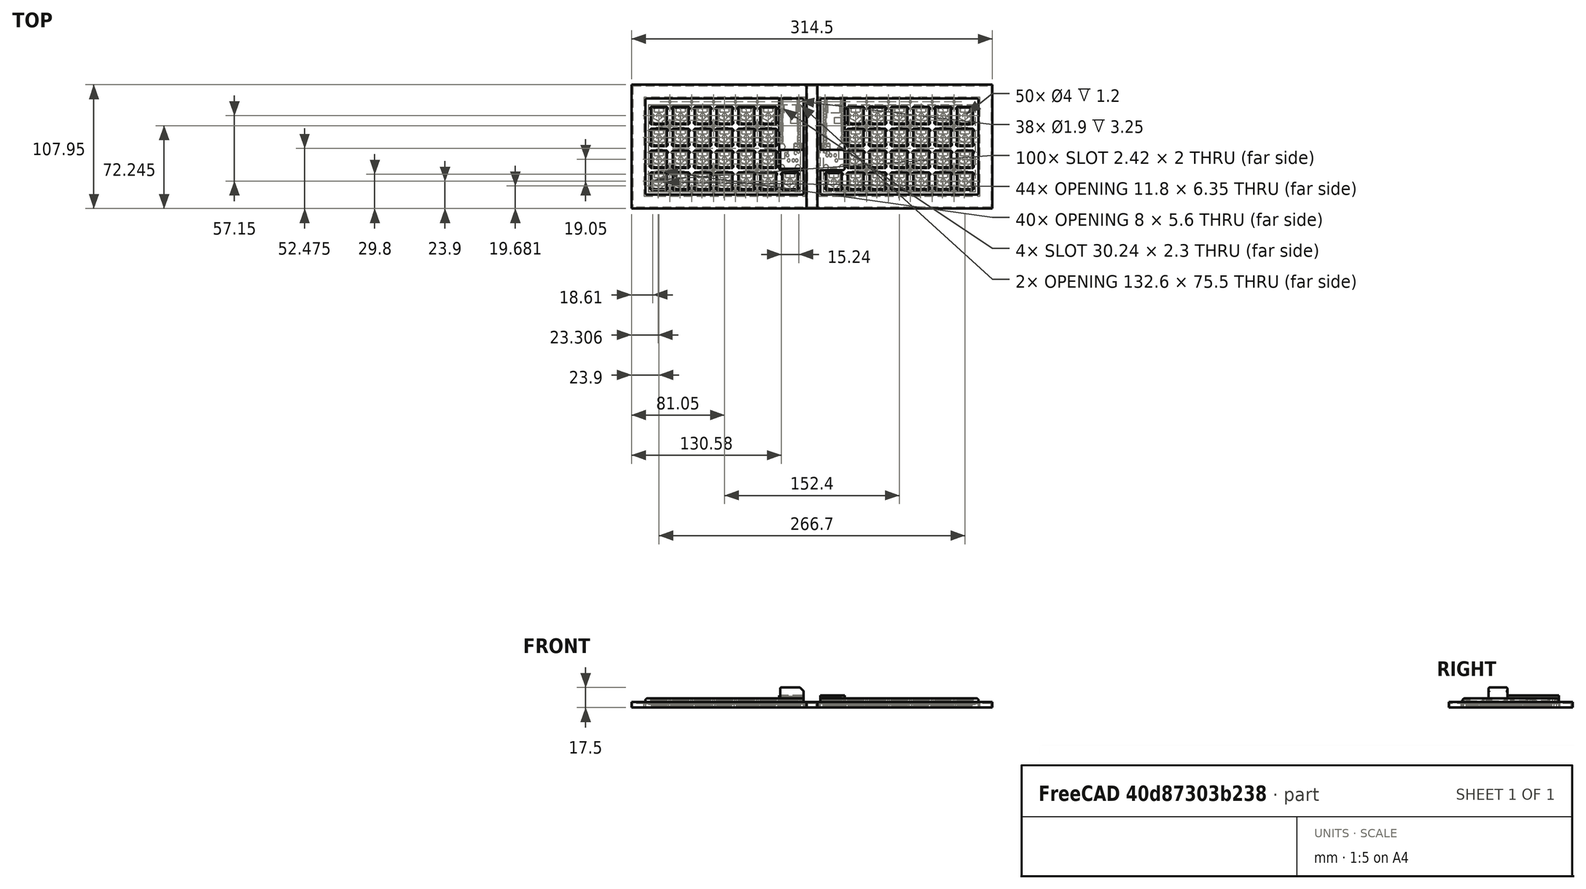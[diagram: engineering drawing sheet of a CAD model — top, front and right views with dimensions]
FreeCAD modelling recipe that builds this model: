
FCSTD DOCUMENT  (FreeCAD 1.0R39285 (Git))
Label: HelixCase
License: All rights reserved
LicenseURL: https://en.wikipedia.org/wiki/All_rights_reserved
objects: Sketcher::SketchObject×76, PartDesign::Pocket×59, PartDesign::Pad×17, PartDesign::Body×10, PartDesign::Fillet×7, Image::ImagePlane×5, PartDesign::ShapeBinder×2, PartDesign::Boolean×2, App::VarSet×1
note: 417 computed .brp shape members not serialized (recipe doc carries the construction recipe); baked Part::Feature solids carry a one-line shape summary decoded from their .brp

FEATURE [Sketcher::SketchObject] Sketch  label="TL-Lo"
  ArcFitTolerance = 1e-06
  AttachmentSupport = -> [XY_Plane]
  FullyConstrained = true
  MakeInternals = false
  MapMode = 5
  expr: Constraints[232] = VarSet.Top_LoXY
  expr: Constraints[233] = VarSet.Top_LoXY
  sketch-geometry (125):
    g0: LineSegment StartX=-45.4 StartY=11.75 StartZ=0 EndX=-30.8 EndY=11.75 EndZ=0
    g1: LineSegment StartX=-30.8 StartY=11.75 StartZ=0 EndX=-30.8 EndY=26.35 EndZ=0
    g2: LineSegment StartX=-30.8 StartY=26.35 StartZ=0 EndX=-45.4 EndY=26.35 EndZ=0
    g3: LineSegment StartX=-45.4 StartY=26.35 StartZ=0 EndX=-45.4 EndY=11.75 EndZ=0
    g4: GeomPoint [constr] X=-38.1 Y=19.05 Z=0
    g5: LineSegment StartX=-64.45 StartY=11.75 StartZ=0 EndX=-49.85 EndY=11.75 EndZ=0
    g6: LineSegment StartX=-49.85 StartY=11.75 StartZ=0 EndX=-49.85 EndY=26.35 EndZ=0
    g7: LineSegment StartX=-49.85 StartY=26.35 StartZ=0 EndX=-64.45 EndY=26.35 EndZ=0
    g8: LineSegment StartX=-64.45 StartY=26.35 StartZ=0 EndX=-64.45 EndY=11.75 EndZ=0
    g9: GeomPoint [constr] X=-57.15 Y=19.05 Z=0
    g10: LineSegment StartX=-83.5 StartY=11.75 StartZ=0 EndX=-68.9 EndY=11.75 EndZ=0
    g11: LineSegment StartX=-68.9 StartY=11.75 StartZ=0 EndX=-68.9 EndY=26.35 EndZ=0
    g12: LineSegment StartX=-68.9 StartY=26.35 StartZ=0 EndX=-83.5 EndY=26.35 EndZ=0
    g13: LineSegment StartX=-83.5 StartY=26.35 StartZ=0 EndX=-83.5 EndY=11.75 EndZ=0
    g14: GeomPoint [constr] X=-76.2 Y=19.05 Z=0
    g15: LineSegment StartX=-102.55 StartY=11.75 StartZ=0 EndX=-87.95 EndY=11.75 EndZ=0
    g16: LineSegment StartX=-87.95 StartY=11.75 StartZ=0 EndX=-87.95 EndY=26.35 EndZ=0
    g17: LineSegment StartX=-87.95 StartY=26.35 StartZ=0 EndX=-102.55 EndY=26.35 EndZ=0
    g18: LineSegment StartX=-102.55 StartY=26.35 StartZ=0 EndX=-102.55 EndY=11.75 EndZ=0
    g19: GeomPoint [constr] X=-95.25 Y=19.05 Z=0
    g20: LineSegment StartX=-121.6 StartY=11.75 StartZ=0 EndX=-107 EndY=11.75 EndZ=0
    g21: LineSegment StartX=-107 StartY=11.75 StartZ=0 EndX=-107 EndY=26.35 EndZ=0
    g22: LineSegment StartX=-107 StartY=26.35 StartZ=0 EndX=-121.6 EndY=26.35 EndZ=0
    g23: LineSegment StartX=-121.6 StartY=26.35 StartZ=0 EndX=-121.6 EndY=11.75 EndZ=0
    g24: GeomPoint [constr] X=-114.3 Y=19.05 Z=0
    g25: LineSegment StartX=-45.4 StartY=49.85 StartZ=0 EndX=-30.8 EndY=49.85 EndZ=0
    g26: LineSegment StartX=-30.8 StartY=49.85 StartZ=0 EndX=-30.8 EndY=64.45 EndZ=0
    g27: LineSegment StartX=-30.8 StartY=64.45 StartZ=0 EndX=-45.4 EndY=64.45 EndZ=0
    g28: LineSegment StartX=-45.4 StartY=64.45 StartZ=0 EndX=-45.4 EndY=49.85 EndZ=0
    g29: GeomPoint [constr] X=-38.1 Y=57.15 Z=0
    g30: LineSegment StartX=-64.45 StartY=49.85 StartZ=0 EndX=-49.85 EndY=49.85 EndZ=0
    g31: LineSegment StartX=-49.85 StartY=49.85 StartZ=0 EndX=-49.85 EndY=64.45 EndZ=0
    g32: LineSegment StartX=-49.85 StartY=64.45 StartZ=0 EndX=-64.45 EndY=64.45 EndZ=0
    g33: LineSegment StartX=-64.45 StartY=64.45 StartZ=0 EndX=-64.45 EndY=49.85 EndZ=0
    g34: GeomPoint [constr] X=-57.15 Y=57.15 Z=0
    g35: LineSegment StartX=-83.5 StartY=49.85 StartZ=0 EndX=-68.9 EndY=49.85 EndZ=0
    g36: LineSegment StartX=-68.9 StartY=49.85 StartZ=0 EndX=-68.9 EndY=64.45 EndZ=0
    g37: LineSegment StartX=-68.9 StartY=64.45 StartZ=0 EndX=-83.5 EndY=64.45 EndZ=0
    g38: LineSegment StartX=-83.5 StartY=64.45 StartZ=0 EndX=-83.5 EndY=49.85 EndZ=0
    g39: GeomPoint [constr] X=-76.2 Y=57.15 Z=0
    g40: LineSegment StartX=-102.55 StartY=49.85 StartZ=0 EndX=-87.95 EndY=49.85 EndZ=0
    g41: LineSegment StartX=-87.95 StartY=49.85 StartZ=0 EndX=-87.95 EndY=64.45 EndZ=0
    g42: LineSegment StartX=-87.95 StartY=64.45 StartZ=0 EndX=-102.55 EndY=64.45 EndZ=0
    g43: LineSegment StartX=-102.55 StartY=64.45 StartZ=0 EndX=-102.55 EndY=49.85 EndZ=0
    g44: GeomPoint [constr] X=-95.25 Y=57.15 Z=0
    g45: LineSegment StartX=-121.6 StartY=49.85 StartZ=0 EndX=-107 EndY=49.85 EndZ=0
    g46: LineSegment StartX=-107 StartY=49.85 StartZ=0 EndX=-107 EndY=64.45 EndZ=0
    g47: LineSegment StartX=-107 StartY=64.45 StartZ=0 EndX=-121.6 EndY=64.45 EndZ=0
    g48: LineSegment StartX=-121.6 StartY=64.45 StartZ=0 EndX=-121.6 EndY=49.85 EndZ=0
    g49: GeomPoint [constr] X=-114.3 Y=57.15 Z=0
    g50: LineSegment StartX=-45.4 StartY=30.8 StartZ=0 EndX=-30.8 EndY=30.8 EndZ=0
    g51: LineSegment StartX=-30.8 StartY=30.8 StartZ=0 EndX=-30.8 EndY=45.4 EndZ=0
    g52: LineSegment StartX=-30.8 StartY=45.4 StartZ=0 EndX=-45.4 EndY=45.4 EndZ=0
    g53: LineSegment StartX=-45.4 StartY=45.4 StartZ=0 EndX=-45.4 EndY=30.8 EndZ=0
    g54: GeomPoint [constr] X=-38.1 Y=38.1 Z=0
    g55: LineSegment StartX=-64.45 StartY=30.8 StartZ=0 EndX=-49.85 EndY=30.8 EndZ=0
    g56: LineSegment StartX=-49.85 StartY=30.8 StartZ=0 EndX=-49.85 EndY=45.4 EndZ=0
    g57: LineSegment StartX=-49.85 StartY=45.4 StartZ=0 EndX=-64.45 EndY=45.4 EndZ=0
    g58: LineSegment StartX=-64.45 StartY=45.4 StartZ=0 EndX=-64.45 EndY=30.8 EndZ=0
    g59: GeomPoint [constr] X=-57.15 Y=38.1 Z=0
    g60: LineSegment StartX=-83.5 StartY=30.8 StartZ=0 EndX=-68.9 EndY=30.8 EndZ=0
    g61: LineSegment StartX=-68.9 StartY=30.8 StartZ=0 EndX=-68.9 EndY=45.4 EndZ=0
    g62: LineSegment StartX=-68.9 StartY=45.4 StartZ=0 EndX=-83.5 EndY=45.4 EndZ=0
    g63: LineSegment StartX=-83.5 StartY=45.4 StartZ=0 EndX=-83.5 EndY=30.8 EndZ=0
    g64: GeomPoint [constr] X=-76.2 Y=38.1 Z=0
    g65: LineSegment StartX=-102.55 StartY=30.8 StartZ=0 EndX=-87.95 EndY=30.8 EndZ=0
    g66: LineSegment StartX=-87.95 StartY=30.8 StartZ=0 EndX=-87.95 EndY=45.4 EndZ=0
    g67: LineSegment StartX=-87.95 StartY=45.4 StartZ=0 EndX=-102.55 EndY=45.4 EndZ=0
    g68: LineSegment StartX=-102.55 StartY=45.4 StartZ=0 EndX=-102.55 EndY=30.8 EndZ=0
    g69: GeomPoint [constr] X=-95.25 Y=38.1 Z=0
    g70: LineSegment StartX=-121.6 StartY=30.8 StartZ=0 EndX=-107 EndY=30.8 EndZ=0
    g71: LineSegment StartX=-107 StartY=30.8 StartZ=0 EndX=-107 EndY=45.4 EndZ=0
    g72: LineSegment StartX=-107 StartY=45.4 StartZ=0 EndX=-121.6 EndY=45.4 EndZ=0
    g73: LineSegment StartX=-121.6 StartY=45.4 StartZ=0 EndX=-121.6 EndY=30.8 EndZ=0
    g74: GeomPoint [constr] X=-114.3 Y=38.1 Z=0
    g75: LineSegment StartX=-102.55 StartY=68.9 StartZ=0 EndX=-87.95 EndY=68.9 EndZ=0
    g76: LineSegment StartX=-87.95 StartY=68.9 StartZ=0 EndX=-87.95 EndY=83.5 EndZ=0
    g77: LineSegment StartX=-87.95 StartY=83.5 StartZ=0 EndX=-102.55 EndY=83.5 EndZ=0
    g78: LineSegment StartX=-102.55 StartY=83.5 StartZ=0 EndX=-102.55 EndY=68.9 EndZ=0
    g79: GeomPoint [constr] X=-95.25 Y=76.2 Z=0
    g80: LineSegment StartX=-64.45 StartY=68.9 StartZ=0 EndX=-49.85 EndY=68.9 EndZ=0
    g81: LineSegment StartX=-49.85 StartY=68.9 StartZ=0 EndX=-49.85 EndY=83.5 EndZ=0
    g82: LineSegment StartX=-49.85 StartY=83.5 StartZ=0 EndX=-64.45 EndY=83.5 EndZ=0
    g83: LineSegment StartX=-64.45 StartY=83.5 StartZ=0 EndX=-64.45 EndY=68.9 EndZ=0
    g84: GeomPoint [constr] X=-57.15 Y=76.2 Z=0
    g85: LineSegment StartX=-140.65 StartY=68.9 StartZ=0 EndX=-126.05 EndY=68.9 EndZ=0
    g86: LineSegment StartX=-126.05 StartY=68.9 StartZ=0 EndX=-126.05 EndY=83.5 EndZ=0
    g87: LineSegment StartX=-126.05 StartY=83.5 StartZ=0 EndX=-140.65 EndY=83.5 EndZ=0
    g88: LineSegment StartX=-140.65 StartY=83.5 StartZ=0 EndX=-140.65 EndY=68.9 EndZ=0
    g89: GeomPoint [constr] X=-133.35 Y=76.2 Z=0
    g90: LineSegment StartX=-121.6 StartY=68.9 StartZ=0 EndX=-107 EndY=68.9 EndZ=0
    g91: LineSegment StartX=-107 StartY=68.9 StartZ=0 EndX=-107 EndY=83.5 EndZ=0
    g92: LineSegment StartX=-107 StartY=83.5 StartZ=0 EndX=-121.6 EndY=83.5 EndZ=0
    g93: LineSegment StartX=-121.6 StartY=83.5 StartZ=0 EndX=-121.6 EndY=68.9 EndZ=0
    g94: GeomPoint [constr] X=-114.3 Y=76.2 Z=0
    g95: LineSegment StartX=-83.5 StartY=68.9 StartZ=0 EndX=-68.9 EndY=68.9 EndZ=0
    g96: LineSegment StartX=-68.9 StartY=68.9 StartZ=0 EndX=-68.9 EndY=83.5 EndZ=0
    g97: LineSegment StartX=-68.9 StartY=83.5 StartZ=0 EndX=-83.5 EndY=83.5 EndZ=0
    g98: LineSegment StartX=-83.5 StartY=83.5 StartZ=0 EndX=-83.5 EndY=68.9 EndZ=0
    g99: GeomPoint [constr] X=-76.2 Y=76.2 Z=0
    g100: LineSegment StartX=-30.8 StartY=83.5 StartZ=0 EndX=-45.4 EndY=83.5 EndZ=0
    g101: LineSegment StartX=-45.4 StartY=83.5 StartZ=0 EndX=-45.4 EndY=68.9 EndZ=0
    g102: LineSegment StartX=-45.4 StartY=68.9 StartZ=0 EndX=-30.8 EndY=68.9 EndZ=0
    g103: LineSegment StartX=-30.8 StartY=68.9 StartZ=0 EndX=-30.8 EndY=83.5 EndZ=0
    g104: GeomPoint [constr] X=-38.1 Y=76.2 Z=0
    g105: LineSegment StartX=-126.05 StartY=64.45 StartZ=0 EndX=-140.65 EndY=64.45 EndZ=0
    g106: LineSegment StartX=-140.65 StartY=64.45 StartZ=0 EndX=-140.65 EndY=49.85 EndZ=0
    g107: LineSegment StartX=-140.65 StartY=49.85 StartZ=0 EndX=-126.05 EndY=49.85 EndZ=0
    g108: LineSegment StartX=-126.05 StartY=49.85 StartZ=0 EndX=-126.05 EndY=64.45 EndZ=0
    g109: GeomPoint [constr] X=-133.35 Y=57.15 Z=0
    g110: LineSegment StartX=-126.05 StartY=45.4 StartZ=0 EndX=-140.65 EndY=45.4 EndZ=0
    g111: LineSegment StartX=-140.65 StartY=45.4 StartZ=0 EndX=-140.65 EndY=30.8 EndZ=0
    g112: LineSegment StartX=-140.65 StartY=30.8 StartZ=0 EndX=-126.05 EndY=30.8 EndZ=0
    g113: LineSegment StartX=-126.05 StartY=30.8 StartZ=0 EndX=-126.05 EndY=45.4 EndZ=0
    g114: GeomPoint [constr] X=-133.35 Y=38.1 Z=0
    g115: LineSegment StartX=-126.05 StartY=26.35 StartZ=0 EndX=-140.65 EndY=26.35 EndZ=0
    g116: LineSegment StartX=-140.65 StartY=26.35 StartZ=0 EndX=-140.65 EndY=11.75 EndZ=0
    g117: LineSegment StartX=-140.65 StartY=11.75 StartZ=0 EndX=-126.05 EndY=11.75 EndZ=0
    g118: LineSegment StartX=-126.05 StartY=11.75 StartZ=0 EndX=-126.05 EndY=26.35 EndZ=0
    g119: GeomPoint [constr] X=-133.35 Y=19.05 Z=0
    g120: LineSegment StartX=-11.75 StartY=26.35 StartZ=0 EndX=-26.35 EndY=26.35 EndZ=0
    g121: LineSegment StartX=-26.35 StartY=26.35 StartZ=0 EndX=-26.35 EndY=11.75 EndZ=0
    g122: LineSegment StartX=-26.35 StartY=11.75 StartZ=0 EndX=-11.75 EndY=11.75 EndZ=0
    g123: LineSegment StartX=-11.75 StartY=11.75 StartZ=0 EndX=-11.75 EndY=26.35 EndZ=0
    g124: GeomPoint [constr] X=-19.05 Y=19.05 Z=0
  constraints (325):
    c: Coincident(g0,g1)
    c: Coincident(g1,g2)
    c: Coincident(g2,g3)
    c: Coincident(g3,g0)
    c: Horizontal(g0)
    c: Horizontal(g2)
    c: Vertical(g1)
    c: Vertical(g3)
    c: Symmetric(g2,g0,g4)
    c: Coincident(g5,g6)
    c: Coincident(g6,g7)
    c: Coincident(g7,g8)
    c: Coincident(g8,g5)
    c: Horizontal(g5)
    c: Horizontal(g7)
    c: Vertical(g6)
    c: Vertical(g8)
    c: Symmetric(g7,g5,g9)
    c: DistanceX(g9,g4) = 19.05
    c: Coincident(g10,g11)
    c: Coincident(g11,g12)
    c: Coincident(g12,g13)
    c: Coincident(g13,g10)
    c: Horizontal(g10)
    c: Horizontal(g12)
    c: Vertical(g11)
    c: Vertical(g13)
    c: Symmetric(g12,g10,g14)
    c: DistanceX(g14,g9) = 19.05
    c: Coincident(g15,g16)
    c: Coincident(g16,g17)
    c: Coincident(g17,g18)
    c: Coincident(g18,g15)
    c: Horizontal(g15)
    c: Horizontal(g17)
    c: Vertical(g16)
    c: Vertical(g18)
    c: Symmetric(g17,g15,g19)
    c: Coincident(g20,g21)
    c: Coincident(g21,g22)
    c: Coincident(g22,g23)
    c: Coincident(g23,g20)
    c: Horizontal(g20)
    c: Horizontal(g22)
    c: Vertical(g21)
    c: Vertical(g23)
    c: Symmetric(g22,g20,g24)
    c: DistanceX(g19,g14) = 19.05
    c: DistanceX(g24,g19) = 19.05
    c: Coincident(g25,g26)
    c: Coincident(g26,g27)
    c: Coincident(g27,g28)
    c: Coincident(g28,g25)
    c: Horizontal(g25)
    c: Horizontal(g27)
    c: Vertical(g26)
    c: Vertical(g28)
    c: Symmetric(g27,g25,g29)
    c: Coincident(g30,g31)
    c: Coincident(g31,g32)
    c: Coincident(g32,g33)
    c: Coincident(g33,g30)
    c: Horizontal(g30)
    c: Horizontal(g32)
    c: Vertical(g31)
    c: Vertical(g33)
    c: Symmetric(g32,g30,g34)
    c: Coincident(g35,g36)
    c: Coincident(g36,g37)
    c: Coincident(g37,g38)
    c: Coincident(g38,g35)
    c: Horizontal(g35)
    c: Horizontal(g37)
    c: Vertical(g36)
    c: Vertical(g38)
    c: Symmetric(g37,g35,g39)
    c: Coincident(g40,g41)
    c: Coincident(g41,g42)
    c: Coincident(g42,g43)
    c: Coincident(g43,g40)
    c: Horizontal(g40)
    c: Horizontal(g42)
    c: Vertical(g41)
    c: Vertical(g43)
    c: Symmetric(g42,g40,g44)
    c: Coincident(g45,g46)
    c: Coincident(g46,g47)
    c: Coincident(g47,g48)
    c: Coincident(g48,g45)
    c: Horizontal(g45)
    c: Horizontal(g47)
    c: Vertical(g46)
    c: Vertical(g48)
    c: Symmetric(g47,g45,g49)
    c: Coincident(g50,g51)
    c: Coincident(g51,g52)
    c: Coincident(g52,g53)
    c: Coincident(g53,g50)
    c: Horizontal(g50)
    c: Horizontal(g52)
    c: Vertical(g51)
    c: Vertical(g53)
    c: Symmetric(g52,g50,g54)
    c: Coincident(g55,g56)
    c: Coincident(g56,g57)
    c: Coincident(g57,g58)
    c: Coincident(g58,g55)
    c: Horizontal(g55)
    c: Horizontal(g57)
    c: Vertical(g56)
    c: Vertical(g58)
    c: Symmetric(g57,g55,g59)
    c: Coincident(g60,g61)
    c: Coincident(g61,g62)
    c: Coincident(g62,g63)
    c: Coincident(g63,g60)
    c: Horizontal(g60)
    c: Horizontal(g62)
    c: Vertical(g61)
    c: Vertical(g63)
    c: Symmetric(g62,g60,g64)
    c: Coincident(g65,g66)
    c: Coincident(g66,g67)
    c: Coincident(g67,g68)
    c: Coincident(g68,g65)
    c: Horizontal(g65)
    c: Horizontal(g67)
    c: Vertical(g66)
    c: Vertical(g68)
    c: Symmetric(g67,g65,g69)
    c: Coincident(g70,g71)
    c: Coincident(g71,g72)
    c: Coincident(g72,g73)
    c: Coincident(g73,g70)
    c: Horizontal(g70)
    c: Horizontal(g72)
    c: Vertical(g71)
    c: Vertical(g73)
    c: Symmetric(g72,g70,g74)
    c: DistanceY(g54,g29) = 19.05
    c: Coincident(g75,g76)
    c: Coincident(g76,g77)
    c: Coincident(g77,g78)
    c: Coincident(g78,g75)
    c: Horizontal(g75)
    c: Horizontal(g77)
    c: Vertical(g76)
    c: Vertical(g78)
    c: Symmetric(g77,g75,g79)
    c: Coincident(g80,g81)
    c: Coincident(g81,g82)
    c: Coincident(g82,g83)
    c: Coincident(g83,g80)
    c: Horizontal(g80)
    c: Horizontal(g82)
    c: Vertical(g81)
    c: Vertical(g83)
    c: Symmetric(g82,g80,g84)
    c: Coincident(g85,g86)
    c: Coincident(g86,g87)
    c: Coincident(g87,g88)
    c: Coincident(g88,g85)
    c: Horizontal(g85)
    c: Horizontal(g87)
    c: Vertical(g86)
    c: Vertical(g88)
    c: Symmetric(g87,g85,g89)
    c: Coincident(g90,g91)
    c: Coincident(g91,g92)
    c: Coincident(g92,g93)
    c: Coincident(g93,g90)
    c: Horizontal(g90)
    c: Horizontal(g92)
    c: Vertical(g91)
    c: Vertical(g93)
    c: Symmetric(g92,g90,g94)
    c: Coincident(g95,g96)
    c: Coincident(g96,g97)
    c: Coincident(g97,g98)
    c: Coincident(g98,g95)
    c: Horizontal(g95)
    c: Horizontal(g97)
    c: Vertical(g96)
    c: Vertical(g98)
    c: Symmetric(g97,g95,g99)
    c: Coincident(g100,g101)
    c: Coincident(g101,g102)
    c: Coincident(g102,g103)
    c: Coincident(g103,g100)
    c: Horizontal(g100)
    c: Horizontal(g102)
    c: Vertical(g101)
    c: Vertical(g103)
    c: Symmetric(g102,g100,g104)
    c: Coincident(g105,g106)
    c: Coincident(g106,g107)
    c: Coincident(g107,g108)
    c: Coincident(g108,g105)
    c: Horizontal(g105)
    c: Horizontal(g107)
    c: Vertical(g106)
    c: Vertical(g108)
    c: Symmetric(g107,g105,g109)
    c: Coincident(g110,g111)
    c: Coincident(g111,g112)
    c: Coincident(g112,g113)
    c: Coincident(g113,g110)
    c: Horizontal(g110)
    c: Horizontal(g112)
    c: Vertical(g111)
    c: Vertical(g113)
    c: Symmetric(g112,g110,g114)
    c: Coincident(g115,g116)
    c: Coincident(g116,g117)
    c: Coincident(g117,g118)
    c: Coincident(g118,g115)
    c: Horizontal(g115)
    c: Horizontal(g117)
    c: Vertical(g118)
    c: Symmetric(g117,g115,g119)
    c: DistanceY(g29,g104) = 19.05
    c: DistanceX(g119,g24) = 19.05
    c: Coincident(g120,g121)
    c: Coincident(g121,g122)
    c: Coincident(g122,g123)
    c: Coincident(g123,g120)
    c: Horizontal(g120)
    c: Horizontal(g122)
    c: Vertical(g121)
    c: Vertical(g123)
    c: Symmetric(g122,g120,g124)
    c: DistanceX(g4,g124) = 19.05
    c: DistanceX(g122,g122) = 14.6
    c: DistanceY(g121,g121) = 14.6
    c: Horizontal(g89,g94)
    c: Horizontal(g94,g79)
    c: Horizontal(g79,g99)
    c: Horizontal(g99,g84)
    c: Horizontal(g84,g104)
    c: Horizontal(g109,g49)
    c: Horizontal(g49,g44)
    c: Horizontal(g44,g39)
    c: Horizontal(g39,g34)
    c: Horizontal(g34,g29)
    c: Horizontal(g114,g74)
    c: Horizontal(g74,g69)
    c: Horizontal(g69,g64)
    c: Horizontal(g64,g59)
    c: Horizontal(g59,g54)
    c: Vertical(g89,g109)
    c: Vertical(g109,g114)
    c: Vertical(g114,g119)
    c: Vertical(g94,g49)
    c: Vertical(g49,g74)
    c: Vertical(g74,g24)
    c: Vertical(g79,g44)
    c: Vertical(g44,g69)
    c: Vertical(g69,g19)
    c: Vertical(g99,g39)
    c: Vertical(g39,g64)
    c: Vertical(g64,g14)
    c: Vertical(g84,g34)
    c: Vertical(g34,g59)
    c: Vertical(g59,g9)
    c: Vertical(g104,g29)
    c: Vertical(g29,g54)
    c: Vertical(g54,g4)
    c: DistanceX(g124,g-1) = 19.05
    c: Horizontal(g119,g24)
    c: Horizontal(g24,g19)
    c: Horizontal(g19,g14)
    c: Horizontal(g14,g9)
    c: Horizontal(g9,g4)
    c: Horizontal(g4,g124)
    c: DistanceY(g-1,g124) = 19.05
    c: DistanceY(g124,g54) = 19.05
    c: Equal(g88,g93)
    c: Equal(g93,g78)
    c: Equal(g78,g98)
    c: Equal(g98,g83)
    c: Equal(g83,g101)
    c: Equal(g101,g121)
    c: Equal(g106,g48)
    c: Equal(g48,g43)
    c: Equal(g43,g38)
    c: Equal(g38,g33)
    c: Equal(g33,g28)
    c: Equal(g28,g121)
    c: Equal(g111,g73)
    c: Equal(g73,g68)
    c: Equal(g68,g63)
    c: Equal(g63,g58)
    c: Equal(g58,g53)
    c: Equal(g53,g121)
    c: Equal(g116,g23)
    c: Equal(g23,g18)
    c: Equal(g18,g13)
    c: Equal(g13,g8)
    c: Equal(g8,g3)
    c: Equal(g3,g121)
    c: Equal(g85,g90)
    c: Equal(g90,g75)
    c: Equal(g75,g95)
    c: Equal(g95,g80)
    c: Equal(g80,g102)
    c: Equal(g102,g122)
    c: Equal(g107,g45)
    c: Equal(g45,g40)
    c: Equal(g40,g35)
    c: Equal(g35,g30)
    c: Equal(g30,g25)
    c: Equal(g25,g122)
    c: Equal(g112,g70)
    c: Equal(g70,g65)
    c: Equal(g65,g60)
    c: Equal(g60,g55)
    c: Equal(g55,g50)
    c: Equal(g50,g122)
    c: Equal(g117,g20)
    c: Equal(g20,g15)
    c: Equal(g15,g10)
    c: Equal(g10,g5)
    c: Vertical(g116)
    c: Equal(g5,g0)
    c: Equal(g0,g122)
FEATURE [App::VarSet] VarSet
  Bottom_ConnectorZ = 1.7
  Bottom_ContactD = 3
  Bottom_ContactTaper = 0
  Bottom_ContactZ = 1.5
  Bottom_DiodeLedGapMerge = true
  Bottom_DiodeX = 5.7
  Bottom_DiodeY = 2
  Bottom_DiodeZ = 1.5
  Bottom_FilletR = 0.1
  Bottom_LedX = 8
  Bottom_LedY = 3.2
  Bottom_LedZ = 1.2
  Bottom_McuContactD = 2.3
  Bottom_McuContactTaper = 0
  Bottom_McuZ = 1.3
  Bottom_PlateZ = 3
  Bottom_ResistorZ = 0.9
  Bottom_StemTaper = 0
  Bottom_StemZ = 1.2
  Bottom_UnderLedR = 1.2
  Bottom_UnderLedX = 5.6
  Bottom_UnderLedY = 7.5
  Bottom_UnderLedZ = 1.8
  Cover_FrontAdd = 1.2
  Cover_InZ = 4.75
  Cover_McuContactZ = 1.25
  Cover_McuRearAdd = 0.5
  Cover_OutZ = 6.75
  Cover_ResetHoleDepth = 1.5
  Cover_ResetHoleHeightH = 4.4
  Cover_ResetHoleHeightL = 3
  Cover_ResetHoleWidth = 4
  Cover_SlantZ = 6.75
  Mold_MoatD = 10
  Mold_WallD = 1
  Screw_ClearanceD = 2.15
  Screw_PostInD = 1.9
  Screw_PostOutD = 3.5
  Screw_RearAdd = 2.5
  Screw_RecessD = 3.9
  Screw_RecessZ = 1.5
  Top_FilletR = 2
  Top_Frame = 5
  Top_FrameFilletR = 2
  Top_FrameSmall = 2.5
  Top_HiSwFilletR = 1
  Top_HiXY = 15.1
  Top_HiZ = 1
  Top_LoXY = 14.6
  Top_LoZ = 1.3
  Top_MedXY = 13.8
  Top_MedZ = 1.2
  Top_PcbX = 132.6
  Top_PcbY = 75.5
  Top_PcbZ = 1.5
  Top_RearAdd = 3
FEATURE [Sketcher::SketchObject] Sketch001  label="TL-Med"
  ArcFitTolerance = 1e-06
  AttachmentSupport = -> [XY_Plane]
  FullyConstrained = true
  MakeInternals = false
  MapMode = 5
  expr: Constraints[232] = VarSet.Top_MedXY
  expr: Constraints[233] = VarSet.Top_MedXY
  sketch-geometry (125):
    g0: LineSegment StartX=-45 StartY=12.15 StartZ=0 EndX=-31.2 EndY=12.15 EndZ=0
    g1: LineSegment StartX=-31.2 StartY=12.15 StartZ=0 EndX=-31.2 EndY=25.95 EndZ=0
    g2: LineSegment StartX=-31.2 StartY=25.95 StartZ=0 EndX=-45 EndY=25.95 EndZ=0
    g3: LineSegment StartX=-45 StartY=25.95 StartZ=0 EndX=-45 EndY=12.15 EndZ=0
    g4: GeomPoint [constr] X=-38.1 Y=19.05 Z=0
    g5: LineSegment StartX=-64.05 StartY=12.15 StartZ=0 EndX=-50.25 EndY=12.15 EndZ=0
    g6: LineSegment StartX=-50.25 StartY=12.15 StartZ=0 EndX=-50.25 EndY=25.95 EndZ=0
    g7: LineSegment StartX=-50.25 StartY=25.95 StartZ=0 EndX=-64.05 EndY=25.95 EndZ=0
    g8: LineSegment StartX=-64.05 StartY=25.95 StartZ=0 EndX=-64.05 EndY=12.15 EndZ=0
    g9: GeomPoint [constr] X=-57.15 Y=19.05 Z=0
    g10: LineSegment StartX=-83.1 StartY=12.15 StartZ=0 EndX=-69.3 EndY=12.15 EndZ=0
    g11: LineSegment StartX=-69.3 StartY=12.15 StartZ=0 EndX=-69.3 EndY=25.95 EndZ=0
    g12: LineSegment StartX=-69.3 StartY=25.95 StartZ=0 EndX=-83.1 EndY=25.95 EndZ=0
    g13: LineSegment StartX=-83.1 StartY=25.95 StartZ=0 EndX=-83.1 EndY=12.15 EndZ=0
    g14: GeomPoint [constr] X=-76.2 Y=19.05 Z=0
    g15: LineSegment StartX=-102.15 StartY=12.15 StartZ=0 EndX=-88.35 EndY=12.15 EndZ=0
    g16: LineSegment StartX=-88.35 StartY=12.15 StartZ=0 EndX=-88.35 EndY=25.95 EndZ=0
    g17: LineSegment StartX=-88.35 StartY=25.95 StartZ=0 EndX=-102.15 EndY=25.95 EndZ=0
    g18: LineSegment StartX=-102.15 StartY=25.95 StartZ=0 EndX=-102.15 EndY=12.15 EndZ=0
    g19: GeomPoint [constr] X=-95.25 Y=19.05 Z=0
    g20: LineSegment StartX=-121.2 StartY=12.15 StartZ=0 EndX=-107.4 EndY=12.15 EndZ=0
    g21: LineSegment StartX=-107.4 StartY=12.15 StartZ=0 EndX=-107.4 EndY=25.95 EndZ=0
    g22: LineSegment StartX=-107.4 StartY=25.95 StartZ=0 EndX=-121.2 EndY=25.95 EndZ=0
    g23: LineSegment StartX=-121.2 StartY=25.95 StartZ=0 EndX=-121.2 EndY=12.15 EndZ=0
    g24: GeomPoint [constr] X=-114.3 Y=19.05 Z=0
    g25: LineSegment StartX=-45 StartY=50.25 StartZ=0 EndX=-31.2 EndY=50.25 EndZ=0
    g26: LineSegment StartX=-31.2 StartY=50.25 StartZ=0 EndX=-31.2 EndY=64.05 EndZ=0
    g27: LineSegment StartX=-31.2 StartY=64.05 StartZ=0 EndX=-45 EndY=64.05 EndZ=0
    g28: LineSegment StartX=-45 StartY=64.05 StartZ=0 EndX=-45 EndY=50.25 EndZ=0
    g29: GeomPoint [constr] X=-38.1 Y=57.15 Z=0
    g30: LineSegment StartX=-64.05 StartY=50.25 StartZ=0 EndX=-50.25 EndY=50.25 EndZ=0
    g31: LineSegment StartX=-50.25 StartY=50.25 StartZ=0 EndX=-50.25 EndY=64.05 EndZ=0
    g32: LineSegment StartX=-50.25 StartY=64.05 StartZ=0 EndX=-64.05 EndY=64.05 EndZ=0
    g33: LineSegment StartX=-64.05 StartY=64.05 StartZ=0 EndX=-64.05 EndY=50.25 EndZ=0
    g34: GeomPoint [constr] X=-57.15 Y=57.15 Z=0
    g35: LineSegment StartX=-83.1 StartY=50.25 StartZ=0 EndX=-69.3 EndY=50.25 EndZ=0
    g36: LineSegment StartX=-69.3 StartY=50.25 StartZ=0 EndX=-69.3 EndY=64.05 EndZ=0
    g37: LineSegment StartX=-69.3 StartY=64.05 StartZ=0 EndX=-83.1 EndY=64.05 EndZ=0
    g38: LineSegment StartX=-83.1 StartY=64.05 StartZ=0 EndX=-83.1 EndY=50.25 EndZ=0
    g39: GeomPoint [constr] X=-76.2 Y=57.15 Z=0
    g40: LineSegment StartX=-102.15 StartY=50.25 StartZ=0 EndX=-88.35 EndY=50.25 EndZ=0
    g41: LineSegment StartX=-88.35 StartY=50.25 StartZ=0 EndX=-88.35 EndY=64.05 EndZ=0
    g42: LineSegment StartX=-88.35 StartY=64.05 StartZ=0 EndX=-102.15 EndY=64.05 EndZ=0
    g43: LineSegment StartX=-102.15 StartY=64.05 StartZ=0 EndX=-102.15 EndY=50.25 EndZ=0
    g44: GeomPoint [constr] X=-95.25 Y=57.15 Z=0
    g45: LineSegment StartX=-121.2 StartY=50.25 StartZ=0 EndX=-107.4 EndY=50.25 EndZ=0
    g46: LineSegment StartX=-107.4 StartY=50.25 StartZ=0 EndX=-107.4 EndY=64.05 EndZ=0
    g47: LineSegment StartX=-107.4 StartY=64.05 StartZ=0 EndX=-121.2 EndY=64.05 EndZ=0
    g48: LineSegment StartX=-121.2 StartY=64.05 StartZ=0 EndX=-121.2 EndY=50.25 EndZ=0
    g49: GeomPoint [constr] X=-114.3 Y=57.15 Z=0
    g50: LineSegment StartX=-45 StartY=31.2 StartZ=0 EndX=-31.2 EndY=31.2 EndZ=0
    g51: LineSegment StartX=-31.2 StartY=31.2 StartZ=0 EndX=-31.2 EndY=45 EndZ=0
    g52: LineSegment StartX=-31.2 StartY=45 StartZ=0 EndX=-45 EndY=45 EndZ=0
    g53: LineSegment StartX=-45 StartY=45 StartZ=0 EndX=-45 EndY=31.2 EndZ=0
    g54: GeomPoint [constr] X=-38.1 Y=38.1 Z=0
    g55: LineSegment StartX=-64.05 StartY=31.2 StartZ=0 EndX=-50.25 EndY=31.2 EndZ=0
    g56: LineSegment StartX=-50.25 StartY=31.2 StartZ=0 EndX=-50.25 EndY=45 EndZ=0
    g57: LineSegment StartX=-50.25 StartY=45 StartZ=0 EndX=-64.05 EndY=45 EndZ=0
    g58: LineSegment StartX=-64.05 StartY=45 StartZ=0 EndX=-64.05 EndY=31.2 EndZ=0
    g59: GeomPoint [constr] X=-57.15 Y=38.1 Z=0
    g60: LineSegment StartX=-83.1 StartY=31.2 StartZ=0 EndX=-69.3 EndY=31.2 EndZ=0
    g61: LineSegment StartX=-69.3 StartY=31.2 StartZ=0 EndX=-69.3 EndY=45 EndZ=0
    g62: LineSegment StartX=-69.3 StartY=45 StartZ=0 EndX=-83.1 EndY=45 EndZ=0
    g63: LineSegment StartX=-83.1 StartY=45 StartZ=0 EndX=-83.1 EndY=31.2 EndZ=0
    g64: GeomPoint [constr] X=-76.2 Y=38.1 Z=0
    g65: LineSegment StartX=-102.15 StartY=31.2 StartZ=0 EndX=-88.35 EndY=31.2 EndZ=0
    g66: LineSegment StartX=-88.35 StartY=31.2 StartZ=0 EndX=-88.35 EndY=45 EndZ=0
    g67: LineSegment StartX=-88.35 StartY=45 StartZ=0 EndX=-102.15 EndY=45 EndZ=0
    g68: LineSegment StartX=-102.15 StartY=45 StartZ=0 EndX=-102.15 EndY=31.2 EndZ=0
    g69: GeomPoint [constr] X=-95.25 Y=38.1 Z=0
    g70: LineSegment StartX=-121.2 StartY=31.2 StartZ=0 EndX=-107.4 EndY=31.2 EndZ=0
    g71: LineSegment StartX=-107.4 StartY=31.2 StartZ=0 EndX=-107.4 EndY=45 EndZ=0
    g72: LineSegment StartX=-107.4 StartY=45 StartZ=0 EndX=-121.2 EndY=45 EndZ=0
    g73: LineSegment StartX=-121.2 StartY=45 StartZ=0 EndX=-121.2 EndY=31.2 EndZ=0
    g74: GeomPoint [constr] X=-114.3 Y=38.1 Z=0
    g75: LineSegment StartX=-102.15 StartY=69.3 StartZ=0 EndX=-88.35 EndY=69.3 EndZ=0
    g76: LineSegment StartX=-88.35 StartY=69.3 StartZ=0 EndX=-88.35 EndY=83.1 EndZ=0
    g77: LineSegment StartX=-88.35 StartY=83.1 StartZ=0 EndX=-102.15 EndY=83.1 EndZ=0
    g78: LineSegment StartX=-102.15 StartY=83.1 StartZ=0 EndX=-102.15 EndY=69.3 EndZ=0
    g79: GeomPoint [constr] X=-95.25 Y=76.2 Z=0
    g80: LineSegment StartX=-64.05 StartY=69.3 StartZ=0 EndX=-50.25 EndY=69.3 EndZ=0
    g81: LineSegment StartX=-50.25 StartY=69.3 StartZ=0 EndX=-50.25 EndY=83.1 EndZ=0
    g82: LineSegment StartX=-50.25 StartY=83.1 StartZ=0 EndX=-64.05 EndY=83.1 EndZ=0
    g83: LineSegment StartX=-64.05 StartY=83.1 StartZ=0 EndX=-64.05 EndY=69.3 EndZ=0
    g84: GeomPoint [constr] X=-57.15 Y=76.2 Z=0
    g85: LineSegment StartX=-140.25 StartY=69.3 StartZ=0 EndX=-126.45 EndY=69.3 EndZ=0
    g86: LineSegment StartX=-126.45 StartY=69.3 StartZ=0 EndX=-126.45 EndY=83.1 EndZ=0
    g87: LineSegment StartX=-126.45 StartY=83.1 StartZ=0 EndX=-140.25 EndY=83.1 EndZ=0
    g88: LineSegment StartX=-140.25 StartY=83.1 StartZ=0 EndX=-140.25 EndY=69.3 EndZ=0
    g89: GeomPoint [constr] X=-133.35 Y=76.2 Z=0
    g90: LineSegment StartX=-121.2 StartY=69.3 StartZ=0 EndX=-107.4 EndY=69.3 EndZ=0
    g91: LineSegment StartX=-107.4 StartY=69.3 StartZ=0 EndX=-107.4 EndY=83.1 EndZ=0
    g92: LineSegment StartX=-107.4 StartY=83.1 StartZ=0 EndX=-121.2 EndY=83.1 EndZ=0
    g93: LineSegment StartX=-121.2 StartY=83.1 StartZ=0 EndX=-121.2 EndY=69.3 EndZ=0
    g94: GeomPoint [constr] X=-114.3 Y=76.2 Z=0
    g95: LineSegment StartX=-83.1 StartY=69.3 StartZ=0 EndX=-69.3 EndY=69.3 EndZ=0
    g96: LineSegment StartX=-69.3 StartY=69.3 StartZ=0 EndX=-69.3 EndY=83.1 EndZ=0
    g97: LineSegment StartX=-69.3 StartY=83.1 StartZ=0 EndX=-83.1 EndY=83.1 EndZ=0
    g98: LineSegment StartX=-83.1 StartY=83.1 StartZ=0 EndX=-83.1 EndY=69.3 EndZ=0
    g99: GeomPoint [constr] X=-76.2 Y=76.2 Z=0
    g100: LineSegment StartX=-31.2 StartY=83.1 StartZ=0 EndX=-45 EndY=83.1 EndZ=0
    g101: LineSegment StartX=-45 StartY=83.1 StartZ=0 EndX=-45 EndY=69.3 EndZ=0
    g102: LineSegment StartX=-45 StartY=69.3 StartZ=0 EndX=-31.2 EndY=69.3 EndZ=0
    g103: LineSegment StartX=-31.2 StartY=69.3 StartZ=0 EndX=-31.2 EndY=83.1 EndZ=0
    g104: GeomPoint [constr] X=-38.1 Y=76.2 Z=0
    g105: LineSegment StartX=-126.45 StartY=64.05 StartZ=0 EndX=-140.25 EndY=64.05 EndZ=0
    g106: LineSegment StartX=-140.25 StartY=64.05 StartZ=0 EndX=-140.25 EndY=50.25 EndZ=0
    g107: LineSegment StartX=-140.25 StartY=50.25 StartZ=0 EndX=-126.45 EndY=50.25 EndZ=0
    g108: LineSegment StartX=-126.45 StartY=50.25 StartZ=0 EndX=-126.45 EndY=64.05 EndZ=0
    g109: GeomPoint [constr] X=-133.35 Y=57.15 Z=0
    g110: LineSegment StartX=-126.45 StartY=45 StartZ=0 EndX=-140.25 EndY=45 EndZ=0
    g111: LineSegment StartX=-140.25 StartY=45 StartZ=0 EndX=-140.25 EndY=31.2 EndZ=0
    g112: LineSegment StartX=-140.25 StartY=31.2 StartZ=0 EndX=-126.45 EndY=31.2 EndZ=0
    g113: LineSegment StartX=-126.45 StartY=31.2 StartZ=0 EndX=-126.45 EndY=45 EndZ=0
    g114: GeomPoint [constr] X=-133.35 Y=38.1 Z=0
    g115: LineSegment StartX=-126.45 StartY=25.95 StartZ=0 EndX=-140.25 EndY=25.95 EndZ=0
    g116: LineSegment StartX=-140.25 StartY=25.95 StartZ=0 EndX=-140.25 EndY=12.15 EndZ=0
    g117: LineSegment StartX=-140.25 StartY=12.15 StartZ=0 EndX=-126.45 EndY=12.15 EndZ=0
    g118: LineSegment StartX=-126.45 StartY=12.15 StartZ=0 EndX=-126.45 EndY=25.95 EndZ=0
    g119: GeomPoint [constr] X=-133.35 Y=19.05 Z=0
    g120: LineSegment StartX=-12.15 StartY=25.95 StartZ=0 EndX=-25.95 EndY=25.95 EndZ=0
    g121: LineSegment StartX=-25.95 StartY=25.95 StartZ=0 EndX=-25.95 EndY=12.15 EndZ=0
    g122: LineSegment StartX=-25.95 StartY=12.15 StartZ=0 EndX=-12.15 EndY=12.15 EndZ=0
    g123: LineSegment StartX=-12.15 StartY=12.15 StartZ=0 EndX=-12.15 EndY=25.95 EndZ=0
    g124: GeomPoint [constr] X=-19.05 Y=19.05 Z=0
  constraints (325):
    c: Coincident(g0,g1)
    c: Coincident(g1,g2)
    c: Coincident(g2,g3)
    c: Coincident(g3,g0)
    c: Horizontal(g0)
    c: Horizontal(g2)
    c: Vertical(g1)
    c: Vertical(g3)
    c: Symmetric(g2,g0,g4)
    c: Coincident(g5,g6)
    c: Coincident(g6,g7)
    c: Coincident(g7,g8)
    c: Coincident(g8,g5)
    c: Horizontal(g5)
    c: Horizontal(g7)
    c: Vertical(g6)
    c: Vertical(g8)
    c: Symmetric(g7,g5,g9)
    c: DistanceX(g9,g4) = 19.05
    c: Coincident(g10,g11)
    c: Coincident(g11,g12)
    c: Coincident(g12,g13)
    c: Coincident(g13,g10)
    c: Horizontal(g10)
    c: Horizontal(g12)
    c: Vertical(g11)
    c: Vertical(g13)
    c: Symmetric(g12,g10,g14)
    c: DistanceX(g14,g9) = 19.05
    c: Coincident(g15,g16)
    c: Coincident(g16,g17)
    c: Coincident(g17,g18)
    c: Coincident(g18,g15)
    c: Horizontal(g15)
    c: Horizontal(g17)
    c: Vertical(g16)
    c: Vertical(g18)
    c: Symmetric(g17,g15,g19)
    c: Coincident(g20,g21)
    c: Coincident(g21,g22)
    c: Coincident(g22,g23)
    c: Coincident(g23,g20)
    c: Horizontal(g20)
    c: Horizontal(g22)
    c: Vertical(g21)
    c: Vertical(g23)
    c: Symmetric(g22,g20,g24)
    c: DistanceX(g19,g14) = 19.05
    c: DistanceX(g24,g19) = 19.05
    c: Coincident(g25,g26)
    c: Coincident(g26,g27)
    c: Coincident(g27,g28)
    c: Coincident(g28,g25)
    c: Horizontal(g25)
    c: Horizontal(g27)
    c: Vertical(g26)
    c: Vertical(g28)
    c: Symmetric(g27,g25,g29)
    c: Coincident(g30,g31)
    c: Coincident(g31,g32)
    c: Coincident(g32,g33)
    c: Coincident(g33,g30)
    c: Horizontal(g30)
    c: Horizontal(g32)
    c: Vertical(g31)
    c: Vertical(g33)
    c: Symmetric(g32,g30,g34)
    c: Coincident(g35,g36)
    c: Coincident(g36,g37)
    c: Coincident(g37,g38)
    c: Coincident(g38,g35)
    c: Horizontal(g35)
    c: Horizontal(g37)
    c: Vertical(g36)
    c: Vertical(g38)
    c: Symmetric(g37,g35,g39)
    c: Coincident(g40,g41)
    c: Coincident(g41,g42)
    c: Coincident(g42,g43)
    c: Coincident(g43,g40)
    c: Horizontal(g40)
    c: Horizontal(g42)
    c: Vertical(g41)
    c: Vertical(g43)
    c: Symmetric(g42,g40,g44)
    c: Coincident(g45,g46)
    c: Coincident(g46,g47)
    c: Coincident(g47,g48)
    c: Coincident(g48,g45)
    c: Horizontal(g45)
    c: Horizontal(g47)
    c: Vertical(g46)
    c: Vertical(g48)
    c: Symmetric(g47,g45,g49)
    c: Coincident(g50,g51)
    c: Coincident(g51,g52)
    c: Coincident(g52,g53)
    c: Coincident(g53,g50)
    c: Horizontal(g50)
    c: Horizontal(g52)
    c: Vertical(g51)
    c: Vertical(g53)
    c: Symmetric(g52,g50,g54)
    c: Coincident(g55,g56)
    c: Coincident(g56,g57)
    c: Coincident(g57,g58)
    c: Coincident(g58,g55)
    c: Horizontal(g55)
    c: Horizontal(g57)
    c: Vertical(g56)
    c: Vertical(g58)
    c: Symmetric(g57,g55,g59)
    c: Coincident(g60,g61)
    c: Coincident(g61,g62)
    c: Coincident(g62,g63)
    c: Coincident(g63,g60)
    c: Horizontal(g60)
    c: Horizontal(g62)
    c: Vertical(g61)
    c: Vertical(g63)
    c: Symmetric(g62,g60,g64)
    c: Coincident(g65,g66)
    c: Coincident(g66,g67)
    c: Coincident(g67,g68)
    c: Coincident(g68,g65)
    c: Horizontal(g65)
    c: Horizontal(g67)
    c: Vertical(g66)
    c: Vertical(g68)
    c: Symmetric(g67,g65,g69)
    c: Coincident(g70,g71)
    c: Coincident(g71,g72)
    c: Coincident(g72,g73)
    c: Coincident(g73,g70)
    c: Horizontal(g70)
    c: Horizontal(g72)
    c: Vertical(g71)
    c: Vertical(g73)
    c: Symmetric(g72,g70,g74)
    c: DistanceY(g54,g29) = 19.05
    c: Coincident(g75,g76)
    c: Coincident(g76,g77)
    c: Coincident(g77,g78)
    c: Coincident(g78,g75)
    c: Horizontal(g75)
    c: Horizontal(g77)
    c: Vertical(g76)
    c: Vertical(g78)
    c: Symmetric(g77,g75,g79)
    c: Coincident(g80,g81)
    c: Coincident(g81,g82)
    c: Coincident(g82,g83)
    c: Coincident(g83,g80)
    c: Horizontal(g80)
    c: Horizontal(g82)
    c: Vertical(g81)
    c: Vertical(g83)
    c: Symmetric(g82,g80,g84)
    c: Coincident(g85,g86)
    c: Coincident(g86,g87)
    c: Coincident(g87,g88)
    c: Coincident(g88,g85)
    c: Horizontal(g85)
    c: Horizontal(g87)
    c: Vertical(g86)
    c: Vertical(g88)
    c: Symmetric(g87,g85,g89)
    c: Coincident(g90,g91)
    c: Coincident(g91,g92)
    c: Coincident(g92,g93)
    c: Coincident(g93,g90)
    c: Horizontal(g90)
    c: Horizontal(g92)
    c: Vertical(g91)
    c: Vertical(g93)
    c: Symmetric(g92,g90,g94)
    c: Coincident(g95,g96)
    c: Coincident(g96,g97)
    c: Coincident(g97,g98)
    c: Coincident(g98,g95)
    c: Horizontal(g95)
    c: Horizontal(g97)
    c: Vertical(g96)
    c: Vertical(g98)
    c: Symmetric(g97,g95,g99)
    c: Coincident(g100,g101)
    c: Coincident(g101,g102)
    c: Coincident(g102,g103)
    c: Coincident(g103,g100)
    c: Horizontal(g100)
    c: Horizontal(g102)
    c: Vertical(g101)
    c: Vertical(g103)
    c: Symmetric(g102,g100,g104)
    c: Coincident(g105,g106)
    c: Coincident(g106,g107)
    c: Coincident(g107,g108)
    c: Coincident(g108,g105)
    c: Horizontal(g105)
    c: Horizontal(g107)
    c: Vertical(g106)
    c: Vertical(g108)
    c: Symmetric(g107,g105,g109)
    c: Coincident(g110,g111)
    c: Coincident(g111,g112)
    c: Coincident(g112,g113)
    c: Coincident(g113,g110)
    c: Horizontal(g110)
    c: Horizontal(g112)
    c: Vertical(g111)
    c: Vertical(g113)
    c: Symmetric(g112,g110,g114)
    c: Coincident(g115,g116)
    c: Coincident(g116,g117)
    c: Coincident(g117,g118)
    c: Coincident(g118,g115)
    c: Horizontal(g115)
    c: Horizontal(g117)
    c: Vertical(g118)
    c: Symmetric(g117,g115,g119)
    c: DistanceY(g29,g104) = 19.05
    c: DistanceX(g119,g24) = 19.05
    c: Coincident(g120,g121)
    c: Coincident(g121,g122)
    c: Coincident(g122,g123)
    c: Coincident(g123,g120)
    c: Horizontal(g120)
    c: Horizontal(g122)
    c: Vertical(g121)
    c: Vertical(g123)
    c: Symmetric(g122,g120,g124)
    c: DistanceX(g4,g124) = 19.05
    c: DistanceX(g122,g122) = 13.8
    c: DistanceY(g121,g121) = 13.8
    c: Horizontal(g89,g94)
    c: Horizontal(g94,g79)
    c: Horizontal(g79,g99)
    c: Horizontal(g99,g84)
    c: Horizontal(g84,g104)
    c: Horizontal(g109,g49)
    c: Horizontal(g49,g44)
    c: Horizontal(g44,g39)
    c: Horizontal(g39,g34)
    c: Horizontal(g34,g29)
    c: Horizontal(g114,g74)
    c: Horizontal(g74,g69)
    c: Horizontal(g69,g64)
    c: Horizontal(g64,g59)
    c: Horizontal(g59,g54)
    c: Vertical(g89,g109)
    c: Vertical(g109,g114)
    c: Vertical(g114,g119)
    c: Vertical(g94,g49)
    c: Vertical(g49,g74)
    c: Vertical(g74,g24)
    c: Vertical(g79,g44)
    c: Vertical(g44,g69)
    c: Vertical(g69,g19)
    c: Vertical(g99,g39)
    c: Vertical(g39,g64)
    c: Vertical(g64,g14)
    c: Vertical(g84,g34)
    c: Vertical(g34,g59)
    c: Vertical(g59,g9)
    c: Vertical(g104,g29)
    c: Vertical(g29,g54)
    c: Vertical(g54,g4)
    c: DistanceX(g124,g-1) = 19.05
    c: Horizontal(g119,g24)
    c: Horizontal(g24,g19)
    c: Horizontal(g19,g14)
    c: Horizontal(g14,g9)
    c: Horizontal(g9,g4)
    c: Horizontal(g4,g124)
    c: DistanceY(g-1,g124) = 19.05
    c: DistanceY(g124,g54) = 19.05
    c: Equal(g88,g93)
    c: Equal(g93,g78)
    c: Equal(g78,g98)
    c: Equal(g98,g83)
    c: Equal(g83,g101)
    c: Equal(g101,g121)
    c: Equal(g106,g48)
    c: Equal(g48,g43)
    c: Equal(g43,g38)
    c: Equal(g38,g33)
    c: Equal(g33,g28)
    c: Equal(g28,g121)
    c: Equal(g111,g73)
    c: Equal(g73,g68)
    c: Equal(g68,g63)
    c: Equal(g63,g58)
    c: Equal(g58,g53)
    c: Equal(g53,g121)
    c: Equal(g116,g23)
    c: Equal(g23,g18)
    c: Equal(g18,g13)
    c: Equal(g13,g8)
    c: Equal(g8,g3)
    c: Equal(g3,g121)
    c: Equal(g85,g90)
    c: Equal(g90,g75)
    c: Equal(g75,g95)
    c: Equal(g95,g80)
    c: Equal(g80,g102)
    c: Equal(g102,g122)
    c: Equal(g107,g45)
    c: Equal(g45,g40)
    c: Equal(g40,g35)
    c: Equal(g35,g30)
    c: Equal(g30,g25)
    c: Equal(g25,g122)
    c: Equal(g112,g70)
    c: Equal(g70,g65)
    c: Equal(g65,g60)
    c: Equal(g60,g55)
    c: Equal(g55,g50)
    c: Equal(g50,g122)
    c: Equal(g117,g20)
    c: Equal(g20,g15)
    c: Equal(g15,g10)
    c: Equal(g10,g5)
    c: Vertical(g116)
    c: Equal(g5,g0)
    c: Equal(g0,g122)
FEATURE [Sketcher::SketchObject] Sketch002  label="TL-Hi"
  ArcFitTolerance = 1e-06
  AttachmentOffset = pos=(0,0,5) rot=(0,0,1;0rad)
  AttachmentSupport = -> [XY_Plane]
  FullyConstrained = true
  MakeInternals = false
  MapMode = 5
  Placement = pos=(0,0,5) rot=(0,0,1;0rad)
  expr: .AttachmentOffset.Base.z = VarSet.Top_PcbZ + VarSet.Top_LoZ + VarSet.Top_MedZ + VarSet.Top_HiZ
  expr: Constraints[132] = VarSet.Top_HiXY
  expr: Constraints[133] = VarSet.Top_HiXY
  expr: Constraints[724] = VarSet.Top_HiSwFilletR
  sketch-geometry (325):
    g0: LineSegment StartX=-44.65 StartY=11.5 StartZ=0 EndX=-31.55 EndY=11.5 EndZ=0
    g1: LineSegment StartX=-30.55 StartY=12.5 StartZ=0 EndX=-30.55 EndY=25.6 EndZ=0
    g2: LineSegment StartX=-31.55 StartY=26.6 StartZ=0 EndX=-44.65 EndY=26.6 EndZ=0
    g3: LineSegment StartX=-45.65 StartY=25.6 StartZ=0 EndX=-45.65 EndY=12.5 EndZ=0
    g4: GeomPoint [constr] X=-38.1 Y=19.05 Z=0
    g5: LineSegment StartX=-63.7 StartY=11.5 StartZ=0 EndX=-50.6 EndY=11.5 EndZ=0
    g6: LineSegment StartX=-49.6 StartY=12.5 StartZ=0 EndX=-49.6 EndY=25.6 EndZ=0
    g7: LineSegment StartX=-50.6 StartY=26.6 StartZ=0 EndX=-63.7 EndY=26.6 EndZ=0
    g8: LineSegment StartX=-64.7 StartY=25.6 StartZ=0 EndX=-64.7 EndY=12.5 EndZ=0
    g9: GeomPoint [constr] X=-57.15 Y=19.05 Z=0
    g10: LineSegment StartX=-82.75 StartY=11.5 StartZ=0 EndX=-69.65 EndY=11.5 EndZ=0
    g11: LineSegment StartX=-68.65 StartY=12.5 StartZ=0 EndX=-68.65 EndY=25.6 EndZ=0
    g12: LineSegment StartX=-69.65 StartY=26.6 StartZ=0 EndX=-82.75 EndY=26.6 EndZ=0
    g13: LineSegment StartX=-83.75 StartY=25.6 StartZ=0 EndX=-83.75 EndY=12.5 EndZ=0
    g14: GeomPoint [constr] X=-76.2 Y=19.05 Z=0
    g15: LineSegment StartX=-101.8 StartY=11.5 StartZ=0 EndX=-88.7 EndY=11.5 EndZ=0
    g16: LineSegment StartX=-87.7 StartY=12.5 StartZ=0 EndX=-87.7 EndY=25.6 EndZ=0
    g17: LineSegment StartX=-88.7 StartY=26.6 StartZ=0 EndX=-101.8 EndY=26.6 EndZ=0
    g18: LineSegment StartX=-102.8 StartY=25.6 StartZ=0 EndX=-102.8 EndY=12.5 EndZ=0
    g19: GeomPoint [constr] X=-95.25 Y=19.05 Z=0
    g20: LineSegment StartX=-120.85 StartY=11.5 StartZ=0 EndX=-107.75 EndY=11.5 EndZ=0
    g21: LineSegment StartX=-106.75 StartY=12.5 StartZ=0 EndX=-106.75 EndY=25.6 EndZ=0
    g22: LineSegment StartX=-107.75 StartY=26.6 StartZ=0 EndX=-120.85 EndY=26.6 EndZ=0
    g23: LineSegment StartX=-121.85 StartY=25.6 StartZ=0 EndX=-121.85 EndY=12.5 EndZ=0
    g24: GeomPoint [constr] X=-114.3 Y=19.05 Z=0
    g25: LineSegment StartX=-44.65 StartY=49.6 StartZ=0 EndX=-31.55 EndY=49.6 EndZ=0
    g26: LineSegment StartX=-30.55 StartY=50.6 StartZ=0 EndX=-30.55 EndY=63.7 EndZ=0
    g27: LineSegment StartX=-31.55 StartY=64.7 StartZ=0 EndX=-44.65 EndY=64.7 EndZ=0
    g28: LineSegment StartX=-45.65 StartY=63.7 StartZ=0 EndX=-45.65 EndY=50.6 EndZ=0
    g29: GeomPoint [constr] X=-38.1 Y=57.15 Z=0
    g30: LineSegment StartX=-63.7 StartY=49.6 StartZ=0 EndX=-50.6 EndY=49.6 EndZ=0
    g31: LineSegment StartX=-49.6 StartY=50.6 StartZ=0 EndX=-49.6 EndY=63.7 EndZ=0
    g32: LineSegment StartX=-50.6 StartY=64.7 StartZ=0 EndX=-63.7 EndY=64.7 EndZ=0
    g33: LineSegment StartX=-64.7 StartY=63.7 StartZ=0 EndX=-64.7 EndY=50.6 EndZ=0
    g34: GeomPoint [constr] X=-57.15 Y=57.15 Z=0
    g35: LineSegment StartX=-82.75 StartY=49.6 StartZ=0 EndX=-69.65 EndY=49.6 EndZ=0
    g36: LineSegment StartX=-68.65 StartY=50.6 StartZ=0 EndX=-68.65 EndY=63.7 EndZ=0
    g37: LineSegment StartX=-69.65 StartY=64.7 StartZ=0 EndX=-82.75 EndY=64.7 EndZ=0
    g38: LineSegment StartX=-83.75 StartY=63.7 StartZ=0 EndX=-83.75 EndY=50.6 EndZ=0
    g39: GeomPoint [constr] X=-76.2 Y=57.15 Z=0
    g40: LineSegment StartX=-101.8 StartY=49.6 StartZ=0 EndX=-88.7 EndY=49.6 EndZ=0
    g41: LineSegment StartX=-87.7 StartY=50.6 StartZ=0 EndX=-87.7 EndY=63.7 EndZ=0
    g42: LineSegment StartX=-88.7 StartY=64.7 StartZ=0 EndX=-101.8 EndY=64.7 EndZ=0
    g43: LineSegment StartX=-102.8 StartY=63.7 StartZ=0 EndX=-102.8 EndY=50.6 EndZ=0
    g44: GeomPoint [constr] X=-95.25 Y=57.15 Z=0
    g45: LineSegment StartX=-120.85 StartY=49.6 StartZ=0 EndX=-107.75 EndY=49.6 EndZ=0
    g46: LineSegment StartX=-106.75 StartY=50.6 StartZ=0 EndX=-106.75 EndY=63.7 EndZ=0
    g47: LineSegment StartX=-107.75 StartY=64.7 StartZ=0 EndX=-120.85 EndY=64.7 EndZ=0
    g48: LineSegment StartX=-121.85 StartY=63.7 StartZ=0 EndX=-121.85 EndY=50.6 EndZ=0
    g49: GeomPoint [constr] X=-114.3 Y=57.15 Z=0
    g50: LineSegment StartX=-44.65 StartY=30.55 StartZ=0 EndX=-31.55 EndY=30.55 EndZ=0
    g51: LineSegment StartX=-30.55 StartY=31.55 StartZ=0 EndX=-30.55 EndY=44.65 EndZ=0
    g52: LineSegment StartX=-31.55 StartY=45.65 StartZ=0 EndX=-44.65 EndY=45.65 EndZ=0
    g53: LineSegment StartX=-45.65 StartY=44.65 StartZ=0 EndX=-45.65 EndY=31.55 EndZ=0
    g54: GeomPoint [constr] X=-38.1 Y=38.1 Z=0
    g55: LineSegment StartX=-63.7 StartY=30.55 StartZ=0 EndX=-50.6 EndY=30.55 EndZ=0
    g56: LineSegment StartX=-49.6 StartY=31.55 StartZ=0 EndX=-49.6 EndY=44.65 EndZ=0
    g57: LineSegment StartX=-50.6 StartY=45.65 StartZ=0 EndX=-63.7 EndY=45.65 EndZ=0
    g58: LineSegment StartX=-64.7 StartY=44.65 StartZ=0 EndX=-64.7 EndY=31.55 EndZ=0
    g59: GeomPoint [constr] X=-57.15 Y=38.1 Z=0
    g60: LineSegment StartX=-82.75 StartY=30.55 StartZ=0 EndX=-69.65 EndY=30.55 EndZ=0
    g61: LineSegment StartX=-68.65 StartY=31.55 StartZ=0 EndX=-68.65 EndY=44.65 EndZ=0
    g62: LineSegment StartX=-69.65 StartY=45.65 StartZ=0 EndX=-82.75 EndY=45.65 EndZ=0
    g63: LineSegment StartX=-83.75 StartY=44.65 StartZ=0 EndX=-83.75 EndY=31.55 EndZ=0
    g64: GeomPoint [constr] X=-76.2 Y=38.1 Z=0
    g65: LineSegment StartX=-101.8 StartY=30.55 StartZ=0 EndX=-88.7 EndY=30.55 EndZ=0
    g66: LineSegment StartX=-87.7 StartY=31.55 StartZ=0 EndX=-87.7 EndY=44.65 EndZ=0
    g67: LineSegment StartX=-88.7 StartY=45.65 StartZ=0 EndX=-101.8 EndY=45.65 EndZ=0
    g68: LineSegment StartX=-102.8 StartY=44.65 StartZ=0 EndX=-102.8 EndY=31.55 EndZ=0
    g69: GeomPoint [constr] X=-95.25 Y=38.1 Z=0
    g70: LineSegment StartX=-120.85 StartY=30.55 StartZ=0 EndX=-107.75 EndY=30.55 EndZ=0
    g71: LineSegment StartX=-106.75 StartY=31.55 StartZ=0 EndX=-106.75 EndY=44.65 EndZ=0
    g72: LineSegment StartX=-107.75 StartY=45.65 StartZ=0 EndX=-120.85 EndY=45.65 EndZ=0
    g73: LineSegment StartX=-121.85 StartY=44.65 StartZ=0 EndX=-121.85 EndY=31.55 EndZ=0
    g74: GeomPoint [constr] X=-114.3 Y=38.1 Z=0
    g75: LineSegment StartX=-101.8 StartY=68.65 StartZ=0 EndX=-88.7 EndY=68.65 EndZ=0
    g76: LineSegment StartX=-87.7 StartY=69.65 StartZ=0 EndX=-87.7 EndY=82.75 EndZ=0
    g77: LineSegment StartX=-88.7 StartY=83.75 StartZ=0 EndX=-101.8 EndY=83.75 EndZ=0
    g78: LineSegment StartX=-102.8 StartY=82.75 StartZ=0 EndX=-102.8 EndY=69.65 EndZ=0
    g79: GeomPoint [constr] X=-95.25 Y=76.2 Z=0
    g80: LineSegment StartX=-63.7 StartY=68.65 StartZ=0 EndX=-50.6 EndY=68.65 EndZ=0
    g81: LineSegment StartX=-49.6 StartY=69.65 StartZ=0 EndX=-49.6 EndY=82.75 EndZ=0
    g82: LineSegment StartX=-50.6 StartY=83.75 StartZ=0 EndX=-63.7 EndY=83.75 EndZ=0
    g83: LineSegment StartX=-64.7 StartY=82.75 StartZ=0 EndX=-64.7 EndY=69.65 EndZ=0
    g84: GeomPoint [constr] X=-57.15 Y=76.2 Z=0
    g85: LineSegment StartX=-139.9 StartY=68.65 StartZ=0 EndX=-126.8 EndY=68.65 EndZ=0
    g86: LineSegment StartX=-125.8 StartY=69.65 StartZ=0 EndX=-125.8 EndY=82.75 EndZ=0
    g87: LineSegment StartX=-126.8 StartY=83.75 StartZ=0 EndX=-139.9 EndY=83.75 EndZ=0
    g88: LineSegment StartX=-140.9 StartY=82.75 StartZ=0 EndX=-140.9 EndY=69.65 EndZ=0
    g89: GeomPoint [constr] X=-133.35 Y=76.2 Z=0
    g90: LineSegment StartX=-120.85 StartY=68.65 StartZ=0 EndX=-107.75 EndY=68.65 EndZ=0
    g91: LineSegment StartX=-106.75 StartY=69.65 StartZ=0 EndX=-106.75 EndY=82.75 EndZ=0
    g92: LineSegment StartX=-107.75 StartY=83.75 StartZ=0 EndX=-120.85 EndY=83.75 EndZ=0
    g93: LineSegment StartX=-121.85 StartY=82.75 StartZ=0 EndX=-121.85 EndY=69.65 EndZ=0
    g94: GeomPoint [constr] X=-114.3 Y=76.2 Z=0
    g95: LineSegment StartX=-82.75 StartY=68.65 StartZ=0 EndX=-69.65 EndY=68.65 EndZ=0
    g96: LineSegment StartX=-68.65 StartY=69.65 StartZ=0 EndX=-68.65 EndY=82.75 EndZ=0
    g97: LineSegment StartX=-69.65 StartY=83.75 StartZ=0 EndX=-82.75 EndY=83.75 EndZ=0
    g98: LineSegment StartX=-83.75 StartY=82.75 StartZ=0 EndX=-83.75 EndY=69.65 EndZ=0
    g99: GeomPoint [constr] X=-76.2 Y=76.2 Z=0
    g100: LineSegment StartX=-31.55 StartY=83.75 StartZ=0 EndX=-44.65 EndY=83.75 EndZ=0
    g101: LineSegment StartX=-45.65 StartY=82.75 StartZ=0 EndX=-45.65 EndY=69.65 EndZ=0
    g102: LineSegment StartX=-44.65 StartY=68.65 StartZ=0 EndX=-31.55 EndY=68.65 EndZ=0
    g103: LineSegment StartX=-30.55 StartY=69.65 StartZ=0 EndX=-30.55 EndY=82.75 EndZ=0
    g104: GeomPoint [constr] X=-38.1 Y=76.2 Z=0
    g105: LineSegment StartX=-126.8 StartY=64.7 StartZ=0 EndX=-139.9 EndY=64.7 EndZ=0
    g106: LineSegment StartX=-140.9 StartY=63.7 StartZ=0 EndX=-140.9 EndY=50.6 EndZ=0
    g107: LineSegment StartX=-139.9 StartY=49.6 StartZ=0 EndX=-126.8 EndY=49.6 EndZ=0
    g108: LineSegment StartX=-125.8 StartY=50.6 StartZ=0 EndX=-125.8 EndY=63.7 EndZ=0
    g109: GeomPoint [constr] X=-133.35 Y=57.15 Z=0
    g110: LineSegment StartX=-126.8 StartY=45.65 StartZ=0 EndX=-139.9 EndY=45.65 EndZ=0
    g111: LineSegment StartX=-140.9 StartY=44.65 StartZ=0 EndX=-140.9 EndY=31.55 EndZ=0
    g112: LineSegment StartX=-139.9 StartY=30.55 StartZ=0 EndX=-126.8 EndY=30.55 EndZ=0
    g113: LineSegment StartX=-125.8 StartY=31.55 StartZ=0 EndX=-125.8 EndY=44.65 EndZ=0
    g114: GeomPoint [constr] X=-133.35 Y=38.1 Z=0
    g115: LineSegment StartX=-126.8 StartY=26.6 StartZ=0 EndX=-139.9 EndY=26.6 EndZ=0
    g116: LineSegment StartX=-140.9 StartY=25.6 StartZ=0 EndX=-140.9 EndY=12.5 EndZ=0
    g117: LineSegment StartX=-139.9 StartY=11.5 StartZ=0 EndX=-126.8 EndY=11.5 EndZ=0
    g118: LineSegment StartX=-125.8 StartY=12.5 StartZ=0 EndX=-125.8 EndY=25.6 EndZ=0
    g119: GeomPoint [constr] X=-133.35 Y=19.05 Z=0
    g120: LineSegment StartX=-12.5 StartY=26.6 StartZ=0 EndX=-25.6 EndY=26.6 EndZ=0
    g121: LineSegment StartX=-26.6 StartY=25.6 StartZ=0 EndX=-26.6 EndY=12.5 EndZ=0
    g122: LineSegment StartX=-25.6 StartY=11.5 StartZ=0 EndX=-12.5 EndY=11.5 EndZ=0
    g123: LineSegment StartX=-11.5 StartY=12.5 StartZ=0 EndX=-11.5 EndY=25.6 EndZ=0
    g124: GeomPoint [constr] X=-19.05 Y=19.05 Z=0
    g125: ArcOfCircle CenterX=-139.9 CenterY=82.75 CenterZ=0 NormalX=0 NormalY=0 NormalZ=1 AngleXU=0 Radius=1 StartAngle=1.5708 EndAngle=3.14159
    g126: GeomPoint [constr] X=-140.9 Y=83.75 Z=0
    g127: ArcOfCircle CenterX=-126.8 CenterY=82.75 CenterZ=0 NormalX=0 NormalY=0 NormalZ=1 AngleXU=0 Radius=1 StartAngle=-7.1e-15 EndAngle=1.5708
    g128: GeomPoint [constr] X=-125.8 Y=83.75 Z=0
    g129: ArcOfCircle CenterX=-126.8 CenterY=69.65 CenterZ=0 NormalX=0 NormalY=0 NormalZ=1 AngleXU=0 Radius=1 StartAngle=4.71239 EndAngle=6.28319
    g130: GeomPoint [constr] X=-125.8 Y=68.65 Z=0
    g131: ArcOfCircle CenterX=-139.9 CenterY=69.65 CenterZ=0 NormalX=0 NormalY=0 NormalZ=1 AngleXU=0 Radius=1 StartAngle=3.14159 EndAngle=4.71239
    g132: GeomPoint [constr] X=-140.9 Y=68.65 Z=0
    g133: ArcOfCircle CenterX=-120.85 CenterY=82.75 CenterZ=0 NormalX=0 NormalY=0 NormalZ=1 AngleXU=0 Radius=1 StartAngle=1.5708 EndAngle=3.14159
    g134: GeomPoint [constr] X=-121.85 Y=83.75 Z=0
    g135: ArcOfCircle CenterX=-107.75 CenterY=82.75 CenterZ=0 NormalX=0 NormalY=0 NormalZ=1 AngleXU=0 Radius=1 StartAngle=5.6e-15 EndAngle=1.5708
    g136: GeomPoint [constr] X=-106.75 Y=83.75 Z=0
    g137: ArcOfCircle CenterX=-107.75 CenterY=69.65 CenterZ=0 NormalX=0 NormalY=0 NormalZ=1 AngleXU=0 Radius=1 StartAngle=4.71239 EndAngle=6.28319
    g138: GeomPoint [constr] X=-106.75 Y=68.65 Z=0
    g139: ArcOfCircle CenterX=-120.85 CenterY=69.65 CenterZ=0 NormalX=0 NormalY=0 NormalZ=1 AngleXU=0 Radius=1 StartAngle=3.14159 EndAngle=4.71239
    g140: GeomPoint [constr] X=-121.85 Y=68.65 Z=0
    g141: ArcOfCircle CenterX=-101.8 CenterY=82.75 CenterZ=0 NormalX=0 NormalY=0 NormalZ=1 AngleXU=0 Radius=1 StartAngle=1.5708 EndAngle=3.14159
    g142: GeomPoint [constr] X=-102.8 Y=83.75 Z=0
    g143: ArcOfCircle CenterX=-88.7 CenterY=82.75 CenterZ=0 NormalX=0 NormalY=0 NormalZ=1 AngleXU=0 Radius=1 StartAngle=-4.4e-15 EndAngle=1.5708
    g144: GeomPoint [constr] X=-87.7 Y=83.75 Z=0
    g145: ArcOfCircle CenterX=-88.7 CenterY=69.65 CenterZ=0 NormalX=0 NormalY=0 NormalZ=1 AngleXU=0 Radius=1 StartAngle=4.71239 EndAngle=6.28319
    g146: GeomPoint [constr] X=-87.7 Y=68.65 Z=0
    g147: ArcOfCircle CenterX=-101.8 CenterY=69.65 CenterZ=0 NormalX=0 NormalY=0 NormalZ=1 AngleXU=0 Radius=1 StartAngle=3.14159 EndAngle=4.71239
    g148: GeomPoint [constr] X=-102.8 Y=68.65 Z=0
    g149: ArcOfCircle CenterX=-82.75 CenterY=82.75 CenterZ=0 NormalX=0 NormalY=0 NormalZ=1 AngleXU=0 Radius=1 StartAngle=1.5708 EndAngle=3.14159
    g150: GeomPoint [constr] X=-83.75 Y=83.75 Z=0
    g151: ArcOfCircle CenterX=-69.65 CenterY=82.75 CenterZ=0 NormalX=0 NormalY=0 NormalZ=1 AngleXU=0 Radius=1 StartAngle=-5.3e-15 EndAngle=1.5708
    g152: GeomPoint [constr] X=-68.65 Y=83.75 Z=0
    g153: ArcOfCircle CenterX=-69.65 CenterY=69.65 CenterZ=0 NormalX=0 NormalY=0 NormalZ=1 AngleXU=0 Radius=1 StartAngle=4.71239 EndAngle=6.28319
    g154: GeomPoint [constr] X=-68.65 Y=68.65 Z=0
    g155: ArcOfCircle CenterX=-82.75 CenterY=69.65 CenterZ=0 NormalX=0 NormalY=0 NormalZ=1 AngleXU=0 Radius=1 StartAngle=3.14159 EndAngle=4.71239
    g156: GeomPoint [constr] X=-83.75 Y=68.65 Z=0
    g157: ArcOfCircle CenterX=-63.7 CenterY=82.75 CenterZ=0 NormalX=0 NormalY=0 NormalZ=1 AngleXU=0 Radius=1 StartAngle=1.5708 EndAngle=3.14159
    g158: GeomPoint [constr] X=-64.7 Y=83.75 Z=0
    g159: ArcOfCircle CenterX=-50.6 CenterY=82.75 CenterZ=0 NormalX=0 NormalY=0 NormalZ=1 AngleXU=0 Radius=1 StartAngle=-5.3e-15 EndAngle=1.5708
    g160: GeomPoint [constr] X=-49.6 Y=83.75 Z=0
    g161: ArcOfCircle CenterX=-50.6 CenterY=69.65 CenterZ=0 NormalX=0 NormalY=0 NormalZ=1 AngleXU=0 Radius=1 StartAngle=4.71239 EndAngle=6.28319
    g162: GeomPoint [constr] X=-49.6 Y=68.65 Z=0
    g163: ArcOfCircle CenterX=-63.7 CenterY=69.65 CenterZ=0 NormalX=0 NormalY=0 NormalZ=1 AngleXU=0 Radius=1 StartAngle=3.14159 EndAngle=4.71239
    g164: GeomPoint [constr] X=-64.7 Y=68.65 Z=0
    g165: ArcOfCircle CenterX=-44.65 CenterY=82.75 CenterZ=0 NormalX=0 NormalY=0 NormalZ=1 AngleXU=0 Radius=1 StartAngle=1.5708 EndAngle=3.14159
    g166: GeomPoint [constr] X=-45.65 Y=83.75 Z=0
    g167: ArcOfCircle CenterX=-31.55 CenterY=82.75 CenterZ=0 NormalX=0 NormalY=0 NormalZ=1 AngleXU=0 Radius=1 StartAngle=5.8e-15 EndAngle=1.5708
    g168: GeomPoint [constr] X=-30.55 Y=83.75 Z=0
    g169: ArcOfCircle CenterX=-31.55 CenterY=69.65 CenterZ=0 NormalX=0 NormalY=0 NormalZ=1 AngleXU=0 Radius=1 StartAngle=4.71239 EndAngle=6.28319
    g170: GeomPoint [constr] X=-30.55 Y=68.65 Z=0
    g171: ArcOfCircle CenterX=-44.65 CenterY=69.65 CenterZ=0 NormalX=0 NormalY=0 NormalZ=1 AngleXU=0 Radius=1 StartAngle=3.14159 EndAngle=4.71239
    g172: GeomPoint [constr] X=-45.65 Y=68.65 Z=0
    g173: ArcOfCircle CenterX=-139.9 CenterY=63.7 CenterZ=0 NormalX=0 NormalY=0 NormalZ=1 AngleXU=0 Radius=1 StartAngle=1.5708 EndAngle=3.14159
    g174: GeomPoint [constr] X=-140.9 Y=64.7 Z=0
    g175: ArcOfCircle CenterX=-126.8 CenterY=63.7 CenterZ=0 NormalX=0 NormalY=0 NormalZ=1 AngleXU=0 Radius=1 StartAngle=-2.7e-15 EndAngle=1.5708
    g176: GeomPoint [constr] X=-125.8 Y=64.7 Z=0
    g177: ArcOfCircle CenterX=-126.8 CenterY=50.6 CenterZ=0 NormalX=0 NormalY=0 NormalZ=1 AngleXU=0 Radius=1 StartAngle=4.71239 EndAngle=6.28319
    g178: GeomPoint [constr] X=-125.8 Y=49.6 Z=0
    g179: ArcOfCircle CenterX=-139.9 CenterY=50.6 CenterZ=0 NormalX=0 NormalY=0 NormalZ=1 AngleXU=0 Radius=1 StartAngle=3.14159 EndAngle=4.71239
    g180: GeomPoint [constr] X=-140.9 Y=49.6 Z=0
    g181: ArcOfCircle CenterX=-120.85 CenterY=63.7 CenterZ=0 NormalX=0 NormalY=0 NormalZ=1 AngleXU=0 Radius=1 StartAngle=1.5708 EndAngle=3.14159
    g182: GeomPoint [constr] X=-121.85 Y=64.7 Z=0
    g183: ArcOfCircle CenterX=-107.75 CenterY=63.7 CenterZ=0 NormalX=0 NormalY=0 NormalZ=1 AngleXU=0 Radius=1 StartAngle=-1.8e-15 EndAngle=1.5708
    g184: GeomPoint [constr] X=-106.75 Y=64.7 Z=0
    g185: ArcOfCircle CenterX=-107.75 CenterY=50.6 CenterZ=0 NormalX=0 NormalY=0 NormalZ=1 AngleXU=0 Radius=1 StartAngle=4.71239 EndAngle=6.28319
    g186: GeomPoint [constr] X=-106.75 Y=49.6 Z=0
    g187: ArcOfCircle CenterX=-120.85 CenterY=50.6 CenterZ=0 NormalX=0 NormalY=0 NormalZ=1 AngleXU=0 Radius=1 StartAngle=3.14159 EndAngle=4.71239
    g188: GeomPoint [constr] X=-121.85 Y=49.6 Z=0
    g189: ArcOfCircle CenterX=-101.8 CenterY=63.7 CenterZ=0 NormalX=0 NormalY=0 NormalZ=1 AngleXU=0 Radius=1 StartAngle=1.5708 EndAngle=3.14159
    g190: GeomPoint [constr] X=-102.8 Y=64.7 Z=0
    g191: ArcOfCircle CenterX=-88.7 CenterY=63.7 CenterZ=0 NormalX=0 NormalY=0 NormalZ=1 AngleXU=0 Radius=1 StartAngle=-1.8e-15 EndAngle=1.5708
    g192: GeomPoint [constr] X=-87.7 Y=64.7 Z=0
    g193: ArcOfCircle CenterX=-88.7 CenterY=50.6 CenterZ=0 NormalX=0 NormalY=0 NormalZ=1 AngleXU=0 Radius=1 StartAngle=4.71239 EndAngle=6.28319
    g194: GeomPoint [constr] X=-87.7 Y=49.6 Z=0
    g195: ArcOfCircle CenterX=-101.8 CenterY=50.6 CenterZ=0 NormalX=0 NormalY=0 NormalZ=1 AngleXU=0 Radius=1 StartAngle=3.14159 EndAngle=4.71239
    g196: GeomPoint [constr] X=-102.8 Y=49.6 Z=0
    g197: ArcOfCircle CenterX=-82.75 CenterY=63.7 CenterZ=0 NormalX=0 NormalY=0 NormalZ=1 AngleXU=0 Radius=1 StartAngle=1.5708 EndAngle=3.14159
    g198: GeomPoint [constr] X=-83.75 Y=64.7 Z=0
    g199: ArcOfCircle CenterX=-69.65 CenterY=63.7 CenterZ=0 NormalX=0 NormalY=0 NormalZ=1 AngleXU=0 Radius=1 StartAngle=-1.8e-15 EndAngle=1.5708
    g200: GeomPoint [constr] X=-68.65 Y=64.7 Z=0
    g201: ArcOfCircle CenterX=-69.65 CenterY=50.6 CenterZ=0 NormalX=0 NormalY=0 NormalZ=1 AngleXU=0 Radius=1 StartAngle=4.71239 EndAngle=6.28319
    g202: GeomPoint [constr] X=-68.65 Y=49.6 Z=0
    g203: ArcOfCircle CenterX=-82.75 CenterY=50.6 CenterZ=0 NormalX=0 NormalY=0 NormalZ=1 AngleXU=0 Radius=1 StartAngle=3.14159 EndAngle=4.71239
    g204: GeomPoint [constr] X=-83.75 Y=49.6 Z=0
    g205: ArcOfCircle CenterX=-63.7 CenterY=63.7 CenterZ=0 NormalX=0 NormalY=0 NormalZ=1 AngleXU=0 Radius=1 StartAngle=1.5708 EndAngle=3.14159
    g206: GeomPoint [constr] X=-64.7 Y=64.7 Z=0
    g207: ArcOfCircle CenterX=-50.6 CenterY=63.7 CenterZ=0 NormalX=0 NormalY=0 NormalZ=1 AngleXU=0 Radius=1 StartAngle=0 EndAngle=1.5708
    g208: GeomPoint [constr] X=-49.6 Y=64.7 Z=0
    g209: ArcOfCircle CenterX=-50.6 CenterY=50.6 CenterZ=0 NormalX=0 NormalY=0 NormalZ=1 AngleXU=0 Radius=1 StartAngle=4.71239 EndAngle=6.28319
    g210: GeomPoint [constr] X=-49.6 Y=49.6 Z=0
    g211: ArcOfCircle CenterX=-63.7 CenterY=50.6 CenterZ=0 NormalX=0 NormalY=0 NormalZ=1 AngleXU=0 Radius=1 StartAngle=3.14159 EndAngle=4.71239
    g212: GeomPoint [constr] X=-64.7 Y=49.6 Z=0
    g213: ArcOfCircle CenterX=-44.65 CenterY=63.7 CenterZ=0 NormalX=0 NormalY=0 NormalZ=1 AngleXU=0 Radius=1 StartAngle=1.5708 EndAngle=3.14159
    g214: GeomPoint [constr] X=-45.65 Y=64.7 Z=0
    g215: ArcOfCircle CenterX=-31.55 CenterY=63.7 CenterZ=0 NormalX=0 NormalY=0 NormalZ=1 AngleXU=0 Radius=1 StartAngle=-9e-16 EndAngle=1.5708
    g216: GeomPoint [constr] X=-30.55 Y=64.7 Z=0
    g217: ArcOfCircle CenterX=-31.55 CenterY=50.6 CenterZ=0 NormalX=0 NormalY=0 NormalZ=1 AngleXU=0 Radius=1 StartAngle=4.71239 EndAngle=6.28319
    g218: GeomPoint [constr] X=-30.55 Y=49.6 Z=0
    g219: ArcOfCircle CenterX=-44.65 CenterY=50.6 CenterZ=0 NormalX=0 NormalY=0 NormalZ=1 AngleXU=0 Radius=1 StartAngle=3.14159 EndAngle=4.71239
    g220: GeomPoint [constr] X=-45.65 Y=49.6 Z=0
    g221: ArcOfCircle CenterX=-139.9 CenterY=44.65 CenterZ=0 NormalX=0 NormalY=0 NormalZ=1 AngleXU=0 Radius=1 StartAngle=1.5708 EndAngle=3.14159
    g222: GeomPoint [constr] X=-140.9 Y=45.65 Z=0
    g223: ArcOfCircle CenterX=-126.8 CenterY=44.65 CenterZ=0 NormalX=0 NormalY=0 NormalZ=1 AngleXU=0 Radius=1 StartAngle=3.2e-15 EndAngle=1.5708
    g224: GeomPoint [constr] X=-125.8 Y=45.65 Z=0
    g225: ArcOfCircle CenterX=-126.8 CenterY=31.55 CenterZ=0 NormalX=0 NormalY=0 NormalZ=1 AngleXU=0 Radius=1 StartAngle=4.71239 EndAngle=6.28319
    g226: GeomPoint [constr] X=-125.8 Y=30.55 Z=0
    g227: ArcOfCircle CenterX=-139.9 CenterY=31.55 CenterZ=0 NormalX=0 NormalY=0 NormalZ=1 AngleXU=0 Radius=1 StartAngle=3.14159 EndAngle=4.71239
    g228: GeomPoint [constr] X=-140.9 Y=30.55 Z=0
    g229: ArcOfCircle CenterX=-120.85 CenterY=44.65 CenterZ=0 NormalX=0 NormalY=0 NormalZ=1 AngleXU=0 Radius=1 StartAngle=1.5708 EndAngle=3.14159
    g230: GeomPoint [constr] X=-121.85 Y=45.65 Z=0
    g231: ArcOfCircle CenterX=-107.75 CenterY=44.65 CenterZ=0 NormalX=0 NormalY=0 NormalZ=1 AngleXU=0 Radius=1 StartAngle=-3.6e-15 EndAngle=1.5708
    g232: GeomPoint [constr] X=-106.75 Y=45.65 Z=0
    g233: ArcOfCircle CenterX=-107.75 CenterY=31.55 CenterZ=0 NormalX=0 NormalY=0 NormalZ=1 AngleXU=0 Radius=1 StartAngle=4.71239 EndAngle=6.28319
    g234: GeomPoint [constr] X=-106.75 Y=30.55 Z=0
    g235: ArcOfCircle CenterX=-120.85 CenterY=31.55 CenterZ=0 NormalX=0 NormalY=0 NormalZ=1 AngleXU=0 Radius=1 StartAngle=3.14159 EndAngle=4.71239
    g236: GeomPoint [constr] X=-121.85 Y=30.55 Z=0
    g237: ArcOfCircle CenterX=-101.8 CenterY=44.65 CenterZ=0 NormalX=0 NormalY=0 NormalZ=1 AngleXU=0 Radius=1 StartAngle=1.5708 EndAngle=3.14159
    g238: GeomPoint [constr] X=-102.8 Y=45.65 Z=0
    g239: ArcOfCircle CenterX=-88.7 CenterY=44.65 CenterZ=0 NormalX=0 NormalY=0 NormalZ=1 AngleXU=0 Radius=1 StartAngle=-1.8e-15 EndAngle=1.5708
    g240: GeomPoint [constr] X=-87.7 Y=45.65 Z=0
    g241: ArcOfCircle CenterX=-88.7 CenterY=31.55 CenterZ=0 NormalX=0 NormalY=0 NormalZ=1 AngleXU=0 Radius=1 StartAngle=4.71239 EndAngle=6.28319
    g242: GeomPoint [constr] X=-87.7 Y=30.55 Z=0
    g243: ArcOfCircle CenterX=-101.8 CenterY=31.55 CenterZ=0 NormalX=0 NormalY=0 NormalZ=1 AngleXU=0 Radius=1 StartAngle=3.14159 EndAngle=4.71239
    g244: GeomPoint [constr] X=-102.8 Y=30.55 Z=0
    g245: ArcOfCircle CenterX=-82.75 CenterY=44.65 CenterZ=0 NormalX=0 NormalY=0 NormalZ=1 AngleXU=0 Radius=1 StartAngle=1.5708 EndAngle=3.14159
    g246: GeomPoint [constr] X=-83.75 Y=45.65 Z=0
    g247: ArcOfCircle CenterX=-69.65 CenterY=44.65 CenterZ=0 NormalX=0 NormalY=0 NormalZ=1 AngleXU=0 Radius=1 StartAngle=6e-16 EndAngle=1.5708
    g248: GeomPoint [constr] X=-68.65 Y=45.65 Z=0
    g249: ArcOfCircle CenterX=-69.65 CenterY=31.55 CenterZ=0 NormalX=0 NormalY=0 NormalZ=1 AngleXU=0 Radius=1 StartAngle=4.71239 EndAngle=6.28319
    g250: GeomPoint [constr] X=-68.65 Y=30.55 Z=0
    g251: ArcOfCircle CenterX=-82.75 CenterY=31.55 CenterZ=0 NormalX=0 NormalY=0 NormalZ=1 AngleXU=0 Radius=1 StartAngle=3.14159 EndAngle=4.71239
    g252: GeomPoint [constr] X=-83.75 Y=30.55 Z=0
    g253: ArcOfCircle CenterX=-63.7 CenterY=44.65 CenterZ=0 NormalX=0 NormalY=0 NormalZ=1 AngleXU=0 Radius=1 StartAngle=1.5708 EndAngle=3.14159
    g254: GeomPoint [constr] X=-64.7 Y=45.65 Z=0
    g255: ArcOfCircle CenterX=-50.6 CenterY=44.65 CenterZ=0 NormalX=0 NormalY=0 NormalZ=1 AngleXU=0 Radius=1 StartAngle=-1.8e-15 EndAngle=1.5708
    g256: GeomPoint [constr] X=-49.6 Y=45.65 Z=0
    g257: ArcOfCircle CenterX=-50.6 CenterY=31.55 CenterZ=0 NormalX=0 NormalY=0 NormalZ=1 AngleXU=0 Radius=1 StartAngle=4.71239 EndAngle=6.28319
    g258: GeomPoint [constr] X=-49.6 Y=30.55 Z=0
    g259: ArcOfCircle CenterX=-63.7 CenterY=31.55 CenterZ=0 NormalX=0 NormalY=0 NormalZ=1 AngleXU=0 Radius=1 StartAngle=3.14159 EndAngle=4.71239
    g260: GeomPoint [constr] X=-64.7 Y=30.55 Z=0
    g261: ArcOfCircle CenterX=-44.65 CenterY=44.65 CenterZ=0 NormalX=0 NormalY=0 NormalZ=1 AngleXU=0 Radius=1 StartAngle=1.5708 EndAngle=3.14159
    g262: GeomPoint [constr] X=-45.65 Y=45.65 Z=0
    g263: ArcOfCircle CenterX=-31.55 CenterY=44.65 CenterZ=0 NormalX=0 NormalY=0 NormalZ=1 AngleXU=0 Radius=1 StartAngle=3.4e-15 EndAngle=1.5708
    g264: GeomPoint [constr] X=-30.55 Y=45.65 Z=0
    g265: ArcOfCircle CenterX=-31.55 CenterY=31.55 CenterZ=0 NormalX=0 NormalY=0 NormalZ=1 AngleXU=0 Radius=1 StartAngle=4.71239 EndAngle=6.28319
    g266: GeomPoint [constr] X=-30.55 Y=30.55 Z=0
    g267: ArcOfCircle CenterX=-44.65 CenterY=31.55 CenterZ=0 NormalX=0 NormalY=0 NormalZ=1 AngleXU=0 Radius=1 StartAngle=3.14159 EndAngle=4.71239
    g268: GeomPoint [constr] X=-45.65 Y=30.55 Z=0
    g269: ArcOfCircle CenterX=-139.9 CenterY=25.6 CenterZ=0 NormalX=0 NormalY=0 NormalZ=1 AngleXU=0 Radius=1 StartAngle=1.5708 EndAngle=3.14159
    g270: GeomPoint [constr] X=-140.9 Y=26.6 Z=0
    g271: ArcOfCircle CenterX=-126.8 CenterY=25.6 CenterZ=0 NormalX=0 NormalY=0 NormalZ=1 AngleXU=0 Radius=1 StartAngle=2e-16 EndAngle=1.5708
    g272: GeomPoint [constr] X=-125.8 Y=26.6 Z=0
    g273: ArcOfCircle CenterX=-126.8 CenterY=12.5 CenterZ=0 NormalX=0 NormalY=0 NormalZ=1 AngleXU=0 Radius=1 StartAngle=4.71239 EndAngle=6.28319
    g274: GeomPoint [constr] X=-125.8 Y=11.5 Z=0
    g275: ArcOfCircle CenterX=-139.9 CenterY=12.5 CenterZ=0 NormalX=0 NormalY=0 NormalZ=1 AngleXU=0 Radius=1 StartAngle=3.14159 EndAngle=4.71239
    g276: GeomPoint [constr] X=-140.9 Y=11.5 Z=0
    g277: ArcOfCircle CenterX=-120.85 CenterY=25.6 CenterZ=0 NormalX=0 NormalY=0 NormalZ=1 AngleXU=0 Radius=1 StartAngle=1.5708 EndAngle=3.14159
    g278: GeomPoint [constr] X=-121.85 Y=26.6 Z=0
    g279: ArcOfCircle CenterX=-107.75 CenterY=25.6 CenterZ=0 NormalX=0 NormalY=0 NormalZ=1 AngleXU=0 Radius=1 StartAngle=0 EndAngle=1.5708
    g280: GeomPoint [constr] X=-106.75 Y=26.6 Z=0
    g281: ArcOfCircle CenterX=-107.75 CenterY=12.5 CenterZ=0 NormalX=0 NormalY=0 NormalZ=1 AngleXU=0 Radius=1 StartAngle=4.71239 EndAngle=6.28319
    g282: GeomPoint [constr] X=-106.75 Y=11.5 Z=0
    g283: ArcOfCircle CenterX=-120.85 CenterY=12.5 CenterZ=0 NormalX=0 NormalY=0 NormalZ=1 AngleXU=0 Radius=1 StartAngle=3.14159 EndAngle=4.71239
    g284: GeomPoint [constr] X=-121.85 Y=11.5 Z=0
    g285: ArcOfCircle CenterX=-101.8 CenterY=25.6 CenterZ=0 NormalX=0 NormalY=0 NormalZ=1 AngleXU=0 Radius=1 StartAngle=1.5708 EndAngle=3.14159
    g286: GeomPoint [constr] X=-102.8 Y=26.6 Z=0
    g287: ArcOfCircle CenterX=-88.7 CenterY=25.6 CenterZ=0 NormalX=0 NormalY=0 NormalZ=1 AngleXU=0 Radius=1 StartAngle=-1.8e-15 EndAngle=1.5708
    g288: GeomPoint [constr] X=-87.7 Y=26.6 Z=0
    g289: ArcOfCircle CenterX=-88.7 CenterY=12.5 CenterZ=0 NormalX=0 NormalY=0 NormalZ=1 AngleXU=0 Radius=1 StartAngle=4.71239 EndAngle=6.28319
    g290: GeomPoint [constr] X=-87.7 Y=11.5 Z=0
    g291: ArcOfCircle CenterX=-101.8 CenterY=12.5 CenterZ=0 NormalX=0 NormalY=0 NormalZ=1 AngleXU=0 Radius=1 StartAngle=3.14159 EndAngle=4.71239
    g292: GeomPoint [constr] X=-102.8 Y=11.5 Z=0
    g293: ArcOfCircle CenterX=-82.75 CenterY=25.6 CenterZ=0 NormalX=0 NormalY=0 NormalZ=1 AngleXU=0 Radius=1 StartAngle=1.5708 EndAngle=3.14159
    g294: GeomPoint [constr] X=-83.75 Y=26.6 Z=0
    g295: ArcOfCircle CenterX=-69.65 CenterY=25.6 CenterZ=0 NormalX=0 NormalY=0 NormalZ=1 AngleXU=0 Radius=1 StartAngle=1e-15 EndAngle=1.5708
    g296: GeomPoint [constr] X=-68.65 Y=26.6 Z=0
    g297: ArcOfCircle CenterX=-69.65 CenterY=12.5 CenterZ=0 NormalX=0 NormalY=0 NormalZ=1 AngleXU=0 Radius=1 StartAngle=4.71239 EndAngle=6.28319
    g298: GeomPoint [constr] X=-68.65 Y=11.5 Z=0
    g299: ArcOfCircle CenterX=-82.75 CenterY=12.5 CenterZ=0 NormalX=0 NormalY=0 NormalZ=1 AngleXU=0 Radius=1 StartAngle=3.14159 EndAngle=4.71239
    g300: GeomPoint [constr] X=-83.75 Y=11.5 Z=0
    g301: ArcOfCircle CenterX=-63.7 CenterY=25.6 CenterZ=0 NormalX=0 NormalY=0 NormalZ=1 AngleXU=0 Radius=1 StartAngle=1.5708 EndAngle=3.14159
    g302: GeomPoint [constr] X=-64.7 Y=26.6 Z=0
    g303: ArcOfCircle CenterX=-50.6 CenterY=25.6 CenterZ=0 NormalX=0 NormalY=0 NormalZ=1 AngleXU=0 Radius=1 StartAngle=0 EndAngle=1.5708
    g304: GeomPoint [constr] X=-49.6 Y=26.6 Z=0
    g305: ArcOfCircle CenterX=-50.6 CenterY=12.5 CenterZ=0 NormalX=0 NormalY=0 NormalZ=1 AngleXU=0 Radius=1 StartAngle=4.71239 EndAngle=6.28319
    g306: GeomPoint [constr] X=-49.6 Y=11.5 Z=0
    g307: ArcOfCircle CenterX=-63.7 CenterY=12.5 CenterZ=0 NormalX=0 NormalY=0 NormalZ=1 AngleXU=0 Radius=1 StartAngle=3.14159 EndAngle=4.71239
    g308: GeomPoint [constr] X=-64.7 Y=11.5 Z=0
    g309: ArcOfCircle CenterX=-44.65 CenterY=25.6 CenterZ=0 NormalX=0 NormalY=0 NormalZ=1 AngleXU=0 Radius=1 StartAngle=1.5708 EndAngle=3.14159
    g310: GeomPoint [constr] X=-45.65 Y=26.6 Z=0
    g311: ArcOfCircle CenterX=-31.55 CenterY=25.6 CenterZ=0 NormalX=0 NormalY=0 NormalZ=1 AngleXU=0 Radius=1 StartAngle=0 EndAngle=1.5708
    g312: GeomPoint [constr] X=-30.55 Y=26.6 Z=0
    g313: ArcOfCircle CenterX=-31.55 CenterY=12.5 CenterZ=0 NormalX=0 NormalY=0 NormalZ=1 AngleXU=0 Radius=1 StartAngle=4.71239 EndAngle=6.28319
    g314: GeomPoint [constr] X=-30.55 Y=11.5 Z=0
    g315: ArcOfCircle CenterX=-44.65 CenterY=12.5 CenterZ=0 NormalX=0 NormalY=0 NormalZ=1 AngleXU=0 Radius=1 StartAngle=3.14159 EndAngle=4.71239
    g316: GeomPoint [constr] X=-45.65 Y=11.5 Z=0
    g317: ArcOfCircle CenterX=-25.6 CenterY=25.6 CenterZ=0 NormalX=0 NormalY=0 NormalZ=1 AngleXU=0 Radius=1 StartAngle=1.5708 EndAngle=3.14159
    g318: GeomPoint [constr] X=-26.6 Y=26.6 Z=0
    g319: ArcOfCircle CenterX=-12.5 CenterY=25.6 CenterZ=0 NormalX=0 NormalY=0 NormalZ=1 AngleXU=0 Radius=1 StartAngle=-9e-16 EndAngle=1.5708
    g320: GeomPoint [constr] X=-11.5 Y=26.6 Z=0
    g321: ArcOfCircle CenterX=-12.5 CenterY=12.5 CenterZ=0 NormalX=0 NormalY=0 NormalZ=1 AngleXU=0 Radius=1 StartAngle=4.71239 EndAngle=6.28319
    g322: GeomPoint [constr] X=-11.5 Y=11.5 Z=0
    g323: ArcOfCircle CenterX=-25.6 CenterY=12.5 CenterZ=0 NormalX=0 NormalY=0 NormalZ=1 AngleXU=0 Radius=1 StartAngle=3.14159 EndAngle=4.71239
    g324: GeomPoint [constr] X=-26.6 Y=11.5 Z=0
  constraints (725):
    c: Horizontal(g0)
    c: Horizontal(g2)
    c: Vertical(g1)
    c: Vertical(g3)
    c: Symmetric(g312,g316,g4)
    c: Horizontal(g5)
    c: Horizontal(g7)
    c: Vertical(g6)
    c: Vertical(g8)
    c: Symmetric(g304,g308,g9)
    c: DistanceX(g9,g4) = 19.05
    c: Horizontal(g10)
    c: Horizontal(g12)
    c: Vertical(g11)
    c: Vertical(g13)
    c: Symmetric(g296,g300,g14)
    c: DistanceX(g14,g9) = 19.05
    c: Horizontal(g15)
    c: Horizontal(g17)
    c: Vertical(g16)
    c: Vertical(g18)
    c: Symmetric(g288,g292,g19)
    c: Horizontal(g20)
    c: Horizontal(g22)
    c: Vertical(g21)
    c: Vertical(g23)
    c: Symmetric(g280,g284,g24)
    c: DistanceX(g19,g14) = 19.05
    c: DistanceX(g24,g19) = 19.05
    c: Horizontal(g25)
    c: Horizontal(g27)
    c: Vertical(g26)
    c: Vertical(g28)
    c: Symmetric(g216,g220,g29)
    c: Horizontal(g30)
    c: Horizontal(g32)
    c: Vertical(g31)
    c: Vertical(g33)
    c: Symmetric(g208,g212,g34)
    c: Horizontal(g35)
    c: Horizontal(g37)
    c: Vertical(g36)
    c: Vertical(g38)
    c: Symmetric(g200,g204,g39)
    c: Horizontal(g40)
    c: Horizontal(g42)
    c: Vertical(g41)
    c: Vertical(g43)
    c: Symmetric(g192,g196,g44)
    c: Horizontal(g45)
    c: Horizontal(g47)
    c: Vertical(g46)
    c: Vertical(g48)
    c: Symmetric(g184,g188,g49)
    c: Horizontal(g50)
    c: Horizontal(g52)
    c: Vertical(g51)
    c: Vertical(g53)
    c: Symmetric(g264,g268,g54)
    c: Horizontal(g55)
    c: Horizontal(g57)
    c: Vertical(g56)
    c: Vertical(g58)
    c: Symmetric(g256,g260,g59)
    c: Horizontal(g60)
    c: Horizontal(g62)
    c: Vertical(g61)
    c: Vertical(g63)
    c: Symmetric(g248,g252,g64)
    c: Horizontal(g65)
    c: Horizontal(g67)
    c: Vertical(g66)
    c: Vertical(g68)
    c: Symmetric(g240,g244,g69)
    c: Horizontal(g70)
    c: Horizontal(g72)
    c: Vertical(g71)
    c: Vertical(g73)
    c: Symmetric(g232,g236,g74)
    c: DistanceY(g54,g29) = 19.05
    c: Horizontal(g75)
    c: Horizontal(g77)
    c: Vertical(g76)
    c: Vertical(g78)
    c: Symmetric(g144,g148,g79)
    c: Horizontal(g80)
    c: Horizontal(g82)
    c: Vertical(g81)
    c: Vertical(g83)
    c: Symmetric(g160,g164,g84)
    c: Horizontal(g85)
    c: Horizontal(g87)
    c: Vertical(g86)
    c: Vertical(g88)
    c: Symmetric(g128,g132,g89)
    c: Horizontal(g90)
    c: Horizontal(g92)
    c: Vertical(g91)
    c: Vertical(g93)
    c: Symmetric(g136,g140,g94)
    c: Horizontal(g95)
    c: Horizontal(g97)
    c: Vertical(g96)
    c: Vertical(g98)
    c: Symmetric(g152,g156,g99)
    c: Horizontal(g100)
    c: Horizontal(g102)
    c: Vertical(g101)
    c: Vertical(g103)
    c: Symmetric(g172,g168,g104)
    c: Horizontal(g105)
    c: Horizontal(g107)
    c: Vertical(g106)
    c: Vertical(g108)
    c: Symmetric(g180,g176,g109)
    c: Horizontal(g110)
    c: Horizontal(g112)
    c: Vertical(g111)
    c: Vertical(g113)
    c: Symmetric(g228,g224,g114)
    c: Horizontal(g115)
    c: Horizontal(g117)
    c: Vertical(g118)
    c: Symmetric(g276,g272,g119)
    c: DistanceY(g29,g104) = 19.05
    c: DistanceX(g119,g24) = 19.05
    c: Horizontal(g120)
    c: Horizontal(g122)
    c: Vertical(g121)
    c: Vertical(g123)
    c: Symmetric(g324,g320,g124)
    c: DistanceX(g4,g124) = 19.05
    c: DistanceX(g324,g322) = 15.1
    c: DistanceY(g324,g318) = 15.1
    c: Horizontal(g89,g94)
    c: Horizontal(g94,g79)
    c: Horizontal(g79,g99)
    c: Horizontal(g99,g84)
    c: Horizontal(g84,g104)
    c: Horizontal(g109,g49)
    c: Horizontal(g49,g44)
    c: Horizontal(g44,g39)
    c: Horizontal(g39,g34)
    c: Horizontal(g34,g29)
    c: Horizontal(g114,g74)
    c: Horizontal(g74,g69)
    c: Horizontal(g69,g64)
    c: Horizontal(g64,g59)
    c: Horizontal(g59,g54)
    c: Vertical(g89,g109)
    c: Vertical(g109,g114)
    c: Vertical(g114,g119)
    c: Vertical(g94,g49)
    c: Vertical(g49,g74)
    c: Vertical(g74,g24)
    c: Vertical(g79,g44)
    c: Vertical(g44,g69)
    c: Vertical(g69,g19)
    c: Vertical(g99,g39)
    c: Vertical(g39,g64)
    c: Vertical(g64,g14)
    c: Vertical(g84,g34)
    c: Vertical(g34,g59)
    c: Vertical(g59,g9)
    c: Vertical(g104,g29)
    c: Vertical(g29,g54)
    c: Vertical(g54,g4)
    c: DistanceX(g124,g-1) = 19.05
    c: Horizontal(g119,g24)
    c: Horizontal(g24,g19)
    c: Horizontal(g19,g14)
    c: Horizontal(g14,g9)
    c: Horizontal(g9,g4)
    c: Horizontal(g4,g124)
    c: DistanceY(g-1,g124) = 19.05
    c: DistanceY(g124,g54) = 19.05
    c: Vertical(g116)
    c: PointOnObject(g126,g87)
    c: PointOnObject(g126,g88)
    c: Tangent(g87,g125) = -1.5708
    c: Tangent(g88,g125) = -1.5708
    c: PointOnObject(g128,g86)
    c: PointOnObject(g128,g87)
    c: Tangent(g86,g127) = -1.5708
    c: Tangent(g87,g127) = -1.5708
    c: PointOnObject(g130,g85)
    c: PointOnObject(g130,g86)
    c: Tangent(g85,g129) = -1.5708
    c: Tangent(g86,g129) = -1.5708
    c: PointOnObject(g132,g85)
    c: PointOnObject(g132,g88)
    c: Tangent(g85,g131) = -1.5708
    c: Tangent(g88,g131) = -1.5708
    c: PointOnObject(g134,g92)
    c: PointOnObject(g134,g93)
    c: Tangent(g92,g133) = -1.5708
    c: Tangent(g93,g133) = -1.5708
    c: PointOnObject(g136,g91)
    c: PointOnObject(g136,g92)
    c: Tangent(g91,g135) = -1.5708
    c: Tangent(g92,g135) = -1.5708
    c: PointOnObject(g138,g90)
    c: PointOnObject(g138,g91)
    c: Tangent(g90,g137) = -1.5708
    c: Tangent(g91,g137) = -1.5708
    c: PointOnObject(g140,g90)
    c: PointOnObject(g140,g93)
    c: Tangent(g90,g139) = -1.5708
    c: Tangent(g93,g139) = -1.5708
    c: PointOnObject(g142,g77)
    c: PointOnObject(g142,g78)
    c: Tangent(g77,g141) = -1.5708
    c: Tangent(g78,g141) = -1.5708
    c: PointOnObject(g144,g76)
    c: PointOnObject(g144,g77)
    c: Tangent(g76,g143) = -1.5708
    c: Tangent(g77,g143) = -1.5708
    c: PointOnObject(g146,g75)
    c: PointOnObject(g146,g76)
    c: Tangent(g75,g145) = -1.5708
    c: Tangent(g76,g145) = -1.5708
    c: PointOnObject(g148,g75)
    c: PointOnObject(g148,g78)
    c: Tangent(g75,g147) = -1.5708
    c: Tangent(g78,g147) = -1.5708
    c: PointOnObject(g150,g97)
    c: PointOnObject(g150,g98)
    c: Tangent(g97,g149) = -1.5708
    c: Tangent(g98,g149) = -1.5708
    c: PointOnObject(g152,g96)
    c: PointOnObject(g152,g97)
    c: Tangent(g96,g151) = -1.5708
    c: Tangent(g97,g151) = -1.5708
    c: PointOnObject(g154,g95)
    c: PointOnObject(g154,g96)
    c: Tangent(g95,g153) = -1.5708
    c: Tangent(g96,g153) = -1.5708
    c: PointOnObject(g156,g95)
    c: PointOnObject(g156,g98)
    c: Tangent(g95,g155) = -1.5708
    c: Tangent(g98,g155) = -1.5708
    c: PointOnObject(g158,g82)
    c: PointOnObject(g158,g83)
    c: Tangent(g82,g157) = -1.5708
    c: Tangent(g83,g157) = -1.5708
    c: PointOnObject(g160,g81)
    c: PointOnObject(g160,g82)
    c: Tangent(g81,g159) = -1.5708
    c: Tangent(g82,g159) = -1.5708
    c: PointOnObject(g162,g80)
    c: PointOnObject(g162,g81)
    c: Tangent(g80,g161) = -1.5708
    c: Tangent(g81,g161) = -1.5708
    c: PointOnObject(g164,g80)
    c: PointOnObject(g164,g83)
    c: Tangent(g80,g163) = -1.5708
    c: Tangent(g83,g163) = -1.5708
    c: PointOnObject(g166,g100)
    c: PointOnObject(g166,g101)
    c: Tangent(g100,g165) = -1.5708
    c: Tangent(g101,g165) = -1.5708
    c: PointOnObject(g168,g100)
    c: PointOnObject(g168,g103)
    c: Tangent(g100,g167) = -1.5708
    c: Tangent(g103,g167) = -1.5708
    c: PointOnObject(g170,g102)
    c: PointOnObject(g170,g103)
    c: Tangent(g102,g169) = -1.5708
    c: Tangent(g103,g169) = -1.5708
    c: PointOnObject(g172,g101)
    c: PointOnObject(g172,g102)
    c: Tangent(g101,g171) = -1.5708
    c: Tangent(g102,g171) = -1.5708
    c: PointOnObject(g174,g105)
    c: PointOnObject(g174,g106)
    c: Tangent(g105,g173) = -1.5708
    c: Tangent(g106,g173) = -1.5708
    c: PointOnObject(g176,g105)
    c: PointOnObject(g176,g108)
    c: Tangent(g105,g175) = -1.5708
    c: Tangent(g108,g175) = -1.5708
    c: PointOnObject(g178,g107)
    c: PointOnObject(g178,g108)
    c: Tangent(g107,g177) = -1.5708
    c: Tangent(g108,g177) = -1.5708
    c: PointOnObject(g180,g106)
    c: PointOnObject(g180,g107)
    c: Tangent(g106,g179) = -1.5708
    c: Tangent(g107,g179) = -1.5708
    c: PointOnObject(g182,g47)
    c: PointOnObject(g182,g48)
    c: Tangent(g47,g181) = -1.5708
    c: Tangent(g48,g181) = -1.5708
    c: PointOnObject(g184,g46)
    c: PointOnObject(g184,g47)
    c: Tangent(g46,g183) = -1.5708
    c: Tangent(g47,g183) = -1.5708
    c: PointOnObject(g186,g45)
    c: PointOnObject(g186,g46)
    c: Tangent(g45,g185) = -1.5708
    c: Tangent(g46,g185) = -1.5708
    c: PointOnObject(g188,g45)
    c: PointOnObject(g188,g48)
    c: Tangent(g45,g187) = -1.5708
    c: Tangent(g48,g187) = -1.5708
    c: PointOnObject(g190,g42)
    c: PointOnObject(g190,g43)
    c: Tangent(g42,g189) = -1.5708
    c: Tangent(g43,g189) = -1.5708
    c: PointOnObject(g192,g41)
    c: PointOnObject(g192,g42)
    c: Tangent(g41,g191) = -1.5708
    c: Tangent(g42,g191) = -1.5708
    c: PointOnObject(g194,g40)
    c: PointOnObject(g194,g41)
    c: Tangent(g40,g193) = -1.5708
    c: Tangent(g41,g193) = -1.5708
    c: PointOnObject(g196,g40)
    c: PointOnObject(g196,g43)
    c: Tangent(g40,g195) = -1.5708
    c: Tangent(g43,g195) = -1.5708
    c: PointOnObject(g198,g37)
    c: PointOnObject(g198,g38)
    c: Tangent(g37,g197) = -1.5708
    c: Tangent(g38,g197) = -1.5708
    c: PointOnObject(g200,g36)
    c: PointOnObject(g200,g37)
    c: Tangent(g36,g199) = -1.5708
    c: Tangent(g37,g199) = -1.5708
    c: PointOnObject(g202,g35)
    c: PointOnObject(g202,g36)
    c: Tangent(g35,g201) = -1.5708
    c: Tangent(g36,g201) = -1.5708
    c: PointOnObject(g204,g35)
    c: PointOnObject(g204,g38)
    c: Tangent(g35,g203) = -1.5708
    c: Tangent(g38,g203) = -1.5708
    c: PointOnObject(g206,g32)
    c: PointOnObject(g206,g33)
    c: Tangent(g32,g205) = -1.5708
    c: Tangent(g33,g205) = -1.5708
    c: PointOnObject(g208,g31)
    c: PointOnObject(g208,g32)
    c: Tangent(g31,g207) = -1.5708
    c: Tangent(g32,g207) = -1.5708
    c: PointOnObject(g210,g30)
    c: PointOnObject(g210,g31)
    c: Tangent(g30,g209) = -1.5708
    c: Tangent(g31,g209) = -1.5708
    c: PointOnObject(g212,g30)
    c: PointOnObject(g212,g33)
    c: Tangent(g30,g211) = -1.5708
    c: Tangent(g33,g211) = -1.5708
    c: PointOnObject(g214,g27)
    c: PointOnObject(g214,g28)
    c: Tangent(g27,g213) = -1.5708
    c: Tangent(g28,g213) = -1.5708
    c: PointOnObject(g216,g26)
    c: PointOnObject(g216,g27)
    c: Tangent(g26,g215) = -1.5708
    c: Tangent(g27,g215) = -1.5708
    c: PointOnObject(g218,g25)
    c: PointOnObject(g218,g26)
    c: Tangent(g25,g217) = -1.5708
    c: Tangent(g26,g217) = -1.5708
    c: PointOnObject(g220,g25)
    c: PointOnObject(g220,g28)
    c: Tangent(g25,g219) = -1.5708
    c: Tangent(g28,g219) = -1.5708
    c: PointOnObject(g222,g110)
    c: PointOnObject(g222,g111)
    c: Tangent(g110,g221) = -1.5708
    c: Tangent(g111,g221) = -1.5708
    c: PointOnObject(g224,g110)
    c: PointOnObject(g224,g113)
    c: Tangent(g110,g223) = -1.5708
    c: Tangent(g113,g223) = -1.5708
    c: PointOnObject(g226,g112)
    c: PointOnObject(g226,g113)
    c: Tangent(g112,g225) = -1.5708
    c: Tangent(g113,g225) = -1.5708
    c: PointOnObject(g228,g111)
    c: PointOnObject(g228,g112)
    c: Tangent(g111,g227) = -1.5708
    c: Tangent(g112,g227) = -1.5708
    c: PointOnObject(g230,g72)
    c: PointOnObject(g230,g73)
    c: Tangent(g72,g229) = -1.5708
    c: Tangent(g73,g229) = -1.5708
    c: PointOnObject(g232,g71)
    c: PointOnObject(g232,g72)
    c: Tangent(g71,g231) = -1.5708
    c: Tangent(g72,g231) = -1.5708
    c: PointOnObject(g234,g70)
    c: PointOnObject(g234,g71)
    c: Tangent(g70,g233) = -1.5708
    c: Tangent(g71,g233) = -1.5708
    c: PointOnObject(g236,g70)
    c: PointOnObject(g236,g73)
    c: Tangent(g70,g235) = -1.5708
    c: Tangent(g73,g235) = -1.5708
    c: PointOnObject(g238,g67)
    c: PointOnObject(g238,g68)
    c: Tangent(g67,g237) = -1.5708
    c: Tangent(g68,g237) = -1.5708
    c: PointOnObject(g240,g66)
    c: PointOnObject(g240,g67)
    c: Tangent(g66,g239) = -1.5708
    c: Tangent(g67,g239) = -1.5708
    c: PointOnObject(g242,g65)
    c: PointOnObject(g242,g66)
    c: Tangent(g65,g241) = -1.5708
    c: Tangent(g66,g241) = -1.5708
    c: PointOnObject(g244,g65)
    c: PointOnObject(g244,g68)
    c: Tangent(g65,g243) = -1.5708
    c: Tangent(g68,g243) = -1.5708
    c: PointOnObject(g246,g62)
    c: PointOnObject(g246,g63)
    c: Tangent(g62,g245) = -1.5708
    c: Tangent(g63,g245) = -1.5708
    c: PointOnObject(g248,g61)
    c: PointOnObject(g248,g62)
    c: Tangent(g61,g247) = -1.5708
    c: Tangent(g62,g247) = -1.5708
    c: PointOnObject(g250,g60)
    c: PointOnObject(g250,g61)
    c: Tangent(g60,g249) = -1.5708
    c: Tangent(g61,g249) = -1.5708
    c: PointOnObject(g252,g60)
    c: PointOnObject(g252,g63)
    c: Tangent(g60,g251) = -1.5708
    c: Tangent(g63,g251) = -1.5708
    c: PointOnObject(g254,g57)
    c: PointOnObject(g254,g58)
    c: Tangent(g57,g253) = -1.5708
    c: Tangent(g58,g253) = -1.5708
    c: PointOnObject(g256,g56)
    c: PointOnObject(g256,g57)
    c: Tangent(g56,g255) = -1.5708
    c: Tangent(g57,g255) = -1.5708
    c: PointOnObject(g258,g55)
    c: PointOnObject(g258,g56)
    c: Tangent(g55,g257) = -1.5708
    c: Tangent(g56,g257) = -1.5708
    c: PointOnObject(g260,g55)
    c: PointOnObject(g260,g58)
    c: Tangent(g55,g259) = -1.5708
    c: Tangent(g58,g259) = -1.5708
    c: PointOnObject(g262,g52)
    c: PointOnObject(g262,g53)
    c: Tangent(g52,g261) = -1.5708
    c: Tangent(g53,g261) = -1.5708
    c: PointOnObject(g264,g51)
    c: PointOnObject(g264,g52)
    c: Tangent(g51,g263) = -1.5708
    c: Tangent(g52,g263) = -1.5708
    c: PointOnObject(g266,g50)
    c: PointOnObject(g266,g51)
    c: Tangent(g50,g265) = -1.5708
    c: Tangent(g51,g265) = -1.5708
    c: PointOnObject(g268,g50)
    c: PointOnObject(g268,g53)
    c: Tangent(g50,g267) = -1.5708
    c: Tangent(g53,g267) = -1.5708
    c: PointOnObject(g270,g115)
    c: PointOnObject(g270,g116)
    c: Tangent(g115,g269) = -1.5708
    c: Tangent(g116,g269) = -1.5708
    c: PointOnObject(g272,g115)
    c: PointOnObject(g272,g118)
    c: Tangent(g115,g271) = -1.5708
    c: Tangent(g118,g271) = -1.5708
    c: PointOnObject(g274,g117)
    c: PointOnObject(g274,g118)
    c: Tangent(g117,g273) = -1.5708
    c: Tangent(g118,g273) = -1.5708
    c: PointOnObject(g276,g116)
    c: PointOnObject(g276,g117)
    c: Tangent(g116,g275) = -1.5708
    c: Tangent(g117,g275) = -1.5708
    c: PointOnObject(g278,g22)
    c: PointOnObject(g278,g23)
    c: Tangent(g22,g277) = -1.5708
    c: Tangent(g23,g277) = -1.5708
    c: PointOnObject(g280,g21)
    c: PointOnObject(g280,g22)
    c: Tangent(g21,g279) = -1.5708
    c: Tangent(g22,g279) = -1.5708
    c: PointOnObject(g282,g20)
    c: PointOnObject(g282,g21)
    c: Tangent(g20,g281) = -1.5708
    c: Tangent(g21,g281) = -1.5708
    c: PointOnObject(g284,g20)
    c: PointOnObject(g284,g23)
    c: Tangent(g20,g283) = -1.5708
    c: Tangent(g23,g283) = -1.5708
    c: PointOnObject(g286,g17)
    c: PointOnObject(g286,g18)
    c: Tangent(g17,g285) = -1.5708
    c: Tangent(g18,g285) = -1.5708
    c: PointOnObject(g288,g16)
    c: PointOnObject(g288,g17)
    c: Tangent(g16,g287) = -1.5708
    c: Tangent(g17,g287) = -1.5708
    c: PointOnObject(g290,g15)
    c: PointOnObject(g290,g16)
    c: Tangent(g15,g289) = -1.5708
    c: Tangent(g16,g289) = -1.5708
    c: PointOnObject(g292,g15)
    c: PointOnObject(g292,g18)
    c: Tangent(g15,g291) = -1.5708
    c: Tangent(g18,g291) = -1.5708
    c: PointOnObject(g294,g12)
    c: PointOnObject(g294,g13)
    c: Tangent(g12,g293) = -1.5708
    c: Tangent(g13,g293) = -1.5708
    c: PointOnObject(g296,g11)
    c: PointOnObject(g296,g12)
    c: Tangent(g11,g295) = -1.5708
    c: Tangent(g12,g295) = -1.5708
    c: PointOnObject(g298,g10)
    c: PointOnObject(g298,g11)
    c: Tangent(g10,g297) = -1.5708
    c: Tangent(g11,g297) = -1.5708
    c: PointOnObject(g300,g10)
    c: PointOnObject(g300,g13)
    c: Tangent(g10,g299) = -1.5708
    c: Tangent(g13,g299) = -1.5708
    c: PointOnObject(g302,g7)
    c: PointOnObject(g302,g8)
    c: Tangent(g7,g301) = -1.5708
    c: Tangent(g8,g301) = -1.5708
    c: PointOnObject(g304,g6)
    c: PointOnObject(g304,g7)
    c: Tangent(g6,g303) = -1.5708
    c: Tangent(g7,g303) = -1.5708
    c: PointOnObject(g306,g5)
    c: PointOnObject(g306,g6)
    c: Tangent(g5,g305) = -1.5708
    c: Tangent(g6,g305) = -1.5708
    c: PointOnObject(g308,g5)
    c: PointOnObject(g308,g8)
    c: Tangent(g5,g307) = -1.5708
    c: Tangent(g8,g307) = -1.5708
    c: PointOnObject(g310,g2)
    c: PointOnObject(g310,g3)
    c: Tangent(g2,g309) = -1.5708
    c: Tangent(g3,g309) = -1.5708
    c: PointOnObject(g312,g1)
    c: PointOnObject(g312,g2)
    c: Tangent(g1,g311) = -1.5708
    c: Tangent(g2,g311) = -1.5708
    c: PointOnObject(g314,g0)
    c: PointOnObject(g314,g1)
    c: Tangent(g0,g313) = -1.5708
    c: Tangent(g1,g313) = -1.5708
    c: PointOnObject(g316,g0)
    c: PointOnObject(g316,g3)
    c: Tangent(g0,g315) = -1.5708
    c: Tangent(g3,g315) = -1.5708
    c: PointOnObject(g318,g120)
    c: PointOnObject(g318,g121)
    c: Tangent(g120,g317) = -1.5708
    c: Tangent(g121,g317) = -1.5708
    c: PointOnObject(g320,g120)
    c: PointOnObject(g320,g123)
    c: Tangent(g120,g319) = -1.5708
    c: Tangent(g123,g319) = -1.5708
    c: PointOnObject(g322,g122)
    c: PointOnObject(g322,g123)
    c: Tangent(g122,g321) = -1.5708
    c: Tangent(g123,g321) = -1.5708
    c: PointOnObject(g324,g121)
    c: PointOnObject(g324,g122)
    c: Tangent(g121,g323) = -1.5708
    c: Tangent(g122,g323) = -1.5708
    c: Equal(g125,g127)
    c: Equal(g127,g129)
    c: Equal(g129,g131)
    c: Equal(g133,g135)
    c: Equal(g135,g137)
    c: Equal(g137,g139)
    c: Equal(g141,g143)
    c: Equal(g143,g145)
    c: Equal(g145,g147)
    c: Equal(g149,g151)
    c: Equal(g151,g153)
    c: Equal(g153,g155)
    c: Equal(g157,g159)
    c: Equal(g159,g161)
    c: Equal(g161,g163)
    c: Equal(g165,g167)
    c: Equal(g167,g169)
    c: Equal(g169,g171)
    c: Equal(g173,g175)
    c: Equal(g175,g177)
    c: Equal(g177,g179)
    c: Equal(g181,g183)
    c: Equal(g183,g185)
    c: Equal(g185,g187)
    c: Equal(g189,g191)
    c: Equal(g191,g193)
    c: Equal(g193,g195)
    c: Equal(g197,g199)
    c: Equal(g199,g201)
    c: Equal(g201,g203)
    c: Equal(g205,g207)
    c: Equal(g207,g209)
    c: Equal(g209,g211)
    c: Equal(g213,g215)
    c: Equal(g215,g217)
    c: Equal(g217,g219)
    c: Equal(g221,g223)
    c: Equal(g223,g225)
    c: Equal(g225,g227)
    c: Equal(g229,g231)
    c: Equal(g231,g233)
    c: Equal(g233,g235)
    c: Equal(g237,g239)
    c: Equal(g239,g241)
    c: Equal(g241,g243)
    c: Equal(g245,g247)
    c: Equal(g247,g249)
    c: Equal(g249,g251)
    c: Equal(g253,g255)
    c: Equal(g255,g257)
    c: Equal(g257,g259)
    c: Equal(g261,g263)
    c: Equal(g263,g265)
    c: Equal(g265,g267)
    c: Equal(g269,g271)
    c: Equal(g271,g273)
    c: Equal(g273,g275)
    c: Equal(g277,g279)
    c: Equal(g279,g281)
    c: Equal(g281,g283)
    c: Equal(g285,g287)
    c: Equal(g287,g289)
    c: Equal(g289,g291)
    c: Equal(g293,g295)
    c: Equal(g295,g297)
    c: Equal(g297,g299)
    c: Equal(g301,g303)
    c: Equal(g303,g305)
    c: Equal(g305,g307)
    c: Equal(g309,g311)
    c: Equal(g311,g313)
    c: Equal(g313,g315)
    c: Equal(g317,g319)
    c: Equal(g319,g321)
    c: Equal(g321,g323)
    c: Equal(g125,g133)
    c: Equal(g133,g141)
    c: Equal(g141,g149)
    c: Equal(g149,g157)
    c: Equal(g157,g165)
    c: Equal(g173,g181)
    c: Equal(g181,g189)
    c: Equal(g189,g197)
    c: Equal(g197,g205)
    c: Equal(g205,g213)
    c: Equal(g221,g229)
    c: Equal(g229,g237)
    c: Equal(g237,g245)
    c: Equal(g245,g253)
    c: Equal(g253,g261)
    c: Equal(g269,g277)
    c: Equal(g277,g285)
    c: Equal(g285,g293)
    c: Equal(g293,g301)
    c: Equal(g301,g309)
    c: Equal(g309,g317)
    c: Equal(g165,g213)
    c: Equal(g213,g261)
    c: Equal(g261,g309)
    c: Equal(g88,g93)
    c: Equal(g93,g78)
    c: Equal(g78,g98)
    c: Equal(g98,g83)
    c: Equal(g83,g101)
    c: Equal(g106,g48)
    c: Equal(g48,g43)
    c: Equal(g43,g38)
    c: Equal(g38,g33)
    c: Equal(g33,g28)
    c: Equal(g111,g73)
    c: Equal(g73,g68)
    c: Equal(g68,g63)
    c: Equal(g63,g58)
    c: Equal(g58,g53)
    c: Equal(g116,g23)
    c: Equal(g23,g18)
    c: Equal(g18,g13)
    c: Equal(g13,g8)
    c: Equal(g8,g3)
    c: Equal(g3,g121)
    c: Equal(g101,g28)
    c: Equal(g28,g53)
    c: Equal(g53,g3)
    c: Equal(g87,g92)
    c: Equal(g92,g77)
    c: Equal(g77,g97)
    c: Equal(g97,g82)
    c: Equal(g82,g100)
    c: Equal(g105,g47)
    c: Equal(g47,g42)
    c: Equal(g42,g37)
    c: Equal(g37,g32)
    c: Equal(g32,g27)
    c: Equal(g110,g72)
    c: Equal(g72,g67)
    c: Equal(g67,g62)
    c: Equal(g62,g57)
    c: Equal(g57,g52)
    c: Equal(g115,g22)
    c: Equal(g22,g17)
    c: Equal(g17,g12)
    c: Equal(g12,g7)
    c: Equal(g7,g2)
    c: Equal(g2,g120)
    c: Equal(g100,g27)
    c: Equal(g27,g52)
    c: Equal(g52,g2)
    c: Radius(g317) = 1
FEATURE [Sketcher::SketchObject] Sketch003  label="TL-PCB"
  ArcFitTolerance = 1e-06
  AttachmentSupport = -> [XY_Plane]
  FullyConstrained = true
  MakeInternals = false
  MapMode = 5
  expr: Constraints[10] = VarSet.Top_PcbY
  expr: Constraints[11] = VarSet.Top_PcbX
  expr: Constraints[12] = 2.5 * 19.05
  expr: Constraints[9] = 4 * 19.05
  sketch-geometry (5):
    g0: LineSegment StartX=-142.5 StartY=85.375 StartZ=0 EndX=-142.5 EndY=9.875 EndZ=0
    g1: LineSegment StartX=-142.5 StartY=9.875 StartZ=0 EndX=-9.9 EndY=9.875 EndZ=0
    g2: LineSegment StartX=-9.9 StartY=9.875 StartZ=0 EndX=-9.9 EndY=85.375 EndZ=0
    g3: LineSegment StartX=-9.9 StartY=85.375 StartZ=0 EndX=-142.5 EndY=85.375 EndZ=0
    g4: GeomPoint [constr] X=-76.2 Y=47.625 Z=0
  constraints (13):
    c: Coincident(g0,g1)
    c: Coincident(g1,g2)
    c: Coincident(g2,g3)
    c: Coincident(g3,g0)
    c: Vertical(g0)
    c: Vertical(g2)
    c: Horizontal(g1)
    c: Horizontal(g3)
    c: Symmetric(g2,g0,g4)
    c: DistanceX(g4,g-1) = 76.2
    c: DistanceY(g0,g0) = 75.5
    c: DistanceX(g1,g1) = 132.6
    c: DistanceY(g-1,g4) = 47.625
FEATURE [Sketcher::SketchObject] Sketch004  label="TL-ScrewPostIn"
  ArcFitTolerance = 1e-06
  AttachmentSupport = -> [XY_Plane]
  FullyConstrained = true
  MakeInternals = false
  MapMode = 5
  expr: Constraints[15] = VarSet.Screw_PostInD
  expr: Constraints[16] = 1.5 * 19.05 mm
  expr: Constraints[17] = 19.05 mm / 2
  expr: Constraints[48] = 2.5 * 19.05 mm
  expr: Constraints[49] = 19.05 mm + VarSet.Screw_RearAdd
  sketch-geometry (17):
    g0: Circle CenterX=-123.825 CenterY=28.575 CenterZ=0 NormalX=0 NormalY=0 NormalZ=1 AngleXU=0 Radius=0.95
    g1: Circle CenterX=-123.825 CenterY=66.675 CenterZ=0 NormalX=0 NormalY=0 NormalZ=1 AngleXU=0 Radius=0.95
    g2: Circle CenterX=-85.725 CenterY=66.675 CenterZ=0 NormalX=0 NormalY=0 NormalZ=1 AngleXU=0 Radius=0.95
    g3: Circle CenterX=-85.725 CenterY=28.575 CenterZ=0 NormalX=0 NormalY=0 NormalZ=1 AngleXU=0 Radius=0.95
    g4: Circle CenterX=-47.625 CenterY=28.575 CenterZ=0 NormalX=0 NormalY=0 NormalZ=1 AngleXU=0 Radius=0.95
    g5: Circle CenterX=-47.625 CenterY=66.675 CenterZ=0 NormalX=0 NormalY=0 NormalZ=1 AngleXU=0 Radius=0.95
    g6: Circle CenterX=-123.825 CenterY=9.525 CenterZ=0 NormalX=0 NormalY=0 NormalZ=1 AngleXU=0 Radius=0.95
    g7: Circle CenterX=-104.775 CenterY=9.525 CenterZ=0 NormalX=0 NormalY=0 NormalZ=1 AngleXU=0 Radius=0.95
    g8: Circle CenterX=-85.725 CenterY=9.525 CenterZ=0 NormalX=0 NormalY=0 NormalZ=1 AngleXU=0 Radius=0.95
    g9: Circle CenterX=-66.675 CenterY=9.525 CenterZ=0 NormalX=0 NormalY=0 NormalZ=1 AngleXU=0 Radius=0.95
    g10: Circle CenterX=-47.625 CenterY=9.525 CenterZ=0 NormalX=0 NormalY=0 NormalZ=1 AngleXU=0 Radius=0.95
    g11: Circle CenterX=-28.575 CenterY=9.525 CenterZ=0 NormalX=0 NormalY=0 NormalZ=1 AngleXU=0 Radius=0.95
    g12: Circle CenterX=-123.825 CenterY=88.225 CenterZ=0 NormalX=0 NormalY=0 NormalZ=1 AngleXU=0 Radius=0.95
    g13: Circle CenterX=-104.775 CenterY=88.225 CenterZ=0 NormalX=0 NormalY=0 NormalZ=1 AngleXU=0 Radius=0.95
    g14: Circle CenterX=-85.725 CenterY=88.225 CenterZ=0 NormalX=0 NormalY=0 NormalZ=1 AngleXU=0 Radius=0.95
    g15: Circle CenterX=-66.675 CenterY=88.225 CenterZ=0 NormalX=0 NormalY=0 NormalZ=1 AngleXU=0 Radius=0.95
    g16: Circle CenterX=-47.625 CenterY=88.225 CenterZ=0 NormalX=0 NormalY=0 NormalZ=1 AngleXU=0 Radius=0.95
  constraints (51):
    c: Horizontal(g6,g7)
    c: Horizontal(g7,g8)
    c: Horizontal(g8,g9)
    c: Horizontal(g9,g10)
    c: Horizontal(g10,g11)
    c: DistanceX(g10,g11) = 19.05
    c: DistanceX(g9,g10) = 19.05
    c: DistanceX(g8,g9) = 19.05
    c: DistanceX(g7,g8) = 19.05
    c: DistanceX(g6,g7) = 19.05
    c: Equal(g6,g7)
    c: Equal(g7,g8)
    c: Equal(g8,g9)
    c: Equal(g9,g10)
    c: Equal(g10,g11)
    c: Diameter(g11) = 1.9
    c: DistanceX(g11,g-1) = 28.575
    c: DistanceY(g-1,g11) = 9.525
    c: DistanceY(g11,g4) = 19.05
    c: DistanceY(g4,g5) = 38.1
    c: Horizontal(g1,g2)
    c: Horizontal(g2,g5)
    c: Horizontal(g0,g3)
    c: Horizontal(g3,g4)
    c: Vertical(g1,g0)
    c: Vertical(g0,g6)
    c: Vertical(g2,g3)
    c: Vertical(g3,g8)
    c: Vertical(g5,g4)
    c: Vertical(g4,g10)
    c: Equal(g1,g2)
    c: Equal(g2,g5)
    c: Equal(g0,g3)
    c: Equal(g3,g4)
    c: Equal(g5,g4)
    c: Equal(g4,g10)
    c: Horizontal(g12,g13)
    c: Horizontal(g13,g14)
    c: Horizontal(g14,g15)
    c: Equal(g12,g13)
    c: Equal(g13,g14)
    c: Equal(g14,g15)
    c: Equal(g15,g16)
    c: Horizontal(g15,g16)
    c: DistanceX(g12,g13) = 19.05
    c: DistanceX(g13,g14) = 19.05
    c: DistanceX(g14,g15) = 19.05
    c: DistanceX(g15,g16) = 19.05
    c: DistanceX(g16,g-1) = 47.625
    c: DistanceY(g5,g16) = 21.55
    c: Equal(g16,g5)
FEATURE [Image::ImagePlane] L  label="Photo-L"
  Placement = pos=(-75.9,47.65,-0.1) rot=(0,-1,0;3.14159rad)
  XSize = 133
  YSize = 74.96
FEATURE [Image::ImagePlane] R  label="Photo-R"
  Placement = pos=(76,47.62,-0.1) rot=(0,-1,0;3.14159rad)
  XSize = 132.01
  YSize = 75
FEATURE [Sketcher::SketchObject] Sketch007  label="TR-Lo"
  ArcFitTolerance = 1e-06
  AttachmentSupport = -> [XY_Plane002]
  FullyConstrained = true
  MakeInternals = false
  MapMode = 5
  expr: Constraints[197] = VarSet.Top_LoXY
  expr: Constraints[198] = VarSet.Top_LoXY
  sketch-geometry (125):
    g0: LineSegment StartX=45.4 StartY=26.35 StartZ=0 EndX=30.8 EndY=26.35 EndZ=0
    g1: LineSegment StartX=30.8 StartY=26.35 StartZ=0 EndX=30.8 EndY=11.75 EndZ=0
    g2: LineSegment StartX=30.8 StartY=11.75 StartZ=0 EndX=45.4 EndY=11.75 EndZ=0
    g3: LineSegment StartX=45.4 StartY=11.75 StartZ=0 EndX=45.4 EndY=26.35 EndZ=0
    g4: GeomPoint [constr] X=38.1 Y=19.05 Z=0
    g5: LineSegment StartX=64.45 StartY=26.35 StartZ=0 EndX=49.85 EndY=26.35 EndZ=0
    g6: LineSegment StartX=49.85 StartY=26.35 StartZ=0 EndX=49.85 EndY=11.75 EndZ=0
    g7: LineSegment StartX=49.85 StartY=11.75 StartZ=0 EndX=64.45 EndY=11.75 EndZ=0
    g8: LineSegment StartX=64.45 StartY=11.75 StartZ=0 EndX=64.45 EndY=26.35 EndZ=0
    g9: GeomPoint [constr] X=57.15 Y=19.05 Z=0
    g10: LineSegment StartX=45.4 StartY=45.4 StartZ=0 EndX=30.8 EndY=45.4 EndZ=0
    g11: LineSegment StartX=30.8 StartY=45.4 StartZ=0 EndX=30.8 EndY=30.8 EndZ=0
    g12: LineSegment StartX=30.8 StartY=30.8 StartZ=0 EndX=45.4 EndY=30.8 EndZ=0
    g13: LineSegment StartX=45.4 StartY=30.8 StartZ=0 EndX=45.4 EndY=45.4 EndZ=0
    g14: GeomPoint [constr] X=38.1 Y=38.1 Z=0
    g15: LineSegment StartX=83.5 StartY=26.35 StartZ=0 EndX=68.9 EndY=26.35 EndZ=0
    g16: LineSegment StartX=68.9 StartY=26.35 StartZ=0 EndX=68.9 EndY=11.75 EndZ=0
    g17: LineSegment StartX=68.9 StartY=11.75 StartZ=0 EndX=83.5 EndY=11.75 EndZ=0
    g18: LineSegment StartX=83.5 StartY=11.75 StartZ=0 EndX=83.5 EndY=26.35 EndZ=0
    g19: GeomPoint [constr] X=76.2 Y=19.05 Z=0
    g20: LineSegment StartX=102.55 StartY=26.35 StartZ=0 EndX=87.95 EndY=26.35 EndZ=0
    g21: LineSegment StartX=87.95 StartY=26.35 StartZ=0 EndX=87.95 EndY=11.75 EndZ=0
    g22: LineSegment StartX=87.95 StartY=11.75 StartZ=0 EndX=102.55 EndY=11.75 EndZ=0
    g23: LineSegment StartX=102.55 StartY=11.75 StartZ=0 EndX=102.55 EndY=26.35 EndZ=0
    g24: GeomPoint [constr] X=95.25 Y=19.05 Z=0
    g25: LineSegment StartX=64.45 StartY=45.4 StartZ=0 EndX=49.85 EndY=45.4 EndZ=0
    g26: LineSegment StartX=49.85 StartY=45.4 StartZ=0 EndX=49.85 EndY=30.8 EndZ=0
    g27: LineSegment StartX=49.85 StartY=30.8 StartZ=0 EndX=64.45 EndY=30.8 EndZ=0
    g28: LineSegment StartX=64.45 StartY=30.8 StartZ=0 EndX=64.45 EndY=45.4 EndZ=0
    g29: GeomPoint [constr] X=57.15 Y=38.1 Z=0
    g30: LineSegment StartX=83.5 StartY=45.4 StartZ=0 EndX=68.9 EndY=45.4 EndZ=0
    g31: LineSegment StartX=68.9 StartY=45.4 StartZ=0 EndX=68.9 EndY=30.8 EndZ=0
    g32: LineSegment StartX=68.9 StartY=30.8 StartZ=0 EndX=83.5 EndY=30.8 EndZ=0
    g33: LineSegment StartX=83.5 StartY=30.8 StartZ=0 EndX=83.5 EndY=45.4 EndZ=0
    g34: GeomPoint [constr] X=76.2 Y=38.1 Z=0
    g35: LineSegment StartX=121.6 StartY=26.35 StartZ=0 EndX=107 EndY=26.35 EndZ=0
    g36: LineSegment StartX=107 StartY=26.35 StartZ=0 EndX=107 EndY=11.75 EndZ=0
    g37: LineSegment StartX=107 StartY=11.75 StartZ=0 EndX=121.6 EndY=11.75 EndZ=0
    g38: LineSegment StartX=121.6 StartY=11.75 StartZ=0 EndX=121.6 EndY=26.35 EndZ=0
    g39: GeomPoint [constr] X=114.3 Y=19.05 Z=0
    g40: LineSegment StartX=102.55 StartY=45.4 StartZ=0 EndX=87.95 EndY=45.4 EndZ=0
    g41: LineSegment StartX=87.95 StartY=45.4 StartZ=0 EndX=87.95 EndY=30.8 EndZ=0
    g42: LineSegment StartX=87.95 StartY=30.8 StartZ=0 EndX=102.55 EndY=30.8 EndZ=0
    g43: LineSegment StartX=102.55 StartY=30.8 StartZ=0 EndX=102.55 EndY=45.4 EndZ=0
    g44: GeomPoint [constr] X=95.25 Y=38.1 Z=0
    g45: LineSegment StartX=45.4 StartY=64.45 StartZ=0 EndX=30.8 EndY=64.45 EndZ=0
    g46: LineSegment StartX=30.8 StartY=64.45 StartZ=0 EndX=30.8 EndY=49.85 EndZ=0
    g47: LineSegment StartX=30.8 StartY=49.85 StartZ=0 EndX=45.4 EndY=49.85 EndZ=0
    g48: LineSegment StartX=45.4 StartY=49.85 StartZ=0 EndX=45.4 EndY=64.45 EndZ=0
    g49: GeomPoint [constr] X=38.1 Y=57.15 Z=0
    g50: LineSegment StartX=64.45 StartY=64.45 StartZ=0 EndX=49.85 EndY=64.45 EndZ=0
    g51: LineSegment StartX=49.85 StartY=64.45 StartZ=0 EndX=49.85 EndY=49.85 EndZ=0
    g52: LineSegment StartX=49.85 StartY=49.85 StartZ=0 EndX=64.45 EndY=49.85 EndZ=0
    g53: LineSegment StartX=64.45 StartY=49.85 StartZ=0 EndX=64.45 EndY=64.45 EndZ=0
    g54: GeomPoint [constr] X=57.15 Y=57.15 Z=0
    g55: LineSegment StartX=83.5 StartY=64.45 StartZ=0 EndX=68.9 EndY=64.45 EndZ=0
    g56: LineSegment StartX=68.9 StartY=64.45 StartZ=0 EndX=68.9 EndY=49.85 EndZ=0
    g57: LineSegment StartX=68.9 StartY=49.85 StartZ=0 EndX=83.5 EndY=49.85 EndZ=0
    g58: LineSegment StartX=83.5 StartY=49.85 StartZ=0 EndX=83.5 EndY=64.45 EndZ=0
    g59: GeomPoint [constr] X=76.2 Y=57.15 Z=0
    g60: LineSegment StartX=102.55 StartY=64.45 StartZ=0 EndX=87.95 EndY=64.45 EndZ=0
    g61: LineSegment StartX=87.95 StartY=64.45 StartZ=0 EndX=87.95 EndY=49.85 EndZ=0
    g62: LineSegment StartX=87.95 StartY=49.85 StartZ=0 EndX=102.55 EndY=49.85 EndZ=0
    g63: LineSegment StartX=102.55 StartY=49.85 StartZ=0 EndX=102.55 EndY=64.45 EndZ=0
    g64: GeomPoint [constr] X=95.25 Y=57.15 Z=0
    g65: LineSegment StartX=45.4 StartY=83.5 StartZ=0 EndX=30.8 EndY=83.5 EndZ=0
    g66: LineSegment StartX=30.8 StartY=83.5 StartZ=0 EndX=30.8 EndY=68.9 EndZ=0
    g67: LineSegment StartX=30.8 StartY=68.9 StartZ=0 EndX=45.4 EndY=68.9 EndZ=0
    g68: LineSegment StartX=45.4 StartY=68.9 StartZ=0 EndX=45.4 EndY=83.5 EndZ=0
    g69: GeomPoint [constr] X=38.1 Y=76.2 Z=0
    g70: LineSegment StartX=64.45 StartY=83.5 StartZ=0 EndX=49.85 EndY=83.5 EndZ=0
    g71: LineSegment StartX=49.85 StartY=83.5 StartZ=0 EndX=49.85 EndY=68.9 EndZ=0
    g72: LineSegment StartX=49.85 StartY=68.9 StartZ=0 EndX=64.45 EndY=68.9 EndZ=0
    g73: LineSegment StartX=64.45 StartY=68.9 StartZ=0 EndX=64.45 EndY=83.5 EndZ=0
    g74: GeomPoint [constr] X=57.15 Y=76.2 Z=0
    g75: LineSegment StartX=83.5 StartY=83.5 StartZ=0 EndX=68.9 EndY=83.5 EndZ=0
    g76: LineSegment StartX=68.9 StartY=83.5 StartZ=0 EndX=68.9 EndY=68.9 EndZ=0
    g77: LineSegment StartX=68.9 StartY=68.9 StartZ=0 EndX=83.5 EndY=68.9 EndZ=0
    g78: LineSegment StartX=83.5 StartY=68.9 StartZ=0 EndX=83.5 EndY=83.5 EndZ=0
    g79: GeomPoint [constr] X=76.2 Y=76.2 Z=0
    g80: LineSegment StartX=102.55 StartY=83.5 StartZ=0 EndX=87.95 EndY=83.5 EndZ=0
    g81: LineSegment StartX=87.95 StartY=83.5 StartZ=0 EndX=87.95 EndY=68.9 EndZ=0
    g82: LineSegment StartX=87.95 StartY=68.9 StartZ=0 EndX=102.55 EndY=68.9 EndZ=0
    g83: LineSegment StartX=102.55 StartY=68.9 StartZ=0 EndX=102.55 EndY=83.5 EndZ=0
    g84: GeomPoint [constr] X=95.25 Y=76.2 Z=0
    g85: LineSegment StartX=121.6 StartY=83.5 StartZ=0 EndX=107 EndY=83.5 EndZ=0
    g86: LineSegment StartX=107 StartY=83.5 StartZ=0 EndX=107 EndY=68.9 EndZ=0
    g87: LineSegment StartX=107 StartY=68.9 StartZ=0 EndX=121.6 EndY=68.9 EndZ=0
    g88: LineSegment StartX=121.6 StartY=68.9 StartZ=0 EndX=121.6 EndY=83.5 EndZ=0
    g89: GeomPoint [constr] X=114.3 Y=76.2 Z=0
    g90: LineSegment StartX=121.6 StartY=64.45 StartZ=0 EndX=107 EndY=64.45 EndZ=0
    g91: LineSegment StartX=107 StartY=64.45 StartZ=0 EndX=107 EndY=49.85 EndZ=0
    g92: LineSegment StartX=107 StartY=49.85 StartZ=0 EndX=121.6 EndY=49.85 EndZ=0
    g93: LineSegment StartX=121.6 StartY=49.85 StartZ=0 EndX=121.6 EndY=64.45 EndZ=0
    g94: GeomPoint [constr] X=114.3 Y=57.15 Z=0
    g95: LineSegment StartX=121.6 StartY=45.4 StartZ=0 EndX=107 EndY=45.4 EndZ=0
    g96: LineSegment StartX=107 StartY=45.4 StartZ=0 EndX=107 EndY=30.8 EndZ=0
    g97: LineSegment StartX=107 StartY=30.8 StartZ=0 EndX=121.6 EndY=30.8 EndZ=0
    g98: LineSegment StartX=121.6 StartY=30.8 StartZ=0 EndX=121.6 EndY=45.4 EndZ=0
    g99: GeomPoint [constr] X=114.3 Y=38.1 Z=0
    g100: LineSegment StartX=140.65 StartY=26.35 StartZ=0 EndX=126.05 EndY=26.35 EndZ=0
    g101: LineSegment StartX=126.05 StartY=26.35 StartZ=0 EndX=126.05 EndY=11.75 EndZ=0
    g102: LineSegment StartX=126.05 StartY=11.75 StartZ=0 EndX=140.65 EndY=11.75 EndZ=0
    g103: LineSegment StartX=140.65 StartY=11.75 StartZ=0 EndX=140.65 EndY=26.35 EndZ=0
    g104: GeomPoint [constr] X=133.35 Y=19.05 Z=0
    g105: LineSegment StartX=26.35 StartY=26.35 StartZ=0 EndX=11.75 EndY=26.35 EndZ=0
    g106: LineSegment StartX=11.75 StartY=26.35 StartZ=0 EndX=11.75 EndY=11.75 EndZ=0
    g107: LineSegment StartX=11.75 StartY=11.75 StartZ=0 EndX=26.35 EndY=11.75 EndZ=0
    g108: LineSegment StartX=26.35 StartY=11.75 StartZ=0 EndX=26.35 EndY=26.35 EndZ=0
    g109: GeomPoint [constr] X=19.05 Y=19.05 Z=0
    g110: LineSegment StartX=140.65 StartY=45.4 StartZ=0 EndX=126.05 EndY=45.4 EndZ=0
    g111: LineSegment StartX=126.05 StartY=45.4 StartZ=0 EndX=126.05 EndY=30.8 EndZ=0
    g112: LineSegment StartX=126.05 StartY=30.8 StartZ=0 EndX=140.65 EndY=30.8 EndZ=0
    g113: LineSegment StartX=140.65 StartY=30.8 StartZ=0 EndX=140.65 EndY=45.4 EndZ=0
    g114: GeomPoint [constr] X=133.35 Y=38.1 Z=0
    g115: LineSegment StartX=140.65 StartY=64.45 StartZ=0 EndX=126.05 EndY=64.45 EndZ=0
    g116: LineSegment StartX=126.05 StartY=64.45 StartZ=0 EndX=126.05 EndY=49.85 EndZ=0
    g117: LineSegment StartX=126.05 StartY=49.85 StartZ=0 EndX=140.65 EndY=49.85 EndZ=0
    g118: LineSegment StartX=140.65 StartY=49.85 StartZ=0 EndX=140.65 EndY=64.45 EndZ=0
    g119: GeomPoint [constr] X=133.35 Y=57.15 Z=0
    g120: LineSegment StartX=140.65 StartY=83.5 StartZ=0 EndX=126.05 EndY=83.5 EndZ=0
    g121: LineSegment StartX=126.05 StartY=83.5 StartZ=0 EndX=126.05 EndY=68.9 EndZ=0
    g122: LineSegment StartX=126.05 StartY=68.9 StartZ=0 EndX=140.65 EndY=68.9 EndZ=0
    g123: LineSegment StartX=140.65 StartY=68.9 StartZ=0 EndX=140.65 EndY=83.5 EndZ=0
    g124: GeomPoint [constr] X=133.35 Y=76.2 Z=0
  constraints (325):
    c: Coincident(g0,g1)
    c: Coincident(g1,g2)
    c: Coincident(g2,g3)
    c: Coincident(g3,g0)
    c: Horizontal(g0)
    c: Horizontal(g2)
    c: Vertical(g1)
    c: Vertical(g3)
    c: Symmetric(g2,g0,g4)
    c: Coincident(g5,g6)
    c: Coincident(g6,g7)
    c: Coincident(g7,g8)
    c: Coincident(g8,g5)
    c: Horizontal(g5)
    c: Horizontal(g7)
    c: Vertical(g6)
    c: Vertical(g8)
    c: Symmetric(g7,g5,g9)
    c: Coincident(g10,g11)
    c: Coincident(g11,g12)
    c: Coincident(g12,g13)
    c: Coincident(g13,g10)
    c: Horizontal(g10)
    c: Horizontal(g12)
    c: Vertical(g11)
    c: Vertical(g13)
    c: Symmetric(g12,g10,g14)
    c: Coincident(g15,g16)
    c: Coincident(g16,g17)
    c: Coincident(g17,g18)
    c: Coincident(g18,g15)
    c: Horizontal(g15)
    c: Horizontal(g17)
    c: Vertical(g16)
    c: Vertical(g18)
    c: Symmetric(g17,g15,g19)
    c: Coincident(g20,g21)
    c: Coincident(g21,g22)
    c: Coincident(g22,g23)
    c: Coincident(g23,g20)
    c: Horizontal(g20)
    c: Horizontal(g22)
    c: Vertical(g21)
    c: Vertical(g23)
    c: Symmetric(g22,g20,g24)
    c: Coincident(g25,g26)
    c: Coincident(g26,g27)
    c: Coincident(g27,g28)
    c: Coincident(g28,g25)
    c: Horizontal(g25)
    c: Horizontal(g27)
    c: Vertical(g26)
    c: Vertical(g28)
    c: Symmetric(g27,g25,g29)
    c: Coincident(g30,g31)
    c: Coincident(g31,g32)
    c: Coincident(g32,g33)
    c: Coincident(g33,g30)
    c: Horizontal(g30)
    c: Horizontal(g32)
    c: Vertical(g31)
    c: Vertical(g33)
    c: Symmetric(g32,g30,g34)
    c: Coincident(g35,g36)
    c: Coincident(g36,g37)
    c: Coincident(g37,g38)
    c: Coincident(g38,g35)
    c: Horizontal(g35)
    c: Horizontal(g37)
    c: Vertical(g36)
    c: Vertical(g38)
    c: Symmetric(g37,g35,g39)
    c: Coincident(g40,g41)
    c: Coincident(g41,g42)
    c: Coincident(g42,g43)
    c: Coincident(g43,g40)
    c: Horizontal(g40)
    c: Horizontal(g42)
    c: Vertical(g41)
    c: Vertical(g43)
    c: Symmetric(g42,g40,g44)
    c: Coincident(g45,g46)
    c: Coincident(g46,g47)
    c: Coincident(g47,g48)
    c: Coincident(g48,g45)
    c: Horizontal(g45)
    c: Horizontal(g47)
    c: Vertical(g46)
    c: Vertical(g48)
    c: Symmetric(g47,g45,g49)
    c: Coincident(g50,g51)
    c: Coincident(g51,g52)
    c: Coincident(g52,g53)
    c: Coincident(g53,g50)
    c: Horizontal(g50)
    c: Horizontal(g52)
    c: Vertical(g51)
    c: Vertical(g53)
    c: Symmetric(g52,g50,g54)
    c: Coincident(g55,g56)
    c: Coincident(g56,g57)
    c: Coincident(g57,g58)
    c: Coincident(g58,g55)
    c: Horizontal(g55)
    c: Horizontal(g57)
    c: Vertical(g56)
    c: Vertical(g58)
    c: Symmetric(g57,g55,g59)
    c: Coincident(g60,g61)
    c: Coincident(g61,g62)
    c: Coincident(g62,g63)
    c: Coincident(g63,g60)
    c: Horizontal(g60)
    c: Horizontal(g62)
    c: Vertical(g61)
    c: Vertical(g63)
    c: Symmetric(g62,g60,g64)
    c: Coincident(g65,g66)
    c: Coincident(g66,g67)
    c: Coincident(g67,g68)
    c: Coincident(g68,g65)
    c: Horizontal(g65)
    c: Horizontal(g67)
    c: Vertical(g66)
    c: Vertical(g68)
    c: Symmetric(g67,g65,g69)
    c: Coincident(g70,g71)
    c: Coincident(g71,g72)
    c: Coincident(g72,g73)
    c: Coincident(g73,g70)
    c: Horizontal(g70)
    c: Horizontal(g72)
    c: Vertical(g71)
    c: Vertical(g73)
    c: Symmetric(g72,g70,g74)
    c: Coincident(g75,g76)
    c: Coincident(g76,g77)
    c: Coincident(g77,g78)
    c: Coincident(g78,g75)
    c: Horizontal(g75)
    c: Horizontal(g77)
    c: Vertical(g76)
    c: Vertical(g78)
    c: Symmetric(g77,g75,g79)
    c: Coincident(g80,g81)
    c: Coincident(g81,g82)
    c: Coincident(g82,g83)
    c: Coincident(g83,g80)
    c: Horizontal(g80)
    c: Horizontal(g82)
    c: Vertical(g81)
    c: Vertical(g83)
    c: Symmetric(g82,g80,g84)
    c: Coincident(g85,g86)
    c: Coincident(g86,g87)
    c: Coincident(g87,g88)
    c: Coincident(g88,g85)
    c: Horizontal(g85)
    c: Horizontal(g87)
    c: Vertical(g86)
    c: Vertical(g88)
    c: Symmetric(g87,g85,g89)
    c: Coincident(g90,g91)
    c: Coincident(g91,g92)
    c: Coincident(g92,g93)
    c: Coincident(g93,g90)
    c: Horizontal(g90)
    c: Horizontal(g92)
    c: Vertical(g91)
    c: Vertical(g93)
    c: Symmetric(g92,g90,g94)
    c: Coincident(g95,g96)
    c: Coincident(g96,g97)
    c: Coincident(g97,g98)
    c: Coincident(g98,g95)
    c: Horizontal(g95)
    c: Vertical(g96)
    c: Vertical(g98)
    c: Symmetric(g97,g95,g99)
    c: Coincident(g100,g101)
    c: Coincident(g101,g102)
    c: Coincident(g102,g103)
    c: Coincident(g103,g100)
    c: Horizontal(g100)
    c: Horizontal(g102)
    c: Vertical(g101)
    c: Vertical(g103)
    c: Symmetric(g102,g100,g104)
    c: Coincident(g105,g106)
    c: Coincident(g106,g107)
    c: Coincident(g107,g108)
    c: Coincident(g108,g105)
    c: Horizontal(g105)
    c: Horizontal(g107)
    c: Vertical(g106)
    c: Vertical(g108)
    c: Symmetric(g107,g105,g109)
    c: DistanceX(g107,g107) = 14.6
    c: DistanceY(g106,g106) = 14.6
    c: Coincident(g110,g111)
    c: Coincident(g111,g112)
    c: Coincident(g112,g113)
    c: Coincident(g113,g110)
    c: Horizontal(g110)
    c: Horizontal(g112)
    c: Vertical(g111)
    c: Vertical(g113)
    c: Symmetric(g112,g110,g114)
    c: Coincident(g115,g116)
    c: Coincident(g116,g117)
    c: Coincident(g117,g118)
    c: Coincident(g118,g115)
    c: Horizontal(g115)
    c: Horizontal(g117)
    c: Vertical(g116)
    c: Vertical(g118)
    c: Symmetric(g117,g115,g119)
    c: Coincident(g120,g121)
    c: Coincident(g121,g122)
    c: Coincident(g122,g123)
    c: Coincident(g123,g120)
    c: Horizontal(g120)
    c: Horizontal(g122)
    c: Vertical(g121)
    c: Vertical(g123)
    c: Symmetric(g122,g120,g124)
    c: Horizontal(g69,g74)
    c: Horizontal(g74,g79)
    c: Horizontal(g79,g84)
    c: Horizontal(g84,g89)
    c: Horizontal(g89,g124)
    c: Horizontal(g49,g54)
    c: Horizontal(g54,g59)
    c: Horizontal(g59,g64)
    c: Horizontal(g64,g94)
    c: Horizontal(g94,g119)
    c: Horizontal(g14,g29)
    c: Horizontal(g29,g34)
    c: Horizontal(g34,g44)
    c: Horizontal(g44,g99)
    c: Horizontal(g99,g114)
    c: Horizontal(g109,g4)
    c: Horizontal(g4,g9)
    c: Horizontal(g9,g19)
    c: Horizontal(g19,g24)
    c: Horizontal(g24,g39)
    c: Horizontal(g39,g104)
    c: Vertical(g69,g49)
    c: Vertical(g49,g14)
    c: Vertical(g14,g4)
    c: Vertical(g74,g54)
    c: Vertical(g54,g29)
    c: Vertical(g29,g9)
    c: Vertical(g79,g59)
    c: Vertical(g59,g34)
    c: Vertical(g34,g19)
    c: Vertical(g84,g64)
    c: Vertical(g64,g44)
    c: Vertical(g44,g24)
    c: Vertical(g89,g94)
    c: Vertical(g94,g99)
    c: Vertical(g99,g39)
    c: Vertical(g124,g119)
    c: Vertical(g119,g114)
    c: Vertical(g114,g104)
    c: DistanceX(g109,g4) = 19.05
    c: DistanceX(g4,g9) = 19.05
    c: DistanceX(g9,g19) = 19.05
    c: DistanceX(g19,g24) = 19.05
    c: DistanceX(g24,g39) = 19.05
    c: DistanceX(g39,g104) = 19.05
    c: DistanceY(g49,g69) = 19.05
    c: DistanceY(g14,g49) = 19.05
    c: DistanceY(g109,g14) = 19.05
    c: DistanceX(g-1,g109) = 19.05
    c: DistanceY(g-1,g109) = 19.05
    c: Equal(g121,g86)
    c: Equal(g86,g81)
    c: Equal(g81,g76)
    c: Equal(g76,g71)
    c: Equal(g71,g66)
    c: Equal(g66,g106)
    c: Equal(g122,g87)
    c: Equal(g87,g82)
    c: Equal(g82,g77)
    c: Equal(g77,g72)
    c: Equal(g72,g67)
    c: Equal(g67,g107)
    c: Equal(g116,g91)
    c: Equal(g91,g61)
    c: Equal(g61,g56)
    c: Equal(g56,g51)
    c: Equal(g51,g46)
    c: Equal(g46,g106)
    c: Equal(g117,g92)
    c: Equal(g92,g62)
    c: Equal(g62,g57)
    c: Equal(g57,g52)
    c: Equal(g52,g47)
    c: Equal(g47,g107)
    c: Horizontal(g97)
    c: Equal(g111,g96)
    c: Equal(g96,g41)
    c: Equal(g41,g31)
    c: Equal(g31,g26)
    c: Equal(g26,g11)
    c: Equal(g11,g106)
    c: Equal(g112,g97)
    c: Equal(g97,g42)
    c: Equal(g42,g32)
    c: Equal(g32,g27)
    c: Equal(g27,g12)
    c: Equal(g12,g107)
    c: Equal(g101,g36)
    c: Equal(g36,g21)
    c: Equal(g21,g16)
    c: Equal(g16,g6)
    c: Equal(g6,g1)
    c: Equal(g1,g106)
    c: Equal(g102,g37)
    c: Equal(g37,g22)
    c: Equal(g22,g17)
    c: Equal(g17,g7)
    c: Equal(g7,g2)
    c: Equal(g2,g107)
FEATURE [Sketcher::SketchObject] Sketch013  label="TR-Med"
  ArcFitTolerance = 1e-06
  AttachmentSupport = -> [XY_Plane002]
  FullyConstrained = true
  MakeInternals = false
  MapMode = 5
  expr: Constraints[197] = VarSet.Top_MedXY
  expr: Constraints[198] = VarSet.Top_MedXY
  sketch-geometry (125):
    g0: LineSegment StartX=45 StartY=25.95 StartZ=0 EndX=31.2 EndY=25.95 EndZ=0
    g1: LineSegment StartX=31.2 StartY=25.95 StartZ=0 EndX=31.2 EndY=12.15 EndZ=0
    g2: LineSegment StartX=31.2 StartY=12.15 StartZ=0 EndX=45 EndY=12.15 EndZ=0
    g3: LineSegment StartX=45 StartY=12.15 StartZ=0 EndX=45 EndY=25.95 EndZ=0
    g4: GeomPoint [constr] X=38.1 Y=19.05 Z=0
    g5: LineSegment StartX=64.05 StartY=25.95 StartZ=0 EndX=50.25 EndY=25.95 EndZ=0
    g6: LineSegment StartX=50.25 StartY=25.95 StartZ=0 EndX=50.25 EndY=12.15 EndZ=0
    g7: LineSegment StartX=50.25 StartY=12.15 StartZ=0 EndX=64.05 EndY=12.15 EndZ=0
    g8: LineSegment StartX=64.05 StartY=12.15 StartZ=0 EndX=64.05 EndY=25.95 EndZ=0
    g9: GeomPoint [constr] X=57.15 Y=19.05 Z=0
    g10: LineSegment StartX=45 StartY=45 StartZ=0 EndX=31.2 EndY=45 EndZ=0
    g11: LineSegment StartX=31.2 StartY=45 StartZ=0 EndX=31.2 EndY=31.2 EndZ=0
    g12: LineSegment StartX=31.2 StartY=31.2 StartZ=0 EndX=45 EndY=31.2 EndZ=0
    g13: LineSegment StartX=45 StartY=31.2 StartZ=0 EndX=45 EndY=45 EndZ=0
    g14: GeomPoint [constr] X=38.1 Y=38.1 Z=0
    g15: LineSegment StartX=83.1 StartY=25.95 StartZ=0 EndX=69.3 EndY=25.95 EndZ=0
    g16: LineSegment StartX=69.3 StartY=25.95 StartZ=0 EndX=69.3 EndY=12.15 EndZ=0
    g17: LineSegment StartX=69.3 StartY=12.15 StartZ=0 EndX=83.1 EndY=12.15 EndZ=0
    g18: LineSegment StartX=83.1 StartY=12.15 StartZ=0 EndX=83.1 EndY=25.95 EndZ=0
    g19: GeomPoint [constr] X=76.2 Y=19.05 Z=0
    g20: LineSegment StartX=102.15 StartY=25.95 StartZ=0 EndX=88.35 EndY=25.95 EndZ=0
    g21: LineSegment StartX=88.35 StartY=25.95 StartZ=0 EndX=88.35 EndY=12.15 EndZ=0
    g22: LineSegment StartX=88.35 StartY=12.15 StartZ=0 EndX=102.15 EndY=12.15 EndZ=0
    g23: LineSegment StartX=102.15 StartY=12.15 StartZ=0 EndX=102.15 EndY=25.95 EndZ=0
    g24: GeomPoint [constr] X=95.25 Y=19.05 Z=0
    g25: LineSegment StartX=64.05 StartY=45 StartZ=0 EndX=50.25 EndY=45 EndZ=0
    g26: LineSegment StartX=50.25 StartY=45 StartZ=0 EndX=50.25 EndY=31.2 EndZ=0
    g27: LineSegment StartX=50.25 StartY=31.2 StartZ=0 EndX=64.05 EndY=31.2 EndZ=0
    g28: LineSegment StartX=64.05 StartY=31.2 StartZ=0 EndX=64.05 EndY=45 EndZ=0
    g29: GeomPoint [constr] X=57.15 Y=38.1 Z=0
    g30: LineSegment StartX=83.1 StartY=45 StartZ=0 EndX=69.3 EndY=45 EndZ=0
    g31: LineSegment StartX=69.3 StartY=45 StartZ=0 EndX=69.3 EndY=31.2 EndZ=0
    g32: LineSegment StartX=69.3 StartY=31.2 StartZ=0 EndX=83.1 EndY=31.2 EndZ=0
    g33: LineSegment StartX=83.1 StartY=31.2 StartZ=0 EndX=83.1 EndY=45 EndZ=0
    g34: GeomPoint [constr] X=76.2 Y=38.1 Z=0
    g35: LineSegment StartX=121.2 StartY=25.95 StartZ=0 EndX=107.4 EndY=25.95 EndZ=0
    g36: LineSegment StartX=107.4 StartY=25.95 StartZ=0 EndX=107.4 EndY=12.15 EndZ=0
    g37: LineSegment StartX=107.4 StartY=12.15 StartZ=0 EndX=121.2 EndY=12.15 EndZ=0
    g38: LineSegment StartX=121.2 StartY=12.15 StartZ=0 EndX=121.2 EndY=25.95 EndZ=0
    g39: GeomPoint [constr] X=114.3 Y=19.05 Z=0
    g40: LineSegment StartX=102.15 StartY=45 StartZ=0 EndX=88.35 EndY=45 EndZ=0
    g41: LineSegment StartX=88.35 StartY=45 StartZ=0 EndX=88.35 EndY=31.2 EndZ=0
    g42: LineSegment StartX=88.35 StartY=31.2 StartZ=0 EndX=102.15 EndY=31.2 EndZ=0
    g43: LineSegment StartX=102.15 StartY=31.2 StartZ=0 EndX=102.15 EndY=45 EndZ=0
    g44: GeomPoint [constr] X=95.25 Y=38.1 Z=0
    g45: LineSegment StartX=45 StartY=64.05 StartZ=0 EndX=31.2 EndY=64.05 EndZ=0
    g46: LineSegment StartX=31.2 StartY=64.05 StartZ=0 EndX=31.2 EndY=50.25 EndZ=0
    g47: LineSegment StartX=31.2 StartY=50.25 StartZ=0 EndX=45 EndY=50.25 EndZ=0
    g48: LineSegment StartX=45 StartY=50.25 StartZ=0 EndX=45 EndY=64.05 EndZ=0
    g49: GeomPoint [constr] X=38.1 Y=57.15 Z=0
    g50: LineSegment StartX=64.05 StartY=64.05 StartZ=0 EndX=50.25 EndY=64.05 EndZ=0
    g51: LineSegment StartX=50.25 StartY=64.05 StartZ=0 EndX=50.25 EndY=50.25 EndZ=0
    g52: LineSegment StartX=50.25 StartY=50.25 StartZ=0 EndX=64.05 EndY=50.25 EndZ=0
    g53: LineSegment StartX=64.05 StartY=50.25 StartZ=0 EndX=64.05 EndY=64.05 EndZ=0
    g54: GeomPoint [constr] X=57.15 Y=57.15 Z=0
    g55: LineSegment StartX=83.1 StartY=64.05 StartZ=0 EndX=69.3 EndY=64.05 EndZ=0
    g56: LineSegment StartX=69.3 StartY=64.05 StartZ=0 EndX=69.3 EndY=50.25 EndZ=0
    g57: LineSegment StartX=69.3 StartY=50.25 StartZ=0 EndX=83.1 EndY=50.25 EndZ=0
    g58: LineSegment StartX=83.1 StartY=50.25 StartZ=0 EndX=83.1 EndY=64.05 EndZ=0
    g59: GeomPoint [constr] X=76.2 Y=57.15 Z=0
    g60: LineSegment StartX=102.15 StartY=64.05 StartZ=0 EndX=88.35 EndY=64.05 EndZ=0
    g61: LineSegment StartX=88.35 StartY=64.05 StartZ=0 EndX=88.35 EndY=50.25 EndZ=0
    g62: LineSegment StartX=88.35 StartY=50.25 StartZ=0 EndX=102.15 EndY=50.25 EndZ=0
    g63: LineSegment StartX=102.15 StartY=50.25 StartZ=0 EndX=102.15 EndY=64.05 EndZ=0
    g64: GeomPoint [constr] X=95.25 Y=57.15 Z=0
    g65: LineSegment StartX=45 StartY=83.1 StartZ=0 EndX=31.2 EndY=83.1 EndZ=0
    g66: LineSegment StartX=31.2 StartY=83.1 StartZ=0 EndX=31.2 EndY=69.3 EndZ=0
    g67: LineSegment StartX=31.2 StartY=69.3 StartZ=0 EndX=45 EndY=69.3 EndZ=0
    g68: LineSegment StartX=45 StartY=69.3 StartZ=0 EndX=45 EndY=83.1 EndZ=0
    g69: GeomPoint [constr] X=38.1 Y=76.2 Z=0
    g70: LineSegment StartX=64.05 StartY=83.1 StartZ=0 EndX=50.25 EndY=83.1 EndZ=0
    g71: LineSegment StartX=50.25 StartY=83.1 StartZ=0 EndX=50.25 EndY=69.3 EndZ=0
    g72: LineSegment StartX=50.25 StartY=69.3 StartZ=0 EndX=64.05 EndY=69.3 EndZ=0
    g73: LineSegment StartX=64.05 StartY=69.3 StartZ=0 EndX=64.05 EndY=83.1 EndZ=0
    g74: GeomPoint [constr] X=57.15 Y=76.2 Z=0
    g75: LineSegment StartX=83.1 StartY=83.1 StartZ=0 EndX=69.3 EndY=83.1 EndZ=0
    g76: LineSegment StartX=69.3 StartY=83.1 StartZ=0 EndX=69.3 EndY=69.3 EndZ=0
    g77: LineSegment StartX=69.3 StartY=69.3 StartZ=0 EndX=83.1 EndY=69.3 EndZ=0
    g78: LineSegment StartX=83.1 StartY=69.3 StartZ=0 EndX=83.1 EndY=83.1 EndZ=0
    g79: GeomPoint [constr] X=76.2 Y=76.2 Z=0
    g80: LineSegment StartX=102.15 StartY=83.1 StartZ=0 EndX=88.35 EndY=83.1 EndZ=0
    g81: LineSegment StartX=88.35 StartY=83.1 StartZ=0 EndX=88.35 EndY=69.3 EndZ=0
    g82: LineSegment StartX=88.35 StartY=69.3 StartZ=0 EndX=102.15 EndY=69.3 EndZ=0
    g83: LineSegment StartX=102.15 StartY=69.3 StartZ=0 EndX=102.15 EndY=83.1 EndZ=0
    g84: GeomPoint [constr] X=95.25 Y=76.2 Z=0
    g85: LineSegment StartX=121.2 StartY=83.1 StartZ=0 EndX=107.4 EndY=83.1 EndZ=0
    g86: LineSegment StartX=107.4 StartY=83.1 StartZ=0 EndX=107.4 EndY=69.3 EndZ=0
    g87: LineSegment StartX=107.4 StartY=69.3 StartZ=0 EndX=121.2 EndY=69.3 EndZ=0
    g88: LineSegment StartX=121.2 StartY=69.3 StartZ=0 EndX=121.2 EndY=83.1 EndZ=0
    g89: GeomPoint [constr] X=114.3 Y=76.2 Z=0
    g90: LineSegment StartX=121.2 StartY=64.05 StartZ=0 EndX=107.4 EndY=64.05 EndZ=0
    g91: LineSegment StartX=107.4 StartY=64.05 StartZ=0 EndX=107.4 EndY=50.25 EndZ=0
    g92: LineSegment StartX=107.4 StartY=50.25 StartZ=0 EndX=121.2 EndY=50.25 EndZ=0
    g93: LineSegment StartX=121.2 StartY=50.25 StartZ=0 EndX=121.2 EndY=64.05 EndZ=0
    g94: GeomPoint [constr] X=114.3 Y=57.15 Z=0
    g95: LineSegment StartX=121.2 StartY=45 StartZ=0 EndX=107.4 EndY=45 EndZ=0
    g96: LineSegment StartX=107.4 StartY=45 StartZ=0 EndX=107.4 EndY=31.2 EndZ=0
    g97: LineSegment StartX=107.4 StartY=31.2 StartZ=0 EndX=121.2 EndY=31.2 EndZ=0
    g98: LineSegment StartX=121.2 StartY=31.2 StartZ=0 EndX=121.2 EndY=45 EndZ=0
    g99: GeomPoint [constr] X=114.3 Y=38.1 Z=0
    g100: LineSegment StartX=140.25 StartY=25.95 StartZ=0 EndX=126.45 EndY=25.95 EndZ=0
    g101: LineSegment StartX=126.45 StartY=25.95 StartZ=0 EndX=126.45 EndY=12.15 EndZ=0
    g102: LineSegment StartX=126.45 StartY=12.15 StartZ=0 EndX=140.25 EndY=12.15 EndZ=0
    g103: LineSegment StartX=140.25 StartY=12.15 StartZ=0 EndX=140.25 EndY=25.95 EndZ=0
    g104: GeomPoint [constr] X=133.35 Y=19.05 Z=0
    g105: LineSegment StartX=25.95 StartY=25.95 StartZ=0 EndX=12.15 EndY=25.95 EndZ=0
    g106: LineSegment StartX=12.15 StartY=25.95 StartZ=0 EndX=12.15 EndY=12.15 EndZ=0
    g107: LineSegment StartX=12.15 StartY=12.15 StartZ=0 EndX=25.95 EndY=12.15 EndZ=0
    g108: LineSegment StartX=25.95 StartY=12.15 StartZ=0 EndX=25.95 EndY=25.95 EndZ=0
    g109: GeomPoint [constr] X=19.05 Y=19.05 Z=0
    g110: LineSegment StartX=140.25 StartY=45 StartZ=0 EndX=126.45 EndY=45 EndZ=0
    g111: LineSegment StartX=126.45 StartY=45 StartZ=0 EndX=126.45 EndY=31.2 EndZ=0
    g112: LineSegment StartX=126.45 StartY=31.2 StartZ=0 EndX=140.25 EndY=31.2 EndZ=0
    g113: LineSegment StartX=140.25 StartY=31.2 StartZ=0 EndX=140.25 EndY=45 EndZ=0
    g114: GeomPoint [constr] X=133.35 Y=38.1 Z=0
    g115: LineSegment StartX=140.25 StartY=64.05 StartZ=0 EndX=126.45 EndY=64.05 EndZ=0
    g116: LineSegment StartX=126.45 StartY=64.05 StartZ=0 EndX=126.45 EndY=50.25 EndZ=0
    g117: LineSegment StartX=126.45 StartY=50.25 StartZ=0 EndX=140.25 EndY=50.25 EndZ=0
    g118: LineSegment StartX=140.25 StartY=50.25 StartZ=0 EndX=140.25 EndY=64.05 EndZ=0
    g119: GeomPoint [constr] X=133.35 Y=57.15 Z=0
    g120: LineSegment StartX=140.25 StartY=83.1 StartZ=0 EndX=126.45 EndY=83.1 EndZ=0
    g121: LineSegment StartX=126.45 StartY=83.1 StartZ=0 EndX=126.45 EndY=69.3 EndZ=0
    g122: LineSegment StartX=126.45 StartY=69.3 StartZ=0 EndX=140.25 EndY=69.3 EndZ=0
    g123: LineSegment StartX=140.25 StartY=69.3 StartZ=0 EndX=140.25 EndY=83.1 EndZ=0
    g124: GeomPoint [constr] X=133.35 Y=76.2 Z=0
  constraints (325):
    c: Coincident(g0,g1)
    c: Coincident(g1,g2)
    c: Coincident(g2,g3)
    c: Coincident(g3,g0)
    c: Horizontal(g0)
    c: Horizontal(g2)
    c: Vertical(g1)
    c: Vertical(g3)
    c: Symmetric(g2,g0,g4)
    c: Coincident(g5,g6)
    c: Coincident(g6,g7)
    c: Coincident(g7,g8)
    c: Coincident(g8,g5)
    c: Horizontal(g5)
    c: Horizontal(g7)
    c: Vertical(g6)
    c: Vertical(g8)
    c: Symmetric(g7,g5,g9)
    c: Coincident(g10,g11)
    c: Coincident(g11,g12)
    c: Coincident(g12,g13)
    c: Coincident(g13,g10)
    c: Horizontal(g10)
    c: Horizontal(g12)
    c: Vertical(g11)
    c: Vertical(g13)
    c: Symmetric(g12,g10,g14)
    c: Coincident(g15,g16)
    c: Coincident(g16,g17)
    c: Coincident(g17,g18)
    c: Coincident(g18,g15)
    c: Horizontal(g15)
    c: Horizontal(g17)
    c: Vertical(g16)
    c: Vertical(g18)
    c: Symmetric(g17,g15,g19)
    c: Coincident(g20,g21)
    c: Coincident(g21,g22)
    c: Coincident(g22,g23)
    c: Coincident(g23,g20)
    c: Horizontal(g20)
    c: Horizontal(g22)
    c: Vertical(g21)
    c: Vertical(g23)
    c: Symmetric(g22,g20,g24)
    c: Coincident(g25,g26)
    c: Coincident(g26,g27)
    c: Coincident(g27,g28)
    c: Coincident(g28,g25)
    c: Horizontal(g25)
    c: Horizontal(g27)
    c: Vertical(g26)
    c: Vertical(g28)
    c: Symmetric(g27,g25,g29)
    c: Coincident(g30,g31)
    c: Coincident(g31,g32)
    c: Coincident(g32,g33)
    c: Coincident(g33,g30)
    c: Horizontal(g30)
    c: Horizontal(g32)
    c: Vertical(g31)
    c: Vertical(g33)
    c: Symmetric(g32,g30,g34)
    c: Coincident(g35,g36)
    c: Coincident(g36,g37)
    c: Coincident(g37,g38)
    c: Coincident(g38,g35)
    c: Horizontal(g35)
    c: Horizontal(g37)
    c: Vertical(g36)
    c: Vertical(g38)
    c: Symmetric(g37,g35,g39)
    c: Coincident(g40,g41)
    c: Coincident(g41,g42)
    c: Coincident(g42,g43)
    c: Coincident(g43,g40)
    c: Horizontal(g40)
    c: Horizontal(g42)
    c: Vertical(g41)
    c: Vertical(g43)
    c: Symmetric(g42,g40,g44)
    c: Coincident(g45,g46)
    c: Coincident(g46,g47)
    c: Coincident(g47,g48)
    c: Coincident(g48,g45)
    c: Horizontal(g45)
    c: Horizontal(g47)
    c: Vertical(g46)
    c: Vertical(g48)
    c: Symmetric(g47,g45,g49)
    c: Coincident(g50,g51)
    c: Coincident(g51,g52)
    c: Coincident(g52,g53)
    c: Coincident(g53,g50)
    c: Horizontal(g50)
    c: Horizontal(g52)
    c: Vertical(g51)
    c: Vertical(g53)
    c: Symmetric(g52,g50,g54)
    c: Coincident(g55,g56)
    c: Coincident(g56,g57)
    c: Coincident(g57,g58)
    c: Coincident(g58,g55)
    c: Horizontal(g55)
    c: Horizontal(g57)
    c: Vertical(g56)
    c: Vertical(g58)
    c: Symmetric(g57,g55,g59)
    c: Coincident(g60,g61)
    c: Coincident(g61,g62)
    c: Coincident(g62,g63)
    c: Coincident(g63,g60)
    c: Horizontal(g60)
    c: Horizontal(g62)
    c: Vertical(g61)
    c: Vertical(g63)
    c: Symmetric(g62,g60,g64)
    c: Coincident(g65,g66)
    c: Coincident(g66,g67)
    c: Coincident(g67,g68)
    c: Coincident(g68,g65)
    c: Horizontal(g65)
    c: Horizontal(g67)
    c: Vertical(g66)
    c: Vertical(g68)
    c: Symmetric(g67,g65,g69)
    c: Coincident(g70,g71)
    c: Coincident(g71,g72)
    c: Coincident(g72,g73)
    c: Coincident(g73,g70)
    c: Horizontal(g70)
    c: Horizontal(g72)
    c: Vertical(g71)
    c: Vertical(g73)
    c: Symmetric(g72,g70,g74)
    c: Coincident(g75,g76)
    c: Coincident(g76,g77)
    c: Coincident(g77,g78)
    c: Coincident(g78,g75)
    c: Horizontal(g75)
    c: Horizontal(g77)
    c: Vertical(g76)
    c: Vertical(g78)
    c: Symmetric(g77,g75,g79)
    c: Coincident(g80,g81)
    c: Coincident(g81,g82)
    c: Coincident(g82,g83)
    c: Coincident(g83,g80)
    c: Horizontal(g80)
    c: Horizontal(g82)
    c: Vertical(g81)
    c: Vertical(g83)
    c: Symmetric(g82,g80,g84)
    c: Coincident(g85,g86)
    c: Coincident(g86,g87)
    c: Coincident(g87,g88)
    c: Coincident(g88,g85)
    c: Horizontal(g85)
    c: Horizontal(g87)
    c: Vertical(g86)
    c: Vertical(g88)
    c: Symmetric(g87,g85,g89)
    c: Coincident(g90,g91)
    c: Coincident(g91,g92)
    c: Coincident(g92,g93)
    c: Coincident(g93,g90)
    c: Horizontal(g90)
    c: Horizontal(g92)
    c: Vertical(g91)
    c: Vertical(g93)
    c: Symmetric(g92,g90,g94)
    c: Coincident(g95,g96)
    c: Coincident(g96,g97)
    c: Coincident(g97,g98)
    c: Coincident(g98,g95)
    c: Horizontal(g95)
    c: Vertical(g96)
    c: Vertical(g98)
    c: Symmetric(g97,g95,g99)
    c: Coincident(g100,g101)
    c: Coincident(g101,g102)
    c: Coincident(g102,g103)
    c: Coincident(g103,g100)
    c: Horizontal(g100)
    c: Horizontal(g102)
    c: Vertical(g101)
    c: Vertical(g103)
    c: Symmetric(g102,g100,g104)
    c: Coincident(g105,g106)
    c: Coincident(g106,g107)
    c: Coincident(g107,g108)
    c: Coincident(g108,g105)
    c: Horizontal(g105)
    c: Horizontal(g107)
    c: Vertical(g106)
    c: Vertical(g108)
    c: Symmetric(g107,g105,g109)
    c: DistanceX(g107,g107) = 13.8
    c: DistanceY(g106,g106) = 13.8
    c: Coincident(g110,g111)
    c: Coincident(g111,g112)
    c: Coincident(g112,g113)
    c: Coincident(g113,g110)
    c: Horizontal(g110)
    c: Horizontal(g112)
    c: Vertical(g111)
    c: Vertical(g113)
    c: Symmetric(g112,g110,g114)
    c: Coincident(g115,g116)
    c: Coincident(g116,g117)
    c: Coincident(g117,g118)
    c: Coincident(g118,g115)
    c: Horizontal(g115)
    c: Horizontal(g117)
    c: Vertical(g116)
    c: Vertical(g118)
    c: Symmetric(g117,g115,g119)
    c: Coincident(g120,g121)
    c: Coincident(g121,g122)
    c: Coincident(g122,g123)
    c: Coincident(g123,g120)
    c: Horizontal(g120)
    c: Horizontal(g122)
    c: Vertical(g121)
    c: Vertical(g123)
    c: Symmetric(g122,g120,g124)
    c: Horizontal(g69,g74)
    c: Horizontal(g74,g79)
    c: Horizontal(g79,g84)
    c: Horizontal(g84,g89)
    c: Horizontal(g89,g124)
    c: Horizontal(g49,g54)
    c: Horizontal(g54,g59)
    c: Horizontal(g59,g64)
    c: Horizontal(g64,g94)
    c: Horizontal(g94,g119)
    c: Horizontal(g14,g29)
    c: Horizontal(g29,g34)
    c: Horizontal(g34,g44)
    c: Horizontal(g44,g99)
    c: Horizontal(g99,g114)
    c: Horizontal(g109,g4)
    c: Horizontal(g4,g9)
    c: Horizontal(g9,g19)
    c: Horizontal(g19,g24)
    c: Horizontal(g24,g39)
    c: Horizontal(g39,g104)
    c: Vertical(g69,g49)
    c: Vertical(g49,g14)
    c: Vertical(g14,g4)
    c: Vertical(g74,g54)
    c: Vertical(g54,g29)
    c: Vertical(g29,g9)
    c: Vertical(g79,g59)
    c: Vertical(g59,g34)
    c: Vertical(g34,g19)
    c: Vertical(g84,g64)
    c: Vertical(g64,g44)
    c: Vertical(g44,g24)
    c: Vertical(g89,g94)
    c: Vertical(g94,g99)
    c: Vertical(g99,g39)
    c: Vertical(g124,g119)
    c: Vertical(g119,g114)
    c: Vertical(g114,g104)
    c: DistanceX(g109,g4) = 19.05
    c: DistanceX(g4,g9) = 19.05
    c: DistanceX(g9,g19) = 19.05
    c: DistanceX(g19,g24) = 19.05
    c: DistanceX(g24,g39) = 19.05
    c: DistanceX(g39,g104) = 19.05
    c: DistanceY(g49,g69) = 19.05
    c: DistanceY(g14,g49) = 19.05
    c: DistanceY(g109,g14) = 19.05
    c: DistanceX(g-1,g109) = 19.05
    c: DistanceY(g-1,g109) = 19.05
    c: Equal(g121,g86)
    c: Equal(g86,g81)
    c: Equal(g81,g76)
    c: Equal(g76,g71)
    c: Equal(g71,g66)
    c: Equal(g66,g106)
    c: Equal(g122,g87)
    c: Equal(g87,g82)
    c: Equal(g82,g77)
    c: Equal(g77,g72)
    c: Equal(g72,g67)
    c: Equal(g67,g107)
    c: Equal(g116,g91)
    c: Equal(g91,g61)
    c: Equal(g61,g56)
    c: Equal(g56,g51)
    c: Equal(g51,g46)
    c: Equal(g46,g106)
    c: Equal(g117,g92)
    c: Equal(g92,g62)
    c: Equal(g62,g57)
    c: Equal(g57,g52)
    c: Equal(g52,g47)
    c: Equal(g47,g107)
    c: Horizontal(g97)
    c: Equal(g111,g96)
    c: Equal(g96,g41)
    c: Equal(g41,g31)
    c: Equal(g31,g26)
    c: Equal(g26,g11)
    c: Equal(g11,g106)
    c: Equal(g112,g97)
    c: Equal(g97,g42)
    c: Equal(g42,g32)
    c: Equal(g32,g27)
    c: Equal(g27,g12)
    c: Equal(g12,g107)
    c: Equal(g101,g36)
    c: Equal(g36,g21)
    c: Equal(g21,g16)
    c: Equal(g16,g6)
    c: Equal(g6,g1)
    c: Equal(g1,g106)
    c: Equal(g102,g37)
    c: Equal(g37,g22)
    c: Equal(g22,g17)
    c: Equal(g17,g7)
    c: Equal(g7,g2)
    c: Equal(g2,g107)
FEATURE [Sketcher::SketchObject] Sketch014  label="TR-Hi"
  ArcFitTolerance = 1e-06
  AttachmentOffset = pos=(0,0,5) rot=(0,0,1;0rad)
  AttachmentSupport = -> [XY_Plane002]
  FullyConstrained = true
  MakeInternals = false
  MapMode = 5
  Placement = pos=(0,0,5) rot=(0,0,1;0rad)
  expr: .AttachmentOffset.Base.z = VarSet.Top_PcbZ + VarSet.Top_LoZ + VarSet.Top_MedZ + VarSet.Top_HiZ
  expr: Constraints[109] = VarSet.Top_HiXY
  expr: Constraints[110] = VarSet.Top_HiXY
  expr: Constraints[718] = VarSet.Top_HiSwFilletR
  sketch-geometry (325):
    g0: LineSegment StartX=44.65 StartY=26.6 StartZ=0 EndX=31.55 EndY=26.6 EndZ=0
    g1: LineSegment StartX=30.55 StartY=25.6 StartZ=0 EndX=30.55 EndY=12.5 EndZ=0
    g2: LineSegment StartX=31.55 StartY=11.5 StartZ=0 EndX=44.65 EndY=11.5 EndZ=0
    g3: LineSegment StartX=45.65 StartY=12.5 StartZ=0 EndX=45.65 EndY=25.6 EndZ=0
    g4: GeomPoint [constr] X=38.1 Y=19.05 Z=0
    g5: LineSegment StartX=63.7 StartY=26.6 StartZ=0 EndX=50.6 EndY=26.6 EndZ=0
    g6: LineSegment StartX=49.6 StartY=25.6 StartZ=0 EndX=49.6 EndY=12.5 EndZ=0
    g7: LineSegment StartX=50.6 StartY=11.5 StartZ=0 EndX=63.7 EndY=11.5 EndZ=0
    g8: LineSegment StartX=64.7 StartY=12.5 StartZ=0 EndX=64.7 EndY=25.6 EndZ=0
    g9: GeomPoint [constr] X=57.15 Y=19.05 Z=0
    g10: LineSegment StartX=44.65 StartY=45.65 StartZ=0 EndX=31.55 EndY=45.65 EndZ=0
    g11: LineSegment StartX=30.55 StartY=44.65 StartZ=0 EndX=30.55 EndY=31.55 EndZ=0
    g12: LineSegment StartX=31.55 StartY=30.55 StartZ=0 EndX=44.65 EndY=30.55 EndZ=0
    g13: LineSegment StartX=45.65 StartY=31.55 StartZ=0 EndX=45.65 EndY=44.65 EndZ=0
    g14: GeomPoint [constr] X=38.1 Y=38.1 Z=0
    g15: LineSegment StartX=82.75 StartY=26.6 StartZ=0 EndX=69.65 EndY=26.6 EndZ=0
    g16: LineSegment StartX=68.65 StartY=25.6 StartZ=0 EndX=68.65 EndY=12.5 EndZ=0
    g17: LineSegment StartX=69.65 StartY=11.5 StartZ=0 EndX=82.75 EndY=11.5 EndZ=0
    g18: LineSegment StartX=83.75 StartY=12.5 StartZ=0 EndX=83.75 EndY=25.6 EndZ=0
    g19: GeomPoint [constr] X=76.2 Y=19.05 Z=0
    g20: LineSegment StartX=101.8 StartY=26.6 StartZ=0 EndX=88.7 EndY=26.6 EndZ=0
    g21: LineSegment StartX=87.7 StartY=25.6 StartZ=0 EndX=87.7 EndY=12.5 EndZ=0
    g22: LineSegment StartX=88.7 StartY=11.5 StartZ=0 EndX=101.8 EndY=11.5 EndZ=0
    g23: LineSegment StartX=102.8 StartY=12.5 StartZ=0 EndX=102.8 EndY=25.6 EndZ=0
    g24: GeomPoint [constr] X=95.25 Y=19.05 Z=0
    g25: LineSegment StartX=63.7 StartY=45.65 StartZ=0 EndX=50.6 EndY=45.65 EndZ=0
    g26: LineSegment StartX=49.6 StartY=44.65 StartZ=0 EndX=49.6 EndY=31.55 EndZ=0
    g27: LineSegment StartX=50.6 StartY=30.55 StartZ=0 EndX=63.7 EndY=30.55 EndZ=0
    g28: LineSegment StartX=64.7 StartY=31.55 StartZ=0 EndX=64.7 EndY=44.65 EndZ=0
    g29: GeomPoint [constr] X=57.15 Y=38.1 Z=0
    g30: LineSegment StartX=82.75 StartY=45.65 StartZ=0 EndX=69.65 EndY=45.65 EndZ=0
    g31: LineSegment StartX=68.65 StartY=44.65 StartZ=0 EndX=68.65 EndY=31.55 EndZ=0
    g32: LineSegment StartX=69.65 StartY=30.55 StartZ=0 EndX=82.75 EndY=30.55 EndZ=0
    g33: LineSegment StartX=83.75 StartY=31.55 StartZ=0 EndX=83.75 EndY=44.65 EndZ=0
    g34: GeomPoint [constr] X=76.2 Y=38.1 Z=0
    g35: LineSegment StartX=120.85 StartY=26.6 StartZ=0 EndX=107.75 EndY=26.6 EndZ=0
    g36: LineSegment StartX=106.75 StartY=25.6 StartZ=0 EndX=106.75 EndY=12.5 EndZ=0
    g37: LineSegment StartX=107.75 StartY=11.5 StartZ=0 EndX=120.85 EndY=11.5 EndZ=0
    g38: LineSegment StartX=121.85 StartY=12.5 StartZ=0 EndX=121.85 EndY=25.6 EndZ=0
    g39: GeomPoint [constr] X=114.3 Y=19.05 Z=0
    g40: LineSegment StartX=101.8 StartY=45.65 StartZ=0 EndX=88.7 EndY=45.65 EndZ=0
    g41: LineSegment StartX=87.7 StartY=44.65 StartZ=0 EndX=87.7 EndY=31.55 EndZ=0
    g42: LineSegment StartX=88.7 StartY=30.55 StartZ=0 EndX=101.8 EndY=30.55 EndZ=0
    g43: LineSegment StartX=102.8 StartY=31.55 StartZ=0 EndX=102.8 EndY=44.65 EndZ=0
    g44: GeomPoint [constr] X=95.25 Y=38.1 Z=0
    g45: LineSegment StartX=44.65 StartY=64.7 StartZ=0 EndX=31.55 EndY=64.7 EndZ=0
    g46: LineSegment StartX=30.55 StartY=63.7 StartZ=0 EndX=30.55 EndY=50.6 EndZ=0
    g47: LineSegment StartX=31.55 StartY=49.6 StartZ=0 EndX=44.65 EndY=49.6 EndZ=0
    g48: LineSegment StartX=45.65 StartY=50.6 StartZ=0 EndX=45.65 EndY=63.7 EndZ=0
    g49: GeomPoint [constr] X=38.1 Y=57.15 Z=0
    g50: LineSegment StartX=63.7 StartY=64.7 StartZ=0 EndX=50.6 EndY=64.7 EndZ=0
    g51: LineSegment StartX=49.6 StartY=63.7 StartZ=0 EndX=49.6 EndY=50.6 EndZ=0
    g52: LineSegment StartX=50.6 StartY=49.6 StartZ=0 EndX=63.7 EndY=49.6 EndZ=0
    g53: LineSegment StartX=64.7 StartY=50.6 StartZ=0 EndX=64.7 EndY=63.7 EndZ=0
    g54: GeomPoint [constr] X=57.15 Y=57.15 Z=0
    g55: LineSegment StartX=82.75 StartY=64.7 StartZ=0 EndX=69.65 EndY=64.7 EndZ=0
    g56: LineSegment StartX=68.65 StartY=63.7 StartZ=0 EndX=68.65 EndY=50.6 EndZ=0
    g57: LineSegment StartX=69.65 StartY=49.6 StartZ=0 EndX=82.75 EndY=49.6 EndZ=0
    g58: LineSegment StartX=83.75 StartY=50.6 StartZ=0 EndX=83.75 EndY=63.7 EndZ=0
    g59: GeomPoint [constr] X=76.2 Y=57.15 Z=0
    g60: LineSegment StartX=101.8 StartY=64.7 StartZ=0 EndX=88.7 EndY=64.7 EndZ=0
    g61: LineSegment StartX=87.7 StartY=63.7 StartZ=0 EndX=87.7 EndY=50.6 EndZ=0
    g62: LineSegment StartX=88.7 StartY=49.6 StartZ=0 EndX=101.8 EndY=49.6 EndZ=0
    g63: LineSegment StartX=102.8 StartY=50.6 StartZ=0 EndX=102.8 EndY=63.7 EndZ=0
    g64: GeomPoint [constr] X=95.25 Y=57.15 Z=0
    g65: LineSegment StartX=44.65 StartY=83.75 StartZ=0 EndX=31.55 EndY=83.75 EndZ=0
    g66: LineSegment StartX=30.55 StartY=82.75 StartZ=0 EndX=30.55 EndY=69.65 EndZ=0
    g67: LineSegment StartX=31.55 StartY=68.65 StartZ=0 EndX=44.65 EndY=68.65 EndZ=0
    g68: LineSegment StartX=45.65 StartY=69.65 StartZ=0 EndX=45.65 EndY=82.75 EndZ=0
    g69: GeomPoint [constr] X=38.1 Y=76.2 Z=0
    g70: LineSegment StartX=63.7 StartY=83.75 StartZ=0 EndX=50.6 EndY=83.75 EndZ=0
    g71: LineSegment StartX=49.6 StartY=82.75 StartZ=0 EndX=49.6 EndY=69.65 EndZ=0
    g72: LineSegment StartX=50.6 StartY=68.65 StartZ=0 EndX=63.7 EndY=68.65 EndZ=0
    g73: LineSegment StartX=64.7 StartY=69.65 StartZ=0 EndX=64.7 EndY=82.75 EndZ=0
    g74: GeomPoint [constr] X=57.15 Y=76.2 Z=0
    g75: LineSegment StartX=82.75 StartY=83.75 StartZ=0 EndX=69.65 EndY=83.75 EndZ=0
    g76: LineSegment StartX=68.65 StartY=82.75 StartZ=0 EndX=68.65 EndY=69.65 EndZ=0
    g77: LineSegment StartX=69.65 StartY=68.65 StartZ=0 EndX=82.75 EndY=68.65 EndZ=0
    g78: LineSegment StartX=83.75 StartY=69.65 StartZ=0 EndX=83.75 EndY=82.75 EndZ=0
    g79: GeomPoint [constr] X=76.2 Y=76.2 Z=0
    g80: LineSegment StartX=101.8 StartY=83.75 StartZ=0 EndX=88.7 EndY=83.75 EndZ=0
    g81: LineSegment StartX=87.7 StartY=82.75 StartZ=0 EndX=87.7 EndY=69.65 EndZ=0
    g82: LineSegment StartX=88.7 StartY=68.65 StartZ=0 EndX=101.8 EndY=68.65 EndZ=0
    g83: LineSegment StartX=102.8 StartY=69.65 StartZ=0 EndX=102.8 EndY=82.75 EndZ=0
    g84: GeomPoint [constr] X=95.25 Y=76.2 Z=0
    g85: LineSegment StartX=120.85 StartY=83.75 StartZ=0 EndX=107.75 EndY=83.75 EndZ=0
    g86: LineSegment StartX=106.75 StartY=82.75 StartZ=0 EndX=106.75 EndY=69.65 EndZ=0
    g87: LineSegment StartX=107.75 StartY=68.65 StartZ=0 EndX=120.85 EndY=68.65 EndZ=0
    g88: LineSegment StartX=121.85 StartY=69.65 StartZ=0 EndX=121.85 EndY=82.75 EndZ=0
    g89: GeomPoint [constr] X=114.3 Y=76.2 Z=0
    g90: LineSegment StartX=120.85 StartY=64.7 StartZ=0 EndX=107.75 EndY=64.7 EndZ=0
    g91: LineSegment StartX=106.75 StartY=63.7 StartZ=0 EndX=106.75 EndY=50.6 EndZ=0
    g92: LineSegment StartX=107.75 StartY=49.6 StartZ=0 EndX=120.85 EndY=49.6 EndZ=0
    g93: LineSegment StartX=121.85 StartY=50.6 StartZ=0 EndX=121.85 EndY=63.7 EndZ=0
    g94: GeomPoint [constr] X=114.3 Y=57.15 Z=0
    g95: LineSegment StartX=120.85 StartY=45.65 StartZ=0 EndX=107.75 EndY=45.65 EndZ=0
    g96: LineSegment StartX=106.75 StartY=44.65 StartZ=0 EndX=106.75 EndY=31.55 EndZ=0
    g97: LineSegment StartX=107.75 StartY=30.55 StartZ=0 EndX=120.85 EndY=30.55 EndZ=0
    g98: LineSegment StartX=121.85 StartY=31.55 StartZ=0 EndX=121.85 EndY=44.65 EndZ=0
    g99: GeomPoint [constr] X=114.3 Y=38.1 Z=0
    g100: LineSegment StartX=139.9 StartY=26.6 StartZ=0 EndX=126.8 EndY=26.6 EndZ=0
    g101: LineSegment StartX=125.8 StartY=25.6 StartZ=0 EndX=125.8 EndY=12.5 EndZ=0
    g102: LineSegment StartX=126.8 StartY=11.5 StartZ=0 EndX=139.9 EndY=11.5 EndZ=0
    g103: LineSegment StartX=140.9 StartY=12.5 StartZ=0 EndX=140.9 EndY=25.6 EndZ=0
    g104: GeomPoint [constr] X=133.35 Y=19.05 Z=0
    g105: LineSegment StartX=25.6 StartY=26.6 StartZ=0 EndX=12.5 EndY=26.6 EndZ=0
    g106: LineSegment StartX=11.5 StartY=25.6 StartZ=0 EndX=11.5 EndY=12.5 EndZ=0
    g107: LineSegment StartX=12.5 StartY=11.5 StartZ=0 EndX=25.6 EndY=11.5 EndZ=0
    g108: LineSegment StartX=26.6 StartY=12.5 StartZ=0 EndX=26.6 EndY=25.6 EndZ=0
    g109: GeomPoint [constr] X=19.05 Y=19.05 Z=0
    g110: LineSegment StartX=139.9 StartY=45.65 StartZ=0 EndX=126.8 EndY=45.65 EndZ=0
    g111: LineSegment StartX=125.8 StartY=44.65 StartZ=0 EndX=125.8 EndY=31.55 EndZ=0
    g112: LineSegment StartX=126.8 StartY=30.55 StartZ=0 EndX=139.9 EndY=30.55 EndZ=0
    g113: LineSegment StartX=140.9 StartY=31.55 StartZ=0 EndX=140.9 EndY=44.65 EndZ=0
    g114: GeomPoint [constr] X=133.35 Y=38.1 Z=0
    g115: LineSegment StartX=139.9 StartY=64.7 StartZ=0 EndX=126.8 EndY=64.7 EndZ=0
    g116: LineSegment StartX=125.8 StartY=63.7 StartZ=0 EndX=125.8 EndY=50.6 EndZ=0
    g117: LineSegment StartX=126.8 StartY=49.6 StartZ=0 EndX=139.9 EndY=49.6 EndZ=0
    g118: LineSegment StartX=140.9 StartY=50.6 StartZ=0 EndX=140.9 EndY=63.7 EndZ=0
    g119: GeomPoint [constr] X=133.35 Y=57.15 Z=0
    g120: LineSegment StartX=139.9 StartY=83.75 StartZ=0 EndX=126.8 EndY=83.75 EndZ=0
    g121: LineSegment StartX=125.8 StartY=82.75 StartZ=0 EndX=125.8 EndY=69.65 EndZ=0
    g122: LineSegment StartX=126.8 StartY=68.65 StartZ=0 EndX=139.9 EndY=68.65 EndZ=0
    g123: LineSegment StartX=140.9 StartY=69.65 StartZ=0 EndX=140.9 EndY=82.75 EndZ=0
    g124: GeomPoint [constr] X=133.35 Y=76.2 Z=0
    g125: ArcOfCircle CenterX=31.55 CenterY=82.75 CenterZ=0 NormalX=0 NormalY=0 NormalZ=1 AngleXU=0 Radius=1 StartAngle=1.5708 EndAngle=3.14159
    g126: GeomPoint [constr] X=30.55 Y=83.75 Z=0
    g127: ArcOfCircle CenterX=44.65 CenterY=82.75 CenterZ=0 NormalX=0 NormalY=0 NormalZ=1 AngleXU=0 Radius=1 StartAngle=6.8e-15 EndAngle=1.5708
    g128: GeomPoint [constr] X=45.65 Y=83.75 Z=0
    g129: ArcOfCircle CenterX=44.65 CenterY=69.65 CenterZ=0 NormalX=0 NormalY=0 NormalZ=1 AngleXU=0 Radius=1 StartAngle=4.71239 EndAngle=6.28319
    g130: GeomPoint [constr] X=45.65 Y=68.65 Z=0
    g131: ArcOfCircle CenterX=31.55 CenterY=69.65 CenterZ=0 NormalX=0 NormalY=0 NormalZ=1 AngleXU=0 Radius=1 StartAngle=3.14159 EndAngle=4.71239
    g132: GeomPoint [constr] X=30.55 Y=68.65 Z=0
    g133: ArcOfCircle CenterX=50.6 CenterY=82.75 CenterZ=0 NormalX=0 NormalY=0 NormalZ=1 AngleXU=0 Radius=1 StartAngle=1.5708 EndAngle=3.14159
    g134: GeomPoint [constr] X=49.6 Y=83.75 Z=0
    g135: ArcOfCircle CenterX=63.7 CenterY=82.75 CenterZ=0 NormalX=0 NormalY=0 NormalZ=1 AngleXU=0 Radius=1 StartAngle=-2.7e-15 EndAngle=1.5708
    g136: GeomPoint [constr] X=64.7 Y=83.75 Z=0
    g137: ArcOfCircle CenterX=63.7 CenterY=69.65 CenterZ=0 NormalX=0 NormalY=0 NormalZ=1 AngleXU=0 Radius=1 StartAngle=4.71239 EndAngle=6.28319
    g138: GeomPoint [constr] X=64.7 Y=68.65 Z=0
    g139: ArcOfCircle CenterX=50.6 CenterY=69.65 CenterZ=0 NormalX=0 NormalY=0 NormalZ=1 AngleXU=0 Radius=1 StartAngle=3.14159 EndAngle=4.71239
    g140: GeomPoint [constr] X=49.6 Y=68.65 Z=0
    g141: ArcOfCircle CenterX=69.65 CenterY=82.75 CenterZ=0 NormalX=0 NormalY=0 NormalZ=1 AngleXU=0 Radius=1 StartAngle=1.5708 EndAngle=3.14159
    g142: GeomPoint [constr] X=68.65 Y=83.75 Z=0
    g143: ArcOfCircle CenterX=82.75 CenterY=82.75 CenterZ=0 NormalX=0 NormalY=0 NormalZ=1 AngleXU=0 Radius=1 StartAngle=-6.2e-15 EndAngle=1.5708
    g144: GeomPoint [constr] X=83.75 Y=83.75 Z=0
    g145: ArcOfCircle CenterX=82.75 CenterY=69.65 CenterZ=0 NormalX=0 NormalY=0 NormalZ=1 AngleXU=0 Radius=1 StartAngle=4.71239 EndAngle=6.28319
    g146: GeomPoint [constr] X=83.75 Y=68.65 Z=0
    g147: ArcOfCircle CenterX=69.65 CenterY=69.65 CenterZ=0 NormalX=0 NormalY=0 NormalZ=1 AngleXU=0 Radius=1 StartAngle=3.14159 EndAngle=4.71239
    g148: GeomPoint [constr] X=68.65 Y=68.65 Z=0
    g149: ArcOfCircle CenterX=88.7 CenterY=82.75 CenterZ=0 NormalX=0 NormalY=0 NormalZ=1 AngleXU=0 Radius=1 StartAngle=1.5708 EndAngle=3.14159
    g150: GeomPoint [constr] X=87.7 Y=83.75 Z=0
    g151: ArcOfCircle CenterX=101.8 CenterY=82.75 CenterZ=0 NormalX=0 NormalY=0 NormalZ=1 AngleXU=0 Radius=1 StartAngle=-1.8e-15 EndAngle=1.5708
    g152: GeomPoint [constr] X=102.8 Y=83.75 Z=0
    g153: ArcOfCircle CenterX=101.8 CenterY=69.65 CenterZ=0 NormalX=0 NormalY=0 NormalZ=1 AngleXU=0 Radius=1 StartAngle=4.71239 EndAngle=6.28319
    g154: GeomPoint [constr] X=102.8 Y=68.65 Z=0
    g155: ArcOfCircle CenterX=88.7 CenterY=69.65 CenterZ=0 NormalX=0 NormalY=0 NormalZ=1 AngleXU=0 Radius=1 StartAngle=3.14159 EndAngle=4.71239
    g156: GeomPoint [constr] X=87.7 Y=68.65 Z=0
    g157: ArcOfCircle CenterX=107.75 CenterY=82.75 CenterZ=0 NormalX=0 NormalY=0 NormalZ=1 AngleXU=0 Radius=1 StartAngle=1.5708 EndAngle=3.14159
    g158: GeomPoint [constr] X=106.75 Y=83.75 Z=0
    g159: ArcOfCircle CenterX=120.85 CenterY=82.75 CenterZ=0 NormalX=0 NormalY=0 NormalZ=1 AngleXU=0 Radius=1 StartAngle=0 EndAngle=1.5708
    g160: GeomPoint [constr] X=121.85 Y=83.75 Z=0
    g161: ArcOfCircle CenterX=120.85 CenterY=69.65 CenterZ=0 NormalX=0 NormalY=0 NormalZ=1 AngleXU=0 Radius=1 StartAngle=4.71239 EndAngle=6.28319
    g162: GeomPoint [constr] X=121.85 Y=68.65 Z=0
    g163: ArcOfCircle CenterX=107.75 CenterY=69.65 CenterZ=0 NormalX=0 NormalY=0 NormalZ=1 AngleXU=0 Radius=1 StartAngle=3.14159 EndAngle=4.71239
    g164: GeomPoint [constr] X=106.75 Y=68.65 Z=0
    g165: ArcOfCircle CenterX=126.8 CenterY=82.75 CenterZ=0 NormalX=0 NormalY=0 NormalZ=1 AngleXU=0 Radius=1 StartAngle=1.5708 EndAngle=3.14159
    g166: GeomPoint [constr] X=125.8 Y=83.75 Z=0
    g167: ArcOfCircle CenterX=139.9 CenterY=82.75 CenterZ=0 NormalX=0 NormalY=0 NormalZ=1 AngleXU=0 Radius=1 StartAngle=-1.8e-15 EndAngle=1.5708
    g168: GeomPoint [constr] X=140.9 Y=83.75 Z=0
    g169: ArcOfCircle CenterX=126.8 CenterY=69.65 CenterZ=0 NormalX=0 NormalY=0 NormalZ=1 AngleXU=0 Radius=1 StartAngle=3.14159 EndAngle=4.71239
    g170: GeomPoint [constr] X=125.8 Y=68.65 Z=0
    g171: ArcOfCircle CenterX=139.9 CenterY=69.65 CenterZ=0 NormalX=0 NormalY=0 NormalZ=1 AngleXU=0 Radius=1 StartAngle=4.71239 EndAngle=6.28319
    g172: GeomPoint [constr] X=140.9 Y=68.65 Z=0
    g173: ArcOfCircle CenterX=31.55 CenterY=63.7 CenterZ=0 NormalX=0 NormalY=0 NormalZ=1 AngleXU=0 Radius=1 StartAngle=1.5708 EndAngle=3.14159
    g174: GeomPoint [constr] X=30.55 Y=64.7 Z=0
    g175: ArcOfCircle CenterX=44.65 CenterY=63.7 CenterZ=0 NormalX=0 NormalY=0 NormalZ=1 AngleXU=0 Radius=1 StartAngle=-1.8e-15 EndAngle=1.5708
    g176: GeomPoint [constr] X=45.65 Y=64.7 Z=0
    g177: ArcOfCircle CenterX=44.65 CenterY=50.6 CenterZ=0 NormalX=0 NormalY=0 NormalZ=1 AngleXU=0 Radius=1 StartAngle=4.71239 EndAngle=6.28319
    g178: GeomPoint [constr] X=45.65 Y=49.6 Z=0
    g179: ArcOfCircle CenterX=31.55 CenterY=50.6 CenterZ=0 NormalX=0 NormalY=0 NormalZ=1 AngleXU=0 Radius=1 StartAngle=3.14159 EndAngle=4.71239
    g180: GeomPoint [constr] X=30.55 Y=49.6 Z=0
    g181: ArcOfCircle CenterX=50.6 CenterY=63.7 CenterZ=0 NormalX=0 NormalY=0 NormalZ=1 AngleXU=0 Radius=1 StartAngle=1.5708 EndAngle=3.14159
    g182: GeomPoint [constr] X=49.6 Y=64.7 Z=0
    g183: ArcOfCircle CenterX=63.7 CenterY=63.7 CenterZ=0 NormalX=0 NormalY=0 NormalZ=1 AngleXU=0 Radius=1 StartAngle=-2.7e-15 EndAngle=1.5708
    g184: GeomPoint [constr] X=64.7 Y=64.7 Z=0
    g185: ArcOfCircle CenterX=63.7 CenterY=50.6 CenterZ=0 NormalX=0 NormalY=0 NormalZ=1 AngleXU=0 Radius=1 StartAngle=4.71239 EndAngle=6.28319
    g186: GeomPoint [constr] X=64.7 Y=49.6 Z=0
    g187: ArcOfCircle CenterX=50.6 CenterY=50.6 CenterZ=0 NormalX=0 NormalY=0 NormalZ=1 AngleXU=0 Radius=1 StartAngle=3.14159 EndAngle=4.71239
    g188: GeomPoint [constr] X=49.6 Y=49.6 Z=0
    g189: ArcOfCircle CenterX=69.65 CenterY=63.7 CenterZ=0 NormalX=0 NormalY=0 NormalZ=1 AngleXU=0 Radius=1 StartAngle=1.5708 EndAngle=3.14159
    g190: GeomPoint [constr] X=68.65 Y=64.7 Z=0
    g191: ArcOfCircle CenterX=82.75 CenterY=63.7 CenterZ=0 NormalX=0 NormalY=0 NormalZ=1 AngleXU=0 Radius=1 StartAngle=-1.8e-15 EndAngle=1.5708
    g192: GeomPoint [constr] X=83.75 Y=64.7 Z=0
    g193: ArcOfCircle CenterX=82.75 CenterY=50.6 CenterZ=0 NormalX=0 NormalY=0 NormalZ=1 AngleXU=0 Radius=1 StartAngle=4.71239 EndAngle=6.28319
    g194: GeomPoint [constr] X=83.75 Y=49.6 Z=0
    g195: ArcOfCircle CenterX=69.65 CenterY=50.6 CenterZ=0 NormalX=0 NormalY=0 NormalZ=1 AngleXU=0 Radius=1 StartAngle=3.14159 EndAngle=4.71239
    g196: GeomPoint [constr] X=68.65 Y=49.6 Z=0
    g197: ArcOfCircle CenterX=88.7 CenterY=63.7 CenterZ=0 NormalX=0 NormalY=0 NormalZ=1 AngleXU=0 Radius=1 StartAngle=1.5708 EndAngle=3.14159
    g198: GeomPoint [constr] X=87.7 Y=64.7 Z=0
    g199: ArcOfCircle CenterX=101.8 CenterY=63.7 CenterZ=0 NormalX=0 NormalY=0 NormalZ=1 AngleXU=0 Radius=1 StartAngle=-2.7e-15 EndAngle=1.5708
    g200: GeomPoint [constr] X=102.8 Y=64.7 Z=0
    g201: ArcOfCircle CenterX=101.8 CenterY=50.6 CenterZ=0 NormalX=0 NormalY=0 NormalZ=1 AngleXU=0 Radius=1 StartAngle=4.71239 EndAngle=6.28319
    g202: GeomPoint [constr] X=102.8 Y=49.6 Z=0
    g203: ArcOfCircle CenterX=88.7 CenterY=50.6 CenterZ=0 NormalX=0 NormalY=0 NormalZ=1 AngleXU=0 Radius=1 StartAngle=3.14159 EndAngle=4.71239
    g204: GeomPoint [constr] X=87.7 Y=49.6 Z=0
    g205: ArcOfCircle CenterX=107.75 CenterY=63.7 CenterZ=0 NormalX=0 NormalY=0 NormalZ=1 AngleXU=0 Radius=1 StartAngle=1.5708 EndAngle=3.14159
    g206: GeomPoint [constr] X=106.75 Y=64.7 Z=0
    g207: ArcOfCircle CenterX=120.85 CenterY=63.7 CenterZ=0 NormalX=0 NormalY=0 NormalZ=1 AngleXU=0 Radius=1 StartAngle=3e-15 EndAngle=1.5708
    g208: GeomPoint [constr] X=121.85 Y=64.7 Z=0
    g209: ArcOfCircle CenterX=120.85 CenterY=50.6 CenterZ=0 NormalX=0 NormalY=0 NormalZ=1 AngleXU=0 Radius=1 StartAngle=4.71239 EndAngle=6.28319
    g210: GeomPoint [constr] X=121.85 Y=49.6 Z=0
    g211: ArcOfCircle CenterX=107.75 CenterY=50.6 CenterZ=0 NormalX=0 NormalY=0 NormalZ=1 AngleXU=0 Radius=1 StartAngle=3.14159 EndAngle=4.71239
    g212: GeomPoint [constr] X=106.75 Y=49.6 Z=0
    g213: ArcOfCircle CenterX=126.8 CenterY=63.7 CenterZ=0 NormalX=0 NormalY=0 NormalZ=1 AngleXU=0 Radius=1 StartAngle=1.5708 EndAngle=3.14159
    g214: GeomPoint [constr] X=125.8 Y=64.7 Z=0
    g215: ArcOfCircle CenterX=139.9 CenterY=63.7 CenterZ=0 NormalX=0 NormalY=0 NormalZ=1 AngleXU=0 Radius=1 StartAngle=-1.8e-15 EndAngle=1.5708
    g216: GeomPoint [constr] X=140.9 Y=64.7 Z=0
    g217: ArcOfCircle CenterX=139.9 CenterY=50.6 CenterZ=0 NormalX=0 NormalY=0 NormalZ=1 AngleXU=0 Radius=1 StartAngle=4.71239 EndAngle=6.28319
    g218: GeomPoint [constr] X=140.9 Y=49.6 Z=0
    g219: ArcOfCircle CenterX=126.8 CenterY=50.6 CenterZ=0 NormalX=0 NormalY=0 NormalZ=1 AngleXU=0 Radius=1 StartAngle=3.14159 EndAngle=4.71239
    g220: GeomPoint [constr] X=125.8 Y=49.6 Z=0
    g221: ArcOfCircle CenterX=31.55 CenterY=44.65 CenterZ=0 NormalX=0 NormalY=0 NormalZ=1 AngleXU=0 Radius=1 StartAngle=1.5708 EndAngle=3.14159
    g222: GeomPoint [constr] X=30.55 Y=45.65 Z=0
    g223: ArcOfCircle CenterX=44.65 CenterY=44.65 CenterZ=0 NormalX=0 NormalY=0 NormalZ=1 AngleXU=0 Radius=1 StartAngle=-2.7e-15 EndAngle=1.5708
    g224: GeomPoint [constr] X=45.65 Y=45.65 Z=0
    g225: ArcOfCircle CenterX=44.65 CenterY=31.55 CenterZ=0 NormalX=0 NormalY=0 NormalZ=1 AngleXU=0 Radius=1 StartAngle=4.71239 EndAngle=6.28319
    g226: GeomPoint [constr] X=45.65 Y=30.55 Z=0
    g227: ArcOfCircle CenterX=31.55 CenterY=31.55 CenterZ=0 NormalX=0 NormalY=0 NormalZ=1 AngleXU=0 Radius=1 StartAngle=3.14159 EndAngle=4.71239
    g228: GeomPoint [constr] X=30.55 Y=30.55 Z=0
    g229: ArcOfCircle CenterX=50.6 CenterY=44.65 CenterZ=0 NormalX=0 NormalY=0 NormalZ=1 AngleXU=0 Radius=1 StartAngle=1.5708 EndAngle=3.14159
    g230: GeomPoint [constr] X=49.6 Y=45.65 Z=0
    g231: ArcOfCircle CenterX=63.7 CenterY=44.65 CenterZ=0 NormalX=0 NormalY=0 NormalZ=1 AngleXU=0 Radius=1 StartAngle=1e-15 EndAngle=1.5708
    g232: GeomPoint [constr] X=64.7 Y=45.65 Z=0
    g233: ArcOfCircle CenterX=63.7 CenterY=31.55 CenterZ=0 NormalX=0 NormalY=0 NormalZ=1 AngleXU=0 Radius=1 StartAngle=4.71239 EndAngle=6.28319
    g234: GeomPoint [constr] X=64.7 Y=30.55 Z=0
    g235: ArcOfCircle CenterX=50.6 CenterY=31.55 CenterZ=0 NormalX=0 NormalY=0 NormalZ=1 AngleXU=0 Radius=1 StartAngle=3.14159 EndAngle=4.71239
    g236: GeomPoint [constr] X=49.6 Y=30.55 Z=0
    g237: ArcOfCircle CenterX=69.65 CenterY=44.65 CenterZ=0 NormalX=0 NormalY=0 NormalZ=1 AngleXU=0 Radius=1 StartAngle=1.5708 EndAngle=3.14159
    g238: GeomPoint [constr] X=68.65 Y=45.65 Z=0
    g239: ArcOfCircle CenterX=82.75 CenterY=44.65 CenterZ=0 NormalX=0 NormalY=0 NormalZ=1 AngleXU=0 Radius=1 StartAngle=-2.7e-15 EndAngle=1.5708
    g240: GeomPoint [constr] X=83.75 Y=45.65 Z=0
    g241: ArcOfCircle CenterX=82.75 CenterY=31.55 CenterZ=0 NormalX=0 NormalY=0 NormalZ=1 AngleXU=0 Radius=1 StartAngle=4.71239 EndAngle=6.28319
    g242: GeomPoint [constr] X=83.75 Y=30.55 Z=0
    g243: ArcOfCircle CenterX=69.65 CenterY=31.55 CenterZ=0 NormalX=0 NormalY=0 NormalZ=1 AngleXU=0 Radius=1 StartAngle=3.14159 EndAngle=4.71239
    g244: GeomPoint [constr] X=68.65 Y=30.55 Z=0
    g245: ArcOfCircle CenterX=88.7 CenterY=44.65 CenterZ=0 NormalX=0 NormalY=0 NormalZ=1 AngleXU=0 Radius=1 StartAngle=1.5708 EndAngle=3.14159
    g246: GeomPoint [constr] X=87.7 Y=45.65 Z=0
    g247: ArcOfCircle CenterX=101.8 CenterY=44.65 CenterZ=0 NormalX=0 NormalY=0 NormalZ=1 AngleXU=0 Radius=1 StartAngle=1.1e-15 EndAngle=1.5708
    g248: GeomPoint [constr] X=102.8 Y=45.65 Z=0
    g249: ArcOfCircle CenterX=101.8 CenterY=31.55 CenterZ=0 NormalX=0 NormalY=0 NormalZ=1 AngleXU=0 Radius=1 StartAngle=4.71239 EndAngle=6.28319
    g250: GeomPoint [constr] X=102.8 Y=30.55 Z=0
    g251: ArcOfCircle CenterX=88.7 CenterY=31.55 CenterZ=0 NormalX=0 NormalY=0 NormalZ=1 AngleXU=0 Radius=1 StartAngle=3.14159 EndAngle=4.71239
    g252: GeomPoint [constr] X=87.7 Y=30.55 Z=0
    g253: ArcOfCircle CenterX=107.75 CenterY=44.65 CenterZ=0 NormalX=0 NormalY=0 NormalZ=1 AngleXU=0 Radius=1 StartAngle=1.5708 EndAngle=3.14159
    g254: GeomPoint [constr] X=106.75 Y=45.65 Z=0
    g255: ArcOfCircle CenterX=120.85 CenterY=44.65 CenterZ=0 NormalX=0 NormalY=0 NormalZ=1 AngleXU=0 Radius=1 StartAngle=1e-15 EndAngle=1.5708
    g256: GeomPoint [constr] X=121.85 Y=45.65 Z=0
    g257: ArcOfCircle CenterX=120.85 CenterY=31.55 CenterZ=0 NormalX=0 NormalY=0 NormalZ=1 AngleXU=0 Radius=1 StartAngle=4.71239 EndAngle=6.28319
    g258: GeomPoint [constr] X=121.85 Y=30.55 Z=0
    g259: ArcOfCircle CenterX=107.75 CenterY=31.55 CenterZ=0 NormalX=0 NormalY=0 NormalZ=1 AngleXU=0 Radius=1 StartAngle=3.14159 EndAngle=4.71239
    g260: GeomPoint [constr] X=106.75 Y=30.55 Z=0
    g261: ArcOfCircle CenterX=126.8 CenterY=44.65 CenterZ=0 NormalX=0 NormalY=0 NormalZ=1 AngleXU=0 Radius=1 StartAngle=1.5708 EndAngle=3.14159
    g262: GeomPoint [constr] X=125.8 Y=45.65 Z=0
    g263: ArcOfCircle CenterX=139.9 CenterY=44.65 CenterZ=0 NormalX=0 NormalY=0 NormalZ=1 AngleXU=0 Radius=1 StartAngle=1.4e-15 EndAngle=1.5708
    g264: GeomPoint [constr] X=140.9 Y=45.65 Z=0
    g265: ArcOfCircle CenterX=139.9 CenterY=31.55 CenterZ=0 NormalX=0 NormalY=0 NormalZ=1 AngleXU=0 Radius=1 StartAngle=4.71239 EndAngle=6.28319
    g266: GeomPoint [constr] X=140.9 Y=30.55 Z=0
    g267: ArcOfCircle CenterX=126.8 CenterY=31.55 CenterZ=0 NormalX=0 NormalY=0 NormalZ=1 AngleXU=0 Radius=1 StartAngle=3.14159 EndAngle=4.71239
    g268: GeomPoint [constr] X=125.8 Y=30.55 Z=0
    g269: ArcOfCircle CenterX=31.55 CenterY=25.6 CenterZ=0 NormalX=0 NormalY=0 NormalZ=1 AngleXU=0 Radius=1 StartAngle=1.5708 EndAngle=3.14159
    g270: GeomPoint [constr] X=30.55 Y=26.6 Z=0
    g271: ArcOfCircle CenterX=44.65 CenterY=25.6 CenterZ=0 NormalX=0 NormalY=0 NormalZ=1 AngleXU=0 Radius=1 StartAngle=-9e-16 EndAngle=1.5708
    g272: GeomPoint [constr] X=45.65 Y=26.6 Z=0
    g273: ArcOfCircle CenterX=44.65 CenterY=12.5 CenterZ=0 NormalX=0 NormalY=0 NormalZ=1 AngleXU=0 Radius=1 StartAngle=4.71239 EndAngle=6.28319
    g274: GeomPoint [constr] X=45.65 Y=11.5 Z=0
    g275: ArcOfCircle CenterX=31.55 CenterY=12.5 CenterZ=0 NormalX=0 NormalY=0 NormalZ=1 AngleXU=0 Radius=1 StartAngle=3.14159 EndAngle=4.71239
    g276: GeomPoint [constr] X=30.55 Y=11.5 Z=0
    g277: ArcOfCircle CenterX=50.6 CenterY=25.6 CenterZ=0 NormalX=0 NormalY=0 NormalZ=1 AngleXU=0 Radius=1 StartAngle=1.5708 EndAngle=3.14159
    g278: GeomPoint [constr] X=49.6 Y=26.6 Z=0
    g279: ArcOfCircle CenterX=63.7 CenterY=25.6 CenterZ=0 NormalX=0 NormalY=0 NormalZ=1 AngleXU=0 Radius=1 StartAngle=-9e-16 EndAngle=1.5708
    g280: GeomPoint [constr] X=64.7 Y=26.6 Z=0
    g281: ArcOfCircle CenterX=63.7 CenterY=12.5 CenterZ=0 NormalX=0 NormalY=0 NormalZ=1 AngleXU=0 Radius=1 StartAngle=4.71239 EndAngle=6.28319
    g282: GeomPoint [constr] X=64.7 Y=11.5 Z=0
    g283: ArcOfCircle CenterX=50.6 CenterY=12.5 CenterZ=0 NormalX=0 NormalY=0 NormalZ=1 AngleXU=0 Radius=1 StartAngle=3.14159 EndAngle=4.71239
    g284: GeomPoint [constr] X=49.6 Y=11.5 Z=0
    g285: ArcOfCircle CenterX=69.65 CenterY=25.6 CenterZ=0 NormalX=0 NormalY=0 NormalZ=1 AngleXU=0 Radius=1 StartAngle=1.5708 EndAngle=3.14159
    g286: GeomPoint [constr] X=68.65 Y=26.6 Z=0
    g287: ArcOfCircle CenterX=82.75 CenterY=25.6 CenterZ=0 NormalX=0 NormalY=0 NormalZ=1 AngleXU=0 Radius=1 StartAngle=-9e-16 EndAngle=1.5708
    g288: GeomPoint [constr] X=83.75 Y=26.6 Z=0
    g289: ArcOfCircle CenterX=82.75 CenterY=12.5 CenterZ=0 NormalX=0 NormalY=0 NormalZ=1 AngleXU=0 Radius=1 StartAngle=4.71239 EndAngle=6.28319
    g290: GeomPoint [constr] X=83.75 Y=11.5 Z=0
    g291: ArcOfCircle CenterX=69.65 CenterY=12.5 CenterZ=0 NormalX=0 NormalY=0 NormalZ=1 AngleXU=0 Radius=1 StartAngle=3.14159 EndAngle=4.71239
    g292: GeomPoint [constr] X=68.65 Y=11.5 Z=0
    g293: ArcOfCircle CenterX=88.7 CenterY=25.6 CenterZ=0 NormalX=0 NormalY=0 NormalZ=1 AngleXU=0 Radius=1 StartAngle=1.5708 EndAngle=3.14159
    g294: GeomPoint [constr] X=87.7 Y=26.6 Z=0
    g295: ArcOfCircle CenterX=101.8 CenterY=25.6 CenterZ=0 NormalX=0 NormalY=0 NormalZ=1 AngleXU=0 Radius=1 StartAngle=-1.8e-15 EndAngle=1.5708
    g296: GeomPoint [constr] X=102.8 Y=26.6 Z=0
    g297: ArcOfCircle CenterX=101.8 CenterY=12.5 CenterZ=0 NormalX=0 NormalY=0 NormalZ=1 AngleXU=0 Radius=1 StartAngle=4.71239 EndAngle=6.28319
    g298: GeomPoint [constr] X=102.8 Y=11.5 Z=0
    g299: ArcOfCircle CenterX=88.7 CenterY=12.5 CenterZ=0 NormalX=0 NormalY=0 NormalZ=1 AngleXU=0 Radius=1 StartAngle=3.14159 EndAngle=4.71239
    g300: GeomPoint [constr] X=87.7 Y=11.5 Z=0
    g301: ArcOfCircle CenterX=107.75 CenterY=25.6 CenterZ=0 NormalX=0 NormalY=0 NormalZ=1 AngleXU=0 Radius=1 StartAngle=1.5708 EndAngle=3.14159
    g302: GeomPoint [constr] X=106.75 Y=26.6 Z=0
    g303: ArcOfCircle CenterX=120.85 CenterY=25.6 CenterZ=0 NormalX=0 NormalY=0 NormalZ=1 AngleXU=0 Radius=1 StartAngle=-9e-16 EndAngle=1.5708
    g304: GeomPoint [constr] X=121.85 Y=26.6 Z=0
    g305: ArcOfCircle CenterX=120.85 CenterY=12.5 CenterZ=0 NormalX=0 NormalY=0 NormalZ=1 AngleXU=0 Radius=1 StartAngle=4.71239 EndAngle=6.28319
    g306: GeomPoint [constr] X=121.85 Y=11.5 Z=0
    g307: ArcOfCircle CenterX=107.75 CenterY=12.5 CenterZ=0 NormalX=0 NormalY=0 NormalZ=1 AngleXU=0 Radius=1 StartAngle=3.14159 EndAngle=4.71239
    g308: GeomPoint [constr] X=106.75 Y=11.5 Z=0
    g309: ArcOfCircle CenterX=126.8 CenterY=25.6 CenterZ=0 NormalX=0 NormalY=0 NormalZ=1 AngleXU=0 Radius=1 StartAngle=1.5708 EndAngle=3.14159
    g310: GeomPoint [constr] X=125.8 Y=26.6 Z=0
    g311: ArcOfCircle CenterX=139.9 CenterY=25.6 CenterZ=0 NormalX=0 NormalY=0 NormalZ=1 AngleXU=0 Radius=1 StartAngle=-9e-16 EndAngle=1.5708
    g312: GeomPoint [constr] X=140.9 Y=26.6 Z=0
    g313: ArcOfCircle CenterX=139.9 CenterY=12.5 CenterZ=0 NormalX=0 NormalY=0 NormalZ=1 AngleXU=0 Radius=1 StartAngle=4.71239 EndAngle=6.28319
    g314: GeomPoint [constr] X=140.9 Y=11.5 Z=0
    g315: ArcOfCircle CenterX=126.8 CenterY=12.5 CenterZ=0 NormalX=0 NormalY=0 NormalZ=1 AngleXU=0 Radius=1 StartAngle=3.14159 EndAngle=4.71239
    g316: GeomPoint [constr] X=125.8 Y=11.5 Z=0
    g317: ArcOfCircle CenterX=12.5 CenterY=25.6 CenterZ=0 NormalX=0 NormalY=0 NormalZ=1 AngleXU=0 Radius=1 StartAngle=1.5708 EndAngle=3.14159
    g318: GeomPoint [constr] X=11.5 Y=26.6 Z=0
    g319: ArcOfCircle CenterX=25.6 CenterY=25.6 CenterZ=0 NormalX=0 NormalY=0 NormalZ=1 AngleXU=0 Radius=1 StartAngle=9e-16 EndAngle=1.5708
    g320: GeomPoint [constr] X=26.6 Y=26.6 Z=0
    g321: ArcOfCircle CenterX=25.6 CenterY=12.5 CenterZ=0 NormalX=0 NormalY=0 NormalZ=1 AngleXU=0 Radius=1 StartAngle=4.71239 EndAngle=6.28319
    g322: GeomPoint [constr] X=26.6 Y=11.5 Z=0
    g323: ArcOfCircle CenterX=12.5 CenterY=12.5 CenterZ=0 NormalX=0 NormalY=0 NormalZ=1 AngleXU=0 Radius=1 StartAngle=3.14159 EndAngle=4.71239
    g324: GeomPoint [constr] X=11.5 Y=11.5 Z=0
  constraints (725):
    c: Horizontal(g0)
    c: Horizontal(g2)
    c: Vertical(g1)
    c: Vertical(g3)
    c: Symmetric(g276,g272,g4)
    c: Horizontal(g5)
    c: Horizontal(g7)
    c: Vertical(g6)
    c: Vertical(g8)
    c: Symmetric(g284,g280,g9)
    c: Horizontal(g10)
    c: Horizontal(g12)
    c: Vertical(g11)
    c: Vertical(g13)
    c: Symmetric(g228,g224,g14)
    c: Horizontal(g15)
    c: Horizontal(g17)
    c: Vertical(g16)
    c: Vertical(g18)
    c: Symmetric(g292,g288,g19)
    c: Horizontal(g20)
    c: Horizontal(g22)
    c: Vertical(g21)
    c: Vertical(g23)
    c: Symmetric(g300,g296,g24)
    c: Horizontal(g25)
    c: Horizontal(g27)
    c: Vertical(g26)
    c: Vertical(g28)
    c: Symmetric(g236,g232,g29)
    c: Horizontal(g30)
    c: Horizontal(g32)
    c: Vertical(g31)
    c: Vertical(g33)
    c: Symmetric(g244,g240,g34)
    c: Horizontal(g35)
    c: Horizontal(g37)
    c: Vertical(g36)
    c: Vertical(g38)
    c: Symmetric(g308,g304,g39)
    c: Horizontal(g40)
    c: Horizontal(g42)
    c: Vertical(g41)
    c: Vertical(g43)
    c: Symmetric(g252,g248,g44)
    c: Horizontal(g45)
    c: Horizontal(g47)
    c: Vertical(g46)
    c: Vertical(g48)
    c: Symmetric(g180,g176,g49)
    c: Horizontal(g50)
    c: Horizontal(g52)
    c: Vertical(g51)
    c: Vertical(g53)
    c: Symmetric(g188,g184,g54)
    c: Horizontal(g55)
    c: Horizontal(g57)
    c: Vertical(g56)
    c: Vertical(g58)
    c: Symmetric(g196,g192,g59)
    c: Horizontal(g60)
    c: Horizontal(g62)
    c: Vertical(g61)
    c: Vertical(g63)
    c: Symmetric(g204,g200,g64)
    c: Horizontal(g65)
    c: Horizontal(g67)
    c: Vertical(g66)
    c: Vertical(g68)
    c: Symmetric(g132,g128,g69)
    c: Horizontal(g70)
    c: Horizontal(g72)
    c: Vertical(g71)
    c: Vertical(g73)
    c: Symmetric(g140,g136,g74)
    c: Horizontal(g75)
    c: Horizontal(g77)
    c: Vertical(g76)
    c: Vertical(g78)
    c: Symmetric(g148,g144,g79)
    c: Horizontal(g80)
    c: Horizontal(g82)
    c: Vertical(g81)
    c: Vertical(g83)
    c: Symmetric(g156,g152,g84)
    c: Horizontal(g85)
    c: Horizontal(g87)
    c: Vertical(g86)
    c: Vertical(g88)
    c: Symmetric(g164,g160,g89)
    c: Horizontal(g90)
    c: Horizontal(g92)
    c: Vertical(g91)
    c: Vertical(g93)
    c: Symmetric(g212,g208,g94)
    c: Horizontal(g95)
    c: Vertical(g96)
    c: Vertical(g98)
    c: Symmetric(g260,g256,g99)
    c: Horizontal(g100)
    c: Horizontal(g102)
    c: Vertical(g101)
    c: Vertical(g103)
    c: Symmetric(g316,g312,g104)
    c: Horizontal(g105)
    c: Horizontal(g107)
    c: Vertical(g106)
    c: Vertical(g108)
    c: Symmetric(g324,g320,g109)
    c: DistanceX(g324,g322) = 15.1
    c: DistanceY(g324,g318) = 15.1
    c: Horizontal(g110)
    c: Horizontal(g112)
    c: Vertical(g111)
    c: Vertical(g113)
    c: Symmetric(g268,g264,g114)
    c: Horizontal(g115)
    c: Horizontal(g117)
    c: Vertical(g116)
    c: Vertical(g118)
    c: Symmetric(g220,g216,g119)
    c: Horizontal(g120)
    c: Horizontal(g122)
    c: Vertical(g121)
    c: Vertical(g123)
    c: Symmetric(g170,g168,g124)
    c: Horizontal(g69,g74)
    c: Horizontal(g74,g79)
    c: Horizontal(g79,g84)
    c: Horizontal(g84,g89)
    c: Horizontal(g89,g124)
    c: Horizontal(g49,g54)
    c: Horizontal(g54,g59)
    c: Horizontal(g59,g64)
    c: Horizontal(g64,g94)
    c: Horizontal(g94,g119)
    c: Horizontal(g14,g29)
    c: Horizontal(g29,g34)
    c: Horizontal(g34,g44)
    c: Horizontal(g44,g99)
    c: Horizontal(g99,g114)
    c: Horizontal(g109,g4)
    c: Horizontal(g4,g9)
    c: Horizontal(g9,g19)
    c: Horizontal(g19,g24)
    c: Horizontal(g24,g39)
    c: Horizontal(g39,g104)
    c: Vertical(g69,g49)
    c: Vertical(g49,g14)
    c: Vertical(g14,g4)
    c: Vertical(g74,g54)
    c: Vertical(g54,g29)
    c: Vertical(g29,g9)
    c: Vertical(g79,g59)
    c: Vertical(g59,g34)
    c: Vertical(g34,g19)
    c: Vertical(g84,g64)
    c: Vertical(g64,g44)
    c: Vertical(g44,g24)
    c: Vertical(g89,g94)
    c: Vertical(g94,g99)
    c: Vertical(g99,g39)
    c: Vertical(g124,g119)
    c: Vertical(g119,g114)
    c: Vertical(g114,g104)
    c: DistanceX(g109,g4) = 19.05
    c: DistanceX(g4,g9) = 19.05
    c: DistanceX(g9,g19) = 19.05
    c: DistanceX(g19,g24) = 19.05
    c: DistanceX(g24,g39) = 19.05
    c: DistanceX(g39,g104) = 19.05
    c: DistanceY(g49,g69) = 19.05
    c: DistanceY(g14,g49) = 19.05
    c: DistanceY(g109,g14) = 19.05
    c: DistanceX(g-1,g109) = 19.05
    c: DistanceY(g-1,g109) = 19.05
    c: Horizontal(g97)
    c: PointOnObject(g126,g65)
    c: PointOnObject(g126,g66)
    c: Tangent(g65,g125) = -1.5708
    c: Tangent(g66,g125) = -1.5708
    c: PointOnObject(g128,g65)
    c: PointOnObject(g128,g68)
    c: Tangent(g65,g127) = -1.5708
    c: Tangent(g68,g127) = -1.5708
    c: PointOnObject(g130,g67)
    c: PointOnObject(g130,g68)
    c: Tangent(g67,g129) = -1.5708
    c: Tangent(g68,g129) = -1.5708
    c: PointOnObject(g132,g66)
    c: PointOnObject(g132,g67)
    c: Tangent(g66,g131) = -1.5708
    c: Tangent(g67,g131) = -1.5708
    c: PointOnObject(g134,g70)
    c: PointOnObject(g134,g71)
    c: Tangent(g70,g133) = -1.5708
    c: Tangent(g71,g133) = -1.5708
    c: PointOnObject(g136,g70)
    c: PointOnObject(g136,g73)
    c: Tangent(g70,g135) = -1.5708
    c: Tangent(g73,g135) = -1.5708
    c: PointOnObject(g138,g72)
    c: PointOnObject(g138,g73)
    c: Tangent(g72,g137) = -1.5708
    c: Tangent(g73,g137) = -1.5708
    c: PointOnObject(g140,g71)
    c: PointOnObject(g140,g72)
    c: Tangent(g71,g139) = -1.5708
    c: Tangent(g72,g139) = -1.5708
    c: PointOnObject(g142,g75)
    c: PointOnObject(g142,g76)
    c: Tangent(g75,g141) = -1.5708
    c: Tangent(g76,g141) = -1.5708
    c: PointOnObject(g144,g75)
    c: PointOnObject(g144,g78)
    c: Tangent(g75,g143) = -1.5708
    c: Tangent(g78,g143) = -1.5708
    c: PointOnObject(g146,g77)
    c: PointOnObject(g146,g78)
    c: Tangent(g77,g145) = -1.5708
    c: Tangent(g78,g145) = -1.5708
    c: PointOnObject(g148,g76)
    c: PointOnObject(g148,g77)
    c: Tangent(g76,g147) = -1.5708
    c: Tangent(g77,g147) = -1.5708
    c: PointOnObject(g150,g80)
    c: PointOnObject(g150,g81)
    c: Tangent(g80,g149) = -1.5708
    c: Tangent(g81,g149) = -1.5708
    c: PointOnObject(g152,g80)
    c: PointOnObject(g152,g83)
    c: Tangent(g80,g151) = -1.5708
    c: Tangent(g83,g151) = -1.5708
    c: PointOnObject(g154,g82)
    c: PointOnObject(g154,g83)
    c: Tangent(g82,g153) = -1.5708
    c: Tangent(g83,g153) = -1.5708
    c: PointOnObject(g156,g81)
    c: PointOnObject(g156,g82)
    c: Tangent(g81,g155) = -1.5708
    c: Tangent(g82,g155) = -1.5708
    c: PointOnObject(g158,g85)
    c: PointOnObject(g158,g86)
    c: Tangent(g85,g157) = -1.5708
    c: Tangent(g86,g157) = -1.5708
    c: PointOnObject(g160,g85)
    c: PointOnObject(g160,g88)
    c: Tangent(g85,g159) = -1.5708
    c: Tangent(g88,g159) = -1.5708
    c: PointOnObject(g162,g87)
    c: PointOnObject(g162,g88)
    c: Tangent(g87,g161) = -1.5708
    c: Tangent(g88,g161) = -1.5708
    c: PointOnObject(g164,g86)
    c: PointOnObject(g164,g87)
    c: Tangent(g86,g163) = -1.5708
    c: Tangent(g87,g163) = -1.5708
    c: PointOnObject(g166,g120)
    c: PointOnObject(g166,g121)
    c: Tangent(g120,g165) = -1.5708
    c: Tangent(g121,g165) = -1.5708
    c: PointOnObject(g168,g120)
    c: PointOnObject(g168,g123)
    c: Tangent(g120,g167) = -1.5708
    c: Tangent(g123,g167) = -1.5708
    c: PointOnObject(g170,g121)
    c: PointOnObject(g170,g122)
    c: Tangent(g121,g169) = -1.5708
    c: Tangent(g122,g169) = -1.5708
    c: PointOnObject(g172,g122)
    c: PointOnObject(g172,g123)
    c: Tangent(g122,g171) = -1.5708
    c: Tangent(g123,g171) = -1.5708
    c: PointOnObject(g174,g45)
    c: PointOnObject(g174,g46)
    c: Tangent(g45,g173) = -1.5708
    c: Tangent(g46,g173) = -1.5708
    c: PointOnObject(g176,g45)
    c: PointOnObject(g176,g48)
    c: Tangent(g45,g175) = -1.5708
    c: Tangent(g48,g175) = -1.5708
    c: PointOnObject(g178,g47)
    c: PointOnObject(g178,g48)
    c: Tangent(g47,g177) = -1.5708
    c: Tangent(g48,g177) = -1.5708
    c: PointOnObject(g180,g46)
    c: PointOnObject(g180,g47)
    c: Tangent(g46,g179) = -1.5708
    c: Tangent(g47,g179) = -1.5708
    c: PointOnObject(g182,g50)
    c: PointOnObject(g182,g51)
    c: Tangent(g50,g181) = -1.5708
    c: Tangent(g51,g181) = -1.5708
    c: PointOnObject(g184,g50)
    c: PointOnObject(g184,g53)
    c: Tangent(g50,g183) = -1.5708
    c: Tangent(g53,g183) = -1.5708
    c: PointOnObject(g186,g52)
    c: PointOnObject(g186,g53)
    c: Tangent(g52,g185) = -1.5708
    c: Tangent(g53,g185) = -1.5708
    c: PointOnObject(g188,g51)
    c: PointOnObject(g188,g52)
    c: Tangent(g51,g187) = -1.5708
    c: Tangent(g52,g187) = -1.5708
    c: PointOnObject(g190,g55)
    c: PointOnObject(g190,g56)
    c: Tangent(g55,g189) = -1.5708
    c: Tangent(g56,g189) = -1.5708
    c: PointOnObject(g192,g55)
    c: PointOnObject(g192,g58)
    c: Tangent(g55,g191) = -1.5708
    c: Tangent(g58,g191) = -1.5708
    c: PointOnObject(g194,g57)
    c: PointOnObject(g194,g58)
    c: Tangent(g57,g193) = -1.5708
    c: Tangent(g58,g193) = -1.5708
    c: PointOnObject(g196,g56)
    c: PointOnObject(g196,g57)
    c: Tangent(g56,g195) = -1.5708
    c: Tangent(g57,g195) = -1.5708
    c: PointOnObject(g198,g60)
    c: PointOnObject(g198,g61)
    c: Tangent(g60,g197) = -1.5708
    c: Tangent(g61,g197) = -1.5708
    c: PointOnObject(g200,g60)
    c: PointOnObject(g200,g63)
    c: Tangent(g60,g199) = -1.5708
    c: Tangent(g63,g199) = -1.5708
    c: PointOnObject(g202,g62)
    c: PointOnObject(g202,g63)
    c: Tangent(g62,g201) = -1.5708
    c: Tangent(g63,g201) = -1.5708
    c: PointOnObject(g204,g61)
    c: PointOnObject(g204,g62)
    c: Tangent(g61,g203) = -1.5708
    c: Tangent(g62,g203) = -1.5708
    c: PointOnObject(g206,g90)
    c: PointOnObject(g206,g91)
    c: Tangent(g90,g205) = -1.5708
    c: Tangent(g91,g205) = -1.5708
    c: PointOnObject(g208,g90)
    c: PointOnObject(g208,g93)
    c: Tangent(g90,g207) = -1.5708
    c: Tangent(g93,g207) = -1.5708
    c: PointOnObject(g210,g92)
    c: PointOnObject(g210,g93)
    c: Tangent(g92,g209) = -1.5708
    c: Tangent(g93,g209) = -1.5708
    c: PointOnObject(g212,g91)
    c: PointOnObject(g212,g92)
    c: Tangent(g91,g211) = -1.5708
    c: Tangent(g92,g211) = -1.5708
    c: PointOnObject(g214,g115)
    c: PointOnObject(g214,g116)
    c: Tangent(g115,g213) = -1.5708
    c: Tangent(g116,g213) = -1.5708
    c: PointOnObject(g216,g115)
    c: PointOnObject(g216,g118)
    c: Tangent(g115,g215) = -1.5708
    c: Tangent(g118,g215) = -1.5708
    c: PointOnObject(g218,g117)
    c: PointOnObject(g218,g118)
    c: Tangent(g117,g217) = -1.5708
    c: Tangent(g118,g217) = -1.5708
    c: PointOnObject(g220,g116)
    c: PointOnObject(g220,g117)
    c: Tangent(g116,g219) = -1.5708
    c: Tangent(g117,g219) = -1.5708
    c: PointOnObject(g222,g10)
    c: PointOnObject(g222,g11)
    c: Tangent(g10,g221) = -1.5708
    c: Tangent(g11,g221) = -1.5708
    c: PointOnObject(g224,g10)
    c: PointOnObject(g224,g13)
    c: Tangent(g10,g223) = -1.5708
    c: Tangent(g13,g223) = -1.5708
    c: PointOnObject(g226,g12)
    c: PointOnObject(g226,g13)
    c: Tangent(g12,g225) = -1.5708
    c: Tangent(g13,g225) = -1.5708
    c: PointOnObject(g228,g11)
    c: PointOnObject(g228,g12)
    c: Tangent(g11,g227) = -1.5708
    c: Tangent(g12,g227) = -1.5708
    c: PointOnObject(g230,g25)
    c: PointOnObject(g230,g26)
    c: Tangent(g25,g229) = -1.5708
    c: Tangent(g26,g229) = -1.5708
    c: PointOnObject(g232,g25)
    c: PointOnObject(g232,g28)
    c: Tangent(g25,g231) = -1.5708
    c: Tangent(g28,g231) = -1.5708
    c: PointOnObject(g234,g27)
    c: PointOnObject(g234,g28)
    c: Tangent(g27,g233) = -1.5708
    c: Tangent(g28,g233) = -1.5708
    c: PointOnObject(g236,g26)
    c: PointOnObject(g236,g27)
    c: Tangent(g26,g235) = -1.5708
    c: Tangent(g27,g235) = -1.5708
    c: PointOnObject(g238,g30)
    c: PointOnObject(g238,g31)
    c: Tangent(g30,g237) = -1.5708
    c: Tangent(g31,g237) = -1.5708
    c: PointOnObject(g240,g30)
    c: PointOnObject(g240,g33)
    c: Tangent(g30,g239) = -1.5708
    c: Tangent(g33,g239) = -1.5708
    c: PointOnObject(g242,g32)
    c: PointOnObject(g242,g33)
    c: Tangent(g32,g241) = -1.5708
    c: Tangent(g33,g241) = -1.5708
    c: PointOnObject(g244,g31)
    c: PointOnObject(g244,g32)
    c: Tangent(g31,g243) = -1.5708
    c: Tangent(g32,g243) = -1.5708
    c: PointOnObject(g246,g40)
    c: PointOnObject(g246,g41)
    c: Tangent(g40,g245) = -1.5708
    c: Tangent(g41,g245) = -1.5708
    c: PointOnObject(g248,g40)
    c: PointOnObject(g248,g43)
    c: Tangent(g40,g247) = -1.5708
    c: Tangent(g43,g247) = -1.5708
    c: PointOnObject(g250,g42)
    c: PointOnObject(g250,g43)
    c: Tangent(g42,g249) = -1.5708
    c: Tangent(g43,g249) = -1.5708
    c: PointOnObject(g252,g41)
    c: PointOnObject(g252,g42)
    c: Tangent(g41,g251) = -1.5708
    c: Tangent(g42,g251) = -1.5708
    c: PointOnObject(g254,g95)
    c: PointOnObject(g254,g96)
    c: Tangent(g95,g253) = -1.5708
    c: Tangent(g96,g253) = -1.5708
    c: PointOnObject(g256,g95)
    c: PointOnObject(g256,g98)
    c: Tangent(g95,g255) = -1.5708
    c: Tangent(g98,g255) = -1.5708
    c: PointOnObject(g258,g97)
    c: PointOnObject(g258,g98)
    c: Tangent(g97,g257) = -1.5708
    c: Tangent(g98,g257) = -1.5708
    c: PointOnObject(g260,g96)
    c: PointOnObject(g260,g97)
    c: Tangent(g96,g259) = -1.5708
    c: Tangent(g97,g259) = -1.5708
    c: PointOnObject(g262,g110)
    c: PointOnObject(g262,g111)
    c: Tangent(g110,g261) = -1.5708
    c: Tangent(g111,g261) = -1.5708
    c: PointOnObject(g264,g110)
    c: PointOnObject(g264,g113)
    c: Tangent(g110,g263) = -1.5708
    c: Tangent(g113,g263) = -1.5708
    c: PointOnObject(g266,g112)
    c: PointOnObject(g266,g113)
    c: Tangent(g112,g265) = -1.5708
    c: Tangent(g113,g265) = -1.5708
    c: PointOnObject(g268,g111)
    c: PointOnObject(g268,g112)
    c: Tangent(g111,g267) = -1.5708
    c: Tangent(g112,g267) = -1.5708
    c: PointOnObject(g270,g0)
    c: PointOnObject(g270,g1)
    c: Tangent(g0,g269) = -1.5708
    c: Tangent(g1,g269) = -1.5708
    c: PointOnObject(g272,g0)
    c: PointOnObject(g272,g3)
    c: Tangent(g0,g271) = -1.5708
    c: Tangent(g3,g271) = -1.5708
    c: PointOnObject(g274,g2)
    c: PointOnObject(g274,g3)
    c: Tangent(g2,g273) = -1.5708
    c: Tangent(g3,g273) = -1.5708
    c: PointOnObject(g276,g1)
    c: PointOnObject(g276,g2)
    c: Tangent(g1,g275) = -1.5708
    c: Tangent(g2,g275) = -1.5708
    c: PointOnObject(g278,g5)
    c: PointOnObject(g278,g6)
    c: Tangent(g5,g277) = -1.5708
    c: Tangent(g6,g277) = -1.5708
    c: PointOnObject(g280,g5)
    c: PointOnObject(g280,g8)
    c: Tangent(g5,g279) = -1.5708
    c: Tangent(g8,g279) = -1.5708
    c: PointOnObject(g282,g7)
    c: PointOnObject(g282,g8)
    c: Tangent(g7,g281) = -1.5708
    c: Tangent(g8,g281) = -1.5708
    c: PointOnObject(g284,g6)
    c: PointOnObject(g284,g7)
    c: Tangent(g6,g283) = -1.5708
    c: Tangent(g7,g283) = -1.5708
    c: PointOnObject(g286,g15)
    c: PointOnObject(g286,g16)
    c: Tangent(g15,g285) = -1.5708
    c: Tangent(g16,g285) = -1.5708
    c: PointOnObject(g288,g15)
    c: PointOnObject(g288,g18)
    c: Tangent(g15,g287) = -1.5708
    c: Tangent(g18,g287) = -1.5708
    c: PointOnObject(g290,g17)
    c: PointOnObject(g290,g18)
    c: Tangent(g17,g289) = -1.5708
    c: Tangent(g18,g289) = -1.5708
    c: PointOnObject(g292,g16)
    c: PointOnObject(g292,g17)
    c: Tangent(g16,g291) = -1.5708
    c: Tangent(g17,g291) = -1.5708
    c: PointOnObject(g294,g20)
    c: PointOnObject(g294,g21)
    c: Tangent(g20,g293) = -1.5708
    c: Tangent(g21,g293) = -1.5708
    c: PointOnObject(g296,g20)
    c: PointOnObject(g296,g23)
    c: Tangent(g20,g295) = -1.5708
    c: Tangent(g23,g295) = -1.5708
    c: PointOnObject(g298,g22)
    c: PointOnObject(g298,g23)
    c: Tangent(g22,g297) = -1.5708
    c: Tangent(g23,g297) = -1.5708
    c: PointOnObject(g300,g21)
    c: PointOnObject(g300,g22)
    c: Tangent(g21,g299) = -1.5708
    c: Tangent(g22,g299) = -1.5708
    c: PointOnObject(g302,g35)
    c: PointOnObject(g302,g36)
    c: Tangent(g35,g301) = -1.5708
    c: Tangent(g36,g301) = -1.5708
    c: PointOnObject(g304,g35)
    c: PointOnObject(g304,g38)
    c: Tangent(g35,g303) = -1.5708
    c: Tangent(g38,g303) = -1.5708
    c: PointOnObject(g306,g37)
    c: PointOnObject(g306,g38)
    c: Tangent(g37,g305) = -1.5708
    c: Tangent(g38,g305) = -1.5708
    c: PointOnObject(g308,g36)
    c: PointOnObject(g308,g37)
    c: Tangent(g36,g307) = -1.5708
    c: Tangent(g37,g307) = -1.5708
    c: PointOnObject(g310,g100)
    c: PointOnObject(g310,g101)
    c: Tangent(g100,g309) = -1.5708
    c: Tangent(g101,g309) = -1.5708
    c: PointOnObject(g312,g100)
    c: PointOnObject(g312,g103)
    c: Tangent(g100,g311) = -1.5708
    c: Tangent(g103,g311) = -1.5708
    c: PointOnObject(g314,g102)
    c: PointOnObject(g314,g103)
    c: Tangent(g102,g313) = -1.5708
    c: Tangent(g103,g313) = -1.5708
    c: PointOnObject(g316,g101)
    c: PointOnObject(g316,g102)
    c: Tangent(g101,g315) = -1.5708
    c: Tangent(g102,g315) = -1.5708
    c: PointOnObject(g318,g105)
    c: PointOnObject(g318,g106)
    c: Tangent(g105,g317) = -1.5708
    c: Tangent(g106,g317) = -1.5708
    c: PointOnObject(g320,g105)
    c: PointOnObject(g320,g108)
    c: Tangent(g105,g319) = -1.5708
    c: Tangent(g108,g319) = -1.5708
    c: PointOnObject(g322,g107)
    c: PointOnObject(g322,g108)
    c: Tangent(g107,g321) = -1.5708
    c: Tangent(g108,g321) = -1.5708
    c: PointOnObject(g324,g106)
    c: PointOnObject(g324,g107)
    c: Tangent(g106,g323) = -1.5708
    c: Tangent(g107,g323) = -1.5708
    c: Equal(g125,g127)
    c: Equal(g127,g129)
    c: Equal(g129,g131)
    c: Equal(g133,g135)
    c: Equal(g135,g137)
    c: Equal(g137,g139)
    c: Equal(g141,g143)
    c: Equal(g143,g145)
    c: Equal(g145,g147)
    c: Equal(g149,g151)
    c: Equal(g151,g153)
    c: Equal(g153,g155)
    c: Equal(g157,g159)
    c: Equal(g159,g161)
    c: Equal(g161,g163)
    c: Equal(g165,g167)
    c: Equal(g167,g171)
    c: Equal(g171,g169)
    c: Equal(g173,g175)
    c: Equal(g175,g177)
    c: Equal(g177,g179)
    c: Equal(g181,g183)
    c: Equal(g183,g185)
    c: Equal(g185,g187)
    c: Equal(g189,g191)
    c: Equal(g191,g193)
    c: Equal(g193,g195)
    c: Equal(g197,g199)
    c: Equal(g199,g201)
    c: Equal(g201,g203)
    c: Equal(g205,g207)
    c: Equal(g207,g209)
    c: Equal(g209,g211)
    c: Equal(g213,g215)
    c: Equal(g215,g217)
    c: Equal(g217,g219)
    c: Equal(g221,g223)
    c: Equal(g223,g225)
    c: Equal(g225,g227)
    c: Equal(g229,g231)
    c: Equal(g231,g233)
    c: Equal(g233,g235)
    c: Equal(g237,g239)
    c: Equal(g239,g241)
    c: Equal(g241,g243)
    c: Equal(g245,g247)
    c: Equal(g247,g249)
    c: Equal(g249,g251)
    c: Equal(g253,g255)
    c: Equal(g255,g257)
    c: Equal(g257,g259)
    c: Equal(g261,g263)
    c: Equal(g263,g265)
    c: Equal(g265,g267)
    c: Equal(g317,g319)
    c: Equal(g319,g321)
    c: Equal(g321,g323)
    c: Equal(g269,g271)
    c: Equal(g271,g273)
    c: Equal(g273,g275)
    c: Equal(g277,g279)
    c: Equal(g279,g281)
    c: Equal(g281,g283)
    c: Equal(g285,g287)
    c: Equal(g287,g289)
    c: Equal(g289,g291)
    c: Equal(g293,g295)
    c: Equal(g295,g297)
    c: Equal(g297,g299)
    c: Equal(g301,g303)
    c: Equal(g303,g305)
    c: Equal(g305,g307)
    c: Equal(g309,g311)
    c: Equal(g311,g313)
    c: Equal(g313,g315)
    c: Equal(g125,g133)
    c: Equal(g133,g141)
    c: Equal(g141,g149)
    c: Equal(g149,g157)
    c: Equal(g157,g165)
    c: Equal(g173,g181)
    c: Equal(g181,g189)
    c: Equal(g189,g197)
    c: Equal(g197,g205)
    c: Equal(g205,g213)
    c: Equal(g221,g229)
    c: Equal(g229,g237)
    c: Equal(g237,g245)
    c: Equal(g245,g253)
    c: Equal(g253,g261)
    c: Equal(g317,g269)
    c: Equal(g269,g277)
    c: Equal(g277,g285)
    c: Equal(g285,g293)
    c: Equal(g293,g301)
    c: Equal(g301,g309)
    c: Equal(g125,g173)
    c: Equal(g173,g221)
    c: Equal(g221,g269)
    c: Equal(g66,g71)
    c: Equal(g71,g76)
    c: Equal(g76,g81)
    c: Equal(g81,g86)
    c: Equal(g86,g121)
    c: Equal(g46,g51)
    c: Equal(g51,g56)
    c: Equal(g56,g61)
    c: Equal(g61,g91)
    c: Equal(g91,g116)
    c: Equal(g11,g26)
    c: Equal(g26,g31)
    c: Equal(g31,g41)
    c: Equal(g41,g96)
    c: Equal(g96,g111)
    c: Equal(g1,g6)
    c: Equal(g6,g16)
    c: Equal(g16,g21)
    c: Equal(g21,g36)
    c: Equal(g36,g101)
    c: Equal(g106,g1)
    c: Equal(g65,g70)
    c: Equal(g70,g75)
    c: Equal(g75,g80)
    c: Equal(g80,g85)
    c: Equal(g85,g120)
    c: Equal(g45,g50)
    c: Equal(g50,g55)
    c: Equal(g55,g60)
    c: Equal(g60,g90)
    c: Equal(g90,g115)
    c: Equal(g10,g25)
    c: Equal(g25,g30)
    c: Equal(g30,g40)
    c: Equal(g40,g95)
    c: Equal(g95,g110)
    c: Equal(g0,g5)
    c: Equal(g5,g15)
    c: Equal(g15,g20)
    c: Equal(g20,g35)
    c: Equal(g35,g100)
    c: Equal(g105,g0)
    c: Radius(g317) = 1
    c: Equal(g66,g46)
    c: Equal(g46,g11)
    c: Equal(g11,g1)
    c: Equal(g65,g45)
    c: Equal(g45,g10)
    c: Equal(g10,g0)
FEATURE [Sketcher::SketchObject] Sketch015  label="TR-PCB"
  ArcFitTolerance = 1e-06
  AttachmentSupport = -> [XY_Plane002]
  FullyConstrained = true
  MakeInternals = false
  MapMode = 5
  expr: Constraints[10] = 4 * 19.05
  expr: Constraints[11] = VarSet.Top_PcbY
  expr: Constraints[12] = 2.5 * 19.05
  expr: Constraints[9] = VarSet.Top_PcbX
  sketch-geometry (5):
    g0: LineSegment StartX=9.9 StartY=85.375 StartZ=0 EndX=9.9 EndY=9.875 EndZ=0
    g1: LineSegment StartX=9.9 StartY=9.875 StartZ=0 EndX=142.5 EndY=9.875 EndZ=0
    g2: LineSegment StartX=142.5 StartY=9.875 StartZ=0 EndX=142.5 EndY=85.375 EndZ=0
    g3: LineSegment StartX=142.5 StartY=85.375 StartZ=0 EndX=9.9 EndY=85.375 EndZ=0
    g4: GeomPoint [constr] X=76.2 Y=47.625 Z=0
  constraints (13):
    c: Coincident(g0,g1)
    c: Coincident(g1,g2)
    c: Coincident(g2,g3)
    c: Coincident(g3,g0)
    c: Vertical(g0)
    c: Vertical(g2)
    c: Horizontal(g1)
    c: Horizontal(g3)
    c: Symmetric(g2,g0,g4)
    c: DistanceX(g1,g1) = 132.6
    c: DistanceX(g-1,g4) = 76.2
    c: DistanceY(g2,g2) = 75.5
    c: DistanceY(g-1,g4) = 47.625
FEATURE [Sketcher::SketchObject] Sketch016  label="TR-ScrewPostIn"
  ArcFitTolerance = 1e-06
  AttachmentSupport = -> [XY_Plane002]
  FullyConstrained = true
  MakeInternals = false
  MapMode = 5
  expr: Constraints[10] = 1.5 * 19.05 mm
  expr: Constraints[32] = 19.05 mm / 2
  expr: Constraints[35] = VarSet.Screw_PostInD
  expr: Constraints[48] = 2.5 * 19.05 mm
  expr: Constraints[50] = 19.05 mm + VarSet.Screw_RearAdd
  sketch-geometry (17):
    g0: Circle CenterX=123.825 CenterY=28.575 CenterZ=0 NormalX=0 NormalY=0 NormalZ=1 AngleXU=0 Radius=0.95
    g1: Circle CenterX=123.825 CenterY=66.675 CenterZ=0 NormalX=0 NormalY=0 NormalZ=1 AngleXU=0 Radius=0.95
    g2: Circle CenterX=85.725 CenterY=66.675 CenterZ=0 NormalX=0 NormalY=0 NormalZ=1 AngleXU=0 Radius=0.95
    g3: Circle CenterX=85.725 CenterY=28.575 CenterZ=0 NormalX=0 NormalY=0 NormalZ=1 AngleXU=0 Radius=0.95
    g4: Circle CenterX=47.625 CenterY=28.575 CenterZ=0 NormalX=0 NormalY=0 NormalZ=1 AngleXU=0 Radius=0.95
    g5: Circle CenterX=47.625 CenterY=66.675 CenterZ=0 NormalX=0 NormalY=0 NormalZ=1 AngleXU=0 Radius=0.95
    g6: Circle CenterX=28.575 CenterY=9.525 CenterZ=0 NormalX=0 NormalY=0 NormalZ=1 AngleXU=0 Radius=0.95
    g7: Circle CenterX=47.625 CenterY=9.525 CenterZ=0 NormalX=0 NormalY=0 NormalZ=1 AngleXU=0 Radius=0.95
    g8: Circle CenterX=66.675 CenterY=9.525 CenterZ=0 NormalX=0 NormalY=0 NormalZ=1 AngleXU=0 Radius=0.95
    g9: Circle CenterX=85.725 CenterY=9.525 CenterZ=0 NormalX=0 NormalY=0 NormalZ=1 AngleXU=0 Radius=0.95
    g10: Circle CenterX=104.775 CenterY=9.525 CenterZ=0 NormalX=0 NormalY=0 NormalZ=1 AngleXU=0 Radius=0.95
    g11: Circle CenterX=123.825 CenterY=9.525 CenterZ=0 NormalX=0 NormalY=0 NormalZ=1 AngleXU=0 Radius=0.95
    g12: Circle CenterX=47.625 CenterY=88.225 CenterZ=0 NormalX=0 NormalY=0 NormalZ=1 AngleXU=0 Radius=0.95
    g13: Circle CenterX=66.675 CenterY=88.225 CenterZ=0 NormalX=0 NormalY=0 NormalZ=1 AngleXU=0 Radius=0.95
    g14: Circle CenterX=85.725 CenterY=88.225 CenterZ=0 NormalX=0 NormalY=0 NormalZ=1 AngleXU=0 Radius=0.95
    g15: Circle CenterX=104.775 CenterY=88.225 CenterZ=0 NormalX=0 NormalY=0 NormalZ=1 AngleXU=0 Radius=0.95
    g16: Circle CenterX=123.825 CenterY=88.225 CenterZ=0 NormalX=0 NormalY=0 NormalZ=1 AngleXU=0 Radius=0.95
  constraints (51):
    c: Horizontal(g6,g7)
    c: Horizontal(g7,g8)
    c: Horizontal(g8,g9)
    c: Horizontal(g9,g10)
    c: Horizontal(g10,g11)
    c: DistanceX(g10,g11) = 19.05
    c: DistanceX(g9,g10) = 19.05
    c: DistanceX(g8,g9) = 19.05
    c: DistanceX(g7,g8) = 19.05
    c: DistanceX(g6,g7) = 19.05
    c: DistanceX(g-1,g6) = 28.575
    c: Horizontal(g1,g2)
    c: Horizontal(g2,g5)
    c: Horizontal(g0,g3)
    c: Horizontal(g3,g4)
    c: Vertical(g1,g0)
    c: Vertical(g0,g11)
    c: Vertical(g2,g3)
    c: Vertical(g3,g9)
    c: Vertical(g5,g4)
    c: Vertical(g4,g7)
    c: Equal(g11,g10)
    c: Equal(g10,g9)
    c: Equal(g9,g8)
    c: Equal(g8,g7)
    c: Equal(g7,g6)
    c: Equal(g1,g2)
    c: Equal(g2,g5)
    c: Equal(g0,g3)
    c: Equal(g3,g4)
    c: Equal(g5,g4)
    c: Equal(g4,g7)
    c: DistanceY(g-1,g6) = 9.525
    c: DistanceY(g6,g4) = 19.05
    c: DistanceY(g4,g5) = 38.1
    c: Diameter(g6) = 1.9
    c: Horizontal(g12,g13)
    c: Horizontal(g13,g14)
    c: Horizontal(g14,g15)
    c: Horizontal(g15,g16)
    c: Equal(g12,g13)
    c: Equal(g13,g14)
    c: Equal(g14,g15)
    c: Equal(g15,g16)
    c: DistanceX(g12,g13) = 19.05
    c: DistanceX(g13,g14) = 19.05
    c: DistanceX(g14,g15) = 19.05
    c: DistanceX(g15,g16) = 19.05
    c: DistanceX(g-1,g12) = 47.625
    c: Equal(g12,g5)
    c: DistanceY(g5,g12) = 21.55
FEATURE [Sketcher::SketchObject] Sketch024  label="BR-Plate"
  ArcFitTolerance = 1e-06
  AttachmentSupport = -> [XY_Plane003]
  FullyConstrained = true
  MakeInternals = false
  MapMode = 5
  expr: Constraints[53] = VarSet.Top_MedXY / 2 + VarSet.Top_Frame
  expr: Constraints[54] = VarSet.Top_MedXY / 2 + VarSet.Top_Frame + VarSet.Top_RearAdd
  expr: Constraints[72] = VarSet.Top_FrameFilletR
  expr: Constraints[73] = VarSet.Top_MedXY / 2 + VarSet.Top_Frame
  expr: Constraints[74] = VarSet.Top_MedXY / 2 + VarSet.Top_Frame
  sketch-geometry (37):
    g0: GeomPoint [constr] X=38.1 Y=19.05 Z=0
    g1: GeomPoint [constr] X=57.15 Y=19.05 Z=0
    g2: GeomPoint [constr] X=38.1 Y=38.1 Z=0
    g3: GeomPoint [constr] X=76.2 Y=19.05 Z=0
    g4: GeomPoint [constr] X=95.25 Y=19.05 Z=0
    g5: GeomPoint [constr] X=57.15 Y=38.1 Z=0
    g6: GeomPoint [constr] X=76.2 Y=38.1 Z=0
    g7: GeomPoint [constr] X=114.3 Y=19.05 Z=0
    g8: GeomPoint [constr] X=95.25 Y=38.1 Z=0
    g9: GeomPoint [constr] X=38.1 Y=57.15 Z=0
    g10: GeomPoint [constr] X=57.15 Y=57.15 Z=0
    g11: GeomPoint [constr] X=76.2 Y=57.15 Z=0
    g12: GeomPoint [constr] X=95.25 Y=57.15 Z=0
    g13: GeomPoint [constr] X=38.1 Y=76.2 Z=0
    g14: GeomPoint [constr] X=57.15 Y=76.2 Z=0
    g15: GeomPoint [constr] X=76.2 Y=76.2 Z=0
    g16: GeomPoint [constr] X=95.25 Y=76.2 Z=0
    g17: GeomPoint [constr] X=114.3 Y=76.2 Z=0
    g18: GeomPoint [constr] X=114.3 Y=57.15 Z=0
    g19: GeomPoint [constr] X=114.3 Y=38.1 Z=0
    g20: GeomPoint [constr] X=133.35 Y=19.05 Z=0
    g21: GeomPoint [constr] X=19.05 Y=19.05 Z=0
    g22: GeomPoint [constr] X=133.35 Y=38.1 Z=0
    g23: GeomPoint [constr] X=133.35 Y=57.15 Z=0
    g24: GeomPoint [constr] X=133.35 Y=76.2 Z=0
    g25: LineSegment StartX=9.15 StartY=91.1 StartZ=0 EndX=143.25 EndY=91.1 EndZ=0
    g26: LineSegment StartX=145.25 StartY=89.1 StartZ=0 EndX=145.25 EndY=9.15 EndZ=0
    g27: LineSegment StartX=143.25 StartY=7.15 StartZ=0 EndX=9.15 EndY=7.15 EndZ=0
    g28: ArcOfCircle CenterX=143.25 CenterY=89.1 CenterZ=0 NormalX=0 NormalY=0 NormalZ=1 AngleXU=0 Radius=2 StartAngle=9.8e-15 EndAngle=1.5708
    g29: GeomPoint [constr] X=145.25 Y=91.1 Z=0
    g30: ArcOfCircle CenterX=143.25 CenterY=9.15 CenterZ=0 NormalX=0 NormalY=0 NormalZ=1 AngleXU=0 Radius=2 StartAngle=4.71239 EndAngle=6.28319
    g31: GeomPoint [constr] X=145.25 Y=7.15 Z=0
    g32: LineSegment StartX=7.15 StartY=9.15 StartZ=0 EndX=7.15 EndY=89.1 EndZ=0
    g33: ArcOfCircle CenterX=9.15 CenterY=89.1 CenterZ=0 NormalX=0 NormalY=0 NormalZ=1 AngleXU=0 Radius=2 StartAngle=1.5708 EndAngle=3.14159
    g34: GeomPoint [constr] X=7.15 Y=91.1 Z=0
    g35: ArcOfCircle CenterX=9.15 CenterY=9.15 CenterZ=0 NormalX=0 NormalY=0 NormalZ=1 AngleXU=0 Radius=2 StartAngle=3.14159 EndAngle=4.71239
    g36: GeomPoint [constr] X=7.15 Y=7.15 Z=0
  constraints (78):
    c: Horizontal(g13,g14)
    c: Horizontal(g14,g15)
    c: Horizontal(g15,g16)
    c: Horizontal(g16,g17)
    c: Horizontal(g17,g24)
    c: Horizontal(g9,g10)
    c: Horizontal(g10,g11)
    c: Horizontal(g11,g12)
    c: Horizontal(g12,g18)
    c: Horizontal(g18,g23)
    c: Horizontal(g2,g5)
    c: Horizontal(g5,g6)
    c: Horizontal(g6,g8)
    c: Horizontal(g8,g19)
    c: Horizontal(g19,g22)
    c: Horizontal(g21,g0)
    c: Horizontal(g0,g1)
    c: Horizontal(g1,g3)
    c: Horizontal(g3,g4)
    c: Horizontal(g4,g7)
    c: Horizontal(g7,g20)
    c: Vertical(g13,g9)
    c: Vertical(g9,g2)
    c: Vertical(g2,g0)
    c: Vertical(g14,g10)
    c: Vertical(g10,g5)
    c: Vertical(g5,g1)
    c: Vertical(g15,g11)
    c: Vertical(g11,g6)
    c: Vertical(g6,g3)
    c: Vertical(g16,g12)
    c: Vertical(g12,g8)
    c: Vertical(g8,g4)
    c: Vertical(g17,g18)
    c: Vertical(g18,g19)
    c: Vertical(g19,g7)
    c: Vertical(g24,g23)
    c: Vertical(g23,g22)
    c: Vertical(g22,g20)
    c: DistanceX(g21,g0) = 19.05
    c: DistanceX(g0,g1) = 19.05
    c: DistanceX(g1,g3) = 19.05
    c: DistanceX(g3,g4) = 19.05
    c: DistanceX(g4,g7) = 19.05
    c: DistanceX(g7,g20) = 19.05
    c: DistanceY(g9,g13) = 19.05
    c: DistanceY(g2,g9) = 19.05
    c: DistanceY(g21,g2) = 19.05
    c: DistanceX(g-1,g21) = 19.05
    c: DistanceY(g-1,g21) = 19.05
    c: Horizontal(g25)
    c: Vertical(g26)
    c: Horizontal(g27)
    c: DistanceX(g24,g29) = 11.9
    c: DistanceY(g24,g29) = 14.9
    c: PointOnObject(g29,g25)
    c: PointOnObject(g29,g26)
    c: Tangent(g25,g28) = 1.5708
    c: Tangent(g26,g28) = 1.5708
    c: PointOnObject(g31,g26)
    c: PointOnObject(g31,g27)
    c: Tangent(g26,g30) = 1.5708
    c: Tangent(g27,g30) = 1.5708
    c: Vertical(g32)
    c: PointOnObject(g34,g25)
    c: PointOnObject(g34,g32)
    c: Tangent(g25,g33) = 1.5708
    c: Tangent(g32,g33) = 1.5708
    c: PointOnObject(g36,g27)
    c: PointOnObject(g36,g32)
    c: Tangent(g27,g35) = 1.5708
    c: Tangent(g32,g35) = 1.5708
    c: Radius(g35) = 2
    c: DistanceX(g36,g21) = 11.9
    c: DistanceY(g36,g21) = 11.9
    c: Equal(g33,g35)
    c: Equal(g28,g35)
    c: Equal(g30,g35)
FEATURE [PartDesign::Pad] Pad011  label="BR-Plate-Pad"
  Direction = (0,0,1)
  Length = 3
  Length2 = 10
  Profile = -> Sketch024
  ReferenceAxis = -> Sketch024 [N_Axis]
  Refine = true
  Reversed = true
  Suppressed = false
  Type = 0
  expr: Length = VarSet.Bottom_PlateZ
FEATURE [Sketcher::SketchObject] Sketch025  label="BR-Stem"
  ArcFitTolerance = 1e-06
  AttachmentSupport = -> [XY_Plane003]
  FullyConstrained = true
  MakeInternals = false
  MapMode = 5
  sketch-geometry (300):
    g0: GeomPoint [constr] X=133.35 Y=19.05 Z=0
    g1: GeomPoint [constr] X=114.3 Y=19.05 Z=0
    g2: GeomPoint [constr] X=95.25 Y=19.05 Z=0
    g3: GeomPoint [constr] X=76.2 Y=19.05 Z=0
    g4: GeomPoint [constr] X=57.15 Y=19.05 Z=0
    g5: GeomPoint [constr] X=133.35 Y=57.15 Z=0
    g6: GeomPoint [constr] X=114.3 Y=57.15 Z=0
    g7: GeomPoint [constr] X=95.25 Y=57.15 Z=0
    g8: GeomPoint [constr] X=76.2 Y=57.15 Z=0
    g9: GeomPoint [constr] X=57.15 Y=57.15 Z=0
    g10: GeomPoint [constr] X=133.35 Y=38.1 Z=0
    g11: GeomPoint [constr] X=114.3 Y=38.1 Z=0
    g12: GeomPoint [constr] X=95.25 Y=38.1 Z=0
    g13: GeomPoint [constr] X=76.2 Y=38.1 Z=0
    g14: GeomPoint [constr] X=57.15 Y=38.1 Z=0
    g15: GeomPoint [constr] X=76.2 Y=76.2 Z=0
    g16: GeomPoint [constr] X=114.3 Y=76.2 Z=0
    g17: GeomPoint [constr] X=38.1 Y=76.2 Z=0
    g18: GeomPoint [constr] X=57.15 Y=76.2 Z=0
    g19: GeomPoint [constr] X=95.25 Y=76.2 Z=0
    g20: GeomPoint [constr] X=133.35 Y=76.2 Z=0
    g21: GeomPoint [constr] X=38.1 Y=57.15 Z=0
    g22: GeomPoint [constr] X=38.1 Y=38.1 Z=0
    g23: GeomPoint [constr] X=38.1 Y=19.05 Z=0
    g24: GeomPoint [constr] X=19.05 Y=19.05 Z=0
    g25: GeomPoint [constr] X=33.02 Y=76.2 Z=0
    g26: ArcOfCircle CenterX=32.6 CenterY=76.2 CenterZ=0 NormalX=0 NormalY=0 NormalZ=1 AngleXU=0 Radius=1 StartAngle=1.5708 EndAngle=4.71239
    g27: ArcOfCircle CenterX=33.02 CenterY=76.2 CenterZ=0 NormalX=0 NormalY=0 NormalZ=1 AngleXU=0 Radius=1 StartAngle=4.71239 EndAngle=7.85398
    g28: LineSegment StartX=32.6 StartY=77.2 StartZ=0 EndX=33.02 EndY=77.2 EndZ=0
    g29: LineSegment StartX=32.6 StartY=75.2 StartZ=0 EndX=33.02 EndY=75.2 EndZ=0
    g30: GeomPoint [constr] X=43.6 Y=76.2 Z=0
    g31: ArcOfCircle CenterX=43.18 CenterY=76.2 CenterZ=0 NormalX=0 NormalY=0 NormalZ=1 AngleXU=0 Radius=1 StartAngle=1.5708 EndAngle=4.71239
    g32: ArcOfCircle CenterX=43.6 CenterY=76.2 CenterZ=0 NormalX=0 NormalY=0 NormalZ=1 AngleXU=0 Radius=1 StartAngle=4.71239 EndAngle=7.85398
    g33: LineSegment StartX=43.18 StartY=77.2 StartZ=0 EndX=43.6 EndY=77.2 EndZ=0
    g34: LineSegment StartX=43.18 StartY=75.2 StartZ=0 EndX=43.6 EndY=75.2 EndZ=0
    g35: Circle CenterX=38.1 CenterY=76.2 CenterZ=0 NormalX=0 NormalY=0 NormalZ=1 AngleXU=0 Radius=2
    g36: GeomPoint [constr] X=52.07 Y=76.2 Z=0
    g37: ArcOfCircle CenterX=51.65 CenterY=76.2 CenterZ=0 NormalX=0 NormalY=0 NormalZ=1 AngleXU=0 Radius=1 StartAngle=1.5708 EndAngle=4.71239
    g38: ArcOfCircle CenterX=52.07 CenterY=76.2 CenterZ=0 NormalX=0 NormalY=0 NormalZ=1 AngleXU=0 Radius=1 StartAngle=4.71239 EndAngle=7.85398
    g39: LineSegment StartX=51.65 StartY=77.2 StartZ=0 EndX=52.07 EndY=77.2 EndZ=0
    g40: LineSegment StartX=51.65 StartY=75.2 StartZ=0 EndX=52.07 EndY=75.2 EndZ=0
    g41: GeomPoint [constr] X=62.65 Y=76.2 Z=0
    g42: ArcOfCircle CenterX=62.23 CenterY=76.2 CenterZ=0 NormalX=0 NormalY=0 NormalZ=1 AngleXU=0 Radius=1 StartAngle=1.5708 EndAngle=4.71239
    g43: ArcOfCircle CenterX=62.65 CenterY=76.2 CenterZ=0 NormalX=0 NormalY=0 NormalZ=1 AngleXU=0 Radius=1 StartAngle=4.71239 EndAngle=7.85398
    g44: LineSegment StartX=62.23 StartY=77.2 StartZ=0 EndX=62.65 EndY=77.2 EndZ=0
    g45: LineSegment StartX=62.23 StartY=75.2 StartZ=0 EndX=62.65 EndY=75.2 EndZ=0
    g46: Circle CenterX=57.15 CenterY=76.2 CenterZ=0 NormalX=0 NormalY=0 NormalZ=1 AngleXU=0 Radius=2
    g47: GeomPoint [constr] X=71.12 Y=76.2 Z=0
    g48: ArcOfCircle CenterX=70.7 CenterY=76.2 CenterZ=0 NormalX=0 NormalY=0 NormalZ=1 AngleXU=0 Radius=1 StartAngle=1.5708 EndAngle=4.71239
    g49: ArcOfCircle CenterX=71.12 CenterY=76.2 CenterZ=0 NormalX=0 NormalY=0 NormalZ=1 AngleXU=0 Radius=1 StartAngle=4.71239 EndAngle=7.85398
    g50: LineSegment StartX=70.7 StartY=77.2 StartZ=0 EndX=71.12 EndY=77.2 EndZ=0
    g51: LineSegment StartX=70.7 StartY=75.2 StartZ=0 EndX=71.12 EndY=75.2 EndZ=0
    g52: GeomPoint [constr] X=81.7 Y=76.2 Z=0
    g53: ArcOfCircle CenterX=81.28 CenterY=76.2 CenterZ=0 NormalX=0 NormalY=0 NormalZ=1 AngleXU=0 Radius=1 StartAngle=1.5708 EndAngle=4.71239
    g54: ArcOfCircle CenterX=81.7 CenterY=76.2 CenterZ=0 NormalX=0 NormalY=0 NormalZ=1 AngleXU=0 Radius=1 StartAngle=4.71239 EndAngle=7.85398
    g55: LineSegment StartX=81.28 StartY=77.2 StartZ=0 EndX=81.7 EndY=77.2 EndZ=0
    g56: LineSegment StartX=81.28 StartY=75.2 StartZ=0 EndX=81.7 EndY=75.2 EndZ=0
    g57: Circle CenterX=76.2 CenterY=76.2 CenterZ=0 NormalX=0 NormalY=0 NormalZ=1 AngleXU=0 Radius=2
    g58: GeomPoint [constr] X=90.17 Y=76.2 Z=0
    g59: ArcOfCircle CenterX=89.75 CenterY=76.2 CenterZ=0 NormalX=0 NormalY=0 NormalZ=1 AngleXU=0 Radius=1 StartAngle=1.5708 EndAngle=4.71239
    g60: ArcOfCircle CenterX=90.17 CenterY=76.2 CenterZ=0 NormalX=0 NormalY=0 NormalZ=1 AngleXU=0 Radius=1 StartAngle=4.71239 EndAngle=7.85398
    g61: LineSegment StartX=89.75 StartY=77.2 StartZ=0 EndX=90.17 EndY=77.2 EndZ=0
    g62: LineSegment StartX=89.75 StartY=75.2 StartZ=0 EndX=90.17 EndY=75.2 EndZ=0
    g63: GeomPoint [constr] X=100.75 Y=76.2 Z=0
    g64: ArcOfCircle CenterX=100.33 CenterY=76.2 CenterZ=0 NormalX=0 NormalY=0 NormalZ=1 AngleXU=0 Radius=1 StartAngle=1.5708 EndAngle=4.71239
    g65: ArcOfCircle CenterX=100.75 CenterY=76.2 CenterZ=0 NormalX=0 NormalY=0 NormalZ=1 AngleXU=0 Radius=1 StartAngle=4.71239 EndAngle=7.85398
    g66: LineSegment StartX=100.33 StartY=77.2 StartZ=0 EndX=100.75 EndY=77.2 EndZ=0
    g67: LineSegment StartX=100.33 StartY=75.2 StartZ=0 EndX=100.75 EndY=75.2 EndZ=0
    g68: Circle CenterX=95.25 CenterY=76.2 CenterZ=0 NormalX=0 NormalY=0 NormalZ=1 AngleXU=0 Radius=2
    g69: GeomPoint [constr] X=109.22 Y=76.2 Z=0
    g70: ArcOfCircle CenterX=108.8 CenterY=76.2 CenterZ=0 NormalX=0 NormalY=0 NormalZ=1 AngleXU=0 Radius=1 StartAngle=1.5708 EndAngle=4.71239
    g71: ArcOfCircle CenterX=109.22 CenterY=76.2 CenterZ=0 NormalX=0 NormalY=0 NormalZ=1 AngleXU=0 Radius=1 StartAngle=4.71239 EndAngle=7.85398
    g72: LineSegment StartX=108.8 StartY=77.2 StartZ=0 EndX=109.22 EndY=77.2 EndZ=0
    g73: LineSegment StartX=108.8 StartY=75.2 StartZ=0 EndX=109.22 EndY=75.2 EndZ=0
    g74: GeomPoint [constr] X=119.8 Y=76.2 Z=0
    g75: ArcOfCircle CenterX=119.38 CenterY=76.2 CenterZ=0 NormalX=0 NormalY=0 NormalZ=1 AngleXU=0 Radius=1 StartAngle=1.5708 EndAngle=4.71239
    g76: ArcOfCircle CenterX=119.8 CenterY=76.2 CenterZ=0 NormalX=0 NormalY=0 NormalZ=1 AngleXU=0 Radius=1 StartAngle=4.71239 EndAngle=7.85398
    g77: LineSegment StartX=119.38 StartY=77.2 StartZ=0 EndX=119.8 EndY=77.2 EndZ=0
    g78: LineSegment StartX=119.38 StartY=75.2 StartZ=0 EndX=119.8 EndY=75.2 EndZ=0
    g79: Circle CenterX=114.3 CenterY=76.2 CenterZ=0 NormalX=0 NormalY=0 NormalZ=1 AngleXU=0 Radius=2
    g80: GeomPoint [constr] X=128.27 Y=76.2 Z=0
    g81: ArcOfCircle CenterX=127.85 CenterY=76.2 CenterZ=0 NormalX=0 NormalY=0 NormalZ=1 AngleXU=0 Radius=1 StartAngle=1.5708 EndAngle=4.71239
    g82: ArcOfCircle CenterX=128.27 CenterY=76.2 CenterZ=0 NormalX=0 NormalY=0 NormalZ=1 AngleXU=0 Radius=1 StartAngle=4.71239 EndAngle=7.85398
    g83: LineSegment StartX=127.85 StartY=77.2 StartZ=0 EndX=128.27 EndY=77.2 EndZ=0
    g84: LineSegment StartX=127.85 StartY=75.2 StartZ=0 EndX=128.27 EndY=75.2 EndZ=0
    g85: GeomPoint [constr] X=138.85 Y=76.2 Z=0
    g86: ArcOfCircle CenterX=138.43 CenterY=76.2 CenterZ=0 NormalX=0 NormalY=0 NormalZ=1 AngleXU=0 Radius=1 StartAngle=1.5708 EndAngle=4.71239
    g87: ArcOfCircle CenterX=138.85 CenterY=76.2 CenterZ=0 NormalX=0 NormalY=0 NormalZ=1 AngleXU=0 Radius=1 StartAngle=4.71239 EndAngle=7.85398
    g88: LineSegment StartX=138.43 StartY=77.2 StartZ=0 EndX=138.85 EndY=77.2 EndZ=0
    g89: LineSegment StartX=138.43 StartY=75.2 StartZ=0 EndX=138.85 EndY=75.2 EndZ=0
    g90: Circle CenterX=133.35 CenterY=76.2 CenterZ=0 NormalX=0 NormalY=0 NormalZ=1 AngleXU=0 Radius=2
    g91: GeomPoint [constr] X=33.02 Y=57.15 Z=0
    g92: ArcOfCircle CenterX=32.6 CenterY=57.15 CenterZ=0 NormalX=0 NormalY=0 NormalZ=1 AngleXU=0 Radius=1 StartAngle=1.5708 EndAngle=4.71239
    g93: ArcOfCircle CenterX=33.02 CenterY=57.15 CenterZ=0 NormalX=0 NormalY=0 NormalZ=1 AngleXU=0 Radius=1 StartAngle=4.71239 EndAngle=7.85398
    g94: LineSegment StartX=32.6 StartY=58.15 StartZ=0 EndX=33.02 EndY=58.15 EndZ=0
    g95: LineSegment StartX=32.6 StartY=56.15 StartZ=0 EndX=33.02 EndY=56.15 EndZ=0
    g96: GeomPoint [constr] X=43.6 Y=57.15 Z=0
    g97: ArcOfCircle CenterX=43.18 CenterY=57.15 CenterZ=0 NormalX=0 NormalY=0 NormalZ=1 AngleXU=0 Radius=1 StartAngle=1.5708 EndAngle=4.71239
    g98: ArcOfCircle CenterX=43.6 CenterY=57.15 CenterZ=0 NormalX=0 NormalY=0 NormalZ=1 AngleXU=0 Radius=1 StartAngle=4.71239 EndAngle=7.85398
    g99: LineSegment StartX=43.18 StartY=58.15 StartZ=0 EndX=43.6 EndY=58.15 EndZ=0
    g100: LineSegment StartX=43.18 StartY=56.15 StartZ=0 EndX=43.6 EndY=56.15 EndZ=0
    g101: Circle CenterX=38.1 CenterY=57.15 CenterZ=0 NormalX=0 NormalY=0 NormalZ=1 AngleXU=0 Radius=2
    g102: GeomPoint [constr] X=52.07 Y=57.15 Z=0
    g103: ArcOfCircle CenterX=51.65 CenterY=57.15 CenterZ=0 NormalX=0 NormalY=0 NormalZ=1 AngleXU=0 Radius=1 StartAngle=1.5708 EndAngle=4.71239
    g104: ArcOfCircle CenterX=52.07 CenterY=57.15 CenterZ=0 NormalX=0 NormalY=0 NormalZ=1 AngleXU=0 Radius=1 StartAngle=4.71239 EndAngle=7.85398
    g105: LineSegment StartX=51.65 StartY=58.15 StartZ=0 EndX=52.07 EndY=58.15 EndZ=0
    g106: LineSegment StartX=51.65 StartY=56.15 StartZ=0 EndX=52.07 EndY=56.15 EndZ=0
    g107: GeomPoint [constr] X=62.65 Y=57.15 Z=0
    g108: ArcOfCircle CenterX=62.23 CenterY=57.15 CenterZ=0 NormalX=0 NormalY=0 NormalZ=1 AngleXU=0 Radius=1 StartAngle=1.5708 EndAngle=4.71239
    g109: ArcOfCircle CenterX=62.65 CenterY=57.15 CenterZ=0 NormalX=0 NormalY=0 NormalZ=1 AngleXU=0 Radius=1 StartAngle=4.71239 EndAngle=7.85398
    g110: LineSegment StartX=62.23 StartY=58.15 StartZ=0 EndX=62.65 EndY=58.15 EndZ=0
    g111: LineSegment StartX=62.23 StartY=56.15 StartZ=0 EndX=62.65 EndY=56.15 EndZ=0
    g112: Circle CenterX=57.15 CenterY=57.15 CenterZ=0 NormalX=0 NormalY=0 NormalZ=1 AngleXU=0 Radius=2
    g113: GeomPoint [constr] X=71.12 Y=57.15 Z=0
    g114: ArcOfCircle CenterX=70.7 CenterY=57.15 CenterZ=0 NormalX=0 NormalY=0 NormalZ=1 AngleXU=0 Radius=1 StartAngle=1.5708 EndAngle=4.71239
    g115: ArcOfCircle CenterX=71.12 CenterY=57.15 CenterZ=0 NormalX=0 NormalY=0 NormalZ=1 AngleXU=0 Radius=1 StartAngle=4.71239 EndAngle=7.85398
    g116: LineSegment StartX=70.7 StartY=58.15 StartZ=0 EndX=71.12 EndY=58.15 EndZ=0
    g117: LineSegment StartX=70.7 StartY=56.15 StartZ=0 EndX=71.12 EndY=56.15 EndZ=0
    g118: GeomPoint [constr] X=81.7 Y=57.15 Z=0
    g119: ArcOfCircle CenterX=81.28 CenterY=57.15 CenterZ=0 NormalX=0 NormalY=0 NormalZ=1 AngleXU=0 Radius=1 StartAngle=1.5708 EndAngle=4.71239
    g120: ArcOfCircle CenterX=81.7 CenterY=57.15 CenterZ=0 NormalX=0 NormalY=0 NormalZ=1 AngleXU=0 Radius=1 StartAngle=4.71239 EndAngle=7.85398
    g121: LineSegment StartX=81.28 StartY=58.15 StartZ=0 EndX=81.7 EndY=58.15 EndZ=0
    g122: LineSegment StartX=81.28 StartY=56.15 StartZ=0 EndX=81.7 EndY=56.15 EndZ=0
    g123: Circle CenterX=76.2 CenterY=57.15 CenterZ=0 NormalX=0 NormalY=0 NormalZ=1 AngleXU=0 Radius=2
    g124: GeomPoint [constr] X=90.17 Y=57.15 Z=0
    g125: ArcOfCircle CenterX=89.75 CenterY=57.15 CenterZ=0 NormalX=0 NormalY=0 NormalZ=1 AngleXU=0 Radius=1 StartAngle=1.5708 EndAngle=4.71239
    g126: ArcOfCircle CenterX=90.17 CenterY=57.15 CenterZ=0 NormalX=0 NormalY=0 NormalZ=1 AngleXU=0 Radius=1 StartAngle=4.71239 EndAngle=7.85398
    g127: LineSegment StartX=89.75 StartY=58.15 StartZ=0 EndX=90.17 EndY=58.15 EndZ=0
    g128: LineSegment StartX=89.75 StartY=56.15 StartZ=0 EndX=90.17 EndY=56.15 EndZ=0
    g129: GeomPoint [constr] X=100.75 Y=57.15 Z=0
    g130: ArcOfCircle CenterX=100.33 CenterY=57.15 CenterZ=0 NormalX=0 NormalY=0 NormalZ=1 AngleXU=0 Radius=1 StartAngle=1.5708 EndAngle=4.71239
    g131: ArcOfCircle CenterX=100.75 CenterY=57.15 CenterZ=0 NormalX=0 NormalY=0 NormalZ=1 AngleXU=0 Radius=1 StartAngle=4.71239 EndAngle=7.85398
    g132: LineSegment StartX=100.33 StartY=58.15 StartZ=0 EndX=100.75 EndY=58.15 EndZ=0
    g133: LineSegment StartX=100.33 StartY=56.15 StartZ=0 EndX=100.75 EndY=56.15 EndZ=0
    g134: Circle CenterX=95.25 CenterY=57.15 CenterZ=0 NormalX=0 NormalY=0 NormalZ=1 AngleXU=0 Radius=2
    g135: GeomPoint [constr] X=109.22 Y=57.15 Z=0
    g136: ArcOfCircle CenterX=108.8 CenterY=57.15 CenterZ=0 NormalX=0 NormalY=0 NormalZ=1 AngleXU=0 Radius=1 StartAngle=1.5708 EndAngle=4.71239
    g137: ArcOfCircle CenterX=109.22 CenterY=57.15 CenterZ=0 NormalX=0 NormalY=0 NormalZ=1 AngleXU=0 Radius=1 StartAngle=4.71239 EndAngle=7.85398
    g138: LineSegment StartX=108.8 StartY=58.15 StartZ=0 EndX=109.22 EndY=58.15 EndZ=0
    g139: LineSegment StartX=108.8 StartY=56.15 StartZ=0 EndX=109.22 EndY=56.15 EndZ=0
    g140: GeomPoint [constr] X=119.8 Y=57.15 Z=0
    g141: ArcOfCircle CenterX=119.38 CenterY=57.15 CenterZ=0 NormalX=0 NormalY=0 NormalZ=1 AngleXU=0 Radius=1 StartAngle=1.5708 EndAngle=4.71239
    g142: ArcOfCircle CenterX=119.8 CenterY=57.15 CenterZ=0 NormalX=0 NormalY=0 NormalZ=1 AngleXU=0 Radius=1 StartAngle=4.71239 EndAngle=7.85398
    g143: LineSegment StartX=119.38 StartY=58.15 StartZ=0 EndX=119.8 EndY=58.15 EndZ=0
    g144: LineSegment StartX=119.38 StartY=56.15 StartZ=0 EndX=119.8 EndY=56.15 EndZ=0
    g145: Circle CenterX=114.3 CenterY=57.15 CenterZ=0 NormalX=0 NormalY=0 NormalZ=1 AngleXU=0 Radius=2
    g146: GeomPoint [constr] X=128.27 Y=57.15 Z=0
    g147: ArcOfCircle CenterX=127.85 CenterY=57.15 CenterZ=0 NormalX=0 NormalY=0 NormalZ=1 AngleXU=0 Radius=1 StartAngle=1.5708 EndAngle=4.71239
    g148: ArcOfCircle CenterX=128.27 CenterY=57.15 CenterZ=0 NormalX=0 NormalY=0 NormalZ=1 AngleXU=0 Radius=1 StartAngle=4.71239 EndAngle=7.85398
    g149: LineSegment StartX=127.85 StartY=58.15 StartZ=0 EndX=128.27 EndY=58.15 EndZ=0
    g150: LineSegment StartX=127.85 StartY=56.15 StartZ=0 EndX=128.27 EndY=56.15 EndZ=0
    g151: GeomPoint [constr] X=138.85 Y=57.15 Z=0
    g152: ArcOfCircle CenterX=138.43 CenterY=57.15 CenterZ=0 NormalX=0 NormalY=0 NormalZ=1 AngleXU=0 Radius=1 StartAngle=1.5708 EndAngle=4.71239
    g153: ArcOfCircle CenterX=138.85 CenterY=57.15 CenterZ=0 NormalX=0 NormalY=0 NormalZ=1 AngleXU=0 Radius=1 StartAngle=4.71239 EndAngle=7.85398
    g154: LineSegment StartX=138.43 StartY=58.15 StartZ=0 EndX=138.85 EndY=58.15 EndZ=0
    g155: LineSegment StartX=138.43 StartY=56.15 StartZ=0 EndX=138.85 EndY=56.15 EndZ=0
    g156: Circle CenterX=133.35 CenterY=57.15 CenterZ=0 NormalX=0 NormalY=0 NormalZ=1 AngleXU=0 Radius=2
    g157: GeomPoint [constr] X=33.02 Y=38.1 Z=0
    g158: ArcOfCircle CenterX=32.6 CenterY=38.1 CenterZ=0 NormalX=0 NormalY=0 NormalZ=1 AngleXU=0 Radius=1 StartAngle=1.5708 EndAngle=4.71239
    g159: ArcOfCircle CenterX=33.02 CenterY=38.1 CenterZ=0 NormalX=0 NormalY=0 NormalZ=1 AngleXU=0 Radius=1 StartAngle=4.71239 EndAngle=7.85398
    g160: LineSegment StartX=32.6 StartY=39.1 StartZ=0 EndX=33.02 EndY=39.1 EndZ=0
    g161: LineSegment StartX=32.6 StartY=37.1 StartZ=0 EndX=33.02 EndY=37.1 EndZ=0
    g162: GeomPoint [constr] X=43.6 Y=38.1 Z=0
    g163: ArcOfCircle CenterX=43.18 CenterY=38.1 CenterZ=0 NormalX=0 NormalY=0 NormalZ=1 AngleXU=0 Radius=1 StartAngle=1.5708 EndAngle=4.71239
    g164: ArcOfCircle CenterX=43.6 CenterY=38.1 CenterZ=0 NormalX=0 NormalY=0 NormalZ=1 AngleXU=0 Radius=1 StartAngle=4.71239 EndAngle=7.85398
    g165: LineSegment StartX=43.18 StartY=39.1 StartZ=0 EndX=43.6 EndY=39.1 EndZ=0
    g166: LineSegment StartX=43.18 StartY=37.1 StartZ=0 EndX=43.6 EndY=37.1 EndZ=0
    g167: Circle CenterX=38.1 CenterY=38.1 CenterZ=0 NormalX=0 NormalY=0 NormalZ=1 AngleXU=0 Radius=2
    g168: GeomPoint [constr] X=52.07 Y=38.1 Z=0
    g169: ArcOfCircle CenterX=51.65 CenterY=38.1 CenterZ=0 NormalX=0 NormalY=0 NormalZ=1 AngleXU=0 Radius=1 StartAngle=1.5708 EndAngle=4.71239
    g170: ArcOfCircle CenterX=52.07 CenterY=38.1 CenterZ=0 NormalX=0 NormalY=0 NormalZ=1 AngleXU=0 Radius=1 StartAngle=4.71239 EndAngle=7.85398
    g171: LineSegment StartX=51.65 StartY=39.1 StartZ=0 EndX=52.07 EndY=39.1 EndZ=0
    g172: LineSegment StartX=51.65 StartY=37.1 StartZ=0 EndX=52.07 EndY=37.1 EndZ=0
    g173: GeomPoint [constr] X=62.65 Y=38.1 Z=0
    g174: ArcOfCircle CenterX=62.23 CenterY=38.1 CenterZ=0 NormalX=0 NormalY=0 NormalZ=1 AngleXU=0 Radius=1 StartAngle=1.5708 EndAngle=4.71239
    g175: ArcOfCircle CenterX=62.65 CenterY=38.1 CenterZ=0 NormalX=0 NormalY=0 NormalZ=1 AngleXU=0 Radius=1 StartAngle=4.71239 EndAngle=7.85398
    g176: LineSegment StartX=62.23 StartY=39.1 StartZ=0 EndX=62.65 EndY=39.1 EndZ=0
    g177: LineSegment StartX=62.23 StartY=37.1 StartZ=0 EndX=62.65 EndY=37.1 EndZ=0
    g178: Circle CenterX=57.15 CenterY=38.1 CenterZ=0 NormalX=0 NormalY=0 NormalZ=1 AngleXU=0 Radius=2
    g179: GeomPoint [constr] X=71.12 Y=38.1 Z=0
    g180: ArcOfCircle CenterX=70.7 CenterY=38.1 CenterZ=0 NormalX=0 NormalY=0 NormalZ=1 AngleXU=0 Radius=1 StartAngle=1.5708 EndAngle=4.71239
    g181: ArcOfCircle CenterX=71.12 CenterY=38.1 CenterZ=0 NormalX=0 NormalY=0 NormalZ=1 AngleXU=0 Radius=1 StartAngle=4.71239 EndAngle=7.85398
    g182: LineSegment StartX=70.7 StartY=39.1 StartZ=0 EndX=71.12 EndY=39.1 EndZ=0
    g183: LineSegment StartX=70.7 StartY=37.1 StartZ=0 EndX=71.12 EndY=37.1 EndZ=0
    g184: GeomPoint [constr] X=81.7 Y=38.1 Z=0
    g185: ArcOfCircle CenterX=81.28 CenterY=38.1 CenterZ=0 NormalX=0 NormalY=0 NormalZ=1 AngleXU=0 Radius=1 StartAngle=1.5708 EndAngle=4.71239
    g186: ArcOfCircle CenterX=81.7 CenterY=38.1 CenterZ=0 NormalX=0 NormalY=0 NormalZ=1 AngleXU=0 Radius=1 StartAngle=4.71239 EndAngle=7.85398
    g187: LineSegment StartX=81.28 StartY=39.1 StartZ=0 EndX=81.7 EndY=39.1 EndZ=0
    g188: LineSegment StartX=81.28 StartY=37.1 StartZ=0 EndX=81.7 EndY=37.1 EndZ=0
    g189: Circle CenterX=76.2 CenterY=38.1 CenterZ=0 NormalX=0 NormalY=0 NormalZ=1 AngleXU=0 Radius=2
    g190: GeomPoint [constr] X=90.17 Y=38.1 Z=0
    g191: ArcOfCircle CenterX=89.75 CenterY=38.1 CenterZ=0 NormalX=0 NormalY=0 NormalZ=1 AngleXU=0 Radius=1 StartAngle=1.5708 EndAngle=4.71239
    g192: ArcOfCircle CenterX=90.17 CenterY=38.1 CenterZ=0 NormalX=0 NormalY=0 NormalZ=1 AngleXU=0 Radius=1 StartAngle=4.71239 EndAngle=7.85398
    g193: LineSegment StartX=89.75 StartY=39.1 StartZ=0 EndX=90.17 EndY=39.1 EndZ=0
    g194: LineSegment StartX=89.75 StartY=37.1 StartZ=0 EndX=90.17 EndY=37.1 EndZ=0
    g195: GeomPoint [constr] X=100.75 Y=38.1 Z=0
    g196: ArcOfCircle CenterX=100.33 CenterY=38.1 CenterZ=0 NormalX=0 NormalY=0 NormalZ=1 AngleXU=0 Radius=1 StartAngle=1.5708 EndAngle=4.71239
    g197: ArcOfCircle CenterX=100.75 CenterY=38.1 CenterZ=0 NormalX=0 NormalY=0 NormalZ=1 AngleXU=0 Radius=1 StartAngle=4.71239 EndAngle=7.85398
    g198: LineSegment StartX=100.33 StartY=39.1 StartZ=0 EndX=100.75 EndY=39.1 EndZ=0
    g199: LineSegment StartX=100.33 StartY=37.1 StartZ=0 EndX=100.75 EndY=37.1 EndZ=0
    g200: Circle CenterX=95.25 CenterY=38.1 CenterZ=0 NormalX=0 NormalY=0 NormalZ=1 AngleXU=0 Radius=2
    g201: GeomPoint [constr] X=109.22 Y=38.1 Z=0
    g202: ArcOfCircle CenterX=108.8 CenterY=38.1 CenterZ=0 NormalX=0 NormalY=0 NormalZ=1 AngleXU=0 Radius=1 StartAngle=1.5708 EndAngle=4.71239
    g203: ArcOfCircle CenterX=109.22 CenterY=38.1 CenterZ=0 NormalX=0 NormalY=0 NormalZ=1 AngleXU=0 Radius=1 StartAngle=4.71239 EndAngle=7.85398
    g204: LineSegment StartX=108.8 StartY=39.1 StartZ=0 EndX=109.22 EndY=39.1 EndZ=0
    g205: LineSegment StartX=108.8 StartY=37.1 StartZ=0 EndX=109.22 EndY=37.1 EndZ=0
    g206: GeomPoint [constr] X=119.8 Y=38.1 Z=0
    g207: ArcOfCircle CenterX=119.38 CenterY=38.1 CenterZ=0 NormalX=0 NormalY=0 NormalZ=1 AngleXU=0 Radius=1 StartAngle=1.5708 EndAngle=4.71239
    g208: ArcOfCircle CenterX=119.8 CenterY=38.1 CenterZ=0 NormalX=0 NormalY=0 NormalZ=1 AngleXU=0 Radius=1 StartAngle=4.71239 EndAngle=7.85398
    g209: LineSegment StartX=119.38 StartY=39.1 StartZ=0 EndX=119.8 EndY=39.1 EndZ=0
    g210: LineSegment StartX=119.38 StartY=37.1 StartZ=0 EndX=119.8 EndY=37.1 EndZ=0
    g211: Circle CenterX=114.3 CenterY=38.1 CenterZ=0 NormalX=0 NormalY=0 NormalZ=1 AngleXU=0 Radius=2
    g212: GeomPoint [constr] X=128.27 Y=38.1 Z=0
    g213: ArcOfCircle CenterX=127.85 CenterY=38.1 CenterZ=0 NormalX=0 NormalY=0 NormalZ=1 AngleXU=0 Radius=1 StartAngle=1.5708 EndAngle=4.71239
    g214: ArcOfCircle CenterX=128.27 CenterY=38.1 CenterZ=0 NormalX=0 NormalY=0 NormalZ=1 AngleXU=0 Radius=1 StartAngle=4.71239 EndAngle=7.85398
    g215: LineSegment StartX=127.85 StartY=39.1 StartZ=0 EndX=128.27 EndY=39.1 EndZ=0
    g216: LineSegment StartX=127.85 StartY=37.1 StartZ=0 EndX=128.27 EndY=37.1 EndZ=0
    g217: GeomPoint [constr] X=138.85 Y=38.1 Z=0
    g218: ArcOfCircle CenterX=138.43 CenterY=38.1 CenterZ=0 NormalX=0 NormalY=0 NormalZ=1 AngleXU=0 Radius=1 StartAngle=1.5708 EndAngle=4.71239
    g219: ArcOfCircle CenterX=138.85 CenterY=38.1 CenterZ=0 NormalX=0 NormalY=0 NormalZ=1 AngleXU=0 Radius=1 StartAngle=4.71239 EndAngle=7.85398
    g220: LineSegment StartX=138.43 StartY=39.1 StartZ=0 EndX=138.85 EndY=39.1 EndZ=0
    g221: LineSegment StartX=138.43 StartY=37.1 StartZ=0 EndX=138.85 EndY=37.1 EndZ=0
    g222: Circle CenterX=133.35 CenterY=38.1 CenterZ=0 NormalX=0 NormalY=0 NormalZ=1 AngleXU=0 Radius=2
    g223: GeomPoint [constr] X=33.02 Y=19.05 Z=0
    g224: ArcOfCircle CenterX=32.6 CenterY=19.05 CenterZ=0 NormalX=0 NormalY=0 NormalZ=1 AngleXU=0 Radius=1 StartAngle=1.5708 EndAngle=4.71239
    g225: ArcOfCircle CenterX=33.02 CenterY=19.05 CenterZ=0 NormalX=0 NormalY=0 NormalZ=1 AngleXU=0 Radius=1 StartAngle=4.71239 EndAngle=7.85398
    g226: LineSegment StartX=32.6 StartY=20.05 StartZ=0 EndX=33.02 EndY=20.05 EndZ=0
    g227: LineSegment StartX=32.6 StartY=18.05 StartZ=0 EndX=33.02 EndY=18.05 EndZ=0
    g228: GeomPoint [constr] X=43.6 Y=19.05 Z=0
    g229: ArcOfCircle CenterX=43.18 CenterY=19.05 CenterZ=0 NormalX=0 NormalY=0 NormalZ=1 AngleXU=0 Radius=1 StartAngle=1.5708 EndAngle=4.71239
    g230: ArcOfCircle CenterX=43.6 CenterY=19.05 CenterZ=0 NormalX=0 NormalY=0 NormalZ=1 AngleXU=0 Radius=1 StartAngle=4.71239 EndAngle=7.85398
    g231: LineSegment StartX=43.18 StartY=20.05 StartZ=0 EndX=43.6 EndY=20.05 EndZ=0
    g232: LineSegment StartX=43.18 StartY=18.05 StartZ=0 EndX=43.6 EndY=18.05 EndZ=0
    g233: Circle CenterX=38.1 CenterY=19.05 CenterZ=0 NormalX=0 NormalY=0 NormalZ=1 AngleXU=0 Radius=2
    g234: GeomPoint [constr] X=52.07 Y=19.05 Z=0
    g235: ArcOfCircle CenterX=51.65 CenterY=19.05 CenterZ=0 NormalX=0 NormalY=0 NormalZ=1 AngleXU=0 Radius=1 StartAngle=1.5708 EndAngle=4.71239
    g236: ArcOfCircle CenterX=52.07 CenterY=19.05 CenterZ=0 NormalX=0 NormalY=0 NormalZ=1 AngleXU=0 Radius=1 StartAngle=4.71239 EndAngle=7.85398
    g237: LineSegment StartX=51.65 StartY=20.05 StartZ=0 EndX=52.07 EndY=20.05 EndZ=0
    g238: LineSegment StartX=51.65 StartY=18.05 StartZ=0 EndX=52.07 EndY=18.05 EndZ=0
    g239: GeomPoint [constr] X=62.65 Y=19.05 Z=0
    g240: ArcOfCircle CenterX=62.23 CenterY=19.05 CenterZ=0 NormalX=0 NormalY=0 NormalZ=1 AngleXU=0 Radius=1 StartAngle=1.5708 EndAngle=4.71239
    g241: ArcOfCircle CenterX=62.65 CenterY=19.05 CenterZ=0 NormalX=0 NormalY=0 NormalZ=1 AngleXU=0 Radius=1 StartAngle=4.71239 EndAngle=7.85398
    g242: LineSegment StartX=62.23 StartY=20.05 StartZ=0 EndX=62.65 EndY=20.05 EndZ=0
    g243: LineSegment StartX=62.23 StartY=18.05 StartZ=0 EndX=62.65 EndY=18.05 EndZ=0
    g244: Circle CenterX=57.15 CenterY=19.05 CenterZ=0 NormalX=0 NormalY=0 NormalZ=1 AngleXU=0 Radius=2
    g245: GeomPoint [constr] X=71.12 Y=19.05 Z=0
    g246: ArcOfCircle CenterX=70.7 CenterY=19.05 CenterZ=0 NormalX=0 NormalY=0 NormalZ=1 AngleXU=0 Radius=1 StartAngle=1.5708 EndAngle=4.71239
    g247: ArcOfCircle CenterX=71.12 CenterY=19.05 CenterZ=0 NormalX=0 NormalY=0 NormalZ=1 AngleXU=0 Radius=1 StartAngle=4.71239 EndAngle=7.85398
    g248: LineSegment StartX=70.7 StartY=20.05 StartZ=0 EndX=71.12 EndY=20.05 EndZ=0
    g249: LineSegment StartX=70.7 StartY=18.05 StartZ=0 EndX=71.12 EndY=18.05 EndZ=0
    g250: GeomPoint [constr] X=81.7 Y=19.05 Z=0
    g251: ArcOfCircle CenterX=81.28 CenterY=19.05 CenterZ=0 NormalX=0 NormalY=0 NormalZ=1 AngleXU=0 Radius=1 StartAngle=1.5708 EndAngle=4.71239
    g252: ArcOfCircle CenterX=81.7 CenterY=19.05 CenterZ=0 NormalX=0 NormalY=0 NormalZ=1 AngleXU=0 Radius=1 StartAngle=4.71239 EndAngle=7.85398
    g253: LineSegment StartX=81.28 StartY=20.05 StartZ=0 EndX=81.7 EndY=20.05 EndZ=0
    g254: LineSegment StartX=81.28 StartY=18.05 StartZ=0 EndX=81.7 EndY=18.05 EndZ=0
    g255: Circle CenterX=76.2 CenterY=19.05 CenterZ=0 NormalX=0 NormalY=0 NormalZ=1 AngleXU=0 Radius=2
    g256: GeomPoint [constr] X=90.17 Y=19.05 Z=0
    g257: ArcOfCircle CenterX=89.75 CenterY=19.05 CenterZ=0 NormalX=0 NormalY=0 NormalZ=1 AngleXU=0 Radius=1 StartAngle=1.5708 EndAngle=4.71239
    g258: ArcOfCircle CenterX=90.17 CenterY=19.05 CenterZ=0 NormalX=0 NormalY=0 NormalZ=1 AngleXU=0 Radius=1 StartAngle=4.71239 EndAngle=7.85398
    g259: LineSegment StartX=89.75 StartY=20.05 StartZ=0 EndX=90.17 EndY=20.05 EndZ=0
    g260: LineSegment StartX=89.75 StartY=18.05 StartZ=0 EndX=90.17 EndY=18.05 EndZ=0
    g261: GeomPoint [constr] X=100.75 Y=19.05 Z=0
    g262: ArcOfCircle CenterX=100.33 CenterY=19.05 CenterZ=0 NormalX=0 NormalY=0 NormalZ=1 AngleXU=0 Radius=1 StartAngle=1.5708 EndAngle=4.71239
    g263: ArcOfCircle CenterX=100.75 CenterY=19.05 CenterZ=0 NormalX=0 NormalY=0 NormalZ=1 AngleXU=0 Radius=1 StartAngle=4.71239 EndAngle=7.85398
    g264: LineSegment StartX=100.33 StartY=20.05 StartZ=0 EndX=100.75 EndY=20.05 EndZ=0
    g265: LineSegment StartX=100.33 StartY=18.05 StartZ=0 EndX=100.75 EndY=18.05 EndZ=0
    g266: Circle CenterX=95.25 CenterY=19.05 CenterZ=0 NormalX=0 NormalY=0 NormalZ=1 AngleXU=0 Radius=2
    g267: GeomPoint [constr] X=109.22 Y=19.05 Z=0
    g268: ArcOfCircle CenterX=108.8 CenterY=19.05 CenterZ=0 NormalX=0 NormalY=0 NormalZ=1 AngleXU=0 Radius=1 StartAngle=1.5708 EndAngle=4.71239
    g269: ArcOfCircle CenterX=109.22 CenterY=19.05 CenterZ=0 NormalX=0 NormalY=0 NormalZ=1 AngleXU=0 Radius=1 StartAngle=4.71239 EndAngle=7.85398
    g270: LineSegment StartX=108.8 StartY=20.05 StartZ=0 EndX=109.22 EndY=20.05 EndZ=0
    g271: LineSegment StartX=108.8 StartY=18.05 StartZ=0 EndX=109.22 EndY=18.05 EndZ=0
    g272: GeomPoint [constr] X=119.8 Y=19.05 Z=0
    g273: ArcOfCircle CenterX=119.38 CenterY=19.05 CenterZ=0 NormalX=0 NormalY=0 NormalZ=1 AngleXU=0 Radius=1 StartAngle=1.5708 EndAngle=4.71239
    g274: ArcOfCircle CenterX=119.8 CenterY=19.05 CenterZ=0 NormalX=0 NormalY=0 NormalZ=1 AngleXU=0 Radius=1 StartAngle=4.71239 EndAngle=7.85398
    g275: LineSegment StartX=119.38 StartY=20.05 StartZ=0 EndX=119.8 EndY=20.05 EndZ=0
    g276: LineSegment StartX=119.38 StartY=18.05 StartZ=0 EndX=119.8 EndY=18.05 EndZ=0
    g277: Circle CenterX=114.3 CenterY=19.05 CenterZ=0 NormalX=0 NormalY=0 NormalZ=1 AngleXU=0 Radius=2
    g278: GeomPoint [constr] X=128.27 Y=19.05 Z=0
    g279: ArcOfCircle CenterX=127.85 CenterY=19.05 CenterZ=0 NormalX=0 NormalY=0 NormalZ=1 AngleXU=0 Radius=1 StartAngle=1.5708 EndAngle=4.71239
    g280: ArcOfCircle CenterX=128.27 CenterY=19.05 CenterZ=0 NormalX=0 NormalY=0 NormalZ=1 AngleXU=0 Radius=1 StartAngle=4.71239 EndAngle=7.85398
    g281: LineSegment StartX=127.85 StartY=20.05 StartZ=0 EndX=128.27 EndY=20.05 EndZ=0
    g282: LineSegment StartX=127.85 StartY=18.05 StartZ=0 EndX=128.27 EndY=18.05 EndZ=0
    g283: GeomPoint [constr] X=138.85 Y=19.05 Z=0
    g284: ArcOfCircle CenterX=138.43 CenterY=19.05 CenterZ=0 NormalX=0 NormalY=0 NormalZ=1 AngleXU=0 Radius=1 StartAngle=1.5708 EndAngle=4.71239
    g285: ArcOfCircle CenterX=138.85 CenterY=19.05 CenterZ=0 NormalX=0 NormalY=0 NormalZ=1 AngleXU=0 Radius=1 StartAngle=4.71239 EndAngle=7.85398
    g286: LineSegment StartX=138.43 StartY=20.05 StartZ=0 EndX=138.85 EndY=20.05 EndZ=0
    g287: LineSegment StartX=138.43 StartY=18.05 StartZ=0 EndX=138.85 EndY=18.05 EndZ=0
    g288: Circle CenterX=133.35 CenterY=19.05 CenterZ=0 NormalX=0 NormalY=0 NormalZ=1 AngleXU=0 Radius=2
    g289: GeomPoint [constr] X=13.97 Y=19.05 Z=0
    g290: ArcOfCircle CenterX=13.55 CenterY=19.05 CenterZ=0 NormalX=0 NormalY=0 NormalZ=1 AngleXU=0 Radius=1 StartAngle=1.5708 EndAngle=4.71239
    g291: ArcOfCircle CenterX=13.97 CenterY=19.05 CenterZ=0 NormalX=0 NormalY=0 NormalZ=1 AngleXU=0 Radius=1 StartAngle=4.71239 EndAngle=7.85398
    g292: LineSegment StartX=13.55 StartY=20.05 StartZ=0 EndX=13.97 EndY=20.05 EndZ=0
    g293: LineSegment StartX=13.55 StartY=18.05 StartZ=0 EndX=13.97 EndY=18.05 EndZ=0
    g294: GeomPoint [constr] X=24.55 Y=19.05 Z=0
    g295: ArcOfCircle CenterX=24.13 CenterY=19.05 CenterZ=0 NormalX=0 NormalY=0 NormalZ=1 AngleXU=0 Radius=1 StartAngle=1.5708 EndAngle=4.71239
    g296: ArcOfCircle CenterX=24.55 CenterY=19.05 CenterZ=0 NormalX=0 NormalY=0 NormalZ=1 AngleXU=0 Radius=1 StartAngle=4.71239 EndAngle=7.85398
    g297: LineSegment StartX=24.13 StartY=20.05 StartZ=0 EndX=24.55 EndY=20.05 EndZ=0
    g298: LineSegment StartX=24.13 StartY=18.05 StartZ=0 EndX=24.55 EndY=18.05 EndZ=0
    g299: Circle CenterX=19.05 CenterY=19.05 CenterZ=0 NormalX=0 NormalY=0 NormalZ=1 AngleXU=0 Radius=2
  constraints (650):
    c: DistanceX(g1,g0) = 19.05
    c: DistanceX(g2,g1) = 19.05
    c: DistanceX(g3,g2) = 19.05
    c: DistanceX(g4,g3) = 19.05
    c: DistanceX(g23,g4) = 19.05
    c: Horizontal(g17,g18)
    c: Horizontal(g18,g15)
    c: Horizontal(g15,g19)
    c: Horizontal(g19,g16)
    c: Horizontal(g16,g20)
    c: Horizontal(g21,g9)
    c: Horizontal(g9,g8)
    c: Horizontal(g8,g7)
    c: Horizontal(g7,g6)
    c: Horizontal(g6,g5)
    c: Horizontal(g22,g14)
    c: Horizontal(g14,g13)
    c: Horizontal(g13,g12)
    c: Horizontal(g12,g11)
    c: Horizontal(g11,g10)
    c: Vertical(g17,g21)
    c: Vertical(g21,g22)
    c: Vertical(g22,g23)
    c: Vertical(g18,g9)
    c: Vertical(g9,g14)
    c: Vertical(g14,g4)
    c: Vertical(g15,g8)
    c: Vertical(g8,g13)
    c: Vertical(g13,g3)
    c: Vertical(g19,g7)
    c: Vertical(g7,g12)
    c: Vertical(g12,g2)
    c: Vertical(g16,g6)
    c: Vertical(g6,g11)
    c: Vertical(g11,g1)
    c: Vertical(g20,g5)
    c: Vertical(g5,g10)
    c: Vertical(g10,g0)
    c: Horizontal(g23,g4)
    c: Horizontal(g4,g3)
    c: Horizontal(g3,g2)
    c: Horizontal(g2,g1)
    c: Horizontal(g1,g0)
    c: Horizontal(g0,g24)
    c: DistanceY(g-1,g24) = 19.05
    c: Tangent(g26,g28) = 1.5708
    c: Tangent(g26,g29) = -1.5708
    c: Tangent(g27,g28) = 1.5708
    c: Tangent(g27,g29) = -1.5708
    c: Coincident(g27,g25)
    c: Tangent(g31,g33) = 1.5708
    c: Tangent(g31,g34) = -1.5708
    c: Tangent(g32,g33) = 1.5708
    c: Tangent(g32,g34) = -1.5708
    c: Coincident(g32,g30)
    c: Horizontal(g26,g25)
    c: Horizontal(g25,g35)
    c: Horizontal(g35,g31)
    c: Horizontal(g31,g30)
    c: Equal(g26,g27)
    c: Equal(g31,g32)
    c: Equal(g27,g31)
    c: Tangent(g37,g39) = 1.5708
    c: Tangent(g37,g40) = -1.5708
    c: Tangent(g38,g39) = 1.5708
    c: Tangent(g38,g40) = -1.5708
    c: Coincident(g38,g36)
    c: Tangent(g42,g44) = 1.5708
    c: Tangent(g42,g45) = -1.5708
    c: Tangent(g43,g44) = 1.5708
    c: Tangent(g43,g45) = -1.5708
    c: Coincident(g43,g41)
    c: Horizontal(g37,g36)
    c: Horizontal(g36,g46)
    c: Horizontal(g46,g42)
    c: Horizontal(g42,g41)
    c: Equal(g37,g38)
    c: Equal(g42,g43)
    c: Equal(g38,g42)
    c: Tangent(g48,g50) = 1.5708
    c: Tangent(g48,g51) = -1.5708
    c: Tangent(g49,g50) = 1.5708
    c: Tangent(g49,g51) = -1.5708
    c: Coincident(g49,g47)
    c: Tangent(g53,g55) = 1.5708
    c: Tangent(g53,g56) = -1.5708
    c: Tangent(g54,g55) = 1.5708
    c: Tangent(g54,g56) = -1.5708
    c: Coincident(g54,g52)
    c: Horizontal(g48,g47)
    c: Horizontal(g47,g57)
    c: Horizontal(g57,g53)
    c: Horizontal(g53,g52)
    c: Equal(g48,g49)
    c: Equal(g53,g54)
    c: Equal(g49,g53)
    c: Tangent(g59,g61) = 1.5708
    c: Tangent(g59,g62) = -1.5708
    c: Tangent(g60,g61) = 1.5708
    c: Tangent(g60,g62) = -1.5708
    c: Coincident(g60,g58)
    c: Tangent(g64,g66) = 1.5708
    c: Tangent(g64,g67) = -1.5708
    c: Tangent(g65,g66) = 1.5708
    c: Tangent(g65,g67) = -1.5708
    c: Coincident(g65,g63)
    c: Horizontal(g59,g58)
    c: Horizontal(g58,g68)
    c: Horizontal(g68,g64)
    c: Horizontal(g64,g63)
    c: Equal(g59,g60)
    c: Equal(g64,g65)
    c: Equal(g60,g64)
    c: Tangent(g70,g72) = 1.5708
    c: Tangent(g70,g73) = -1.5708
    c: Tangent(g71,g72) = 1.5708
    c: Tangent(g71,g73) = -1.5708
    c: Coincident(g71,g69)
    c: Tangent(g75,g77) = 1.5708
    c: Tangent(g75,g78) = -1.5708
    c: Tangent(g76,g77) = 1.5708
    c: Tangent(g76,g78) = -1.5708
    c: Coincident(g76,g74)
    c: Horizontal(g70,g69)
    c: Horizontal(g69,g79)
    c: Horizontal(g79,g75)
    c: Horizontal(g75,g74)
    c: Equal(g70,g71)
    c: Equal(g75,g76)
    c: Equal(g71,g75)
    c: Tangent(g81,g83) = 1.5708
    c: Tangent(g81,g84) = -1.5708
    c: Tangent(g82,g83) = 1.5708
    c: Tangent(g82,g84) = -1.5708
    c: Coincident(g82,g80)
    c: Tangent(g86,g88) = 1.5708
    c: Tangent(g86,g89) = -1.5708
    c: Tangent(g87,g88) = 1.5708
    c: Tangent(g87,g89) = -1.5708
    c: Coincident(g87,g85)
    c: Horizontal(g81,g80)
    c: Horizontal(g80,g90)
    c: Horizontal(g90,g86)
    c: Horizontal(g86,g85)
    c: Equal(g81,g82)
    c: Equal(g86,g87)
    c: Equal(g82,g86)
    c: Tangent(g92,g94) = 1.5708
    c: Tangent(g92,g95) = -1.5708
    c: Tangent(g93,g94) = 1.5708
    c: Tangent(g93,g95) = -1.5708
    c: Coincident(g93,g91)
    c: Tangent(g97,g99) = 1.5708
    c: Tangent(g97,g100) = -1.5708
    c: Tangent(g98,g99) = 1.5708
    c: Tangent(g98,g100) = -1.5708
    c: Coincident(g98,g96)
    c: Horizontal(g92,g91)
    c: Horizontal(g91,g101)
    c: Horizontal(g101,g97)
    c: Horizontal(g97,g96)
    c: Equal(g92,g93)
    c: Equal(g97,g98)
    c: Equal(g93,g97)
    c: Tangent(g103,g105) = 1.5708
    c: Tangent(g103,g106) = -1.5708
    c: Tangent(g104,g105) = 1.5708
    c: Tangent(g104,g106) = -1.5708
    c: Coincident(g104,g102)
    c: Tangent(g108,g110) = 1.5708
    c: Tangent(g108,g111) = -1.5708
    c: Tangent(g109,g110) = 1.5708
    c: Tangent(g109,g111) = -1.5708
    c: Coincident(g109,g107)
    c: Horizontal(g103,g102)
    c: Horizontal(g102,g112)
    c: Horizontal(g112,g108)
    c: Horizontal(g108,g107)
    c: Equal(g103,g104)
    c: Equal(g108,g109)
    c: Equal(g104,g108)
    c: Tangent(g114,g116) = 1.5708
    c: Tangent(g114,g117) = -1.5708
    c: Tangent(g115,g116) = 1.5708
    c: Tangent(g115,g117) = -1.5708
    c: Coincident(g115,g113)
    c: Tangent(g119,g121) = 1.5708
    c: Tangent(g119,g122) = -1.5708
    c: Tangent(g120,g121) = 1.5708
    c: Tangent(g120,g122) = -1.5708
    c: Coincident(g120,g118)
    c: Horizontal(g114,g113)
    c: Horizontal(g113,g123)
    c: Horizontal(g123,g119)
    c: Horizontal(g119,g118)
    c: Equal(g114,g115)
    c: Equal(g119,g120)
    c: Equal(g115,g119)
    c: Tangent(g125,g127) = 1.5708
    c: Tangent(g125,g128) = -1.5708
    c: Tangent(g126,g127) = 1.5708
    c: Tangent(g126,g128) = -1.5708
    c: Coincident(g126,g124)
    c: Tangent(g130,g132) = 1.5708
    c: Tangent(g130,g133) = -1.5708
    c: Tangent(g131,g132) = 1.5708
    c: Tangent(g131,g133) = -1.5708
    c: Coincident(g131,g129)
    c: Horizontal(g125,g124)
    c: Horizontal(g124,g134)
    c: Horizontal(g134,g130)
    c: Horizontal(g130,g129)
    c: Equal(g125,g126)
    c: Equal(g130,g131)
    c: Equal(g126,g130)
    c: Tangent(g136,g138) = 1.5708
    c: Tangent(g136,g139) = -1.5708
    c: Tangent(g137,g138) = 1.5708
    c: Tangent(g137,g139) = -1.5708
    c: Coincident(g137,g135)
    c: Tangent(g141,g143) = 1.5708
    c: Tangent(g141,g144) = -1.5708
    c: Tangent(g142,g143) = 1.5708
    c: Tangent(g142,g144) = -1.5708
    c: Coincident(g142,g140)
    c: Horizontal(g136,g135)
    c: Horizontal(g135,g145)
    c: Horizontal(g145,g141)
    c: Horizontal(g141,g140)
    c: Equal(g136,g137)
    c: Equal(g141,g142)
    c: Equal(g137,g141)
    c: Tangent(g147,g149) = 1.5708
    c: Tangent(g147,g150) = -1.5708
    c: Tangent(g148,g149) = 1.5708
    c: Tangent(g148,g150) = -1.5708
    c: Coincident(g148,g146)
    c: Tangent(g152,g154) = 1.5708
    c: Tangent(g152,g155) = -1.5708
    c: Tangent(g153,g154) = 1.5708
    c: Tangent(g153,g155) = -1.5708
    c: Coincident(g153,g151)
    c: Horizontal(g147,g146)
    c: Horizontal(g146,g156)
    c: Horizontal(g156,g152)
    c: Horizontal(g152,g151)
    c: Equal(g147,g148)
    c: Equal(g152,g153)
    c: Equal(g148,g152)
    c: Tangent(g158,g160) = 1.5708
    c: Tangent(g158,g161) = -1.5708
    c: Tangent(g159,g160) = 1.5708
    c: Tangent(g159,g161) = -1.5708
    c: Coincident(g159,g157)
    c: Tangent(g163,g165) = 1.5708
    c: Tangent(g163,g166) = -1.5708
    c: Tangent(g164,g165) = 1.5708
    c: Tangent(g164,g166) = -1.5708
    c: Coincident(g164,g162)
    c: Horizontal(g158,g157)
    c: Horizontal(g157,g167)
    c: Horizontal(g167,g163)
    c: Horizontal(g163,g162)
    c: Equal(g158,g159)
    c: Equal(g163,g164)
    c: Equal(g159,g163)
    c: Tangent(g169,g171) = 1.5708
    c: Tangent(g169,g172) = -1.5708
    c: Tangent(g170,g171) = 1.5708
    c: Tangent(g170,g172) = -1.5708
    c: Coincident(g170,g168)
    c: Tangent(g174,g176) = 1.5708
    c: Tangent(g174,g177) = -1.5708
    c: Tangent(g175,g176) = 1.5708
    c: Tangent(g175,g177) = -1.5708
    c: Coincident(g175,g173)
    c: Horizontal(g169,g168)
    c: Horizontal(g168,g178)
    c: Horizontal(g178,g174)
    c: Horizontal(g174,g173)
    c: Equal(g169,g170)
    c: Equal(g174,g175)
    c: Equal(g170,g174)
    c: Tangent(g180,g182) = 1.5708
    c: Tangent(g180,g183) = -1.5708
    c: Tangent(g181,g182) = 1.5708
    c: Tangent(g181,g183) = -1.5708
    c: Coincident(g181,g179)
    c: Tangent(g185,g187) = 1.5708
    c: Tangent(g185,g188) = -1.5708
    c: Tangent(g186,g187) = 1.5708
    c: Tangent(g186,g188) = -1.5708
    c: Coincident(g186,g184)
    c: Horizontal(g180,g179)
    c: Horizontal(g179,g189)
    c: Horizontal(g189,g185)
    c: Horizontal(g185,g184)
    c: Equal(g180,g181)
    c: Equal(g185,g186)
    c: Equal(g181,g185)
    c: Tangent(g191,g193) = 1.5708
    c: Tangent(g191,g194) = -1.5708
    c: Tangent(g192,g193) = 1.5708
    c: Tangent(g192,g194) = -1.5708
    c: Coincident(g192,g190)
    c: Tangent(g196,g198) = 1.5708
    c: Tangent(g196,g199) = -1.5708
    c: Tangent(g197,g198) = 1.5708
    c: Tangent(g197,g199) = -1.5708
    c: Coincident(g197,g195)
    c: Horizontal(g191,g190)
    c: Horizontal(g190,g200)
    c: Horizontal(g200,g196)
    c: Horizontal(g196,g195)
    c: Equal(g191,g192)
    c: Equal(g196,g197)
    c: Equal(g192,g196)
    c: Tangent(g202,g204) = 1.5708
    c: Tangent(g202,g205) = -1.5708
    c: Tangent(g203,g204) = 1.5708
    c: Tangent(g203,g205) = -1.5708
    c: Coincident(g203,g201)
    c: Tangent(g207,g209) = 1.5708
    c: Tangent(g207,g210) = -1.5708
    c: Tangent(g208,g209) = 1.5708
    c: Tangent(g208,g210) = -1.5708
    c: Coincident(g208,g206)
    c: Horizontal(g202,g201)
    c: Horizontal(g201,g211)
    c: Horizontal(g211,g207)
    c: Horizontal(g207,g206)
    c: Equal(g202,g203)
    c: Equal(g207,g208)
    c: Equal(g203,g207)
    c: Tangent(g213,g215) = 1.5708
    c: Tangent(g213,g216) = -1.5708
    c: Tangent(g214,g215) = 1.5708
    c: Tangent(g214,g216) = -1.5708
    c: Coincident(g214,g212)
    c: Tangent(g218,g220) = 1.5708
    c: Tangent(g218,g221) = -1.5708
    c: Tangent(g219,g220) = 1.5708
    c: Tangent(g219,g221) = -1.5708
    c: Coincident(g219,g217)
    c: Horizontal(g213,g212)
    c: Horizontal(g212,g222)
    c: Horizontal(g222,g218)
    c: Horizontal(g218,g217)
    c: Equal(g213,g214)
    c: Equal(g218,g219)
    c: Equal(g214,g218)
    c: Tangent(g224,g226) = 1.5708
    c: Tangent(g224,g227) = -1.5708
    c: Tangent(g225,g226) = 1.5708
    c: Tangent(g225,g227) = -1.5708
    c: Coincident(g225,g223)
    c: Tangent(g229,g231) = 1.5708
    c: Tangent(g229,g232) = -1.5708
    c: Tangent(g230,g231) = 1.5708
    c: Tangent(g230,g232) = -1.5708
    c: Coincident(g230,g228)
    c: Horizontal(g224,g223)
    c: Horizontal(g223,g233)
    c: Horizontal(g233,g229)
    c: Horizontal(g229,g228)
    c: Equal(g224,g225)
    c: Equal(g229,g230)
    c: Equal(g225,g229)
    c: Tangent(g235,g237) = 1.5708
    c: Tangent(g235,g238) = -1.5708
    c: Tangent(g236,g237) = 1.5708
    c: Tangent(g236,g238) = -1.5708
    c: Coincident(g236,g234)
    c: Tangent(g240,g242) = 1.5708
    c: Tangent(g240,g243) = -1.5708
    c: Tangent(g241,g242) = 1.5708
    c: Tangent(g241,g243) = -1.5708
    c: Coincident(g241,g239)
    c: Horizontal(g235,g234)
    c: Horizontal(g234,g244)
    c: Horizontal(g244,g240)
    c: Horizontal(g240,g239)
    c: Equal(g235,g236)
    c: Equal(g240,g241)
    c: Equal(g236,g240)
    c: DistanceX(g244,g239) = 5.5
    c: Tangent(g246,g248) = 1.5708
    c: Tangent(g246,g249) = -1.5708
    c: Tangent(g247,g248) = 1.5708
    c: Tangent(g247,g249) = -1.5708
    c: Coincident(g247,g245)
    c: Tangent(g251,g253) = 1.5708
    c: Tangent(g251,g254) = -1.5708
    c: Tangent(g252,g253) = 1.5708
    c: Tangent(g252,g254) = -1.5708
    c: Coincident(g252,g250)
    c: Horizontal(g246,g245)
    c: Horizontal(g245,g255)
    c: Horizontal(g255,g251)
    c: Horizontal(g251,g250)
    c: Equal(g246,g247)
    c: Equal(g251,g252)
    c: Equal(g247,g251)
    c: DistanceX(g246,g255) = 5.5
    c: DistanceX(g255,g250) = 5.5
    c: Tangent(g257,g259) = 1.5708
    c: Tangent(g257,g260) = -1.5708
    c: Tangent(g258,g259) = 1.5708
    c: Tangent(g258,g260) = -1.5708
    c: Coincident(g258,g256)
    c: Tangent(g262,g264) = 1.5708
    c: Tangent(g262,g265) = -1.5708
    c: Tangent(g263,g264) = 1.5708
    c: Tangent(g263,g265) = -1.5708
    c: Coincident(g263,g261)
    c: Horizontal(g257,g256)
    c: Horizontal(g256,g266)
    c: Horizontal(g266,g262)
    c: Horizontal(g262,g261)
    c: Equal(g257,g258)
    c: Equal(g262,g263)
    c: Equal(g258,g262)
    c: DistanceX(g257,g266) = 5.5
    c: DistanceX(g266,g261) = 5.5
    c: Tangent(g268,g270) = 1.5708
    c: Tangent(g268,g271) = -1.5708
    c: Tangent(g269,g270) = 1.5708
    c: Tangent(g269,g271) = -1.5708
    c: Coincident(g269,g267)
    c: Tangent(g273,g275) = 1.5708
    c: Tangent(g273,g276) = -1.5708
    c: Tangent(g274,g275) = 1.5708
    c: Tangent(g274,g276) = -1.5708
    c: Coincident(g274,g272)
    c: Horizontal(g268,g267)
    c: Horizontal(g267,g277)
    c: Horizontal(g277,g273)
    c: Horizontal(g273,g272)
    c: Equal(g268,g269)
    c: Equal(g273,g274)
    c: Equal(g269,g273)
    c: DistanceX(g268,g277) = 5.5
    c: DistanceX(g277,g272) = 5.5
    c: Tangent(g279,g281) = 1.5708
    c: Tangent(g279,g282) = -1.5708
    c: Tangent(g280,g281) = 1.5708
    c: Tangent(g280,g282) = -1.5708
    c: Coincident(g280,g278)
    c: Tangent(g284,g286) = 1.5708
    c: Tangent(g284,g287) = -1.5708
    c: Tangent(g285,g286) = 1.5708
    c: Tangent(g285,g287) = -1.5708
    c: Coincident(g285,g283)
    c: Horizontal(g279,g278)
    c: Horizontal(g278,g288)
    c: Horizontal(g288,g284)
    c: Horizontal(g284,g283)
    c: Equal(g279,g280)
    c: Equal(g284,g285)
    c: Equal(g280,g284)
    c: DistanceX(g279,g288) = 5.5
    c: DistanceX(g288,g283) = 5.5
    c: Tangent(g290,g292) = 1.5708
    c: Tangent(g290,g293) = -1.5708
    c: Tangent(g291,g292) = 1.5708
    c: Tangent(g291,g293) = -1.5708
    c: Coincident(g291,g289)
    c: Tangent(g295,g297) = 1.5708
    c: Tangent(g295,g298) = -1.5708
    c: Tangent(g296,g297) = 1.5708
    c: Tangent(g296,g298) = -1.5708
    c: Coincident(g296,g294)
    c: Horizontal(g290,g289)
    c: Horizontal(g289,g299)
    c: Horizontal(g299,g295)
    c: Horizontal(g295,g294)
    c: Equal(g290,g291)
    c: Equal(g295,g296)
    c: Equal(g291,g295)
    c: DistanceX(g290,g299) = 5.5
    c: DistanceX(g299,g294) = 5.5
    c: Coincident(g35,g17)
    c: Coincident(g46,g18)
    c: Coincident(g57,g15)
    c: Coincident(g68,g19)
    c: Coincident(g79,g16)
    c: Coincident(g90,g20)
    c: Coincident(g101,g21)
    c: Coincident(g112,g9)
    c: Coincident(g123,g8)
    c: Coincident(g134,g7)
    c: Coincident(g145,g6)
    c: Coincident(g156,g5)
    c: Coincident(g167,g22)
    c: Coincident(g178,g14)
    c: Coincident(g189,g13)
    c: Coincident(g200,g12)
    c: Coincident(g211,g11)
    c: Coincident(g222,g10)
    c: Coincident(g233,g23)
    c: Coincident(g244,g4)
    c: Coincident(g255,g3)
    c: Coincident(g266,g2)
    c: Coincident(g277,g1)
    c: Coincident(g288,g0)
    c: Coincident(g299,g24)
    c: Equal(g35,g46)
    c: Equal(g46,g57)
    c: Equal(g57,g68)
    c: Equal(g68,g79)
    c: Equal(g79,g90)
    c: Equal(g101,g112)
    c: Equal(g112,g123)
    c: Equal(g123,g134)
    c: Equal(g134,g145)
    c: Equal(g145,g156)
    c: Equal(g167,g178)
    c: Equal(g178,g189)
    c: Equal(g189,g200)
    c: Equal(g200,g211)
    c: Equal(g211,g222)
    c: Equal(g233,g244)
    c: Equal(g244,g255)
    c: Equal(g255,g266)
    c: Equal(g266,g277)
    c: Equal(g277,g288)
    c: Equal(g288,g299)
    c: Diameter(g299) = 4
    c: Equal(g90,g156)
    c: Equal(g156,g222)
    c: Equal(g222,g288)
    c: Diameter(g290) = 2
    c: Equal(g26,g37)
    c: Equal(g37,g48)
    c: Equal(g48,g59)
    c: Equal(g59,g70)
    c: Equal(g70,g81)
    c: Equal(g92,g103)
    c: Equal(g103,g114)
    c: Equal(g114,g125)
    c: Equal(g125,g136)
    c: Equal(g136,g147)
    c: Equal(g158,g169)
    c: Equal(g169,g180)
    c: Equal(g180,g191)
    c: Equal(g191,g202)
    c: Equal(g202,g213)
    c: Equal(g224,g235)
    c: Equal(g235,g246)
    c: Equal(g246,g257)
    c: Equal(g257,g268)
    c: Equal(g268,g279)
    c: Equal(g279,g290)
    c: Equal(g81,g147)
    c: Equal(g147,g213)
    c: Equal(g213,g279)
    c: Vertical(g26,g92)
    c: Vertical(g92,g158)
    c: Vertical(g158,g224)
    c: Vertical(g25,g91)
    c: Vertical(g91,g157)
    c: Vertical(g157,g223)
    c: Vertical(g31,g97)
    c: Vertical(g97,g163)
    c: Vertical(g163,g229)
    c: Vertical(g30,g96)
    c: Vertical(g96,g162)
    c: Vertical(g162,g228)
    c: Vertical(g37,g103)
    c: Vertical(g103,g169)
    c: Vertical(g169,g235)
    c: Vertical(g36,g102)
    c: Vertical(g102,g168)
    c: Vertical(g168,g234)
    c: DistanceX(g224,g23) = 5.5
    c: DistanceX(g23,g228) = 5.5
    c: DistanceX(g223,g23) = 5.08
    c: DistanceX(g23,g229) = 5.08
    c: DistanceX(g235,g4) = 5.5
    c: DistanceX(g4,g240) = 5.08
    c: DistanceX(g234,g4) = 5.08
    c: DistanceX(g289,g24) = 5.08
    c: DistanceX(g24,g295) = 5.08
    c: DistanceX(g245,g3) = 5.08
    c: DistanceX(g3,g251) = 5.08
    c: DistanceX(g256,g2) = 5.08
    c: DistanceX(g2,g262) = 5.08
    c: DistanceX(g267,g1) = 5.08
    c: DistanceX(g1,g273) = 5.08
    c: DistanceX(g278,g0) = 5.08
    c: DistanceX(g0,g284) = 5.08
    c: Vertical(g42,g108)
    c: Vertical(g108,g174)
    c: Vertical(g174,g240)
    c: Vertical(g41,g107)
    c: Vertical(g107,g173)
    c: Vertical(g173,g239)
    c: Vertical(g48,g114)
    c: Vertical(g114,g180)
    c: Vertical(g180,g246)
    c: Vertical(g47,g113)
    c: Vertical(g113,g179)
    c: Vertical(g179,g245)
    c: Vertical(g53,g119)
    c: Vertical(g119,g185)
    c: Vertical(g185,g251)
    c: Vertical(g52,g118)
    c: Vertical(g118,g184)
    c: Vertical(g184,g250)
    c: Vertical(g59,g125)
    c: Vertical(g125,g191)
    c: Vertical(g191,g257)
    c: Vertical(g58,g124)
    c: Vertical(g124,g190)
    c: Vertical(g190,g256)
    c: Vertical(g64,g130)
    c: Vertical(g130,g196)
    c: Vertical(g196,g262)
    c: Vertical(g63,g129)
    c: Vertical(g129,g195)
    c: Vertical(g195,g261)
    c: Vertical(g70,g136)
    c: Vertical(g136,g202)
    c: Vertical(g202,g268)
    c: Vertical(g69,g135)
    c: Vertical(g135,g201)
    c: Vertical(g201,g267)
    c: Vertical(g75,g141)
    c: Vertical(g141,g207)
    c: Vertical(g207,g273)
    c: Vertical(g74,g140)
    c: Vertical(g140,g206)
    c: Vertical(g206,g272)
    c: Vertical(g81,g147)
    c: Vertical(g147,g213)
    c: Vertical(g213,g279)
    c: Vertical(g80,g146)
    c: Vertical(g146,g212)
    c: Vertical(g212,g278)
    c: Vertical(g86,g152)
    c: Vertical(g152,g218)
    c: Vertical(g218,g284)
    c: Vertical(g85,g151)
    c: Vertical(g151,g217)
    c: Vertical(g217,g283)
    c: DistanceX(g-1,g24) = 19.05
    c: DistanceY(g24,g22) = 19.05
    c: DistanceY(g22,g21) = 19.05
    c: DistanceY(g21,g17) = 19.05
    c: DistanceX(g24,g23) = 19.05
FEATURE [Sketcher::SketchObject] Sketch026  label="BR-Contact"
  ArcFitTolerance = 1e-06
  AttachmentSupport = -> [XY_Plane003]
  FullyConstrained = true
  MakeInternals = false
  MapMode = 5
  expr: Constraints[388] = VarSet.Bottom_ContactD
  sketch-geometry (229):
    g0: GeomPoint [constr] X=133.35 Y=13.15 Z=0
    g1: GeomPoint [constr] X=114.3 Y=13.15 Z=0
    g2: GeomPoint [constr] X=95.25 Y=13.15 Z=0
    g3: GeomPoint [constr] X=76.2 Y=13.15 Z=0
    g4: GeomPoint [constr] X=57.15 Y=13.15 Z=0
    g5: GeomPoint [constr] X=133.35 Y=51.25 Z=0
    g6: GeomPoint [constr] X=114.3 Y=51.25 Z=0
    g7: GeomPoint [constr] X=95.25 Y=51.25 Z=0
    g8: GeomPoint [constr] X=76.2 Y=51.25 Z=0
    g9: GeomPoint [constr] X=57.15 Y=51.25 Z=0
    g10: GeomPoint [constr] X=133.35 Y=32.2 Z=0
    g11: GeomPoint [constr] X=114.3 Y=32.2 Z=0
    g12: GeomPoint [constr] X=95.25 Y=32.2 Z=0
    g13: GeomPoint [constr] X=76.2 Y=32.2 Z=0
    g14: GeomPoint [constr] X=57.15 Y=32.2 Z=0
    g15: GeomPoint [constr] X=76.2 Y=70.3 Z=0
    g16: GeomPoint [constr] X=114.3 Y=70.3 Z=0
    g17: GeomPoint [constr] X=38.1 Y=70.3 Z=0
    g18: GeomPoint [constr] X=57.15 Y=70.3 Z=0
    g19: GeomPoint [constr] X=95.25 Y=70.3 Z=0
    g20: GeomPoint [constr] X=133.35 Y=70.3 Z=0
    g21: GeomPoint [constr] X=38.1 Y=51.25 Z=0
    g22: GeomPoint [constr] X=38.1 Y=32.2 Z=0
    g23: GeomPoint [constr] X=38.1 Y=13.15 Z=0
    g24: GeomPoint [constr] X=19.05 Y=13.15 Z=0
    g25: ArcOfCircle CenterX=41.91 CenterY=73.66 CenterZ=0 NormalX=0 NormalY=0 NormalZ=1 AngleXU=0 Radius=1.5 StartAngle=5.43511 EndAngle=8.5767
    g26: ArcOfCircle CenterX=38.1 CenterY=70.3 CenterZ=0 NormalX=0 NormalY=0 NormalZ=1 AngleXU=0 Radius=1.5 StartAngle=2.29352 EndAngle=5.43511
    g27: LineSegment StartX=42.9021 StartY=72.535 StartZ=0 EndX=39.0921 EndY=69.175 EndZ=0
    g28: LineSegment StartX=40.9179 StartY=74.785 StartZ=0 EndX=37.1079 EndY=71.425 EndZ=0
    g29: ArcOfCircle CenterX=33.1 CenterY=72.4 CenterZ=0 NormalX=0 NormalY=0 NormalZ=1 AngleXU=0 Radius=1.5 StartAngle=1.09102 EndAngle=4.23261
    g30: ArcOfCircle CenterX=35.56 CenterY=71.12 CenterZ=0 NormalX=0 NormalY=0 NormalZ=1 AngleXU=0 Radius=1.5 StartAngle=4.23261 EndAngle=7.37421
    g31: LineSegment StartX=33.7924 StartY=73.7306 StartZ=0 EndX=36.2524 EndY=72.4506 EndZ=0
    g32: LineSegment StartX=32.4076 StartY=71.0694 StartZ=0 EndX=34.8676 EndY=69.7894 EndZ=0
    g33: ArcOfCircle CenterX=60.96 CenterY=73.66 CenterZ=0 NormalX=0 NormalY=0 NormalZ=1 AngleXU=0 Radius=1.5 StartAngle=5.43511 EndAngle=8.5767
    g34: ArcOfCircle CenterX=57.15 CenterY=70.3 CenterZ=0 NormalX=0 NormalY=0 NormalZ=1 AngleXU=0 Radius=1.5 StartAngle=2.29352 EndAngle=5.43511
    g35: LineSegment StartX=61.9521 StartY=72.535 StartZ=0 EndX=58.1421 EndY=69.175 EndZ=0
    g36: LineSegment StartX=59.9679 StartY=74.785 StartZ=0 EndX=56.1579 EndY=71.425 EndZ=0
    g37: ArcOfCircle CenterX=52.15 CenterY=72.4 CenterZ=0 NormalX=0 NormalY=0 NormalZ=1 AngleXU=0 Radius=1.5 StartAngle=1.09102 EndAngle=4.23261
    g38: ArcOfCircle CenterX=54.61 CenterY=71.12 CenterZ=0 NormalX=0 NormalY=0 NormalZ=1 AngleXU=0 Radius=1.5 StartAngle=4.23261 EndAngle=7.37421
    g39: LineSegment StartX=52.8424 StartY=73.7306 StartZ=0 EndX=55.3024 EndY=72.4506 EndZ=0
    g40: LineSegment StartX=51.4576 StartY=71.0694 StartZ=0 EndX=53.9176 EndY=69.7894 EndZ=0
    g41: ArcOfCircle CenterX=80.01 CenterY=73.66 CenterZ=0 NormalX=0 NormalY=0 NormalZ=1 AngleXU=0 Radius=1.5 StartAngle=5.43511 EndAngle=8.5767
    g42: ArcOfCircle CenterX=76.2 CenterY=70.3 CenterZ=0 NormalX=0 NormalY=0 NormalZ=1 AngleXU=0 Radius=1.5 StartAngle=2.29352 EndAngle=5.43511
    g43: LineSegment StartX=81.0021 StartY=72.535 StartZ=0 EndX=77.1921 EndY=69.175 EndZ=0
    g44: LineSegment StartX=79.0179 StartY=74.785 StartZ=0 EndX=75.2079 EndY=71.425 EndZ=0
    g45: ArcOfCircle CenterX=71.2 CenterY=72.4 CenterZ=0 NormalX=0 NormalY=0 NormalZ=1 AngleXU=0 Radius=1.5 StartAngle=1.09102 EndAngle=4.23261
    g46: ArcOfCircle CenterX=73.66 CenterY=71.12 CenterZ=0 NormalX=0 NormalY=0 NormalZ=1 AngleXU=0 Radius=1.5 StartAngle=4.23261 EndAngle=7.37421
    g47: LineSegment StartX=71.8924 StartY=73.7306 StartZ=0 EndX=74.3524 EndY=72.4506 EndZ=0
    g48: LineSegment StartX=70.5076 StartY=71.0694 StartZ=0 EndX=72.9676 EndY=69.7894 EndZ=0
    g49: ArcOfCircle CenterX=99.06 CenterY=73.66 CenterZ=0 NormalX=0 NormalY=0 NormalZ=1 AngleXU=0 Radius=1.5 StartAngle=5.43511 EndAngle=8.5767
    g50: ArcOfCircle CenterX=95.25 CenterY=70.3 CenterZ=0 NormalX=0 NormalY=0 NormalZ=1 AngleXU=0 Radius=1.5 StartAngle=2.29352 EndAngle=5.43511
    g51: LineSegment StartX=100.052 StartY=72.535 StartZ=0 EndX=96.2421 EndY=69.175 EndZ=0
    g52: LineSegment StartX=98.0679 StartY=74.785 StartZ=0 EndX=94.2579 EndY=71.425 EndZ=0
    g53: ArcOfCircle CenterX=90.25 CenterY=72.4 CenterZ=0 NormalX=0 NormalY=0 NormalZ=1 AngleXU=0 Radius=1.5 StartAngle=1.09102 EndAngle=4.23261
    g54: ArcOfCircle CenterX=92.71 CenterY=71.12 CenterZ=0 NormalX=0 NormalY=0 NormalZ=1 AngleXU=0 Radius=1.5 StartAngle=4.23261 EndAngle=7.37421
    g55: LineSegment StartX=90.9424 StartY=73.7306 StartZ=0 EndX=93.4024 EndY=72.4506 EndZ=0
    g56: LineSegment StartX=89.5576 StartY=71.0694 StartZ=0 EndX=92.0176 EndY=69.7894 EndZ=0
    g57: ArcOfCircle CenterX=118.11 CenterY=73.66 CenterZ=0 NormalX=0 NormalY=0 NormalZ=1 AngleXU=0 Radius=1.5 StartAngle=5.43511 EndAngle=8.5767
    g58: ArcOfCircle CenterX=114.3 CenterY=70.3 CenterZ=0 NormalX=0 NormalY=0 NormalZ=1 AngleXU=0 Radius=1.5 StartAngle=2.29352 EndAngle=5.43511
    g59: LineSegment StartX=119.102 StartY=72.535 StartZ=0 EndX=115.292 EndY=69.175 EndZ=0
    g60: LineSegment StartX=117.118 StartY=74.785 StartZ=0 EndX=113.308 EndY=71.425 EndZ=0
    g61: ArcOfCircle CenterX=109.3 CenterY=72.4 CenterZ=0 NormalX=0 NormalY=0 NormalZ=1 AngleXU=0 Radius=1.5 StartAngle=1.09102 EndAngle=4.23261
    g62: ArcOfCircle CenterX=111.76 CenterY=71.12 CenterZ=0 NormalX=0 NormalY=0 NormalZ=1 AngleXU=0 Radius=1.5 StartAngle=4.23261 EndAngle=7.37421
    g63: LineSegment StartX=109.992 StartY=73.7306 StartZ=0 EndX=112.452 EndY=72.4506 EndZ=0
    g64: LineSegment StartX=108.608 StartY=71.0694 StartZ=0 EndX=111.068 EndY=69.7894 EndZ=0
    g65: ArcOfCircle CenterX=137.16 CenterY=73.66 CenterZ=0 NormalX=0 NormalY=0 NormalZ=1 AngleXU=0 Radius=1.5 StartAngle=5.43511 EndAngle=8.5767
    g66: ArcOfCircle CenterX=133.35 CenterY=70.3 CenterZ=0 NormalX=0 NormalY=0 NormalZ=1 AngleXU=0 Radius=1.5 StartAngle=2.29352 EndAngle=5.43511
    g67: LineSegment StartX=138.152 StartY=72.535 StartZ=0 EndX=134.342 EndY=69.175 EndZ=0
    g68: LineSegment StartX=136.168 StartY=74.785 StartZ=0 EndX=132.358 EndY=71.425 EndZ=0
    g69: ArcOfCircle CenterX=128.35 CenterY=72.4 CenterZ=0 NormalX=0 NormalY=0 NormalZ=1 AngleXU=0 Radius=1.5 StartAngle=1.09102 EndAngle=4.23261
    g70: ArcOfCircle CenterX=130.81 CenterY=71.12 CenterZ=0 NormalX=0 NormalY=0 NormalZ=1 AngleXU=0 Radius=1.5 StartAngle=4.23261 EndAngle=7.37421
    g71: LineSegment StartX=129.042 StartY=73.7306 StartZ=0 EndX=131.502 EndY=72.4506 EndZ=0
    g72: LineSegment StartX=127.658 StartY=71.0694 StartZ=0 EndX=130.118 EndY=69.7894 EndZ=0
    g73: ArcOfCircle CenterX=41.91 CenterY=54.61 CenterZ=0 NormalX=0 NormalY=0 NormalZ=1 AngleXU=0 Radius=1.5 StartAngle=5.43511 EndAngle=8.5767
    g74: ArcOfCircle CenterX=38.1 CenterY=51.25 CenterZ=0 NormalX=0 NormalY=0 NormalZ=1 AngleXU=0 Radius=1.5 StartAngle=2.29352 EndAngle=5.43511
    g75: LineSegment StartX=42.9021 StartY=53.485 StartZ=0 EndX=39.0921 EndY=50.125 EndZ=0
    g76: LineSegment StartX=40.9179 StartY=55.735 StartZ=0 EndX=37.1079 EndY=52.375 EndZ=0
    g77: ArcOfCircle CenterX=33.1 CenterY=53.35 CenterZ=0 NormalX=0 NormalY=0 NormalZ=1 AngleXU=0 Radius=1.5 StartAngle=1.09102 EndAngle=4.23261
    g78: ArcOfCircle CenterX=35.56 CenterY=52.07 CenterZ=0 NormalX=0 NormalY=0 NormalZ=1 AngleXU=0 Radius=1.5 StartAngle=4.23261 EndAngle=7.37421
    g79: LineSegment StartX=33.7924 StartY=54.6806 StartZ=0 EndX=36.2524 EndY=53.4006 EndZ=0
    g80: LineSegment StartX=32.4076 StartY=52.0194 StartZ=0 EndX=34.8676 EndY=50.7394 EndZ=0
    g81: ArcOfCircle CenterX=60.96 CenterY=54.61 CenterZ=0 NormalX=0 NormalY=0 NormalZ=1 AngleXU=0 Radius=1.5 StartAngle=5.43511 EndAngle=8.5767
    g82: ArcOfCircle CenterX=57.15 CenterY=51.25 CenterZ=0 NormalX=0 NormalY=0 NormalZ=1 AngleXU=0 Radius=1.5 StartAngle=2.29352 EndAngle=5.43511
    g83: LineSegment StartX=61.9521 StartY=53.485 StartZ=0 EndX=58.1421 EndY=50.125 EndZ=0
    g84: LineSegment StartX=59.9679 StartY=55.735 StartZ=0 EndX=56.1579 EndY=52.375 EndZ=0
    g85: ArcOfCircle CenterX=52.15 CenterY=53.35 CenterZ=0 NormalX=0 NormalY=0 NormalZ=1 AngleXU=0 Radius=1.5 StartAngle=1.09102 EndAngle=4.23261
    g86: ArcOfCircle CenterX=54.61 CenterY=52.07 CenterZ=0 NormalX=0 NormalY=0 NormalZ=1 AngleXU=0 Radius=1.5 StartAngle=4.23261 EndAngle=7.37421
    g87: LineSegment StartX=52.8424 StartY=54.6806 StartZ=0 EndX=55.3024 EndY=53.4006 EndZ=0
    g88: LineSegment StartX=51.4576 StartY=52.0194 StartZ=0 EndX=53.9176 EndY=50.7394 EndZ=0
    g89: ArcOfCircle CenterX=80.01 CenterY=54.61 CenterZ=0 NormalX=0 NormalY=0 NormalZ=1 AngleXU=0 Radius=1.5 StartAngle=5.43511 EndAngle=8.5767
    g90: ArcOfCircle CenterX=76.2 CenterY=51.25 CenterZ=0 NormalX=0 NormalY=0 NormalZ=1 AngleXU=0 Radius=1.5 StartAngle=2.29352 EndAngle=5.43511
    g91: LineSegment StartX=81.0021 StartY=53.485 StartZ=0 EndX=77.1921 EndY=50.125 EndZ=0
    g92: LineSegment StartX=79.0179 StartY=55.735 StartZ=0 EndX=75.2079 EndY=52.375 EndZ=0
    g93: ArcOfCircle CenterX=71.2 CenterY=53.35 CenterZ=0 NormalX=0 NormalY=0 NormalZ=1 AngleXU=0 Radius=1.5 StartAngle=1.09102 EndAngle=4.23261
    g94: ArcOfCircle CenterX=73.66 CenterY=52.07 CenterZ=0 NormalX=0 NormalY=0 NormalZ=1 AngleXU=0 Radius=1.5 StartAngle=4.23261 EndAngle=7.37421
    g95: LineSegment StartX=71.8924 StartY=54.6806 StartZ=0 EndX=74.3524 EndY=53.4006 EndZ=0
    g96: LineSegment StartX=70.5076 StartY=52.0194 StartZ=0 EndX=72.9676 EndY=50.7394 EndZ=0
    g97: ArcOfCircle CenterX=99.06 CenterY=54.61 CenterZ=0 NormalX=0 NormalY=0 NormalZ=1 AngleXU=0 Radius=1.5 StartAngle=5.43511 EndAngle=8.5767
    g98: ArcOfCircle CenterX=95.25 CenterY=51.25 CenterZ=0 NormalX=0 NormalY=0 NormalZ=1 AngleXU=0 Radius=1.5 StartAngle=2.29352 EndAngle=5.43511
    g99: LineSegment StartX=100.052 StartY=53.485 StartZ=0 EndX=96.2421 EndY=50.125 EndZ=0
    g100: LineSegment StartX=98.0679 StartY=55.735 StartZ=0 EndX=94.2579 EndY=52.375 EndZ=0
    g101: ArcOfCircle CenterX=90.25 CenterY=53.35 CenterZ=0 NormalX=0 NormalY=0 NormalZ=1 AngleXU=0 Radius=1.5 StartAngle=1.09102 EndAngle=4.23261
    g102: ArcOfCircle CenterX=92.71 CenterY=52.07 CenterZ=0 NormalX=0 NormalY=0 NormalZ=1 AngleXU=0 Radius=1.5 StartAngle=4.23261 EndAngle=7.37421
    g103: LineSegment StartX=90.9424 StartY=54.6806 StartZ=0 EndX=93.4024 EndY=53.4006 EndZ=0
    g104: LineSegment StartX=89.5576 StartY=52.0194 StartZ=0 EndX=92.0176 EndY=50.7394 EndZ=0
    g105: ArcOfCircle CenterX=118.11 CenterY=54.61 CenterZ=0 NormalX=0 NormalY=0 NormalZ=1 AngleXU=0 Radius=1.5 StartAngle=5.43511 EndAngle=8.5767
    g106: ArcOfCircle CenterX=114.3 CenterY=51.25 CenterZ=0 NormalX=0 NormalY=0 NormalZ=1 AngleXU=0 Radius=1.5 StartAngle=2.29352 EndAngle=5.43511
    g107: LineSegment StartX=119.102 StartY=53.485 StartZ=0 EndX=115.292 EndY=50.125 EndZ=0
    g108: LineSegment StartX=117.118 StartY=55.735 StartZ=0 EndX=113.308 EndY=52.375 EndZ=0
    g109: ArcOfCircle CenterX=109.3 CenterY=53.35 CenterZ=0 NormalX=0 NormalY=0 NormalZ=1 AngleXU=0 Radius=1.5 StartAngle=1.09102 EndAngle=4.23261
    g110: ArcOfCircle CenterX=111.76 CenterY=52.07 CenterZ=0 NormalX=0 NormalY=0 NormalZ=1 AngleXU=0 Radius=1.5 StartAngle=4.23261 EndAngle=7.37421
    g111: LineSegment StartX=109.992 StartY=54.6806 StartZ=0 EndX=112.452 EndY=53.4006 EndZ=0
    g112: LineSegment StartX=108.608 StartY=52.0194 StartZ=0 EndX=111.068 EndY=50.7394 EndZ=0
    g113: ArcOfCircle CenterX=137.16 CenterY=54.61 CenterZ=0 NormalX=0 NormalY=0 NormalZ=1 AngleXU=0 Radius=1.5 StartAngle=5.43511 EndAngle=8.5767
    g114: ArcOfCircle CenterX=133.35 CenterY=51.25 CenterZ=0 NormalX=0 NormalY=0 NormalZ=1 AngleXU=0 Radius=1.5 StartAngle=2.29352 EndAngle=5.43511
    g115: LineSegment StartX=138.152 StartY=53.485 StartZ=0 EndX=134.342 EndY=50.125 EndZ=0
    g116: LineSegment StartX=136.168 StartY=55.735 StartZ=0 EndX=132.358 EndY=52.375 EndZ=0
    g117: ArcOfCircle CenterX=128.35 CenterY=53.35 CenterZ=0 NormalX=0 NormalY=0 NormalZ=1 AngleXU=0 Radius=1.5 StartAngle=1.09102 EndAngle=4.23261
    g118: ArcOfCircle CenterX=130.81 CenterY=52.07 CenterZ=0 NormalX=0 NormalY=0 NormalZ=1 AngleXU=0 Radius=1.5 StartAngle=4.23261 EndAngle=7.37421
    g119: LineSegment StartX=129.042 StartY=54.6806 StartZ=0 EndX=131.502 EndY=53.4006 EndZ=0
    g120: LineSegment StartX=127.658 StartY=52.0194 StartZ=0 EndX=130.118 EndY=50.7394 EndZ=0
    g121: ArcOfCircle CenterX=41.91 CenterY=35.56 CenterZ=0 NormalX=0 NormalY=0 NormalZ=1 AngleXU=0 Radius=1.5 StartAngle=5.43511 EndAngle=8.5767
    g122: ArcOfCircle CenterX=38.1 CenterY=32.2 CenterZ=0 NormalX=0 NormalY=0 NormalZ=1 AngleXU=0 Radius=1.5 StartAngle=2.29352 EndAngle=5.43511
    g123: LineSegment StartX=42.9021 StartY=34.435 StartZ=0 EndX=39.0921 EndY=31.075 EndZ=0
    g124: LineSegment StartX=40.9179 StartY=36.685 StartZ=0 EndX=37.1079 EndY=33.325 EndZ=0
    g125: ArcOfCircle CenterX=33.1 CenterY=34.3 CenterZ=0 NormalX=0 NormalY=0 NormalZ=1 AngleXU=0 Radius=1.5 StartAngle=1.09102 EndAngle=4.23261
    g126: ArcOfCircle CenterX=35.56 CenterY=33.02 CenterZ=0 NormalX=0 NormalY=0 NormalZ=1 AngleXU=0 Radius=1.5 StartAngle=4.23261 EndAngle=7.37421
    g127: LineSegment StartX=33.7924 StartY=35.6306 StartZ=0 EndX=36.2524 EndY=34.3506 EndZ=0
    g128: LineSegment StartX=32.4076 StartY=32.9694 StartZ=0 EndX=34.8676 EndY=31.6894 EndZ=0
    g129: ArcOfCircle CenterX=60.96 CenterY=35.56 CenterZ=0 NormalX=0 NormalY=0 NormalZ=1 AngleXU=0 Radius=1.5 StartAngle=5.43511 EndAngle=8.5767
    g130: ArcOfCircle CenterX=57.15 CenterY=32.2 CenterZ=0 NormalX=0 NormalY=0 NormalZ=1 AngleXU=0 Radius=1.5 StartAngle=2.29352 EndAngle=5.43511
    g131: LineSegment StartX=61.9521 StartY=34.435 StartZ=0 EndX=58.1421 EndY=31.075 EndZ=0
    g132: LineSegment StartX=59.9679 StartY=36.685 StartZ=0 EndX=56.1579 EndY=33.325 EndZ=0
    g133: ArcOfCircle CenterX=52.15 CenterY=34.3 CenterZ=0 NormalX=0 NormalY=0 NormalZ=1 AngleXU=0 Radius=1.5 StartAngle=1.09102 EndAngle=4.23261
    g134: ArcOfCircle CenterX=54.61 CenterY=33.02 CenterZ=0 NormalX=0 NormalY=0 NormalZ=1 AngleXU=0 Radius=1.5 StartAngle=4.23261 EndAngle=7.37421
    g135: LineSegment StartX=52.8424 StartY=35.6306 StartZ=0 EndX=55.3024 EndY=34.3506 EndZ=0
    g136: LineSegment StartX=51.4576 StartY=32.9694 StartZ=0 EndX=53.9176 EndY=31.6894 EndZ=0
    g137: ArcOfCircle CenterX=80.01 CenterY=35.56 CenterZ=0 NormalX=0 NormalY=0 NormalZ=1 AngleXU=0 Radius=1.5 StartAngle=5.43511 EndAngle=8.5767
    g138: ArcOfCircle CenterX=76.2 CenterY=32.2 CenterZ=0 NormalX=0 NormalY=0 NormalZ=1 AngleXU=0 Radius=1.5 StartAngle=2.29352 EndAngle=5.43511
    g139: LineSegment StartX=81.0021 StartY=34.435 StartZ=0 EndX=77.1921 EndY=31.075 EndZ=0
    g140: LineSegment StartX=79.0179 StartY=36.685 StartZ=0 EndX=75.2079 EndY=33.325 EndZ=0
    g141: ArcOfCircle CenterX=71.2 CenterY=34.3 CenterZ=0 NormalX=0 NormalY=0 NormalZ=1 AngleXU=0 Radius=1.5 StartAngle=1.09102 EndAngle=4.23261
    g142: ArcOfCircle CenterX=73.66 CenterY=33.02 CenterZ=0 NormalX=0 NormalY=0 NormalZ=1 AngleXU=0 Radius=1.5 StartAngle=4.23261 EndAngle=7.37421
    g143: LineSegment StartX=71.8924 StartY=35.6306 StartZ=0 EndX=74.3524 EndY=34.3506 EndZ=0
    g144: LineSegment StartX=70.5076 StartY=32.9694 StartZ=0 EndX=72.9676 EndY=31.6894 EndZ=0
    g145: ArcOfCircle CenterX=99.06 CenterY=35.56 CenterZ=0 NormalX=0 NormalY=0 NormalZ=1 AngleXU=0 Radius=1.5 StartAngle=5.43511 EndAngle=8.5767
    g146: ArcOfCircle CenterX=95.25 CenterY=32.2 CenterZ=0 NormalX=0 NormalY=0 NormalZ=1 AngleXU=0 Radius=1.5 StartAngle=2.29352 EndAngle=5.43511
    g147: LineSegment StartX=100.052 StartY=34.435 StartZ=0 EndX=96.2421 EndY=31.075 EndZ=0
    g148: LineSegment StartX=98.0679 StartY=36.685 StartZ=0 EndX=94.2579 EndY=33.325 EndZ=0
    g149: ArcOfCircle CenterX=90.25 CenterY=34.3 CenterZ=0 NormalX=0 NormalY=0 NormalZ=1 AngleXU=0 Radius=1.5 StartAngle=1.09102 EndAngle=4.23261
    g150: ArcOfCircle CenterX=92.71 CenterY=33.02 CenterZ=0 NormalX=0 NormalY=0 NormalZ=1 AngleXU=0 Radius=1.5 StartAngle=4.23261 EndAngle=7.37421
    g151: LineSegment StartX=90.9424 StartY=35.6306 StartZ=0 EndX=93.4024 EndY=34.3506 EndZ=0
    g152: LineSegment StartX=89.5576 StartY=32.9694 StartZ=0 EndX=92.0176 EndY=31.6894 EndZ=0
    g153: ArcOfCircle CenterX=118.11 CenterY=35.56 CenterZ=0 NormalX=0 NormalY=0 NormalZ=1 AngleXU=0 Radius=1.5 StartAngle=5.43511 EndAngle=8.5767
    g154: ArcOfCircle CenterX=114.3 CenterY=32.2 CenterZ=0 NormalX=0 NormalY=0 NormalZ=1 AngleXU=0 Radius=1.5 StartAngle=2.29352 EndAngle=5.43511
    g155: LineSegment StartX=119.102 StartY=34.435 StartZ=0 EndX=115.292 EndY=31.075 EndZ=0
    g156: LineSegment StartX=117.118 StartY=36.685 StartZ=0 EndX=113.308 EndY=33.325 EndZ=0
    g157: ArcOfCircle CenterX=109.3 CenterY=34.3 CenterZ=0 NormalX=0 NormalY=0 NormalZ=1 AngleXU=0 Radius=1.5 StartAngle=1.09102 EndAngle=4.23261
    g158: ArcOfCircle CenterX=111.76 CenterY=33.02 CenterZ=0 NormalX=0 NormalY=0 NormalZ=1 AngleXU=0 Radius=1.5 StartAngle=4.23261 EndAngle=7.37421
    g159: LineSegment StartX=109.992 StartY=35.6306 StartZ=0 EndX=112.452 EndY=34.3506 EndZ=0
    g160: LineSegment StartX=108.608 StartY=32.9694 StartZ=0 EndX=111.068 EndY=31.6894 EndZ=0
    g161: ArcOfCircle CenterX=137.16 CenterY=35.56 CenterZ=0 NormalX=0 NormalY=0 NormalZ=1 AngleXU=0 Radius=1.5 StartAngle=5.43511 EndAngle=8.5767
    g162: ArcOfCircle CenterX=133.35 CenterY=32.2 CenterZ=0 NormalX=0 NormalY=0 NormalZ=1 AngleXU=0 Radius=1.5 StartAngle=2.29352 EndAngle=5.43511
    g163: LineSegment StartX=138.152 StartY=34.435 StartZ=0 EndX=134.342 EndY=31.075 EndZ=0
    g164: LineSegment StartX=136.168 StartY=36.685 StartZ=0 EndX=132.358 EndY=33.325 EndZ=0
    g165: ArcOfCircle CenterX=128.35 CenterY=34.3 CenterZ=0 NormalX=0 NormalY=0 NormalZ=1 AngleXU=0 Radius=1.5 StartAngle=1.09102 EndAngle=4.23261
    g166: ArcOfCircle CenterX=130.81 CenterY=33.02 CenterZ=0 NormalX=0 NormalY=0 NormalZ=1 AngleXU=0 Radius=1.5 StartAngle=4.23261 EndAngle=7.37421
    g167: LineSegment StartX=129.042 StartY=35.6306 StartZ=0 EndX=131.502 EndY=34.3506 EndZ=0
    g168: LineSegment StartX=127.658 StartY=32.9694 StartZ=0 EndX=130.118 EndY=31.6894 EndZ=0
    g169: ArcOfCircle CenterX=41.91 CenterY=16.51 CenterZ=0 NormalX=0 NormalY=0 NormalZ=1 AngleXU=0 Radius=1.5 StartAngle=5.43511 EndAngle=8.5767
    g170: ArcOfCircle CenterX=38.1 CenterY=13.15 CenterZ=0 NormalX=0 NormalY=0 NormalZ=1 AngleXU=0 Radius=1.5 StartAngle=2.29352 EndAngle=5.43511
    g171: LineSegment StartX=42.9021 StartY=15.385 StartZ=0 EndX=39.0921 EndY=12.025 EndZ=0
    g172: LineSegment StartX=40.9179 StartY=17.635 StartZ=0 EndX=37.1079 EndY=14.275 EndZ=0
    g173: ArcOfCircle CenterX=33.1 CenterY=15.25 CenterZ=0 NormalX=0 NormalY=0 NormalZ=1 AngleXU=0 Radius=1.5 StartAngle=1.09102 EndAngle=4.23261
    g174: ArcOfCircle CenterX=35.56 CenterY=13.97 CenterZ=0 NormalX=0 NormalY=0 NormalZ=1 AngleXU=0 Radius=1.5 StartAngle=4.23261 EndAngle=7.37421
    g175: LineSegment StartX=33.7924 StartY=16.5806 StartZ=0 EndX=36.2524 EndY=15.3006 EndZ=0
    g176: LineSegment StartX=32.4076 StartY=13.9194 StartZ=0 EndX=34.8676 EndY=12.6394 EndZ=0
    g177: ArcOfCircle CenterX=60.96 CenterY=16.51 CenterZ=0 NormalX=0 NormalY=0 NormalZ=1 AngleXU=0 Radius=1.5 StartAngle=5.43511 EndAngle=8.5767
    g178: ArcOfCircle CenterX=57.15 CenterY=13.15 CenterZ=0 NormalX=0 NormalY=0 NormalZ=1 AngleXU=0 Radius=1.5 StartAngle=2.29352 EndAngle=5.43511
    g179: LineSegment StartX=61.9521 StartY=15.385 StartZ=0 EndX=58.1421 EndY=12.025 EndZ=0
    g180: LineSegment StartX=59.9679 StartY=17.635 StartZ=0 EndX=56.1579 EndY=14.275 EndZ=0
    g181: ArcOfCircle CenterX=52.15 CenterY=15.25 CenterZ=0 NormalX=0 NormalY=0 NormalZ=1 AngleXU=0 Radius=1.5 StartAngle=1.09102 EndAngle=4.23261
    g182: ArcOfCircle CenterX=54.61 CenterY=13.97 CenterZ=0 NormalX=0 NormalY=0 NormalZ=1 AngleXU=0 Radius=1.5 StartAngle=4.23261 EndAngle=7.37421
    g183: LineSegment StartX=52.8424 StartY=16.5806 StartZ=0 EndX=55.3024 EndY=15.3006 EndZ=0
    g184: LineSegment StartX=51.4576 StartY=13.9194 StartZ=0 EndX=53.9176 EndY=12.6394 EndZ=0
    g185: ArcOfCircle CenterX=80.01 CenterY=16.51 CenterZ=0 NormalX=0 NormalY=0 NormalZ=1 AngleXU=0 Radius=1.5 StartAngle=5.43511 EndAngle=8.5767
    g186: ArcOfCircle CenterX=76.2 CenterY=13.15 CenterZ=0 NormalX=0 NormalY=0 NormalZ=1 AngleXU=0 Radius=1.5 StartAngle=2.29352 EndAngle=5.43511
    g187: LineSegment StartX=81.0021 StartY=15.385 StartZ=0 EndX=77.1921 EndY=12.025 EndZ=0
    g188: LineSegment StartX=79.0179 StartY=17.635 StartZ=0 EndX=75.2079 EndY=14.275 EndZ=0
    g189: ArcOfCircle CenterX=71.2 CenterY=15.25 CenterZ=0 NormalX=0 NormalY=0 NormalZ=1 AngleXU=0 Radius=1.5 StartAngle=1.09102 EndAngle=4.23261
    g190: ArcOfCircle CenterX=73.66 CenterY=13.97 CenterZ=0 NormalX=0 NormalY=0 NormalZ=1 AngleXU=0 Radius=1.5 StartAngle=4.23261 EndAngle=7.37421
    g191: LineSegment StartX=71.8924 StartY=16.5806 StartZ=0 EndX=74.3524 EndY=15.3006 EndZ=0
    g192: LineSegment StartX=70.5076 StartY=13.9194 StartZ=0 EndX=72.9676 EndY=12.6394 EndZ=0
    g193: ArcOfCircle CenterX=99.06 CenterY=16.51 CenterZ=0 NormalX=0 NormalY=0 NormalZ=1 AngleXU=0 Radius=1.5 StartAngle=5.43511 EndAngle=8.5767
    g194: ArcOfCircle CenterX=95.25 CenterY=13.15 CenterZ=0 NormalX=0 NormalY=0 NormalZ=1 AngleXU=0 Radius=1.5 StartAngle=2.29352 EndAngle=5.43511
    g195: LineSegment StartX=100.052 StartY=15.385 StartZ=0 EndX=96.2421 EndY=12.025 EndZ=0
    g196: LineSegment StartX=98.0679 StartY=17.635 StartZ=0 EndX=94.2579 EndY=14.275 EndZ=0
    g197: ArcOfCircle CenterX=90.25 CenterY=15.25 CenterZ=0 NormalX=0 NormalY=0 NormalZ=1 AngleXU=0 Radius=1.5 StartAngle=1.09102 EndAngle=4.23261
    g198: ArcOfCircle CenterX=92.71 CenterY=13.97 CenterZ=0 NormalX=0 NormalY=0 NormalZ=1 AngleXU=0 Radius=1.5 StartAngle=4.23261 EndAngle=7.37421
    g199: LineSegment StartX=90.9424 StartY=16.5806 StartZ=0 EndX=93.4024 EndY=15.3006 EndZ=0
    g200: LineSegment StartX=89.5576 StartY=13.9194 StartZ=0 EndX=92.0176 EndY=12.6394 EndZ=0
    g201: ArcOfCircle CenterX=118.11 CenterY=16.51 CenterZ=0 NormalX=0 NormalY=0 NormalZ=1 AngleXU=0 Radius=1.5 StartAngle=5.43511 EndAngle=8.5767
    g202: ArcOfCircle CenterX=114.3 CenterY=13.15 CenterZ=0 NormalX=0 NormalY=0 NormalZ=1 AngleXU=0 Radius=1.5 StartAngle=2.29352 EndAngle=5.43511
    g203: LineSegment StartX=119.102 StartY=15.385 StartZ=0 EndX=115.292 EndY=12.025 EndZ=0
    g204: LineSegment StartX=117.118 StartY=17.635 StartZ=0 EndX=113.308 EndY=14.275 EndZ=0
    g205: ArcOfCircle CenterX=109.3 CenterY=15.25 CenterZ=0 NormalX=0 NormalY=0 NormalZ=1 AngleXU=0 Radius=1.5 StartAngle=1.09102 EndAngle=4.23261
    g206: ArcOfCircle CenterX=111.76 CenterY=13.97 CenterZ=0 NormalX=0 NormalY=0 NormalZ=1 AngleXU=0 Radius=1.5 StartAngle=4.23261 EndAngle=7.37421
    g207: LineSegment StartX=109.992 StartY=16.5806 StartZ=0 EndX=112.452 EndY=15.3006 EndZ=0
    g208: LineSegment StartX=108.608 StartY=13.9194 StartZ=0 EndX=111.068 EndY=12.6394 EndZ=0
    g209: ArcOfCircle CenterX=137.16 CenterY=16.51 CenterZ=0 NormalX=0 NormalY=0 NormalZ=1 AngleXU=0 Radius=1.5 StartAngle=5.43511 EndAngle=8.5767
    g210: ArcOfCircle CenterX=133.35 CenterY=13.15 CenterZ=0 NormalX=0 NormalY=0 NormalZ=1 AngleXU=0 Radius=1.5 StartAngle=2.29352 EndAngle=5.43511
    g211: LineSegment StartX=138.152 StartY=15.385 StartZ=0 EndX=134.342 EndY=12.025 EndZ=0
    g212: LineSegment StartX=136.168 StartY=17.635 StartZ=0 EndX=132.358 EndY=14.275 EndZ=0
    g213: ArcOfCircle CenterX=128.35 CenterY=15.25 CenterZ=0 NormalX=0 NormalY=0 NormalZ=1 AngleXU=0 Radius=1.5 StartAngle=1.09102 EndAngle=4.23261
    g214: ArcOfCircle CenterX=130.81 CenterY=13.97 CenterZ=0 NormalX=0 NormalY=0 NormalZ=1 AngleXU=0 Radius=1.5 StartAngle=4.23261 EndAngle=7.37421
    g215: LineSegment StartX=129.042 StartY=16.5806 StartZ=0 EndX=131.502 EndY=15.3006 EndZ=0
    g216: LineSegment StartX=127.658 StartY=13.9194 StartZ=0 EndX=130.118 EndY=12.6394 EndZ=0
    g217: ArcOfCircle CenterX=22.86 CenterY=16.51 CenterZ=0 NormalX=0 NormalY=0 NormalZ=1 AngleXU=0 Radius=1.5 StartAngle=5.43511 EndAngle=8.5767
    g218: ArcOfCircle CenterX=19.05 CenterY=13.15 CenterZ=0 NormalX=0 NormalY=0 NormalZ=1 AngleXU=0 Radius=1.5 StartAngle=2.29352 EndAngle=5.43511
    g219: LineSegment StartX=23.8521 StartY=15.385 StartZ=0 EndX=20.0421 EndY=12.025 EndZ=0
    g220: LineSegment StartX=21.8679 StartY=17.635 StartZ=0 EndX=18.0579 EndY=14.275 EndZ=0
    g221: ArcOfCircle CenterX=14.05 CenterY=15.25 CenterZ=0 NormalX=0 NormalY=0 NormalZ=1 AngleXU=0 Radius=1.5 StartAngle=1.09102 EndAngle=4.23261
    g222: ArcOfCircle CenterX=16.51 CenterY=13.97 CenterZ=0 NormalX=0 NormalY=0 NormalZ=1 AngleXU=0 Radius=1.5 StartAngle=4.23261 EndAngle=7.37421
    g223: LineSegment StartX=14.7424 StartY=16.5806 StartZ=0 EndX=17.2024 EndY=15.3006 EndZ=0
    g224: LineSegment StartX=13.3576 StartY=13.9194 StartZ=0 EndX=15.8176 EndY=12.6394 EndZ=0
    g225: GeomPoint X=19.05 Y=19.05 Z=0
    g226: GeomPoint [constr] X=38.1 Y=70.3 Z=0
    g227: GeomPoint [constr] X=19.05 Y=13.15 Z=0
    g228: GeomPoint [constr] X=133.35 Y=70.3 Z=0
  constraints (530):
    c: DistanceX(g1,g0) = 19.05
    c: DistanceX(g2,g1) = 19.05
    c: DistanceX(g3,g2) = 19.05
    c: DistanceX(g4,g3) = 19.05
    c: DistanceX(g23,g4) = 19.05
    c: Horizontal(g17,g18)
    c: Horizontal(g18,g15)
    c: Horizontal(g15,g19)
    c: Horizontal(g19,g16)
    c: Horizontal(g16,g20)
    c: Horizontal(g21,g9)
    c: Horizontal(g9,g8)
    c: Horizontal(g8,g7)
    c: Horizontal(g7,g6)
    c: Horizontal(g6,g5)
    c: Horizontal(g22,g14)
    c: Horizontal(g14,g13)
    c: Horizontal(g13,g12)
    c: Horizontal(g12,g11)
    c: Horizontal(g11,g10)
    c: Vertical(g17,g21)
    c: Vertical(g21,g22)
    c: Vertical(g22,g23)
    c: Vertical(g18,g9)
    c: Vertical(g9,g14)
    c: Vertical(g14,g4)
    c: Vertical(g15,g8)
    c: Vertical(g8,g13)
    c: Vertical(g13,g3)
    c: Vertical(g19,g7)
    c: Vertical(g7,g12)
    c: Vertical(g12,g2)
    c: Vertical(g16,g6)
    c: Vertical(g6,g11)
    c: Vertical(g11,g1)
    c: Vertical(g20,g5)
    c: Vertical(g5,g10)
    c: Vertical(g10,g0)
    c: Horizontal(g23,g4)
    c: Horizontal(g4,g3)
    c: Horizontal(g3,g2)
    c: Horizontal(g2,g1)
    c: Horizontal(g1,g0)
    c: Horizontal(g0,g24)
    c: Tangent(g25,g27) = 1.5708
    c: Tangent(g25,g28) = -1.5708
    c: Tangent(g26,g27) = 1.5708
    c: Tangent(g26,g28) = -1.5708
    c: Equal(g25,g26)
    c: Tangent(g29,g31) = 1.5708
    c: Tangent(g29,g32) = -1.5708
    c: Tangent(g30,g31) = 1.5708
    c: Tangent(g30,g32) = -1.5708
    c: Equal(g29,g30)
    c: Tangent(g33,g35) = 1.5708
    c: Tangent(g33,g36) = -1.5708
    c: Tangent(g34,g35) = 1.5708
    c: Tangent(g34,g36) = -1.5708
    c: Equal(g33,g34)
    c: Tangent(g37,g39) = 1.5708
    c: Tangent(g37,g40) = -1.5708
    c: Tangent(g38,g39) = 1.5708
    c: Tangent(g38,g40) = -1.5708
    c: Equal(g37,g38)
    c: Tangent(g41,g43) = 1.5708
    c: Tangent(g41,g44) = -1.5708
    c: Tangent(g42,g43) = 1.5708
    c: Tangent(g42,g44) = -1.5708
    c: Equal(g41,g42)
    c: Tangent(g45,g47) = 1.5708
    c: Tangent(g45,g48) = -1.5708
    c: Tangent(g46,g47) = 1.5708
    c: Tangent(g46,g48) = -1.5708
    c: Equal(g45,g46)
    c: Tangent(g49,g51) = 1.5708
    c: Tangent(g49,g52) = -1.5708
    c: Tangent(g50,g51) = 1.5708
    c: Tangent(g50,g52) = -1.5708
    c: Equal(g49,g50)
    c: Tangent(g53,g55) = 1.5708
    c: Tangent(g53,g56) = -1.5708
    c: Tangent(g54,g55) = 1.5708
    c: Tangent(g54,g56) = -1.5708
    c: Equal(g53,g54)
    c: Tangent(g57,g59) = 1.5708
    c: Tangent(g57,g60) = -1.5708
    c: Tangent(g58,g59) = 1.5708
    c: Tangent(g58,g60) = -1.5708
    c: Equal(g57,g58)
    c: Tangent(g61,g63) = 1.5708
    c: Tangent(g61,g64) = -1.5708
    c: Tangent(g62,g63) = 1.5708
    c: Tangent(g62,g64) = -1.5708
    c: Equal(g61,g62)
    c: Tangent(g65,g67) = 1.5708
    c: Tangent(g65,g68) = -1.5708
    c: Tangent(g66,g67) = 1.5708
    c: Tangent(g66,g68) = -1.5708
    c: Equal(g65,g66)
    c: Tangent(g69,g71) = 1.5708
    c: Tangent(g69,g72) = -1.5708
    c: Tangent(g70,g71) = 1.5708
    c: Tangent(g70,g72) = -1.5708
    c: Equal(g69,g70)
    c: Tangent(g73,g75) = 1.5708
    c: Tangent(g73,g76) = -1.5708
    c: Tangent(g74,g75) = 1.5708
    c: Tangent(g74,g76) = -1.5708
    c: Equal(g73,g74)
    c: Tangent(g77,g79) = 1.5708
    c: Tangent(g77,g80) = -1.5708
    c: Tangent(g78,g79) = 1.5708
    c: Tangent(g78,g80) = -1.5708
    c: Equal(g77,g78)
    c: Tangent(g81,g83) = 1.5708
    c: Tangent(g81,g84) = -1.5708
    c: Tangent(g82,g83) = 1.5708
    c: Tangent(g82,g84) = -1.5708
    c: Equal(g81,g82)
    c: Tangent(g85,g87) = 1.5708
    c: Tangent(g85,g88) = -1.5708
    c: Tangent(g86,g87) = 1.5708
    c: Tangent(g86,g88) = -1.5708
    c: Equal(g85,g86)
    c: Tangent(g89,g91) = 1.5708
    c: Tangent(g89,g92) = -1.5708
    c: Tangent(g90,g91) = 1.5708
    c: Tangent(g90,g92) = -1.5708
    c: Equal(g89,g90)
    c: Tangent(g93,g95) = 1.5708
    c: Tangent(g93,g96) = -1.5708
    c: Tangent(g94,g95) = 1.5708
    c: Tangent(g94,g96) = -1.5708
    c: Equal(g93,g94)
    c: Tangent(g97,g99) = 1.5708
    c: Tangent(g97,g100) = -1.5708
    c: Tangent(g98,g99) = 1.5708
    c: Tangent(g98,g100) = -1.5708
    c: Equal(g97,g98)
    c: Tangent(g101,g103) = 1.5708
    c: Tangent(g101,g104) = -1.5708
    c: Tangent(g102,g103) = 1.5708
    c: Tangent(g102,g104) = -1.5708
    c: Equal(g101,g102)
    c: Tangent(g105,g107) = 1.5708
    c: Tangent(g105,g108) = -1.5708
    c: Tangent(g106,g107) = 1.5708
    c: Tangent(g106,g108) = -1.5708
    c: Equal(g105,g106)
    c: Tangent(g109,g111) = 1.5708
    c: Tangent(g109,g112) = -1.5708
    c: Tangent(g110,g111) = 1.5708
    c: Tangent(g110,g112) = -1.5708
    c: Equal(g109,g110)
    c: Tangent(g113,g115) = 1.5708
    c: Tangent(g113,g116) = -1.5708
    c: Tangent(g114,g115) = 1.5708
    c: Tangent(g114,g116) = -1.5708
    c: Equal(g113,g114)
    c: Tangent(g117,g119) = 1.5708
    c: Tangent(g117,g120) = -1.5708
    c: Tangent(g118,g119) = 1.5708
    c: Tangent(g118,g120) = -1.5708
    c: Equal(g117,g118)
    c: Tangent(g121,g123) = 1.5708
    c: Tangent(g121,g124) = -1.5708
    c: Tangent(g122,g123) = 1.5708
    c: Tangent(g122,g124) = -1.5708
    c: Equal(g121,g122)
    c: Tangent(g125,g127) = 1.5708
    c: Tangent(g125,g128) = -1.5708
    c: Tangent(g126,g127) = 1.5708
    c: Tangent(g126,g128) = -1.5708
    c: Equal(g125,g126)
    c: Tangent(g129,g131) = 1.5708
    c: Tangent(g129,g132) = -1.5708
    c: Tangent(g130,g131) = 1.5708
    c: Tangent(g130,g132) = -1.5708
    c: Equal(g129,g130)
    c: Tangent(g133,g135) = 1.5708
    c: Tangent(g133,g136) = -1.5708
    c: Tangent(g134,g135) = 1.5708
    c: Tangent(g134,g136) = -1.5708
    c: Equal(g133,g134)
    c: Tangent(g137,g139) = 1.5708
    c: Tangent(g137,g140) = -1.5708
    c: Tangent(g138,g139) = 1.5708
    c: Tangent(g138,g140) = -1.5708
    c: Equal(g137,g138)
    c: Tangent(g141,g143) = 1.5708
    c: Tangent(g141,g144) = -1.5708
    c: Tangent(g142,g143) = 1.5708
    c: Tangent(g142,g144) = -1.5708
    c: Equal(g141,g142)
    c: Tangent(g145,g147) = 1.5708
    c: Tangent(g145,g148) = -1.5708
    c: Tangent(g146,g147) = 1.5708
    c: Tangent(g146,g148) = -1.5708
    c: Equal(g145,g146)
    c: Tangent(g149,g151) = 1.5708
    c: Tangent(g149,g152) = -1.5708
    c: Tangent(g150,g151) = 1.5708
    c: Tangent(g150,g152) = -1.5708
    c: Equal(g149,g150)
    c: Tangent(g153,g155) = 1.5708
    c: Tangent(g153,g156) = -1.5708
    c: Tangent(g154,g155) = 1.5708
    c: Tangent(g154,g156) = -1.5708
    c: Equal(g153,g154)
    c: Tangent(g157,g159) = 1.5708
    c: Tangent(g157,g160) = -1.5708
    c: Tangent(g158,g159) = 1.5708
    c: Tangent(g158,g160) = -1.5708
    c: Equal(g157,g158)
    c: Tangent(g161,g163) = 1.5708
    c: Tangent(g161,g164) = -1.5708
    c: Tangent(g162,g163) = 1.5708
    c: Tangent(g162,g164) = -1.5708
    c: Equal(g161,g162)
    c: Tangent(g165,g167) = 1.5708
    c: Tangent(g165,g168) = -1.5708
    c: Tangent(g166,g167) = 1.5708
    c: Tangent(g166,g168) = -1.5708
    c: Equal(g165,g166)
    c: Tangent(g169,g171) = 1.5708
    c: Tangent(g169,g172) = -1.5708
    c: Tangent(g170,g171) = 1.5708
    c: Tangent(g170,g172) = -1.5708
    c: Equal(g169,g170)
    c: Tangent(g173,g175) = 1.5708
    c: Tangent(g173,g176) = -1.5708
    c: Tangent(g174,g175) = 1.5708
    c: Tangent(g174,g176) = -1.5708
    c: Equal(g173,g174)
    c: DistanceX(g173,g174) = 2.46
    c: DistanceX(g174,g170) = 2.54
    c: DistanceX(g170,g169) = 3.81
    c: Tangent(g177,g179) = 1.5708
    c: Tangent(g177,g180) = -1.5708
    c: Tangent(g178,g179) = 1.5708
    c: Tangent(g178,g180) = -1.5708
    c: Equal(g177,g178)
    c: Tangent(g181,g183) = 1.5708
    c: Tangent(g181,g184) = -1.5708
    c: Tangent(g182,g183) = 1.5708
    c: Tangent(g182,g184) = -1.5708
    c: Equal(g181,g182)
    c: DistanceX(g181,g182) = 2.46
    c: DistanceX(g182,g178) = 2.54
    c: DistanceX(g178,g177) = 3.81
    c: Tangent(g185,g187) = 1.5708
    c: Tangent(g185,g188) = -1.5708
    c: Tangent(g186,g187) = 1.5708
    c: Tangent(g186,g188) = -1.5708
    c: Equal(g185,g186)
    c: Tangent(g189,g191) = 1.5708
    c: Tangent(g189,g192) = -1.5708
    c: Tangent(g190,g191) = 1.5708
    c: Tangent(g190,g192) = -1.5708
    c: Equal(g189,g190)
    c: DistanceX(g189,g190) = 2.46
    c: DistanceX(g190,g186) = 2.54
    c: DistanceX(g186,g185) = 3.81
    c: Tangent(g193,g195) = 1.5708
    c: Tangent(g193,g196) = -1.5708
    c: Tangent(g194,g195) = 1.5708
    c: Tangent(g194,g196) = -1.5708
    c: Equal(g193,g194)
    c: Tangent(g197,g199) = 1.5708
    c: Tangent(g197,g200) = -1.5708
    c: Tangent(g198,g199) = 1.5708
    c: Tangent(g198,g200) = -1.5708
    c: Equal(g197,g198)
    c: DistanceX(g197,g198) = 2.46
    c: DistanceX(g198,g194) = 2.54
    c: DistanceX(g194,g193) = 3.81
    c: Tangent(g201,g203) = 1.5708
    c: Tangent(g201,g204) = -1.5708
    c: Tangent(g202,g203) = 1.5708
    c: Tangent(g202,g204) = -1.5708
    c: Equal(g201,g202)
    c: Tangent(g205,g207) = 1.5708
    c: Tangent(g205,g208) = -1.5708
    c: Tangent(g206,g207) = 1.5708
    c: Tangent(g206,g208) = -1.5708
    c: Equal(g205,g206)
    c: DistanceX(g205,g206) = 2.46
    c: DistanceX(g206,g202) = 2.54
    c: DistanceX(g202,g201) = 3.81
    c: Tangent(g209,g211) = 1.5708
    c: Tangent(g209,g212) = -1.5708
    c: Tangent(g210,g211) = 1.5708
    c: Tangent(g210,g212) = -1.5708
    c: Equal(g209,g210)
    c: Tangent(g213,g215) = 1.5708
    c: Tangent(g213,g216) = -1.5708
    c: Tangent(g214,g215) = 1.5708
    c: Tangent(g214,g216) = -1.5708
    c: Equal(g213,g214)
    c: DistanceX(g213,g214) = 2.46
    c: DistanceX(g214,g210) = 2.54
    c: DistanceX(g210,g209) = 3.81
    c: Tangent(g217,g219) = 1.5708
    c: Tangent(g217,g220) = -1.5708
    c: Tangent(g218,g219) = 1.5708
    c: Tangent(g218,g220) = -1.5708
    c: Equal(g217,g218)
    c: Tangent(g221,g223) = 1.5708
    c: Tangent(g221,g224) = -1.5708
    c: Tangent(g222,g223) = 1.5708
    c: Tangent(g222,g224) = -1.5708
    c: Equal(g221,g222)
    c: DistanceX(g221,g222) = 2.46
    c: DistanceX(g222,g218) = 2.54
    c: DistanceX(g218,g217) = 3.81
    c: DistanceY(g222,g221) = 1.28
    c: DistanceY(g221,g217) = 1.26
    c: Coincident(g26,g17)
    c: Coincident(g34,g18)
    c: Coincident(g42,g15)
    c: Coincident(g50,g19)
    c: Coincident(g58,g16)
    c: Coincident(g66,g20)
    c: Coincident(g74,g21)
    c: Coincident(g82,g9)
    c: Coincident(g90,g8)
    c: Coincident(g98,g7)
    c: Coincident(g106,g6)
    c: Coincident(g114,g5)
    c: Coincident(g122,g22)
    c: Coincident(g130,g14)
    c: Coincident(g138,g13)
    c: Coincident(g146,g12)
    c: Coincident(g154,g11)
    c: Coincident(g162,g10)
    c: Coincident(g170,g23)
    c: Coincident(g178,g4)
    c: Coincident(g186,g3)
    c: Coincident(g194,g2)
    c: Coincident(g202,g1)
    c: Coincident(g210,g0)
    c: Coincident(g218,g24)
    c: Equal(g30,g26)
    c: Equal(g38,g34)
    c: Equal(g46,g42)
    c: Equal(g54,g50)
    c: Equal(g62,g58)
    c: Equal(g70,g66)
    c: Equal(g78,g74)
    c: Equal(g86,g82)
    c: Equal(g94,g90)
    c: Equal(g102,g98)
    c: Equal(g110,g106)
    c: Equal(g118,g114)
    c: Equal(g126,g122)
    c: Equal(g134,g130)
    c: Equal(g142,g138)
    c: Equal(g150,g146)
    c: Equal(g158,g154)
    c: Equal(g166,g162)
    c: Equal(g174,g170)
    c: Equal(g182,g178)
    c: Equal(g190,g186)
    c: Equal(g198,g194)
    c: Equal(g206,g202)
    c: Equal(g214,g210)
    c: Equal(g222,g218)
    c: Equal(g26,g34)
    c: Equal(g34,g42)
    c: Equal(g42,g50)
    c: Equal(g50,g58)
    c: Equal(g58,g66)
    c: Equal(g74,g82)
    c: Equal(g82,g90)
    c: Equal(g90,g98)
    c: Equal(g98,g106)
    c: Equal(g106,g114)
    c: Equal(g122,g130)
    c: Equal(g130,g138)
    c: Equal(g138,g146)
    c: Equal(g146,g154)
    c: Equal(g154,g162)
    c: Equal(g170,g178)
    c: Equal(g178,g186)
    c: Equal(g186,g194)
    c: Equal(g194,g202)
    c: Equal(g202,g210)
    c: Equal(g210,g218)
    c: Diameter(g218) = 3
    c: Equal(g66,g114)
    c: Equal(g114,g162)
    c: Equal(g162,g210)
    c: Vertical(g29,g77)
    c: Vertical(g77,g125)
    c: Vertical(g125,g173)
    c: Vertical(g30,g78)
    c: Vertical(g78,g126)
    c: Vertical(g126,g174)
    c: Vertical(g25,g73)
    c: Vertical(g73,g121)
    c: Vertical(g121,g169)
    c: Vertical(g37,g85)
    c: Vertical(g85,g133)
    c: Vertical(g133,g181)
    c: Vertical(g38,g86)
    c: Vertical(g86,g134)
    c: Vertical(g134,g182)
    c: Vertical(g33,g81)
    c: Vertical(g81,g129)
    c: Vertical(g129,g177)
    c: Vertical(g45,g93)
    c: Vertical(g93,g141)
    c: Vertical(g141,g189)
    c: Vertical(g46,g94)
    c: Vertical(g94,g142)
    c: Vertical(g142,g190)
    c: Vertical(g41,g89)
    c: Vertical(g89,g137)
    c: Vertical(g137,g185)
    c: Vertical(g53,g101)
    c: Vertical(g101,g149)
    c: Vertical(g149,g197)
    c: Vertical(g54,g102)
    c: Vertical(g102,g150)
    c: Vertical(g150,g198)
    c: Vertical(g49,g97)
    c: Vertical(g97,g145)
    c: Vertical(g145,g193)
    c: Vertical(g61,g109)
    c: Vertical(g109,g157)
    c: Vertical(g157,g205)
    c: Vertical(g62,g110)
    c: Vertical(g110,g158)
    c: Vertical(g158,g206)
    c: Vertical(g57,g105)
    c: Vertical(g105,g153)
    c: Vertical(g153,g201)
    c: Vertical(g69,g117)
    c: Vertical(g117,g165)
    c: Vertical(g165,g213)
    c: Vertical(g70,g118)
    c: Vertical(g118,g166)
    c: Vertical(g166,g214)
    c: Vertical(g65,g113)
    c: Vertical(g113,g161)
    c: Vertical(g161,g209)
    c: Horizontal(g25,g33)
    c: Horizontal(g33,g41)
    c: Horizontal(g41,g49)
    c: Horizontal(g49,g57)
    c: Horizontal(g57,g65)
    c: Horizontal(g29,g37)
    c: Horizontal(g37,g45)
    c: Horizontal(g45,g53)
    c: Horizontal(g53,g61)
    c: Horizontal(g61,g69)
    c: Horizontal(g30,g38)
    c: Horizontal(g38,g46)
    c: Horizontal(g46,g54)
    c: Horizontal(g54,g62)
    c: Horizontal(g62,g70)
    c: Horizontal(g73,g81)
    c: Horizontal(g81,g89)
    c: Horizontal(g89,g97)
    c: Horizontal(g97,g105)
    c: Horizontal(g105,g113)
    c: Horizontal(g77,g85)
    c: Horizontal(g85,g93)
    c: Horizontal(g93,g101)
    c: Horizontal(g101,g109)
    c: Horizontal(g109,g117)
    c: Horizontal(g78,g86)
    c: Horizontal(g86,g94)
    c: Horizontal(g94,g102)
    c: Horizontal(g102,g110)
    c: Horizontal(g110,g118)
    c: Horizontal(g121,g129)
    c: Horizontal(g129,g137)
    c: Horizontal(g137,g145)
    c: Horizontal(g145,g153)
    c: Horizontal(g153,g161)
    c: Horizontal(g125,g133)
    c: Horizontal(g133,g141)
    c: Horizontal(g141,g149)
    c: Horizontal(g149,g157)
    c: Horizontal(g157,g165)
    c: Horizontal(g126,g134)
    c: Horizontal(g134,g142)
    c: Horizontal(g142,g150)
    c: Horizontal(g150,g158)
    c: Horizontal(g158,g166)
    c: Horizontal(g169,g177)
    c: Horizontal(g177,g185)
    c: Horizontal(g185,g193)
    c: Horizontal(g193,g201)
    c: Horizontal(g201,g209)
    c: Horizontal(g209,g217)
    c: Horizontal(g173,g181)
    c: Horizontal(g181,g189)
    c: Horizontal(g189,g197)
    c: Horizontal(g197,g205)
    c: Horizontal(g205,g213)
    c: Horizontal(g213,g221)
    c: Horizontal(g174,g182)
    c: Horizontal(g182,g190)
    c: Horizontal(g190,g198)
    c: Horizontal(g198,g206)
    c: Horizontal(g206,g214)
    c: Horizontal(g214,g222)
    c: DistanceY(g24,g222) = 0.82
    c: DistanceX(g-1,g24) = 19.05
    c: DistanceX(g24,g23) = 19.05
    c: DistanceY(g21,g17) = 19.05
    c: DistanceY(g22,g21) = 19.05
    c: DistanceY(g24,g22) = 19.05
    c: DistanceY(g125,g121) = 1.26
    c: DistanceY(g126,g125) = 1.28
    c: DistanceY(g22,g126) = 0.82
    c: DistanceY(g77,g73) = 1.26
    c: DistanceY(g78,g77) = 1.28
    c: DistanceY(g21,g78) = 0.82
    c: DistanceY(g29,g25) = 1.26
    c: DistanceY(g30,g29) = 1.28
    c: DistanceY(g17,g30) = 0.82
    c: DistanceX(g-1,g225) = 19.05
    c: DistanceY(g-1,g225) = 19.05
    c: DistanceY(g24,g225) = 5.9
    c: Coincident(g228,g20)
    c: Coincident(g226,g17)
    c: Coincident(g227,g24)
FEATURE [Sketcher::SketchObject] Sketch027  label="BR-LED"
  ArcFitTolerance = 1e-06
  AttachmentSupport = -> [XY_Plane003]
  FullyConstrained = true
  MakeInternals = false
  MapMode = 5
  expr: Constraints[311] = VarSet.Bottom_LedX
  expr: Constraints[312] = VarSet.Bottom_LedY
  sketch-geometry (126):
    g0: GeomPoint X=19.05 Y=19.05 Z=0
    g1: LineSegment StartX=34.1 StartY=82.5 StartZ=0 EndX=34.1 EndY=79.3 EndZ=0
    g2: LineSegment StartX=34.1 StartY=79.3 StartZ=0 EndX=42.1 EndY=79.3 EndZ=0
    g3: LineSegment StartX=42.1 StartY=79.3 StartZ=0 EndX=42.1 EndY=82.5 EndZ=0
    g4: LineSegment StartX=42.1 StartY=82.5 StartZ=0 EndX=34.1 EndY=82.5 EndZ=0
    g5: GeomPoint [constr] X=38.1 Y=80.9 Z=0
    g6: LineSegment StartX=53.15 StartY=82.5 StartZ=0 EndX=53.15 EndY=79.3 EndZ=0
    g7: LineSegment StartX=53.15 StartY=79.3 StartZ=0 EndX=61.15 EndY=79.3 EndZ=0
    g8: LineSegment StartX=61.15 StartY=79.3 StartZ=0 EndX=61.15 EndY=82.5 EndZ=0
    g9: LineSegment StartX=61.15 StartY=82.5 StartZ=0 EndX=53.15 EndY=82.5 EndZ=0
    g10: GeomPoint [constr] X=57.15 Y=80.9 Z=0
    g11: LineSegment StartX=72.2 StartY=82.5 StartZ=0 EndX=72.2 EndY=79.3 EndZ=0
    g12: LineSegment StartX=72.2 StartY=79.3 StartZ=0 EndX=80.2 EndY=79.3 EndZ=0
    g13: LineSegment StartX=80.2 StartY=79.3 StartZ=0 EndX=80.2 EndY=82.5 EndZ=0
    g14: LineSegment StartX=80.2 StartY=82.5 StartZ=0 EndX=72.2 EndY=82.5 EndZ=0
    g15: GeomPoint [constr] X=76.2 Y=80.9 Z=0
    g16: LineSegment StartX=91.25 StartY=82.5 StartZ=0 EndX=91.25 EndY=79.3 EndZ=0
    g17: LineSegment StartX=91.25 StartY=79.3 StartZ=0 EndX=99.25 EndY=79.3 EndZ=0
    g18: LineSegment StartX=99.25 StartY=79.3 StartZ=0 EndX=99.25 EndY=82.5 EndZ=0
    g19: LineSegment StartX=99.25 StartY=82.5 StartZ=0 EndX=91.25 EndY=82.5 EndZ=0
    g20: GeomPoint [constr] X=95.25 Y=80.9 Z=0
    g21: LineSegment StartX=110.3 StartY=82.5 StartZ=0 EndX=110.3 EndY=79.3 EndZ=0
    g22: LineSegment StartX=110.3 StartY=79.3 StartZ=0 EndX=118.3 EndY=79.3 EndZ=0
    g23: LineSegment StartX=118.3 StartY=79.3 StartZ=0 EndX=118.3 EndY=82.5 EndZ=0
    g24: LineSegment StartX=118.3 StartY=82.5 StartZ=0 EndX=110.3 EndY=82.5 EndZ=0
    g25: GeomPoint [constr] X=114.3 Y=80.9 Z=0
    g26: LineSegment StartX=129.35 StartY=82.5 StartZ=0 EndX=129.35 EndY=79.3 EndZ=0
    g27: LineSegment StartX=129.35 StartY=79.3 StartZ=0 EndX=137.35 EndY=79.3 EndZ=0
    g28: LineSegment StartX=137.35 StartY=79.3 StartZ=0 EndX=137.35 EndY=82.5 EndZ=0
    g29: LineSegment StartX=137.35 StartY=82.5 StartZ=0 EndX=129.35 EndY=82.5 EndZ=0
    g30: GeomPoint [constr] X=133.35 Y=80.9 Z=0
    g31: LineSegment StartX=34.1 StartY=63.45 StartZ=0 EndX=34.1 EndY=60.25 EndZ=0
    g32: LineSegment StartX=34.1 StartY=60.25 StartZ=0 EndX=42.1 EndY=60.25 EndZ=0
    g33: LineSegment StartX=42.1 StartY=60.25 StartZ=0 EndX=42.1 EndY=63.45 EndZ=0
    g34: LineSegment StartX=42.1 StartY=63.45 StartZ=0 EndX=34.1 EndY=63.45 EndZ=0
    g35: GeomPoint [constr] X=38.1 Y=61.85 Z=0
    g36: LineSegment StartX=53.15 StartY=63.45 StartZ=0 EndX=53.15 EndY=60.25 EndZ=0
    g37: LineSegment StartX=53.15 StartY=60.25 StartZ=0 EndX=61.15 EndY=60.25 EndZ=0
    g38: LineSegment StartX=61.15 StartY=60.25 StartZ=0 EndX=61.15 EndY=63.45 EndZ=0
    g39: LineSegment StartX=61.15 StartY=63.45 StartZ=0 EndX=53.15 EndY=63.45 EndZ=0
    g40: GeomPoint [constr] X=57.15 Y=61.85 Z=0
    g41: LineSegment StartX=72.2 StartY=63.45 StartZ=0 EndX=72.2 EndY=60.25 EndZ=0
    g42: LineSegment StartX=72.2 StartY=60.25 StartZ=0 EndX=80.2 EndY=60.25 EndZ=0
    g43: LineSegment StartX=80.2 StartY=60.25 StartZ=0 EndX=80.2 EndY=63.45 EndZ=0
    g44: LineSegment StartX=80.2 StartY=63.45 StartZ=0 EndX=72.2 EndY=63.45 EndZ=0
    g45: GeomPoint [constr] X=76.2 Y=61.85 Z=0
    g46: LineSegment StartX=91.25 StartY=63.45 StartZ=0 EndX=91.25 EndY=60.25 EndZ=0
    g47: LineSegment StartX=91.25 StartY=60.25 StartZ=0 EndX=99.25 EndY=60.25 EndZ=0
    g48: LineSegment StartX=99.25 StartY=60.25 StartZ=0 EndX=99.25 EndY=63.45 EndZ=0
    g49: LineSegment StartX=99.25 StartY=63.45 StartZ=0 EndX=91.25 EndY=63.45 EndZ=0
    g50: GeomPoint [constr] X=95.25 Y=61.85 Z=0
    g51: LineSegment StartX=110.3 StartY=63.45 StartZ=0 EndX=110.3 EndY=60.25 EndZ=0
    g52: LineSegment StartX=110.3 StartY=60.25 StartZ=0 EndX=118.3 EndY=60.25 EndZ=0
    g53: LineSegment StartX=118.3 StartY=60.25 StartZ=0 EndX=118.3 EndY=63.45 EndZ=0
    g54: LineSegment StartX=118.3 StartY=63.45 StartZ=0 EndX=110.3 EndY=63.45 EndZ=0
    g55: GeomPoint [constr] X=114.3 Y=61.85 Z=0
    g56: LineSegment StartX=129.35 StartY=63.45 StartZ=0 EndX=129.35 EndY=60.25 EndZ=0
    g57: LineSegment StartX=129.35 StartY=60.25 StartZ=0 EndX=137.35 EndY=60.25 EndZ=0
    g58: LineSegment StartX=137.35 StartY=60.25 StartZ=0 EndX=137.35 EndY=63.45 EndZ=0
    g59: LineSegment StartX=137.35 StartY=63.45 StartZ=0 EndX=129.35 EndY=63.45 EndZ=0
    g60: GeomPoint [constr] X=133.35 Y=61.85 Z=0
    g61: LineSegment StartX=34.1 StartY=44.4 StartZ=0 EndX=34.1 EndY=41.2 EndZ=0
    g62: LineSegment StartX=34.1 StartY=41.2 StartZ=0 EndX=42.1 EndY=41.2 EndZ=0
    g63: LineSegment StartX=42.1 StartY=41.2 StartZ=0 EndX=42.1 EndY=44.4 EndZ=0
    g64: LineSegment StartX=42.1 StartY=44.4 StartZ=0 EndX=34.1 EndY=44.4 EndZ=0
    g65: GeomPoint [constr] X=38.1 Y=42.8 Z=0
    g66: LineSegment StartX=53.15 StartY=44.4 StartZ=0 EndX=53.15 EndY=41.2 EndZ=0
    g67: LineSegment StartX=53.15 StartY=41.2 StartZ=0 EndX=61.15 EndY=41.2 EndZ=0
    g68: LineSegment StartX=61.15 StartY=41.2 StartZ=0 EndX=61.15 EndY=44.4 EndZ=0
    g69: LineSegment StartX=61.15 StartY=44.4 StartZ=0 EndX=53.15 EndY=44.4 EndZ=0
    g70: GeomPoint [constr] X=57.15 Y=42.8 Z=0
    g71: LineSegment StartX=72.2 StartY=44.4 StartZ=0 EndX=72.2 EndY=41.2 EndZ=0
    g72: LineSegment StartX=72.2 StartY=41.2 StartZ=0 EndX=80.2 EndY=41.2 EndZ=0
    g73: LineSegment StartX=80.2 StartY=41.2 StartZ=0 EndX=80.2 EndY=44.4 EndZ=0
    g74: LineSegment StartX=80.2 StartY=44.4 StartZ=0 EndX=72.2 EndY=44.4 EndZ=0
    g75: GeomPoint [constr] X=76.2 Y=42.8 Z=0
    g76: LineSegment StartX=91.25 StartY=44.4 StartZ=0 EndX=91.25 EndY=41.2 EndZ=0
    g77: LineSegment StartX=91.25 StartY=41.2 StartZ=0 EndX=99.25 EndY=41.2 EndZ=0
    g78: LineSegment StartX=99.25 StartY=41.2 StartZ=0 EndX=99.25 EndY=44.4 EndZ=0
    g79: LineSegment StartX=99.25 StartY=44.4 StartZ=0 EndX=91.25 EndY=44.4 EndZ=0
    g80: GeomPoint [constr] X=95.25 Y=42.8 Z=0
    g81: LineSegment StartX=110.3 StartY=44.4 StartZ=0 EndX=110.3 EndY=41.2 EndZ=0
    g82: LineSegment StartX=110.3 StartY=41.2 StartZ=0 EndX=118.3 EndY=41.2 EndZ=0
    g83: LineSegment StartX=118.3 StartY=41.2 StartZ=0 EndX=118.3 EndY=44.4 EndZ=0
    g84: LineSegment StartX=118.3 StartY=44.4 StartZ=0 EndX=110.3 EndY=44.4 EndZ=0
    g85: GeomPoint [constr] X=114.3 Y=42.8 Z=0
    g86: LineSegment StartX=129.35 StartY=44.4 StartZ=0 EndX=129.35 EndY=41.2 EndZ=0
    g87: LineSegment StartX=129.35 StartY=41.2 StartZ=0 EndX=137.35 EndY=41.2 EndZ=0
    g88: LineSegment StartX=137.35 StartY=41.2 StartZ=0 EndX=137.35 EndY=44.4 EndZ=0
    g89: LineSegment StartX=137.35 StartY=44.4 StartZ=0 EndX=129.35 EndY=44.4 EndZ=0
    g90: GeomPoint [constr] X=133.35 Y=42.8 Z=0
    g91: LineSegment StartX=34.1 StartY=25.35 StartZ=0 EndX=34.1 EndY=22.15 EndZ=0
    g92: LineSegment StartX=34.1 StartY=22.15 StartZ=0 EndX=42.1 EndY=22.15 EndZ=0
    g93: LineSegment StartX=42.1 StartY=22.15 StartZ=0 EndX=42.1 EndY=25.35 EndZ=0
    g94: LineSegment StartX=42.1 StartY=25.35 StartZ=0 EndX=34.1 EndY=25.35 EndZ=0
    g95: GeomPoint [constr] X=38.1 Y=23.75 Z=0
    g96: LineSegment StartX=53.15 StartY=25.35 StartZ=0 EndX=53.15 EndY=22.15 EndZ=0
    g97: LineSegment StartX=53.15 StartY=22.15 StartZ=0 EndX=61.15 EndY=22.15 EndZ=0
    g98: LineSegment StartX=61.15 StartY=22.15 StartZ=0 EndX=61.15 EndY=25.35 EndZ=0
    g99: LineSegment StartX=61.15 StartY=25.35 StartZ=0 EndX=53.15 EndY=25.35 EndZ=0
    g100: GeomPoint [constr] X=57.15 Y=23.75 Z=0
    g101: LineSegment StartX=72.2 StartY=25.35 StartZ=0 EndX=72.2 EndY=22.15 EndZ=0
    g102: LineSegment StartX=72.2 StartY=22.15 StartZ=0 EndX=80.2 EndY=22.15 EndZ=0
    g103: LineSegment StartX=80.2 StartY=22.15 StartZ=0 EndX=80.2 EndY=25.35 EndZ=0
    g104: LineSegment StartX=80.2 StartY=25.35 StartZ=0 EndX=72.2 EndY=25.35 EndZ=0
    g105: GeomPoint [constr] X=76.2 Y=23.75 Z=0
    g106: LineSegment StartX=91.25 StartY=25.35 StartZ=0 EndX=91.25 EndY=22.15 EndZ=0
    g107: LineSegment StartX=91.25 StartY=22.15 StartZ=0 EndX=99.25 EndY=22.15 EndZ=0
    g108: LineSegment StartX=99.25 StartY=22.15 StartZ=0 EndX=99.25 EndY=25.35 EndZ=0
    g109: LineSegment StartX=99.25 StartY=25.35 StartZ=0 EndX=91.25 EndY=25.35 EndZ=0
    g110: GeomPoint [constr] X=95.25 Y=23.75 Z=0
    g111: LineSegment StartX=110.3 StartY=25.35 StartZ=0 EndX=110.3 EndY=22.15 EndZ=0
    g112: LineSegment StartX=110.3 StartY=22.15 StartZ=0 EndX=118.3 EndY=22.15 EndZ=0
    g113: LineSegment StartX=118.3 StartY=22.15 StartZ=0 EndX=118.3 EndY=25.35 EndZ=0
    g114: LineSegment StartX=118.3 StartY=25.35 StartZ=0 EndX=110.3 EndY=25.35 EndZ=0
    g115: GeomPoint [constr] X=114.3 Y=23.75 Z=0
    g116: LineSegment StartX=129.35 StartY=25.35 StartZ=0 EndX=129.35 EndY=22.15 EndZ=0
    g117: LineSegment StartX=129.35 StartY=22.15 StartZ=0 EndX=137.35 EndY=22.15 EndZ=0
    g118: LineSegment StartX=137.35 StartY=22.15 StartZ=0 EndX=137.35 EndY=25.35 EndZ=0
    g119: LineSegment StartX=137.35 StartY=25.35 StartZ=0 EndX=129.35 EndY=25.35 EndZ=0
    g120: GeomPoint [constr] X=133.35 Y=23.75 Z=0
    g121: LineSegment StartX=15.05 StartY=25.35 StartZ=0 EndX=15.05 EndY=22.15 EndZ=0
    g122: LineSegment StartX=15.05 StartY=22.15 StartZ=0 EndX=23.05 EndY=22.15 EndZ=0
    g123: LineSegment StartX=23.05 StartY=22.15 StartZ=0 EndX=23.05 EndY=25.35 EndZ=0
    g124: LineSegment StartX=23.05 StartY=25.35 StartZ=0 EndX=15.05 EndY=25.35 EndZ=0
    g125: GeomPoint [constr] X=19.05 Y=23.75 Z=0
  constraints (327):
    c: DistanceX(g-1,g0) = 19.05
    c: DistanceY(g-1,g0) = 19.05
    c: Coincident(g1,g2)
    c: Coincident(g2,g3)
    c: Coincident(g3,g4)
    c: Coincident(g4,g1)
    c: Vertical(g1)
    c: Vertical(g3)
    c: Horizontal(g2)
    c: Horizontal(g4)
    c: Symmetric(g3,g1,g5)
    c: Coincident(g6,g7)
    c: Coincident(g7,g8)
    c: Coincident(g8,g9)
    c: Coincident(g9,g6)
    c: Vertical(g6)
    c: Vertical(g8)
    c: Horizontal(g7)
    c: Horizontal(g9)
    c: Symmetric(g8,g6,g10)
    c: Coincident(g11,g12)
    c: Coincident(g12,g13)
    c: Coincident(g13,g14)
    c: Coincident(g14,g11)
    c: Vertical(g11)
    c: Vertical(g13)
    c: Horizontal(g12)
    c: Horizontal(g14)
    c: Symmetric(g13,g11,g15)
    c: Coincident(g16,g17)
    c: Coincident(g17,g18)
    c: Coincident(g18,g19)
    c: Coincident(g19,g16)
    c: Vertical(g16)
    c: Vertical(g18)
    c: Horizontal(g17)
    c: Horizontal(g19)
    c: Symmetric(g18,g16,g20)
    c: Coincident(g21,g22)
    c: Coincident(g22,g23)
    c: Coincident(g23,g24)
    c: Coincident(g24,g21)
    c: Vertical(g21)
    c: Vertical(g23)
    c: Horizontal(g22)
    c: Horizontal(g24)
    c: Symmetric(g23,g21,g25)
    c: Coincident(g26,g27)
    c: Coincident(g27,g28)
    c: Coincident(g28,g29)
    c: Coincident(g29,g26)
    c: Vertical(g26)
    c: Vertical(g28)
    c: Horizontal(g27)
    c: Horizontal(g29)
    c: Symmetric(g28,g26,g30)
    c: Coincident(g31,g32)
    c: Coincident(g32,g33)
    c: Coincident(g33,g34)
    c: Coincident(g34,g31)
    c: Vertical(g31)
    c: Vertical(g33)
    c: Horizontal(g32)
    c: Horizontal(g34)
    c: Symmetric(g33,g31,g35)
    c: Coincident(g36,g37)
    c: Coincident(g37,g38)
    c: Coincident(g38,g39)
    c: Coincident(g39,g36)
    c: Vertical(g36)
    c: Vertical(g38)
    c: Horizontal(g37)
    c: Horizontal(g39)
    c: Symmetric(g38,g36,g40)
    c: Coincident(g41,g42)
    c: Coincident(g42,g43)
    c: Coincident(g43,g44)
    c: Coincident(g44,g41)
    c: Vertical(g41)
    c: Vertical(g43)
    c: Horizontal(g42)
    c: Horizontal(g44)
    c: Symmetric(g43,g41,g45)
    c: Coincident(g46,g47)
    c: Coincident(g47,g48)
    c: Coincident(g48,g49)
    c: Coincident(g49,g46)
    c: Vertical(g46)
    c: Vertical(g48)
    c: Horizontal(g47)
    c: Horizontal(g49)
    c: Symmetric(g48,g46,g50)
    c: Coincident(g51,g52)
    c: Coincident(g52,g53)
    c: Coincident(g53,g54)
    c: Coincident(g54,g51)
    c: Vertical(g51)
    c: Vertical(g53)
    c: Horizontal(g52)
    c: Horizontal(g54)
    c: Symmetric(g53,g51,g55)
    c: Coincident(g56,g57)
    c: Coincident(g57,g58)
    c: Coincident(g58,g59)
    c: Coincident(g59,g56)
    c: Vertical(g56)
    c: Vertical(g58)
    c: Horizontal(g57)
    c: Horizontal(g59)
    c: Symmetric(g58,g56,g60)
    c: Coincident(g61,g62)
    c: Coincident(g62,g63)
    c: Coincident(g63,g64)
    c: Coincident(g64,g61)
    c: Vertical(g61)
    c: Vertical(g63)
    c: Horizontal(g62)
    c: Horizontal(g64)
    c: Symmetric(g63,g61,g65)
    c: Coincident(g66,g67)
    c: Coincident(g67,g68)
    c: Coincident(g68,g69)
    c: Coincident(g69,g66)
    c: Vertical(g66)
    c: Vertical(g68)
    c: Horizontal(g67)
    c: Horizontal(g69)
    c: Symmetric(g68,g66,g70)
    c: Coincident(g71,g72)
    c: Coincident(g72,g73)
    c: Coincident(g73,g74)
    c: Coincident(g74,g71)
    c: Vertical(g71)
    c: Vertical(g73)
    c: Horizontal(g72)
    c: Horizontal(g74)
    c: Symmetric(g73,g71,g75)
    c: Coincident(g76,g77)
    c: Coincident(g77,g78)
    c: Coincident(g78,g79)
    c: Coincident(g79,g76)
    c: Vertical(g76)
    c: Vertical(g78)
    c: Horizontal(g77)
    c: Horizontal(g79)
    c: Symmetric(g78,g76,g80)
    c: Coincident(g81,g82)
    c: Coincident(g82,g83)
    c: Coincident(g83,g84)
    c: Coincident(g84,g81)
    c: Vertical(g81)
    c: Vertical(g83)
    c: Horizontal(g82)
    c: Horizontal(g84)
    c: Symmetric(g83,g81,g85)
    c: Coincident(g86,g87)
    c: Coincident(g87,g88)
    c: Coincident(g88,g89)
    c: Coincident(g89,g86)
    c: Vertical(g86)
    c: Vertical(g88)
    c: Horizontal(g87)
    c: Horizontal(g89)
    c: Symmetric(g88,g86,g90)
    c: Coincident(g91,g92)
    c: Coincident(g92,g93)
    c: Coincident(g93,g94)
    c: Coincident(g94,g91)
    c: Vertical(g91)
    c: Vertical(g93)
    c: Horizontal(g92)
    c: Horizontal(g94)
    c: Symmetric(g93,g91,g95)
    c: Coincident(g96,g97)
    c: Coincident(g97,g98)
    c: Coincident(g98,g99)
    c: Coincident(g99,g96)
    c: Vertical(g96)
    c: Vertical(g98)
    c: Horizontal(g97)
    c: Horizontal(g99)
    c: Symmetric(g98,g96,g100)
    c: Coincident(g101,g102)
    c: Coincident(g102,g103)
    c: Coincident(g103,g104)
    c: Coincident(g104,g101)
    c: Vertical(g101)
    c: Vertical(g103)
    c: Horizontal(g102)
    c: Horizontal(g104)
    c: Symmetric(g103,g101,g105)
    c: Coincident(g106,g107)
    c: Coincident(g107,g108)
    c: Coincident(g108,g109)
    c: Coincident(g109,g106)
    c: Vertical(g106)
    c: Vertical(g108)
    c: Horizontal(g107)
    c: Horizontal(g109)
    c: Symmetric(g108,g106,g110)
    c: Coincident(g111,g112)
    c: Coincident(g112,g113)
    c: Coincident(g113,g114)
    c: Coincident(g114,g111)
    c: Vertical(g111)
    c: Vertical(g113)
    c: Horizontal(g112)
    c: Horizontal(g114)
    c: Symmetric(g113,g111,g115)
    c: Coincident(g116,g117)
    c: Coincident(g117,g118)
    c: Coincident(g118,g119)
    c: Coincident(g119,g116)
    c: Vertical(g116)
    c: Vertical(g118)
    c: Horizontal(g117)
    c: Horizontal(g119)
    c: Symmetric(g118,g116,g120)
    c: Horizontal(g5,g10)
    c: Horizontal(g10,g15)
    c: Horizontal(g15,g20)
    c: Horizontal(g20,g25)
    c: Horizontal(g25,g30)
    c: Horizontal(g35,g40)
    c: Horizontal(g40,g45)
    c: Horizontal(g45,g50)
    c: Horizontal(g50,g55)
    c: Horizontal(g55,g60)
    c: Horizontal(g65,g70)
    c: Horizontal(g70,g75)
    c: Horizontal(g75,g80)
    c: Horizontal(g80,g85)
    c: Horizontal(g85,g90)
    c: Horizontal(g95,g100)
    c: Horizontal(g100,g105)
    c: Horizontal(g105,g110)
    c: Horizontal(g110,g115)
    c: Horizontal(g115,g120)
    c: Vertical(g5,g35)
    c: Vertical(g35,g65)
    c: Vertical(g65,g95)
    c: Vertical(g10,g40)
    c: Vertical(g40,g70)
    c: Vertical(g70,g100)
    c: Vertical(g15,g45)
    c: Vertical(g45,g75)
    c: Vertical(g75,g105)
    c: Vertical(g20,g50)
    c: Vertical(g50,g80)
    c: Vertical(g80,g110)
    c: Vertical(g25,g55)
    c: Vertical(g55,g85)
    c: Vertical(g85,g115)
    c: Vertical(g30,g60)
    c: Vertical(g60,g90)
    c: Vertical(g90,g120)
    c: Equal(g1,g6)
    c: Equal(g6,g11)
    c: Equal(g11,g16)
    c: Equal(g16,g21)
    c: Equal(g21,g26)
    c: Equal(g31,g36)
    c: Equal(g36,g41)
    c: Equal(g41,g46)
    c: Equal(g46,g51)
    c: Equal(g51,g56)
    c: Equal(g61,g66)
    c: Equal(g66,g71)
    c: Equal(g71,g76)
    c: Equal(g76,g81)
    c: Equal(g81,g86)
    c: Equal(g91,g96)
    c: Equal(g96,g101)
    c: Equal(g101,g106)
    c: Equal(g106,g111)
    c: Equal(g111,g116)
    c: Equal(g1,g31)
    c: Equal(g31,g61)
    c: Equal(g61,g91)
    c: Equal(g2,g7)
    c: Equal(g7,g12)
    c: Equal(g12,g17)
    c: Equal(g17,g22)
    c: Equal(g22,g27)
    c: Equal(g32,g37)
    c: Equal(g37,g42)
    c: Equal(g42,g47)
    c: Equal(g47,g52)
    c: Equal(g52,g57)
    c: Equal(g62,g67)
    c: Equal(g67,g72)
    c: Equal(g72,g77)
    c: Equal(g77,g82)
    c: Equal(g82,g87)
    c: Equal(g92,g97)
    c: Equal(g97,g102)
    c: Equal(g102,g107)
    c: Equal(g107,g112)
    c: Equal(g112,g117)
    c: Equal(g2,g32)
    c: Equal(g32,g62)
    c: Equal(g62,g92)
    c: Coincident(g121,g122)
    c: Coincident(g122,g123)
    c: Coincident(g123,g124)
    c: Coincident(g124,g121)
    c: Vertical(g121)
    c: Vertical(g123)
    c: Horizontal(g122)
    c: Horizontal(g124)
    c: Symmetric(g123,g121,g125)
    c: DistanceX(g122,g122) = 8
    c: DistanceY(g121,g121) = 3.2
    c: Vertical(g125,g0)
    c: DistanceY(g0,g125) = 4.7
    c: Horizontal(g95,g125)
    c: Equal(g121,g91)
    c: Equal(g122,g92)
    c: DistanceX(g125,g95) = 19.05
    c: DistanceX(g95,g100) = 19.05
    c: DistanceX(g100,g105) = 19.05
    c: DistanceX(g105,g110) = 19.05
    c: DistanceX(g110,g115) = 19.05
    c: DistanceX(g115,g120) = 19.05
    c: DistanceY(g35,g5) = 19.05
    c: DistanceY(g65,g35) = 19.05
    c: DistanceY(g125,g65) = 19.05
FEATURE [Sketcher::SketchObject] Sketch028  label="BR-UnderLED"
  ArcFitTolerance = 1e-06
  AttachmentSupport = -> [XY_Plane003]
  FullyConstrained = true
  MakeInternals = false
  MapMode = 5
  expr: Constraints[169] = 2.5 * 19.05
  expr: Constraints[170] = VarSet.Bottom_UnderLedY
  expr: Constraints[171] = VarSet.Bottom_UnderLedX
  expr: Constraints[172] = VarSet.Bottom_UnderLedR
  sketch-geometry (79):
    g0: LineSegment StartX=44.825 StartY=63.2 StartZ=0 EndX=44.825 EndY=58.1 EndZ=0
    g1: LineSegment StartX=46.025 StartY=56.9 StartZ=0 EndX=49.225 EndY=56.9 EndZ=0
    g2: LineSegment StartX=50.425 StartY=58.1 StartZ=0 EndX=50.425 EndY=63.2 EndZ=0
    g3: LineSegment StartX=49.225 StartY=64.4 StartZ=0 EndX=46.025 EndY=64.4 EndZ=0
    g4: GeomPoint [constr] X=47.625 Y=60.65 Z=0
    g5: ArcOfCircle CenterX=46.025 CenterY=63.2 CenterZ=0 NormalX=0 NormalY=0 NormalZ=1 AngleXU=0 Radius=1.2 StartAngle=1.5708 EndAngle=3.14159
    g6: GeomPoint [constr] X=44.825 Y=64.4 Z=0
    g7: ArcOfCircle CenterX=49.225 CenterY=63.2 CenterZ=0 NormalX=0 NormalY=0 NormalZ=1 AngleXU=0 Radius=1.2 StartAngle=8e-16 EndAngle=1.5708
    g8: GeomPoint [constr] X=50.425 Y=64.4 Z=0
    g9: ArcOfCircle CenterX=49.225 CenterY=58.1 CenterZ=0 NormalX=0 NormalY=0 NormalZ=1 AngleXU=0 Radius=1.2 StartAngle=4.71239 EndAngle=6.28319
    g10: GeomPoint [constr] X=50.425 Y=56.9 Z=0
    g11: ArcOfCircle CenterX=46.025 CenterY=58.1 CenterZ=0 NormalX=0 NormalY=0 NormalZ=1 AngleXU=0 Radius=1.2 StartAngle=3.14159 EndAngle=4.71239
    g12: GeomPoint [constr] X=44.825 Y=56.9 Z=0
    g13: LineSegment StartX=82.925 StartY=63.2 StartZ=0 EndX=82.925 EndY=58.1 EndZ=0
    g14: LineSegment StartX=84.125 StartY=56.9 StartZ=0 EndX=87.325 EndY=56.9 EndZ=0
    g15: LineSegment StartX=88.525 StartY=58.1 StartZ=0 EndX=88.525 EndY=63.2 EndZ=0
    g16: LineSegment StartX=87.325 StartY=64.4 StartZ=0 EndX=84.125 EndY=64.4 EndZ=0
    g17: GeomPoint [constr] X=85.725 Y=60.65 Z=0
    g18: ArcOfCircle CenterX=84.125 CenterY=63.2 CenterZ=0 NormalX=0 NormalY=0 NormalZ=1 AngleXU=0 Radius=1.2 StartAngle=1.5708 EndAngle=3.14159
    g19: GeomPoint [constr] X=82.925 Y=64.4 Z=0
    g20: ArcOfCircle CenterX=87.325 CenterY=63.2 CenterZ=0 NormalX=0 NormalY=0 NormalZ=1 AngleXU=0 Radius=1.2 StartAngle=-2.7e-15 EndAngle=1.5708
    g21: GeomPoint [constr] X=88.525 Y=64.4 Z=0
    g22: ArcOfCircle CenterX=87.325 CenterY=58.1 CenterZ=0 NormalX=0 NormalY=0 NormalZ=1 AngleXU=0 Radius=1.2 StartAngle=4.71239 EndAngle=6.28319
    g23: GeomPoint [constr] X=88.525 Y=56.9 Z=0
    g24: ArcOfCircle CenterX=84.125 CenterY=58.1 CenterZ=0 NormalX=0 NormalY=0 NormalZ=1 AngleXU=0 Radius=1.2 StartAngle=3.14159 EndAngle=4.71239
    g25: GeomPoint [constr] X=82.925 Y=56.9 Z=0
    g26: LineSegment StartX=121.025 StartY=63.2 StartZ=0 EndX=121.025 EndY=58.1 EndZ=0
    g27: LineSegment StartX=122.225 StartY=56.9 StartZ=0 EndX=125.425 EndY=56.9 EndZ=0
    g28: LineSegment StartX=126.625 StartY=58.1 StartZ=0 EndX=126.625 EndY=63.2 EndZ=0
    g29: LineSegment StartX=125.425 StartY=64.4 StartZ=0 EndX=122.225 EndY=64.4 EndZ=0
    g30: GeomPoint [constr] X=123.825 Y=60.65 Z=0
    g31: ArcOfCircle CenterX=122.225 CenterY=63.2 CenterZ=0 NormalX=0 NormalY=0 NormalZ=1 AngleXU=0 Radius=1.2 StartAngle=1.5708 EndAngle=3.14159
    g32: GeomPoint [constr] X=121.025 Y=64.4 Z=0
    g33: ArcOfCircle CenterX=125.425 CenterY=63.2 CenterZ=0 NormalX=0 NormalY=0 NormalZ=1 AngleXU=0 Radius=1.2 StartAngle=6e-16 EndAngle=1.5708
    g34: GeomPoint [constr] X=126.625 Y=64.4 Z=0
    g35: ArcOfCircle CenterX=125.425 CenterY=58.1 CenterZ=0 NormalX=0 NormalY=0 NormalZ=1 AngleXU=0 Radius=1.2 StartAngle=4.71239 EndAngle=6.28319
    g36: GeomPoint [constr] X=126.625 Y=56.9 Z=0
    g37: ArcOfCircle CenterX=122.225 CenterY=58.1 CenterZ=0 NormalX=0 NormalY=0 NormalZ=1 AngleXU=0 Radius=1.2 StartAngle=3.14159 EndAngle=4.71239
    g38: GeomPoint [constr] X=121.025 Y=56.9 Z=0
    g39: LineSegment StartX=44.825 StartY=25.1 StartZ=0 EndX=44.825 EndY=20 EndZ=0
    g40: LineSegment StartX=46.025 StartY=18.8 StartZ=0 EndX=49.225 EndY=18.8 EndZ=0
    g41: LineSegment StartX=50.425 StartY=20 StartZ=0 EndX=50.425 EndY=25.1 EndZ=0
    g42: LineSegment StartX=49.225 StartY=26.3 StartZ=0 EndX=46.025 EndY=26.3 EndZ=0
    g43: GeomPoint [constr] X=47.625 Y=22.55 Z=0
    g44: ArcOfCircle CenterX=46.025 CenterY=25.1 CenterZ=0 NormalX=0 NormalY=0 NormalZ=1 AngleXU=0 Radius=1.2 StartAngle=1.5708 EndAngle=3.14159
    g45: GeomPoint [constr] X=44.825 Y=26.3 Z=0
    g46: ArcOfCircle CenterX=49.225 CenterY=25.1 CenterZ=0 NormalX=0 NormalY=0 NormalZ=1 AngleXU=0 Radius=1.2 StartAngle=1.2e-15 EndAngle=1.5708
    g47: GeomPoint [constr] X=50.425 Y=26.3 Z=0
    g48: ArcOfCircle CenterX=49.225 CenterY=20 CenterZ=0 NormalX=0 NormalY=0 NormalZ=1 AngleXU=0 Radius=1.2 StartAngle=4.71239 EndAngle=6.28319
    g49: GeomPoint [constr] X=50.425 Y=18.8 Z=0
    g50: ArcOfCircle CenterX=46.025 CenterY=20 CenterZ=0 NormalX=0 NormalY=0 NormalZ=1 AngleXU=0 Radius=1.2 StartAngle=3.14159 EndAngle=4.71239
    g51: GeomPoint [constr] X=44.825 Y=18.8 Z=0
    g52: LineSegment StartX=82.925 StartY=25.1 StartZ=0 EndX=82.925 EndY=20 EndZ=0
    g53: LineSegment StartX=84.125 StartY=18.8 StartZ=0 EndX=87.325 EndY=18.8 EndZ=0
    g54: LineSegment StartX=88.525 StartY=20 StartZ=0 EndX=88.525 EndY=25.1 EndZ=0
    g55: LineSegment StartX=87.325 StartY=26.3 StartZ=0 EndX=84.125 EndY=26.3 EndZ=0
    g56: GeomPoint [constr] X=85.725 Y=22.55 Z=0
    g57: ArcOfCircle CenterX=84.125 CenterY=25.1 CenterZ=0 NormalX=0 NormalY=0 NormalZ=1 AngleXU=0 Radius=1.2 StartAngle=1.5708 EndAngle=3.14159
    g58: GeomPoint [constr] X=82.925 Y=26.3 Z=0
    g59: ArcOfCircle CenterX=87.325 CenterY=25.1 CenterZ=0 NormalX=0 NormalY=0 NormalZ=1 AngleXU=0 Radius=1.2 StartAngle=0 EndAngle=1.5708
    g60: GeomPoint [constr] X=88.525 Y=26.3 Z=0
    g61: ArcOfCircle CenterX=87.325 CenterY=20 CenterZ=0 NormalX=0 NormalY=0 NormalZ=1 AngleXU=0 Radius=1.2 StartAngle=4.71239 EndAngle=6.28319
    g62: GeomPoint [constr] X=88.525 Y=18.8 Z=0
    g63: ArcOfCircle CenterX=84.125 CenterY=20 CenterZ=0 NormalX=0 NormalY=0 NormalZ=1 AngleXU=0 Radius=1.2 StartAngle=3.14159 EndAngle=4.71239
    g64: GeomPoint [constr] X=82.925 Y=18.8 Z=0
    g65: LineSegment StartX=121.025 StartY=25.1 StartZ=0 EndX=121.025 EndY=20 EndZ=0
    g66: LineSegment StartX=122.225 StartY=18.8 StartZ=0 EndX=125.425 EndY=18.8 EndZ=0
    g67: LineSegment StartX=126.625 StartY=20 StartZ=0 EndX=126.625 EndY=25.1 EndZ=0
    g68: LineSegment StartX=125.425 StartY=26.3 StartZ=0 EndX=122.225 EndY=26.3 EndZ=0
    g69: GeomPoint [constr] X=123.825 Y=22.55 Z=0
    g70: ArcOfCircle CenterX=122.225 CenterY=25.1 CenterZ=0 NormalX=0 NormalY=0 NormalZ=1 AngleXU=0 Radius=1.2 StartAngle=1.5708 EndAngle=3.14159
    g71: GeomPoint [constr] X=121.025 Y=26.3 Z=0
    g72: ArcOfCircle CenterX=125.425 CenterY=25.1 CenterZ=0 NormalX=0 NormalY=0 NormalZ=1 AngleXU=0 Radius=1.2 StartAngle=-9e-16 EndAngle=1.5708
    g73: GeomPoint [constr] X=126.625 Y=26.3 Z=0
    g74: ArcOfCircle CenterX=125.425 CenterY=20 CenterZ=0 NormalX=0 NormalY=0 NormalZ=1 AngleXU=0 Radius=1.2 StartAngle=4.71239 EndAngle=6.28319
    g75: GeomPoint [constr] X=126.625 Y=18.8 Z=0
    g76: ArcOfCircle CenterX=122.225 CenterY=20 CenterZ=0 NormalX=0 NormalY=0 NormalZ=1 AngleXU=0 Radius=1.2 StartAngle=3.14159 EndAngle=4.71239
    g77: GeomPoint [constr] X=121.025 Y=18.8 Z=0
    g78: GeomPoint X=19.05 Y=19.05 Z=0
  constraints (176):
    c: Vertical(g0)
    c: Vertical(g2)
    c: Horizontal(g1)
    c: Horizontal(g3)
    c: Symmetric(g10,g6,g4)
    c: PointOnObject(g6,g0)
    c: PointOnObject(g6,g3)
    c: Tangent(g0,g5) = -1.5708
    c: Tangent(g3,g5) = -1.5708
    c: PointOnObject(g8,g2)
    c: PointOnObject(g8,g3)
    c: Tangent(g2,g7) = -1.5708
    c: Tangent(g3,g7) = -1.5708
    c: PointOnObject(g10,g1)
    c: PointOnObject(g10,g2)
    c: Tangent(g1,g9) = -1.5708
    c: Tangent(g2,g9) = -1.5708
    c: PointOnObject(g12,g0)
    c: PointOnObject(g12,g1)
    c: Tangent(g0,g11) = -1.5708
    c: Tangent(g1,g11) = -1.5708
    c: Equal(g5,g7)
    c: Equal(g7,g9)
    c: Equal(g9,g11)
    c: Vertical(g13)
    c: Vertical(g15)
    c: Horizontal(g14)
    c: Horizontal(g16)
    c: Symmetric(g23,g19,g17)
    c: PointOnObject(g19,g13)
    c: PointOnObject(g19,g16)
    c: Tangent(g13,g18) = -1.5708
    c: Tangent(g16,g18) = -1.5708
    c: PointOnObject(g21,g15)
    c: PointOnObject(g21,g16)
    c: Tangent(g15,g20) = -1.5708
    c: Tangent(g16,g20) = -1.5708
    c: PointOnObject(g23,g14)
    c: PointOnObject(g23,g15)
    c: Tangent(g14,g22) = -1.5708
    c: Tangent(g15,g22) = -1.5708
    c: PointOnObject(g25,g13)
    c: PointOnObject(g25,g14)
    c: Tangent(g13,g24) = -1.5708
    c: Tangent(g14,g24) = -1.5708
    c: Equal(g18,g20)
    c: Equal(g20,g22)
    c: Equal(g22,g24)
    c: Vertical(g26)
    c: Vertical(g28)
    c: Horizontal(g27)
    c: Horizontal(g29)
    c: Symmetric(g36,g32,g30)
    c: PointOnObject(g32,g26)
    c: PointOnObject(g32,g29)
    c: Tangent(g26,g31) = -1.5708
    c: Tangent(g29,g31) = -1.5708
    c: PointOnObject(g34,g28)
    c: PointOnObject(g34,g29)
    c: Tangent(g28,g33) = -1.5708
    c: Tangent(g29,g33) = -1.5708
    c: PointOnObject(g36,g27)
    c: PointOnObject(g36,g28)
    c: Tangent(g27,g35) = -1.5708
    c: Tangent(g28,g35) = -1.5708
    c: PointOnObject(g38,g26)
    c: PointOnObject(g38,g27)
    c: Tangent(g26,g37) = -1.5708
    c: Tangent(g27,g37) = -1.5708
    c: Equal(g31,g33)
    c: Equal(g33,g35)
    c: Equal(g35,g37)
    c: Vertical(g39)
    c: Vertical(g41)
    c: Horizontal(g40)
    c: Horizontal(g42)
    c: Symmetric(g49,g45,g43)
    c: PointOnObject(g45,g39)
    c: PointOnObject(g45,g42)
    c: Tangent(g39,g44) = -1.5708
    c: Tangent(g42,g44) = -1.5708
    c: PointOnObject(g47,g41)
    c: PointOnObject(g47,g42)
    c: Tangent(g41,g46) = -1.5708
    c: Tangent(g42,g46) = -1.5708
    c: PointOnObject(g49,g40)
    c: PointOnObject(g49,g41)
    c: Tangent(g40,g48) = -1.5708
    c: Tangent(g41,g48) = -1.5708
    c: PointOnObject(g51,g39)
    c: PointOnObject(g51,g40)
    c: Tangent(g39,g50) = -1.5708
    c: Tangent(g40,g50) = -1.5708
    c: Equal(g44,g46)
    c: Equal(g46,g48)
    c: Equal(g48,g50)
    c: Vertical(g52)
    c: Vertical(g54)
    c: Horizontal(g53)
    c: Horizontal(g55)
    c: Symmetric(g62,g58,g56)
    c: PointOnObject(g58,g52)
    c: PointOnObject(g58,g55)
    c: Tangent(g52,g57) = -1.5708
    c: Tangent(g55,g57) = -1.5708
    c: PointOnObject(g60,g54)
    c: PointOnObject(g60,g55)
    c: Tangent(g54,g59) = -1.5708
    c: Tangent(g55,g59) = -1.5708
    c: PointOnObject(g62,g53)
    c: PointOnObject(g62,g54)
    c: Tangent(g53,g61) = -1.5708
    c: Tangent(g54,g61) = -1.5708
    c: PointOnObject(g64,g52)
    c: PointOnObject(g64,g53)
    c: Tangent(g52,g63) = -1.5708
    c: Tangent(g53,g63) = -1.5708
    c: Equal(g57,g59)
    c: Equal(g59,g61)
    c: Equal(g61,g63)
    c: Vertical(g65)
    c: Vertical(g67)
    c: Horizontal(g66)
    c: Horizontal(g68)
    c: Symmetric(g75,g71,g69)
    c: PointOnObject(g71,g65)
    c: PointOnObject(g71,g68)
    c: Tangent(g65,g70) = -1.5708
    c: Tangent(g68,g70) = -1.5708
    c: PointOnObject(g73,g67)
    c: PointOnObject(g73,g68)
    c: Tangent(g67,g72) = -1.5708
    c: Tangent(g68,g72) = -1.5708
    c: PointOnObject(g75,g66)
    c: PointOnObject(g75,g67)
    c: Tangent(g66,g74) = -1.5708
    c: Tangent(g67,g74) = -1.5708
    c: PointOnObject(g77,g65)
    c: PointOnObject(g77,g66)
    c: Tangent(g65,g76) = -1.5708
    c: Tangent(g66,g76) = -1.5708
    c: Equal(g70,g72)
    c: Equal(g72,g74)
    c: Equal(g74,g76)
    c: Horizontal(g4,g17)
    c: Horizontal(g17,g30)
    c: Horizontal(g43,g56)
    c: Horizontal(g56,g69)
    c: Vertical(g4,g43)
    c: Vertical(g17,g56)
    c: Vertical(g30,g69)
    c: Equal(g0,g13)
    c: Equal(g13,g26)
    c: Equal(g39,g52)
    c: Equal(g52,g65)
    c: Equal(g26,g65)
    c: Equal(g1,g14)
    c: Equal(g14,g27)
    c: Equal(g40,g53)
    c: Equal(g53,g66)
    c: Equal(g27,g66)
    c: Equal(g5,g18)
    c: Equal(g18,g31)
    c: Equal(g44,g57)
    c: Equal(g57,g70)
    c: Equal(g31,g70)
    c: DistanceX(g43,g56) = 38.1
    c: DistanceX(g56,g69) = 38.1
    c: DistanceY(g56,g17) = 38.1
    c: DistanceX(g-1,g43) = 47.625
    c: DistanceY(g40,g42) = 7.5
    c: DistanceX(g39,g41) = 5.6
    c: Radius(g50) = 1.2
    c: DistanceX(g-1,g78) = 19.05
    c: DistanceY(g-1,g78) = 19.05
    c: DistanceY(g78,g43) = 3.5
FEATURE [Sketcher::SketchObject] Sketch031  label="BR-Diode"
  ArcFitTolerance = 1e-06
  AttachmentSupport = -> [XY_Plane003]
  FullyConstrained = true
  MakeInternals = false
  MapMode = 5
  expr: Constraints[257] = VarSet.Bottom_DiodeX
  expr: Constraints[258] = VarSet.Bottom_DiodeY
  sketch-geometry (126):
    g0: LineSegment StartX=47.675 StartY=84.9 StartZ=0 EndX=47.675 EndY=82.9 EndZ=0
    g1: LineSegment StartX=47.675 StartY=82.9 StartZ=0 EndX=53.375 EndY=82.9 EndZ=0
    g2: LineSegment StartX=53.375 StartY=82.9 StartZ=0 EndX=53.375 EndY=84.9 EndZ=0
    g3: LineSegment StartX=53.375 StartY=84.9 StartZ=0 EndX=47.675 EndY=84.9 EndZ=0
    g4: GeomPoint [constr] X=50.525 Y=83.9 Z=0
    g5: LineSegment StartX=60.425 StartY=84.9 StartZ=0 EndX=60.425 EndY=82.9 EndZ=0
    g6: LineSegment StartX=60.425 StartY=82.9 StartZ=0 EndX=66.125 EndY=82.9 EndZ=0
    g7: LineSegment StartX=66.125 StartY=82.9 StartZ=0 EndX=66.125 EndY=84.9 EndZ=0
    g8: LineSegment StartX=66.125 StartY=84.9 StartZ=0 EndX=60.425 EndY=84.9 EndZ=0
    g9: GeomPoint [constr] X=63.275 Y=83.9 Z=0
    g10: LineSegment StartX=73.1 StartY=84.9 StartZ=0 EndX=73.1 EndY=82.9 EndZ=0
    g11: LineSegment StartX=73.1 StartY=82.9 StartZ=0 EndX=78.8 EndY=82.9 EndZ=0
    g12: LineSegment StartX=78.8 StartY=82.9 StartZ=0 EndX=78.8 EndY=84.9 EndZ=0
    g13: LineSegment StartX=78.8 StartY=84.9 StartZ=0 EndX=73.1 EndY=84.9 EndZ=0
    g14: GeomPoint [constr] X=75.95 Y=83.9 Z=0
    g15: LineSegment StartX=92.15 StartY=84.9 StartZ=0 EndX=92.15 EndY=82.9 EndZ=0
    g16: LineSegment StartX=92.15 StartY=82.9 StartZ=0 EndX=97.85 EndY=82.9 EndZ=0
    g17: LineSegment StartX=97.85 StartY=82.9 StartZ=0 EndX=97.85 EndY=84.9 EndZ=0
    g18: LineSegment StartX=97.85 StartY=84.9 StartZ=0 EndX=92.15 EndY=84.9 EndZ=0
    g19: GeomPoint [constr] X=95 Y=83.9 Z=0
    g20: LineSegment StartX=104.825 StartY=84.9 StartZ=0 EndX=104.825 EndY=82.9 EndZ=0
    g21: LineSegment StartX=104.825 StartY=82.9 StartZ=0 EndX=110.525 EndY=82.9 EndZ=0
    g22: LineSegment StartX=110.525 StartY=82.9 StartZ=0 EndX=110.525 EndY=84.9 EndZ=0
    g23: LineSegment StartX=110.525 StartY=84.9 StartZ=0 EndX=104.825 EndY=84.9 EndZ=0
    g24: GeomPoint [constr] X=107.675 Y=83.9 Z=0
    g25: LineSegment StartX=117.575 StartY=84.9 StartZ=0 EndX=117.575 EndY=82.9 EndZ=0
    g26: LineSegment StartX=117.575 StartY=82.9 StartZ=0 EndX=123.275 EndY=82.9 EndZ=0
    g27: LineSegment StartX=123.275 StartY=82.9 StartZ=0 EndX=123.275 EndY=84.9 EndZ=0
    g28: LineSegment StartX=123.275 StartY=84.9 StartZ=0 EndX=117.575 EndY=84.9 EndZ=0
    g29: GeomPoint [constr] X=120.425 Y=83.9 Z=0
    g30: LineSegment StartX=35 StartY=65.85 StartZ=0 EndX=35 EndY=63.85 EndZ=0
    g31: LineSegment StartX=35 StartY=63.85 StartZ=0 EndX=40.7 EndY=63.85 EndZ=0
    g32: LineSegment StartX=40.7 StartY=63.85 StartZ=0 EndX=40.7 EndY=65.85 EndZ=0
    g33: LineSegment StartX=40.7 StartY=65.85 StartZ=0 EndX=35 EndY=65.85 EndZ=0
    g34: GeomPoint [constr] X=37.85 Y=64.85 Z=0
    g35: LineSegment StartX=54.05 StartY=65.85 StartZ=0 EndX=54.05 EndY=63.85 EndZ=0
    g36: LineSegment StartX=54.05 StartY=63.85 StartZ=0 EndX=59.75 EndY=63.85 EndZ=0
    g37: LineSegment StartX=59.75 StartY=63.85 StartZ=0 EndX=59.75 EndY=65.85 EndZ=0
    g38: LineSegment StartX=59.75 StartY=65.85 StartZ=0 EndX=54.05 EndY=65.85 EndZ=0
    g39: GeomPoint [constr] X=56.9 Y=64.85 Z=0
    g40: LineSegment StartX=73.1 StartY=65.85 StartZ=0 EndX=73.1 EndY=63.85 EndZ=0
    g41: LineSegment StartX=73.1 StartY=63.85 StartZ=0 EndX=78.8 EndY=63.85 EndZ=0
    g42: LineSegment StartX=78.8 StartY=63.85 StartZ=0 EndX=78.8 EndY=65.85 EndZ=0
    g43: LineSegment StartX=78.8 StartY=65.85 StartZ=0 EndX=73.1 EndY=65.85 EndZ=0
    g44: GeomPoint [constr] X=75.95 Y=64.85 Z=0
    g45: LineSegment StartX=92.15 StartY=65.85 StartZ=0 EndX=92.15 EndY=63.85 EndZ=0
    g46: LineSegment StartX=92.15 StartY=63.85 StartZ=0 EndX=97.85 EndY=63.85 EndZ=0
    g47: LineSegment StartX=97.85 StartY=63.85 StartZ=0 EndX=97.85 EndY=65.85 EndZ=0
    g48: LineSegment StartX=97.85 StartY=65.85 StartZ=0 EndX=92.15 EndY=65.85 EndZ=0
    g49: GeomPoint [constr] X=95 Y=64.85 Z=0
    g50: LineSegment StartX=111.2 StartY=65.85 StartZ=0 EndX=111.2 EndY=63.85 EndZ=0
    g51: LineSegment StartX=111.2 StartY=63.85 StartZ=0 EndX=116.9 EndY=63.85 EndZ=0
    g52: LineSegment StartX=116.9 StartY=63.85 StartZ=0 EndX=116.9 EndY=65.85 EndZ=0
    g53: LineSegment StartX=116.9 StartY=65.85 StartZ=0 EndX=111.2 EndY=65.85 EndZ=0
    g54: GeomPoint [constr] X=114.05 Y=64.85 Z=0
    g55: LineSegment StartX=130.25 StartY=65.85 StartZ=0 EndX=130.25 EndY=63.85 EndZ=0
    g56: LineSegment StartX=130.25 StartY=63.85 StartZ=0 EndX=135.95 EndY=63.85 EndZ=0
    g57: LineSegment StartX=135.95 StartY=63.85 StartZ=0 EndX=135.95 EndY=65.85 EndZ=0
    g58: LineSegment StartX=135.95 StartY=65.85 StartZ=0 EndX=130.25 EndY=65.85 EndZ=0
    g59: GeomPoint [constr] X=133.1 Y=64.85 Z=0
    g60: LineSegment StartX=35 StartY=46.8 StartZ=0 EndX=35 EndY=44.8 EndZ=0
    g61: LineSegment StartX=35 StartY=44.8 StartZ=0 EndX=40.7 EndY=44.8 EndZ=0
    g62: LineSegment StartX=40.7 StartY=44.8 StartZ=0 EndX=40.7 EndY=46.8 EndZ=0
    g63: LineSegment StartX=40.7 StartY=46.8 StartZ=0 EndX=35 EndY=46.8 EndZ=0
    g64: GeomPoint [constr] X=37.85 Y=45.8 Z=0
    g65: LineSegment StartX=54.05 StartY=46.8 StartZ=0 EndX=54.05 EndY=44.8 EndZ=0
    g66: LineSegment StartX=54.05 StartY=44.8 StartZ=0 EndX=59.75 EndY=44.8 EndZ=0
    g67: LineSegment StartX=59.75 StartY=44.8 StartZ=0 EndX=59.75 EndY=46.8 EndZ=0
    g68: LineSegment StartX=59.75 StartY=46.8 StartZ=0 EndX=54.05 EndY=46.8 EndZ=0
    g69: GeomPoint [constr] X=56.9 Y=45.8 Z=0
    g70: LineSegment StartX=73.1 StartY=46.8 StartZ=0 EndX=73.1 EndY=44.8 EndZ=0
    g71: LineSegment StartX=73.1 StartY=44.8 StartZ=0 EndX=78.8 EndY=44.8 EndZ=0
    g72: LineSegment StartX=78.8 StartY=44.8 StartZ=0 EndX=78.8 EndY=46.8 EndZ=0
    g73: LineSegment StartX=78.8 StartY=46.8 StartZ=0 EndX=73.1 EndY=46.8 EndZ=0
    g74: GeomPoint [constr] X=75.95 Y=45.8 Z=0
    g75: LineSegment StartX=92.15 StartY=46.8 StartZ=0 EndX=92.15 EndY=44.8 EndZ=0
    g76: LineSegment StartX=92.15 StartY=44.8 StartZ=0 EndX=97.85 EndY=44.8 EndZ=0
    g77: LineSegment StartX=97.85 StartY=44.8 StartZ=0 EndX=97.85 EndY=46.8 EndZ=0
    g78: LineSegment StartX=97.85 StartY=46.8 StartZ=0 EndX=92.15 EndY=46.8 EndZ=0
    g79: GeomPoint [constr] X=95 Y=45.8 Z=0
    g80: LineSegment StartX=111.2 StartY=46.8 StartZ=0 EndX=111.2 EndY=44.8 EndZ=0
    g81: LineSegment StartX=111.2 StartY=44.8 StartZ=0 EndX=116.9 EndY=44.8 EndZ=0
    g82: LineSegment StartX=116.9 StartY=44.8 StartZ=0 EndX=116.9 EndY=46.8 EndZ=0
    g83: LineSegment StartX=116.9 StartY=46.8 StartZ=0 EndX=111.2 EndY=46.8 EndZ=0
    g84: GeomPoint [constr] X=114.05 Y=45.8 Z=0
    g85: LineSegment StartX=135.95 StartY=46.8 StartZ=0 EndX=135.95 EndY=44.8 EndZ=0
    g86: LineSegment StartX=135.95 StartY=44.8 StartZ=0 EndX=130.25 EndY=44.8 EndZ=0
    g87: LineSegment StartX=130.25 StartY=44.8 StartZ=0 EndX=130.25 EndY=46.8 EndZ=0
    g88: LineSegment StartX=130.25 StartY=46.8 StartZ=0 EndX=135.95 EndY=46.8 EndZ=0
    g89: GeomPoint [constr] X=133.1 Y=45.8 Z=0
    g90: LineSegment StartX=35 StartY=27.75 StartZ=0 EndX=35 EndY=25.75 EndZ=0
    g91: LineSegment StartX=35 StartY=25.75 StartZ=0 EndX=40.7 EndY=25.75 EndZ=0
    g92: LineSegment StartX=40.7 StartY=25.75 StartZ=0 EndX=40.7 EndY=27.75 EndZ=0
    g93: LineSegment StartX=40.7 StartY=27.75 StartZ=0 EndX=35 EndY=27.75 EndZ=0
    g94: GeomPoint [constr] X=37.85 Y=26.75 Z=0
    g95: LineSegment StartX=54.05 StartY=27.75 StartZ=0 EndX=54.05 EndY=25.75 EndZ=0
    g96: LineSegment StartX=54.05 StartY=25.75 StartZ=0 EndX=59.75 EndY=25.75 EndZ=0
    g97: LineSegment StartX=59.75 StartY=25.75 StartZ=0 EndX=59.75 EndY=27.75 EndZ=0
    g98: LineSegment StartX=59.75 StartY=27.75 StartZ=0 EndX=54.05 EndY=27.75 EndZ=0
    g99: GeomPoint [constr] X=56.9 Y=26.75 Z=0
    g100: LineSegment StartX=73.1 StartY=27.75 StartZ=0 EndX=73.1 EndY=25.75 EndZ=0
    g101: LineSegment StartX=73.1 StartY=25.75 StartZ=0 EndX=78.8 EndY=25.75 EndZ=0
    g102: LineSegment StartX=78.8 StartY=25.75 StartZ=0 EndX=78.8 EndY=27.75 EndZ=0
    g103: LineSegment StartX=78.8 StartY=27.75 StartZ=0 EndX=73.1 EndY=27.75 EndZ=0
    g104: GeomPoint [constr] X=75.95 Y=26.75 Z=0
    g105: LineSegment StartX=92.15 StartY=27.75 StartZ=0 EndX=92.15 EndY=25.75 EndZ=0
    g106: LineSegment StartX=92.15 StartY=25.75 StartZ=0 EndX=97.85 EndY=25.75 EndZ=0
    g107: LineSegment StartX=97.85 StartY=25.75 StartZ=0 EndX=97.85 EndY=27.75 EndZ=0
    g108: LineSegment StartX=97.85 StartY=27.75 StartZ=0 EndX=92.15 EndY=27.75 EndZ=0
    g109: GeomPoint [constr] X=95 Y=26.75 Z=0
    g110: LineSegment StartX=111.2 StartY=27.75 StartZ=0 EndX=111.2 EndY=25.75 EndZ=0
    g111: LineSegment StartX=111.2 StartY=25.75 StartZ=0 EndX=116.9 EndY=25.75 EndZ=0
    g112: LineSegment StartX=116.9 StartY=25.75 StartZ=0 EndX=116.9 EndY=27.75 EndZ=0
    g113: LineSegment StartX=116.9 StartY=27.75 StartZ=0 EndX=111.2 EndY=27.75 EndZ=0
    g114: GeomPoint [constr] X=114.05 Y=26.75 Z=0
    g115: LineSegment StartX=130.25 StartY=27.75 StartZ=0 EndX=130.25 EndY=25.75 EndZ=0
    g116: LineSegment StartX=130.25 StartY=25.75 StartZ=0 EndX=135.95 EndY=25.75 EndZ=0
    g117: LineSegment StartX=135.95 StartY=25.75 StartZ=0 EndX=135.95 EndY=27.75 EndZ=0
    g118: LineSegment StartX=135.95 StartY=27.75 StartZ=0 EndX=130.25 EndY=27.75 EndZ=0
    g119: GeomPoint [constr] X=133.1 Y=26.75 Z=0
    g120: LineSegment StartX=15.95 StartY=30.05 StartZ=0 EndX=15.95 EndY=28.05 EndZ=0
    g121: LineSegment StartX=15.95 StartY=28.05 StartZ=0 EndX=21.65 EndY=28.05 EndZ=0
    g122: LineSegment StartX=21.65 StartY=28.05 StartZ=0 EndX=21.65 EndY=30.05 EndZ=0
    g123: LineSegment StartX=21.65 StartY=30.05 StartZ=0 EndX=15.95 EndY=30.05 EndZ=0
    g124: GeomPoint [constr] X=18.8 Y=29.05 Z=0
    g125: GeomPoint X=19.05 Y=19.05 Z=0
  constraints (327):
    c: Coincident(g0,g1)
    c: Coincident(g1,g2)
    c: Coincident(g2,g3)
    c: Coincident(g3,g0)
    c: Vertical(g0)
    c: Vertical(g2)
    c: Horizontal(g1)
    c: Horizontal(g3)
    c: Symmetric(g2,g0,g4)
    c: Coincident(g5,g6)
    c: Coincident(g6,g7)
    c: Coincident(g7,g8)
    c: Coincident(g8,g5)
    c: Vertical(g5)
    c: Vertical(g7)
    c: Horizontal(g6)
    c: Horizontal(g8)
    c: Symmetric(g7,g5,g9)
    c: Coincident(g10,g11)
    c: Coincident(g11,g12)
    c: Coincident(g12,g13)
    c: Coincident(g13,g10)
    c: Vertical(g10)
    c: Vertical(g12)
    c: Horizontal(g11)
    c: Horizontal(g13)
    c: Symmetric(g12,g10,g14)
    c: Coincident(g15,g16)
    c: Coincident(g16,g17)
    c: Coincident(g17,g18)
    c: Coincident(g18,g15)
    c: Vertical(g15)
    c: Vertical(g17)
    c: Horizontal(g16)
    c: Horizontal(g18)
    c: Symmetric(g17,g15,g19)
    c: Coincident(g20,g21)
    c: Coincident(g21,g22)
    c: Coincident(g22,g23)
    c: Coincident(g23,g20)
    c: Vertical(g20)
    c: Vertical(g22)
    c: Horizontal(g21)
    c: Horizontal(g23)
    c: Symmetric(g22,g20,g24)
    c: Coincident(g25,g26)
    c: Coincident(g26,g27)
    c: Coincident(g27,g28)
    c: Coincident(g28,g25)
    c: Vertical(g25)
    c: Vertical(g27)
    c: Horizontal(g26)
    c: Horizontal(g28)
    c: Symmetric(g27,g25,g29)
    c: Coincident(g30,g31)
    c: Coincident(g31,g32)
    c: Coincident(g32,g33)
    c: Coincident(g33,g30)
    c: Vertical(g30)
    c: Vertical(g32)
    c: Horizontal(g31)
    c: Horizontal(g33)
    c: Symmetric(g32,g30,g34)
    c: Coincident(g35,g36)
    c: Coincident(g36,g37)
    c: Coincident(g37,g38)
    c: Coincident(g38,g35)
    c: Vertical(g35)
    c: Vertical(g37)
    c: Horizontal(g36)
    c: Horizontal(g38)
    c: Symmetric(g37,g35,g39)
    c: Coincident(g40,g41)
    c: Coincident(g41,g42)
    c: Coincident(g42,g43)
    c: Coincident(g43,g40)
    c: Vertical(g40)
    c: Vertical(g42)
    c: Horizontal(g41)
    c: Horizontal(g43)
    c: Symmetric(g42,g40,g44)
    c: Coincident(g45,g46)
    c: Coincident(g46,g47)
    c: Coincident(g47,g48)
    c: Coincident(g48,g45)
    c: Vertical(g45)
    c: Vertical(g47)
    c: Horizontal(g46)
    c: Horizontal(g48)
    c: Symmetric(g47,g45,g49)
    c: Coincident(g50,g51)
    c: Coincident(g51,g52)
    c: Coincident(g52,g53)
    c: Coincident(g53,g50)
    c: Vertical(g50)
    c: Vertical(g52)
    c: Horizontal(g51)
    c: Horizontal(g53)
    c: Symmetric(g52,g50,g54)
    c: Coincident(g55,g56)
    c: Coincident(g56,g57)
    c: Coincident(g57,g58)
    c: Coincident(g58,g55)
    c: Vertical(g55)
    c: Vertical(g57)
    c: Horizontal(g56)
    c: Horizontal(g58)
    c: Symmetric(g57,g55,g59)
    c: Coincident(g60,g61)
    c: Coincident(g61,g62)
    c: Coincident(g62,g63)
    c: Coincident(g63,g60)
    c: Vertical(g60)
    c: Vertical(g62)
    c: Horizontal(g61)
    c: Horizontal(g63)
    c: Symmetric(g62,g60,g64)
    c: Coincident(g65,g66)
    c: Coincident(g66,g67)
    c: Coincident(g67,g68)
    c: Coincident(g68,g65)
    c: Vertical(g65)
    c: Vertical(g67)
    c: Horizontal(g66)
    c: Horizontal(g68)
    c: Symmetric(g67,g65,g69)
    c: Coincident(g70,g71)
    c: Coincident(g71,g72)
    c: Coincident(g72,g73)
    c: Coincident(g73,g70)
    c: Vertical(g70)
    c: Vertical(g72)
    c: Horizontal(g71)
    c: Horizontal(g73)
    c: Symmetric(g72,g70,g74)
    c: Coincident(g75,g76)
    c: Coincident(g76,g77)
    c: Coincident(g77,g78)
    c: Coincident(g78,g75)
    c: Vertical(g75)
    c: Vertical(g77)
    c: Horizontal(g76)
    c: Horizontal(g78)
    c: Symmetric(g77,g75,g79)
    c: Coincident(g80,g81)
    c: Coincident(g81,g82)
    c: Coincident(g82,g83)
    c: Coincident(g83,g80)
    c: Vertical(g80)
    c: Vertical(g82)
    c: Horizontal(g81)
    c: Horizontal(g83)
    c: Symmetric(g82,g80,g84)
    c: Coincident(g85,g86)
    c: Coincident(g86,g87)
    c: Coincident(g87,g88)
    c: Coincident(g88,g85)
    c: Vertical(g85)
    c: Vertical(g87)
    c: Horizontal(g86)
    c: Horizontal(g88)
    c: Symmetric(g87,g85,g89)
    c: Coincident(g90,g91)
    c: Coincident(g91,g92)
    c: Coincident(g92,g93)
    c: Coincident(g93,g90)
    c: Vertical(g90)
    c: Vertical(g92)
    c: Horizontal(g91)
    c: Horizontal(g93)
    c: Symmetric(g92,g90,g94)
    c: Coincident(g95,g96)
    c: Coincident(g96,g97)
    c: Coincident(g97,g98)
    c: Coincident(g98,g95)
    c: Vertical(g95)
    c: Vertical(g97)
    c: Horizontal(g96)
    c: Horizontal(g98)
    c: Symmetric(g97,g95,g99)
    c: Coincident(g100,g101)
    c: Coincident(g101,g102)
    c: Coincident(g102,g103)
    c: Coincident(g103,g100)
    c: Vertical(g100)
    c: Vertical(g102)
    c: Horizontal(g101)
    c: Horizontal(g103)
    c: Symmetric(g102,g100,g104)
    c: Coincident(g105,g106)
    c: Coincident(g106,g107)
    c: Coincident(g107,g108)
    c: Coincident(g108,g105)
    c: Vertical(g105)
    c: Vertical(g107)
    c: Horizontal(g106)
    c: Horizontal(g108)
    c: Symmetric(g107,g105,g109)
    c: Coincident(g110,g111)
    c: Coincident(g111,g112)
    c: Coincident(g112,g113)
    c: Coincident(g113,g110)
    c: Vertical(g110)
    c: Vertical(g112)
    c: Horizontal(g111)
    c: Horizontal(g113)
    c: Symmetric(g112,g110,g114)
    c: Coincident(g115,g116)
    c: Coincident(g116,g117)
    c: Coincident(g117,g118)
    c: Coincident(g118,g115)
    c: Vertical(g115)
    c: Vertical(g117)
    c: Horizontal(g116)
    c: Horizontal(g118)
    c: Symmetric(g117,g115,g119)
    c: Coincident(g120,g121)
    c: Coincident(g121,g122)
    c: Coincident(g122,g123)
    c: Coincident(g123,g120)
    c: Vertical(g120)
    c: Vertical(g122)
    c: Horizontal(g121)
    c: Horizontal(g123)
    c: Symmetric(g122,g120,g124)
    c: Horizontal(g4,g9)
    c: Horizontal(g9,g14)
    c: Horizontal(g14,g19)
    c: Horizontal(g19,g24)
    c: Horizontal(g24,g29)
    c: Horizontal(g34,g39)
    c: Horizontal(g39,g44)
    c: Horizontal(g44,g49)
    c: Horizontal(g49,g54)
    c: Horizontal(g54,g59)
    c: Horizontal(g64,g69)
    c: Horizontal(g69,g74)
    c: Horizontal(g74,g79)
    c: Horizontal(g79,g84)
    c: Horizontal(g84,g89)
    c: Horizontal(g94,g99)
    c: Horizontal(g99,g104)
    c: Horizontal(g104,g109)
    c: Horizontal(g109,g114)
    c: Horizontal(g114,g119)
    c: Vertical(g34,g64)
    c: Vertical(g64,g94)
    c: Vertical(g39,g69)
    c: Vertical(g69,g99)
    c: Vertical(g44,g74)
    c: Vertical(g74,g104)
    c: Vertical(g49,g79)
    c: Vertical(g79,g109)
    c: Vertical(g54,g84)
    c: Vertical(g84,g114)
    c: Vertical(g59,g89)
    c: Vertical(g89,g119)
    c: DistanceX(g121,g121) = 5.7
    c: DistanceY(g120,g120) = 2
    c: Equal(g0,g5)
    c: Equal(g5,g10)
    c: Equal(g10,g15)
    c: Equal(g15,g20)
    c: Equal(g20,g25)
    c: Equal(g30,g35)
    c: Equal(g35,g40)
    c: Equal(g40,g45)
    c: Equal(g45,g50)
    c: Equal(g50,g55)
    c: Equal(g60,g65)
    c: Equal(g65,g70)
    c: Equal(g70,g75)
    c: Equal(g75,g80)
    c: Equal(g80,g85)
    c: Equal(g90,g95)
    c: Equal(g95,g100)
    c: Equal(g100,g105)
    c: Equal(g105,g110)
    c: Equal(g110,g115)
    c: Equal(g115,g120)
    c: Equal(g25,g55)
    c: Equal(g55,g85)
    c: Equal(g85,g115)
    c: Equal(g1,g6)
    c: Equal(g6,g11)
    c: Equal(g11,g16)
    c: Equal(g16,g21)
    c: Equal(g21,g26)
    c: Equal(g31,g36)
    c: Equal(g36,g41)
    c: Equal(g41,g46)
    c: Equal(g46,g51)
    c: Equal(g51,g56)
    c: Equal(g61,g66)
    c: Equal(g66,g71)
    c: Equal(g71,g76)
    c: Equal(g76,g81)
    c: Equal(g81,g86)
    c: Equal(g91,g96)
    c: Equal(g96,g101)
    c: Equal(g101,g106)
    c: Equal(g106,g111)
    c: Equal(g111,g116)
    c: Equal(g116,g121)
    c: Equal(g26,g56)
    c: Equal(g56,g86)
    c: Equal(g86,g116)
    c: DistanceX(g94,g99) = 19.05
    c: DistanceX(g99,g104) = 19.05
    c: DistanceX(g104,g109) = 19.05
    c: DistanceX(g109,g114) = 19.05
    c: DistanceX(g114,g119) = 19.05
    c: Vertical(g14,g44)
    c: Vertical(g19,g49)
    c: DistanceY(g-1,g125) = 19.05
    c: DistanceX(g4,g39) = 6.375
    c: DistanceX(g39,g9) = 6.375
    c: DistanceX(g24,g54) = 6.375
    c: DistanceX(g54,g29) = 6.375
    c: DistanceY(g119,g124) = 2.3
    c: DistanceX(g-1,g125) = 19.05
    c: DistanceX(g124,g94) = 19.05
    c: DistanceX(g124,g125) = 0.25
    c: DistanceY(g125,g94) = 7.7
    c: DistanceY(g34,g4) = 19.05
    c: DistanceY(g64,g34) = 19.05
    c: DistanceY(g94,g64) = 19.05
FEATURE [Sketcher::SketchObject] Sketch032  label="BR-ContactEnc"
  ArcFitTolerance = 1e-06
  AttachmentSupport = -> [XY_Plane003]
  FullyConstrained = true
  MakeInternals = false
  MapMode = 5
  expr: Constraints[15] = VarSet.Bottom_ContactD - 0.5 mm
  sketch-geometry (33):
    g0: GeomPoint [constr] X=19.05 Y=13.15 Z=0
    g1: GeomPoint X=19.05 Y=19.05 Z=0
    g2: GeomPoint [constr] X=19.05 Y=13.15 Z=0
    g3: ArcOfCircle CenterX=19.05 CenterY=13.15 CenterZ=0 NormalX=0 NormalY=0 NormalZ=1 AngleXU=0 Radius=1.25 StartAngle=1.13589 EndAngle=4.27749
    g4: ArcOfCircle CenterX=21.59 CenterY=11.97 CenterZ=0 NormalX=0 NormalY=0 NormalZ=1 AngleXU=0 Radius=1.25 StartAngle=4.27749 EndAngle=7.41908
    g5: LineSegment StartX=19.5767 StartY=14.2836 StartZ=0 EndX=22.1167 EndY=13.1036 EndZ=0
    g6: LineSegment StartX=18.5233 StartY=12.0164 StartZ=0 EndX=21.0633 EndY=10.8364 EndZ=0
    g7: ArcOfCircle CenterX=16.51 CenterY=13.97 CenterZ=0 NormalX=0 NormalY=0 NormalZ=1 AngleXU=0 Radius=1.25 StartAngle=8e-16 EndAngle=3.14159
    g8: ArcOfCircle CenterX=16.51 CenterY=11.97 CenterZ=0 NormalX=0 NormalY=0 NormalZ=1 AngleXU=0 Radius=1.25 StartAngle=3.14159 EndAngle=6.28319
    g9: LineSegment StartX=17.76 StartY=13.97 StartZ=0 EndX=17.76 EndY=11.97 EndZ=0
    g10: LineSegment StartX=15.26 StartY=13.97 StartZ=0 EndX=15.26 EndY=11.97 EndZ=0
    g11: GeomPoint [constr] X=133.35 Y=70.3 Z=0
    g12: GeomPoint X=133.35 Y=76.2 Z=0
    g13: GeomPoint [constr] X=133.35 Y=70.3 Z=0
    g14: ArcOfCircle CenterX=133.35 CenterY=70.3 CenterZ=0 NormalX=0 NormalY=0 NormalZ=1 AngleXU=0 Radius=1.25 StartAngle=1.13589 EndAngle=4.27749
    g15: ArcOfCircle CenterX=135.89 CenterY=69.12 CenterZ=0 NormalX=0 NormalY=0 NormalZ=1 AngleXU=0 Radius=1.25 StartAngle=4.27749 EndAngle=7.41908
    g16: LineSegment StartX=133.877 StartY=71.4336 StartZ=0 EndX=136.417 EndY=70.2536 EndZ=0
    g17: LineSegment StartX=132.823 StartY=69.1664 StartZ=0 EndX=135.363 EndY=67.9864 EndZ=0
    g18: ArcOfCircle CenterX=130.81 CenterY=71.12 CenterZ=0 NormalX=0 NormalY=0 NormalZ=1 AngleXU=0 Radius=1.25 StartAngle=-2.7e-15 EndAngle=3.14159
    g19: ArcOfCircle CenterX=130.81 CenterY=69.12 CenterZ=0 NormalX=0 NormalY=0 NormalZ=1 AngleXU=0 Radius=1.25 StartAngle=3.14159 EndAngle=6.28319
    g20: LineSegment StartX=132.06 StartY=71.12 StartZ=0 EndX=132.06 EndY=69.12 EndZ=0
    g21: LineSegment StartX=129.56 StartY=71.12 StartZ=0 EndX=129.56 EndY=69.12 EndZ=0
    g22: GeomPoint [constr] X=38.1 Y=70.3 Z=0
    g23: GeomPoint X=38.1 Y=76.2 Z=0
    g24: GeomPoint [constr] X=38.1 Y=70.3 Z=0
    g25: ArcOfCircle CenterX=38.1 CenterY=70.3 CenterZ=0 NormalX=0 NormalY=0 NormalZ=1 AngleXU=0 Radius=1.25 StartAngle=1.13589 EndAngle=4.27749
    g26: ArcOfCircle CenterX=40.64 CenterY=69.12 CenterZ=0 NormalX=0 NormalY=0 NormalZ=1 AngleXU=0 Radius=1.25 StartAngle=4.27749 EndAngle=7.41908
    g27: LineSegment StartX=38.6267 StartY=71.4336 StartZ=0 EndX=41.1667 EndY=70.2536 EndZ=0
    g28: LineSegment StartX=37.5733 StartY=69.1664 StartZ=0 EndX=40.1133 EndY=67.9864 EndZ=0
    g29: ArcOfCircle CenterX=35.56 CenterY=71.12 CenterZ=0 NormalX=0 NormalY=0 NormalZ=1 AngleXU=0 Radius=1.25 StartAngle=5e-16 EndAngle=3.14159
    g30: ArcOfCircle CenterX=35.56 CenterY=69.12 CenterZ=0 NormalX=0 NormalY=0 NormalZ=1 AngleXU=0 Radius=1.25 StartAngle=3.14159 EndAngle=6.28319
    g31: LineSegment StartX=36.81 StartY=71.12 StartZ=0 EndX=36.81 EndY=69.12 EndZ=0
    g32: LineSegment StartX=34.31 StartY=71.12 StartZ=0 EndX=34.31 EndY=69.12 EndZ=0
  constraints (72):
    c: DistanceY(g-1,g1) = 19.05
    c: DistanceY(g0,g1) = 5.9
    c: Tangent(g3,g5) = 1.5708
    c: Tangent(g3,g6) = -1.5708
    c: Tangent(g4,g5) = 1.5708
    c: Tangent(g4,g6) = -1.5708
    c: Equal(g3,g4)
    c: Tangent(g7,g9) = 1.5708
    c: Tangent(g7,g10) = -1.5708
    c: Tangent(g8,g9) = 1.5708
    c: Tangent(g8,g10) = -1.5708
    c: Equal(g7,g8)
    c: Coincident(g3,g2)
    c: Horizontal(g8,g4)
    c: Equal(g8,g4)
    c: Diameter(g8) = 2.5
    c: Vertical(g7,g8)
    c: Coincident(g2,g0)
    c: DistanceX(g0,g4) = 2.54
    c: DistanceX(g8,g0) = 2.54
    c: DistanceY(g0,g7) = 0.82
    c: DistanceY(g4,g0) = 1.18
    c: DistanceY(g11,g12) = 5.9
    c: Tangent(g14,g16) = 1.5708
    c: Tangent(g14,g17) = -1.5708
    c: Tangent(g15,g16) = 1.5708
    c: Tangent(g15,g17) = -1.5708
    c: Equal(g14,g15)
    c: Tangent(g18,g20) = 1.5708
    c: Tangent(g18,g21) = -1.5708
    c: Tangent(g19,g20) = 1.5708
    c: Tangent(g19,g21) = -1.5708
    c: Equal(g18,g19)
    c: Coincident(g14,g13)
    c: Horizontal(g19,g15)
    c: Equal(g19,g15)
    c: Vertical(g18,g19)
    c: Coincident(g13,g11)
    c: DistanceX(g11,g15) = 2.54
    c: DistanceX(g19,g11) = 2.54
    c: DistanceY(g11,g18) = 0.82
    c: DistanceY(g22,g23) = 5.9
    c: Tangent(g25,g27) = 1.5708
    c: Tangent(g25,g28) = -1.5708
    c: Tangent(g26,g27) = 1.5708
    c: Tangent(g26,g28) = -1.5708
    c: Equal(g25,g26)
    c: Tangent(g29,g31) = 1.5708
    c: Tangent(g29,g32) = -1.5708
    c: Tangent(g30,g31) = 1.5708
    c: Tangent(g30,g32) = -1.5708
    c: Equal(g29,g30)
    c: Coincident(g25,g24)
    c: Horizontal(g30,g26)
    c: Equal(g30,g26)
    c: Vertical(g29,g30)
    c: Coincident(g24,g22)
    c: DistanceX(g22,g26) = 2.54
    c: DistanceX(g30,g22) = 2.54
    c: DistanceY(g22,g29) = 0.82
    c: Horizontal(g12,g23)
    c: DistanceY(g1,g23) = 57.15
    c: Equal(g30,g8)
    c: Equal(g19,g8)
    c: DistanceY(g19,g11) = 1.18
    c: DistanceY(g30,g22) = 1.18
    c: DistanceX(g-1,g22) = 38.1
    c: DistanceX(g-1,g23) = 38.1
    c: DistanceX(g22,g11) = 95.25
    c: DistanceX(g23,g12) = 95.25
    c: DistanceX(g-1,g0) = 19.05
    c: DistanceX(g-1,g1) = 19.05
FEATURE [Sketcher::SketchObject] Sketch034  label="BR-Connector"
  ArcFitTolerance = 1e-06
  AttachmentSupport = -> [XY_Plane003]
  FullyConstrained = true
  MakeInternals = false
  MapMode = 5
  expr: Constraints[20] = 1.5 * 19.05 mm
  sketch-geometry (14):
    g0: Circle CenterX=26.05 CenterY=31.05 CenterZ=0 NormalX=0 NormalY=0 NormalZ=1 AngleXU=0 Radius=2.25
    g1: Circle CenterX=12.25 CenterY=31.05 CenterZ=0 NormalX=0 NormalY=0 NormalZ=1 AngleXU=0 Radius=2.25
    g2: GeomPoint X=19.05 Y=19.05 Z=0
    g3: Circle CenterX=11.7 CenterY=49.725 CenterZ=0 NormalX=0 NormalY=0 NormalZ=1 AngleXU=0 Radius=1.15
    g4: Circle CenterX=11.7 CenterY=44.725 CenterZ=0 NormalX=0 NormalY=0 NormalZ=1 AngleXU=0 Radius=1.15
    g5: Circle CenterX=14.2 CenterY=43.725 CenterZ=0 NormalX=0 NormalY=0 NormalZ=1 AngleXU=0 Radius=1.4
    g6: Circle CenterX=14.2 CenterY=50.725 CenterZ=0 NormalX=0 NormalY=0 NormalZ=1 AngleXU=0 Radius=1.4
    g7: GeomPoint X=14.2 Y=47.225 Z=0
    g8: GeomPoint X=11.7 Y=47.225 Z=0
    g9: GeomPoint X=2 Y=47.625 Z=0
    g10: Circle CenterX=13.25 CenterY=41.55 CenterZ=0 NormalX=0 NormalY=0 NormalZ=1 AngleXU=0 Radius=1.25
    g11: Circle CenterX=16.25 CenterY=41.55 CenterZ=0 NormalX=0 NormalY=0 NormalZ=1 AngleXU=0 Radius=1.25
    g12: Circle CenterX=20.25 CenterY=41.55 CenterZ=0 NormalX=0 NormalY=0 NormalZ=1 AngleXU=0 Radius=1.25
    g13: Circle CenterX=21.25 CenterY=37.05 CenterZ=0 NormalX=0 NormalY=0 NormalZ=1 AngleXU=0 Radius=1.25
  constraints (38):
    c: Equal(g0,g1)
    c: Diameter(g1) = 4.5
    c: Equal(g6,g5)
    c: Equal(g3,g4)
    c: Diameter(g6) = 2.8
    c: Diameter(g3) = 2.3
    c: DistanceX(g-1,g9) = 2
    c: DistanceX(g-1,g2) = 19.05
    c: DistanceY(g-1,g2) = 19.05
    c: DistanceY(g8,g3) = 2.5
    c: DistanceY(g4,g8) = 2.5
    c: DistanceY(g7,g6) = 3.5
    c: DistanceY(g5,g7) = 3.5
    c: DistanceX(g8,g7) = 2.5
    c: DistanceX(g-1,g3) = 11.7
    c: DistanceY(g8,g9) = 0.4
    c: DistanceY(g2,g1) = 12
    c: DistanceX(g1,g2) = 6.8
    c: DistanceX(g2,g0) = 7
    c: Horizontal(g1,g0)
    c: DistanceY(g2,g9) = 28.575
    c: Vertical(g3,g8)
    c: Vertical(g8,g4)
    c: Vertical(g6,g7)
    c: Vertical(g7,g5)
    c: Horizontal(g8,g7)
    c: Diameter(g10) = 2.5
    c: Diameter(g11) = 2.5
    c: Diameter(g12) = 2.5
    c: Diameter(g13) = 2.5
    c: DistanceX(g10,g11) = 3
    c: DistanceX(g11,g12) = 4
    c: DistanceX(g12,g13) = 1
    c: DistanceY(g13,g12) = 4.5
    c: Horizontal(g10,g11)
    c: Horizontal(g11,g12)
    c: DistanceX(g1,g10) = 1
    c: DistanceY(g1,g13) = 6
FEATURE [Sketcher::SketchObject] Sketch037  label="BR-MCU"
  ArcFitTolerance = 1e-06
  AttachmentSupport = -> [XY_Plane003]
  FullyConstrained = true
  MakeInternals = false
  MapMode = 5
  expr: Constraints[0] = 2.5 * 19.05 mm
  expr: Constraints[15] = 2.54 mm * 11
  expr: Constraints[17] = VarSet.Bottom_McuContactD
  expr: Constraints[19] = 15.24 mm / 2
  expr: Constraints[20] = 15.24 mm / 2
  expr: Constraints[8] = 2.54 mm * 11
  sketch-geometry (9):
    g0: GeomPoint X=19.05 Y=47.625 Z=0
    g1: ArcOfCircle CenterX=11.43 CenterY=81.365 CenterZ=0 NormalX=0 NormalY=0 NormalZ=1 AngleXU=0 Radius=1.15 StartAngle=-1.8e-15 EndAngle=3.14159
    g2: ArcOfCircle CenterX=11.43 CenterY=53.425 CenterZ=0 NormalX=0 NormalY=0 NormalZ=1 AngleXU=0 Radius=1.15 StartAngle=3.14159 EndAngle=6.28319
    g3: LineSegment StartX=12.58 StartY=81.365 StartZ=0 EndX=12.58 EndY=53.425 EndZ=0
    g4: LineSegment StartX=10.28 StartY=81.365 StartZ=0 EndX=10.28 EndY=53.425 EndZ=0
    g5: ArcOfCircle CenterX=26.67 CenterY=81.365 CenterZ=0 NormalX=0 NormalY=0 NormalZ=1 AngleXU=0 Radius=1.15 StartAngle=2.1e-15 EndAngle=3.14159
    g6: ArcOfCircle CenterX=26.67 CenterY=53.425 CenterZ=0 NormalX=0 NormalY=0 NormalZ=1 AngleXU=0 Radius=1.15 StartAngle=3.14159 EndAngle=6.28319
    g7: LineSegment StartX=27.82 StartY=81.365 StartZ=0 EndX=27.82 EndY=53.425 EndZ=0
    g8: LineSegment StartX=25.52 StartY=81.365 StartZ=0 EndX=25.52 EndY=53.425 EndZ=0
  constraints (22):
    c: DistanceY(g-1,g0) = 47.625
    c: DistanceX(g-1,g0) = 19.05
    c: Tangent(g1,g3) = 1.5708
    c: Tangent(g1,g4) = -1.5708
    c: Tangent(g2,g3) = 1.5708
    c: Tangent(g2,g4) = -1.5708
    c: Equal(g1,g2)
    c: Vertical(g4)
    c: DistanceY(g2,g1) = 27.94
    c: Tangent(g5,g7) = 1.5708
    c: Tangent(g5,g8) = -1.5708
    c: Tangent(g6,g7) = 1.5708
    c: Tangent(g6,g8) = -1.5708
    c: Equal(g5,g6)
    c: Vertical(g7)
    c: DistanceY(g6,g5) = 27.94
    c: Horizontal(g1,g5)
    c: Diameter(g1) = 2.3
    c: Equal(g1,g5)
    c: DistanceX(g2,g0) = 7.62
    c: DistanceX(g0,g6) = 7.62
    c: DistanceY(g0,g2) = 5.8
FEATURE [Sketcher::SketchObject] Sketch029  label="BL-Diode"
  ArcFitTolerance = 1e-06
  AttachmentSupport = -> [XY_Plane001]
  FullyConstrained = true
  MakeInternals = false
  MapMode = 5
  expr: Constraints[257] = VarSet.Bottom_DiodeX
  expr: Constraints[258] = VarSet.Bottom_DiodeY
  sketch-geometry (126):
    g0: LineSegment StartX=-123.275 StartY=84.9 StartZ=0 EndX=-123.275 EndY=82.9 EndZ=0
    g1: LineSegment StartX=-123.275 StartY=82.9 StartZ=0 EndX=-117.575 EndY=82.9 EndZ=0
    g2: LineSegment StartX=-117.575 StartY=82.9 StartZ=0 EndX=-117.575 EndY=84.9 EndZ=0
    g3: LineSegment StartX=-117.575 StartY=84.9 StartZ=0 EndX=-123.275 EndY=84.9 EndZ=0
    g4: GeomPoint [constr] X=-120.425 Y=83.9 Z=0
    g5: LineSegment StartX=-110.525 StartY=84.9 StartZ=0 EndX=-110.525 EndY=82.9 EndZ=0
    g6: LineSegment StartX=-110.525 StartY=82.9 StartZ=0 EndX=-104.825 EndY=82.9 EndZ=0
    g7: LineSegment StartX=-104.825 StartY=82.9 StartZ=0 EndX=-104.825 EndY=84.9 EndZ=0
    g8: LineSegment StartX=-104.825 StartY=84.9 StartZ=0 EndX=-110.525 EndY=84.9 EndZ=0
    g9: GeomPoint [constr] X=-107.675 Y=83.9 Z=0
    g10: LineSegment StartX=-97.85 StartY=84.9 StartZ=0 EndX=-97.85 EndY=82.9 EndZ=0
    g11: LineSegment StartX=-97.85 StartY=82.9 StartZ=0 EndX=-92.15 EndY=82.9 EndZ=0
    g12: LineSegment StartX=-92.15 StartY=82.9 StartZ=0 EndX=-92.15 EndY=84.9 EndZ=0
    g13: LineSegment StartX=-92.15 StartY=84.9 StartZ=0 EndX=-97.85 EndY=84.9 EndZ=0
    g14: GeomPoint [constr] X=-95 Y=83.9 Z=0
    g15: LineSegment StartX=-78.8 StartY=84.9 StartZ=0 EndX=-78.8 EndY=82.9 EndZ=0
    g16: LineSegment StartX=-78.8 StartY=82.9 StartZ=0 EndX=-73.1 EndY=82.9 EndZ=0
    g17: LineSegment StartX=-73.1 StartY=82.9 StartZ=0 EndX=-73.1 EndY=84.9 EndZ=0
    g18: LineSegment StartX=-73.1 StartY=84.9 StartZ=0 EndX=-78.8 EndY=84.9 EndZ=0
    g19: GeomPoint [constr] X=-75.95 Y=83.9 Z=0
    g20: LineSegment StartX=-66.125 StartY=84.9 StartZ=0 EndX=-66.125 EndY=82.9 EndZ=0
    g21: LineSegment StartX=-66.125 StartY=82.9 StartZ=0 EndX=-60.425 EndY=82.9 EndZ=0
    g22: LineSegment StartX=-60.425 StartY=82.9 StartZ=0 EndX=-60.425 EndY=84.9 EndZ=0
    g23: LineSegment StartX=-60.425 StartY=84.9 StartZ=0 EndX=-66.125 EndY=84.9 EndZ=0
    g24: GeomPoint [constr] X=-63.275 Y=83.9 Z=0
    g25: LineSegment StartX=-53.375 StartY=84.9 StartZ=0 EndX=-53.375 EndY=82.9 EndZ=0
    g26: LineSegment StartX=-53.375 StartY=82.9 StartZ=0 EndX=-47.675 EndY=82.9 EndZ=0
    g27: LineSegment StartX=-47.675 StartY=82.9 StartZ=0 EndX=-47.675 EndY=84.9 EndZ=0
    g28: LineSegment StartX=-47.675 StartY=84.9 StartZ=0 EndX=-53.375 EndY=84.9 EndZ=0
    g29: GeomPoint [constr] X=-50.525 Y=83.9 Z=0
    g30: LineSegment StartX=-135.95 StartY=65.85 StartZ=0 EndX=-135.95 EndY=63.85 EndZ=0
    g31: LineSegment StartX=-135.95 StartY=63.85 StartZ=0 EndX=-130.25 EndY=63.85 EndZ=0
    g32: LineSegment StartX=-130.25 StartY=63.85 StartZ=0 EndX=-130.25 EndY=65.85 EndZ=0
    g33: LineSegment StartX=-130.25 StartY=65.85 StartZ=0 EndX=-135.95 EndY=65.85 EndZ=0
    g34: GeomPoint [constr] X=-133.1 Y=64.85 Z=0
    g35: LineSegment StartX=-116.9 StartY=65.85 StartZ=0 EndX=-116.9 EndY=63.85 EndZ=0
    g36: LineSegment StartX=-116.9 StartY=63.85 StartZ=0 EndX=-111.2 EndY=63.85 EndZ=0
    g37: LineSegment StartX=-111.2 StartY=63.85 StartZ=0 EndX=-111.2 EndY=65.85 EndZ=0
    g38: LineSegment StartX=-111.2 StartY=65.85 StartZ=0 EndX=-116.9 EndY=65.85 EndZ=0
    g39: GeomPoint [constr] X=-114.05 Y=64.85 Z=0
    g40: LineSegment StartX=-97.85 StartY=65.85 StartZ=0 EndX=-97.85 EndY=63.85 EndZ=0
    g41: LineSegment StartX=-97.85 StartY=63.85 StartZ=0 EndX=-92.15 EndY=63.85 EndZ=0
    g42: LineSegment StartX=-92.15 StartY=63.85 StartZ=0 EndX=-92.15 EndY=65.85 EndZ=0
    g43: LineSegment StartX=-92.15 StartY=65.85 StartZ=0 EndX=-97.85 EndY=65.85 EndZ=0
    g44: GeomPoint [constr] X=-95 Y=64.85 Z=0
    g45: LineSegment StartX=-78.8 StartY=65.85 StartZ=0 EndX=-78.8 EndY=63.85 EndZ=0
    g46: LineSegment StartX=-78.8 StartY=63.85 StartZ=0 EndX=-73.1 EndY=63.85 EndZ=0
    g47: LineSegment StartX=-73.1 StartY=63.85 StartZ=0 EndX=-73.1 EndY=65.85 EndZ=0
    g48: LineSegment StartX=-73.1 StartY=65.85 StartZ=0 EndX=-78.8 EndY=65.85 EndZ=0
    g49: GeomPoint [constr] X=-75.95 Y=64.85 Z=0
    g50: LineSegment StartX=-59.75 StartY=65.85 StartZ=0 EndX=-59.75 EndY=63.85 EndZ=0
    g51: LineSegment StartX=-59.75 StartY=63.85 StartZ=0 EndX=-54.05 EndY=63.85 EndZ=0
    g52: LineSegment StartX=-54.05 StartY=63.85 StartZ=0 EndX=-54.05 EndY=65.85 EndZ=0
    g53: LineSegment StartX=-54.05 StartY=65.85 StartZ=0 EndX=-59.75 EndY=65.85 EndZ=0
    g54: GeomPoint [constr] X=-56.9 Y=64.85 Z=0
    g55: LineSegment StartX=-40.7 StartY=65.85 StartZ=0 EndX=-40.7 EndY=63.85 EndZ=0
    g56: LineSegment StartX=-40.7 StartY=63.85 StartZ=0 EndX=-35 EndY=63.85 EndZ=0
    g57: LineSegment StartX=-35 StartY=63.85 StartZ=0 EndX=-35 EndY=65.85 EndZ=0
    g58: LineSegment StartX=-35 StartY=65.85 StartZ=0 EndX=-40.7 EndY=65.85 EndZ=0
    g59: GeomPoint [constr] X=-37.85 Y=64.85 Z=0
    g60: LineSegment StartX=-135.95 StartY=46.8 StartZ=0 EndX=-135.95 EndY=44.8 EndZ=0
    g61: LineSegment StartX=-135.95 StartY=44.8 StartZ=0 EndX=-130.25 EndY=44.8 EndZ=0
    g62: LineSegment StartX=-130.25 StartY=44.8 StartZ=0 EndX=-130.25 EndY=46.8 EndZ=0
    g63: LineSegment StartX=-130.25 StartY=46.8 StartZ=0 EndX=-135.95 EndY=46.8 EndZ=0
    g64: GeomPoint [constr] X=-133.1 Y=45.8 Z=0
    g65: LineSegment StartX=-116.9 StartY=46.8 StartZ=0 EndX=-116.9 EndY=44.8 EndZ=0
    g66: LineSegment StartX=-116.9 StartY=44.8 StartZ=0 EndX=-111.2 EndY=44.8 EndZ=0
    g67: LineSegment StartX=-111.2 StartY=44.8 StartZ=0 EndX=-111.2 EndY=46.8 EndZ=0
    g68: LineSegment StartX=-111.2 StartY=46.8 StartZ=0 EndX=-116.9 EndY=46.8 EndZ=0
    g69: GeomPoint [constr] X=-114.05 Y=45.8 Z=0
    g70: LineSegment StartX=-97.85 StartY=46.8 StartZ=0 EndX=-97.85 EndY=44.8 EndZ=0
    g71: LineSegment StartX=-97.85 StartY=44.8 StartZ=0 EndX=-92.15 EndY=44.8 EndZ=0
    g72: LineSegment StartX=-92.15 StartY=44.8 StartZ=0 EndX=-92.15 EndY=46.8 EndZ=0
    g73: LineSegment StartX=-92.15 StartY=46.8 StartZ=0 EndX=-97.85 EndY=46.8 EndZ=0
    g74: GeomPoint [constr] X=-95 Y=45.8 Z=0
    g75: LineSegment StartX=-78.8 StartY=46.8 StartZ=0 EndX=-78.8 EndY=44.8 EndZ=0
    g76: LineSegment StartX=-78.8 StartY=44.8 StartZ=0 EndX=-73.1 EndY=44.8 EndZ=0
    g77: LineSegment StartX=-73.1 StartY=44.8 StartZ=0 EndX=-73.1 EndY=46.8 EndZ=0
    g78: LineSegment StartX=-73.1 StartY=46.8 StartZ=0 EndX=-78.8 EndY=46.8 EndZ=0
    g79: GeomPoint [constr] X=-75.95 Y=45.8 Z=0
    g80: LineSegment StartX=-59.75 StartY=46.8 StartZ=0 EndX=-59.75 EndY=44.8 EndZ=0
    g81: LineSegment StartX=-59.75 StartY=44.8 StartZ=0 EndX=-54.05 EndY=44.8 EndZ=0
    g82: LineSegment StartX=-54.05 StartY=44.8 StartZ=0 EndX=-54.05 EndY=46.8 EndZ=0
    g83: LineSegment StartX=-54.05 StartY=46.8 StartZ=0 EndX=-59.75 EndY=46.8 EndZ=0
    g84: GeomPoint [constr] X=-56.9 Y=45.8 Z=0
    g85: LineSegment StartX=-40.7 StartY=46.8 StartZ=0 EndX=-40.7 EndY=44.8 EndZ=0
    g86: LineSegment StartX=-40.7 StartY=44.8 StartZ=0 EndX=-35 EndY=44.8 EndZ=0
    g87: LineSegment StartX=-35 StartY=44.8 StartZ=0 EndX=-35 EndY=46.8 EndZ=0
    g88: LineSegment StartX=-35 StartY=46.8 StartZ=0 EndX=-40.7 EndY=46.8 EndZ=0
    g89: GeomPoint [constr] X=-37.85 Y=45.8 Z=0
    g90: LineSegment StartX=-135.95 StartY=27.75 StartZ=0 EndX=-135.95 EndY=25.75 EndZ=0
    g91: LineSegment StartX=-135.95 StartY=25.75 StartZ=0 EndX=-130.25 EndY=25.75 EndZ=0
    g92: LineSegment StartX=-130.25 StartY=25.75 StartZ=0 EndX=-130.25 EndY=27.75 EndZ=0
    g93: LineSegment StartX=-130.25 StartY=27.75 StartZ=0 EndX=-135.95 EndY=27.75 EndZ=0
    g94: GeomPoint [constr] X=-133.1 Y=26.75 Z=0
    g95: LineSegment StartX=-116.9 StartY=27.75 StartZ=0 EndX=-116.9 EndY=25.75 EndZ=0
    g96: LineSegment StartX=-116.9 StartY=25.75 StartZ=0 EndX=-111.2 EndY=25.75 EndZ=0
    g97: LineSegment StartX=-111.2 StartY=25.75 StartZ=0 EndX=-111.2 EndY=27.75 EndZ=0
    g98: LineSegment StartX=-111.2 StartY=27.75 StartZ=0 EndX=-116.9 EndY=27.75 EndZ=0
    g99: GeomPoint [constr] X=-114.05 Y=26.75 Z=0
    g100: LineSegment StartX=-97.85 StartY=27.75 StartZ=0 EndX=-97.85 EndY=25.75 EndZ=0
    g101: LineSegment StartX=-97.85 StartY=25.75 StartZ=0 EndX=-92.15 EndY=25.75 EndZ=0
    g102: LineSegment StartX=-92.15 StartY=25.75 StartZ=0 EndX=-92.15 EndY=27.75 EndZ=0
    g103: LineSegment StartX=-92.15 StartY=27.75 StartZ=0 EndX=-97.85 EndY=27.75 EndZ=0
    g104: GeomPoint [constr] X=-95 Y=26.75 Z=0
    g105: LineSegment StartX=-78.8 StartY=27.75 StartZ=0 EndX=-78.8 EndY=25.75 EndZ=0
    g106: LineSegment StartX=-78.8 StartY=25.75 StartZ=0 EndX=-73.1 EndY=25.75 EndZ=0
    g107: LineSegment StartX=-73.1 StartY=25.75 StartZ=0 EndX=-73.1 EndY=27.75 EndZ=0
    g108: LineSegment StartX=-73.1 StartY=27.75 StartZ=0 EndX=-78.8 EndY=27.75 EndZ=0
    g109: GeomPoint [constr] X=-75.95 Y=26.75 Z=0
    g110: LineSegment StartX=-59.75 StartY=27.75 StartZ=0 EndX=-59.75 EndY=25.75 EndZ=0
    g111: LineSegment StartX=-59.75 StartY=25.75 StartZ=0 EndX=-54.05 EndY=25.75 EndZ=0
    g112: LineSegment StartX=-54.05 StartY=25.75 StartZ=0 EndX=-54.05 EndY=27.75 EndZ=0
    g113: LineSegment StartX=-54.05 StartY=27.75 StartZ=0 EndX=-59.75 EndY=27.75 EndZ=0
    g114: GeomPoint [constr] X=-56.9 Y=26.75 Z=0
    g115: LineSegment StartX=-40.7 StartY=27.75 StartZ=0 EndX=-40.7 EndY=25.75 EndZ=0
    g116: LineSegment StartX=-40.7 StartY=25.75 StartZ=0 EndX=-35 EndY=25.75 EndZ=0
    g117: LineSegment StartX=-35 StartY=25.75 StartZ=0 EndX=-35 EndY=27.75 EndZ=0
    g118: LineSegment StartX=-35 StartY=27.75 StartZ=0 EndX=-40.7 EndY=27.75 EndZ=0
    g119: GeomPoint [constr] X=-37.85 Y=26.75 Z=0
    g120: LineSegment StartX=-21.65 StartY=30.05 StartZ=0 EndX=-21.65 EndY=28.05 EndZ=0
    g121: LineSegment StartX=-21.65 StartY=28.05 StartZ=0 EndX=-15.95 EndY=28.05 EndZ=0
    g122: LineSegment StartX=-15.95 StartY=28.05 StartZ=0 EndX=-15.95 EndY=30.05 EndZ=0
    g123: LineSegment StartX=-15.95 StartY=30.05 StartZ=0 EndX=-21.65 EndY=30.05 EndZ=0
    g124: GeomPoint [constr] X=-18.8 Y=29.05 Z=0
    g125: GeomPoint X=-19.05 Y=19.05 Z=0
  constraints (327):
    c: Coincident(g0,g1)
    c: Coincident(g1,g2)
    c: Coincident(g2,g3)
    c: Coincident(g3,g0)
    c: Vertical(g0)
    c: Vertical(g2)
    c: Horizontal(g1)
    c: Horizontal(g3)
    c: Symmetric(g2,g0,g4)
    c: Coincident(g5,g6)
    c: Coincident(g6,g7)
    c: Coincident(g7,g8)
    c: Coincident(g8,g5)
    c: Vertical(g5)
    c: Vertical(g7)
    c: Horizontal(g6)
    c: Horizontal(g8)
    c: Symmetric(g7,g5,g9)
    c: Coincident(g10,g11)
    c: Coincident(g11,g12)
    c: Coincident(g12,g13)
    c: Coincident(g13,g10)
    c: Vertical(g10)
    c: Vertical(g12)
    c: Horizontal(g11)
    c: Horizontal(g13)
    c: Symmetric(g12,g10,g14)
    c: Coincident(g15,g16)
    c: Coincident(g16,g17)
    c: Coincident(g17,g18)
    c: Coincident(g18,g15)
    c: Vertical(g15)
    c: Vertical(g17)
    c: Horizontal(g16)
    c: Horizontal(g18)
    c: Symmetric(g17,g15,g19)
    c: Coincident(g20,g21)
    c: Coincident(g21,g22)
    c: Coincident(g22,g23)
    c: Coincident(g23,g20)
    c: Vertical(g20)
    c: Vertical(g22)
    c: Horizontal(g21)
    c: Horizontal(g23)
    c: Symmetric(g22,g20,g24)
    c: Coincident(g25,g26)
    c: Coincident(g26,g27)
    c: Coincident(g27,g28)
    c: Coincident(g28,g25)
    c: Vertical(g25)
    c: Vertical(g27)
    c: Horizontal(g26)
    c: Horizontal(g28)
    c: Symmetric(g27,g25,g29)
    c: Coincident(g30,g31)
    c: Coincident(g31,g32)
    c: Coincident(g32,g33)
    c: Coincident(g33,g30)
    c: Vertical(g30)
    c: Vertical(g32)
    c: Horizontal(g31)
    c: Horizontal(g33)
    c: Symmetric(g32,g30,g34)
    c: Coincident(g35,g36)
    c: Coincident(g36,g37)
    c: Coincident(g37,g38)
    c: Coincident(g38,g35)
    c: Vertical(g35)
    c: Vertical(g37)
    c: Horizontal(g36)
    c: Horizontal(g38)
    c: Symmetric(g37,g35,g39)
    c: Coincident(g40,g41)
    c: Coincident(g41,g42)
    c: Coincident(g42,g43)
    c: Coincident(g43,g40)
    c: Vertical(g40)
    c: Vertical(g42)
    c: Horizontal(g41)
    c: Horizontal(g43)
    c: Symmetric(g42,g40,g44)
    c: Coincident(g45,g46)
    c: Coincident(g46,g47)
    c: Coincident(g47,g48)
    c: Coincident(g48,g45)
    c: Vertical(g45)
    c: Vertical(g47)
    c: Horizontal(g46)
    c: Horizontal(g48)
    c: Symmetric(g47,g45,g49)
    c: Coincident(g50,g51)
    c: Coincident(g51,g52)
    c: Coincident(g52,g53)
    c: Coincident(g53,g50)
    c: Vertical(g50)
    c: Vertical(g52)
    c: Horizontal(g51)
    c: Horizontal(g53)
    c: Symmetric(g52,g50,g54)
    c: Coincident(g55,g56)
    c: Coincident(g56,g57)
    c: Coincident(g57,g58)
    c: Coincident(g58,g55)
    c: Vertical(g55)
    c: Vertical(g57)
    c: Horizontal(g56)
    c: Horizontal(g58)
    c: Symmetric(g57,g55,g59)
    c: Coincident(g60,g61)
    c: Coincident(g61,g62)
    c: Coincident(g62,g63)
    c: Coincident(g63,g60)
    c: Vertical(g60)
    c: Vertical(g62)
    c: Horizontal(g61)
    c: Horizontal(g63)
    c: Symmetric(g62,g60,g64)
    c: Coincident(g65,g66)
    c: Coincident(g66,g67)
    c: Coincident(g67,g68)
    c: Coincident(g68,g65)
    c: Vertical(g65)
    c: Vertical(g67)
    c: Horizontal(g66)
    c: Horizontal(g68)
    c: Symmetric(g67,g65,g69)
    c: Coincident(g70,g71)
    c: Coincident(g71,g72)
    c: Coincident(g72,g73)
    c: Coincident(g73,g70)
    c: Vertical(g70)
    c: Vertical(g72)
    c: Horizontal(g71)
    c: Horizontal(g73)
    c: Symmetric(g72,g70,g74)
    c: Coincident(g75,g76)
    c: Coincident(g76,g77)
    c: Coincident(g77,g78)
    c: Coincident(g78,g75)
    c: Vertical(g75)
    c: Vertical(g77)
    c: Horizontal(g76)
    c: Horizontal(g78)
    c: Symmetric(g77,g75,g79)
    c: Coincident(g80,g81)
    c: Coincident(g81,g82)
    c: Coincident(g82,g83)
    c: Coincident(g83,g80)
    c: Vertical(g80)
    c: Vertical(g82)
    c: Horizontal(g81)
    c: Horizontal(g83)
    c: Symmetric(g82,g80,g84)
    c: Coincident(g85,g86)
    c: Coincident(g86,g87)
    c: Coincident(g87,g88)
    c: Coincident(g88,g85)
    c: Vertical(g85)
    c: Vertical(g87)
    c: Horizontal(g86)
    c: Horizontal(g88)
    c: Symmetric(g87,g85,g89)
    c: Coincident(g90,g91)
    c: Coincident(g91,g92)
    c: Coincident(g92,g93)
    c: Coincident(g93,g90)
    c: Vertical(g90)
    c: Vertical(g92)
    c: Horizontal(g91)
    c: Horizontal(g93)
    c: Symmetric(g92,g90,g94)
    c: Coincident(g95,g96)
    c: Coincident(g96,g97)
    c: Coincident(g97,g98)
    c: Coincident(g98,g95)
    c: Vertical(g95)
    c: Vertical(g97)
    c: Horizontal(g96)
    c: Horizontal(g98)
    c: Symmetric(g97,g95,g99)
    c: Coincident(g100,g101)
    c: Coincident(g101,g102)
    c: Coincident(g102,g103)
    c: Coincident(g103,g100)
    c: Vertical(g100)
    c: Vertical(g102)
    c: Horizontal(g101)
    c: Horizontal(g103)
    c: Symmetric(g102,g100,g104)
    c: Coincident(g105,g106)
    c: Coincident(g106,g107)
    c: Coincident(g107,g108)
    c: Coincident(g108,g105)
    c: Vertical(g105)
    c: Vertical(g107)
    c: Horizontal(g106)
    c: Horizontal(g108)
    c: Symmetric(g107,g105,g109)
    c: Coincident(g110,g111)
    c: Coincident(g111,g112)
    c: Coincident(g112,g113)
    c: Coincident(g113,g110)
    c: Vertical(g110)
    c: Vertical(g112)
    c: Horizontal(g111)
    c: Horizontal(g113)
    c: Symmetric(g112,g110,g114)
    c: Coincident(g115,g116)
    c: Coincident(g116,g117)
    c: Coincident(g117,g118)
    c: Coincident(g118,g115)
    c: Vertical(g115)
    c: Vertical(g117)
    c: Horizontal(g116)
    c: Horizontal(g118)
    c: Symmetric(g117,g115,g119)
    c: Coincident(g120,g121)
    c: Coincident(g121,g122)
    c: Coincident(g122,g123)
    c: Coincident(g123,g120)
    c: Vertical(g120)
    c: Vertical(g122)
    c: Horizontal(g121)
    c: Horizontal(g123)
    c: Symmetric(g122,g120,g124)
    c: Horizontal(g4,g9)
    c: Horizontal(g9,g14)
    c: Horizontal(g14,g19)
    c: Horizontal(g19,g24)
    c: Horizontal(g24,g29)
    c: Horizontal(g34,g39)
    c: Horizontal(g39,g44)
    c: Horizontal(g44,g49)
    c: Horizontal(g49,g54)
    c: Horizontal(g54,g59)
    c: Horizontal(g64,g69)
    c: Horizontal(g69,g74)
    c: Horizontal(g74,g79)
    c: Horizontal(g79,g84)
    c: Horizontal(g84,g89)
    c: Horizontal(g94,g99)
    c: Horizontal(g99,g104)
    c: Horizontal(g104,g109)
    c: Horizontal(g109,g114)
    c: Horizontal(g114,g119)
    c: Vertical(g34,g64)
    c: Vertical(g64,g94)
    c: Vertical(g39,g69)
    c: Vertical(g69,g99)
    c: Vertical(g44,g74)
    c: Vertical(g74,g104)
    c: Vertical(g49,g79)
    c: Vertical(g79,g109)
    c: Vertical(g54,g84)
    c: Vertical(g84,g114)
    c: Vertical(g59,g89)
    c: Vertical(g89,g119)
    c: DistanceX(g121,g121) = 5.7
    c: DistanceY(g120,g120) = 2
    c: Equal(g0,g5)
    c: Equal(g5,g10)
    c: Equal(g10,g15)
    c: Equal(g15,g20)
    c: Equal(g20,g25)
    c: Equal(g30,g35)
    c: Equal(g35,g40)
    c: Equal(g40,g45)
    c: Equal(g45,g50)
    c: Equal(g50,g55)
    c: Equal(g60,g65)
    c: Equal(g65,g70)
    c: Equal(g70,g75)
    c: Equal(g75,g80)
    c: Equal(g80,g85)
    c: Equal(g90,g95)
    c: Equal(g95,g100)
    c: Equal(g100,g105)
    c: Equal(g105,g110)
    c: Equal(g110,g115)
    c: Equal(g115,g120)
    c: Equal(g25,g55)
    c: Equal(g55,g85)
    c: Equal(g85,g115)
    c: Equal(g1,g6)
    c: Equal(g6,g11)
    c: Equal(g11,g16)
    c: Equal(g16,g21)
    c: Equal(g21,g26)
    c: Equal(g31,g36)
    c: Equal(g36,g41)
    c: Equal(g41,g46)
    c: Equal(g46,g51)
    c: Equal(g51,g56)
    c: Equal(g61,g66)
    c: Equal(g66,g71)
    c: Equal(g71,g76)
    c: Equal(g76,g81)
    c: Equal(g81,g86)
    c: Equal(g91,g96)
    c: Equal(g96,g101)
    c: Equal(g101,g106)
    c: Equal(g106,g111)
    c: Equal(g111,g116)
    c: Equal(g116,g121)
    c: Equal(g26,g56)
    c: Equal(g56,g86)
    c: Equal(g86,g116)
    c: DistanceX(g94,g99) = 19.05
    c: DistanceX(g99,g104) = 19.05
    c: DistanceX(g104,g109) = 19.05
    c: DistanceX(g109,g114) = 19.05
    c: DistanceX(g114,g119) = 19.05
    c: DistanceX(g119,g124) = 19.05
    c: DistanceY(g119,g89) = 19.05
    c: DistanceY(g89,g59) = 19.05
    c: Vertical(g14,g44)
    c: Vertical(g19,g49)
    c: DistanceY(g59,g29) = 19.05
    c: DistanceY(g-1,g125) = 19.05
    c: DistanceY(g125,g119) = 7.7
    c: DistanceX(g125,g-1) = 19.05
    c: DistanceX(g125,g124) = 0.25
    c: DistanceX(g4,g39) = 6.375
    c: DistanceX(g39,g9) = 6.375
    c: DistanceX(g24,g54) = 6.375
    c: DistanceX(g54,g29) = 6.375
    c: DistanceY(g119,g124) = 2.3
FEATURE [Sketcher::SketchObject] Sketch033  label="BL-Connector"
  ArcFitTolerance = 1e-06
  AttachmentSupport = -> [XY_Plane001]
  FullyConstrained = true
  MakeInternals = false
  MapMode = 5
  expr: Constraints[36] = 1.5 * 19.05 mm
  sketch-geometry (14):
    g0: Circle CenterX=-26.05 CenterY=31.05 CenterZ=0 NormalX=0 NormalY=0 NormalZ=1 AngleXU=0 Radius=2.25
    g1: Circle CenterX=-12.25 CenterY=31.05 CenterZ=0 NormalX=0 NormalY=0 NormalZ=1 AngleXU=0 Radius=2.25
    g2: GeomPoint X=-19.05 Y=19.05 Z=0
    g3: Circle CenterX=-11.8 CenterY=49.725 CenterZ=0 NormalX=0 NormalY=0 NormalZ=1 AngleXU=0 Radius=1.15
    g4: Circle CenterX=-11.8 CenterY=44.725 CenterZ=0 NormalX=0 NormalY=0 NormalZ=1 AngleXU=0 Radius=1.15
    g5: Circle CenterX=-14.3 CenterY=43.725 CenterZ=0 NormalX=0 NormalY=0 NormalZ=1 AngleXU=0 Radius=1.4
    g6: Circle CenterX=-14.3 CenterY=50.725 CenterZ=0 NormalX=0 NormalY=0 NormalZ=1 AngleXU=0 Radius=1.4
    g7: Circle CenterX=-13.25 CenterY=37.05 CenterZ=0 NormalX=0 NormalY=0 NormalZ=1 AngleXU=0 Radius=1.25
    g8: Circle CenterX=-16.25 CenterY=37.05 CenterZ=0 NormalX=0 NormalY=0 NormalZ=1 AngleXU=0 Radius=1.25
    g9: Circle CenterX=-20.25 CenterY=37.05 CenterZ=0 NormalX=0 NormalY=0 NormalZ=1 AngleXU=0 Radius=1.25
    g10: Circle CenterX=-21.25 CenterY=41.55 CenterZ=0 NormalX=0 NormalY=0 NormalZ=1 AngleXU=0 Radius=1.25
    g11: GeomPoint X=-14.3 Y=47.225 Z=0
    g12: GeomPoint X=-11.8 Y=47.225 Z=0
    g13: GeomPoint X=-2 Y=47.625 Z=0
  constraints (38):
    c: Horizontal(g0,g1)
    c: DistanceX(g2,g-1) = 19.05
    c: DistanceY(g-1,g2) = 19.05
    c: Equal(g0,g1)
    c: Diameter(g1) = 4.5
    c: DistanceY(g2,g1) = 12
    c: DistanceX(g0,g2) = 7
    c: DistanceX(g2,g1) = 6.8
    c: Equal(g6,g5)
    c: Equal(g3,g4)
    c: Diameter(g6) = 2.8
    c: Diameter(g3) = 2.3
    c: Diameter(g7) = 2.5
    c: Diameter(g8) = 2.5
    c: Diameter(g9) = 2.5
    c: Diameter(g10) = 2.5
    c: DistanceY(g9,g10) = 4.5
    c: DistanceX(g10,g9) = 1
    c: DistanceX(g8,g7) = 3
    c: Horizontal(g9,g8)
    c: Horizontal(g8,g7)
    c: DistanceX(g9,g8) = 4
    c: Vertical(g3,g12)
    c: Vertical(g12,g4)
    c: Vertical(g6,g11)
    c: Vertical(g11,g5)
    c: DistanceX(g11,g12) = 2.5
    c: DistanceY(g11,g6) = 3.5
    c: DistanceY(g5,g11) = 3.5
    c: DistanceY(g12,g3) = 2.5
    c: DistanceY(g4,g12) = 2.5
    c: Horizontal(g11,g12)
    c: DistanceX(g13,g-1) = 2
    c: DistanceY(g12,g13) = 0.4
    c: DistanceY(g1,g7) = 6
    c: DistanceX(g7,g1) = 1
    c: DistanceY(g2,g13) = 28.575
    c: DistanceX(g3,g-1) = 11.8
FEATURE [Sketcher::SketchObject] Sketch035  label="BL-MCU"
  ArcFitTolerance = 1e-06
  AttachmentSupport = -> [XY_Plane001]
  FullyConstrained = true
  MakeInternals = false
  MapMode = 5
  expr: Constraints[15] = 2.54 mm * 11
  expr: Constraints[17] = VarSet.Bottom_McuContactD
  expr: Constraints[1] = 2.5 * 19.05 mm
  expr: Constraints[20] = 15.24 mm / 2
  expr: Constraints[21] = 15.24 mm / 2
  expr: Constraints[8] = 11 * 2.54 mm
  sketch-geometry (9):
    g0: GeomPoint X=-19.05 Y=47.625 Z=0
    g1: ArcOfCircle CenterX=-26.67 CenterY=81.365 CenterZ=0 NormalX=0 NormalY=0 NormalZ=1 AngleXU=0 Radius=1.15 StartAngle=3.7e-15 EndAngle=3.14159
    g2: ArcOfCircle CenterX=-26.67 CenterY=53.425 CenterZ=0 NormalX=0 NormalY=0 NormalZ=1 AngleXU=0 Radius=1.15 StartAngle=3.14159 EndAngle=6.28319
    g3: LineSegment StartX=-25.52 StartY=81.365 StartZ=0 EndX=-25.52 EndY=53.425 EndZ=0
    g4: LineSegment StartX=-27.82 StartY=81.365 StartZ=0 EndX=-27.82 EndY=53.425 EndZ=0
    g5: ArcOfCircle CenterX=-11.43 CenterY=81.365 CenterZ=0 NormalX=0 NormalY=0 NormalZ=1 AngleXU=0 Radius=1.15 StartAngle=-3.6e-15 EndAngle=3.14159
    g6: ArcOfCircle CenterX=-11.43 CenterY=53.425 CenterZ=0 NormalX=0 NormalY=0 NormalZ=1 AngleXU=0 Radius=1.15 StartAngle=3.14159 EndAngle=6.28319
    g7: LineSegment StartX=-10.28 StartY=81.365 StartZ=0 EndX=-10.28 EndY=53.425 EndZ=0
    g8: LineSegment StartX=-12.58 StartY=81.365 StartZ=0 EndX=-12.58 EndY=53.425 EndZ=0
  constraints (22):
    c: DistanceX(g0,g-1) = 19.05
    c: DistanceY(g-1,g0) = 47.625
    c: Tangent(g1,g3) = 1.5708
    c: Tangent(g1,g4) = -1.5708
    c: Tangent(g2,g3) = 1.5708
    c: Tangent(g2,g4) = -1.5708
    c: Equal(g1,g2)
    c: Vertical(g4)
    c: DistanceY(g2,g1) = 27.94
    c: Tangent(g5,g7) = 1.5708
    c: Tangent(g5,g8) = -1.5708
    c: Tangent(g6,g7) = 1.5708
    c: Tangent(g6,g8) = -1.5708
    c: Equal(g5,g6)
    c: Vertical(g7)
    c: DistanceY(g6,g5) = 27.94
    c: Horizontal(g1,g5)
    c: Diameter(g1) = 2.3
    c: Equal(g1,g5)
    c: DistanceY(g0,g2) = 5.8
    c: DistanceX(g2,g0) = 7.62
    c: DistanceX(g0,g6) = 7.62
FEATURE [Sketcher::SketchObject] Sketch030  label="BL-ContactEnc"
  ArcFitTolerance = 1e-06
  AttachmentSupport = -> [XY_Plane001]
  FullyConstrained = true
  MakeInternals = false
  MapMode = 5
  expr: Constraints[17] = VarSet.Bottom_ContactD - 0.5 mm
  sketch-geometry (33):
    g0: GeomPoint [constr] X=-19.05 Y=13.15 Z=0
    g1: GeomPoint X=-19.05 Y=19.05 Z=0
    g2: GeomPoint [constr] X=-19.05 Y=13.15 Z=0
    g3: ArcOfCircle CenterX=-19.05 CenterY=13.15 CenterZ=0 NormalX=0 NormalY=0 NormalZ=1 AngleXU=0 Radius=1.25 StartAngle=1.13589 EndAngle=4.27749
    g4: ArcOfCircle CenterX=-16.51 CenterY=11.97 CenterZ=0 NormalX=0 NormalY=0 NormalZ=1 AngleXU=0 Radius=1.25 StartAngle=4.27749 EndAngle=7.41908
    g5: LineSegment StartX=-18.5233 StartY=14.2836 StartZ=0 EndX=-15.9833 EndY=13.1036 EndZ=0
    g6: LineSegment StartX=-19.5767 StartY=12.0164 StartZ=0 EndX=-17.0367 EndY=10.8364 EndZ=0
    g7: ArcOfCircle CenterX=-21.59 CenterY=13.97 CenterZ=0 NormalX=0 NormalY=0 NormalZ=1 AngleXU=0 Radius=1.25 StartAngle=8e-16 EndAngle=3.14159
    g8: ArcOfCircle CenterX=-21.59 CenterY=11.97 CenterZ=0 NormalX=0 NormalY=0 NormalZ=1 AngleXU=0 Radius=1.25 StartAngle=3.14159 EndAngle=6.28319
    g9: LineSegment StartX=-20.34 StartY=13.97 StartZ=0 EndX=-20.34 EndY=11.97 EndZ=0
    g10: LineSegment StartX=-22.84 StartY=13.97 StartZ=0 EndX=-22.84 EndY=11.97 EndZ=0
    g11: GeomPoint [constr] X=-133.35 Y=70.3 Z=0
    g12: GeomPoint X=-133.35 Y=76.2 Z=0
    g13: GeomPoint [constr] X=-133.35 Y=70.3 Z=0
    g14: ArcOfCircle CenterX=-133.35 CenterY=70.3 CenterZ=0 NormalX=0 NormalY=0 NormalZ=1 AngleXU=0 Radius=1.25 StartAngle=1.13589 EndAngle=4.27749
    g15: ArcOfCircle CenterX=-130.81 CenterY=69.12 CenterZ=0 NormalX=0 NormalY=0 NormalZ=1 AngleXU=0 Radius=1.25 StartAngle=4.27749 EndAngle=7.41908
    g16: LineSegment StartX=-132.823 StartY=71.4336 StartZ=0 EndX=-130.283 EndY=70.2536 EndZ=0
    g17: LineSegment StartX=-133.877 StartY=69.1664 StartZ=0 EndX=-131.337 EndY=67.9864 EndZ=0
    g18: ArcOfCircle CenterX=-135.89 CenterY=71.12 CenterZ=0 NormalX=0 NormalY=0 NormalZ=1 AngleXU=0 Radius=1.25 StartAngle=-2.7e-15 EndAngle=3.14159
    g19: ArcOfCircle CenterX=-135.89 CenterY=69.12 CenterZ=0 NormalX=0 NormalY=0 NormalZ=1 AngleXU=0 Radius=1.25 StartAngle=3.14159 EndAngle=6.28319
    g20: LineSegment StartX=-134.64 StartY=71.12 StartZ=0 EndX=-134.64 EndY=69.12 EndZ=0
    g21: LineSegment StartX=-137.14 StartY=71.12 StartZ=0 EndX=-137.14 EndY=69.12 EndZ=0
    g22: GeomPoint [constr] X=-38.1 Y=70.3 Z=0
    g23: GeomPoint X=-38.1 Y=76.2 Z=0
    g24: GeomPoint [constr] X=-38.1 Y=70.3 Z=0
    g25: ArcOfCircle CenterX=-38.1 CenterY=70.3 CenterZ=0 NormalX=0 NormalY=0 NormalZ=1 AngleXU=0 Radius=1.25 StartAngle=1.13589 EndAngle=4.27749
    g26: ArcOfCircle CenterX=-35.56 CenterY=69.12 CenterZ=0 NormalX=0 NormalY=0 NormalZ=1 AngleXU=0 Radius=1.25 StartAngle=4.27749 EndAngle=7.41908
    g27: LineSegment StartX=-37.5733 StartY=71.4336 StartZ=0 EndX=-35.0333 EndY=70.2536 EndZ=0
    g28: LineSegment StartX=-38.6267 StartY=69.1664 StartZ=0 EndX=-36.0867 EndY=67.9864 EndZ=0
    g29: ArcOfCircle CenterX=-40.64 CenterY=71.12 CenterZ=0 NormalX=0 NormalY=0 NormalZ=1 AngleXU=0 Radius=1.25 StartAngle=3.1e-15 EndAngle=3.14159
    g30: ArcOfCircle CenterX=-40.64 CenterY=69.12 CenterZ=0 NormalX=0 NormalY=0 NormalZ=1 AngleXU=0 Radius=1.25 StartAngle=3.14159 EndAngle=6.28319
    g31: LineSegment StartX=-39.39 StartY=71.12 StartZ=0 EndX=-39.39 EndY=69.12 EndZ=0
    g32: LineSegment StartX=-41.89 StartY=71.12 StartZ=0 EndX=-41.89 EndY=69.12 EndZ=0
  constraints (72):
    c: DistanceX(g0,g-1) = 19.05
    c: DistanceX(g1,g-1) = 19.05
    c: DistanceY(g-1,g1) = 19.05
    c: DistanceY(g0,g1) = 5.9
    c: Tangent(g3,g5) = 1.5708
    c: Tangent(g3,g6) = -1.5708
    c: Tangent(g4,g5) = 1.5708
    c: Tangent(g4,g6) = -1.5708
    c: Equal(g3,g4)
    c: Tangent(g7,g9) = 1.5708
    c: Tangent(g7,g10) = -1.5708
    c: Tangent(g8,g9) = 1.5708
    c: Tangent(g8,g10) = -1.5708
    c: Equal(g7,g8)
    c: Coincident(g3,g2)
    c: Horizontal(g8,g4)
    c: Equal(g8,g4)
    c: Diameter(g8) = 2.5
    c: Vertical(g7,g8)
    c: Coincident(g2,g0)
    c: DistanceX(g0,g4) = 2.54
    c: DistanceX(g8,g0) = 2.54
    c: DistanceY(g0,g7) = 0.82
    c: DistanceY(g4,g0) = 1.18
    c: DistanceY(g11,g12) = 5.9
    c: Tangent(g14,g16) = 1.5708
    c: Tangent(g14,g17) = -1.5708
    c: Tangent(g15,g16) = 1.5708
    c: Tangent(g15,g17) = -1.5708
    c: Equal(g14,g15)
    c: Tangent(g18,g20) = 1.5708
    c: Tangent(g18,g21) = -1.5708
    c: Tangent(g19,g20) = 1.5708
    c: Tangent(g19,g21) = -1.5708
    c: Equal(g18,g19)
    c: Coincident(g14,g13)
    c: Horizontal(g19,g15)
    c: Equal(g19,g15)
    c: Vertical(g18,g19)
    c: Coincident(g13,g11)
    c: DistanceX(g11,g15) = 2.54
    c: DistanceX(g19,g11) = 2.54
    c: DistanceY(g11,g18) = 0.82
    c: DistanceX(g22,g-1) = 38.1
    c: DistanceX(g23,g-1) = 38.1
    c: DistanceY(g22,g23) = 5.9
    c: Tangent(g25,g27) = 1.5708
    c: Tangent(g25,g28) = -1.5708
    c: Tangent(g26,g27) = 1.5708
    c: Tangent(g26,g28) = -1.5708
    c: Equal(g25,g26)
    c: Tangent(g29,g31) = 1.5708
    c: Tangent(g29,g32) = -1.5708
    c: Tangent(g30,g31) = 1.5708
    c: Tangent(g30,g32) = -1.5708
    c: Equal(g29,g30)
    c: Coincident(g25,g24)
    c: Horizontal(g30,g26)
    c: Equal(g30,g26)
    c: Vertical(g29,g30)
    c: Coincident(g24,g22)
    c: DistanceX(g22,g26) = 2.54
    c: DistanceX(g30,g22) = 2.54
    c: DistanceY(g22,g29) = 0.82
    c: Horizontal(g12,g23)
    c: DistanceX(g12,g23) = 95.25
    c: DistanceX(g11,g22) = 95.25
    c: DistanceY(g1,g23) = 57.15
    c: Equal(g30,g8)
    c: Equal(g19,g8)
    c: DistanceY(g19,g11) = 1.18
    c: DistanceY(g30,g22) = 1.18
FEATURE [Sketcher::SketchObject] Sketch021  label="BL-Contact"
  ArcFitTolerance = 1e-06
  AttachmentSupport = -> [XY_Plane001]
  FullyConstrained = true
  MakeInternals = false
  MapMode = 5
  expr: Constraints[401] = VarSet.Bottom_ContactD
  sketch-geometry (229):
    g0: GeomPoint [constr] X=-38.1 Y=13.15 Z=0
    g1: GeomPoint [constr] X=-57.15 Y=13.15 Z=0
    g2: GeomPoint [constr] X=-76.2 Y=13.15 Z=0
    g3: GeomPoint [constr] X=-95.25 Y=13.15 Z=0
    g4: GeomPoint [constr] X=-114.3 Y=13.15 Z=0
    g5: GeomPoint [constr] X=-38.1 Y=51.25 Z=0
    g6: GeomPoint [constr] X=-57.15 Y=51.25 Z=0
    g7: GeomPoint [constr] X=-76.2 Y=51.25 Z=0
    g8: GeomPoint [constr] X=-95.25 Y=51.25 Z=0
    g9: GeomPoint [constr] X=-114.3 Y=51.25 Z=0
    g10: GeomPoint [constr] X=-38.1 Y=32.2 Z=0
    g11: GeomPoint [constr] X=-57.15 Y=32.2 Z=0
    g12: GeomPoint [constr] X=-76.2 Y=32.2 Z=0
    g13: GeomPoint [constr] X=-95.25 Y=32.2 Z=0
    g14: GeomPoint [constr] X=-114.3 Y=32.2 Z=0
    g15: GeomPoint [constr] X=-95.25 Y=70.3 Z=0
    g16: GeomPoint [constr] X=-57.15 Y=70.3 Z=0
    g17: GeomPoint [constr] X=-133.35 Y=70.3 Z=0
    g18: GeomPoint [constr] X=-114.3 Y=70.3 Z=0
    g19: GeomPoint [constr] X=-76.2 Y=70.3 Z=0
    g20: GeomPoint [constr] X=-38.1 Y=70.3 Z=0
    g21: GeomPoint [constr] X=-133.35 Y=51.25 Z=0
    g22: GeomPoint [constr] X=-133.35 Y=32.2 Z=0
    g23: GeomPoint [constr] X=-133.35 Y=13.15 Z=0
    g24: GeomPoint [constr] X=-19.05 Y=13.15 Z=0
    g25: ArcOfCircle CenterX=-129.54 CenterY=73.66 CenterZ=0 NormalX=0 NormalY=0 NormalZ=1 AngleXU=0 Radius=1.5 StartAngle=5.43511 EndAngle=8.5767
    g26: ArcOfCircle CenterX=-133.35 CenterY=70.3 CenterZ=0 NormalX=0 NormalY=0 NormalZ=1 AngleXU=0 Radius=1.5 StartAngle=2.29352 EndAngle=5.43511
    g27: LineSegment StartX=-128.548 StartY=72.535 StartZ=0 EndX=-132.358 EndY=69.175 EndZ=0
    g28: LineSegment StartX=-130.532 StartY=74.785 StartZ=0 EndX=-134.342 EndY=71.425 EndZ=0
    g29: ArcOfCircle CenterX=-138.35 CenterY=72.4 CenterZ=0 NormalX=0 NormalY=0 NormalZ=1 AngleXU=0 Radius=1.5 StartAngle=1.09102 EndAngle=4.23261
    g30: ArcOfCircle CenterX=-135.89 CenterY=71.12 CenterZ=0 NormalX=0 NormalY=0 NormalZ=1 AngleXU=0 Radius=1.5 StartAngle=4.23261 EndAngle=7.37421
    g31: LineSegment StartX=-137.658 StartY=73.7306 StartZ=0 EndX=-135.198 EndY=72.4506 EndZ=0
    g32: LineSegment StartX=-139.042 StartY=71.0694 StartZ=0 EndX=-136.582 EndY=69.7894 EndZ=0
    g33: ArcOfCircle CenterX=-110.49 CenterY=73.66 CenterZ=0 NormalX=0 NormalY=0 NormalZ=1 AngleXU=0 Radius=1.5 StartAngle=5.43511 EndAngle=8.5767
    g34: ArcOfCircle CenterX=-114.3 CenterY=70.3 CenterZ=0 NormalX=0 NormalY=0 NormalZ=1 AngleXU=0 Radius=1.5 StartAngle=2.29352 EndAngle=5.43511
    g35: LineSegment StartX=-109.498 StartY=72.535 StartZ=0 EndX=-113.308 EndY=69.175 EndZ=0
    g36: LineSegment StartX=-111.482 StartY=74.785 StartZ=0 EndX=-115.292 EndY=71.425 EndZ=0
    g37: ArcOfCircle CenterX=-119.3 CenterY=72.4 CenterZ=0 NormalX=0 NormalY=0 NormalZ=1 AngleXU=0 Radius=1.5 StartAngle=1.09102 EndAngle=4.23261
    g38: ArcOfCircle CenterX=-116.84 CenterY=71.12 CenterZ=0 NormalX=0 NormalY=0 NormalZ=1 AngleXU=0 Radius=1.5 StartAngle=4.23261 EndAngle=7.37421
    g39: LineSegment StartX=-118.608 StartY=73.7306 StartZ=0 EndX=-116.148 EndY=72.4506 EndZ=0
    g40: LineSegment StartX=-119.992 StartY=71.0694 StartZ=0 EndX=-117.532 EndY=69.7894 EndZ=0
    g41: ArcOfCircle CenterX=-91.44 CenterY=73.66 CenterZ=0 NormalX=0 NormalY=0 NormalZ=1 AngleXU=0 Radius=1.5 StartAngle=5.43511 EndAngle=8.5767
    g42: ArcOfCircle CenterX=-95.25 CenterY=70.3 CenterZ=0 NormalX=0 NormalY=0 NormalZ=1 AngleXU=0 Radius=1.5 StartAngle=2.29352 EndAngle=5.43511
    g43: LineSegment StartX=-90.4479 StartY=72.535 StartZ=0 EndX=-94.2579 EndY=69.175 EndZ=0
    g44: LineSegment StartX=-92.4321 StartY=74.785 StartZ=0 EndX=-96.2421 EndY=71.425 EndZ=0
    g45: ArcOfCircle CenterX=-100.25 CenterY=72.4 CenterZ=0 NormalX=0 NormalY=0 NormalZ=1 AngleXU=0 Radius=1.5 StartAngle=1.09102 EndAngle=4.23261
    g46: ArcOfCircle CenterX=-97.79 CenterY=71.12 CenterZ=0 NormalX=0 NormalY=0 NormalZ=1 AngleXU=0 Radius=1.5 StartAngle=4.23261 EndAngle=7.37421
    g47: LineSegment StartX=-99.5576 StartY=73.7306 StartZ=0 EndX=-97.0976 EndY=72.4506 EndZ=0
    g48: LineSegment StartX=-100.942 StartY=71.0694 StartZ=0 EndX=-98.4824 EndY=69.7894 EndZ=0
    g49: ArcOfCircle CenterX=-72.39 CenterY=73.66 CenterZ=0 NormalX=0 NormalY=0 NormalZ=1 AngleXU=0 Radius=1.5 StartAngle=5.43511 EndAngle=8.5767
    g50: ArcOfCircle CenterX=-76.2 CenterY=70.3 CenterZ=0 NormalX=0 NormalY=0 NormalZ=1 AngleXU=0 Radius=1.5 StartAngle=2.29352 EndAngle=5.43511
    g51: LineSegment StartX=-71.3979 StartY=72.535 StartZ=0 EndX=-75.2079 EndY=69.175 EndZ=0
    g52: LineSegment StartX=-73.3821 StartY=74.785 StartZ=0 EndX=-77.1921 EndY=71.425 EndZ=0
    g53: ArcOfCircle CenterX=-81.2 CenterY=72.4 CenterZ=0 NormalX=0 NormalY=0 NormalZ=1 AngleXU=0 Radius=1.5 StartAngle=1.09102 EndAngle=4.23261
    g54: ArcOfCircle CenterX=-78.74 CenterY=71.12 CenterZ=0 NormalX=0 NormalY=0 NormalZ=1 AngleXU=0 Radius=1.5 StartAngle=4.23261 EndAngle=7.37421
    g55: LineSegment StartX=-80.5076 StartY=73.7306 StartZ=0 EndX=-78.0476 EndY=72.4506 EndZ=0
    g56: LineSegment StartX=-81.8924 StartY=71.0694 StartZ=0 EndX=-79.4324 EndY=69.7894 EndZ=0
    g57: ArcOfCircle CenterX=-53.34 CenterY=73.66 CenterZ=0 NormalX=0 NormalY=0 NormalZ=1 AngleXU=0 Radius=1.5 StartAngle=5.43511 EndAngle=8.5767
    g58: ArcOfCircle CenterX=-57.15 CenterY=70.3 CenterZ=0 NormalX=0 NormalY=0 NormalZ=1 AngleXU=0 Radius=1.5 StartAngle=2.29352 EndAngle=5.43511
    g59: LineSegment StartX=-52.3479 StartY=72.535 StartZ=0 EndX=-56.1579 EndY=69.175 EndZ=0
    g60: LineSegment StartX=-54.3321 StartY=74.785 StartZ=0 EndX=-58.1421 EndY=71.425 EndZ=0
    g61: ArcOfCircle CenterX=-62.15 CenterY=72.4 CenterZ=0 NormalX=0 NormalY=0 NormalZ=1 AngleXU=0 Radius=1.5 StartAngle=1.09102 EndAngle=4.23261
    g62: ArcOfCircle CenterX=-59.69 CenterY=71.12 CenterZ=0 NormalX=0 NormalY=0 NormalZ=1 AngleXU=0 Radius=1.5 StartAngle=4.23261 EndAngle=7.37421
    g63: LineSegment StartX=-61.4576 StartY=73.7306 StartZ=0 EndX=-58.9976 EndY=72.4506 EndZ=0
    g64: LineSegment StartX=-62.8424 StartY=71.0694 StartZ=0 EndX=-60.3824 EndY=69.7894 EndZ=0
    g65: ArcOfCircle CenterX=-34.29 CenterY=73.66 CenterZ=0 NormalX=0 NormalY=0 NormalZ=1 AngleXU=0 Radius=1.5 StartAngle=5.43511 EndAngle=8.5767
    g66: ArcOfCircle CenterX=-38.1 CenterY=70.3 CenterZ=0 NormalX=0 NormalY=0 NormalZ=1 AngleXU=0 Radius=1.5 StartAngle=2.29352 EndAngle=5.43511
    g67: LineSegment StartX=-33.2979 StartY=72.535 StartZ=0 EndX=-37.1079 EndY=69.175 EndZ=0
    g68: LineSegment StartX=-35.2821 StartY=74.785 StartZ=0 EndX=-39.0921 EndY=71.425 EndZ=0
    g69: ArcOfCircle CenterX=-43.1 CenterY=72.4 CenterZ=0 NormalX=0 NormalY=0 NormalZ=1 AngleXU=0 Radius=1.5 StartAngle=1.09102 EndAngle=4.23261
    g70: ArcOfCircle CenterX=-40.64 CenterY=71.12 CenterZ=0 NormalX=0 NormalY=0 NormalZ=1 AngleXU=0 Radius=1.5 StartAngle=4.23261 EndAngle=7.37421
    g71: LineSegment StartX=-42.4076 StartY=73.7306 StartZ=0 EndX=-39.9476 EndY=72.4506 EndZ=0
    g72: LineSegment StartX=-43.7924 StartY=71.0694 StartZ=0 EndX=-41.3324 EndY=69.7894 EndZ=0
    g73: ArcOfCircle CenterX=-129.54 CenterY=54.61 CenterZ=0 NormalX=0 NormalY=0 NormalZ=1 AngleXU=0 Radius=1.5 StartAngle=5.43511 EndAngle=8.5767
    g74: ArcOfCircle CenterX=-133.35 CenterY=51.25 CenterZ=0 NormalX=0 NormalY=0 NormalZ=1 AngleXU=0 Radius=1.5 StartAngle=2.29352 EndAngle=5.43511
    g75: LineSegment StartX=-128.548 StartY=53.485 StartZ=0 EndX=-132.358 EndY=50.125 EndZ=0
    g76: LineSegment StartX=-130.532 StartY=55.735 StartZ=0 EndX=-134.342 EndY=52.375 EndZ=0
    g77: ArcOfCircle CenterX=-138.35 CenterY=53.35 CenterZ=0 NormalX=0 NormalY=0 NormalZ=1 AngleXU=0 Radius=1.5 StartAngle=1.09102 EndAngle=4.23261
    g78: ArcOfCircle CenterX=-135.89 CenterY=52.07 CenterZ=0 NormalX=0 NormalY=0 NormalZ=1 AngleXU=0 Radius=1.5 StartAngle=4.23261 EndAngle=7.37421
    g79: LineSegment StartX=-137.658 StartY=54.6806 StartZ=0 EndX=-135.198 EndY=53.4006 EndZ=0
    g80: LineSegment StartX=-139.042 StartY=52.0194 StartZ=0 EndX=-136.582 EndY=50.7394 EndZ=0
    g81: ArcOfCircle CenterX=-110.49 CenterY=54.61 CenterZ=0 NormalX=0 NormalY=0 NormalZ=1 AngleXU=0 Radius=1.5 StartAngle=5.43511 EndAngle=8.5767
    g82: ArcOfCircle CenterX=-114.3 CenterY=51.25 CenterZ=0 NormalX=0 NormalY=0 NormalZ=1 AngleXU=0 Radius=1.5 StartAngle=2.29352 EndAngle=5.43511
    g83: LineSegment StartX=-109.498 StartY=53.485 StartZ=0 EndX=-113.308 EndY=50.125 EndZ=0
    g84: LineSegment StartX=-111.482 StartY=55.735 StartZ=0 EndX=-115.292 EndY=52.375 EndZ=0
    g85: ArcOfCircle CenterX=-119.3 CenterY=53.35 CenterZ=0 NormalX=0 NormalY=0 NormalZ=1 AngleXU=0 Radius=1.5 StartAngle=1.09102 EndAngle=4.23261
    g86: ArcOfCircle CenterX=-116.84 CenterY=52.07 CenterZ=0 NormalX=0 NormalY=0 NormalZ=1 AngleXU=0 Radius=1.5 StartAngle=4.23261 EndAngle=7.37421
    g87: LineSegment StartX=-118.608 StartY=54.6806 StartZ=0 EndX=-116.148 EndY=53.4006 EndZ=0
    g88: LineSegment StartX=-119.992 StartY=52.0194 StartZ=0 EndX=-117.532 EndY=50.7394 EndZ=0
    g89: ArcOfCircle CenterX=-91.44 CenterY=54.61 CenterZ=0 NormalX=0 NormalY=0 NormalZ=1 AngleXU=0 Radius=1.5 StartAngle=5.43511 EndAngle=8.5767
    g90: ArcOfCircle CenterX=-95.25 CenterY=51.25 CenterZ=0 NormalX=0 NormalY=0 NormalZ=1 AngleXU=0 Radius=1.5 StartAngle=2.29352 EndAngle=5.43511
    g91: LineSegment StartX=-90.4479 StartY=53.485 StartZ=0 EndX=-94.2579 EndY=50.125 EndZ=0
    g92: LineSegment StartX=-92.4321 StartY=55.735 StartZ=0 EndX=-96.2421 EndY=52.375 EndZ=0
    g93: ArcOfCircle CenterX=-100.25 CenterY=53.35 CenterZ=0 NormalX=0 NormalY=0 NormalZ=1 AngleXU=0 Radius=1.5 StartAngle=1.09102 EndAngle=4.23261
    g94: ArcOfCircle CenterX=-97.79 CenterY=52.07 CenterZ=0 NormalX=0 NormalY=0 NormalZ=1 AngleXU=0 Radius=1.5 StartAngle=4.23261 EndAngle=7.37421
    g95: LineSegment StartX=-99.5576 StartY=54.6806 StartZ=0 EndX=-97.0976 EndY=53.4006 EndZ=0
    g96: LineSegment StartX=-100.942 StartY=52.0194 StartZ=0 EndX=-98.4824 EndY=50.7394 EndZ=0
    g97: ArcOfCircle CenterX=-72.39 CenterY=54.61 CenterZ=0 NormalX=0 NormalY=0 NormalZ=1 AngleXU=0 Radius=1.5 StartAngle=5.43511 EndAngle=8.5767
    g98: ArcOfCircle CenterX=-76.2 CenterY=51.25 CenterZ=0 NormalX=0 NormalY=0 NormalZ=1 AngleXU=0 Radius=1.5 StartAngle=2.29352 EndAngle=5.43511
    g99: LineSegment StartX=-71.3979 StartY=53.485 StartZ=0 EndX=-75.2079 EndY=50.125 EndZ=0
    g100: LineSegment StartX=-73.3821 StartY=55.735 StartZ=0 EndX=-77.1921 EndY=52.375 EndZ=0
    g101: ArcOfCircle CenterX=-81.2 CenterY=53.35 CenterZ=0 NormalX=0 NormalY=0 NormalZ=1 AngleXU=0 Radius=1.5 StartAngle=1.09102 EndAngle=4.23261
    g102: ArcOfCircle CenterX=-78.74 CenterY=52.07 CenterZ=0 NormalX=0 NormalY=0 NormalZ=1 AngleXU=0 Radius=1.5 StartAngle=4.23261 EndAngle=7.37421
    g103: LineSegment StartX=-80.5076 StartY=54.6806 StartZ=0 EndX=-78.0476 EndY=53.4006 EndZ=0
    g104: LineSegment StartX=-81.8924 StartY=52.0194 StartZ=0 EndX=-79.4324 EndY=50.7394 EndZ=0
    g105: ArcOfCircle CenterX=-53.34 CenterY=54.61 CenterZ=0 NormalX=0 NormalY=0 NormalZ=1 AngleXU=0 Radius=1.5 StartAngle=5.43511 EndAngle=8.5767
    g106: ArcOfCircle CenterX=-57.15 CenterY=51.25 CenterZ=0 NormalX=0 NormalY=0 NormalZ=1 AngleXU=0 Radius=1.5 StartAngle=2.29352 EndAngle=5.43511
    g107: LineSegment StartX=-52.3479 StartY=53.485 StartZ=0 EndX=-56.1579 EndY=50.125 EndZ=0
    g108: LineSegment StartX=-54.3321 StartY=55.735 StartZ=0 EndX=-58.1421 EndY=52.375 EndZ=0
    g109: ArcOfCircle CenterX=-62.15 CenterY=53.35 CenterZ=0 NormalX=0 NormalY=0 NormalZ=1 AngleXU=0 Radius=1.5 StartAngle=1.09102 EndAngle=4.23261
    g110: ArcOfCircle CenterX=-59.69 CenterY=52.07 CenterZ=0 NormalX=0 NormalY=0 NormalZ=1 AngleXU=0 Radius=1.5 StartAngle=4.23261 EndAngle=7.37421
    g111: LineSegment StartX=-61.4576 StartY=54.6806 StartZ=0 EndX=-58.9976 EndY=53.4006 EndZ=0
    g112: LineSegment StartX=-62.8424 StartY=52.0194 StartZ=0 EndX=-60.3824 EndY=50.7394 EndZ=0
    g113: ArcOfCircle CenterX=-34.29 CenterY=54.61 CenterZ=0 NormalX=0 NormalY=0 NormalZ=1 AngleXU=0 Radius=1.5 StartAngle=5.43511 EndAngle=8.5767
    g114: ArcOfCircle CenterX=-38.1 CenterY=51.25 CenterZ=0 NormalX=0 NormalY=0 NormalZ=1 AngleXU=0 Radius=1.5 StartAngle=2.29352 EndAngle=5.43511
    g115: LineSegment StartX=-33.2979 StartY=53.485 StartZ=0 EndX=-37.1079 EndY=50.125 EndZ=0
    g116: LineSegment StartX=-35.2821 StartY=55.735 StartZ=0 EndX=-39.0921 EndY=52.375 EndZ=0
    g117: ArcOfCircle CenterX=-43.1 CenterY=53.35 CenterZ=0 NormalX=0 NormalY=0 NormalZ=1 AngleXU=0 Radius=1.5 StartAngle=1.09102 EndAngle=4.23261
    g118: ArcOfCircle CenterX=-40.64 CenterY=52.07 CenterZ=0 NormalX=0 NormalY=0 NormalZ=1 AngleXU=0 Radius=1.5 StartAngle=4.23261 EndAngle=7.37421
    g119: LineSegment StartX=-42.4076 StartY=54.6806 StartZ=0 EndX=-39.9476 EndY=53.4006 EndZ=0
    g120: LineSegment StartX=-43.7924 StartY=52.0194 StartZ=0 EndX=-41.3324 EndY=50.7394 EndZ=0
    g121: ArcOfCircle CenterX=-129.54 CenterY=35.56 CenterZ=0 NormalX=0 NormalY=0 NormalZ=1 AngleXU=0 Radius=1.5 StartAngle=5.43511 EndAngle=8.5767
    g122: ArcOfCircle CenterX=-133.35 CenterY=32.2 CenterZ=0 NormalX=0 NormalY=0 NormalZ=1 AngleXU=0 Radius=1.5 StartAngle=2.29352 EndAngle=5.43511
    g123: LineSegment StartX=-128.548 StartY=34.435 StartZ=0 EndX=-132.358 EndY=31.075 EndZ=0
    g124: LineSegment StartX=-130.532 StartY=36.685 StartZ=0 EndX=-134.342 EndY=33.325 EndZ=0
    g125: ArcOfCircle CenterX=-138.35 CenterY=34.3 CenterZ=0 NormalX=0 NormalY=0 NormalZ=1 AngleXU=0 Radius=1.5 StartAngle=1.09102 EndAngle=4.23261
    g126: ArcOfCircle CenterX=-135.89 CenterY=33.02 CenterZ=0 NormalX=0 NormalY=0 NormalZ=1 AngleXU=0 Radius=1.5 StartAngle=4.23261 EndAngle=7.37421
    g127: LineSegment StartX=-137.658 StartY=35.6306 StartZ=0 EndX=-135.198 EndY=34.3506 EndZ=0
    g128: LineSegment StartX=-139.042 StartY=32.9694 StartZ=0 EndX=-136.582 EndY=31.6894 EndZ=0
    g129: ArcOfCircle CenterX=-110.49 CenterY=35.56 CenterZ=0 NormalX=0 NormalY=0 NormalZ=1 AngleXU=0 Radius=1.5 StartAngle=5.43511 EndAngle=8.5767
    g130: ArcOfCircle CenterX=-114.3 CenterY=32.2 CenterZ=0 NormalX=0 NormalY=0 NormalZ=1 AngleXU=0 Radius=1.5 StartAngle=2.29352 EndAngle=5.43511
    g131: LineSegment StartX=-109.498 StartY=34.435 StartZ=0 EndX=-113.308 EndY=31.075 EndZ=0
    g132: LineSegment StartX=-111.482 StartY=36.685 StartZ=0 EndX=-115.292 EndY=33.325 EndZ=0
    g133: ArcOfCircle CenterX=-119.3 CenterY=34.3 CenterZ=0 NormalX=0 NormalY=0 NormalZ=1 AngleXU=0 Radius=1.5 StartAngle=1.09102 EndAngle=4.23261
    g134: ArcOfCircle CenterX=-116.84 CenterY=33.02 CenterZ=0 NormalX=0 NormalY=0 NormalZ=1 AngleXU=0 Radius=1.5 StartAngle=4.23261 EndAngle=7.37421
    g135: LineSegment StartX=-118.608 StartY=35.6306 StartZ=0 EndX=-116.148 EndY=34.3506 EndZ=0
    g136: LineSegment StartX=-119.992 StartY=32.9694 StartZ=0 EndX=-117.532 EndY=31.6894 EndZ=0
    g137: ArcOfCircle CenterX=-91.44 CenterY=35.56 CenterZ=0 NormalX=0 NormalY=0 NormalZ=1 AngleXU=0 Radius=1.5 StartAngle=5.43511 EndAngle=8.5767
    g138: ArcOfCircle CenterX=-95.25 CenterY=32.2 CenterZ=0 NormalX=0 NormalY=0 NormalZ=1 AngleXU=0 Radius=1.5 StartAngle=2.29352 EndAngle=5.43511
    g139: LineSegment StartX=-90.4479 StartY=34.435 StartZ=0 EndX=-94.2579 EndY=31.075 EndZ=0
    g140: LineSegment StartX=-92.4321 StartY=36.685 StartZ=0 EndX=-96.2421 EndY=33.325 EndZ=0
    g141: ArcOfCircle CenterX=-100.25 CenterY=34.3 CenterZ=0 NormalX=0 NormalY=0 NormalZ=1 AngleXU=0 Radius=1.5 StartAngle=1.09102 EndAngle=4.23261
    g142: ArcOfCircle CenterX=-97.79 CenterY=33.02 CenterZ=0 NormalX=0 NormalY=0 NormalZ=1 AngleXU=0 Radius=1.5 StartAngle=4.23261 EndAngle=7.37421
    g143: LineSegment StartX=-99.5576 StartY=35.6306 StartZ=0 EndX=-97.0976 EndY=34.3506 EndZ=0
    g144: LineSegment StartX=-100.942 StartY=32.9694 StartZ=0 EndX=-98.4824 EndY=31.6894 EndZ=0
    g145: ArcOfCircle CenterX=-72.39 CenterY=35.56 CenterZ=0 NormalX=0 NormalY=0 NormalZ=1 AngleXU=0 Radius=1.5 StartAngle=5.43511 EndAngle=8.5767
    g146: ArcOfCircle CenterX=-76.2 CenterY=32.2 CenterZ=0 NormalX=0 NormalY=0 NormalZ=1 AngleXU=0 Radius=1.5 StartAngle=2.29352 EndAngle=5.43511
    g147: LineSegment StartX=-71.3979 StartY=34.435 StartZ=0 EndX=-75.2079 EndY=31.075 EndZ=0
    g148: LineSegment StartX=-73.3821 StartY=36.685 StartZ=0 EndX=-77.1921 EndY=33.325 EndZ=0
    g149: ArcOfCircle CenterX=-81.2 CenterY=34.3 CenterZ=0 NormalX=0 NormalY=0 NormalZ=1 AngleXU=0 Radius=1.5 StartAngle=1.09102 EndAngle=4.23261
    g150: ArcOfCircle CenterX=-78.74 CenterY=33.02 CenterZ=0 NormalX=0 NormalY=0 NormalZ=1 AngleXU=0 Radius=1.5 StartAngle=4.23261 EndAngle=7.37421
    g151: LineSegment StartX=-80.5076 StartY=35.6306 StartZ=0 EndX=-78.0476 EndY=34.3506 EndZ=0
    g152: LineSegment StartX=-81.8924 StartY=32.9694 StartZ=0 EndX=-79.4324 EndY=31.6894 EndZ=0
    g153: ArcOfCircle CenterX=-53.34 CenterY=35.56 CenterZ=0 NormalX=0 NormalY=0 NormalZ=1 AngleXU=0 Radius=1.5 StartAngle=5.43511 EndAngle=8.5767
    g154: ArcOfCircle CenterX=-57.15 CenterY=32.2 CenterZ=0 NormalX=0 NormalY=0 NormalZ=1 AngleXU=0 Radius=1.5 StartAngle=2.29352 EndAngle=5.43511
    g155: LineSegment StartX=-52.3479 StartY=34.435 StartZ=0 EndX=-56.1579 EndY=31.075 EndZ=0
    g156: LineSegment StartX=-54.3321 StartY=36.685 StartZ=0 EndX=-58.1421 EndY=33.325 EndZ=0
    g157: ArcOfCircle CenterX=-62.15 CenterY=34.3 CenterZ=0 NormalX=0 NormalY=0 NormalZ=1 AngleXU=0 Radius=1.5 StartAngle=1.09102 EndAngle=4.23261
    g158: ArcOfCircle CenterX=-59.69 CenterY=33.02 CenterZ=0 NormalX=0 NormalY=0 NormalZ=1 AngleXU=0 Radius=1.5 StartAngle=4.23261 EndAngle=7.37421
    g159: LineSegment StartX=-61.4576 StartY=35.6306 StartZ=0 EndX=-58.9976 EndY=34.3506 EndZ=0
    g160: LineSegment StartX=-62.8424 StartY=32.9694 StartZ=0 EndX=-60.3824 EndY=31.6894 EndZ=0
    g161: ArcOfCircle CenterX=-34.29 CenterY=35.56 CenterZ=0 NormalX=0 NormalY=0 NormalZ=1 AngleXU=0 Radius=1.5 StartAngle=5.43511 EndAngle=8.5767
    g162: ArcOfCircle CenterX=-38.1 CenterY=32.2 CenterZ=0 NormalX=0 NormalY=0 NormalZ=1 AngleXU=0 Radius=1.5 StartAngle=2.29352 EndAngle=5.43511
    g163: LineSegment StartX=-33.2979 StartY=34.435 StartZ=0 EndX=-37.1079 EndY=31.075 EndZ=0
    g164: LineSegment StartX=-35.2821 StartY=36.685 StartZ=0 EndX=-39.0921 EndY=33.325 EndZ=0
    g165: ArcOfCircle CenterX=-43.1 CenterY=34.3 CenterZ=0 NormalX=0 NormalY=0 NormalZ=1 AngleXU=0 Radius=1.5 StartAngle=1.09102 EndAngle=4.23261
    g166: ArcOfCircle CenterX=-40.64 CenterY=33.02 CenterZ=0 NormalX=0 NormalY=0 NormalZ=1 AngleXU=0 Radius=1.5 StartAngle=4.23261 EndAngle=7.37421
    g167: LineSegment StartX=-42.4076 StartY=35.6306 StartZ=0 EndX=-39.9476 EndY=34.3506 EndZ=0
    g168: LineSegment StartX=-43.7924 StartY=32.9694 StartZ=0 EndX=-41.3324 EndY=31.6894 EndZ=0
    g169: ArcOfCircle CenterX=-129.54 CenterY=16.51 CenterZ=0 NormalX=0 NormalY=0 NormalZ=1 AngleXU=0 Radius=1.5 StartAngle=5.43511 EndAngle=8.5767
    g170: ArcOfCircle CenterX=-133.35 CenterY=13.15 CenterZ=0 NormalX=0 NormalY=0 NormalZ=1 AngleXU=0 Radius=1.5 StartAngle=2.29352 EndAngle=5.43511
    g171: LineSegment StartX=-128.548 StartY=15.385 StartZ=0 EndX=-132.358 EndY=12.025 EndZ=0
    g172: LineSegment StartX=-130.532 StartY=17.635 StartZ=0 EndX=-134.342 EndY=14.275 EndZ=0
    g173: ArcOfCircle CenterX=-138.35 CenterY=15.25 CenterZ=0 NormalX=0 NormalY=0 NormalZ=1 AngleXU=0 Radius=1.5 StartAngle=1.09102 EndAngle=4.23261
    g174: ArcOfCircle CenterX=-135.89 CenterY=13.97 CenterZ=0 NormalX=0 NormalY=0 NormalZ=1 AngleXU=0 Radius=1.5 StartAngle=4.23261 EndAngle=7.37421
    g175: LineSegment StartX=-137.658 StartY=16.5806 StartZ=0 EndX=-135.198 EndY=15.3006 EndZ=0
    g176: LineSegment StartX=-139.042 StartY=13.9194 StartZ=0 EndX=-136.582 EndY=12.6394 EndZ=0
    g177: ArcOfCircle CenterX=-110.49 CenterY=16.51 CenterZ=0 NormalX=0 NormalY=0 NormalZ=1 AngleXU=0 Radius=1.5 StartAngle=5.43511 EndAngle=8.5767
    g178: ArcOfCircle CenterX=-114.3 CenterY=13.15 CenterZ=0 NormalX=0 NormalY=0 NormalZ=1 AngleXU=0 Radius=1.5 StartAngle=2.29352 EndAngle=5.43511
    g179: LineSegment StartX=-109.498 StartY=15.385 StartZ=0 EndX=-113.308 EndY=12.025 EndZ=0
    g180: LineSegment StartX=-111.482 StartY=17.635 StartZ=0 EndX=-115.292 EndY=14.275 EndZ=0
    g181: ArcOfCircle CenterX=-119.3 CenterY=15.25 CenterZ=0 NormalX=0 NormalY=0 NormalZ=1 AngleXU=0 Radius=1.5 StartAngle=1.09102 EndAngle=4.23261
    g182: ArcOfCircle CenterX=-116.84 CenterY=13.97 CenterZ=0 NormalX=0 NormalY=0 NormalZ=1 AngleXU=0 Radius=1.5 StartAngle=4.23261 EndAngle=7.37421
    g183: LineSegment StartX=-118.608 StartY=16.5806 StartZ=0 EndX=-116.148 EndY=15.3006 EndZ=0
    g184: LineSegment StartX=-119.992 StartY=13.9194 StartZ=0 EndX=-117.532 EndY=12.6394 EndZ=0
    g185: ArcOfCircle CenterX=-91.44 CenterY=16.51 CenterZ=0 NormalX=0 NormalY=0 NormalZ=1 AngleXU=0 Radius=1.5 StartAngle=5.43511 EndAngle=8.5767
    g186: ArcOfCircle CenterX=-95.25 CenterY=13.15 CenterZ=0 NormalX=0 NormalY=0 NormalZ=1 AngleXU=0 Radius=1.5 StartAngle=2.29352 EndAngle=5.43511
    g187: LineSegment StartX=-90.4479 StartY=15.385 StartZ=0 EndX=-94.2579 EndY=12.025 EndZ=0
    g188: LineSegment StartX=-92.4321 StartY=17.635 StartZ=0 EndX=-96.2421 EndY=14.275 EndZ=0
    g189: ArcOfCircle CenterX=-100.25 CenterY=15.25 CenterZ=0 NormalX=0 NormalY=0 NormalZ=1 AngleXU=0 Radius=1.5 StartAngle=1.09102 EndAngle=4.23261
    g190: ArcOfCircle CenterX=-97.79 CenterY=13.97 CenterZ=0 NormalX=0 NormalY=0 NormalZ=1 AngleXU=0 Radius=1.5 StartAngle=4.23261 EndAngle=7.37421
    g191: LineSegment StartX=-99.5576 StartY=16.5806 StartZ=0 EndX=-97.0976 EndY=15.3006 EndZ=0
    g192: LineSegment StartX=-100.942 StartY=13.9194 StartZ=0 EndX=-98.4824 EndY=12.6394 EndZ=0
    g193: ArcOfCircle CenterX=-72.39 CenterY=16.51 CenterZ=0 NormalX=0 NormalY=0 NormalZ=1 AngleXU=0 Radius=1.5 StartAngle=5.43511 EndAngle=8.5767
    g194: ArcOfCircle CenterX=-76.2 CenterY=13.15 CenterZ=0 NormalX=0 NormalY=0 NormalZ=1 AngleXU=0 Radius=1.5 StartAngle=2.29352 EndAngle=5.43511
    g195: LineSegment StartX=-71.3979 StartY=15.385 StartZ=0 EndX=-75.2079 EndY=12.025 EndZ=0
    g196: LineSegment StartX=-73.3821 StartY=17.635 StartZ=0 EndX=-77.1921 EndY=14.275 EndZ=0
    g197: ArcOfCircle CenterX=-81.2 CenterY=15.25 CenterZ=0 NormalX=0 NormalY=0 NormalZ=1 AngleXU=0 Radius=1.5 StartAngle=1.09102 EndAngle=4.23261
    g198: ArcOfCircle CenterX=-78.74 CenterY=13.97 CenterZ=0 NormalX=0 NormalY=0 NormalZ=1 AngleXU=0 Radius=1.5 StartAngle=4.23261 EndAngle=7.37421
    g199: LineSegment StartX=-80.5076 StartY=16.5806 StartZ=0 EndX=-78.0476 EndY=15.3006 EndZ=0
    g200: LineSegment StartX=-81.8924 StartY=13.9194 StartZ=0 EndX=-79.4324 EndY=12.6394 EndZ=0
    g201: ArcOfCircle CenterX=-53.34 CenterY=16.51 CenterZ=0 NormalX=0 NormalY=0 NormalZ=1 AngleXU=0 Radius=1.5 StartAngle=5.43511 EndAngle=8.5767
    g202: ArcOfCircle CenterX=-57.15 CenterY=13.15 CenterZ=0 NormalX=0 NormalY=0 NormalZ=1 AngleXU=0 Radius=1.5 StartAngle=2.29352 EndAngle=5.43511
    g203: LineSegment StartX=-52.3479 StartY=15.385 StartZ=0 EndX=-56.1579 EndY=12.025 EndZ=0
    g204: LineSegment StartX=-54.3321 StartY=17.635 StartZ=0 EndX=-58.1421 EndY=14.275 EndZ=0
    g205: ArcOfCircle CenterX=-62.15 CenterY=15.25 CenterZ=0 NormalX=0 NormalY=0 NormalZ=1 AngleXU=0 Radius=1.5 StartAngle=1.09102 EndAngle=4.23261
    g206: ArcOfCircle CenterX=-59.69 CenterY=13.97 CenterZ=0 NormalX=0 NormalY=0 NormalZ=1 AngleXU=0 Radius=1.5 StartAngle=4.23261 EndAngle=7.37421
    g207: LineSegment StartX=-61.4576 StartY=16.5806 StartZ=0 EndX=-58.9976 EndY=15.3006 EndZ=0
    g208: LineSegment StartX=-62.8424 StartY=13.9194 StartZ=0 EndX=-60.3824 EndY=12.6394 EndZ=0
    g209: ArcOfCircle CenterX=-34.29 CenterY=16.51 CenterZ=0 NormalX=0 NormalY=0 NormalZ=1 AngleXU=0 Radius=1.5 StartAngle=5.43511 EndAngle=8.5767
    g210: ArcOfCircle CenterX=-38.1 CenterY=13.15 CenterZ=0 NormalX=0 NormalY=0 NormalZ=1 AngleXU=0 Radius=1.5 StartAngle=2.29352 EndAngle=5.43511
    g211: LineSegment StartX=-33.2979 StartY=15.385 StartZ=0 EndX=-37.1079 EndY=12.025 EndZ=0
    g212: LineSegment StartX=-35.2821 StartY=17.635 StartZ=0 EndX=-39.0921 EndY=14.275 EndZ=0
    g213: ArcOfCircle CenterX=-43.1 CenterY=15.25 CenterZ=0 NormalX=0 NormalY=0 NormalZ=1 AngleXU=0 Radius=1.5 StartAngle=1.09102 EndAngle=4.23261
    g214: ArcOfCircle CenterX=-40.64 CenterY=13.97 CenterZ=0 NormalX=0 NormalY=0 NormalZ=1 AngleXU=0 Radius=1.5 StartAngle=4.23261 EndAngle=7.37421
    g215: LineSegment StartX=-42.4076 StartY=16.5806 StartZ=0 EndX=-39.9476 EndY=15.3006 EndZ=0
    g216: LineSegment StartX=-43.7924 StartY=13.9194 StartZ=0 EndX=-41.3324 EndY=12.6394 EndZ=0
    g217: ArcOfCircle CenterX=-15.24 CenterY=16.51 CenterZ=0 NormalX=0 NormalY=0 NormalZ=1 AngleXU=0 Radius=1.5 StartAngle=5.43511 EndAngle=8.5767
    g218: ArcOfCircle CenterX=-19.05 CenterY=13.15 CenterZ=0 NormalX=0 NormalY=0 NormalZ=1 AngleXU=0 Radius=1.5 StartAngle=2.29352 EndAngle=5.43511
    g219: LineSegment StartX=-14.2479 StartY=15.385 StartZ=0 EndX=-18.0579 EndY=12.025 EndZ=0
    g220: LineSegment StartX=-16.2321 StartY=17.635 StartZ=0 EndX=-20.0421 EndY=14.275 EndZ=0
    g221: ArcOfCircle CenterX=-24.05 CenterY=15.25 CenterZ=0 NormalX=0 NormalY=0 NormalZ=1 AngleXU=0 Radius=1.5 StartAngle=1.09102 EndAngle=4.23261
    g222: ArcOfCircle CenterX=-21.59 CenterY=13.97 CenterZ=0 NormalX=0 NormalY=0 NormalZ=1 AngleXU=0 Radius=1.5 StartAngle=4.23261 EndAngle=7.37421
    g223: LineSegment StartX=-23.3576 StartY=16.5806 StartZ=0 EndX=-20.8976 EndY=15.3006 EndZ=0
    g224: LineSegment StartX=-24.7424 StartY=13.9194 StartZ=0 EndX=-22.2824 EndY=12.6394 EndZ=0
    g225: GeomPoint X=-19.05 Y=19.05 Z=0
    g226: GeomPoint [constr] X=-19.05 Y=13.15 Z=0
    g227: GeomPoint [constr] X=-133.35 Y=70.3 Z=0
    g228: GeomPoint [constr] X=-38.1 Y=70.3 Z=0
  constraints (530):
    c: DistanceX(g1,g0) = 19.05
    c: DistanceX(g2,g1) = 19.05
    c: DistanceX(g3,g2) = 19.05
    c: DistanceX(g4,g3) = 19.05
    c: DistanceY(g10,g5) = 19.05
    c: DistanceY(g5,g20) = 19.05
    c: DistanceX(g23,g4) = 19.05
    c: DistanceX(g0,g24) = 19.05
    c: DistanceX(g24,g-1) = 19.05
    c: Horizontal(g17,g18)
    c: Horizontal(g18,g15)
    c: Horizontal(g15,g19)
    c: Horizontal(g19,g16)
    c: Horizontal(g16,g20)
    c: Horizontal(g21,g9)
    c: Horizontal(g9,g8)
    c: Horizontal(g8,g7)
    c: Horizontal(g7,g6)
    c: Horizontal(g6,g5)
    c: Horizontal(g22,g14)
    c: Horizontal(g14,g13)
    c: Horizontal(g13,g12)
    c: Horizontal(g12,g11)
    c: Horizontal(g11,g10)
    c: Vertical(g17,g21)
    c: Vertical(g21,g22)
    c: Vertical(g22,g23)
    c: Vertical(g18,g9)
    c: Vertical(g9,g14)
    c: Vertical(g14,g4)
    c: Vertical(g15,g8)
    c: Vertical(g8,g13)
    c: Vertical(g13,g3)
    c: Vertical(g19,g7)
    c: Vertical(g7,g12)
    c: Vertical(g12,g2)
    c: Vertical(g16,g6)
    c: Vertical(g6,g11)
    c: Vertical(g11,g1)
    c: Vertical(g20,g5)
    c: Vertical(g5,g10)
    c: Vertical(g10,g0)
    c: Horizontal(g23,g4)
    c: Horizontal(g4,g3)
    c: Horizontal(g3,g2)
    c: Horizontal(g2,g1)
    c: Horizontal(g1,g0)
    c: Horizontal(g0,g24)
    c: Tangent(g25,g27) = 1.5708
    c: Tangent(g25,g28) = -1.5708
    c: Tangent(g26,g27) = 1.5708
    c: Tangent(g26,g28) = -1.5708
    c: Equal(g25,g26)
    c: Tangent(g29,g31) = 1.5708
    c: Tangent(g29,g32) = -1.5708
    c: Tangent(g30,g31) = 1.5708
    c: Tangent(g30,g32) = -1.5708
    c: Equal(g29,g30)
    c: Tangent(g33,g35) = 1.5708
    c: Tangent(g33,g36) = -1.5708
    c: Tangent(g34,g35) = 1.5708
    c: Tangent(g34,g36) = -1.5708
    c: Equal(g33,g34)
    c: Tangent(g37,g39) = 1.5708
    c: Tangent(g37,g40) = -1.5708
    c: Tangent(g38,g39) = 1.5708
    c: Tangent(g38,g40) = -1.5708
    c: Equal(g37,g38)
    c: Tangent(g41,g43) = 1.5708
    c: Tangent(g41,g44) = -1.5708
    c: Tangent(g42,g43) = 1.5708
    c: Tangent(g42,g44) = -1.5708
    c: Equal(g41,g42)
    c: Tangent(g45,g47) = 1.5708
    c: Tangent(g45,g48) = -1.5708
    c: Tangent(g46,g47) = 1.5708
    c: Tangent(g46,g48) = -1.5708
    c: Equal(g45,g46)
    c: Tangent(g49,g51) = 1.5708
    c: Tangent(g49,g52) = -1.5708
    c: Tangent(g50,g51) = 1.5708
    c: Tangent(g50,g52) = -1.5708
    c: Equal(g49,g50)
    c: Tangent(g53,g55) = 1.5708
    c: Tangent(g53,g56) = -1.5708
    c: Tangent(g54,g55) = 1.5708
    c: Tangent(g54,g56) = -1.5708
    c: Equal(g53,g54)
    c: Tangent(g57,g59) = 1.5708
    c: Tangent(g57,g60) = -1.5708
    c: Tangent(g58,g59) = 1.5708
    c: Tangent(g58,g60) = -1.5708
    c: Equal(g57,g58)
    c: Tangent(g61,g63) = 1.5708
    c: Tangent(g61,g64) = -1.5708
    c: Tangent(g62,g63) = 1.5708
    c: Tangent(g62,g64) = -1.5708
    c: Equal(g61,g62)
    c: Tangent(g65,g67) = 1.5708
    c: Tangent(g65,g68) = -1.5708
    c: Tangent(g66,g67) = 1.5708
    c: Tangent(g66,g68) = -1.5708
    c: Equal(g65,g66)
    c: Tangent(g69,g71) = 1.5708
    c: Tangent(g69,g72) = -1.5708
    c: Tangent(g70,g71) = 1.5708
    c: Tangent(g70,g72) = -1.5708
    c: Equal(g69,g70)
    c: DistanceY(g70,g69) = 1.28
    c: DistanceY(g66,g70) = 0.82
    c: DistanceY(g69,g65) = 1.26
    c: Tangent(g73,g75) = 1.5708
    c: Tangent(g73,g76) = -1.5708
    c: Tangent(g74,g75) = 1.5708
    c: Tangent(g74,g76) = -1.5708
    c: Equal(g73,g74)
    c: Tangent(g77,g79) = 1.5708
    c: Tangent(g77,g80) = -1.5708
    c: Tangent(g78,g79) = 1.5708
    c: Tangent(g78,g80) = -1.5708
    c: Equal(g77,g78)
    c: Tangent(g81,g83) = 1.5708
    c: Tangent(g81,g84) = -1.5708
    c: Tangent(g82,g83) = 1.5708
    c: Tangent(g82,g84) = -1.5708
    c: Equal(g81,g82)
    c: Tangent(g85,g87) = 1.5708
    c: Tangent(g85,g88) = -1.5708
    c: Tangent(g86,g87) = 1.5708
    c: Tangent(g86,g88) = -1.5708
    c: Equal(g85,g86)
    c: Tangent(g89,g91) = 1.5708
    c: Tangent(g89,g92) = -1.5708
    c: Tangent(g90,g91) = 1.5708
    c: Tangent(g90,g92) = -1.5708
    c: Equal(g89,g90)
    c: Tangent(g93,g95) = 1.5708
    c: Tangent(g93,g96) = -1.5708
    c: Tangent(g94,g95) = 1.5708
    c: Tangent(g94,g96) = -1.5708
    c: Equal(g93,g94)
    c: Tangent(g97,g99) = 1.5708
    c: Tangent(g97,g100) = -1.5708
    c: Tangent(g98,g99) = 1.5708
    c: Tangent(g98,g100) = -1.5708
    c: Equal(g97,g98)
    c: Tangent(g101,g103) = 1.5708
    c: Tangent(g101,g104) = -1.5708
    c: Tangent(g102,g103) = 1.5708
    c: Tangent(g102,g104) = -1.5708
    c: Equal(g101,g102)
    c: Tangent(g105,g107) = 1.5708
    c: Tangent(g105,g108) = -1.5708
    c: Tangent(g106,g107) = 1.5708
    c: Tangent(g106,g108) = -1.5708
    c: Equal(g105,g106)
    c: Tangent(g109,g111) = 1.5708
    c: Tangent(g109,g112) = -1.5708
    c: Tangent(g110,g111) = 1.5708
    c: Tangent(g110,g112) = -1.5708
    c: Equal(g109,g110)
    c: Tangent(g113,g115) = 1.5708
    c: Tangent(g113,g116) = -1.5708
    c: Tangent(g114,g115) = 1.5708
    c: Tangent(g114,g116) = -1.5708
    c: Equal(g113,g114)
    c: Tangent(g117,g119) = 1.5708
    c: Tangent(g117,g120) = -1.5708
    c: Tangent(g118,g119) = 1.5708
    c: Tangent(g118,g120) = -1.5708
    c: Equal(g117,g118)
    c: DistanceY(g118,g117) = 1.28
    c: DistanceY(g114,g118) = 0.82
    c: DistanceY(g117,g113) = 1.26
    c: Tangent(g121,g123) = 1.5708
    c: Tangent(g121,g124) = -1.5708
    c: Tangent(g122,g123) = 1.5708
    c: Tangent(g122,g124) = -1.5708
    c: Equal(g121,g122)
    c: Tangent(g125,g127) = 1.5708
    c: Tangent(g125,g128) = -1.5708
    c: Tangent(g126,g127) = 1.5708
    c: Tangent(g126,g128) = -1.5708
    c: Equal(g125,g126)
    c: Tangent(g129,g131) = 1.5708
    c: Tangent(g129,g132) = -1.5708
    c: Tangent(g130,g131) = 1.5708
    c: Tangent(g130,g132) = -1.5708
    c: Equal(g129,g130)
    c: Tangent(g133,g135) = 1.5708
    c: Tangent(g133,g136) = -1.5708
    c: Tangent(g134,g135) = 1.5708
    c: Tangent(g134,g136) = -1.5708
    c: Equal(g133,g134)
    c: Tangent(g137,g139) = 1.5708
    c: Tangent(g137,g140) = -1.5708
    c: Tangent(g138,g139) = 1.5708
    c: Tangent(g138,g140) = -1.5708
    c: Equal(g137,g138)
    c: Tangent(g141,g143) = 1.5708
    c: Tangent(g141,g144) = -1.5708
    c: Tangent(g142,g143) = 1.5708
    c: Tangent(g142,g144) = -1.5708
    c: Equal(g141,g142)
    c: Tangent(g145,g147) = 1.5708
    c: Tangent(g145,g148) = -1.5708
    c: Tangent(g146,g147) = 1.5708
    c: Tangent(g146,g148) = -1.5708
    c: Equal(g145,g146)
    c: Tangent(g149,g151) = 1.5708
    c: Tangent(g149,g152) = -1.5708
    c: Tangent(g150,g151) = 1.5708
    c: Tangent(g150,g152) = -1.5708
    c: Equal(g149,g150)
    c: Tangent(g153,g155) = 1.5708
    c: Tangent(g153,g156) = -1.5708
    c: Tangent(g154,g155) = 1.5708
    c: Tangent(g154,g156) = -1.5708
    c: Equal(g153,g154)
    c: Tangent(g157,g159) = 1.5708
    c: Tangent(g157,g160) = -1.5708
    c: Tangent(g158,g159) = 1.5708
    c: Tangent(g158,g160) = -1.5708
    c: Equal(g157,g158)
    c: Tangent(g161,g163) = 1.5708
    c: Tangent(g161,g164) = -1.5708
    c: Tangent(g162,g163) = 1.5708
    c: Tangent(g162,g164) = -1.5708
    c: Equal(g161,g162)
    c: Tangent(g165,g167) = 1.5708
    c: Tangent(g165,g168) = -1.5708
    c: Tangent(g166,g167) = 1.5708
    c: Tangent(g166,g168) = -1.5708
    c: Equal(g165,g166)
    c: DistanceY(g166,g165) = 1.28
    c: DistanceY(g162,g166) = 0.82
    c: DistanceY(g165,g161) = 1.26
    c: Tangent(g169,g171) = 1.5708
    c: Tangent(g169,g172) = -1.5708
    c: Tangent(g170,g171) = 1.5708
    c: Tangent(g170,g172) = -1.5708
    c: Equal(g169,g170)
    c: Tangent(g173,g175) = 1.5708
    c: Tangent(g173,g176) = -1.5708
    c: Tangent(g174,g175) = 1.5708
    c: Tangent(g174,g176) = -1.5708
    c: Equal(g173,g174)
    c: DistanceX(g173,g174) = 2.46
    c: DistanceX(g174,g170) = 2.54
    c: DistanceX(g170,g169) = 3.81
    c: Tangent(g177,g179) = 1.5708
    c: Tangent(g177,g180) = -1.5708
    c: Tangent(g178,g179) = 1.5708
    c: Tangent(g178,g180) = -1.5708
    c: Equal(g177,g178)
    c: Tangent(g181,g183) = 1.5708
    c: Tangent(g181,g184) = -1.5708
    c: Tangent(g182,g183) = 1.5708
    c: Tangent(g182,g184) = -1.5708
    c: Equal(g181,g182)
    c: DistanceX(g181,g182) = 2.46
    c: DistanceX(g182,g178) = 2.54
    c: DistanceX(g178,g177) = 3.81
    c: Tangent(g185,g187) = 1.5708
    c: Tangent(g185,g188) = -1.5708
    c: Tangent(g186,g187) = 1.5708
    c: Tangent(g186,g188) = -1.5708
    c: Equal(g185,g186)
    c: Tangent(g189,g191) = 1.5708
    c: Tangent(g189,g192) = -1.5708
    c: Tangent(g190,g191) = 1.5708
    c: Tangent(g190,g192) = -1.5708
    c: Equal(g189,g190)
    c: DistanceX(g189,g190) = 2.46
    c: DistanceX(g190,g186) = 2.54
    c: DistanceX(g186,g185) = 3.81
    c: Tangent(g193,g195) = 1.5708
    c: Tangent(g193,g196) = -1.5708
    c: Tangent(g194,g195) = 1.5708
    c: Tangent(g194,g196) = -1.5708
    c: Equal(g193,g194)
    c: Tangent(g197,g199) = 1.5708
    c: Tangent(g197,g200) = -1.5708
    c: Tangent(g198,g199) = 1.5708
    c: Tangent(g198,g200) = -1.5708
    c: Equal(g197,g198)
    c: DistanceX(g197,g198) = 2.46
    c: DistanceX(g198,g194) = 2.54
    c: DistanceX(g194,g193) = 3.81
    c: Tangent(g201,g203) = 1.5708
    c: Tangent(g201,g204) = -1.5708
    c: Tangent(g202,g203) = 1.5708
    c: Tangent(g202,g204) = -1.5708
    c: Equal(g201,g202)
    c: Tangent(g205,g207) = 1.5708
    c: Tangent(g205,g208) = -1.5708
    c: Tangent(g206,g207) = 1.5708
    c: Tangent(g206,g208) = -1.5708
    c: Equal(g205,g206)
    c: DistanceX(g205,g206) = 2.46
    c: DistanceX(g206,g202) = 2.54
    c: DistanceX(g202,g201) = 3.81
    c: Tangent(g209,g211) = 1.5708
    c: Tangent(g209,g212) = -1.5708
    c: Tangent(g210,g211) = 1.5708
    c: Tangent(g210,g212) = -1.5708
    c: Equal(g209,g210)
    c: Tangent(g213,g215) = 1.5708
    c: Tangent(g213,g216) = -1.5708
    c: Tangent(g214,g215) = 1.5708
    c: Tangent(g214,g216) = -1.5708
    c: Equal(g213,g214)
    c: DistanceX(g213,g214) = 2.46
    c: DistanceX(g214,g210) = 2.54
    c: DistanceX(g210,g209) = 3.81
    c: Tangent(g217,g219) = 1.5708
    c: Tangent(g217,g220) = -1.5708
    c: Tangent(g218,g219) = 1.5708
    c: Tangent(g218,g220) = -1.5708
    c: Equal(g217,g218)
    c: Tangent(g221,g223) = 1.5708
    c: Tangent(g221,g224) = -1.5708
    c: Tangent(g222,g223) = 1.5708
    c: Tangent(g222,g224) = -1.5708
    c: Equal(g221,g222)
    c: DistanceX(g221,g222) = 2.46
    c: DistanceX(g222,g218) = 2.54
    c: DistanceX(g218,g217) = 3.81
    c: DistanceY(g222,g221) = 1.28
    c: DistanceY(g221,g217) = 1.26
    c: Coincident(g26,g17)
    c: Coincident(g34,g18)
    c: Coincident(g42,g15)
    c: Coincident(g50,g19)
    c: Coincident(g58,g16)
    c: Coincident(g66,g20)
    c: Coincident(g74,g21)
    c: Coincident(g82,g9)
    c: Coincident(g90,g8)
    c: Coincident(g98,g7)
    c: Coincident(g106,g6)
    c: Coincident(g114,g5)
    c: Coincident(g122,g22)
    c: Coincident(g130,g14)
    c: Coincident(g138,g13)
    c: Coincident(g146,g12)
    c: Coincident(g154,g11)
    c: Coincident(g162,g10)
    c: Coincident(g170,g23)
    c: Coincident(g178,g4)
    c: Coincident(g186,g3)
    c: Coincident(g194,g2)
    c: Coincident(g202,g1)
    c: Coincident(g210,g0)
    c: Coincident(g218,g24)
    c: Equal(g30,g26)
    c: Equal(g38,g34)
    c: Equal(g46,g42)
    c: Equal(g54,g50)
    c: Equal(g62,g58)
    c: Equal(g70,g66)
    c: Equal(g78,g74)
    c: Equal(g86,g82)
    c: Equal(g94,g90)
    c: Equal(g102,g98)
    c: Equal(g110,g106)
    c: Equal(g118,g114)
    c: Equal(g126,g122)
    c: Equal(g134,g130)
    c: Equal(g142,g138)
    c: Equal(g150,g146)
    c: Equal(g158,g154)
    c: Equal(g166,g162)
    c: Equal(g174,g170)
    c: Equal(g182,g178)
    c: Equal(g190,g186)
    c: Equal(g198,g194)
    c: Equal(g206,g202)
    c: Equal(g214,g210)
    c: Equal(g222,g218)
    c: Equal(g26,g34)
    c: Equal(g34,g42)
    c: Equal(g42,g50)
    c: Equal(g50,g58)
    c: Equal(g58,g66)
    c: Equal(g74,g82)
    c: Equal(g82,g90)
    c: Equal(g90,g98)
    c: Equal(g98,g106)
    c: Equal(g106,g114)
    c: Equal(g122,g130)
    c: Equal(g130,g138)
    c: Equal(g138,g146)
    c: Equal(g146,g154)
    c: Equal(g154,g162)
    c: Equal(g170,g178)
    c: Equal(g178,g186)
    c: Equal(g186,g194)
    c: Equal(g194,g202)
    c: Equal(g202,g210)
    c: Equal(g210,g218)
    c: Diameter(g218) = 3
    c: Equal(g66,g114)
    c: Equal(g114,g162)
    c: Equal(g162,g210)
    c: Vertical(g29,g77)
    c: Vertical(g77,g125)
    c: Vertical(g125,g173)
    c: Vertical(g30,g78)
    c: Vertical(g78,g126)
    c: Vertical(g126,g174)
    c: Vertical(g25,g73)
    c: Vertical(g73,g121)
    c: Vertical(g121,g169)
    c: Vertical(g37,g85)
    c: Vertical(g85,g133)
    c: Vertical(g133,g181)
    c: Vertical(g38,g86)
    c: Vertical(g86,g134)
    c: Vertical(g134,g182)
    c: Vertical(g33,g81)
    c: Vertical(g81,g129)
    c: Vertical(g129,g177)
    c: Vertical(g45,g93)
    c: Vertical(g93,g141)
    c: Vertical(g141,g189)
    c: Vertical(g46,g94)
    c: Vertical(g94,g142)
    c: Vertical(g142,g190)
    c: Vertical(g41,g89)
    c: Vertical(g89,g137)
    c: Vertical(g137,g185)
    c: Vertical(g53,g101)
    c: Vertical(g101,g149)
    c: Vertical(g149,g197)
    c: Vertical(g54,g102)
    c: Vertical(g102,g150)
    c: Vertical(g150,g198)
    c: Vertical(g49,g97)
    c: Vertical(g97,g145)
    c: Vertical(g145,g193)
    c: Vertical(g61,g109)
    c: Vertical(g109,g157)
    c: Vertical(g157,g205)
    c: Vertical(g62,g110)
    c: Vertical(g110,g158)
    c: Vertical(g158,g206)
    c: Vertical(g57,g105)
    c: Vertical(g105,g153)
    c: Vertical(g153,g201)
    c: Vertical(g69,g117)
    c: Vertical(g117,g165)
    c: Vertical(g165,g213)
    c: Vertical(g70,g118)
    c: Vertical(g118,g166)
    c: Vertical(g166,g214)
    c: Vertical(g65,g113)
    c: Vertical(g113,g161)
    c: Vertical(g161,g209)
    c: Horizontal(g25,g33)
    c: Horizontal(g33,g41)
    c: Horizontal(g41,g49)
    c: Horizontal(g49,g57)
    c: Horizontal(g57,g65)
    c: Horizontal(g29,g37)
    c: Horizontal(g37,g45)
    c: Horizontal(g45,g53)
    c: Horizontal(g53,g61)
    c: Horizontal(g61,g69)
    c: Horizontal(g30,g38)
    c: Horizontal(g38,g46)
    c: Horizontal(g46,g54)
    c: Horizontal(g54,g62)
    c: Horizontal(g62,g70)
    c: Horizontal(g73,g81)
    c: Horizontal(g81,g89)
    c: Horizontal(g89,g97)
    c: Horizontal(g97,g105)
    c: Horizontal(g105,g113)
    c: Horizontal(g77,g85)
    c: Horizontal(g85,g93)
    c: Horizontal(g93,g101)
    c: Horizontal(g101,g109)
    c: Horizontal(g109,g117)
    c: Horizontal(g78,g86)
    c: Horizontal(g86,g94)
    c: Horizontal(g94,g102)
    c: Horizontal(g102,g110)
    c: Horizontal(g110,g118)
    c: Horizontal(g121,g129)
    c: Horizontal(g129,g137)
    c: Horizontal(g137,g145)
    c: Horizontal(g145,g153)
    c: Horizontal(g153,g161)
    c: Horizontal(g125,g133)
    c: Horizontal(g133,g141)
    c: Horizontal(g141,g149)
    c: Horizontal(g149,g157)
    c: Horizontal(g157,g165)
    c: Horizontal(g126,g134)
    c: Horizontal(g134,g142)
    c: Horizontal(g142,g150)
    c: Horizontal(g150,g158)
    c: Horizontal(g158,g166)
    c: Horizontal(g169,g177)
    c: Horizontal(g177,g185)
    c: Horizontal(g185,g193)
    c: Horizontal(g193,g201)
    c: Horizontal(g201,g209)
    c: Horizontal(g209,g217)
    c: Horizontal(g173,g181)
    c: Horizontal(g181,g189)
    c: Horizontal(g189,g197)
    c: Horizontal(g197,g205)
    c: Horizontal(g205,g213)
    c: Horizontal(g213,g221)
    c: Horizontal(g174,g182)
    c: Horizontal(g182,g190)
    c: Horizontal(g190,g198)
    c: Horizontal(g198,g206)
    c: Horizontal(g206,g214)
    c: Horizontal(g214,g222)
    c: DistanceY(g24,g222) = 0.82
    c: DistanceY(g24,g10) = 19.05
    c: DistanceX(g225,g-1) = 19.05
    c: DistanceY(g-1,g225) = 19.05
    c: DistanceY(g24,g225) = 5.9
    c: Coincident(g228,g20)
    c: Coincident(g226,g24)
    c: Coincident(g227,g17)
FEATURE [Sketcher::SketchObject] Sketch022  label="BL-LED"
  ArcFitTolerance = 1e-06
  AttachmentSupport = -> [XY_Plane001]
  FullyConstrained = true
  MakeInternals = false
  MapMode = 5
  expr: Constraints[20] = VarSet.Bottom_LedY
  expr: Constraints[21] = VarSet.Bottom_LedX
  sketch-geometry (126):
    g0: GeomPoint X=-19.05 Y=19.05 Z=0
    g1: LineSegment StartX=-137.35 StartY=82.5 StartZ=0 EndX=-137.35 EndY=79.3 EndZ=0
    g2: LineSegment StartX=-137.35 StartY=79.3 StartZ=0 EndX=-129.35 EndY=79.3 EndZ=0
    g3: LineSegment StartX=-129.35 StartY=79.3 StartZ=0 EndX=-129.35 EndY=82.5 EndZ=0
    g4: LineSegment StartX=-129.35 StartY=82.5 StartZ=0 EndX=-137.35 EndY=82.5 EndZ=0
    g5: GeomPoint [constr] X=-133.35 Y=80.9 Z=0
    g6: LineSegment StartX=-23.05 StartY=25.35 StartZ=0 EndX=-23.05 EndY=22.15 EndZ=0
    g7: LineSegment StartX=-23.05 StartY=22.15 StartZ=0 EndX=-15.05 EndY=22.15 EndZ=0
    g8: LineSegment StartX=-15.05 StartY=22.15 StartZ=0 EndX=-15.05 EndY=25.35 EndZ=0
    g9: LineSegment StartX=-15.05 StartY=25.35 StartZ=0 EndX=-23.05 EndY=25.35 EndZ=0
    g10: GeomPoint [constr] X=-19.05 Y=23.75 Z=0
    g11: LineSegment StartX=-118.3 StartY=82.5 StartZ=0 EndX=-118.3 EndY=79.3 EndZ=0
    g12: LineSegment StartX=-118.3 StartY=79.3 StartZ=0 EndX=-110.3 EndY=79.3 EndZ=0
    g13: LineSegment StartX=-110.3 StartY=79.3 StartZ=0 EndX=-110.3 EndY=82.5 EndZ=0
    g14: LineSegment StartX=-110.3 StartY=82.5 StartZ=0 EndX=-118.3 EndY=82.5 EndZ=0
    g15: GeomPoint [constr] X=-114.3 Y=80.9 Z=0
    g16: LineSegment StartX=-99.25 StartY=82.5 StartZ=0 EndX=-99.25 EndY=79.3 EndZ=0
    g17: LineSegment StartX=-99.25 StartY=79.3 StartZ=0 EndX=-91.25 EndY=79.3 EndZ=0
    g18: LineSegment StartX=-91.25 StartY=79.3 StartZ=0 EndX=-91.25 EndY=82.5 EndZ=0
    g19: LineSegment StartX=-91.25 StartY=82.5 StartZ=0 EndX=-99.25 EndY=82.5 EndZ=0
    g20: GeomPoint [constr] X=-95.25 Y=80.9 Z=0
    g21: LineSegment StartX=-80.2 StartY=82.5 StartZ=0 EndX=-80.2 EndY=79.3 EndZ=0
    g22: LineSegment StartX=-80.2 StartY=79.3 StartZ=0 EndX=-72.2 EndY=79.3 EndZ=0
    g23: LineSegment StartX=-72.2 StartY=79.3 StartZ=0 EndX=-72.2 EndY=82.5 EndZ=0
    g24: LineSegment StartX=-72.2 StartY=82.5 StartZ=0 EndX=-80.2 EndY=82.5 EndZ=0
    g25: GeomPoint [constr] X=-76.2 Y=80.9 Z=0
    g26: LineSegment StartX=-61.15 StartY=82.5 StartZ=0 EndX=-61.15 EndY=79.3 EndZ=0
    g27: LineSegment StartX=-61.15 StartY=79.3 StartZ=0 EndX=-53.15 EndY=79.3 EndZ=0
    g28: LineSegment StartX=-53.15 StartY=79.3 StartZ=0 EndX=-53.15 EndY=82.5 EndZ=0
    g29: LineSegment StartX=-53.15 StartY=82.5 StartZ=0 EndX=-61.15 EndY=82.5 EndZ=0
    g30: GeomPoint [constr] X=-57.15 Y=80.9 Z=0
    g31: LineSegment StartX=-42.1 StartY=82.5 StartZ=0 EndX=-42.1 EndY=79.3 EndZ=0
    g32: LineSegment StartX=-42.1 StartY=79.3 StartZ=0 EndX=-34.1 EndY=79.3 EndZ=0
    g33: LineSegment StartX=-34.1 StartY=79.3 StartZ=0 EndX=-34.1 EndY=82.5 EndZ=0
    g34: LineSegment StartX=-34.1 StartY=82.5 StartZ=0 EndX=-42.1 EndY=82.5 EndZ=0
    g35: GeomPoint [constr] X=-38.1 Y=80.9 Z=0
    g36: LineSegment StartX=-137.35 StartY=63.45 StartZ=0 EndX=-137.35 EndY=60.25 EndZ=0
    g37: LineSegment StartX=-137.35 StartY=60.25 StartZ=0 EndX=-129.35 EndY=60.25 EndZ=0
    g38: LineSegment StartX=-129.35 StartY=60.25 StartZ=0 EndX=-129.35 EndY=63.45 EndZ=0
    g39: LineSegment StartX=-129.35 StartY=63.45 StartZ=0 EndX=-137.35 EndY=63.45 EndZ=0
    g40: GeomPoint [constr] X=-133.35 Y=61.85 Z=0
    g41: LineSegment StartX=-118.3 StartY=63.45 StartZ=0 EndX=-118.3 EndY=60.25 EndZ=0
    g42: LineSegment StartX=-118.3 StartY=60.25 StartZ=0 EndX=-110.3 EndY=60.25 EndZ=0
    g43: LineSegment StartX=-110.3 StartY=60.25 StartZ=0 EndX=-110.3 EndY=63.45 EndZ=0
    g44: LineSegment StartX=-110.3 StartY=63.45 StartZ=0 EndX=-118.3 EndY=63.45 EndZ=0
    g45: GeomPoint [constr] X=-114.3 Y=61.85 Z=0
    g46: LineSegment StartX=-99.25 StartY=63.45 StartZ=0 EndX=-99.25 EndY=60.25 EndZ=0
    g47: LineSegment StartX=-99.25 StartY=60.25 StartZ=0 EndX=-91.25 EndY=60.25 EndZ=0
    g48: LineSegment StartX=-91.25 StartY=60.25 StartZ=0 EndX=-91.25 EndY=63.45 EndZ=0
    g49: LineSegment StartX=-91.25 StartY=63.45 StartZ=0 EndX=-99.25 EndY=63.45 EndZ=0
    g50: GeomPoint [constr] X=-95.25 Y=61.85 Z=0
    g51: LineSegment StartX=-80.2 StartY=63.45 StartZ=0 EndX=-80.2 EndY=60.25 EndZ=0
    g52: LineSegment StartX=-80.2 StartY=60.25 StartZ=0 EndX=-72.2 EndY=60.25 EndZ=0
    g53: LineSegment StartX=-72.2 StartY=60.25 StartZ=0 EndX=-72.2 EndY=63.45 EndZ=0
    g54: LineSegment StartX=-72.2 StartY=63.45 StartZ=0 EndX=-80.2 EndY=63.45 EndZ=0
    g55: GeomPoint [constr] X=-76.2 Y=61.85 Z=0
    g56: LineSegment StartX=-61.15 StartY=63.45 StartZ=0 EndX=-61.15 EndY=60.25 EndZ=0
    g57: LineSegment StartX=-61.15 StartY=60.25 StartZ=0 EndX=-53.15 EndY=60.25 EndZ=0
    g58: LineSegment StartX=-53.15 StartY=60.25 StartZ=0 EndX=-53.15 EndY=63.45 EndZ=0
    g59: LineSegment StartX=-53.15 StartY=63.45 StartZ=0 EndX=-61.15 EndY=63.45 EndZ=0
    g60: GeomPoint [constr] X=-57.15 Y=61.85 Z=0
    g61: LineSegment StartX=-42.1 StartY=63.45 StartZ=0 EndX=-42.1 EndY=60.25 EndZ=0
    g62: LineSegment StartX=-42.1 StartY=60.25 StartZ=0 EndX=-34.1 EndY=60.25 EndZ=0
    g63: LineSegment StartX=-34.1 StartY=60.25 StartZ=0 EndX=-34.1 EndY=63.45 EndZ=0
    g64: LineSegment StartX=-34.1 StartY=63.45 StartZ=0 EndX=-42.1 EndY=63.45 EndZ=0
    g65: GeomPoint [constr] X=-38.1 Y=61.85 Z=0
    g66: LineSegment StartX=-137.35 StartY=44.4 StartZ=0 EndX=-137.35 EndY=41.2 EndZ=0
    g67: LineSegment StartX=-137.35 StartY=41.2 StartZ=0 EndX=-129.35 EndY=41.2 EndZ=0
    g68: LineSegment StartX=-129.35 StartY=41.2 StartZ=0 EndX=-129.35 EndY=44.4 EndZ=0
    g69: LineSegment StartX=-129.35 StartY=44.4 StartZ=0 EndX=-137.35 EndY=44.4 EndZ=0
    g70: GeomPoint [constr] X=-133.35 Y=42.8 Z=0
    g71: LineSegment StartX=-118.3 StartY=44.4 StartZ=0 EndX=-118.3 EndY=41.2 EndZ=0
    g72: LineSegment StartX=-118.3 StartY=41.2 StartZ=0 EndX=-110.3 EndY=41.2 EndZ=0
    g73: LineSegment StartX=-110.3 StartY=41.2 StartZ=0 EndX=-110.3 EndY=44.4 EndZ=0
    g74: LineSegment StartX=-110.3 StartY=44.4 StartZ=0 EndX=-118.3 EndY=44.4 EndZ=0
    g75: GeomPoint [constr] X=-114.3 Y=42.8 Z=0
    g76: LineSegment StartX=-99.25 StartY=44.4 StartZ=0 EndX=-99.25 EndY=41.2 EndZ=0
    g77: LineSegment StartX=-99.25 StartY=41.2 StartZ=0 EndX=-91.25 EndY=41.2 EndZ=0
    g78: LineSegment StartX=-91.25 StartY=41.2 StartZ=0 EndX=-91.25 EndY=44.4 EndZ=0
    g79: LineSegment StartX=-91.25 StartY=44.4 StartZ=0 EndX=-99.25 EndY=44.4 EndZ=0
    g80: GeomPoint [constr] X=-95.25 Y=42.8 Z=0
    g81: LineSegment StartX=-80.2 StartY=44.4 StartZ=0 EndX=-80.2 EndY=41.2 EndZ=0
    g82: LineSegment StartX=-80.2 StartY=41.2 StartZ=0 EndX=-72.2 EndY=41.2 EndZ=0
    g83: LineSegment StartX=-72.2 StartY=41.2 StartZ=0 EndX=-72.2 EndY=44.4 EndZ=0
    g84: LineSegment StartX=-72.2 StartY=44.4 StartZ=0 EndX=-80.2 EndY=44.4 EndZ=0
    g85: GeomPoint [constr] X=-76.2 Y=42.8 Z=0
    g86: LineSegment StartX=-61.15 StartY=44.4 StartZ=0 EndX=-61.15 EndY=41.2 EndZ=0
    g87: LineSegment StartX=-61.15 StartY=41.2 StartZ=0 EndX=-53.15 EndY=41.2 EndZ=0
    g88: LineSegment StartX=-53.15 StartY=41.2 StartZ=0 EndX=-53.15 EndY=44.4 EndZ=0
    g89: LineSegment StartX=-53.15 StartY=44.4 StartZ=0 EndX=-61.15 EndY=44.4 EndZ=0
    g90: GeomPoint [constr] X=-57.15 Y=42.8 Z=0
    g91: LineSegment StartX=-42.1 StartY=44.4 StartZ=0 EndX=-42.1 EndY=41.2 EndZ=0
    g92: LineSegment StartX=-42.1 StartY=41.2 StartZ=0 EndX=-34.1 EndY=41.2 EndZ=0
    g93: LineSegment StartX=-34.1 StartY=41.2 StartZ=0 EndX=-34.1 EndY=44.4 EndZ=0
    g94: LineSegment StartX=-34.1 StartY=44.4 StartZ=0 EndX=-42.1 EndY=44.4 EndZ=0
    g95: GeomPoint [constr] X=-38.1 Y=42.8 Z=0
    g96: LineSegment StartX=-137.35 StartY=25.35 StartZ=0 EndX=-137.35 EndY=22.15 EndZ=0
    g97: LineSegment StartX=-137.35 StartY=22.15 StartZ=0 EndX=-129.35 EndY=22.15 EndZ=0
    g98: LineSegment StartX=-129.35 StartY=22.15 StartZ=0 EndX=-129.35 EndY=25.35 EndZ=0
    g99: LineSegment StartX=-129.35 StartY=25.35 StartZ=0 EndX=-137.35 EndY=25.35 EndZ=0
    g100: GeomPoint [constr] X=-133.35 Y=23.75 Z=0
    g101: LineSegment StartX=-118.3 StartY=25.35 StartZ=0 EndX=-118.3 EndY=22.15 EndZ=0
    g102: LineSegment StartX=-118.3 StartY=22.15 StartZ=0 EndX=-110.3 EndY=22.15 EndZ=0
    g103: LineSegment StartX=-110.3 StartY=22.15 StartZ=0 EndX=-110.3 EndY=25.35 EndZ=0
    g104: LineSegment StartX=-110.3 StartY=25.35 StartZ=0 EndX=-118.3 EndY=25.35 EndZ=0
    g105: GeomPoint [constr] X=-114.3 Y=23.75 Z=0
    g106: LineSegment StartX=-99.25 StartY=25.35 StartZ=0 EndX=-99.25 EndY=22.15 EndZ=0
    g107: LineSegment StartX=-99.25 StartY=22.15 StartZ=0 EndX=-91.25 EndY=22.15 EndZ=0
    g108: LineSegment StartX=-91.25 StartY=22.15 StartZ=0 EndX=-91.25 EndY=25.35 EndZ=0
    g109: LineSegment StartX=-91.25 StartY=25.35 StartZ=0 EndX=-99.25 EndY=25.35 EndZ=0
    g110: GeomPoint [constr] X=-95.25 Y=23.75 Z=0
    g111: LineSegment StartX=-80.2 StartY=25.35 StartZ=0 EndX=-80.2 EndY=22.15 EndZ=0
    g112: LineSegment StartX=-80.2 StartY=22.15 StartZ=0 EndX=-72.2 EndY=22.15 EndZ=0
    g113: LineSegment StartX=-72.2 StartY=22.15 StartZ=0 EndX=-72.2 EndY=25.35 EndZ=0
    g114: LineSegment StartX=-72.2 StartY=25.35 StartZ=0 EndX=-80.2 EndY=25.35 EndZ=0
    g115: GeomPoint [constr] X=-76.2 Y=23.75 Z=0
    g116: LineSegment StartX=-61.15 StartY=25.35 StartZ=0 EndX=-61.15 EndY=22.15 EndZ=0
    g117: LineSegment StartX=-61.15 StartY=22.15 StartZ=0 EndX=-53.15 EndY=22.15 EndZ=0
    g118: LineSegment StartX=-53.15 StartY=22.15 StartZ=0 EndX=-53.15 EndY=25.35 EndZ=0
    g119: LineSegment StartX=-53.15 StartY=25.35 StartZ=0 EndX=-61.15 EndY=25.35 EndZ=0
    g120: GeomPoint [constr] X=-57.15 Y=23.75 Z=0
    g121: LineSegment StartX=-42.1 StartY=25.35 StartZ=0 EndX=-42.1 EndY=22.15 EndZ=0
    g122: LineSegment StartX=-42.1 StartY=22.15 StartZ=0 EndX=-34.1 EndY=22.15 EndZ=0
    g123: LineSegment StartX=-34.1 StartY=22.15 StartZ=0 EndX=-34.1 EndY=25.35 EndZ=0
    g124: LineSegment StartX=-34.1 StartY=25.35 StartZ=0 EndX=-42.1 EndY=25.35 EndZ=0
    g125: GeomPoint [constr] X=-38.1 Y=23.75 Z=0
  constraints (327):
    c: DistanceX(g0,g-1) = 19.05
    c: DistanceY(g-1,g0) = 19.05
    c: Coincident(g1,g2)
    c: Coincident(g2,g3)
    c: Coincident(g3,g4)
    c: Coincident(g4,g1)
    c: Vertical(g1)
    c: Vertical(g3)
    c: Horizontal(g2)
    c: Horizontal(g4)
    c: Symmetric(g3,g1,g5)
    c: Coincident(g6,g7)
    c: Coincident(g7,g8)
    c: Coincident(g8,g9)
    c: Coincident(g9,g6)
    c: Vertical(g6)
    c: Vertical(g8)
    c: Horizontal(g7)
    c: Horizontal(g9)
    c: Symmetric(g8,g6,g10)
    c: DistanceY(g6,g6) = 3.2
    c: DistanceX(g7,g7) = 8
    c: Vertical(g10,g0)
    c: DistanceY(g0,g10) = 4.7
    c: Coincident(g11,g12)
    c: Coincident(g12,g13)
    c: Coincident(g13,g14)
    c: Coincident(g14,g11)
    c: Vertical(g11)
    c: Vertical(g13)
    c: Horizontal(g12)
    c: Horizontal(g14)
    c: Symmetric(g13,g11,g15)
    c: Coincident(g16,g17)
    c: Coincident(g17,g18)
    c: Coincident(g18,g19)
    c: Coincident(g19,g16)
    c: Vertical(g16)
    c: Vertical(g18)
    c: Horizontal(g17)
    c: Horizontal(g19)
    c: Symmetric(g18,g16,g20)
    c: Coincident(g21,g22)
    c: Coincident(g22,g23)
    c: Coincident(g23,g24)
    c: Coincident(g24,g21)
    c: Vertical(g21)
    c: Vertical(g23)
    c: Horizontal(g22)
    c: Horizontal(g24)
    c: Symmetric(g23,g21,g25)
    c: Coincident(g26,g27)
    c: Coincident(g27,g28)
    c: Coincident(g28,g29)
    c: Coincident(g29,g26)
    c: Vertical(g26)
    c: Vertical(g28)
    c: Horizontal(g27)
    c: Horizontal(g29)
    c: Symmetric(g28,g26,g30)
    c: Coincident(g31,g32)
    c: Coincident(g32,g33)
    c: Coincident(g33,g34)
    c: Coincident(g34,g31)
    c: Vertical(g31)
    c: Vertical(g33)
    c: Horizontal(g32)
    c: Horizontal(g34)
    c: Symmetric(g33,g31,g35)
    c: Coincident(g36,g37)
    c: Coincident(g37,g38)
    c: Coincident(g38,g39)
    c: Coincident(g39,g36)
    c: Vertical(g36)
    c: Vertical(g38)
    c: Horizontal(g37)
    c: Horizontal(g39)
    c: Symmetric(g38,g36,g40)
    c: Coincident(g41,g42)
    c: Coincident(g42,g43)
    c: Coincident(g43,g44)
    c: Coincident(g44,g41)
    c: Vertical(g41)
    c: Vertical(g43)
    c: Horizontal(g42)
    c: Horizontal(g44)
    c: Symmetric(g43,g41,g45)
    c: Coincident(g46,g47)
    c: Coincident(g47,g48)
    c: Coincident(g48,g49)
    c: Coincident(g49,g46)
    c: Vertical(g46)
    c: Vertical(g48)
    c: Horizontal(g47)
    c: Horizontal(g49)
    c: Symmetric(g48,g46,g50)
    c: Coincident(g51,g52)
    c: Coincident(g52,g53)
    c: Coincident(g53,g54)
    c: Coincident(g54,g51)
    c: Vertical(g51)
    c: Vertical(g53)
    c: Horizontal(g52)
    c: Horizontal(g54)
    c: Symmetric(g53,g51,g55)
    c: Coincident(g56,g57)
    c: Coincident(g57,g58)
    c: Coincident(g58,g59)
    c: Coincident(g59,g56)
    c: Vertical(g56)
    c: Vertical(g58)
    c: Horizontal(g57)
    c: Horizontal(g59)
    c: Symmetric(g58,g56,g60)
    c: Coincident(g61,g62)
    c: Coincident(g62,g63)
    c: Coincident(g63,g64)
    c: Coincident(g64,g61)
    c: Vertical(g61)
    c: Vertical(g63)
    c: Horizontal(g62)
    c: Horizontal(g64)
    c: Symmetric(g63,g61,g65)
    c: Coincident(g66,g67)
    c: Coincident(g67,g68)
    c: Coincident(g68,g69)
    c: Coincident(g69,g66)
    c: Vertical(g66)
    c: Vertical(g68)
    c: Horizontal(g67)
    c: Horizontal(g69)
    c: Symmetric(g68,g66,g70)
    c: Coincident(g71,g72)
    c: Coincident(g72,g73)
    c: Coincident(g73,g74)
    c: Coincident(g74,g71)
    c: Vertical(g71)
    c: Vertical(g73)
    c: Horizontal(g72)
    c: Horizontal(g74)
    c: Symmetric(g73,g71,g75)
    c: Coincident(g76,g77)
    c: Coincident(g77,g78)
    c: Coincident(g78,g79)
    c: Coincident(g79,g76)
    c: Vertical(g76)
    c: Vertical(g78)
    c: Horizontal(g77)
    c: Horizontal(g79)
    c: Symmetric(g78,g76,g80)
    c: Coincident(g81,g82)
    c: Coincident(g82,g83)
    c: Coincident(g83,g84)
    c: Coincident(g84,g81)
    c: Vertical(g81)
    c: Vertical(g83)
    c: Horizontal(g82)
    c: Horizontal(g84)
    c: Symmetric(g83,g81,g85)
    c: Coincident(g86,g87)
    c: Coincident(g87,g88)
    c: Coincident(g88,g89)
    c: Coincident(g89,g86)
    c: Vertical(g86)
    c: Vertical(g88)
    c: Horizontal(g87)
    c: Horizontal(g89)
    c: Symmetric(g88,g86,g90)
    c: Coincident(g91,g92)
    c: Coincident(g92,g93)
    c: Coincident(g93,g94)
    c: Coincident(g94,g91)
    c: Vertical(g91)
    c: Vertical(g93)
    c: Horizontal(g92)
    c: Horizontal(g94)
    c: Symmetric(g93,g91,g95)
    c: Coincident(g96,g97)
    c: Coincident(g97,g98)
    c: Coincident(g98,g99)
    c: Coincident(g99,g96)
    c: Vertical(g96)
    c: Vertical(g98)
    c: Horizontal(g97)
    c: Horizontal(g99)
    c: Symmetric(g98,g96,g100)
    c: Coincident(g101,g102)
    c: Coincident(g102,g103)
    c: Coincident(g103,g104)
    c: Coincident(g104,g101)
    c: Vertical(g101)
    c: Vertical(g103)
    c: Horizontal(g102)
    c: Horizontal(g104)
    c: Symmetric(g103,g101,g105)
    c: Coincident(g106,g107)
    c: Coincident(g107,g108)
    c: Coincident(g108,g109)
    c: Coincident(g109,g106)
    c: Vertical(g106)
    c: Vertical(g108)
    c: Horizontal(g107)
    c: Horizontal(g109)
    c: Symmetric(g108,g106,g110)
    c: Coincident(g111,g112)
    c: Coincident(g112,g113)
    c: Coincident(g113,g114)
    c: Coincident(g114,g111)
    c: Vertical(g111)
    c: Vertical(g113)
    c: Horizontal(g112)
    c: Horizontal(g114)
    c: Symmetric(g113,g111,g115)
    c: Coincident(g116,g117)
    c: Coincident(g117,g118)
    c: Coincident(g118,g119)
    c: Coincident(g119,g116)
    c: Vertical(g116)
    c: Vertical(g118)
    c: Horizontal(g117)
    c: Horizontal(g119)
    c: Symmetric(g118,g116,g120)
    c: Coincident(g121,g122)
    c: Coincident(g122,g123)
    c: Coincident(g123,g124)
    c: Coincident(g124,g121)
    c: Vertical(g121)
    c: Vertical(g123)
    c: Horizontal(g122)
    c: Horizontal(g124)
    c: Symmetric(g123,g121,g125)
    c: Horizontal(g5,g15)
    c: Horizontal(g15,g20)
    c: Horizontal(g20,g25)
    c: Horizontal(g25,g30)
    c: Horizontal(g30,g35)
    c: Horizontal(g40,g45)
    c: Horizontal(g45,g50)
    c: Horizontal(g50,g55)
    c: Horizontal(g55,g60)
    c: Horizontal(g60,g65)
    c: Horizontal(g70,g75)
    c: Horizontal(g75,g80)
    c: Horizontal(g80,g85)
    c: Horizontal(g85,g90)
    c: Horizontal(g90,g95)
    c: Horizontal(g100,g105)
    c: Horizontal(g105,g110)
    c: Horizontal(g110,g115)
    c: Horizontal(g115,g120)
    c: Horizontal(g120,g125)
    c: Horizontal(g125,g10)
    c: Vertical(g5,g40)
    c: Vertical(g40,g70)
    c: Vertical(g70,g100)
    c: Vertical(g15,g45)
    c: Vertical(g45,g75)
    c: Vertical(g75,g105)
    c: Vertical(g20,g50)
    c: Vertical(g50,g80)
    c: Vertical(g80,g110)
    c: Vertical(g25,g55)
    c: Vertical(g55,g85)
    c: Vertical(g85,g115)
    c: Vertical(g30,g60)
    c: Vertical(g60,g90)
    c: Vertical(g90,g120)
    c: Vertical(g35,g65)
    c: Vertical(g65,g95)
    c: Vertical(g95,g125)
    c: Equal(g1,g11)
    c: Equal(g11,g16)
    c: Equal(g16,g21)
    c: Equal(g21,g26)
    c: Equal(g26,g31)
    c: Equal(g36,g41)
    c: Equal(g41,g46)
    c: Equal(g46,g51)
    c: Equal(g51,g56)
    c: Equal(g56,g61)
    c: Equal(g66,g71)
    c: Equal(g71,g76)
    c: Equal(g76,g81)
    c: Equal(g81,g86)
    c: Equal(g86,g91)
    c: Equal(g96,g101)
    c: Equal(g101,g106)
    c: Equal(g106,g111)
    c: Equal(g111,g116)
    c: Equal(g116,g121)
    c: Equal(g121,g6)
    c: Equal(g2,g12)
    c: Equal(g12,g17)
    c: Equal(g17,g22)
    c: Equal(g22,g27)
    c: Equal(g27,g32)
    c: Equal(g37,g42)
    c: Equal(g42,g47)
    c: Equal(g47,g52)
    c: Equal(g52,g57)
    c: Equal(g57,g62)
    c: Equal(g67,g72)
    c: Equal(g72,g77)
    c: Equal(g77,g82)
    c: Equal(g82,g87)
    c: Equal(g87,g92)
    c: Equal(g97,g102)
    c: Equal(g102,g107)
    c: Equal(g107,g112)
    c: Equal(g112,g117)
    c: Equal(g117,g122)
    c: Equal(g122,g7)
    c: Equal(g32,g62)
    c: Equal(g62,g92)
    c: Equal(g92,g122)
    c: Equal(g31,g61)
    c: Equal(g61,g91)
    c: Equal(g91,g121)
    c: DistanceX(g125,g10) = 19.05
    c: DistanceX(g120,g125) = 19.05
    c: DistanceX(g115,g120) = 19.05
    c: DistanceX(g110,g115) = 19.05
    c: DistanceX(g105,g110) = 19.05
    c: DistanceX(g100,g105) = 19.05
    c: DistanceY(g10,g95) = 19.05
    c: DistanceY(g95,g65) = 19.05
    c: DistanceY(g65,g35) = 19.05
FEATURE [Sketcher::SketchObject] Sketch023  label="BL-UnderLED"
  ArcFitTolerance = 1e-06
  AttachmentSupport = -> [XY_Plane001]
  FullyConstrained = true
  MakeInternals = false
  MapMode = 5
  expr: Constraints[166] = VarSet.Bottom_UnderLedX
  expr: Constraints[167] = VarSet.Bottom_UnderLedY
  expr: Constraints[171] = 2.5 * 19.05 mm
  expr: Constraints[172] = VarSet.Bottom_UnderLedR
  sketch-geometry (79):
    g0: LineSegment StartX=-126.625 StartY=63.2 StartZ=0 EndX=-126.625 EndY=58.1 EndZ=0
    g1: LineSegment StartX=-125.425 StartY=56.9 StartZ=0 EndX=-122.225 EndY=56.9 EndZ=0
    g2: LineSegment StartX=-121.025 StartY=58.1 StartZ=0 EndX=-121.025 EndY=63.2 EndZ=0
    g3: LineSegment StartX=-122.225 StartY=64.4 StartZ=0 EndX=-125.425 EndY=64.4 EndZ=0
    g4: GeomPoint [constr] X=-123.825 Y=60.65 Z=0
    g5: ArcOfCircle CenterX=-125.425 CenterY=63.2 CenterZ=0 NormalX=0 NormalY=0 NormalZ=1 AngleXU=0 Radius=1.2 StartAngle=1.5708 EndAngle=3.14159
    g6: GeomPoint [constr] X=-126.625 Y=64.4 Z=0
    g7: ArcOfCircle CenterX=-122.225 CenterY=63.2 CenterZ=0 NormalX=0 NormalY=0 NormalZ=1 AngleXU=0 Radius=1.2 StartAngle=3e-16 EndAngle=1.5708
    g8: GeomPoint [constr] X=-121.025 Y=64.4 Z=0
    g9: ArcOfCircle CenterX=-122.225 CenterY=58.1 CenterZ=0 NormalX=0 NormalY=0 NormalZ=1 AngleXU=0 Radius=1.2 StartAngle=4.71239 EndAngle=6.28319
    g10: GeomPoint [constr] X=-121.025 Y=56.9 Z=0
    g11: ArcOfCircle CenterX=-125.425 CenterY=58.1 CenterZ=0 NormalX=0 NormalY=0 NormalZ=1 AngleXU=0 Radius=1.2 StartAngle=3.14159 EndAngle=4.71239
    g12: GeomPoint [constr] X=-126.625 Y=56.9 Z=0
    g13: LineSegment StartX=-88.525 StartY=63.2 StartZ=0 EndX=-88.525 EndY=58.1 EndZ=0
    g14: LineSegment StartX=-87.325 StartY=56.9 StartZ=0 EndX=-84.125 EndY=56.9 EndZ=0
    g15: LineSegment StartX=-82.925 StartY=58.1 StartZ=0 EndX=-82.925 EndY=63.2 EndZ=0
    g16: LineSegment StartX=-84.125 StartY=64.4 StartZ=0 EndX=-87.325 EndY=64.4 EndZ=0
    g17: GeomPoint [constr] X=-85.725 Y=60.65 Z=0
    g18: ArcOfCircle CenterX=-87.325 CenterY=63.2 CenterZ=0 NormalX=0 NormalY=0 NormalZ=1 AngleXU=0 Radius=1.2 StartAngle=1.5708 EndAngle=3.14159
    g19: GeomPoint [constr] X=-88.525 Y=64.4 Z=0
    g20: ArcOfCircle CenterX=-84.125 CenterY=63.2 CenterZ=0 NormalX=0 NormalY=0 NormalZ=1 AngleXU=0 Radius=1.2 StartAngle=1.4e-15 EndAngle=1.5708
    g21: GeomPoint [constr] X=-82.925 Y=64.4 Z=0
    g22: ArcOfCircle CenterX=-84.125 CenterY=58.1 CenterZ=0 NormalX=0 NormalY=0 NormalZ=1 AngleXU=0 Radius=1.2 StartAngle=4.71239 EndAngle=6.28319
    g23: GeomPoint [constr] X=-82.925 Y=56.9 Z=0
    g24: ArcOfCircle CenterX=-87.325 CenterY=58.1 CenterZ=0 NormalX=0 NormalY=0 NormalZ=1 AngleXU=0 Radius=1.2 StartAngle=3.14159 EndAngle=4.71239
    g25: GeomPoint [constr] X=-88.525 Y=56.9 Z=0
    g26: LineSegment StartX=-50.425 StartY=63.2 StartZ=0 EndX=-50.425 EndY=58.1 EndZ=0
    g27: LineSegment StartX=-49.225 StartY=56.9 StartZ=0 EndX=-46.025 EndY=56.9 EndZ=0
    g28: LineSegment StartX=-44.825 StartY=58.1 StartZ=0 EndX=-44.825 EndY=63.2 EndZ=0
    g29: LineSegment StartX=-46.025 StartY=64.4 StartZ=0 EndX=-49.225 EndY=64.4 EndZ=0
    g30: GeomPoint [constr] X=-47.625 Y=60.65 Z=0
    g31: ArcOfCircle CenterX=-49.225 CenterY=63.2 CenterZ=0 NormalX=0 NormalY=0 NormalZ=1 AngleXU=0 Radius=1.2 StartAngle=1.5708 EndAngle=3.14159
    g32: GeomPoint [constr] X=-50.425 Y=64.4 Z=0
    g33: ArcOfCircle CenterX=-46.025 CenterY=63.2 CenterZ=0 NormalX=0 NormalY=0 NormalZ=1 AngleXU=0 Radius=1.2 StartAngle=3e-16 EndAngle=1.5708
    g34: GeomPoint [constr] X=-44.825 Y=64.4 Z=0
    g35: ArcOfCircle CenterX=-46.025 CenterY=58.1 CenterZ=0 NormalX=0 NormalY=0 NormalZ=1 AngleXU=0 Radius=1.2 StartAngle=4.71239 EndAngle=6.28319
    g36: GeomPoint [constr] X=-44.825 Y=56.9 Z=0
    g37: ArcOfCircle CenterX=-49.225 CenterY=58.1 CenterZ=0 NormalX=0 NormalY=0 NormalZ=1 AngleXU=0 Radius=1.2 StartAngle=3.14159 EndAngle=4.71239
    g38: GeomPoint [constr] X=-50.425 Y=56.9 Z=0
    g39: LineSegment StartX=-126.625 StartY=25.1 StartZ=0 EndX=-126.625 EndY=20 EndZ=0
    g40: LineSegment StartX=-125.425 StartY=18.8 StartZ=0 EndX=-122.225 EndY=18.8 EndZ=0
    g41: LineSegment StartX=-121.025 StartY=20 StartZ=0 EndX=-121.025 EndY=25.1 EndZ=0
    g42: LineSegment StartX=-122.225 StartY=26.3 StartZ=0 EndX=-125.425 EndY=26.3 EndZ=0
    g43: GeomPoint [constr] X=-123.825 Y=22.55 Z=0
    g44: ArcOfCircle CenterX=-125.425 CenterY=25.1 CenterZ=0 NormalX=0 NormalY=0 NormalZ=1 AngleXU=0 Radius=1.2 StartAngle=1.5708 EndAngle=3.14159
    g45: GeomPoint [constr] X=-126.625 Y=26.3 Z=0
    g46: ArcOfCircle CenterX=-122.225 CenterY=25.1 CenterZ=0 NormalX=0 NormalY=0 NormalZ=1 AngleXU=0 Radius=1.2 StartAngle=4e-16 EndAngle=1.5708
    g47: GeomPoint [constr] X=-121.025 Y=26.3 Z=0
    g48: ArcOfCircle CenterX=-122.225 CenterY=20 CenterZ=0 NormalX=0 NormalY=0 NormalZ=1 AngleXU=0 Radius=1.2 StartAngle=4.71239 EndAngle=6.28319
    g49: GeomPoint [constr] X=-121.025 Y=18.8 Z=0
    g50: ArcOfCircle CenterX=-125.425 CenterY=20 CenterZ=0 NormalX=0 NormalY=0 NormalZ=1 AngleXU=0 Radius=1.2 StartAngle=3.14159 EndAngle=4.71239
    g51: GeomPoint [constr] X=-126.625 Y=18.8 Z=0
    g52: LineSegment StartX=-88.525 StartY=25.1 StartZ=0 EndX=-88.525 EndY=20 EndZ=0
    g53: LineSegment StartX=-87.325 StartY=18.8 StartZ=0 EndX=-84.125 EndY=18.8 EndZ=0
    g54: LineSegment StartX=-82.925 StartY=20 StartZ=0 EndX=-82.925 EndY=25.1 EndZ=0
    g55: LineSegment StartX=-84.125 StartY=26.3 StartZ=0 EndX=-87.325 EndY=26.3 EndZ=0
    g56: GeomPoint [constr] X=-85.725 Y=22.55 Z=0
    g57: ArcOfCircle CenterX=-87.325 CenterY=25.1 CenterZ=0 NormalX=0 NormalY=0 NormalZ=1 AngleXU=0 Radius=1.2 StartAngle=1.5708 EndAngle=3.14159
    g58: GeomPoint [constr] X=-88.525 Y=26.3 Z=0
    g59: ArcOfCircle CenterX=-84.125 CenterY=25.1 CenterZ=0 NormalX=0 NormalY=0 NormalZ=1 AngleXU=0 Radius=1.2 StartAngle=5e-16 EndAngle=1.5708
    g60: GeomPoint [constr] X=-82.925 Y=26.3 Z=0
    g61: ArcOfCircle CenterX=-84.125 CenterY=20 CenterZ=0 NormalX=0 NormalY=0 NormalZ=1 AngleXU=0 Radius=1.2 StartAngle=4.71239 EndAngle=6.28319
    g62: GeomPoint [constr] X=-82.925 Y=18.8 Z=0
    g63: ArcOfCircle CenterX=-87.325 CenterY=20 CenterZ=0 NormalX=0 NormalY=0 NormalZ=1 AngleXU=0 Radius=1.2 StartAngle=3.14159 EndAngle=4.71239
    g64: GeomPoint [constr] X=-88.525 Y=18.8 Z=0
    g65: LineSegment StartX=-50.425 StartY=25.1 StartZ=0 EndX=-50.425 EndY=20 EndZ=0
    g66: LineSegment StartX=-49.225 StartY=18.8 StartZ=0 EndX=-46.025 EndY=18.8 EndZ=0
    g67: LineSegment StartX=-44.825 StartY=20 StartZ=0 EndX=-44.825 EndY=25.1 EndZ=0
    g68: LineSegment StartX=-46.025 StartY=26.3 StartZ=0 EndX=-49.225 EndY=26.3 EndZ=0
    g69: GeomPoint [constr] X=-47.625 Y=22.55 Z=0
    g70: ArcOfCircle CenterX=-49.225 CenterY=25.1 CenterZ=0 NormalX=0 NormalY=0 NormalZ=1 AngleXU=0 Radius=1.2 StartAngle=1.5708 EndAngle=3.14159
    g71: GeomPoint [constr] X=-50.425 Y=26.3 Z=0
    g72: ArcOfCircle CenterX=-46.025 CenterY=25.1 CenterZ=0 NormalX=0 NormalY=0 NormalZ=1 AngleXU=0 Radius=1.2 StartAngle=3e-16 EndAngle=1.5708
    g73: GeomPoint [constr] X=-44.825 Y=26.3 Z=0
    g74: ArcOfCircle CenterX=-46.025 CenterY=20 CenterZ=0 NormalX=0 NormalY=0 NormalZ=1 AngleXU=0 Radius=1.2 StartAngle=4.71239 EndAngle=6.28319
    g75: GeomPoint [constr] X=-44.825 Y=18.8 Z=0
    g76: ArcOfCircle CenterX=-49.225 CenterY=20 CenterZ=0 NormalX=0 NormalY=0 NormalZ=1 AngleXU=0 Radius=1.2 StartAngle=3.14159 EndAngle=4.71239
    g77: GeomPoint [constr] X=-50.425 Y=18.8 Z=0
    g78: GeomPoint X=-19.05 Y=19.05 Z=0
  constraints (176):
    c: Vertical(g0)
    c: Vertical(g2)
    c: Horizontal(g1)
    c: Horizontal(g3)
    c: Symmetric(g10,g6,g4)
    c: PointOnObject(g6,g0)
    c: PointOnObject(g6,g3)
    c: Tangent(g0,g5) = -1.5708
    c: Tangent(g3,g5) = -1.5708
    c: PointOnObject(g8,g2)
    c: PointOnObject(g8,g3)
    c: Tangent(g2,g7) = -1.5708
    c: Tangent(g3,g7) = -1.5708
    c: PointOnObject(g10,g1)
    c: PointOnObject(g10,g2)
    c: Tangent(g1,g9) = -1.5708
    c: Tangent(g2,g9) = -1.5708
    c: PointOnObject(g12,g0)
    c: PointOnObject(g12,g1)
    c: Tangent(g0,g11) = -1.5708
    c: Tangent(g1,g11) = -1.5708
    c: Equal(g5,g7)
    c: Equal(g7,g9)
    c: Equal(g9,g11)
    c: Vertical(g13)
    c: Vertical(g15)
    c: Horizontal(g14)
    c: Horizontal(g16)
    c: Symmetric(g23,g19,g17)
    c: PointOnObject(g19,g13)
    c: PointOnObject(g19,g16)
    c: Tangent(g13,g18) = -1.5708
    c: Tangent(g16,g18) = -1.5708
    c: PointOnObject(g21,g15)
    c: PointOnObject(g21,g16)
    c: Tangent(g15,g20) = -1.5708
    c: Tangent(g16,g20) = -1.5708
    c: PointOnObject(g23,g14)
    c: PointOnObject(g23,g15)
    c: Tangent(g14,g22) = -1.5708
    c: Tangent(g15,g22) = -1.5708
    c: PointOnObject(g25,g13)
    c: PointOnObject(g25,g14)
    c: Tangent(g13,g24) = -1.5708
    c: Tangent(g14,g24) = -1.5708
    c: Equal(g18,g20)
    c: Equal(g20,g22)
    c: Equal(g22,g24)
    c: Vertical(g26)
    c: Vertical(g28)
    c: Horizontal(g27)
    c: Horizontal(g29)
    c: Symmetric(g36,g32,g30)
    c: PointOnObject(g32,g26)
    c: PointOnObject(g32,g29)
    c: Tangent(g26,g31) = -1.5708
    c: Tangent(g29,g31) = -1.5708
    c: PointOnObject(g34,g28)
    c: PointOnObject(g34,g29)
    c: Tangent(g28,g33) = -1.5708
    c: Tangent(g29,g33) = -1.5708
    c: PointOnObject(g36,g27)
    c: PointOnObject(g36,g28)
    c: Tangent(g27,g35) = -1.5708
    c: Tangent(g28,g35) = -1.5708
    c: PointOnObject(g38,g26)
    c: PointOnObject(g38,g27)
    c: Tangent(g26,g37) = -1.5708
    c: Tangent(g27,g37) = -1.5708
    c: Equal(g31,g33)
    c: Equal(g33,g35)
    c: Equal(g35,g37)
    c: Vertical(g39)
    c: Vertical(g41)
    c: Horizontal(g40)
    c: Horizontal(g42)
    c: Symmetric(g49,g45,g43)
    c: PointOnObject(g45,g39)
    c: PointOnObject(g45,g42)
    c: Tangent(g39,g44) = -1.5708
    c: Tangent(g42,g44) = -1.5708
    c: PointOnObject(g47,g41)
    c: PointOnObject(g47,g42)
    c: Tangent(g41,g46) = -1.5708
    c: Tangent(g42,g46) = -1.5708
    c: PointOnObject(g49,g40)
    c: PointOnObject(g49,g41)
    c: Tangent(g40,g48) = -1.5708
    c: Tangent(g41,g48) = -1.5708
    c: PointOnObject(g51,g39)
    c: PointOnObject(g51,g40)
    c: Tangent(g39,g50) = -1.5708
    c: Tangent(g40,g50) = -1.5708
    c: Equal(g44,g46)
    c: Equal(g46,g48)
    c: Equal(g48,g50)
    c: Vertical(g52)
    c: Vertical(g54)
    c: Horizontal(g53)
    c: Horizontal(g55)
    c: Symmetric(g62,g58,g56)
    c: PointOnObject(g58,g52)
    c: PointOnObject(g58,g55)
    c: Tangent(g52,g57) = -1.5708
    c: Tangent(g55,g57) = -1.5708
    c: PointOnObject(g60,g54)
    c: PointOnObject(g60,g55)
    c: Tangent(g54,g59) = -1.5708
    c: Tangent(g55,g59) = -1.5708
    c: PointOnObject(g62,g53)
    c: PointOnObject(g62,g54)
    c: Tangent(g53,g61) = -1.5708
    c: Tangent(g54,g61) = -1.5708
    c: PointOnObject(g64,g52)
    c: PointOnObject(g64,g53)
    c: Tangent(g52,g63) = -1.5708
    c: Tangent(g53,g63) = -1.5708
    c: Equal(g57,g59)
    c: Equal(g59,g61)
    c: Equal(g61,g63)
    c: Vertical(g65)
    c: Vertical(g67)
    c: Horizontal(g66)
    c: Horizontal(g68)
    c: Symmetric(g75,g71,g69)
    c: PointOnObject(g71,g65)
    c: PointOnObject(g71,g68)
    c: Tangent(g65,g70) = -1.5708
    c: Tangent(g68,g70) = -1.5708
    c: PointOnObject(g73,g67)
    c: PointOnObject(g73,g68)
    c: Tangent(g67,g72) = -1.5708
    c: Tangent(g68,g72) = -1.5708
    c: PointOnObject(g75,g66)
    c: PointOnObject(g75,g67)
    c: Tangent(g66,g74) = -1.5708
    c: Tangent(g67,g74) = -1.5708
    c: PointOnObject(g77,g65)
    c: PointOnObject(g77,g66)
    c: Tangent(g65,g76) = -1.5708
    c: Tangent(g66,g76) = -1.5708
    c: Equal(g70,g72)
    c: Equal(g72,g74)
    c: Equal(g74,g76)
    c: Horizontal(g4,g17)
    c: Horizontal(g17,g30)
    c: Horizontal(g43,g56)
    c: Horizontal(g56,g69)
    c: Vertical(g4,g43)
    c: Vertical(g17,g56)
    c: Vertical(g30,g69)
    c: Equal(g0,g13)
    c: Equal(g13,g26)
    c: Equal(g39,g52)
    c: Equal(g52,g65)
    c: Equal(g26,g65)
    c: Equal(g1,g14)
    c: Equal(g14,g27)
    c: Equal(g40,g53)
    c: Equal(g53,g66)
    c: Equal(g27,g66)
    c: Equal(g5,g18)
    c: Equal(g18,g31)
    c: Equal(g44,g57)
    c: Equal(g57,g70)
    c: Equal(g31,g70)
    c: DistanceX(g65,g67) = 5.6
    c: DistanceY(g66,g68) = 7.5
    c: DistanceX(g43,g56) = 38.1
    c: DistanceX(g56,g69) = 38.1
    c: DistanceY(g56,g17) = 38.1
    c: DistanceX(g69,g-1) = 47.625
    c: Radius(g76) = 1.2
    c: DistanceY(g-1,g78) = 19.05
    c: DistanceY(g78,g69) = 3.5
    c: DistanceX(g78,g-1) = 19.05
FEATURE [Sketcher::SketchObject] Sketch017  label="BL-Plate"
  ArcFitTolerance = 1e-06
  AttachmentSupport = -> [XY_Plane001]
  FullyConstrained = true
  MakeInternals = false
  MapMode = 5
  expr: Constraints[14] = VarSet.Top_FrameFilletR
  expr: Constraints[25] = VarSet.Top_MedXY / 2 + VarSet.Top_Frame
  expr: Constraints[26] = VarSet.Top_MedXY / 2 + VarSet.Top_Frame + VarSet.Top_RearAdd
  expr: Constraints[29] = VarSet.Top_MedXY / 2 + VarSet.Top_Frame
  expr: Constraints[30] = VarSet.Top_MedXY / 2 + VarSet.Top_Frame
  sketch-geometry (37):
    g0: GeomPoint [constr] X=-38.1 Y=19.05 Z=0
    g1: GeomPoint [constr] X=-57.15 Y=19.05 Z=0
    g2: GeomPoint [constr] X=-76.2 Y=19.05 Z=0
    g3: GeomPoint [constr] X=-95.25 Y=19.05 Z=0
    g4: GeomPoint [constr] X=-114.3 Y=19.05 Z=0
    g5: GeomPoint [constr] X=-38.1 Y=57.15 Z=0
    g6: GeomPoint [constr] X=-57.15 Y=57.15 Z=0
    g7: GeomPoint [constr] X=-76.2 Y=57.15 Z=0
    g8: GeomPoint [constr] X=-95.25 Y=57.15 Z=0
    g9: GeomPoint [constr] X=-114.3 Y=57.15 Z=0
    g10: GeomPoint [constr] X=-38.1 Y=38.1 Z=0
    g11: GeomPoint [constr] X=-57.15 Y=38.1 Z=0
    g12: GeomPoint [constr] X=-76.2 Y=38.1 Z=0
    g13: GeomPoint [constr] X=-95.25 Y=38.1 Z=0
    g14: GeomPoint [constr] X=-114.3 Y=38.1 Z=0
    g15: GeomPoint [constr] X=-95.25 Y=76.2 Z=0
    g16: GeomPoint [constr] X=-57.15 Y=76.2 Z=0
    g17: GeomPoint [constr] X=-133.35 Y=76.2 Z=0
    g18: GeomPoint [constr] X=-114.3 Y=76.2 Z=0
    g19: GeomPoint [constr] X=-76.2 Y=76.2 Z=0
    g20: LineSegment StartX=-145.25 StartY=89.1 StartZ=0 EndX=-145.25 EndY=9.15 EndZ=0
    g21: LineSegment StartX=-143.25 StartY=91.1 StartZ=0 EndX=-9.15 EndY=91.1 EndZ=0
    g22: LineSegment StartX=-7.15 StartY=89.1 StartZ=0 EndX=-7.15 EndY=9.15 EndZ=0
    g23: LineSegment StartX=-9.15 StartY=7.15 StartZ=0 EndX=-143.25 EndY=7.15 EndZ=0
    g24: ArcOfCircle CenterX=-9.15 CenterY=9.15 CenterZ=0 NormalX=0 NormalY=0 NormalZ=1 AngleXU=0 Radius=2 StartAngle=4.71239 EndAngle=6.28319
    g25: GeomPoint [constr] X=-7.15 Y=7.15 Z=0
    g26: ArcOfCircle CenterX=-143.25 CenterY=9.15 CenterZ=0 NormalX=0 NormalY=0 NormalZ=1 AngleXU=0 Radius=2 StartAngle=3.14159 EndAngle=4.71239
    g27: GeomPoint [constr] X=-145.25 Y=7.15 Z=0
    g28: ArcOfCircle CenterX=-143.25 CenterY=89.1 CenterZ=0 NormalX=0 NormalY=0 NormalZ=1 AngleXU=0 Radius=2 StartAngle=1.5708 EndAngle=3.14159
    g29: GeomPoint [constr] X=-145.25 Y=91.1 Z=0
    g30: GeomPoint [constr] X=-38.1 Y=76.2 Z=0
    g31: GeomPoint [constr] X=-133.35 Y=57.15 Z=0
    g32: GeomPoint [constr] X=-133.35 Y=38.1 Z=0
    g33: GeomPoint [constr] X=-133.35 Y=19.05 Z=0
    g34: GeomPoint [constr] X=-19.05 Y=19.05 Z=0
    g35: ArcOfCircle CenterX=-9.15 CenterY=89.1 CenterZ=0 NormalX=0 NormalY=0 NormalZ=1 AngleXU=0 Radius=2 StartAngle=7.2e-15 EndAngle=1.5708
    g36: GeomPoint [constr] X=-7.15 Y=91.1 Z=0
  constraints (78):
    c: DistanceX(g1,g0) = 19.05
    c: DistanceX(g2,g1) = 19.05
    c: DistanceX(g3,g2) = 19.05
    c: DistanceX(g4,g3) = 19.05
    c: DistanceY(g0,g10) = 19.05
    c: DistanceY(g10,g5) = 19.05
    c: Vertical(g20)
    c: Horizontal(g21)
    c: Vertical(g22)
    c: Horizontal(g23)
    c: PointOnObject(g25,g22)
    c: PointOnObject(g25,g23)
    c: Tangent(g22,g24) = 1.5708
    c: Tangent(g23,g24) = 1.5708
    c: Radius(g24) = 2
    c: PointOnObject(g27,g20)
    c: PointOnObject(g27,g23)
    c: Tangent(g20,g26) = -1.5708
    c: Tangent(g23,g26) = 1.5708
    c: PointOnObject(g29,g20)
    c: PointOnObject(g29,g21)
    c: Tangent(g20,g28) = -1.5708
    c: Tangent(g21,g28) = 1.5708
    c: DistanceY(g5,g30) = 19.05
    c: DistanceX(g33,g4) = 19.05
    c: DistanceX(g29,g17) = 11.9
    c: DistanceY(g17,g29) = 14.9
    c: DistanceX(g0,g34) = 19.05
    c: DistanceX(g34,g-1) = 19.05
    c: DistanceX(g34,g25) = 11.9
    c: DistanceY(g25,g34) = 11.9
    c: Horizontal(g17,g18)
    c: Horizontal(g18,g15)
    c: Horizontal(g15,g19)
    c: Horizontal(g19,g16)
    c: Horizontal(g16,g30)
    c: Horizontal(g31,g9)
    c: Horizontal(g9,g8)
    c: Horizontal(g8,g7)
    c: Horizontal(g7,g6)
    c: Horizontal(g6,g5)
    c: Horizontal(g32,g14)
    c: Horizontal(g14,g13)
    c: Horizontal(g13,g12)
    c: Horizontal(g12,g11)
    c: Horizontal(g11,g10)
    c: Vertical(g17,g31)
    c: Vertical(g31,g32)
    c: Vertical(g32,g33)
    c: Vertical(g18,g9)
    c: Vertical(g9,g14)
    c: Vertical(g14,g4)
    c: Vertical(g15,g8)
    c: Vertical(g8,g13)
    c: Vertical(g13,g3)
    c: Vertical(g19,g7)
    c: Vertical(g7,g12)
    c: Vertical(g12,g2)
    c: Vertical(g16,g6)
    c: Vertical(g6,g11)
    c: Vertical(g11,g1)
    c: Vertical(g30,g5)
    c: Vertical(g5,g10)
    c: Vertical(g10,g0)
    c: PointOnObject(g36,g21)
    c: PointOnObject(g36,g22)
    c: Tangent(g21,g35) = 1.5708
    c: Tangent(g22,g35) = 1.5708
    c: Horizontal(g33,g4)
    c: Horizontal(g4,g3)
    c: Horizontal(g3,g2)
    c: Horizontal(g2,g1)
    c: Horizontal(g1,g0)
    c: Horizontal(g0,g34)
    c: DistanceY(g-1,g34) = 19.05
    c: Equal(g28,g24)
    c: Equal(g35,g24)
    c: Equal(g26,g24)
FEATURE [PartDesign::Pad] Pad010  label="BL-Plate-Pad"
  Direction = (0,0,1)
  Length = 3
  Length2 = 10
  Profile = -> Sketch017
  ReferenceAxis = -> Sketch017 [N_Axis]
  Refine = true
  Reversed = true
  Suppressed = false
  Type = 0
  expr: Length = VarSet.Bottom_PlateZ
FEATURE [Sketcher::SketchObject] Sketch018  label="BL-Stem"
  ArcFitTolerance = 1e-06
  AttachmentSupport = -> [XY_Plane001]
  FullyConstrained = true
  MakeInternals = false
  MapMode = 5
  sketch-geometry (300):
    g0: GeomPoint [constr] X=-38.1 Y=19.05 Z=0
    g1: GeomPoint [constr] X=-57.15 Y=19.05 Z=0
    g2: GeomPoint [constr] X=-76.2 Y=19.05 Z=0
    g3: GeomPoint [constr] X=-95.25 Y=19.05 Z=0
    g4: GeomPoint [constr] X=-114.3 Y=19.05 Z=0
    g5: GeomPoint [constr] X=-38.1 Y=57.15 Z=0
    g6: GeomPoint [constr] X=-57.15 Y=57.15 Z=0
    g7: GeomPoint [constr] X=-76.2 Y=57.15 Z=0
    g8: GeomPoint [constr] X=-95.25 Y=57.15 Z=0
    g9: GeomPoint [constr] X=-114.3 Y=57.15 Z=0
    g10: GeomPoint [constr] X=-38.1 Y=38.1 Z=0
    g11: GeomPoint [constr] X=-57.15 Y=38.1 Z=0
    g12: GeomPoint [constr] X=-76.2 Y=38.1 Z=0
    g13: GeomPoint [constr] X=-95.25 Y=38.1 Z=0
    g14: GeomPoint [constr] X=-114.3 Y=38.1 Z=0
    g15: GeomPoint [constr] X=-95.25 Y=76.2 Z=0
    g16: GeomPoint [constr] X=-57.15 Y=76.2 Z=0
    g17: GeomPoint [constr] X=-133.35 Y=76.2 Z=0
    g18: GeomPoint [constr] X=-114.3 Y=76.2 Z=0
    g19: GeomPoint [constr] X=-76.2 Y=76.2 Z=0
    g20: GeomPoint [constr] X=-38.1 Y=76.2 Z=0
    g21: GeomPoint [constr] X=-133.35 Y=57.15 Z=0
    g22: GeomPoint [constr] X=-133.35 Y=38.1 Z=0
    g23: GeomPoint [constr] X=-133.35 Y=19.05 Z=0
    g24: GeomPoint [constr] X=-19.05 Y=19.05 Z=0
    g25: GeomPoint [constr] X=-138.43 Y=76.2 Z=0
    g26: ArcOfCircle CenterX=-138.85 CenterY=76.2 CenterZ=0 NormalX=0 NormalY=0 NormalZ=1 AngleXU=0 Radius=1 StartAngle=1.5708 EndAngle=4.71239
    g27: ArcOfCircle CenterX=-138.43 CenterY=76.2 CenterZ=0 NormalX=0 NormalY=0 NormalZ=1 AngleXU=0 Radius=1 StartAngle=4.71239 EndAngle=7.85398
    g28: LineSegment StartX=-138.85 StartY=77.2 StartZ=0 EndX=-138.43 EndY=77.2 EndZ=0
    g29: LineSegment StartX=-138.85 StartY=75.2 StartZ=0 EndX=-138.43 EndY=75.2 EndZ=0
    g30: GeomPoint [constr] X=-127.85 Y=76.2 Z=0
    g31: ArcOfCircle CenterX=-128.27 CenterY=76.2 CenterZ=0 NormalX=0 NormalY=0 NormalZ=1 AngleXU=0 Radius=1 StartAngle=1.5708 EndAngle=4.71239
    g32: ArcOfCircle CenterX=-127.85 CenterY=76.2 CenterZ=0 NormalX=0 NormalY=0 NormalZ=1 AngleXU=0 Radius=1 StartAngle=4.71239 EndAngle=7.85398
    g33: LineSegment StartX=-128.27 StartY=77.2 StartZ=0 EndX=-127.85 EndY=77.2 EndZ=0
    g34: LineSegment StartX=-128.27 StartY=75.2 StartZ=0 EndX=-127.85 EndY=75.2 EndZ=0
    g35: Circle CenterX=-133.35 CenterY=76.2 CenterZ=0 NormalX=0 NormalY=0 NormalZ=1 AngleXU=0 Radius=2
    g36: GeomPoint [constr] X=-119.38 Y=76.2 Z=0
    g37: ArcOfCircle CenterX=-119.8 CenterY=76.2 CenterZ=0 NormalX=0 NormalY=0 NormalZ=1 AngleXU=0 Radius=1 StartAngle=1.5708 EndAngle=4.71239
    g38: ArcOfCircle CenterX=-119.38 CenterY=76.2 CenterZ=0 NormalX=0 NormalY=0 NormalZ=1 AngleXU=0 Radius=1 StartAngle=4.71239 EndAngle=7.85398
    g39: LineSegment StartX=-119.8 StartY=77.2 StartZ=0 EndX=-119.38 EndY=77.2 EndZ=0
    g40: LineSegment StartX=-119.8 StartY=75.2 StartZ=0 EndX=-119.38 EndY=75.2 EndZ=0
    g41: GeomPoint [constr] X=-108.8 Y=76.2 Z=0
    g42: ArcOfCircle CenterX=-109.22 CenterY=76.2 CenterZ=0 NormalX=0 NormalY=0 NormalZ=1 AngleXU=0 Radius=1 StartAngle=1.5708 EndAngle=4.71239
    g43: ArcOfCircle CenterX=-108.8 CenterY=76.2 CenterZ=0 NormalX=0 NormalY=0 NormalZ=1 AngleXU=0 Radius=1 StartAngle=4.71239 EndAngle=7.85398
    g44: LineSegment StartX=-109.22 StartY=77.2 StartZ=0 EndX=-108.8 EndY=77.2 EndZ=0
    g45: LineSegment StartX=-109.22 StartY=75.2 StartZ=0 EndX=-108.8 EndY=75.2 EndZ=0
    g46: Circle CenterX=-114.3 CenterY=76.2 CenterZ=0 NormalX=0 NormalY=0 NormalZ=1 AngleXU=0 Radius=2
    g47: GeomPoint [constr] X=-100.33 Y=76.2 Z=0
    g48: ArcOfCircle CenterX=-100.75 CenterY=76.2 CenterZ=0 NormalX=0 NormalY=0 NormalZ=1 AngleXU=0 Radius=1 StartAngle=1.5708 EndAngle=4.71239
    g49: ArcOfCircle CenterX=-100.33 CenterY=76.2 CenterZ=0 NormalX=0 NormalY=0 NormalZ=1 AngleXU=0 Radius=1 StartAngle=4.71239 EndAngle=7.85398
    g50: LineSegment StartX=-100.75 StartY=77.2 StartZ=0 EndX=-100.33 EndY=77.2 EndZ=0
    g51: LineSegment StartX=-100.75 StartY=75.2 StartZ=0 EndX=-100.33 EndY=75.2 EndZ=0
    g52: GeomPoint [constr] X=-89.75 Y=76.2 Z=0
    g53: ArcOfCircle CenterX=-90.17 CenterY=76.2 CenterZ=0 NormalX=0 NormalY=0 NormalZ=1 AngleXU=0 Radius=1 StartAngle=1.5708 EndAngle=4.71239
    g54: ArcOfCircle CenterX=-89.75 CenterY=76.2 CenterZ=0 NormalX=0 NormalY=0 NormalZ=1 AngleXU=0 Radius=1 StartAngle=4.71239 EndAngle=7.85398
    g55: LineSegment StartX=-90.17 StartY=77.2 StartZ=0 EndX=-89.75 EndY=77.2 EndZ=0
    g56: LineSegment StartX=-90.17 StartY=75.2 StartZ=0 EndX=-89.75 EndY=75.2 EndZ=0
    g57: Circle CenterX=-95.25 CenterY=76.2 CenterZ=0 NormalX=0 NormalY=0 NormalZ=1 AngleXU=0 Radius=2
    g58: GeomPoint [constr] X=-81.28 Y=76.2 Z=0
    g59: ArcOfCircle CenterX=-81.7 CenterY=76.2 CenterZ=0 NormalX=0 NormalY=0 NormalZ=1 AngleXU=0 Radius=1 StartAngle=1.5708 EndAngle=4.71239
    g60: ArcOfCircle CenterX=-81.28 CenterY=76.2 CenterZ=0 NormalX=0 NormalY=0 NormalZ=1 AngleXU=0 Radius=1 StartAngle=4.71239 EndAngle=7.85398
    g61: LineSegment StartX=-81.7 StartY=77.2 StartZ=0 EndX=-81.28 EndY=77.2 EndZ=0
    g62: LineSegment StartX=-81.7 StartY=75.2 StartZ=0 EndX=-81.28 EndY=75.2 EndZ=0
    g63: GeomPoint [constr] X=-70.7 Y=76.2 Z=0
    g64: ArcOfCircle CenterX=-71.12 CenterY=76.2 CenterZ=0 NormalX=0 NormalY=0 NormalZ=1 AngleXU=0 Radius=1 StartAngle=1.5708 EndAngle=4.71239
    g65: ArcOfCircle CenterX=-70.7 CenterY=76.2 CenterZ=0 NormalX=0 NormalY=0 NormalZ=1 AngleXU=0 Radius=1 StartAngle=4.71239 EndAngle=7.85398
    g66: LineSegment StartX=-71.12 StartY=77.2 StartZ=0 EndX=-70.7 EndY=77.2 EndZ=0
    g67: LineSegment StartX=-71.12 StartY=75.2 StartZ=0 EndX=-70.7 EndY=75.2 EndZ=0
    g68: Circle CenterX=-76.2 CenterY=76.2 CenterZ=0 NormalX=0 NormalY=0 NormalZ=1 AngleXU=0 Radius=2
    g69: GeomPoint [constr] X=-62.23 Y=76.2 Z=0
    g70: ArcOfCircle CenterX=-62.65 CenterY=76.2 CenterZ=0 NormalX=0 NormalY=0 NormalZ=1 AngleXU=0 Radius=1 StartAngle=1.5708 EndAngle=4.71239
    g71: ArcOfCircle CenterX=-62.23 CenterY=76.2 CenterZ=0 NormalX=0 NormalY=0 NormalZ=1 AngleXU=0 Radius=1 StartAngle=4.71239 EndAngle=7.85398
    g72: LineSegment StartX=-62.65 StartY=77.2 StartZ=0 EndX=-62.23 EndY=77.2 EndZ=0
    g73: LineSegment StartX=-62.65 StartY=75.2 StartZ=0 EndX=-62.23 EndY=75.2 EndZ=0
    g74: GeomPoint [constr] X=-51.65 Y=76.2 Z=0
    g75: ArcOfCircle CenterX=-52.07 CenterY=76.2 CenterZ=0 NormalX=0 NormalY=0 NormalZ=1 AngleXU=0 Radius=1 StartAngle=1.5708 EndAngle=4.71239
    g76: ArcOfCircle CenterX=-51.65 CenterY=76.2 CenterZ=0 NormalX=0 NormalY=0 NormalZ=1 AngleXU=0 Radius=1 StartAngle=4.71239 EndAngle=7.85398
    g77: LineSegment StartX=-52.07 StartY=77.2 StartZ=0 EndX=-51.65 EndY=77.2 EndZ=0
    g78: LineSegment StartX=-52.07 StartY=75.2 StartZ=0 EndX=-51.65 EndY=75.2 EndZ=0
    g79: Circle CenterX=-57.15 CenterY=76.2 CenterZ=0 NormalX=0 NormalY=0 NormalZ=1 AngleXU=0 Radius=2
    g80: GeomPoint [constr] X=-43.18 Y=76.2 Z=0
    g81: ArcOfCircle CenterX=-43.6 CenterY=76.2 CenterZ=0 NormalX=0 NormalY=0 NormalZ=1 AngleXU=0 Radius=1 StartAngle=1.5708 EndAngle=4.71239
    g82: ArcOfCircle CenterX=-43.18 CenterY=76.2 CenterZ=0 NormalX=0 NormalY=0 NormalZ=1 AngleXU=0 Radius=1 StartAngle=4.71239 EndAngle=7.85398
    g83: LineSegment StartX=-43.6 StartY=77.2 StartZ=0 EndX=-43.18 EndY=77.2 EndZ=0
    g84: LineSegment StartX=-43.6 StartY=75.2 StartZ=0 EndX=-43.18 EndY=75.2 EndZ=0
    g85: GeomPoint [constr] X=-32.6 Y=76.2 Z=0
    g86: ArcOfCircle CenterX=-33.02 CenterY=76.2 CenterZ=0 NormalX=0 NormalY=0 NormalZ=1 AngleXU=0 Radius=1 StartAngle=1.5708 EndAngle=4.71239
    g87: ArcOfCircle CenterX=-32.6 CenterY=76.2 CenterZ=0 NormalX=0 NormalY=0 NormalZ=1 AngleXU=0 Radius=1 StartAngle=4.71239 EndAngle=7.85398
    g88: LineSegment StartX=-33.02 StartY=77.2 StartZ=0 EndX=-32.6 EndY=77.2 EndZ=0
    g89: LineSegment StartX=-33.02 StartY=75.2 StartZ=0 EndX=-32.6 EndY=75.2 EndZ=0
    g90: Circle CenterX=-38.1 CenterY=76.2 CenterZ=0 NormalX=0 NormalY=0 NormalZ=1 AngleXU=0 Radius=2
    g91: GeomPoint [constr] X=-138.43 Y=57.15 Z=0
    g92: ArcOfCircle CenterX=-138.85 CenterY=57.15 CenterZ=0 NormalX=0 NormalY=0 NormalZ=1 AngleXU=0 Radius=1 StartAngle=1.5708 EndAngle=4.71239
    g93: ArcOfCircle CenterX=-138.43 CenterY=57.15 CenterZ=0 NormalX=0 NormalY=0 NormalZ=1 AngleXU=0 Radius=1 StartAngle=4.71239 EndAngle=7.85398
    g94: LineSegment StartX=-138.85 StartY=58.15 StartZ=0 EndX=-138.43 EndY=58.15 EndZ=0
    g95: LineSegment StartX=-138.85 StartY=56.15 StartZ=0 EndX=-138.43 EndY=56.15 EndZ=0
    g96: GeomPoint [constr] X=-127.85 Y=57.15 Z=0
    g97: ArcOfCircle CenterX=-128.27 CenterY=57.15 CenterZ=0 NormalX=0 NormalY=0 NormalZ=1 AngleXU=0 Radius=1 StartAngle=1.5708 EndAngle=4.71239
    g98: ArcOfCircle CenterX=-127.85 CenterY=57.15 CenterZ=0 NormalX=0 NormalY=0 NormalZ=1 AngleXU=0 Radius=1 StartAngle=4.71239 EndAngle=7.85398
    g99: LineSegment StartX=-128.27 StartY=58.15 StartZ=0 EndX=-127.85 EndY=58.15 EndZ=0
    g100: LineSegment StartX=-128.27 StartY=56.15 StartZ=0 EndX=-127.85 EndY=56.15 EndZ=0
    g101: Circle CenterX=-133.35 CenterY=57.15 CenterZ=0 NormalX=0 NormalY=0 NormalZ=1 AngleXU=0 Radius=2
    g102: GeomPoint [constr] X=-119.38 Y=57.15 Z=0
    g103: ArcOfCircle CenterX=-119.8 CenterY=57.15 CenterZ=0 NormalX=0 NormalY=0 NormalZ=1 AngleXU=0 Radius=1 StartAngle=1.5708 EndAngle=4.71239
    g104: ArcOfCircle CenterX=-119.38 CenterY=57.15 CenterZ=0 NormalX=0 NormalY=0 NormalZ=1 AngleXU=0 Radius=1 StartAngle=4.71239 EndAngle=7.85398
    g105: LineSegment StartX=-119.8 StartY=58.15 StartZ=0 EndX=-119.38 EndY=58.15 EndZ=0
    g106: LineSegment StartX=-119.8 StartY=56.15 StartZ=0 EndX=-119.38 EndY=56.15 EndZ=0
    g107: GeomPoint [constr] X=-108.8 Y=57.15 Z=0
    g108: ArcOfCircle CenterX=-109.22 CenterY=57.15 CenterZ=0 NormalX=0 NormalY=0 NormalZ=1 AngleXU=0 Radius=1 StartAngle=1.5708 EndAngle=4.71239
    g109: ArcOfCircle CenterX=-108.8 CenterY=57.15 CenterZ=0 NormalX=0 NormalY=0 NormalZ=1 AngleXU=0 Radius=1 StartAngle=4.71239 EndAngle=7.85398
    g110: LineSegment StartX=-109.22 StartY=58.15 StartZ=0 EndX=-108.8 EndY=58.15 EndZ=0
    g111: LineSegment StartX=-109.22 StartY=56.15 StartZ=0 EndX=-108.8 EndY=56.15 EndZ=0
    g112: Circle CenterX=-114.3 CenterY=57.15 CenterZ=0 NormalX=0 NormalY=0 NormalZ=1 AngleXU=0 Radius=2
    g113: GeomPoint [constr] X=-100.33 Y=57.15 Z=0
    g114: ArcOfCircle CenterX=-100.75 CenterY=57.15 CenterZ=0 NormalX=0 NormalY=0 NormalZ=1 AngleXU=0 Radius=1 StartAngle=1.5708 EndAngle=4.71239
    g115: ArcOfCircle CenterX=-100.33 CenterY=57.15 CenterZ=0 NormalX=0 NormalY=0 NormalZ=1 AngleXU=0 Radius=1 StartAngle=4.71239 EndAngle=7.85398
    g116: LineSegment StartX=-100.75 StartY=58.15 StartZ=0 EndX=-100.33 EndY=58.15 EndZ=0
    g117: LineSegment StartX=-100.75 StartY=56.15 StartZ=0 EndX=-100.33 EndY=56.15 EndZ=0
    g118: GeomPoint [constr] X=-89.75 Y=57.15 Z=0
    g119: ArcOfCircle CenterX=-90.17 CenterY=57.15 CenterZ=0 NormalX=0 NormalY=0 NormalZ=1 AngleXU=0 Radius=1 StartAngle=1.5708 EndAngle=4.71239
    g120: ArcOfCircle CenterX=-89.75 CenterY=57.15 CenterZ=0 NormalX=0 NormalY=0 NormalZ=1 AngleXU=0 Radius=1 StartAngle=4.71239 EndAngle=7.85398
    g121: LineSegment StartX=-90.17 StartY=58.15 StartZ=0 EndX=-89.75 EndY=58.15 EndZ=0
    g122: LineSegment StartX=-90.17 StartY=56.15 StartZ=0 EndX=-89.75 EndY=56.15 EndZ=0
    g123: Circle CenterX=-95.25 CenterY=57.15 CenterZ=0 NormalX=0 NormalY=0 NormalZ=1 AngleXU=0 Radius=2
    g124: GeomPoint [constr] X=-81.28 Y=57.15 Z=0
    g125: ArcOfCircle CenterX=-81.7 CenterY=57.15 CenterZ=0 NormalX=0 NormalY=0 NormalZ=1 AngleXU=0 Radius=1 StartAngle=1.5708 EndAngle=4.71239
    g126: ArcOfCircle CenterX=-81.28 CenterY=57.15 CenterZ=0 NormalX=0 NormalY=0 NormalZ=1 AngleXU=0 Radius=1 StartAngle=4.71239 EndAngle=7.85398
    g127: LineSegment StartX=-81.7 StartY=58.15 StartZ=0 EndX=-81.28 EndY=58.15 EndZ=0
    g128: LineSegment StartX=-81.7 StartY=56.15 StartZ=0 EndX=-81.28 EndY=56.15 EndZ=0
    g129: GeomPoint [constr] X=-70.7 Y=57.15 Z=0
    g130: ArcOfCircle CenterX=-71.12 CenterY=57.15 CenterZ=0 NormalX=0 NormalY=0 NormalZ=1 AngleXU=0 Radius=1 StartAngle=1.5708 EndAngle=4.71239
    g131: ArcOfCircle CenterX=-70.7 CenterY=57.15 CenterZ=0 NormalX=0 NormalY=0 NormalZ=1 AngleXU=0 Radius=1 StartAngle=4.71239 EndAngle=7.85398
    g132: LineSegment StartX=-71.12 StartY=58.15 StartZ=0 EndX=-70.7 EndY=58.15 EndZ=0
    g133: LineSegment StartX=-71.12 StartY=56.15 StartZ=0 EndX=-70.7 EndY=56.15 EndZ=0
    g134: Circle CenterX=-76.2 CenterY=57.15 CenterZ=0 NormalX=0 NormalY=0 NormalZ=1 AngleXU=0 Radius=2
    g135: GeomPoint [constr] X=-62.23 Y=57.15 Z=0
    g136: ArcOfCircle CenterX=-62.65 CenterY=57.15 CenterZ=0 NormalX=0 NormalY=0 NormalZ=1 AngleXU=0 Radius=1 StartAngle=1.5708 EndAngle=4.71239
    g137: ArcOfCircle CenterX=-62.23 CenterY=57.15 CenterZ=0 NormalX=0 NormalY=0 NormalZ=1 AngleXU=0 Radius=1 StartAngle=4.71239 EndAngle=7.85398
    g138: LineSegment StartX=-62.65 StartY=58.15 StartZ=0 EndX=-62.23 EndY=58.15 EndZ=0
    g139: LineSegment StartX=-62.65 StartY=56.15 StartZ=0 EndX=-62.23 EndY=56.15 EndZ=0
    g140: GeomPoint [constr] X=-51.65 Y=57.15 Z=0
    g141: ArcOfCircle CenterX=-52.07 CenterY=57.15 CenterZ=0 NormalX=0 NormalY=0 NormalZ=1 AngleXU=0 Radius=1 StartAngle=1.5708 EndAngle=4.71239
    g142: ArcOfCircle CenterX=-51.65 CenterY=57.15 CenterZ=0 NormalX=0 NormalY=0 NormalZ=1 AngleXU=0 Radius=1 StartAngle=4.71239 EndAngle=7.85398
    g143: LineSegment StartX=-52.07 StartY=58.15 StartZ=0 EndX=-51.65 EndY=58.15 EndZ=0
    g144: LineSegment StartX=-52.07 StartY=56.15 StartZ=0 EndX=-51.65 EndY=56.15 EndZ=0
    g145: Circle CenterX=-57.15 CenterY=57.15 CenterZ=0 NormalX=0 NormalY=0 NormalZ=1 AngleXU=0 Radius=2
    g146: GeomPoint [constr] X=-43.18 Y=57.15 Z=0
    g147: ArcOfCircle CenterX=-43.6 CenterY=57.15 CenterZ=0 NormalX=0 NormalY=0 NormalZ=1 AngleXU=0 Radius=1 StartAngle=1.5708 EndAngle=4.71239
    g148: ArcOfCircle CenterX=-43.18 CenterY=57.15 CenterZ=0 NormalX=0 NormalY=0 NormalZ=1 AngleXU=0 Radius=1 StartAngle=4.71239 EndAngle=7.85398
    g149: LineSegment StartX=-43.6 StartY=58.15 StartZ=0 EndX=-43.18 EndY=58.15 EndZ=0
    g150: LineSegment StartX=-43.6 StartY=56.15 StartZ=0 EndX=-43.18 EndY=56.15 EndZ=0
    g151: GeomPoint [constr] X=-32.6 Y=57.15 Z=0
    g152: ArcOfCircle CenterX=-33.02 CenterY=57.15 CenterZ=0 NormalX=0 NormalY=0 NormalZ=1 AngleXU=0 Radius=1 StartAngle=1.5708 EndAngle=4.71239
    g153: ArcOfCircle CenterX=-32.6 CenterY=57.15 CenterZ=0 NormalX=0 NormalY=0 NormalZ=1 AngleXU=0 Radius=1 StartAngle=4.71239 EndAngle=7.85398
    g154: LineSegment StartX=-33.02 StartY=58.15 StartZ=0 EndX=-32.6 EndY=58.15 EndZ=0
    g155: LineSegment StartX=-33.02 StartY=56.15 StartZ=0 EndX=-32.6 EndY=56.15 EndZ=0
    g156: Circle CenterX=-38.1 CenterY=57.15 CenterZ=0 NormalX=0 NormalY=0 NormalZ=1 AngleXU=0 Radius=2
    g157: GeomPoint [constr] X=-138.43 Y=38.1 Z=0
    g158: ArcOfCircle CenterX=-138.85 CenterY=38.1 CenterZ=0 NormalX=0 NormalY=0 NormalZ=1 AngleXU=0 Radius=1 StartAngle=1.5708 EndAngle=4.71239
    g159: ArcOfCircle CenterX=-138.43 CenterY=38.1 CenterZ=0 NormalX=0 NormalY=0 NormalZ=1 AngleXU=0 Radius=1 StartAngle=4.71239 EndAngle=7.85398
    g160: LineSegment StartX=-138.85 StartY=39.1 StartZ=0 EndX=-138.43 EndY=39.1 EndZ=0
    g161: LineSegment StartX=-138.85 StartY=37.1 StartZ=0 EndX=-138.43 EndY=37.1 EndZ=0
    g162: GeomPoint [constr] X=-127.85 Y=38.1 Z=0
    g163: ArcOfCircle CenterX=-128.27 CenterY=38.1 CenterZ=0 NormalX=0 NormalY=0 NormalZ=1 AngleXU=0 Radius=1 StartAngle=1.5708 EndAngle=4.71239
    g164: ArcOfCircle CenterX=-127.85 CenterY=38.1 CenterZ=0 NormalX=0 NormalY=0 NormalZ=1 AngleXU=0 Radius=1 StartAngle=4.71239 EndAngle=7.85398
    g165: LineSegment StartX=-128.27 StartY=39.1 StartZ=0 EndX=-127.85 EndY=39.1 EndZ=0
    g166: LineSegment StartX=-128.27 StartY=37.1 StartZ=0 EndX=-127.85 EndY=37.1 EndZ=0
    g167: Circle CenterX=-133.35 CenterY=38.1 CenterZ=0 NormalX=0 NormalY=0 NormalZ=1 AngleXU=0 Radius=2
    g168: GeomPoint [constr] X=-119.38 Y=38.1 Z=0
    g169: ArcOfCircle CenterX=-119.8 CenterY=38.1 CenterZ=0 NormalX=0 NormalY=0 NormalZ=1 AngleXU=0 Radius=1 StartAngle=1.5708 EndAngle=4.71239
    g170: ArcOfCircle CenterX=-119.38 CenterY=38.1 CenterZ=0 NormalX=0 NormalY=0 NormalZ=1 AngleXU=0 Radius=1 StartAngle=4.71239 EndAngle=7.85398
    g171: LineSegment StartX=-119.8 StartY=39.1 StartZ=0 EndX=-119.38 EndY=39.1 EndZ=0
    g172: LineSegment StartX=-119.8 StartY=37.1 StartZ=0 EndX=-119.38 EndY=37.1 EndZ=0
    g173: GeomPoint [constr] X=-108.8 Y=38.1 Z=0
    g174: ArcOfCircle CenterX=-109.22 CenterY=38.1 CenterZ=0 NormalX=0 NormalY=0 NormalZ=1 AngleXU=0 Radius=1 StartAngle=1.5708 EndAngle=4.71239
    g175: ArcOfCircle CenterX=-108.8 CenterY=38.1 CenterZ=0 NormalX=0 NormalY=0 NormalZ=1 AngleXU=0 Radius=1 StartAngle=4.71239 EndAngle=7.85398
    g176: LineSegment StartX=-109.22 StartY=39.1 StartZ=0 EndX=-108.8 EndY=39.1 EndZ=0
    g177: LineSegment StartX=-109.22 StartY=37.1 StartZ=0 EndX=-108.8 EndY=37.1 EndZ=0
    g178: Circle CenterX=-114.3 CenterY=38.1 CenterZ=0 NormalX=0 NormalY=0 NormalZ=1 AngleXU=0 Radius=2
    g179: GeomPoint [constr] X=-100.33 Y=38.1 Z=0
    g180: ArcOfCircle CenterX=-100.75 CenterY=38.1 CenterZ=0 NormalX=0 NormalY=0 NormalZ=1 AngleXU=0 Radius=1 StartAngle=1.5708 EndAngle=4.71239
    g181: ArcOfCircle CenterX=-100.33 CenterY=38.1 CenterZ=0 NormalX=0 NormalY=0 NormalZ=1 AngleXU=0 Radius=1 StartAngle=4.71239 EndAngle=7.85398
    g182: LineSegment StartX=-100.75 StartY=39.1 StartZ=0 EndX=-100.33 EndY=39.1 EndZ=0
    g183: LineSegment StartX=-100.75 StartY=37.1 StartZ=0 EndX=-100.33 EndY=37.1 EndZ=0
    g184: GeomPoint [constr] X=-89.75 Y=38.1 Z=0
    g185: ArcOfCircle CenterX=-90.17 CenterY=38.1 CenterZ=0 NormalX=0 NormalY=0 NormalZ=1 AngleXU=0 Radius=1 StartAngle=1.5708 EndAngle=4.71239
    g186: ArcOfCircle CenterX=-89.75 CenterY=38.1 CenterZ=0 NormalX=0 NormalY=0 NormalZ=1 AngleXU=0 Radius=1 StartAngle=4.71239 EndAngle=7.85398
    g187: LineSegment StartX=-90.17 StartY=39.1 StartZ=0 EndX=-89.75 EndY=39.1 EndZ=0
    g188: LineSegment StartX=-90.17 StartY=37.1 StartZ=0 EndX=-89.75 EndY=37.1 EndZ=0
    g189: Circle CenterX=-95.25 CenterY=38.1 CenterZ=0 NormalX=0 NormalY=0 NormalZ=1 AngleXU=0 Radius=2
    g190: GeomPoint [constr] X=-81.28 Y=38.1 Z=0
    g191: ArcOfCircle CenterX=-81.7 CenterY=38.1 CenterZ=0 NormalX=0 NormalY=0 NormalZ=1 AngleXU=0 Radius=1 StartAngle=1.5708 EndAngle=4.71239
    g192: ArcOfCircle CenterX=-81.28 CenterY=38.1 CenterZ=0 NormalX=0 NormalY=0 NormalZ=1 AngleXU=0 Radius=1 StartAngle=4.71239 EndAngle=7.85398
    g193: LineSegment StartX=-81.7 StartY=39.1 StartZ=0 EndX=-81.28 EndY=39.1 EndZ=0
    g194: LineSegment StartX=-81.7 StartY=37.1 StartZ=0 EndX=-81.28 EndY=37.1 EndZ=0
    g195: GeomPoint [constr] X=-70.7 Y=38.1 Z=0
    g196: ArcOfCircle CenterX=-71.12 CenterY=38.1 CenterZ=0 NormalX=0 NormalY=0 NormalZ=1 AngleXU=0 Radius=1 StartAngle=1.5708 EndAngle=4.71239
    g197: ArcOfCircle CenterX=-70.7 CenterY=38.1 CenterZ=0 NormalX=0 NormalY=0 NormalZ=1 AngleXU=0 Radius=1 StartAngle=4.71239 EndAngle=7.85398
    g198: LineSegment StartX=-71.12 StartY=39.1 StartZ=0 EndX=-70.7 EndY=39.1 EndZ=0
    g199: LineSegment StartX=-71.12 StartY=37.1 StartZ=0 EndX=-70.7 EndY=37.1 EndZ=0
    g200: Circle CenterX=-76.2 CenterY=38.1 CenterZ=0 NormalX=0 NormalY=0 NormalZ=1 AngleXU=0 Radius=2
    g201: GeomPoint [constr] X=-62.23 Y=38.1 Z=0
    g202: ArcOfCircle CenterX=-62.65 CenterY=38.1 CenterZ=0 NormalX=0 NormalY=0 NormalZ=1 AngleXU=0 Radius=1 StartAngle=1.5708 EndAngle=4.71239
    g203: ArcOfCircle CenterX=-62.23 CenterY=38.1 CenterZ=0 NormalX=0 NormalY=0 NormalZ=1 AngleXU=0 Radius=1 StartAngle=4.71239 EndAngle=7.85398
    g204: LineSegment StartX=-62.65 StartY=39.1 StartZ=0 EndX=-62.23 EndY=39.1 EndZ=0
    g205: LineSegment StartX=-62.65 StartY=37.1 StartZ=0 EndX=-62.23 EndY=37.1 EndZ=0
    g206: GeomPoint [constr] X=-51.65 Y=38.1 Z=0
    g207: ArcOfCircle CenterX=-52.07 CenterY=38.1 CenterZ=0 NormalX=0 NormalY=0 NormalZ=1 AngleXU=0 Radius=1 StartAngle=1.5708 EndAngle=4.71239
    g208: ArcOfCircle CenterX=-51.65 CenterY=38.1 CenterZ=0 NormalX=0 NormalY=0 NormalZ=1 AngleXU=0 Radius=1 StartAngle=4.71239 EndAngle=7.85398
    g209: LineSegment StartX=-52.07 StartY=39.1 StartZ=0 EndX=-51.65 EndY=39.1 EndZ=0
    g210: LineSegment StartX=-52.07 StartY=37.1 StartZ=0 EndX=-51.65 EndY=37.1 EndZ=0
    g211: Circle CenterX=-57.15 CenterY=38.1 CenterZ=0 NormalX=0 NormalY=0 NormalZ=1 AngleXU=0 Radius=2
    g212: GeomPoint [constr] X=-43.18 Y=38.1 Z=0
    g213: ArcOfCircle CenterX=-43.6 CenterY=38.1 CenterZ=0 NormalX=0 NormalY=0 NormalZ=1 AngleXU=0 Radius=1 StartAngle=1.5708 EndAngle=4.71239
    g214: ArcOfCircle CenterX=-43.18 CenterY=38.1 CenterZ=0 NormalX=0 NormalY=0 NormalZ=1 AngleXU=0 Radius=1 StartAngle=4.71239 EndAngle=7.85398
    g215: LineSegment StartX=-43.6 StartY=39.1 StartZ=0 EndX=-43.18 EndY=39.1 EndZ=0
    g216: LineSegment StartX=-43.6 StartY=37.1 StartZ=0 EndX=-43.18 EndY=37.1 EndZ=0
    g217: GeomPoint [constr] X=-32.6 Y=38.1 Z=0
    g218: ArcOfCircle CenterX=-33.02 CenterY=38.1 CenterZ=0 NormalX=0 NormalY=0 NormalZ=1 AngleXU=0 Radius=1 StartAngle=1.5708 EndAngle=4.71239
    g219: ArcOfCircle CenterX=-32.6 CenterY=38.1 CenterZ=0 NormalX=0 NormalY=0 NormalZ=1 AngleXU=0 Radius=1 StartAngle=4.71239 EndAngle=7.85398
    g220: LineSegment StartX=-33.02 StartY=39.1 StartZ=0 EndX=-32.6 EndY=39.1 EndZ=0
    g221: LineSegment StartX=-33.02 StartY=37.1 StartZ=0 EndX=-32.6 EndY=37.1 EndZ=0
    g222: Circle CenterX=-38.1 CenterY=38.1 CenterZ=0 NormalX=0 NormalY=0 NormalZ=1 AngleXU=0 Radius=2
    g223: GeomPoint [constr] X=-138.43 Y=19.05 Z=0
    g224: ArcOfCircle CenterX=-138.85 CenterY=19.05 CenterZ=0 NormalX=0 NormalY=0 NormalZ=1 AngleXU=0 Radius=1 StartAngle=1.5708 EndAngle=4.71239
    g225: ArcOfCircle CenterX=-138.43 CenterY=19.05 CenterZ=0 NormalX=0 NormalY=0 NormalZ=1 AngleXU=0 Radius=1 StartAngle=4.71239 EndAngle=7.85398
    g226: LineSegment StartX=-138.85 StartY=20.05 StartZ=0 EndX=-138.43 EndY=20.05 EndZ=0
    g227: LineSegment StartX=-138.85 StartY=18.05 StartZ=0 EndX=-138.43 EndY=18.05 EndZ=0
    g228: GeomPoint [constr] X=-127.85 Y=19.05 Z=0
    g229: ArcOfCircle CenterX=-128.27 CenterY=19.05 CenterZ=0 NormalX=0 NormalY=0 NormalZ=1 AngleXU=0 Radius=1 StartAngle=1.5708 EndAngle=4.71239
    g230: ArcOfCircle CenterX=-127.85 CenterY=19.05 CenterZ=0 NormalX=0 NormalY=0 NormalZ=1 AngleXU=0 Radius=1 StartAngle=4.71239 EndAngle=7.85398
    g231: LineSegment StartX=-128.27 StartY=20.05 StartZ=0 EndX=-127.85 EndY=20.05 EndZ=0
    g232: LineSegment StartX=-128.27 StartY=18.05 StartZ=0 EndX=-127.85 EndY=18.05 EndZ=0
    g233: Circle CenterX=-133.35 CenterY=19.05 CenterZ=0 NormalX=0 NormalY=0 NormalZ=1 AngleXU=0 Radius=2
    g234: GeomPoint [constr] X=-119.38 Y=19.05 Z=0
    g235: ArcOfCircle CenterX=-119.8 CenterY=19.05 CenterZ=0 NormalX=0 NormalY=0 NormalZ=1 AngleXU=0 Radius=1 StartAngle=1.5708 EndAngle=4.71239
    g236: ArcOfCircle CenterX=-119.38 CenterY=19.05 CenterZ=0 NormalX=0 NormalY=0 NormalZ=1 AngleXU=0 Radius=1 StartAngle=4.71239 EndAngle=7.85398
    g237: LineSegment StartX=-119.8 StartY=20.05 StartZ=0 EndX=-119.38 EndY=20.05 EndZ=0
    g238: LineSegment StartX=-119.8 StartY=18.05 StartZ=0 EndX=-119.38 EndY=18.05 EndZ=0
    g239: GeomPoint [constr] X=-108.8 Y=19.05 Z=0
    g240: ArcOfCircle CenterX=-109.22 CenterY=19.05 CenterZ=0 NormalX=0 NormalY=0 NormalZ=1 AngleXU=0 Radius=1 StartAngle=1.5708 EndAngle=4.71239
    g241: ArcOfCircle CenterX=-108.8 CenterY=19.05 CenterZ=0 NormalX=0 NormalY=0 NormalZ=1 AngleXU=0 Radius=1 StartAngle=4.71239 EndAngle=7.85398
    g242: LineSegment StartX=-109.22 StartY=20.05 StartZ=0 EndX=-108.8 EndY=20.05 EndZ=0
    g243: LineSegment StartX=-109.22 StartY=18.05 StartZ=0 EndX=-108.8 EndY=18.05 EndZ=0
    g244: Circle CenterX=-114.3 CenterY=19.05 CenterZ=0 NormalX=0 NormalY=0 NormalZ=1 AngleXU=0 Radius=2
    g245: GeomPoint [constr] X=-100.33 Y=19.05 Z=0
    g246: ArcOfCircle CenterX=-100.75 CenterY=19.05 CenterZ=0 NormalX=0 NormalY=0 NormalZ=1 AngleXU=0 Radius=1 StartAngle=1.5708 EndAngle=4.71239
    g247: ArcOfCircle CenterX=-100.33 CenterY=19.05 CenterZ=0 NormalX=0 NormalY=0 NormalZ=1 AngleXU=0 Radius=1 StartAngle=4.71239 EndAngle=7.85398
    g248: LineSegment StartX=-100.75 StartY=20.05 StartZ=0 EndX=-100.33 EndY=20.05 EndZ=0
    g249: LineSegment StartX=-100.75 StartY=18.05 StartZ=0 EndX=-100.33 EndY=18.05 EndZ=0
    g250: GeomPoint [constr] X=-89.75 Y=19.05 Z=0
    g251: ArcOfCircle CenterX=-90.17 CenterY=19.05 CenterZ=0 NormalX=0 NormalY=0 NormalZ=1 AngleXU=0 Radius=1 StartAngle=1.5708 EndAngle=4.71239
    g252: ArcOfCircle CenterX=-89.75 CenterY=19.05 CenterZ=0 NormalX=0 NormalY=0 NormalZ=1 AngleXU=0 Radius=1 StartAngle=4.71239 EndAngle=7.85398
    g253: LineSegment StartX=-90.17 StartY=20.05 StartZ=0 EndX=-89.75 EndY=20.05 EndZ=0
    g254: LineSegment StartX=-90.17 StartY=18.05 StartZ=0 EndX=-89.75 EndY=18.05 EndZ=0
    g255: Circle CenterX=-95.25 CenterY=19.05 CenterZ=0 NormalX=0 NormalY=0 NormalZ=1 AngleXU=0 Radius=2
    g256: GeomPoint [constr] X=-81.28 Y=19.05 Z=0
    g257: ArcOfCircle CenterX=-81.7 CenterY=19.05 CenterZ=0 NormalX=0 NormalY=0 NormalZ=1 AngleXU=0 Radius=1 StartAngle=1.5708 EndAngle=4.71239
    g258: ArcOfCircle CenterX=-81.28 CenterY=19.05 CenterZ=0 NormalX=0 NormalY=0 NormalZ=1 AngleXU=0 Radius=1 StartAngle=4.71239 EndAngle=7.85398
    g259: LineSegment StartX=-81.7 StartY=20.05 StartZ=0 EndX=-81.28 EndY=20.05 EndZ=0
    g260: LineSegment StartX=-81.7 StartY=18.05 StartZ=0 EndX=-81.28 EndY=18.05 EndZ=0
    g261: GeomPoint [constr] X=-70.7 Y=19.05 Z=0
    g262: ArcOfCircle CenterX=-71.12 CenterY=19.05 CenterZ=0 NormalX=0 NormalY=0 NormalZ=1 AngleXU=0 Radius=1 StartAngle=1.5708 EndAngle=4.71239
    g263: ArcOfCircle CenterX=-70.7 CenterY=19.05 CenterZ=0 NormalX=0 NormalY=0 NormalZ=1 AngleXU=0 Radius=1 StartAngle=4.71239 EndAngle=7.85398
    g264: LineSegment StartX=-71.12 StartY=20.05 StartZ=0 EndX=-70.7 EndY=20.05 EndZ=0
    g265: LineSegment StartX=-71.12 StartY=18.05 StartZ=0 EndX=-70.7 EndY=18.05 EndZ=0
    g266: Circle CenterX=-76.2 CenterY=19.05 CenterZ=0 NormalX=0 NormalY=0 NormalZ=1 AngleXU=0 Radius=2
    g267: GeomPoint [constr] X=-62.23 Y=19.05 Z=0
    g268: ArcOfCircle CenterX=-62.65 CenterY=19.05 CenterZ=0 NormalX=0 NormalY=0 NormalZ=1 AngleXU=0 Radius=1 StartAngle=1.5708 EndAngle=4.71239
    g269: ArcOfCircle CenterX=-62.23 CenterY=19.05 CenterZ=0 NormalX=0 NormalY=0 NormalZ=1 AngleXU=0 Radius=1 StartAngle=4.71239 EndAngle=7.85398
    g270: LineSegment StartX=-62.65 StartY=20.05 StartZ=0 EndX=-62.23 EndY=20.05 EndZ=0
    g271: LineSegment StartX=-62.65 StartY=18.05 StartZ=0 EndX=-62.23 EndY=18.05 EndZ=0
    g272: GeomPoint [constr] X=-51.65 Y=19.05 Z=0
    g273: ArcOfCircle CenterX=-52.07 CenterY=19.05 CenterZ=0 NormalX=0 NormalY=0 NormalZ=1 AngleXU=0 Radius=1 StartAngle=1.5708 EndAngle=4.71239
    g274: ArcOfCircle CenterX=-51.65 CenterY=19.05 CenterZ=0 NormalX=0 NormalY=0 NormalZ=1 AngleXU=0 Radius=1 StartAngle=4.71239 EndAngle=7.85398
    g275: LineSegment StartX=-52.07 StartY=20.05 StartZ=0 EndX=-51.65 EndY=20.05 EndZ=0
    g276: LineSegment StartX=-52.07 StartY=18.05 StartZ=0 EndX=-51.65 EndY=18.05 EndZ=0
    g277: Circle CenterX=-57.15 CenterY=19.05 CenterZ=0 NormalX=0 NormalY=0 NormalZ=1 AngleXU=0 Radius=2
    g278: GeomPoint [constr] X=-43.18 Y=19.05 Z=0
    g279: ArcOfCircle CenterX=-43.6 CenterY=19.05 CenterZ=0 NormalX=0 NormalY=0 NormalZ=1 AngleXU=0 Radius=1 StartAngle=1.5708 EndAngle=4.71239
    g280: ArcOfCircle CenterX=-43.18 CenterY=19.05 CenterZ=0 NormalX=0 NormalY=0 NormalZ=1 AngleXU=0 Radius=1 StartAngle=4.71239 EndAngle=7.85398
    g281: LineSegment StartX=-43.6 StartY=20.05 StartZ=0 EndX=-43.18 EndY=20.05 EndZ=0
    g282: LineSegment StartX=-43.6 StartY=18.05 StartZ=0 EndX=-43.18 EndY=18.05 EndZ=0
    g283: GeomPoint [constr] X=-32.6 Y=19.05 Z=0
    g284: ArcOfCircle CenterX=-33.02 CenterY=19.05 CenterZ=0 NormalX=0 NormalY=0 NormalZ=1 AngleXU=0 Radius=1 StartAngle=1.5708 EndAngle=4.71239
    g285: ArcOfCircle CenterX=-32.6 CenterY=19.05 CenterZ=0 NormalX=0 NormalY=0 NormalZ=1 AngleXU=0 Radius=1 StartAngle=4.71239 EndAngle=7.85398
    g286: LineSegment StartX=-33.02 StartY=20.05 StartZ=0 EndX=-32.6 EndY=20.05 EndZ=0
    g287: LineSegment StartX=-33.02 StartY=18.05 StartZ=0 EndX=-32.6 EndY=18.05 EndZ=0
    g288: Circle CenterX=-38.1 CenterY=19.05 CenterZ=0 NormalX=0 NormalY=0 NormalZ=1 AngleXU=0 Radius=2
    g289: GeomPoint [constr] X=-24.13 Y=19.05 Z=0
    g290: ArcOfCircle CenterX=-24.55 CenterY=19.05 CenterZ=0 NormalX=0 NormalY=0 NormalZ=1 AngleXU=0 Radius=1 StartAngle=1.5708 EndAngle=4.71239
    g291: ArcOfCircle CenterX=-24.13 CenterY=19.05 CenterZ=0 NormalX=0 NormalY=0 NormalZ=1 AngleXU=0 Radius=1 StartAngle=4.71239 EndAngle=7.85398
    g292: LineSegment StartX=-24.55 StartY=20.05 StartZ=0 EndX=-24.13 EndY=20.05 EndZ=0
    g293: LineSegment StartX=-24.55 StartY=18.05 StartZ=0 EndX=-24.13 EndY=18.05 EndZ=0
    g294: GeomPoint [constr] X=-13.55 Y=19.05 Z=0
    g295: ArcOfCircle CenterX=-13.97 CenterY=19.05 CenterZ=0 NormalX=0 NormalY=0 NormalZ=1 AngleXU=0 Radius=1 StartAngle=1.5708 EndAngle=4.71239
    g296: ArcOfCircle CenterX=-13.55 CenterY=19.05 CenterZ=0 NormalX=0 NormalY=0 NormalZ=1 AngleXU=0 Radius=1 StartAngle=4.71239 EndAngle=7.85398
    g297: LineSegment StartX=-13.97 StartY=20.05 StartZ=0 EndX=-13.55 EndY=20.05 EndZ=0
    g298: LineSegment StartX=-13.97 StartY=18.05 StartZ=0 EndX=-13.55 EndY=18.05 EndZ=0
    g299: Circle CenterX=-19.05 CenterY=19.05 CenterZ=0 NormalX=0 NormalY=0 NormalZ=1 AngleXU=0 Radius=2
  constraints (650):
    c: DistanceX(g1,g0) = 19.05
    c: DistanceX(g2,g1) = 19.05
    c: DistanceX(g3,g2) = 19.05
    c: DistanceX(g4,g3) = 19.05
    c: DistanceY(g0,g10) = 19.05
    c: DistanceY(g10,g5) = 19.05
    c: DistanceY(g5,g20) = 19.05
    c: DistanceX(g23,g4) = 19.05
    c: DistanceX(g0,g24) = 19.05
    c: DistanceX(g24,g-1) = 19.05
    c: Horizontal(g17,g18)
    c: Horizontal(g18,g15)
    c: Horizontal(g15,g19)
    c: Horizontal(g19,g16)
    c: Horizontal(g16,g20)
    c: Horizontal(g21,g9)
    c: Horizontal(g9,g8)
    c: Horizontal(g8,g7)
    c: Horizontal(g7,g6)
    c: Horizontal(g6,g5)
    c: Horizontal(g22,g14)
    c: Horizontal(g14,g13)
    c: Horizontal(g13,g12)
    c: Horizontal(g12,g11)
    c: Horizontal(g11,g10)
    c: Vertical(g17,g21)
    c: Vertical(g21,g22)
    c: Vertical(g22,g23)
    c: Vertical(g18,g9)
    c: Vertical(g9,g14)
    c: Vertical(g14,g4)
    c: Vertical(g15,g8)
    c: Vertical(g8,g13)
    c: Vertical(g13,g3)
    c: Vertical(g19,g7)
    c: Vertical(g7,g12)
    c: Vertical(g12,g2)
    c: Vertical(g16,g6)
    c: Vertical(g6,g11)
    c: Vertical(g11,g1)
    c: Vertical(g20,g5)
    c: Vertical(g5,g10)
    c: Vertical(g10,g0)
    c: Horizontal(g23,g4)
    c: Horizontal(g4,g3)
    c: Horizontal(g3,g2)
    c: Horizontal(g2,g1)
    c: Horizontal(g1,g0)
    c: Horizontal(g0,g24)
    c: DistanceY(g-1,g24) = 19.05
    c: Tangent(g26,g28) = 1.5708
    c: Tangent(g26,g29) = -1.5708
    c: Tangent(g27,g28) = 1.5708
    c: Tangent(g27,g29) = -1.5708
    c: Coincident(g27,g25)
    c: Tangent(g31,g33) = 1.5708
    c: Tangent(g31,g34) = -1.5708
    c: Tangent(g32,g33) = 1.5708
    c: Tangent(g32,g34) = -1.5708
    c: Coincident(g32,g30)
    c: Horizontal(g26,g25)
    c: Horizontal(g25,g35)
    c: Horizontal(g35,g31)
    c: Horizontal(g31,g30)
    c: Equal(g26,g27)
    c: Equal(g31,g32)
    c: Equal(g27,g31)
    c: Tangent(g37,g39) = 1.5708
    c: Tangent(g37,g40) = -1.5708
    c: Tangent(g38,g39) = 1.5708
    c: Tangent(g38,g40) = -1.5708
    c: Coincident(g38,g36)
    c: Tangent(g42,g44) = 1.5708
    c: Tangent(g42,g45) = -1.5708
    c: Tangent(g43,g44) = 1.5708
    c: Tangent(g43,g45) = -1.5708
    c: Coincident(g43,g41)
    c: Horizontal(g37,g36)
    c: Horizontal(g36,g46)
    c: Horizontal(g46,g42)
    c: Horizontal(g42,g41)
    c: Equal(g37,g38)
    c: Equal(g42,g43)
    c: Equal(g38,g42)
    c: Tangent(g48,g50) = 1.5708
    c: Tangent(g48,g51) = -1.5708
    c: Tangent(g49,g50) = 1.5708
    c: Tangent(g49,g51) = -1.5708
    c: Coincident(g49,g47)
    c: Tangent(g53,g55) = 1.5708
    c: Tangent(g53,g56) = -1.5708
    c: Tangent(g54,g55) = 1.5708
    c: Tangent(g54,g56) = -1.5708
    c: Coincident(g54,g52)
    c: Horizontal(g48,g47)
    c: Horizontal(g47,g57)
    c: Horizontal(g57,g53)
    c: Horizontal(g53,g52)
    c: Equal(g48,g49)
    c: Equal(g53,g54)
    c: Equal(g49,g53)
    c: Tangent(g59,g61) = 1.5708
    c: Tangent(g59,g62) = -1.5708
    c: Tangent(g60,g61) = 1.5708
    c: Tangent(g60,g62) = -1.5708
    c: Coincident(g60,g58)
    c: Tangent(g64,g66) = 1.5708
    c: Tangent(g64,g67) = -1.5708
    c: Tangent(g65,g66) = 1.5708
    c: Tangent(g65,g67) = -1.5708
    c: Coincident(g65,g63)
    c: Horizontal(g59,g58)
    c: Horizontal(g58,g68)
    c: Horizontal(g68,g64)
    c: Horizontal(g64,g63)
    c: Equal(g59,g60)
    c: Equal(g64,g65)
    c: Equal(g60,g64)
    c: Tangent(g70,g72) = 1.5708
    c: Tangent(g70,g73) = -1.5708
    c: Tangent(g71,g72) = 1.5708
    c: Tangent(g71,g73) = -1.5708
    c: Coincident(g71,g69)
    c: Tangent(g75,g77) = 1.5708
    c: Tangent(g75,g78) = -1.5708
    c: Tangent(g76,g77) = 1.5708
    c: Tangent(g76,g78) = -1.5708
    c: Coincident(g76,g74)
    c: Horizontal(g70,g69)
    c: Horizontal(g69,g79)
    c: Horizontal(g79,g75)
    c: Horizontal(g75,g74)
    c: Equal(g70,g71)
    c: Equal(g75,g76)
    c: Equal(g71,g75)
    c: Tangent(g81,g83) = 1.5708
    c: Tangent(g81,g84) = -1.5708
    c: Tangent(g82,g83) = 1.5708
    c: Tangent(g82,g84) = -1.5708
    c: Coincident(g82,g80)
    c: Tangent(g86,g88) = 1.5708
    c: Tangent(g86,g89) = -1.5708
    c: Tangent(g87,g88) = 1.5708
    c: Tangent(g87,g89) = -1.5708
    c: Coincident(g87,g85)
    c: Horizontal(g81,g80)
    c: Horizontal(g80,g90)
    c: Horizontal(g90,g86)
    c: Horizontal(g86,g85)
    c: Equal(g81,g82)
    c: Equal(g86,g87)
    c: Equal(g82,g86)
    c: Tangent(g92,g94) = 1.5708
    c: Tangent(g92,g95) = -1.5708
    c: Tangent(g93,g94) = 1.5708
    c: Tangent(g93,g95) = -1.5708
    c: Coincident(g93,g91)
    c: Tangent(g97,g99) = 1.5708
    c: Tangent(g97,g100) = -1.5708
    c: Tangent(g98,g99) = 1.5708
    c: Tangent(g98,g100) = -1.5708
    c: Coincident(g98,g96)
    c: Horizontal(g92,g91)
    c: Horizontal(g91,g101)
    c: Horizontal(g101,g97)
    c: Horizontal(g97,g96)
    c: Equal(g92,g93)
    c: Equal(g97,g98)
    c: Equal(g93,g97)
    c: Tangent(g103,g105) = 1.5708
    c: Tangent(g103,g106) = -1.5708
    c: Tangent(g104,g105) = 1.5708
    c: Tangent(g104,g106) = -1.5708
    c: Coincident(g104,g102)
    c: Tangent(g108,g110) = 1.5708
    c: Tangent(g108,g111) = -1.5708
    c: Tangent(g109,g110) = 1.5708
    c: Tangent(g109,g111) = -1.5708
    c: Coincident(g109,g107)
    c: Horizontal(g103,g102)
    c: Horizontal(g102,g112)
    c: Horizontal(g112,g108)
    c: Horizontal(g108,g107)
    c: Equal(g103,g104)
    c: Equal(g108,g109)
    c: Equal(g104,g108)
    c: Tangent(g114,g116) = 1.5708
    c: Tangent(g114,g117) = -1.5708
    c: Tangent(g115,g116) = 1.5708
    c: Tangent(g115,g117) = -1.5708
    c: Coincident(g115,g113)
    c: Tangent(g119,g121) = 1.5708
    c: Tangent(g119,g122) = -1.5708
    c: Tangent(g120,g121) = 1.5708
    c: Tangent(g120,g122) = -1.5708
    c: Coincident(g120,g118)
    c: Horizontal(g114,g113)
    c: Horizontal(g113,g123)
    c: Horizontal(g123,g119)
    c: Horizontal(g119,g118)
    c: Equal(g114,g115)
    c: Equal(g119,g120)
    c: Equal(g115,g119)
    c: Tangent(g125,g127) = 1.5708
    c: Tangent(g125,g128) = -1.5708
    c: Tangent(g126,g127) = 1.5708
    c: Tangent(g126,g128) = -1.5708
    c: Coincident(g126,g124)
    c: Tangent(g130,g132) = 1.5708
    c: Tangent(g130,g133) = -1.5708
    c: Tangent(g131,g132) = 1.5708
    c: Tangent(g131,g133) = -1.5708
    c: Coincident(g131,g129)
    c: Horizontal(g125,g124)
    c: Horizontal(g124,g134)
    c: Horizontal(g134,g130)
    c: Horizontal(g130,g129)
    c: Equal(g125,g126)
    c: Equal(g130,g131)
    c: Equal(g126,g130)
    c: Tangent(g136,g138) = 1.5708
    c: Tangent(g136,g139) = -1.5708
    c: Tangent(g137,g138) = 1.5708
    c: Tangent(g137,g139) = -1.5708
    c: Coincident(g137,g135)
    c: Tangent(g141,g143) = 1.5708
    c: Tangent(g141,g144) = -1.5708
    c: Tangent(g142,g143) = 1.5708
    c: Tangent(g142,g144) = -1.5708
    c: Coincident(g142,g140)
    c: Horizontal(g136,g135)
    c: Horizontal(g135,g145)
    c: Horizontal(g145,g141)
    c: Horizontal(g141,g140)
    c: Equal(g136,g137)
    c: Equal(g141,g142)
    c: Equal(g137,g141)
    c: Tangent(g147,g149) = 1.5708
    c: Tangent(g147,g150) = -1.5708
    c: Tangent(g148,g149) = 1.5708
    c: Tangent(g148,g150) = -1.5708
    c: Coincident(g148,g146)
    c: Tangent(g152,g154) = 1.5708
    c: Tangent(g152,g155) = -1.5708
    c: Tangent(g153,g154) = 1.5708
    c: Tangent(g153,g155) = -1.5708
    c: Coincident(g153,g151)
    c: Horizontal(g147,g146)
    c: Horizontal(g146,g156)
    c: Horizontal(g156,g152)
    c: Horizontal(g152,g151)
    c: Equal(g147,g148)
    c: Equal(g152,g153)
    c: Equal(g148,g152)
    c: Tangent(g158,g160) = 1.5708
    c: Tangent(g158,g161) = -1.5708
    c: Tangent(g159,g160) = 1.5708
    c: Tangent(g159,g161) = -1.5708
    c: Coincident(g159,g157)
    c: Tangent(g163,g165) = 1.5708
    c: Tangent(g163,g166) = -1.5708
    c: Tangent(g164,g165) = 1.5708
    c: Tangent(g164,g166) = -1.5708
    c: Coincident(g164,g162)
    c: Horizontal(g158,g157)
    c: Horizontal(g157,g167)
    c: Horizontal(g167,g163)
    c: Horizontal(g163,g162)
    c: Equal(g158,g159)
    c: Equal(g163,g164)
    c: Equal(g159,g163)
    c: Tangent(g169,g171) = 1.5708
    c: Tangent(g169,g172) = -1.5708
    c: Tangent(g170,g171) = 1.5708
    c: Tangent(g170,g172) = -1.5708
    c: Coincident(g170,g168)
    c: Tangent(g174,g176) = 1.5708
    c: Tangent(g174,g177) = -1.5708
    c: Tangent(g175,g176) = 1.5708
    c: Tangent(g175,g177) = -1.5708
    c: Coincident(g175,g173)
    c: Horizontal(g169,g168)
    c: Horizontal(g168,g178)
    c: Horizontal(g178,g174)
    c: Horizontal(g174,g173)
    c: Equal(g169,g170)
    c: Equal(g174,g175)
    c: Equal(g170,g174)
    c: Tangent(g180,g182) = 1.5708
    c: Tangent(g180,g183) = -1.5708
    c: Tangent(g181,g182) = 1.5708
    c: Tangent(g181,g183) = -1.5708
    c: Coincident(g181,g179)
    c: Tangent(g185,g187) = 1.5708
    c: Tangent(g185,g188) = -1.5708
    c: Tangent(g186,g187) = 1.5708
    c: Tangent(g186,g188) = -1.5708
    c: Coincident(g186,g184)
    c: Horizontal(g180,g179)
    c: Horizontal(g179,g189)
    c: Horizontal(g189,g185)
    c: Horizontal(g185,g184)
    c: Equal(g180,g181)
    c: Equal(g185,g186)
    c: Equal(g181,g185)
    c: Tangent(g191,g193) = 1.5708
    c: Tangent(g191,g194) = -1.5708
    c: Tangent(g192,g193) = 1.5708
    c: Tangent(g192,g194) = -1.5708
    c: Coincident(g192,g190)
    c: Tangent(g196,g198) = 1.5708
    c: Tangent(g196,g199) = -1.5708
    c: Tangent(g197,g198) = 1.5708
    c: Tangent(g197,g199) = -1.5708
    c: Coincident(g197,g195)
    c: Horizontal(g191,g190)
    c: Horizontal(g190,g200)
    c: Horizontal(g200,g196)
    c: Horizontal(g196,g195)
    c: Equal(g191,g192)
    c: Equal(g196,g197)
    c: Equal(g192,g196)
    c: Tangent(g202,g204) = 1.5708
    c: Tangent(g202,g205) = -1.5708
    c: Tangent(g203,g204) = 1.5708
    c: Tangent(g203,g205) = -1.5708
    c: Coincident(g203,g201)
    c: Tangent(g207,g209) = 1.5708
    c: Tangent(g207,g210) = -1.5708
    c: Tangent(g208,g209) = 1.5708
    c: Tangent(g208,g210) = -1.5708
    c: Coincident(g208,g206)
    c: Horizontal(g202,g201)
    c: Horizontal(g201,g211)
    c: Horizontal(g211,g207)
    c: Horizontal(g207,g206)
    c: Equal(g202,g203)
    c: Equal(g207,g208)
    c: Equal(g203,g207)
    c: Tangent(g213,g215) = 1.5708
    c: Tangent(g213,g216) = -1.5708
    c: Tangent(g214,g215) = 1.5708
    c: Tangent(g214,g216) = -1.5708
    c: Coincident(g214,g212)
    c: Tangent(g218,g220) = 1.5708
    c: Tangent(g218,g221) = -1.5708
    c: Tangent(g219,g220) = 1.5708
    c: Tangent(g219,g221) = -1.5708
    c: Coincident(g219,g217)
    c: Horizontal(g213,g212)
    c: Horizontal(g212,g222)
    c: Horizontal(g222,g218)
    c: Horizontal(g218,g217)
    c: Equal(g213,g214)
    c: Equal(g218,g219)
    c: Equal(g214,g218)
    c: Tangent(g224,g226) = 1.5708
    c: Tangent(g224,g227) = -1.5708
    c: Tangent(g225,g226) = 1.5708
    c: Tangent(g225,g227) = -1.5708
    c: Coincident(g225,g223)
    c: Tangent(g229,g231) = 1.5708
    c: Tangent(g229,g232) = -1.5708
    c: Tangent(g230,g231) = 1.5708
    c: Tangent(g230,g232) = -1.5708
    c: Coincident(g230,g228)
    c: Horizontal(g224,g223)
    c: Horizontal(g223,g233)
    c: Horizontal(g233,g229)
    c: Horizontal(g229,g228)
    c: Equal(g224,g225)
    c: Equal(g229,g230)
    c: Equal(g225,g229)
    c: Tangent(g235,g237) = 1.5708
    c: Tangent(g235,g238) = -1.5708
    c: Tangent(g236,g237) = 1.5708
    c: Tangent(g236,g238) = -1.5708
    c: Coincident(g236,g234)
    c: Tangent(g240,g242) = 1.5708
    c: Tangent(g240,g243) = -1.5708
    c: Tangent(g241,g242) = 1.5708
    c: Tangent(g241,g243) = -1.5708
    c: Coincident(g241,g239)
    c: Horizontal(g235,g234)
    c: Horizontal(g234,g244)
    c: Horizontal(g244,g240)
    c: Horizontal(g240,g239)
    c: Equal(g235,g236)
    c: Equal(g240,g241)
    c: Equal(g236,g240)
    c: DistanceX(g244,g239) = 5.5
    c: Tangent(g246,g248) = 1.5708
    c: Tangent(g246,g249) = -1.5708
    c: Tangent(g247,g248) = 1.5708
    c: Tangent(g247,g249) = -1.5708
    c: Coincident(g247,g245)
    c: Tangent(g251,g253) = 1.5708
    c: Tangent(g251,g254) = -1.5708
    c: Tangent(g252,g253) = 1.5708
    c: Tangent(g252,g254) = -1.5708
    c: Coincident(g252,g250)
    c: Horizontal(g246,g245)
    c: Horizontal(g245,g255)
    c: Horizontal(g255,g251)
    c: Horizontal(g251,g250)
    c: Equal(g246,g247)
    c: Equal(g251,g252)
    c: Equal(g247,g251)
    c: DistanceX(g246,g255) = 5.5
    c: DistanceX(g255,g250) = 5.5
    c: Tangent(g257,g259) = 1.5708
    c: Tangent(g257,g260) = -1.5708
    c: Tangent(g258,g259) = 1.5708
    c: Tangent(g258,g260) = -1.5708
    c: Coincident(g258,g256)
    c: Tangent(g262,g264) = 1.5708
    c: Tangent(g262,g265) = -1.5708
    c: Tangent(g263,g264) = 1.5708
    c: Tangent(g263,g265) = -1.5708
    c: Coincident(g263,g261)
    c: Horizontal(g257,g256)
    c: Horizontal(g256,g266)
    c: Horizontal(g266,g262)
    c: Horizontal(g262,g261)
    c: Equal(g257,g258)
    c: Equal(g262,g263)
    c: Equal(g258,g262)
    c: DistanceX(g257,g266) = 5.5
    c: DistanceX(g266,g261) = 5.5
    c: Tangent(g268,g270) = 1.5708
    c: Tangent(g268,g271) = -1.5708
    c: Tangent(g269,g270) = 1.5708
    c: Tangent(g269,g271) = -1.5708
    c: Coincident(g269,g267)
    c: Tangent(g273,g275) = 1.5708
    c: Tangent(g273,g276) = -1.5708
    c: Tangent(g274,g275) = 1.5708
    c: Tangent(g274,g276) = -1.5708
    c: Coincident(g274,g272)
    c: Horizontal(g268,g267)
    c: Horizontal(g267,g277)
    c: Horizontal(g277,g273)
    c: Horizontal(g273,g272)
    c: Equal(g268,g269)
    c: Equal(g273,g274)
    c: Equal(g269,g273)
    c: DistanceX(g268,g277) = 5.5
    c: DistanceX(g277,g272) = 5.5
    c: Tangent(g279,g281) = 1.5708
    c: Tangent(g279,g282) = -1.5708
    c: Tangent(g280,g281) = 1.5708
    c: Tangent(g280,g282) = -1.5708
    c: Coincident(g280,g278)
    c: Tangent(g284,g286) = 1.5708
    c: Tangent(g284,g287) = -1.5708
    c: Tangent(g285,g286) = 1.5708
    c: Tangent(g285,g287) = -1.5708
    c: Coincident(g285,g283)
    c: Horizontal(g279,g278)
    c: Horizontal(g278,g288)
    c: Horizontal(g288,g284)
    c: Horizontal(g284,g283)
    c: Equal(g279,g280)
    c: Equal(g284,g285)
    c: Equal(g280,g284)
    c: DistanceX(g279,g288) = 5.5
    c: DistanceX(g288,g283) = 5.5
    c: Tangent(g290,g292) = 1.5708
    c: Tangent(g290,g293) = -1.5708
    c: Tangent(g291,g292) = 1.5708
    c: Tangent(g291,g293) = -1.5708
    c: Coincident(g291,g289)
    c: Tangent(g295,g297) = 1.5708
    c: Tangent(g295,g298) = -1.5708
    c: Tangent(g296,g297) = 1.5708
    c: Tangent(g296,g298) = -1.5708
    c: Coincident(g296,g294)
    c: Horizontal(g290,g289)
    c: Horizontal(g289,g299)
    c: Horizontal(g299,g295)
    c: Horizontal(g295,g294)
    c: Equal(g290,g291)
    c: Equal(g295,g296)
    c: Equal(g291,g295)
    c: DistanceX(g290,g299) = 5.5
    c: DistanceX(g299,g294) = 5.5
    c: Coincident(g35,g17)
    c: Coincident(g46,g18)
    c: Coincident(g57,g15)
    c: Coincident(g68,g19)
    c: Coincident(g79,g16)
    c: Coincident(g90,g20)
    c: Coincident(g101,g21)
    c: Coincident(g112,g9)
    c: Coincident(g123,g8)
    c: Coincident(g134,g7)
    c: Coincident(g145,g6)
    c: Coincident(g156,g5)
    c: Coincident(g167,g22)
    c: Coincident(g178,g14)
    c: Coincident(g189,g13)
    c: Coincident(g200,g12)
    c: Coincident(g211,g11)
    c: Coincident(g222,g10)
    c: Coincident(g233,g23)
    c: Coincident(g244,g4)
    c: Coincident(g255,g3)
    c: Coincident(g266,g2)
    c: Coincident(g277,g1)
    c: Coincident(g288,g0)
    c: Coincident(g299,g24)
    c: Equal(g35,g46)
    c: Equal(g46,g57)
    c: Equal(g57,g68)
    c: Equal(g68,g79)
    c: Equal(g79,g90)
    c: Equal(g101,g112)
    c: Equal(g112,g123)
    c: Equal(g123,g134)
    c: Equal(g134,g145)
    c: Equal(g145,g156)
    c: Equal(g167,g178)
    c: Equal(g178,g189)
    c: Equal(g189,g200)
    c: Equal(g200,g211)
    c: Equal(g211,g222)
    c: Equal(g233,g244)
    c: Equal(g244,g255)
    c: Equal(g255,g266)
    c: Equal(g266,g277)
    c: Equal(g277,g288)
    c: Equal(g288,g299)
    c: Diameter(g299) = 4
    c: Equal(g90,g156)
    c: Equal(g156,g222)
    c: Equal(g222,g288)
    c: Diameter(g290) = 2
    c: Equal(g26,g37)
    c: Equal(g37,g48)
    c: Equal(g48,g59)
    c: Equal(g59,g70)
    c: Equal(g70,g81)
    c: Equal(g92,g103)
    c: Equal(g103,g114)
    c: Equal(g114,g125)
    c: Equal(g125,g136)
    c: Equal(g136,g147)
    c: Equal(g158,g169)
    c: Equal(g169,g180)
    c: Equal(g180,g191)
    c: Equal(g191,g202)
    c: Equal(g202,g213)
    c: Equal(g224,g235)
    c: Equal(g235,g246)
    c: Equal(g246,g257)
    c: Equal(g257,g268)
    c: Equal(g268,g279)
    c: Equal(g279,g290)
    c: Equal(g81,g147)
    c: Equal(g147,g213)
    c: Equal(g213,g279)
    c: Vertical(g26,g92)
    c: Vertical(g92,g158)
    c: Vertical(g158,g224)
    c: Vertical(g25,g91)
    c: Vertical(g91,g157)
    c: Vertical(g157,g223)
    c: Vertical(g31,g97)
    c: Vertical(g97,g163)
    c: Vertical(g163,g229)
    c: Vertical(g30,g96)
    c: Vertical(g96,g162)
    c: Vertical(g162,g228)
    c: Vertical(g37,g103)
    c: Vertical(g103,g169)
    c: Vertical(g169,g235)
    c: Vertical(g36,g102)
    c: Vertical(g102,g168)
    c: Vertical(g168,g234)
    c: DistanceX(g224,g23) = 5.5
    c: DistanceX(g23,g228) = 5.5
    c: DistanceX(g223,g23) = 5.08
    c: DistanceX(g23,g229) = 5.08
    c: DistanceX(g235,g4) = 5.5
    c: DistanceX(g4,g240) = 5.08
    c: DistanceX(g234,g4) = 5.08
    c: DistanceX(g289,g24) = 5.08
    c: DistanceX(g24,g295) = 5.08
    c: DistanceX(g245,g3) = 5.08
    c: DistanceX(g3,g251) = 5.08
    c: DistanceX(g256,g2) = 5.08
    c: DistanceX(g2,g262) = 5.08
    c: DistanceX(g267,g1) = 5.08
    c: DistanceX(g1,g273) = 5.08
    c: DistanceX(g278,g0) = 5.08
    c: DistanceX(g0,g284) = 5.08
    c: Vertical(g42,g108)
    c: Vertical(g108,g174)
    c: Vertical(g174,g240)
    c: Vertical(g41,g107)
    c: Vertical(g107,g173)
    c: Vertical(g173,g239)
    c: Vertical(g48,g114)
    c: Vertical(g114,g180)
    c: Vertical(g180,g246)
    c: Vertical(g47,g113)
    c: Vertical(g113,g179)
    c: Vertical(g179,g245)
    c: Vertical(g53,g119)
    c: Vertical(g119,g185)
    c: Vertical(g185,g251)
    c: Vertical(g52,g118)
    c: Vertical(g118,g184)
    c: Vertical(g184,g250)
    c: Vertical(g59,g125)
    c: Vertical(g125,g191)
    c: Vertical(g191,g257)
    c: Vertical(g58,g124)
    c: Vertical(g124,g190)
    c: Vertical(g190,g256)
    c: Vertical(g64,g130)
    c: Vertical(g130,g196)
    c: Vertical(g196,g262)
    c: Vertical(g63,g129)
    c: Vertical(g129,g195)
    c: Vertical(g195,g261)
    c: Vertical(g70,g136)
    c: Vertical(g136,g202)
    c: Vertical(g202,g268)
    c: Vertical(g69,g135)
    c: Vertical(g135,g201)
    c: Vertical(g201,g267)
    c: Vertical(g75,g141)
    c: Vertical(g141,g207)
    c: Vertical(g207,g273)
    c: Vertical(g74,g140)
    c: Vertical(g140,g206)
    c: Vertical(g206,g272)
    c: Vertical(g81,g147)
    c: Vertical(g147,g213)
    c: Vertical(g213,g279)
    c: Vertical(g80,g146)
    c: Vertical(g146,g212)
    c: Vertical(g212,g278)
    c: Vertical(g86,g152)
    c: Vertical(g152,g218)
    c: Vertical(g218,g284)
    c: Vertical(g85,g151)
    c: Vertical(g151,g217)
    c: Vertical(g217,g283)
FEATURE [Image::ImagePlane] SplitKB_BL
  Placement = pos=(-76.3,38,-0.1) rot=(0,1,0;3.14159rad)
  XSize = 132.3
  YSize = 94.8
FEATURE [Image::ImagePlane] SplitKB_BR
  Placement = pos=(76.2018,38.0495,-0.1) rot=(0.002618,-0.999997,0;3.14159rad)
  XSize = 132.188
  YSize = 95.3188
FEATURE [Sketcher::SketchObject] Sketch039  label="TL-ScrewPostOut"
  ArcFitTolerance = 1e-06
  AttachmentSupport = -> [XY_Plane]
  FullyConstrained = true
  MakeInternals = false
  MapMode = 5
  expr: Constraints[15] = VarSet.Screw_PostOutD
  expr: Constraints[16] = 1.5 * 19.05 mm
  expr: Constraints[17] = 19.05 mm / 2
  expr: Constraints[49] = 2.5 * 19.05 mm
  expr: Constraints[50] = 19.05 mm + VarSet.Screw_RearAdd
  sketch-geometry (17):
    g0: Circle CenterX=-123.825 CenterY=28.575 CenterZ=0 NormalX=0 NormalY=0 NormalZ=1 AngleXU=0 Radius=1.75
    g1: Circle CenterX=-123.825 CenterY=66.675 CenterZ=0 NormalX=0 NormalY=0 NormalZ=1 AngleXU=0 Radius=1.75
    g2: Circle CenterX=-85.725 CenterY=66.675 CenterZ=0 NormalX=0 NormalY=0 NormalZ=1 AngleXU=0 Radius=1.75
    g3: Circle CenterX=-85.725 CenterY=28.575 CenterZ=0 NormalX=0 NormalY=0 NormalZ=1 AngleXU=0 Radius=1.75
    g4: Circle CenterX=-47.625 CenterY=28.575 CenterZ=0 NormalX=0 NormalY=0 NormalZ=1 AngleXU=0 Radius=1.75
    g5: Circle CenterX=-47.625 CenterY=66.675 CenterZ=0 NormalX=0 NormalY=0 NormalZ=1 AngleXU=0 Radius=1.75
    g6: Circle CenterX=-123.825 CenterY=9.525 CenterZ=0 NormalX=0 NormalY=0 NormalZ=1 AngleXU=0 Radius=1.75
    g7: Circle CenterX=-104.775 CenterY=9.525 CenterZ=0 NormalX=0 NormalY=0 NormalZ=1 AngleXU=0 Radius=1.75
    g8: Circle CenterX=-85.725 CenterY=9.525 CenterZ=0 NormalX=0 NormalY=0 NormalZ=1 AngleXU=0 Radius=1.75
    g9: Circle CenterX=-66.675 CenterY=9.525 CenterZ=0 NormalX=0 NormalY=0 NormalZ=1 AngleXU=0 Radius=1.75
    g10: Circle CenterX=-47.625 CenterY=9.525 CenterZ=0 NormalX=0 NormalY=0 NormalZ=1 AngleXU=0 Radius=1.75
    g11: Circle CenterX=-28.575 CenterY=9.525 CenterZ=0 NormalX=0 NormalY=0 NormalZ=1 AngleXU=0 Radius=1.75
    g12: Circle CenterX=-123.825 CenterY=88.225 CenterZ=0 NormalX=0 NormalY=0 NormalZ=1 AngleXU=0 Radius=1.75
    g13: Circle CenterX=-104.775 CenterY=88.225 CenterZ=0 NormalX=0 NormalY=0 NormalZ=1 AngleXU=0 Radius=1.75
    g14: Circle CenterX=-85.725 CenterY=88.225 CenterZ=0 NormalX=0 NormalY=0 NormalZ=1 AngleXU=0 Radius=1.75
    g15: Circle CenterX=-66.675 CenterY=88.225 CenterZ=0 NormalX=0 NormalY=0 NormalZ=1 AngleXU=0 Radius=1.75
    g16: Circle CenterX=-47.625 CenterY=88.225 CenterZ=0 NormalX=0 NormalY=0 NormalZ=1 AngleXU=0 Radius=1.75
  constraints (51):
    c: Horizontal(g6,g7)
    c: Horizontal(g7,g8)
    c: Horizontal(g8,g9)
    c: Horizontal(g9,g10)
    c: Horizontal(g10,g11)
    c: DistanceX(g10,g11) = 19.05
    c: DistanceX(g9,g10) = 19.05
    c: DistanceX(g8,g9) = 19.05
    c: DistanceX(g7,g8) = 19.05
    c: DistanceX(g6,g7) = 19.05
    c: Equal(g6,g7)
    c: Equal(g7,g8)
    c: Equal(g8,g9)
    c: Equal(g9,g10)
    c: Equal(g10,g11)
    c: Diameter(g11) = 3.5
    c: DistanceX(g11,g-1) = 28.575
    c: DistanceY(g-1,g11) = 9.525
    c: DistanceY(g11,g4) = 19.05
    c: DistanceY(g4,g5) = 38.1
    c: Horizontal(g1,g2)
    c: Horizontal(g2,g5)
    c: Horizontal(g0,g3)
    c: Horizontal(g3,g4)
    c: Vertical(g1,g0)
    c: Vertical(g0,g6)
    c: Vertical(g2,g3)
    c: Vertical(g3,g8)
    c: Vertical(g5,g4)
    c: Vertical(g4,g10)
    c: Equal(g1,g2)
    c: Equal(g2,g5)
    c: Equal(g0,g3)
    c: Equal(g3,g4)
    c: Equal(g5,g4)
    c: Equal(g4,g10)
    c: Horizontal(g12,g13)
    c: Horizontal(g13,g14)
    c: Horizontal(g14,g15)
    c: Equal(g12,g13)
    c: Equal(g13,g14)
    c: Equal(g14,g15)
    c: Equal(g15,g16)
    c: Equal(g16,g5)
    c: Horizontal(g15,g16)
    c: DistanceX(g12,g13) = 19.05
    c: DistanceX(g13,g14) = 19.05
    c: DistanceX(g14,g15) = 19.05
    c: DistanceX(g15,g16) = 19.05
    c: DistanceX(g16,g-1) = 47.625
    c: DistanceY(g5,g16) = 21.55
FEATURE [Sketcher::SketchObject] Sketch040  label="TR-ScrewPostOut"
  ArcFitTolerance = 1e-06
  AttachmentSupport = -> [XY_Plane002]
  FullyConstrained = true
  MakeInternals = false
  MapMode = 5
  expr: Constraints[10] = 1.5 * 19.05 mm
  expr: Constraints[32] = 19.05 mm / 2
  expr: Constraints[35] = VarSet.Screw_PostOutD
  expr: Constraints[48] = 19.05 mm + VarSet.Screw_RearAdd
  expr: Constraints[49] = 2.5 * 19.05 mm
  sketch-geometry (17):
    g0: Circle CenterX=123.825 CenterY=28.575 CenterZ=0 NormalX=0 NormalY=0 NormalZ=1 AngleXU=0 Radius=1.75
    g1: Circle CenterX=123.825 CenterY=66.675 CenterZ=0 NormalX=0 NormalY=0 NormalZ=1 AngleXU=0 Radius=1.75
    g2: Circle CenterX=85.725 CenterY=66.675 CenterZ=0 NormalX=0 NormalY=0 NormalZ=1 AngleXU=0 Radius=1.75
    g3: Circle CenterX=85.725 CenterY=28.575 CenterZ=0 NormalX=0 NormalY=0 NormalZ=1 AngleXU=0 Radius=1.75
    g4: Circle CenterX=47.625 CenterY=28.575 CenterZ=0 NormalX=0 NormalY=0 NormalZ=1 AngleXU=0 Radius=1.75
    g5: Circle CenterX=47.625 CenterY=66.675 CenterZ=0 NormalX=0 NormalY=0 NormalZ=1 AngleXU=0 Radius=1.75
    g6: Circle CenterX=28.575 CenterY=9.525 CenterZ=0 NormalX=0 NormalY=0 NormalZ=1 AngleXU=0 Radius=1.75
    g7: Circle CenterX=47.625 CenterY=9.525 CenterZ=0 NormalX=0 NormalY=0 NormalZ=1 AngleXU=0 Radius=1.75
    g8: Circle CenterX=66.675 CenterY=9.525 CenterZ=0 NormalX=0 NormalY=0 NormalZ=1 AngleXU=0 Radius=1.75
    g9: Circle CenterX=85.725 CenterY=9.525 CenterZ=0 NormalX=0 NormalY=0 NormalZ=1 AngleXU=0 Radius=1.75
    g10: Circle CenterX=104.775 CenterY=9.525 CenterZ=0 NormalX=0 NormalY=0 NormalZ=1 AngleXU=0 Radius=1.75
    g11: Circle CenterX=123.825 CenterY=9.525 CenterZ=0 NormalX=0 NormalY=0 NormalZ=1 AngleXU=0 Radius=1.75
    g12: Circle CenterX=47.625 CenterY=88.225 CenterZ=0 NormalX=0 NormalY=0 NormalZ=1 AngleXU=0 Radius=1.75
    g13: Circle CenterX=66.675 CenterY=88.225 CenterZ=0 NormalX=0 NormalY=0 NormalZ=1 AngleXU=0 Radius=1.75
    g14: Circle CenterX=85.725 CenterY=88.225 CenterZ=0 NormalX=0 NormalY=0 NormalZ=1 AngleXU=0 Radius=1.75
    g15: Circle CenterX=104.775 CenterY=88.225 CenterZ=0 NormalX=0 NormalY=0 NormalZ=1 AngleXU=0 Radius=1.75
    g16: Circle CenterX=123.825 CenterY=88.225 CenterZ=0 NormalX=0 NormalY=0 NormalZ=1 AngleXU=0 Radius=1.75
  constraints (51):
    c: Horizontal(g6,g7)
    c: Horizontal(g7,g8)
    c: Horizontal(g8,g9)
    c: Horizontal(g9,g10)
    c: Horizontal(g10,g11)
    c: DistanceX(g10,g11) = 19.05
    c: DistanceX(g9,g10) = 19.05
    c: DistanceX(g8,g9) = 19.05
    c: DistanceX(g7,g8) = 19.05
    c: DistanceX(g6,g7) = 19.05
    c: DistanceX(g-1,g6) = 28.575
    c: Horizontal(g1,g2)
    c: Horizontal(g2,g5)
    c: Horizontal(g0,g3)
    c: Horizontal(g3,g4)
    c: Vertical(g1,g0)
    c: Vertical(g0,g11)
    c: Vertical(g2,g3)
    c: Vertical(g3,g9)
    c: Vertical(g5,g4)
    c: Vertical(g4,g7)
    c: Equal(g11,g10)
    c: Equal(g10,g9)
    c: Equal(g9,g8)
    c: Equal(g8,g7)
    c: Equal(g7,g6)
    c: Equal(g1,g2)
    c: Equal(g2,g5)
    c: Equal(g0,g3)
    c: Equal(g3,g4)
    c: Equal(g5,g4)
    c: Equal(g4,g7)
    c: DistanceY(g-1,g6) = 9.525
    c: DistanceY(g6,g4) = 19.05
    c: DistanceY(g4,g5) = 38.1
    c: Diameter(g6) = 3.5
    c: Horizontal(g12,g13)
    c: Horizontal(g13,g14)
    c: Horizontal(g14,g15)
    c: Horizontal(g15,g16)
    c: Equal(g12,g13)
    c: Equal(g13,g14)
    c: Equal(g14,g15)
    c: Equal(g15,g16)
    c: DistanceX(g12,g13) = 19.05
    c: DistanceX(g13,g14) = 19.05
    c: DistanceX(g14,g15) = 19.05
    c: DistanceX(g15,g16) = 19.05
    c: DistanceY(g5,g12) = 21.55
    c: DistanceX(g-1,g12) = 47.625
    c: Equal(g12,g5)
FEATURE [Sketcher::SketchObject] Sketch041  label="BL-Resistor"
  ArcFitTolerance = 1e-06
  AttachmentSupport = -> [XY_Plane001]
  FullyConstrained = true
  MakeInternals = false
  MapMode = 5
  sketch-geometry (11):
    g0: GeomPoint X=-27.39 Y=42.475 Z=0
    g1: GeomPoint X=-24.85 Y=42.475 Z=0
    g2: GeomPoint X=-26.1 Y=44.675 Z=0
    g3: GeomPoint X=-5 Y=47.625 Z=0
    g4: LineSegment StartX=-23.85 StartY=43.675 StartZ=0 EndX=-23.85 EndY=38.475 EndZ=0
    g5: LineSegment StartX=-23.85 StartY=38.475 StartZ=0 EndX=-28.39 EndY=38.475 EndZ=0
    g6: LineSegment StartX=-28.39 StartY=38.475 StartZ=0 EndX=-28.39 EndY=43.475 EndZ=0
    g7: LineSegment StartX=-28.39 StartY=43.475 StartZ=0 EndX=-27.1 EndY=45.675 EndZ=0
    g8: LineSegment StartX=-27.1 StartY=45.675 StartZ=0 EndX=-21.1 EndY=45.675 EndZ=0
    g9: LineSegment StartX=-21.1 StartY=45.675 StartZ=0 EndX=-21.1 EndY=43.675 EndZ=0
    g10: LineSegment StartX=-21.1 StartY=43.675 StartZ=0 EndX=-23.85 EndY=43.675 EndZ=0
  constraints (29):
    c: Horizontal(g0,g1)
    c: DistanceX(g3,g-1) = 5
    c: DistanceY(g-1,g3) = 47.625
    c: DistanceX(g1,g3) = 19.85
    c: DistanceY(g1,g3) = 5.15
    c: DistanceX(g0,g1) = 2.54
    c: Vertical(g4)
    c: Coincident(g4,g5)
    c: Horizontal(g5)
    c: Coincident(g5,g6)
    c: Vertical(g6)
    c: Coincident(g6,g7)
    c: Coincident(g7,g8)
    c: Horizontal(g8)
    c: Coincident(g8,g9)
    c: Vertical(g9)
    c: Coincident(g9,g10)
    c: Coincident(g10,g4)
    c: Horizontal(g10)
    c: DistanceX(g1,g4) = 1
    c: DistanceY(g1,g4) = 1.2
    c: DistanceY(g4,g1) = 4
    c: DistanceX(g6,g0) = 1
    c: DistanceY(g1,g2) = 2.2
    c: DistanceY(g0,g6) = 1
    c: DistanceX(g2,g1) = 1.25
    c: DistanceX(g2,g8) = 5
    c: DistanceX(g7,g2) = 1
    c: DistanceY(g2,g7) = 1
FEATURE [Sketcher::SketchObject] Sketch042  label="BR-Resistor"
  ArcFitTolerance = 1e-06
  AttachmentSupport = -> [XY_Plane003]
  FullyConstrained = true
  MakeInternals = false
  MapMode = 5
  expr: Constraints[1] = 2.5 * 19.05 mm
  sketch-geometry (14):
    g0: GeomPoint X=5 Y=47.625 Z=0
    g1: GeomPoint X=24.3 Y=42.475 Z=0
    g2: LineSegment StartX=23.3 StartY=45.2446 StartZ=0 EndX=23.3 EndY=38.475 EndZ=0
    g3: LineSegment StartX=23.3 StartY=38.475 StartZ=0 EndX=27.84 EndY=38.475 EndZ=0
    g4: LineSegment StartX=27.84 StartY=38.475 StartZ=0 EndX=27.84 EndY=44.475 EndZ=0
    g5: LineSegment StartX=27.84 StartY=44.475 StartZ=0 EndX=24.3 EndY=48.335 EndZ=0
    g6: LineSegment StartX=24.3 StartY=48.335 StartZ=0 EndX=22.3 EndY=48.335 EndZ=0
    g7: LineSegment StartX=22.3 StartY=48.335 StartZ=0 EndX=22.3 EndY=46.335 EndZ=0
    g8: GeomPoint [constr] X=23.3 Y=47.335 Z=0
    g9: GeomPoint [constr] X=24.3 Y=48.335 Z=0
    g10: GeomPoint [constr] X=22.3 Y=46.335 Z=0
    g11: GeomPoint [constr] X=23.3 Y=38.475 Z=0
    g12: GeomPoint X=26.84 Y=42.475 Z=0
    g13: LineSegment StartX=22.3 StartY=46.335 StartZ=0 EndX=23.3 EndY=45.2446 EndZ=0
  constraints (35):
    c: DistanceX(g-1,g0) = 5
    c: DistanceY(g-1,g0) = 47.625
    c: DistanceY(g1,g0) = 5.15
    c: DistanceX(g0,g1) = 19.3
    c: Vertical(g2)
    c: Horizontal(g3)
    c: Vertical(g4)
    c: Vertical(g7)
    c: Horizontal(g6)
    c: DistanceX(g8,g9) = 1
    c: DistanceY(g10,g8) = 1
    c: DistanceY(g11,g1) = 4
    c: PointOnObject(g9,g6)
    c: PointOnObject(g10,g7)
    c: PointOnObject(g11,g2)
    c: PointOnObject(g11,g3)
    c: DistanceX(g1,g12) = 2.54
    c: Coincident(g5,g4)
    c: Coincident(g4,g3)
    c: Coincident(g2,g3)
    c: Horizontal(g1,g12)
    c: Coincident(g9,g5)
    c: PointOnObject(g6,g5)
    c: Coincident(g6,g7)
    c: Coincident(g13,g10)
    c: Parallel(g13,g5)
    c: Coincident(g13,g2)
    c: DistanceX(g2,g1) = 1
    c: DistanceX(g12,g4) = 1
    c: DistanceY(g12,g4) = 2
    c: DistanceY(g1,g8) = 4.86
    c: DistanceX(g8,g1) = 1
    c: DistanceX(g6,g8) = 1
    c: PointOnObject(g7,g13)
    c: DistanceY(g8,g6) = 1
FEATURE [Sketcher::SketchObject] Sketch043  label="BL-ScrewClearance"
  ArcFitTolerance = 1e-06
  AttachmentOffset = pos=(0,0,1.5) rot=(0,0,1;0rad)
  AttachmentSupport = -> [XY_Plane001]
  FullyConstrained = true
  MakeInternals = false
  MapMode = 5
  Placement = pos=(0,0,1.5) rot=(0,0,1;0rad)
  expr: .AttachmentOffset.Base.z = VarSet.Top_PcbZ
  expr: Constraints[15] = VarSet.Screw_ClearanceD
  expr: Constraints[16] = 1.5 * 19.05 mm
  expr: Constraints[17] = 19.05 mm / 2
  expr: Constraints[48] = 19.05 mm + VarSet.Screw_RearAdd
  expr: Constraints[54] = 1.5 * 19.05 mm
  sketch-geometry (20):
    g0: Circle CenterX=-123.825 CenterY=28.575 CenterZ=0 NormalX=0 NormalY=0 NormalZ=1 AngleXU=0 Radius=1.075
    g1: Circle CenterX=-123.825 CenterY=66.675 CenterZ=0 NormalX=0 NormalY=0 NormalZ=1 AngleXU=0 Radius=1.075
    g2: Circle CenterX=-85.725 CenterY=66.675 CenterZ=0 NormalX=0 NormalY=0 NormalZ=1 AngleXU=0 Radius=1.075
    g3: Circle CenterX=-85.725 CenterY=28.575 CenterZ=0 NormalX=0 NormalY=0 NormalZ=1 AngleXU=0 Radius=1.075
    g4: Circle CenterX=-47.625 CenterY=28.575 CenterZ=0 NormalX=0 NormalY=0 NormalZ=1 AngleXU=0 Radius=1.075
    g5: Circle CenterX=-47.625 CenterY=66.675 CenterZ=0 NormalX=0 NormalY=0 NormalZ=1 AngleXU=0 Radius=1.075
    g6: Circle CenterX=-123.825 CenterY=9.525 CenterZ=0 NormalX=0 NormalY=0 NormalZ=1 AngleXU=0 Radius=1.075
    g7: Circle CenterX=-104.775 CenterY=9.525 CenterZ=0 NormalX=0 NormalY=0 NormalZ=1 AngleXU=0 Radius=1.075
    g8: Circle CenterX=-85.725 CenterY=9.525 CenterZ=0 NormalX=0 NormalY=0 NormalZ=1 AngleXU=0 Radius=1.075
    g9: Circle CenterX=-66.675 CenterY=9.525 CenterZ=0 NormalX=0 NormalY=0 NormalZ=1 AngleXU=0 Radius=1.075
    g10: Circle CenterX=-47.625 CenterY=9.525 CenterZ=0 NormalX=0 NormalY=0 NormalZ=1 AngleXU=0 Radius=1.075
    g11: Circle CenterX=-28.575 CenterY=9.525 CenterZ=0 NormalX=0 NormalY=0 NormalZ=1 AngleXU=0 Radius=1.075
    g12: Circle CenterX=-123.825 CenterY=88.225 CenterZ=0 NormalX=0 NormalY=0 NormalZ=1 AngleXU=0 Radius=1.075
    g13: Circle CenterX=-104.775 CenterY=88.225 CenterZ=0 NormalX=0 NormalY=0 NormalZ=1 AngleXU=0 Radius=1.075
    g14: Circle CenterX=-85.725 CenterY=88.225 CenterZ=0 NormalX=0 NormalY=0 NormalZ=1 AngleXU=0 Radius=1.075
    g15: Circle CenterX=-66.675 CenterY=88.225 CenterZ=0 NormalX=0 NormalY=0 NormalZ=1 AngleXU=0 Radius=1.075
    g16: Circle CenterX=-47.625 CenterY=88.225 CenterZ=0 NormalX=0 NormalY=0 NormalZ=1 AngleXU=0 Radius=1.075
    g17: Circle CenterX=-11.43 CenterY=88.225 CenterZ=0 NormalX=0 NormalY=0 NormalZ=1 AngleXU=0 Radius=1.075
    g18: Circle CenterX=-26.67 CenterY=88.225 CenterZ=0 NormalX=0 NormalY=0 NormalZ=1 AngleXU=0 Radius=1.075
    g19: GeomPoint X=-19.05 Y=88.225 Z=0
  constraints (58):
    c: Horizontal(g6,g7)
    c: Horizontal(g7,g8)
    c: Horizontal(g8,g9)
    c: Horizontal(g9,g10)
    c: Horizontal(g10,g11)
    c: DistanceX(g10,g11) = 19.05
    c: DistanceX(g9,g10) = 19.05
    c: DistanceX(g8,g9) = 19.05
    c: DistanceX(g7,g8) = 19.05
    c: DistanceX(g6,g7) = 19.05
    c: Equal(g6,g7)
    c: Equal(g7,g8)
    c: Equal(g8,g9)
    c: Equal(g9,g10)
    c: Equal(g10,g11)
    c: Diameter(g11) = 2.15
    c: DistanceX(g11,g-1) = 28.575
    c: DistanceY(g-1,g11) = 9.525
    c: DistanceY(g11,g4) = 19.05
    c: DistanceY(g4,g5) = 38.1
    c: Horizontal(g1,g2)
    c: Horizontal(g2,g5)
    c: Horizontal(g0,g3)
    c: Horizontal(g3,g4)
    c: Vertical(g1,g0)
    c: Vertical(g0,g6)
    c: Vertical(g2,g3)
    c: Vertical(g3,g8)
    c: Vertical(g5,g4)
    c: Vertical(g4,g10)
    c: Equal(g1,g2)
    c: Equal(g2,g5)
    c: Equal(g0,g3)
    c: Equal(g3,g4)
    c: Equal(g5,g4)
    c: Equal(g4,g10)
    c: Horizontal(g12,g13)
    c: Horizontal(g13,g14)
    c: Horizontal(g14,g15)
    c: Equal(g12,g13)
    c: Equal(g13,g14)
    c: Equal(g14,g15)
    c: Equal(g15,g16)
    c: Horizontal(g15,g16)
    c: DistanceX(g12,g13) = 19.05
    c: DistanceX(g13,g14) = 19.05
    c: DistanceX(g14,g15) = 19.05
    c: DistanceX(g15,g16) = 19.05
    c: DistanceY(g5,g16) = 21.55
    c: Equal(g16,g5)
    c: Equal(g18,g17)
    c: Symmetric(g18,g17,g19)
    c: Horizontal(g18,g17)
    c: Equal(g16,g18)
    c: DistanceX(g16,g19) = 28.575
    c: DistanceX(g19,g-1) = 19.05
    c: DistanceX(g18,g19) = 7.62
    c: Horizontal(g16,g19)
FEATURE [Sketcher::SketchObject] Sketch044  label="BR-ScrewClearance"
  ArcFitTolerance = 1e-06
  AttachmentOffset = pos=(0,0,1.5) rot=(0,0,1;0rad)
  AttachmentSupport = -> [XY_Plane003]
  FullyConstrained = true
  MakeInternals = false
  MapMode = 5
  Placement = pos=(0,0,1.5) rot=(0,0,1;0rad)
  expr: .AttachmentOffset.Base.z = VarSet.Top_PcbZ
  expr: Constraints[10] = 1.5 * 19.05 mm
  expr: Constraints[32] = 19.05 mm / 2
  expr: Constraints[35] = VarSet.Screw_ClearanceD
  expr: Constraints[49] = 19.05 mm + VarSet.Screw_RearAdd
  expr: Constraints[54] = 1.5 * 19.05 mm
  sketch-geometry (20):
    g0: Circle CenterX=123.825 CenterY=28.575 CenterZ=0 NormalX=0 NormalY=0 NormalZ=1 AngleXU=0 Radius=1.075
    g1: Circle CenterX=123.825 CenterY=66.675 CenterZ=0 NormalX=0 NormalY=0 NormalZ=1 AngleXU=0 Radius=1.075
    g2: Circle CenterX=85.725 CenterY=66.675 CenterZ=0 NormalX=0 NormalY=0 NormalZ=1 AngleXU=0 Radius=1.075
    g3: Circle CenterX=85.725 CenterY=28.575 CenterZ=0 NormalX=0 NormalY=0 NormalZ=1 AngleXU=0 Radius=1.075
    g4: Circle CenterX=47.625 CenterY=28.575 CenterZ=0 NormalX=0 NormalY=0 NormalZ=1 AngleXU=0 Radius=1.075
    g5: Circle CenterX=47.625 CenterY=66.675 CenterZ=0 NormalX=0 NormalY=0 NormalZ=1 AngleXU=0 Radius=1.075
    g6: Circle CenterX=28.575 CenterY=9.525 CenterZ=0 NormalX=0 NormalY=0 NormalZ=1 AngleXU=0 Radius=1.075
    g7: Circle CenterX=47.625 CenterY=9.525 CenterZ=0 NormalX=0 NormalY=0 NormalZ=1 AngleXU=0 Radius=1.075
    g8: Circle CenterX=66.675 CenterY=9.525 CenterZ=0 NormalX=0 NormalY=0 NormalZ=1 AngleXU=0 Radius=1.075
    g9: Circle CenterX=85.725 CenterY=9.525 CenterZ=0 NormalX=0 NormalY=0 NormalZ=1 AngleXU=0 Radius=1.075
    g10: Circle CenterX=104.775 CenterY=9.525 CenterZ=0 NormalX=0 NormalY=0 NormalZ=1 AngleXU=0 Radius=1.075
    g11: Circle CenterX=123.825 CenterY=9.525 CenterZ=0 NormalX=0 NormalY=0 NormalZ=1 AngleXU=0 Radius=1.075
    g12: Circle CenterX=47.625 CenterY=88.225 CenterZ=0 NormalX=0 NormalY=0 NormalZ=1 AngleXU=0 Radius=1.075
    g13: Circle CenterX=66.675 CenterY=88.225 CenterZ=0 NormalX=0 NormalY=0 NormalZ=1 AngleXU=0 Radius=1.075
    g14: Circle CenterX=85.725 CenterY=88.225 CenterZ=0 NormalX=0 NormalY=0 NormalZ=1 AngleXU=0 Radius=1.075
    g15: Circle CenterX=104.775 CenterY=88.225 CenterZ=0 NormalX=0 NormalY=0 NormalZ=1 AngleXU=0 Radius=1.075
    g16: Circle CenterX=123.825 CenterY=88.225 CenterZ=0 NormalX=0 NormalY=0 NormalZ=1 AngleXU=0 Radius=1.075
    g17: Circle CenterX=26.67 CenterY=88.225 CenterZ=0 NormalX=0 NormalY=0 NormalZ=1 AngleXU=0 Radius=1.075
    g18: Circle CenterX=11.43 CenterY=88.225 CenterZ=0 NormalX=0 NormalY=0 NormalZ=1 AngleXU=0 Radius=1.075
    g19: GeomPoint X=19.05 Y=88.225 Z=0
  constraints (58):
    c: Horizontal(g6,g7)
    c: Horizontal(g7,g8)
    c: Horizontal(g8,g9)
    c: Horizontal(g9,g10)
    c: Horizontal(g10,g11)
    c: DistanceX(g10,g11) = 19.05
    c: DistanceX(g9,g10) = 19.05
    c: DistanceX(g8,g9) = 19.05
    c: DistanceX(g7,g8) = 19.05
    c: DistanceX(g6,g7) = 19.05
    c: DistanceX(g-1,g6) = 28.575
    c: Horizontal(g1,g2)
    c: Horizontal(g2,g5)
    c: Horizontal(g0,g3)
    c: Horizontal(g3,g4)
    c: Vertical(g1,g0)
    c: Vertical(g0,g11)
    c: Vertical(g2,g3)
    c: Vertical(g3,g9)
    c: Vertical(g5,g4)
    c: Vertical(g4,g7)
    c: Equal(g11,g10)
    c: Equal(g10,g9)
    c: Equal(g9,g8)
    c: Equal(g8,g7)
    c: Equal(g7,g6)
    c: Equal(g1,g2)
    c: Equal(g2,g5)
    c: Equal(g0,g3)
    c: Equal(g3,g4)
    c: Equal(g5,g4)
    c: Equal(g4,g7)
    c: DistanceY(g-1,g6) = 9.525
    c: DistanceY(g6,g4) = 19.05
    c: DistanceY(g4,g5) = 38.1
    c: Diameter(g6) = 2.15
    c: Horizontal(g12,g13)
    c: Horizontal(g13,g14)
    c: Horizontal(g14,g15)
    c: Horizontal(g15,g16)
    c: Equal(g12,g13)
    c: Equal(g13,g14)
    c: Equal(g14,g15)
    c: Equal(g15,g16)
    c: DistanceX(g12,g13) = 19.05
    c: DistanceX(g13,g14) = 19.05
    c: DistanceX(g14,g15) = 19.05
    c: DistanceX(g15,g16) = 19.05
    c: Equal(g12,g5)
    c: DistanceY(g5,g12) = 21.55
    c: Equal(g18,g17)
    c: Symmetric(g18,g17,g19)
    c: Horizontal(g18,g17)
    c: DistanceX(g18,g19) = 7.62
    c: DistanceX(g19,g12) = 28.575
    c: DistanceX(g-1,g19) = 19.05
    c: Horizontal(g19,g12)
    c: Equal(g17,g12)
FEATURE [Sketcher::SketchObject] Sketch049  label="OL-Base"
  ArcFitTolerance = 1e-06
  AttachmentSupport = -> [XY_Plane006]
  FullyConstrained = true
  MakeInternals = false
  MapMode = 5
  expr: Constraints[13] = 19.05 mm / 2
  expr: Constraints[14] = 1.75 mm / 2
  expr: Constraints[16] = VarSet.Top_MedXY / 2 + VarSet.Top_Frame
  sketch-geometry (7):
    g0: GeomPoint X=-19.05 Y=19.05 Z=0
    g1: LineSegment StartX=-7.15 StartY=46.3 StartZ=0 EndX=-27.7 EndY=46.3 EndZ=0
    g2: LineSegment StartX=-27.7 StartY=46.3 StartZ=0 EndX=-27.7 EndY=29.9 EndZ=0
    g3: LineSegment StartX=-27.7 StartY=29.9 StartZ=0 EndX=-7.15 EndY=29.9 EndZ=0
    g4: LineSegment StartX=-7.15 StartY=29.9 StartZ=0 EndX=-7.15 EndY=46.3 EndZ=0
    g5: GeomPoint [constr] X=-17.425 Y=38.1 Z=0
    g6: GeomPoint X=-28.575 Y=19.05 Z=0
  constraints (17):
    c: DistanceX(g0,g-1) = 19.05
    c: DistanceY(g-1,g0) = 19.05
    c: Coincident(g1,g2)
    c: Coincident(g2,g3)
    c: Coincident(g3,g4)
    c: Coincident(g4,g1)
    c: Horizontal(g1)
    c: Horizontal(g3)
    c: Vertical(g2)
    c: Vertical(g4)
    c: Symmetric(g3,g1,g5)
    c: DistanceY(g0,g5) = 19.05
    c: DistanceY(g2,g2) = 16.4
    c: DistanceX(g6,g0) = 9.525
    c: DistanceX(g6,g2) = 0.875
    c: Horizontal(g6,g0)
    c: DistanceX(g0,g3) = 11.9
FEATURE [PartDesign::Pad] Pad017  label="OL-Base-Pad"
  Direction = (0,0,1)
  Length = 14.5
  Length2 = 10
  Profile = -> Sketch049
  ReferenceAxis = -> Sketch049 [N_Axis]
  Refine = true
  Suppressed = false
  Type = 0
FEATURE [Sketcher::SketchObject] Sketch053  label="CR-Out"
  ArcFitTolerance = 1e-06
  AttachmentSupport = -> [XY_Plane005]
  FullyConstrained = true
  MakeInternals = false
  MapMode = 5
  expr: Constraints[11] = VarSet.Top_FrameFilletR
  expr: Constraints[17] = 3 * 19.05 mm
  expr: Constraints[18] = VarSet.Top_MedXY / 2 + VarSet.Top_Frame + VarSet.Top_RearAdd
  expr: Constraints[19] = 19.05 mm / 2
  expr: Constraints[20] = VarSet.Top_MedXY / 2 + VarSet.Top_Frame
  expr: Constraints[22] = 1.5 * 19.05 mm
  expr: Constraints[23] = VarSet.Cover_FrontAdd
  sketch-geometry (10):
    g0: GeomPoint [constr] X=19.05 Y=19.05 Z=0
    g1: LineSegment StartX=28.575 StartY=91.1 StartZ=0 EndX=28.575 EndY=46.425 EndZ=0
    g2: LineSegment StartX=28.575 StartY=46.425 StartZ=0 EndX=7.15 EndY=46.425 EndZ=0
    g3: LineSegment StartX=7.15 StartY=46.425 StartZ=0 EndX=7.15 EndY=89.1 EndZ=0
    g4: LineSegment StartX=9.15 StartY=91.1 StartZ=0 EndX=28.575 EndY=91.1 EndZ=0
    g5: GeomPoint X=38.1 Y=76.2 Z=0
    g6: GeomPoint X=38.1 Y=19.05 Z=0
    g7: ArcOfCircle CenterX=9.15 CenterY=89.1 CenterZ=0 NormalX=0 NormalY=0 NormalZ=1 AngleXU=0 Radius=2 StartAngle=1.5708 EndAngle=3.14159
    g8: GeomPoint [constr] X=7.15 Y=91.1 Z=0
    g9: GeomPoint X=19.05 Y=47.625 Z=0
  constraints (24):
    c: Coincident(g1,g2)
    c: Coincident(g2,g3)
    c: Coincident(g4,g1)
    c: Vertical(g1)
    c: Vertical(g3)
    c: Horizontal(g2)
    c: Horizontal(g4)
    c: PointOnObject(g8,g3)
    c: PointOnObject(g8,g4)
    c: Tangent(g3,g7) = 1.5708
    c: Tangent(g4,g7) = 1.5708
    c: Radius(g7) = 2
    c: DistanceX(g0,g6) = 19.05
    c: DistanceY(g-1,g0) = 19.05
    c: DistanceX(g-1,g0) = 19.05
    c: Horizontal(g0,g6)
    c: Vertical(g6,g5)
    c: DistanceY(g6,g5) = 57.15
    c: DistanceY(g5,g1) = 14.9
    c: DistanceX(g1,g5) = 9.525
    c: DistanceX(g2,g0) = 11.9
    c: Vertical(g9,g0)
    c: DistanceY(g0,g9) = 28.575
    c: DistanceY(g2,g9) = 1.2
FEATURE [PartDesign::Pad] Pad018  label="CR-Out-Pad"
  Direction = (0,0,1)
  Length = 7.5
  Length2 = 10
  Profile = -> Sketch053
  ReferenceAxis = -> Sketch053 [N_Axis]
  Refine = true
  Suppressed = false
  Type = 0
  expr: Length = VarSet.Top_PcbZ / 2 + VarSet.Cover_OutZ
FEATURE [Sketcher::SketchObject] Sketch054  label="CR-PCB"
  ArcFitTolerance = 1e-06
  AttachmentSupport = -> [XY_Plane005]
  FullyConstrained = true
  MakeInternals = false
  MapMode = 5
  expr: Constraints[8] = 2.5 * 19.05 mm + VarSet.Top_PcbY / 2
  expr: Constraints[9] = 4 * 19.05 mm - VarSet.Top_PcbX / 2
  sketch-geometry (4):
    g0: LineSegment StartX=9.9 StartY=35.375 StartZ=0 EndX=59.9 EndY=35.375 EndZ=0
    g1: LineSegment StartX=59.9 StartY=35.375 StartZ=0 EndX=59.9 EndY=85.375 EndZ=0
    g2: LineSegment StartX=59.9 StartY=85.375 StartZ=0 EndX=9.9 EndY=85.375 EndZ=0
    g3: LineSegment StartX=9.9 StartY=85.375 StartZ=0 EndX=9.9 EndY=35.375 EndZ=0
  constraints (12):
    c: Coincident(g0,g1)
    c: Coincident(g1,g2)
    c: Coincident(g2,g3)
    c: Coincident(g3,g0)
    c: Horizontal(g0)
    c: Horizontal(g2)
    c: Vertical(g1)
    c: Vertical(g3)
    c: DistanceY(g-1,g2) = 85.375
    c: DistanceX(g-1,g2) = 9.9
    c: DistanceX(g0,g0) = 50
    c: DistanceY(g1,g1) = 50
FEATURE [Sketcher::SketchObject] Sketch055  label="CR-In"
  ArcFitTolerance = 1e-06
  AttachmentSupport = -> [XY_Plane005]
  FullyConstrained = true
  MakeInternals = false
  MapMode = 5
  expr: Constraints[16] = VarSet.Cover_McuRearAdd
  expr: Constraints[17] = 2.5 * 19.05 mm + VarSet.Top_PcbY / 2
  expr: Constraints[18] = 3 * 19.05 mm
  expr: Constraints[22] = 1.5 * 19.05 mm
  expr: Constraints[24] = VarSet.Cover_FrontAdd
  sketch-geometry (13):
    g0: LineSegment StartX=28.1 StartY=51.625 StartZ=0 EndX=28.1 EndY=85.875 EndZ=0
    g1: LineSegment StartX=10 StartY=85.875 StartZ=0 EndX=10 EndY=46.425 EndZ=0
    g2: LineSegment StartX=10 StartY=46.425 StartZ=0 EndX=25.6 EndY=46.425 EndZ=0
    g3: GeomPoint [constr] X=19.05 Y=19.05 Z=0
    g4: GeomPoint [constr] X=38.1 Y=19.05 Z=0
    g5: GeomPoint [constr] X=38.1 Y=76.2 Z=0
    g6: LineSegment StartX=28.1 StartY=51.625 StartZ=0 EndX=25.6 EndY=51.625 EndZ=0
    g7: LineSegment StartX=28.1 StartY=85.875 StartZ=0 EndX=10 EndY=85.875 EndZ=0
    g8: GeomPoint X=38.1 Y=85.375 Z=0
    g9: GeomPoint X=19.05 Y=47.625 Z=0
    g10: ArcOfCircle CenterX=25.6 CenterY=49.625 CenterZ=0 NormalX=0 NormalY=0 NormalZ=1 AngleXU=0 Radius=2 StartAngle=1.5708 EndAngle=3.14159
    g11: ArcOfCircle CenterX=25.6 CenterY=48.425 CenterZ=0 NormalX=0 NormalY=0 NormalZ=1 AngleXU=0 Radius=2 StartAngle=3.14159 EndAngle=4.71239
    g12: LineSegment StartX=23.6 StartY=49.625 StartZ=0 EndX=23.6 EndY=48.425 EndZ=0
  constraints (33):
    c: Coincident(g7,g1)
    c: Coincident(g1,g2)
    c: Vertical(g0)
    c: Vertical(g1)
    c: Horizontal(g2)
    c: Horizontal(g6)
    c: Coincident(g6,g0)
    c: Horizontal(g7)
    c: DistanceX(g-1,g3) = 19.05
    c: DistanceX(g3,g4) = 19.05
    c: DistanceX(g0,g5) = 10
    c: DistanceX(g-1,g1) = 10
    c: DistanceY(g-1,g3) = 19.05
    c: Horizontal(g3,g4)
    c: Vertical(g4,g5)
    c: Vertical(g5,g8)
    c: DistanceY(g8,g0) = 0.5
    c: DistanceY(g-1,g8) = 85.375
    c: DistanceY(g4,g5) = 57.15
    c: DistanceX(g6,g6) = 2.5
    c: Coincident(g7,g0)
    c: Vertical(g6,g2)
    c: DistanceY(g3,g9) = 28.575
    c: Vertical(g9,g3)
    c: DistanceY(g1,g9) = 1.2
    c: Vertical(g12)
    c: Tangent(g10,g6) = -1.5708
    c: Tangent(g12,g10) = -1.5708
    c: Tangent(g12,g11) = -1.5708
    c: Equal(g10,g11)
    c: Radius(g10) = 2
    c: Coincident(g11,g2)
    c: DistanceY(g9,g10) = 2
FEATURE [PartDesign::Pocket] Pocket031  label="CR-In-Pocket"
  BaseFeature = -> Pad018
  Direction = (0,0,-1)
  Length = 5.5
  Length2 = 5
  Profile = -> Sketch055
  ReferenceAxis = -> Sketch055 [N_Axis]
  Refine = true
  Reversed = true
  Suppressed = false
  Type = 0
  expr: Length = VarSet.Top_PcbZ / 2 + VarSet.Cover_InZ
FEATURE [Sketcher::SketchObject] Sketch057  label="OL-Chamfer"
  ArcFitTolerance = 1e-06
  AttachmentSupport = -> [Pad017]
  ExternalGeometry = -> [Pad017]
  FullyConstrained = true
  MakeInternals = false
  MapMode = 5
  Placement = pos=(0,29.9,0) rot=(1,0,0;1.5708rad)
  sketch-geometry (9):
    g0: LineSegment StartX=-32 StartY=18 StartZ=0 EndX=-32 EndY=-2 EndZ=0
    g1: LineSegment StartX=-32 StartY=-2 StartZ=0 EndX=-2 EndY=-2 EndZ=0
    g2: LineSegment StartX=-2 StartY=-2 StartZ=0 EndX=-2 EndY=18 EndZ=0
    g3: LineSegment StartX=-2 StartY=18 StartZ=0 EndX=-32 EndY=18 EndZ=0
    g4: LineSegment StartX=-27.7 StartY=14.5 StartZ=0 EndX=-10.4 EndY=14.5 EndZ=0
    g5: LineSegment StartX=-10.4 StartY=14.5 StartZ=0 EndX=-7.15 EndY=11.25 EndZ=0
    g6: LineSegment StartX=-7.15 StartY=11.25 StartZ=0 EndX=-7.15 EndY=0 EndZ=0
    g7: LineSegment StartX=-7.15 StartY=0 StartZ=0 EndX=-27.7 EndY=0 EndZ=0
    g8: LineSegment StartX=-27.7 StartY=0 StartZ=0 EndX=-27.7 EndY=14.5 EndZ=0
  constraints (24):
    c: Coincident(g0,g1)
    c: Coincident(g1,g2)
    c: Coincident(g2,g3)
    c: Coincident(g3,g0)
    c: Vertical(g0)
    c: Vertical(g2)
    c: Horizontal(g1)
    c: Horizontal(g3)
    c: Coincident(g4,g-3)
    c: Horizontal(g4)
    c: Coincident(g4,g5)
    c: Coincident(g5,g6)
    c: Coincident(g6,g-5)
    c: Vertical(g6)
    c: Coincident(g6,g7)
    c: Coincident(g7,g-6)
    c: Coincident(g7,g8)
    c: Coincident(g8,g4)
    c: DistanceX(g4,g4) = 17.3
    c: Angle(g4,g5) = 2.35619
    c: DistanceX(g3,g3) = 30
    c: DistanceY(g2,g2) = 20
    c: DistanceX(g1,g-1) = 2
    c: DistanceY(g1,g-1) = 2
FEATURE [PartDesign::Pocket] Pocket032  label="OL-Chamfer-Pocket"
  BaseFeature = -> Pad017
  Direction = (0,1,-2e-16)
  Length = 5
  Length2 = 5
  Profile = -> Sketch057
  ReferenceAxis = -> Sketch057 [N_Axis]
  Refine = true
  Suppressed = false
  Type = 1
FEATURE [PartDesign::Fillet] Fillet003  label="OL-Fillet"
  Base = -> Pocket032 [Edge10,Edge3,Edge11,Edge12,Edge13,Edge4,Edge14,Edge9,Edge2]
  BaseFeature = -> Pocket032
  Radius = 1
  Refine = true
  SupportTransform = false
  Suppressed = false
  UseAllEdges = false
FEATURE [PartDesign::Body] Body006  label="ModuleLeft"
  AllowCompound = false
  Group = -> [Sketch049,Pad017,Sketch057,Pocket032,Fillet003]
  Origin = -> Origin006
  Tip = -> Fillet003
FEATURE [Image::ImagePlane] SplitKB_Liatris
  Placement = pos=(-19.15,68.9,5) rot=(1,0,0;0rad)
  XSize = 17.8651
  YSize = 33.3694
FEATURE [Sketcher::SketchObject] Sketch060  label="CR-MCU"
  ArcFitTolerance = 1e-06
  AttachmentSupport = -> [XY_Plane005]
  FullyConstrained = true
  MakeInternals = false
  MapMode = 5
  expr: Constraints[30] = 1.5 * 19.05 mm
  expr: Constraints[45] = VarSet.Top_MedXY / 2 + VarSet.Top_Frame - VarSet.Cover_ResetHoleDepth
  sketch-geometry (139):
    g0: GeomPoint X=19.05 Y=81.365 Z=0
    g1: LineSegment StartX=14.05 StartY=78.365 StartZ=0 EndX=24.05 EndY=78.365 EndZ=0
    g2: LineSegment StartX=24.05 StartY=78.365 StartZ=0 EndX=24.05 EndY=86.365 EndZ=0
    g3: LineSegment StartX=24.05 StartY=86.365 StartZ=0 EndX=14.05 EndY=86.365 EndZ=0
    g4: LineSegment StartX=14.05 StartY=86.365 StartZ=0 EndX=14.05 EndY=78.365 EndZ=0
    g5: GeomPoint [constr] X=19.05 Y=82.365 Z=0
    g6: LineSegment StartX=25.07 StartY=69.265 StartZ=0 EndX=25.07 EndY=74.765 EndZ=0
    g7: LineSegment StartX=25.07 StartY=74.765 StartZ=0 EndX=19.57 EndY=74.765 EndZ=0
    g8: LineSegment StartX=19.57 StartY=74.765 StartZ=0 EndX=19.57 EndY=69.265 EndZ=0
    g9: LineSegment StartX=19.57 StartY=69.265 StartZ=0 EndX=25.07 EndY=69.265 EndZ=0
    g10: GeomPoint [constr] X=22.32 Y=72.015 Z=0
    g11: GeomPoint X=19.05 Y=19.05 Z=0
    g12: GeomPoint X=38.1 Y=19.05 Z=0
    g13: GeomPoint X=19.05 Y=47.625 Z=0
    g14: LineSegment StartX=15.55 StartY=51.725 StartZ=0 EndX=8.65 EndY=51.725 EndZ=0
    g15: LineSegment StartX=8.65 StartY=51.725 StartZ=0 EndX=8.65 EndY=42.725 EndZ=0
    g16: LineSegment StartX=8.65 StartY=42.725 StartZ=0 EndX=15.55 EndY=42.725 EndZ=0
    g17: LineSegment StartX=15.55 StartY=42.725 StartZ=0 EndX=15.55 EndY=51.725 EndZ=0
    g18: GeomPoint [constr] X=12.1 Y=47.225 Z=0
    g19: LineSegment StartX=28.1 StartY=79.825 StartZ=0 EndX=28.1 EndY=77.825 EndZ=0
    g20: LineSegment StartX=28.1 StartY=77.825 StartZ=0 EndX=25.6 EndY=77.825 EndZ=0
    g21: LineSegment StartX=25.6 StartY=77.825 StartZ=0 EndX=25.6 EndY=79.825 EndZ=0
    g22: LineSegment StartX=25.6 StartY=79.825 StartZ=0 EndX=28.1 EndY=79.825 EndZ=0
    g23: GeomPoint [constr] X=26.85 Y=78.825 Z=0
    g24: LineSegment StartX=28.1 StartY=77.285 StartZ=0 EndX=28.1 EndY=75.285 EndZ=0
    g25: LineSegment StartX=28.1 StartY=75.285 StartZ=0 EndX=25.6 EndY=75.285 EndZ=0
    g26: LineSegment StartX=25.6 StartY=75.285 StartZ=0 EndX=25.6 EndY=77.285 EndZ=0
    g27: LineSegment StartX=25.6 StartY=77.285 StartZ=0 EndX=28.1 EndY=77.285 EndZ=0
    g28: GeomPoint [constr] X=26.85 Y=76.285 Z=0
    g29: LineSegment StartX=28.1 StartY=74.745 StartZ=0 EndX=28.1 EndY=72.745 EndZ=0
    g30: LineSegment StartX=28.1 StartY=72.745 StartZ=0 EndX=25.6 EndY=72.745 EndZ=0
    g31: LineSegment StartX=25.6 StartY=72.745 StartZ=0 EndX=25.6 EndY=74.745 EndZ=0
    g32: LineSegment StartX=25.6 StartY=74.745 StartZ=0 EndX=28.1 EndY=74.745 EndZ=0
    g33: GeomPoint [constr] X=26.85 Y=73.745 Z=0
    g34: LineSegment StartX=28.1 StartY=72.205 StartZ=0 EndX=28.1 EndY=70.205 EndZ=0
    g35: LineSegment StartX=28.1 StartY=70.205 StartZ=0 EndX=25.6 EndY=70.205 EndZ=0
    g36: LineSegment StartX=25.6 StartY=70.205 StartZ=0 EndX=25.6 EndY=72.205 EndZ=0
    g37: LineSegment StartX=25.6 StartY=72.205 StartZ=0 EndX=28.1 EndY=72.205 EndZ=0
    g38: GeomPoint [constr] X=26.85 Y=71.205 Z=0
    g39: LineSegment StartX=28.1 StartY=69.665 StartZ=0 EndX=28.1 EndY=67.665 EndZ=0
    g40: LineSegment StartX=28.1 StartY=67.665 StartZ=0 EndX=25.6 EndY=67.665 EndZ=0
    g41: LineSegment StartX=25.6 StartY=67.665 StartZ=0 EndX=25.6 EndY=69.665 EndZ=0
    g42: LineSegment StartX=25.6 StartY=69.665 StartZ=0 EndX=28.1 EndY=69.665 EndZ=0
    g43: GeomPoint [constr] X=26.85 Y=68.665 Z=0
    g44: LineSegment StartX=28.1 StartY=67.125 StartZ=0 EndX=28.1 EndY=65.125 EndZ=0
    g45: LineSegment StartX=28.1 StartY=65.125 StartZ=0 EndX=25.6 EndY=65.125 EndZ=0
    g46: LineSegment StartX=25.6 StartY=65.125 StartZ=0 EndX=25.6 EndY=67.125 EndZ=0
    g47: LineSegment StartX=25.6 StartY=67.125 StartZ=0 EndX=28.1 EndY=67.125 EndZ=0
    g48: GeomPoint [constr] X=26.85 Y=66.125 Z=0
    g49: LineSegment StartX=28.1 StartY=64.585 StartZ=0 EndX=28.1 EndY=62.585 EndZ=0
    g50: LineSegment StartX=28.1 StartY=62.585 StartZ=0 EndX=25.6 EndY=62.585 EndZ=0
    g51: LineSegment StartX=25.6 StartY=62.585 StartZ=0 EndX=25.6 EndY=64.585 EndZ=0
    g52: LineSegment StartX=25.6 StartY=64.585 StartZ=0 EndX=28.1 EndY=64.585 EndZ=0
    g53: GeomPoint [constr] X=26.85 Y=63.585 Z=0
    g54: LineSegment StartX=28.1 StartY=82.365 StartZ=0 EndX=28.1 EndY=80.365 EndZ=0
    g55: LineSegment StartX=28.1 StartY=80.365 StartZ=0 EndX=25.6 EndY=80.365 EndZ=0
    g56: LineSegment StartX=25.6 StartY=80.365 StartZ=0 EndX=25.6 EndY=82.365 EndZ=0
    g57: LineSegment StartX=25.6 StartY=82.365 StartZ=0 EndX=28.1 EndY=82.365 EndZ=0
    g58: GeomPoint [constr] X=26.85 Y=81.365 Z=0
    g59: LineSegment StartX=28.1 StartY=62.045 StartZ=0 EndX=28.1 EndY=60.045 EndZ=0
    g60: LineSegment StartX=28.1 StartY=60.045 StartZ=0 EndX=25.6 EndY=60.045 EndZ=0
    g61: LineSegment StartX=25.6 StartY=60.045 StartZ=0 EndX=25.6 EndY=62.045 EndZ=0
    g62: LineSegment StartX=25.6 StartY=62.045 StartZ=0 EndX=28.1 EndY=62.045 EndZ=0
    g63: GeomPoint [constr] X=26.85 Y=61.045 Z=0
    g64: LineSegment StartX=28.1 StartY=59.505 StartZ=0 EndX=28.1 EndY=57.505 EndZ=0
    g65: LineSegment StartX=28.1 StartY=57.505 StartZ=0 EndX=25.6 EndY=57.505 EndZ=0
    g66: LineSegment StartX=25.6 StartY=57.505 StartZ=0 EndX=25.6 EndY=59.505 EndZ=0
    g67: LineSegment StartX=25.6 StartY=59.505 StartZ=0 EndX=28.1 EndY=59.505 EndZ=0
    g68: GeomPoint [constr] X=26.85 Y=58.505 Z=0
    g69: LineSegment StartX=28.1 StartY=56.965 StartZ=0 EndX=28.1 EndY=54.965 EndZ=0
    g70: LineSegment StartX=28.1 StartY=54.965 StartZ=0 EndX=25.6 EndY=54.965 EndZ=0
    g71: LineSegment StartX=25.6 StartY=54.965 StartZ=0 EndX=25.6 EndY=56.965 EndZ=0
    g72: LineSegment StartX=25.6 StartY=56.965 StartZ=0 EndX=28.1 EndY=56.965 EndZ=0
    g73: GeomPoint [constr] X=26.85 Y=55.965 Z=0
    g74: LineSegment StartX=28.1 StartY=54.425 StartZ=0 EndX=28.1 EndY=52.425 EndZ=0
    g75: LineSegment StartX=28.1 StartY=52.425 StartZ=0 EndX=25.6 EndY=52.425 EndZ=0
    g76: LineSegment StartX=25.6 StartY=52.425 StartZ=0 EndX=25.6 EndY=54.425 EndZ=0
    g77: LineSegment StartX=25.6 StartY=54.425 StartZ=0 EndX=28.1 EndY=54.425 EndZ=0
    g78: GeomPoint [constr] X=26.85 Y=53.425 Z=0
    g79: LineSegment StartX=12.5 StartY=79.825 StartZ=0 EndX=12.5 EndY=77.825 EndZ=0
    g80: LineSegment StartX=12.5 StartY=77.825 StartZ=0 EndX=10 EndY=77.825 EndZ=0
    g81: LineSegment StartX=10 StartY=77.825 StartZ=0 EndX=10 EndY=79.825 EndZ=0
    g82: LineSegment StartX=10 StartY=79.825 StartZ=0 EndX=12.5 EndY=79.825 EndZ=0
    g83: GeomPoint [constr] X=11.25 Y=78.825 Z=0
    g84: LineSegment StartX=12.5 StartY=77.285 StartZ=0 EndX=12.5 EndY=75.285 EndZ=0
    g85: LineSegment StartX=12.5 StartY=75.285 StartZ=0 EndX=10 EndY=75.285 EndZ=0
    g86: LineSegment StartX=10 StartY=75.285 StartZ=0 EndX=10 EndY=77.285 EndZ=0
    g87: LineSegment StartX=10 StartY=77.285 StartZ=0 EndX=12.5 EndY=77.285 EndZ=0
    g88: GeomPoint [constr] X=11.25 Y=76.285 Z=0
    g89: LineSegment StartX=12.5 StartY=74.745 StartZ=0 EndX=12.5 EndY=72.745 EndZ=0
    g90: LineSegment StartX=12.5 StartY=72.745 StartZ=0 EndX=10 EndY=72.745 EndZ=0
    g91: LineSegment StartX=10 StartY=72.745 StartZ=0 EndX=10 EndY=74.745 EndZ=0
    g92: LineSegment StartX=10 StartY=74.745 StartZ=0 EndX=12.5 EndY=74.745 EndZ=0
    g93: GeomPoint [constr] X=11.25 Y=73.745 Z=0
    g94: LineSegment StartX=12.5 StartY=72.205 StartZ=0 EndX=12.5 EndY=70.205 EndZ=0
    g95: LineSegment StartX=12.5 StartY=70.205 StartZ=0 EndX=10 EndY=70.205 EndZ=0
    g96: LineSegment StartX=10 StartY=70.205 StartZ=0 EndX=10 EndY=72.205 EndZ=0
    g97: LineSegment StartX=10 StartY=72.205 StartZ=0 EndX=12.5 EndY=72.205 EndZ=0
    g98: GeomPoint [constr] X=11.25 Y=71.205 Z=0
    g99: LineSegment StartX=12.5 StartY=69.665 StartZ=0 EndX=12.5 EndY=67.665 EndZ=0
    g100: LineSegment StartX=12.5 StartY=67.665 StartZ=0 EndX=10 EndY=67.665 EndZ=0
    g101: LineSegment StartX=10 StartY=67.665 StartZ=0 EndX=10 EndY=69.665 EndZ=0
    g102: LineSegment StartX=10 StartY=69.665 StartZ=0 EndX=12.5 EndY=69.665 EndZ=0
    g103: GeomPoint [constr] X=11.25 Y=68.665 Z=0
    g104: LineSegment StartX=12.5 StartY=67.125 StartZ=0 EndX=12.5 EndY=65.125 EndZ=0
    g105: LineSegment StartX=12.5 StartY=65.125 StartZ=0 EndX=10 EndY=65.125 EndZ=0
    g106: LineSegment StartX=10 StartY=65.125 StartZ=0 EndX=10 EndY=67.125 EndZ=0
    g107: LineSegment StartX=10 StartY=67.125 StartZ=0 EndX=12.5 EndY=67.125 EndZ=0
    g108: GeomPoint [constr] X=11.25 Y=66.125 Z=0
    g109: LineSegment StartX=12.5 StartY=64.585 StartZ=0 EndX=12.5 EndY=62.585 EndZ=0
    g110: LineSegment StartX=12.5 StartY=62.585 StartZ=0 EndX=10 EndY=62.585 EndZ=0
    g111: LineSegment StartX=10 StartY=62.585 StartZ=0 EndX=10 EndY=64.585 EndZ=0
    g112: LineSegment StartX=10 StartY=64.585 StartZ=0 EndX=12.5 EndY=64.585 EndZ=0
    g113: GeomPoint [constr] X=11.25 Y=63.585 Z=0
    g114: LineSegment StartX=12.5 StartY=62.045 StartZ=0 EndX=12.5 EndY=60.045 EndZ=0
    g115: LineSegment StartX=12.5 StartY=60.045 StartZ=0 EndX=10 EndY=60.045 EndZ=0
    g116: LineSegment StartX=10 StartY=60.045 StartZ=0 EndX=10 EndY=62.045 EndZ=0
    g117: LineSegment StartX=10 StartY=62.045 StartZ=0 EndX=12.5 EndY=62.045 EndZ=0
    g118: GeomPoint [constr] X=11.25 Y=61.045 Z=0
    g119: LineSegment StartX=12.5 StartY=59.505 StartZ=0 EndX=12.5 EndY=57.505 EndZ=0
    g120: LineSegment StartX=12.5 StartY=57.505 StartZ=0 EndX=10 EndY=57.505 EndZ=0
    g121: LineSegment StartX=10 StartY=57.505 StartZ=0 EndX=10 EndY=59.505 EndZ=0
    g122: LineSegment StartX=10 StartY=59.505 StartZ=0 EndX=12.5 EndY=59.505 EndZ=0
    g123: GeomPoint [constr] X=11.25 Y=58.505 Z=0
    g124: LineSegment StartX=12.5 StartY=56.965 StartZ=0 EndX=12.5 EndY=54.965 EndZ=0
    g125: LineSegment StartX=12.5 StartY=54.965 StartZ=0 EndX=10 EndY=54.965 EndZ=0
    g126: LineSegment StartX=10 StartY=54.965 StartZ=0 EndX=10 EndY=56.965 EndZ=0
    g127: LineSegment StartX=10 StartY=56.965 StartZ=0 EndX=12.5 EndY=56.965 EndZ=0
    g128: GeomPoint [constr] X=11.25 Y=55.965 Z=0
    g129: LineSegment StartX=12.5 StartY=54.425 StartZ=0 EndX=12.5 EndY=52.425 EndZ=0
    g130: LineSegment StartX=12.5 StartY=52.425 StartZ=0 EndX=10 EndY=52.425 EndZ=0
    g131: LineSegment StartX=10 StartY=52.425 StartZ=0 EndX=10 EndY=54.425 EndZ=0
    g132: LineSegment StartX=10 StartY=54.425 StartZ=0 EndX=12.5 EndY=54.425 EndZ=0
    g133: GeomPoint [constr] X=11.25 Y=53.425 Z=0
    g134: LineSegment StartX=12.5 StartY=82.365 StartZ=0 EndX=12.5 EndY=80.365 EndZ=0
    g135: LineSegment StartX=12.5 StartY=80.365 StartZ=0 EndX=10 EndY=80.365 EndZ=0
    g136: LineSegment StartX=10 StartY=80.365 StartZ=0 EndX=10 EndY=82.365 EndZ=0
    g137: LineSegment StartX=10 StartY=82.365 StartZ=0 EndX=12.5 EndY=82.365 EndZ=0
    g138: GeomPoint [constr] X=11.25 Y=81.365 Z=0
  constraints (359):
    c: Coincident(g1,g2)
    c: Coincident(g2,g3)
    c: Coincident(g3,g4)
    c: Coincident(g4,g1)
    c: Horizontal(g1)
    c: Horizontal(g3)
    c: Vertical(g2)
    c: Vertical(g4)
    c: Symmetric(g3,g1,g5)
    c: Distance(g1,g3) = 8
    c: Vertical(g5,g0)
    c: DistanceY(g1,g0) = 3
    c: Coincident(g6,g7)
    c: Coincident(g7,g8)
    c: Coincident(g8,g9)
    c: Coincident(g9,g6)
    c: Vertical(g6)
    c: Vertical(g8)
    c: Horizontal(g7)
    c: Horizontal(g9)
    c: Symmetric(g8,g6,g10)
    c: DistanceY(g10,g0) = 9.35
    c: DistanceX(g3,g3) = 10
    c: DistanceX(g0,g10) = 3.27
    c: Equal(g9,g8)
    c: DistanceX(g9,g9) = 5.5
    c: Horizontal(g12,g11)
    c: Vertical(g0,g11)
    c: DistanceY(g-1,g11) = 19.05
    c: Vertical(g13,g11)
    c: DistanceY(g11,g13) = 28.575
    c: DistanceX(g11,g12) = 19.05
    c: DistanceX(g-1,g11) = 19.05
    c: Coincident(g14,g15)
    c: Coincident(g15,g16)
    c: Coincident(g16,g17)
    c: Coincident(g17,g14)
    c: Horizontal(g14)
    c: Horizontal(g16)
    c: Vertical(g15)
    c: Vertical(g17)
    c: Symmetric(g16,g14,g18)
    c: DistanceY(g18,g13) = 0.4
    c: DistanceY(g15,g15) = 9
    c: DistanceX(g16,g13) = 3.5
    c: DistanceX(g15,g13) = 10.4
    c: Coincident(g19,g20)
    c: Coincident(g20,g21)
    c: Coincident(g21,g22)
    c: Coincident(g22,g19)
    c: Vertical(g19)
    c: Vertical(g21)
    c: Horizontal(g20)
    c: Horizontal(g22)
    c: Symmetric(g21,g19,g23)
    c: Coincident(g24,g25)
    c: Coincident(g25,g26)
    c: Coincident(g26,g27)
    c: Coincident(g27,g24)
    c: Vertical(g24)
    c: Vertical(g26)
    c: Horizontal(g25)
    c: Horizontal(g27)
    c: Symmetric(g26,g24,g28)
    c: Coincident(g29,g30)
    c: Coincident(g30,g31)
    c: Coincident(g31,g32)
    c: Coincident(g32,g29)
    c: Vertical(g29)
    c: Vertical(g31)
    c: Horizontal(g30)
    c: Horizontal(g32)
    c: Symmetric(g31,g29,g33)
    c: Coincident(g34,g35)
    c: Coincident(g35,g36)
    c: Coincident(g36,g37)
    c: Coincident(g37,g34)
    c: Vertical(g34)
    c: Vertical(g36)
    c: Horizontal(g35)
    c: Horizontal(g37)
    c: Symmetric(g36,g34,g38)
    c: Coincident(g39,g40)
    c: Coincident(g40,g41)
    c: Coincident(g41,g42)
    c: Coincident(g42,g39)
    c: Vertical(g39)
    c: Vertical(g41)
    c: Horizontal(g40)
    c: Horizontal(g42)
    c: Symmetric(g41,g39,g43)
    c: Coincident(g44,g45)
    c: Coincident(g45,g46)
    c: Coincident(g46,g47)
    c: Coincident(g47,g44)
    c: Vertical(g44)
    c: Vertical(g46)
    c: Horizontal(g45)
    c: Horizontal(g47)
    c: Symmetric(g46,g44,g48)
    c: Coincident(g49,g50)
    c: Coincident(g50,g51)
    c: Coincident(g51,g52)
    c: Coincident(g52,g49)
    c: Vertical(g49)
    c: Vertical(g51)
    c: Horizontal(g50)
    c: Horizontal(g52)
    c: Symmetric(g51,g49,g53)
    c: Coincident(g54,g55)
    c: Coincident(g55,g56)
    c: Coincident(g56,g57)
    c: Coincident(g57,g54)
    c: Vertical(g54)
    c: Vertical(g56)
    c: Horizontal(g55)
    c: Horizontal(g57)
    c: Symmetric(g56,g54,g58)
    c: Coincident(g59,g60)
    c: Coincident(g60,g61)
    c: Coincident(g61,g62)
    c: Coincident(g62,g59)
    c: Vertical(g59)
    c: Vertical(g61)
    c: Horizontal(g60)
    c: Horizontal(g62)
    c: Symmetric(g61,g59,g63)
    c: Coincident(g64,g65)
    c: Coincident(g65,g66)
    c: Coincident(g66,g67)
    c: Coincident(g67,g64)
    c: Vertical(g64)
    c: Vertical(g66)
    c: Horizontal(g65)
    c: Horizontal(g67)
    c: Symmetric(g66,g64,g68)
    c: Coincident(g69,g70)
    c: Coincident(g70,g71)
    c: Coincident(g71,g72)
    c: Coincident(g72,g69)
    c: Vertical(g69)
    c: Vertical(g71)
    c: Horizontal(g70)
    c: Horizontal(g72)
    c: Symmetric(g71,g69,g73)
    c: Coincident(g74,g75)
    c: Coincident(g75,g76)
    c: Coincident(g76,g77)
    c: Coincident(g77,g74)
    c: Vertical(g74)
    c: Vertical(g76)
    c: Horizontal(g75)
    c: Horizontal(g77)
    c: Symmetric(g76,g74,g78)
    c: Vertical(g58,g23)
    c: Vertical(g23,g28)
    c: Vertical(g28,g33)
    c: Vertical(g33,g38)
    c: Vertical(g38,g43)
    c: Vertical(g43,g48)
    c: Vertical(g48,g53)
    c: Vertical(g53,g63)
    c: Vertical(g63,g68)
    c: Vertical(g68,g73)
    c: Vertical(g73,g78)
    c: DistanceY(g23,g58) = 2.54
    c: DistanceY(g28,g23) = 2.54
    c: DistanceY(g33,g28) = 2.54
    c: DistanceY(g38,g33) = 2.54
    c: DistanceY(g43,g38) = 2.54
    c: DistanceY(g48,g43) = 2.54
    c: DistanceY(g53,g48) = 2.54
    c: DistanceY(g63,g53) = 2.54
    c: DistanceY(g68,g63) = 2.54
    c: DistanceY(g73,g68) = 2.54
    c: DistanceY(g78,g73) = 2.54
    c: Equal(g54,g19)
    c: Equal(g19,g24)
    c: Equal(g24,g29)
    c: Equal(g29,g34)
    c: Equal(g34,g39)
    c: Equal(g39,g44)
    c: Equal(g44,g49)
    c: Equal(g49,g59)
    c: Equal(g59,g64)
    c: Equal(g64,g69)
    c: Equal(g69,g74)
    c: Equal(g55,g20)
    c: Equal(g20,g25)
    c: Equal(g25,g30)
    c: Equal(g30,g35)
    c: Equal(g35,g40)
    c: Equal(g40,g45)
    c: Equal(g45,g50)
    c: Equal(g50,g60)
    c: Equal(g60,g65)
    c: Equal(g65,g70)
    c: Equal(g70,g75)
    c: Coincident(g79,g80)
    c: Coincident(g80,g81)
    c: Coincident(g81,g82)
    c: Coincident(g82,g79)
    c: Vertical(g79)
    c: Vertical(g81)
    c: Horizontal(g80)
    c: Horizontal(g82)
    c: Symmetric(g81,g79,g83)
    c: Coincident(g84,g85)
    c: Coincident(g85,g86)
    c: Coincident(g86,g87)
    c: Coincident(g87,g84)
    c: Vertical(g84)
    c: Vertical(g86)
    c: Horizontal(g85)
    c: Horizontal(g87)
    c: Symmetric(g86,g84,g88)
    c: Coincident(g89,g90)
    c: Coincident(g90,g91)
    c: Coincident(g91,g92)
    c: Coincident(g92,g89)
    c: Vertical(g89)
    c: Vertical(g91)
    c: Horizontal(g90)
    c: Horizontal(g92)
    c: Symmetric(g91,g89,g93)
    c: Coincident(g94,g95)
    c: Coincident(g95,g96)
    c: Coincident(g96,g97)
    c: Coincident(g97,g94)
    c: Vertical(g94)
    c: Vertical(g96)
    c: Horizontal(g95)
    c: Horizontal(g97)
    c: Symmetric(g96,g94,g98)
    c: Coincident(g99,g100)
    c: Coincident(g100,g101)
    c: Coincident(g101,g102)
    c: Coincident(g102,g99)
    c: Vertical(g99)
    c: Vertical(g101)
    c: Horizontal(g100)
    c: Horizontal(g102)
    c: Symmetric(g101,g99,g103)
    c: Coincident(g104,g105)
    c: Coincident(g105,g106)
    c: Coincident(g106,g107)
    c: Coincident(g107,g104)
    c: Vertical(g104)
    c: Vertical(g106)
    c: Horizontal(g105)
    c: Horizontal(g107)
    c: Symmetric(g106,g104,g108)
    c: Coincident(g109,g110)
    c: Coincident(g110,g111)
    c: Coincident(g111,g112)
    c: Coincident(g112,g109)
    c: Vertical(g109)
    c: Vertical(g111)
    c: Horizontal(g110)
    c: Horizontal(g112)
    c: Symmetric(g111,g109,g113)
    c: Coincident(g114,g115)
    c: Coincident(g115,g116)
    c: Coincident(g116,g117)
    c: Coincident(g117,g114)
    c: Vertical(g114)
    c: Vertical(g116)
    c: Horizontal(g115)
    c: Horizontal(g117)
    c: Symmetric(g116,g114,g118)
    c: Coincident(g119,g120)
    c: Coincident(g120,g121)
    c: Coincident(g121,g122)
    c: Coincident(g122,g119)
    c: Vertical(g119)
    c: Vertical(g121)
    c: Horizontal(g120)
    c: Horizontal(g122)
    c: Symmetric(g121,g119,g123)
    c: Coincident(g124,g125)
    c: Coincident(g125,g126)
    c: Coincident(g126,g127)
    c: Coincident(g127,g124)
    c: Vertical(g124)
    c: Vertical(g126)
    c: Horizontal(g125)
    c: Horizontal(g127)
    c: Symmetric(g126,g124,g128)
    c: Coincident(g129,g130)
    c: Coincident(g130,g131)
    c: Coincident(g131,g132)
    c: Coincident(g132,g129)
    c: Vertical(g129)
    c: Horizontal(g130)
    c: Horizontal(g132)
    c: Symmetric(g131,g129,g133)
    c: Vertical(g83,g88)
    c: Vertical(g88,g93)
    c: Vertical(g93,g98)
    c: Vertical(g98,g103)
    c: Vertical(g103,g108)
    c: Vertical(g108,g113)
    c: Vertical(g113,g118)
    c: Vertical(g118,g123)
    c: Vertical(g123,g128)
    c: Vertical(g128,g133)
    c: Equal(g79,g84)
    c: Equal(g84,g89)
    c: Equal(g89,g94)
    c: Equal(g94,g99)
    c: Equal(g99,g104)
    c: Equal(g104,g109)
    c: Equal(g109,g114)
    c: Equal(g114,g119)
    c: Equal(g119,g124)
    c: Equal(g124,g129)
    c: Equal(g80,g85)
    c: Equal(g85,g90)
    c: Equal(g90,g95)
    c: Equal(g95,g100)
    c: Equal(g100,g105)
    c: Equal(g105,g110)
    c: Equal(g110,g115)
    c: Equal(g115,g120)
    c: Equal(g120,g125)
    c: Equal(g125,g130)
    c: Horizontal(g23,g83)
    c: Horizontal(g28,g88)
    c: Horizontal(g33,g93)
    c: Horizontal(g38,g98)
    c: Horizontal(g43,g103)
    c: Horizontal(g48,g108)
    c: Horizontal(g53,g113)
    c: Horizontal(g63,g118)
    c: Horizontal(g68,g123)
    c: Horizontal(g73,g128)
    c: Horizontal(g78,g133)
    c: Coincident(g134,g135)
    c: Coincident(g135,g136)
    c: Coincident(g136,g137)
    c: Vertical(g134)
    c: Vertical(g136)
    c: Horizontal(g135)
    c: Horizontal(g137)
    c: Symmetric(g136,g134,g138)
    c: Vertical(g138,g83)
    c: Horizontal(g138,g58)
    c: Equal(g135,g80)
    c: Equal(g79,g134)
    c: Equal(g130,g75)
    c: Equal(g129,g74)
    c: DistanceY(g13,g78) = 5.8
    c: DistanceX(g74,g12) = 10
    c: DistanceX(g-1,g130) = 10
    c: DistanceX(g75,g75) = 2.5
    c: DistanceY(g74,g74) = 2
    c: Vertical(g131)
    c: Horizontal(g138,g0)
    c: Coincident(g137,g134)
FEATURE [Sketcher::SketchObject] Sketch061  label="TL-HiSw"
  ArcFitTolerance = 1e-06
  AttachmentOffset = pos=(0,0,5) rot=(0,0,1;0rad)
  AttachmentSupport = -> [XY_Plane]
  FullyConstrained = true
  MakeInternals = false
  MapMode = 5
  Placement = pos=(0,0,5) rot=(0,0,1;0rad)
  expr: .AttachmentOffset.Base.z = VarSet.Top_PcbZ + VarSet.Top_LoZ + VarSet.Top_MedZ + VarSet.Top_HiZ
  expr: Constraints[38] = 19.05 mm / 2
  expr: Constraints[41] = 6 * 19.05
  expr: Constraints[45] = 7 * 19.05 mm
  expr: Constraints[50] = 4 * 19.05 mm
  sketch-geometry (20):
    g0: LineSegment StartX=-142.875 StartY=81.2 StartZ=0 EndX=-142.875 EndY=71.2 EndZ=0
    g1: LineSegment StartX=-142.875 StartY=71.2 StartZ=0 EndX=-28.575 EndY=71.2 EndZ=0
    g2: LineSegment StartX=-28.575 StartY=71.2 StartZ=0 EndX=-28.575 EndY=81.2 EndZ=0
    g3: LineSegment StartX=-28.575 StartY=81.2 StartZ=0 EndX=-142.875 EndY=81.2 EndZ=0
    g4: GeomPoint [constr] X=-85.725 Y=76.2 Z=0
    g5: LineSegment StartX=-142.875 StartY=62.15 StartZ=0 EndX=-142.875 EndY=52.15 EndZ=0
    g6: LineSegment StartX=-142.875 StartY=52.15 StartZ=0 EndX=-28.575 EndY=52.15 EndZ=0
    g7: LineSegment StartX=-28.575 StartY=52.15 StartZ=0 EndX=-28.575 EndY=62.15 EndZ=0
    g8: LineSegment StartX=-28.575 StartY=62.15 StartZ=0 EndX=-142.875 EndY=62.15 EndZ=0
    g9: GeomPoint [constr] X=-85.725 Y=57.15 Z=0
    g10: LineSegment StartX=-142.875 StartY=43.1 StartZ=0 EndX=-142.875 EndY=33.1 EndZ=0
    g11: LineSegment StartX=-142.875 StartY=33.1 StartZ=0 EndX=-28.575 EndY=33.1 EndZ=0
    g12: LineSegment StartX=-28.575 StartY=33.1 StartZ=0 EndX=-28.575 EndY=43.1 EndZ=0
    g13: LineSegment StartX=-28.575 StartY=43.1 StartZ=0 EndX=-142.875 EndY=43.1 EndZ=0
    g14: GeomPoint [constr] X=-85.725 Y=38.1 Z=0
    g15: LineSegment StartX=-9.525 StartY=24.05 StartZ=0 EndX=-142.875 EndY=24.05 EndZ=0
    g16: LineSegment StartX=-142.875 StartY=24.05 StartZ=0 EndX=-142.875 EndY=14.05 EndZ=0
    g17: LineSegment StartX=-142.875 StartY=14.05 StartZ=0 EndX=-9.525 EndY=14.05 EndZ=0
    g18: LineSegment StartX=-9.525 StartY=14.05 StartZ=0 EndX=-9.525 EndY=24.05 EndZ=0
    g19: GeomPoint [constr] X=-76.2 Y=19.05 Z=0
  constraints (52):
    c: Coincident(g0,g1)
    c: Coincident(g1,g2)
    c: Coincident(g2,g3)
    c: Coincident(g3,g0)
    c: Vertical(g0)
    c: Vertical(g2)
    c: Horizontal(g1)
    c: Horizontal(g3)
    c: Symmetric(g2,g0,g4)
    c: Coincident(g5,g6)
    c: Coincident(g6,g7)
    c: Coincident(g7,g8)
    c: Coincident(g8,g5)
    c: Vertical(g5)
    c: Vertical(g7)
    c: Horizontal(g6)
    c: Horizontal(g8)
    c: Symmetric(g7,g5,g9)
    c: Coincident(g10,g11)
    c: Coincident(g11,g12)
    c: Coincident(g12,g13)
    c: Coincident(g13,g10)
    c: Vertical(g10)
    c: Vertical(g12)
    c: Horizontal(g11)
    c: Horizontal(g13)
    c: Symmetric(g12,g10,g14)
    c: Coincident(g15,g16)
    c: Coincident(g16,g17)
    c: Coincident(g17,g18)
    c: Coincident(g18,g15)
    c: Horizontal(g15)
    c: Horizontal(g17)
    c: Vertical(g16)
    c: Vertical(g18)
    c: Symmetric(g17,g15,g19)
    c: Vertical(g4,g9)
    c: Vertical(g9,g14)
    c: DistanceX(g14,g19) = 9.525
    c: Equal(g1,g6)
    c: Equal(g6,g11)
    c: DistanceX(g3,g3) = 114.3
    c: Equal(g0,g5)
    c: Equal(g5,g10)
    c: Equal(g10,g16)
    c: DistanceX(g17,g17) = 133.35
    c: DistanceY(g18,g18) = 10
    c: DistanceY(g9,g4) = 19.05
    c: DistanceY(g14,g9) = 19.05
    c: DistanceY(g19,g14) = 19.05
    c: DistanceX(g19,g-1) = 76.2
    c: DistanceY(g-1,g19) = 19.05
FEATURE [Sketcher::SketchObject] Sketch062  label="TL-Plate"
  ArcFitTolerance = 1e-06
  AttachmentSupport = -> [XY_Plane]
  FullyConstrained = true
  MakeInternals = false
  MapMode = 5
  expr: Constraints[17] = VarSet.Top_FrameFilletR
  expr: Constraints[32] = 19.05 mm / 2
  expr: Constraints[33] = VarSet.Top_MedXY / 2 + VarSet.Top_Frame
  expr: Constraints[34] = VarSet.Top_MedXY / 2 + VarSet.Top_Frame + VarSet.Top_RearAdd
  expr: Constraints[36] = 19.05 mm / 2
  expr: Constraints[37] = VarSet.Top_MedXY / 2 + VarSet.Top_Frame
  expr: Constraints[38] = VarSet.Top_MedXY / 2 + VarSet.Top_Frame
  sketch-geometry (39):
    g0: GeomPoint [constr] X=-38.1 Y=19.05 Z=0
    g1: GeomPoint [constr] X=-57.15 Y=19.05 Z=0
    g2: GeomPoint [constr] X=-76.2 Y=19.05 Z=0
    g3: GeomPoint [constr] X=-95.25 Y=19.05 Z=0
    g4: GeomPoint [constr] X=-114.3 Y=19.05 Z=0
    g5: GeomPoint [constr] X=-38.1 Y=57.15 Z=0
    g6: GeomPoint [constr] X=-57.15 Y=57.15 Z=0
    g7: GeomPoint [constr] X=-76.2 Y=57.15 Z=0
    g8: GeomPoint [constr] X=-95.25 Y=57.15 Z=0
    g9: GeomPoint [constr] X=-114.3 Y=57.15 Z=0
    g10: GeomPoint [constr] X=-38.1 Y=38.1 Z=0
    g11: GeomPoint [constr] X=-57.15 Y=38.1 Z=0
    g12: GeomPoint [constr] X=-76.2 Y=38.1 Z=0
    g13: GeomPoint [constr] X=-95.25 Y=38.1 Z=0
    g14: GeomPoint [constr] X=-114.3 Y=38.1 Z=0
    g15: GeomPoint [constr] X=-95.25 Y=76.2 Z=0
    g16: GeomPoint [constr] X=-57.15 Y=76.2 Z=0
    g17: GeomPoint [constr] X=-133.35 Y=76.2 Z=0
    g18: GeomPoint [constr] X=-114.3 Y=76.2 Z=0
    g19: GeomPoint [constr] X=-76.2 Y=76.2 Z=0
    g20: LineSegment StartX=-145.25 StartY=89.1 StartZ=0 EndX=-145.25 EndY=9.15 EndZ=0
    g21: LineSegment StartX=-143.25 StartY=91.1 StartZ=0 EndX=-28.575 EndY=91.1 EndZ=0
    g22: LineSegment StartX=-28.575 StartY=91.1 StartZ=0 EndX=-28.575 EndY=30.575 EndZ=0
    g23: LineSegment StartX=-26.575 StartY=28.575 StartZ=0 EndX=-7.15 EndY=28.575 EndZ=0
    g24: LineSegment StartX=-7.15 StartY=28.575 StartZ=0 EndX=-7.15 EndY=9.15 EndZ=0
    g25: LineSegment StartX=-9.15 StartY=7.15 StartZ=0 EndX=-143.25 EndY=7.15 EndZ=0
    g26: ArcOfCircle CenterX=-9.15 CenterY=9.15 CenterZ=0 NormalX=0 NormalY=0 NormalZ=1 AngleXU=0 Radius=2 StartAngle=4.71239 EndAngle=6.28319
    g27: GeomPoint [constr] X=-7.15 Y=7.15 Z=0
    g28: ArcOfCircle CenterX=-26.575 CenterY=30.575 CenterZ=0 NormalX=0 NormalY=0 NormalZ=1 AngleXU=0 Radius=2 StartAngle=3.14159 EndAngle=4.71239
    g29: GeomPoint [constr] X=-28.575 Y=28.575 Z=0
    g30: ArcOfCircle CenterX=-143.25 CenterY=9.15 CenterZ=0 NormalX=0 NormalY=0 NormalZ=1 AngleXU=0 Radius=2 StartAngle=3.14159 EndAngle=4.71239
    g31: GeomPoint [constr] X=-145.25 Y=7.15 Z=0
    g32: ArcOfCircle CenterX=-143.25 CenterY=89.1 CenterZ=0 NormalX=0 NormalY=0 NormalZ=1 AngleXU=0 Radius=2 StartAngle=1.5708 EndAngle=3.14159
    g33: GeomPoint [constr] X=-145.25 Y=91.1 Z=0
    g34: GeomPoint [constr] X=-38.1 Y=76.2 Z=0
    g35: GeomPoint [constr] X=-133.35 Y=57.15 Z=0
    g36: GeomPoint [constr] X=-133.35 Y=38.1 Z=0
    g37: GeomPoint [constr] X=-133.35 Y=19.05 Z=0
    g38: GeomPoint [constr] X=-19.05 Y=19.05 Z=0
  constraints (84):
    c: DistanceX(g1,g0) = 19.05
    c: DistanceX(g2,g1) = 19.05
    c: DistanceX(g3,g2) = 19.05
    c: DistanceX(g4,g3) = 19.05
    c: DistanceY(g10,g5) = 19.05
    c: Vertical(g20)
    c: Horizontal(g21)
    c: Coincident(g22,g21)
    c: Vertical(g22)
    c: Horizontal(g23)
    c: Vertical(g24)
    c: Horizontal(g25)
    c: Coincident(g23,g24)
    c: PointOnObject(g27,g24)
    c: PointOnObject(g27,g25)
    c: Tangent(g24,g26) = 1.5708
    c: Tangent(g25,g26) = 1.5708
    c: Radius(g26) = 2
    c: PointOnObject(g29,g22)
    c: PointOnObject(g29,g23)
    c: Tangent(g22,g28) = -1.5708
    c: Tangent(g23,g28) = -1.5708
    c: PointOnObject(g31,g20)
    c: PointOnObject(g31,g25)
    c: Tangent(g20,g30) = -1.5708
    c: Tangent(g25,g30) = 1.5708
    c: PointOnObject(g33,g20)
    c: PointOnObject(g33,g21)
    c: Tangent(g20,g32) = -1.5708
    c: Tangent(g21,g32) = 1.5708
    c: DistanceY(g5,g34) = 19.05
    c: DistanceX(g37,g4) = 19.05
    c: DistanceX(g10,g29) = 9.525
    c: DistanceX(g33,g17) = 11.9
    c: DistanceY(g17,g33) = 14.9
    c: DistanceX(g0,g38) = 19.05
    c: DistanceY(g38,g29) = 9.525
    c: DistanceX(g38,g27) = 11.9
    c: DistanceY(g27,g38) = 11.9
    c: Horizontal(g17,g18)
    c: Horizontal(g18,g15)
    c: Horizontal(g15,g19)
    c: Horizontal(g19,g16)
    c: Horizontal(g16,g34)
    c: Horizontal(g35,g9)
    c: Horizontal(g9,g8)
    c: Horizontal(g8,g7)
    c: Horizontal(g7,g6)
    c: Horizontal(g6,g5)
    c: Horizontal(g36,g14)
    c: Horizontal(g14,g13)
    c: Horizontal(g13,g12)
    c: Horizontal(g12,g11)
    c: Horizontal(g11,g10)
    c: Vertical(g17,g35)
    c: Vertical(g35,g36)
    c: Vertical(g36,g37)
    c: Vertical(g18,g9)
    c: Vertical(g9,g14)
    c: Vertical(g14,g4)
    c: Vertical(g15,g8)
    c: Vertical(g8,g13)
    c: Vertical(g13,g3)
    c: Vertical(g19,g7)
    c: Vertical(g7,g12)
    c: Vertical(g12,g2)
    c: Vertical(g16,g6)
    c: Vertical(g6,g11)
    c: Vertical(g11,g1)
    c: Vertical(g34,g5)
    c: Vertical(g5,g10)
    c: Vertical(g10,g0)
    c: DistanceX(g38,g-1) = 19.05
    c: Horizontal(g37,g4)
    c: Horizontal(g4,g3)
    c: Horizontal(g3,g2)
    c: Horizontal(g2,g1)
    c: Horizontal(g1,g0)
    c: Horizontal(g0,g38)
    c: DistanceY(g-1,g38) = 19.05
    c: DistanceY(g38,g10) = 19.05
    c: Equal(g32,g26)
    c: Equal(g30,g26)
    c: Equal(g28,g26)
FEATURE [PartDesign::Pad] Pad  label="TL-Plate-Pad"
  Direction = (0,0,1)
  Length = 5
  Length2 = 10
  Profile = -> Sketch062
  ReferenceAxis = -> Sketch062 [N_Axis]
  Refine = true
  Suppressed = false
  Type = 0
  expr: Length = VarSet.Top_PcbZ + VarSet.Top_LoZ + VarSet.Top_MedZ + VarSet.Top_HiZ
FEATURE [PartDesign::Fillet] Fillet002  label="TL-Fillet"
  Base = -> Pad [Edge30,Edge4,Edge7,Edge10,Edge13,Edge16,Edge19]
  BaseFeature = -> Pad
  Radius = 2
  Refine = true
  SupportTransform = false
  Suppressed = false
  UseAllEdges = false
  expr: Radius = VarSet.Top_FilletR
FEATURE [PartDesign::Pocket] Pocket035  label="TL-Lo-Pocket"
  BaseFeature = -> Fillet002
  Direction = (0,0,-1)
  Length = 2.8
  Length2 = 5
  Profile = -> Sketch
  ReferenceAxis = -> Sketch [N_Axis]
  Refine = true
  Reversed = true
  Suppressed = false
  Type = 0
  expr: Length = VarSet.Top_PcbZ + VarSet.Top_LoZ
FEATURE [PartDesign::Pocket] Pocket036  label="TL-Hi-Pocket"
  BaseFeature = -> Pocket035
  Direction = (0,0,-1)
  Length = 1
  Length2 = 5
  Profile = -> Sketch002
  ReferenceAxis = -> Sketch002 [N_Axis]
  Refine = true
  Suppressed = false
  Type = 0
  expr: Length = VarSet.Top_HiZ
FEATURE [Sketcher::SketchObject] Sketch063  label="TR-Plate"
  ArcFitTolerance = 1e-06
  AttachmentSupport = -> [XY_Plane002]
  FullyConstrained = true
  MakeInternals = false
  MapMode = 5
  expr: Constraints[58] = 19.05 mm / 2
  expr: Constraints[59] = 19.05 mm / 2
  expr: Constraints[60] = VarSet.Top_MedXY / 2 + VarSet.Top_Frame
  expr: Constraints[61] = VarSet.Top_MedXY / 2 + VarSet.Top_Frame
  expr: Constraints[62] = VarSet.Top_MedXY / 2 + VarSet.Top_Frame
  expr: Constraints[63] = VarSet.Top_MedXY / 2 + VarSet.Top_Frame + VarSet.Top_RearAdd
  expr: Constraints[80] = VarSet.Top_FrameFilletR
  sketch-geometry (39):
    g0: GeomPoint [constr] X=38.1 Y=19.05 Z=0
    g1: GeomPoint [constr] X=57.15 Y=19.05 Z=0
    g2: GeomPoint [constr] X=38.1 Y=38.1 Z=0
    g3: GeomPoint [constr] X=76.2 Y=19.05 Z=0
    g4: GeomPoint [constr] X=95.25 Y=19.05 Z=0
    g5: GeomPoint [constr] X=57.15 Y=38.1 Z=0
    g6: GeomPoint [constr] X=76.2 Y=38.1 Z=0
    g7: GeomPoint [constr] X=114.3 Y=19.05 Z=0
    g8: GeomPoint [constr] X=95.25 Y=38.1 Z=0
    g9: GeomPoint [constr] X=38.1 Y=57.15 Z=0
    g10: GeomPoint [constr] X=57.15 Y=57.15 Z=0
    g11: GeomPoint [constr] X=76.2 Y=57.15 Z=0
    g12: GeomPoint [constr] X=95.25 Y=57.15 Z=0
    g13: GeomPoint [constr] X=38.1 Y=76.2 Z=0
    g14: GeomPoint [constr] X=57.15 Y=76.2 Z=0
    g15: GeomPoint [constr] X=76.2 Y=76.2 Z=0
    g16: GeomPoint [constr] X=95.25 Y=76.2 Z=0
    g17: GeomPoint [constr] X=114.3 Y=76.2 Z=0
    g18: GeomPoint [constr] X=114.3 Y=57.15 Z=0
    g19: GeomPoint [constr] X=114.3 Y=38.1 Z=0
    g20: GeomPoint [constr] X=133.35 Y=19.05 Z=0
    g21: GeomPoint [constr] X=19.05 Y=19.05 Z=0
    g22: GeomPoint [constr] X=133.35 Y=38.1 Z=0
    g23: GeomPoint [constr] X=133.35 Y=57.15 Z=0
    g24: GeomPoint [constr] X=133.35 Y=76.2 Z=0
    g25: LineSegment StartX=7.15 StartY=9.15 StartZ=0 EndX=7.15 EndY=28.575 EndZ=0
    g26: LineSegment StartX=7.15 StartY=28.575 StartZ=0 EndX=26.575 EndY=28.575 EndZ=0
    g27: LineSegment StartX=28.575 StartY=30.575 StartZ=0 EndX=28.575 EndY=91.1 EndZ=0
    g28: LineSegment StartX=28.575 StartY=91.1 StartZ=0 EndX=143.25 EndY=91.1 EndZ=0
    g29: LineSegment StartX=145.25 StartY=89.1 StartZ=0 EndX=145.25 EndY=9.15 EndZ=0
    g30: LineSegment StartX=143.25 StartY=7.15 StartZ=0 EndX=9.15 EndY=7.15 EndZ=0
    g31: ArcOfCircle CenterX=26.575 CenterY=30.575 CenterZ=0 NormalX=0 NormalY=0 NormalZ=1 AngleXU=0 Radius=2 StartAngle=4.71239 EndAngle=6.28319
    g32: GeomPoint [constr] X=28.575 Y=28.575 Z=0
    g33: ArcOfCircle CenterX=9.15 CenterY=9.15 CenterZ=0 NormalX=0 NormalY=0 NormalZ=1 AngleXU=0 Radius=2 StartAngle=3.14159 EndAngle=4.71239
    g34: GeomPoint [constr] X=7.15 Y=7.15 Z=0
    g35: ArcOfCircle CenterX=143.25 CenterY=89.1 CenterZ=0 NormalX=0 NormalY=0 NormalZ=1 AngleXU=0 Radius=2 StartAngle=1.85e-14 EndAngle=1.5708
    g36: GeomPoint [constr] X=145.25 Y=91.1 Z=0
    g37: ArcOfCircle CenterX=143.25 CenterY=9.15 CenterZ=0 NormalX=0 NormalY=0 NormalZ=1 AngleXU=0 Radius=2 StartAngle=4.71239 EndAngle=6.28319
    g38: GeomPoint [constr] X=145.25 Y=7.15 Z=0
  constraints (84):
    c: Horizontal(g13,g14)
    c: Horizontal(g14,g15)
    c: Horizontal(g15,g16)
    c: Horizontal(g16,g17)
    c: Horizontal(g17,g24)
    c: Horizontal(g9,g10)
    c: Horizontal(g10,g11)
    c: Horizontal(g11,g12)
    c: Horizontal(g12,g18)
    c: Horizontal(g18,g23)
    c: Horizontal(g2,g5)
    c: Horizontal(g5,g6)
    c: Horizontal(g6,g8)
    c: Horizontal(g8,g19)
    c: Horizontal(g19,g22)
    c: Horizontal(g21,g0)
    c: Horizontal(g0,g1)
    c: Horizontal(g1,g3)
    c: Horizontal(g3,g4)
    c: Horizontal(g4,g7)
    c: Horizontal(g7,g20)
    c: Vertical(g13,g9)
    c: Vertical(g9,g2)
    c: Vertical(g2,g0)
    c: Vertical(g14,g10)
    c: Vertical(g10,g5)
    c: Vertical(g5,g1)
    c: Vertical(g15,g11)
    c: Vertical(g11,g6)
    c: Vertical(g6,g3)
    c: Vertical(g16,g12)
    c: Vertical(g12,g8)
    c: Vertical(g8,g4)
    c: Vertical(g17,g18)
    c: Vertical(g18,g19)
    c: Vertical(g19,g7)
    c: Vertical(g24,g23)
    c: Vertical(g23,g22)
    c: Vertical(g22,g20)
    c: DistanceX(g21,g0) = 19.05
    c: DistanceX(g0,g1) = 19.05
    c: DistanceX(g1,g3) = 19.05
    c: DistanceX(g3,g4) = 19.05
    c: DistanceX(g4,g7) = 19.05
    c: DistanceX(g7,g20) = 19.05
    c: DistanceY(g9,g13) = 19.05
    c: DistanceY(g2,g9) = 19.05
    c: DistanceY(g21,g2) = 19.05
    c: DistanceX(g-1,g21) = 19.05
    c: DistanceY(g-1,g21) = 19.05
    c: Vertical(g25)
    c: Coincident(g25,g26)
    c: Horizontal(g26)
    c: Vertical(g27)
    c: Coincident(g27,g28)
    c: Horizontal(g28)
    c: Vertical(g29)
    c: Horizontal(g30)
    c: DistanceY(g21,g32) = 9.525
    c: DistanceX(g32,g2) = 9.525
    c: DistanceX(g34,g21) = 11.9
    c: DistanceY(g34,g21) = 11.9
    c: DistanceX(g24,g36) = 11.9
    c: DistanceY(g24,g36) = 14.9
    c: PointOnObject(g32,g26)
    c: PointOnObject(g32,g27)
    c: Tangent(g26,g31) = -1.5708
    c: Tangent(g27,g31) = -1.5708
    c: PointOnObject(g34,g25)
    c: PointOnObject(g34,g30)
    c: Tangent(g25,g33) = 1.5708
    c: Tangent(g30,g33) = 1.5708
    c: PointOnObject(g36,g28)
    c: PointOnObject(g36,g29)
    c: Tangent(g28,g35) = 1.5708
    c: Tangent(g29,g35) = 1.5708
    c: PointOnObject(g38,g29)
    c: PointOnObject(g38,g30)
    c: Tangent(g29,g37) = 1.5708
    c: Tangent(g30,g37) = 1.5708
    c: Radius(g33) = 2
    c: Equal(g35,g33)
    c: Equal(g37,g33)
    c: Equal(g31,g33)
FEATURE [PartDesign::Pad] Pad019  label="TR-Plate-Pad"
  Direction = (0,0,1)
  Length = 5
  Length2 = 10
  Profile = -> Sketch063
  ReferenceAxis = -> Sketch063 [N_Axis]
  Refine = true
  Suppressed = false
  Type = 0
  expr: Length = VarSet.Top_PcbZ + VarSet.Top_LoZ + VarSet.Top_MedZ + VarSet.Top_HiZ
FEATURE [PartDesign::Fillet] Fillet  label="TR-Fillet"
  Base = -> Pad019 [Edge16,Edge19,Edge22,Edge25,Edge28,Edge30,Edge4]
  BaseFeature = -> Pad019
  Radius = 2
  Refine = true
  SupportTransform = false
  Suppressed = false
  UseAllEdges = false
  expr: Radius = VarSet.Top_FilletR
FEATURE [PartDesign::Pocket] Pocket037  label="TR-Lo-Pocket"
  BaseFeature = -> Fillet
  Direction = (0,0,-1)
  Length = 2.8
  Length2 = 5
  Profile = -> Sketch007
  ReferenceAxis = -> Sketch007 [N_Axis]
  Refine = true
  Reversed = true
  Suppressed = false
  Type = 0
  expr: Length = VarSet.Top_PcbZ + VarSet.Top_LoZ
FEATURE [PartDesign::Pocket] Pocket038  label="TR-Hi-Pocket"
  BaseFeature = -> Pocket037
  Direction = (0,0,-1)
  Length = 1
  Length2 = 5
  Profile = -> Sketch014
  ReferenceAxis = -> Sketch014 [N_Axis]
  Refine = true
  Suppressed = false
  Type = 0
  expr: Length = VarSet.Top_HiZ
FEATURE [PartDesign::Pad] Pad020  label="TL-HiSw-Pad"
  BaseFeature = -> Pocket036
  Direction = (0,0,1)
  Length = 1
  Length2 = 10
  Profile = -> Sketch061
  ReferenceAxis = -> Sketch061 [N_Axis]
  Refine = true
  Reversed = true
  Suppressed = false
  Type = 0
  expr: Length = VarSet.Top_HiZ
FEATURE [PartDesign::Pocket] Pocket039  label="TL-Med-Pocket"
  BaseFeature = -> Pad020
  Direction = (0,0,-1)
  Length = 10
  Length2 = 5
  Profile = -> Sketch001
  ReferenceAxis = -> Sketch001 [N_Axis]
  Refine = true
  Reversed = true
  Suppressed = false
  Type = 1
FEATURE [PartDesign::Pocket] Pocket  label="TL-PCB-Pocket"
  BaseFeature = -> Pocket039
  Direction = (0,0,-1)
  Length = 1.5
  Length2 = 5
  Profile = -> Sketch003
  ReferenceAxis = -> Sketch003 [N_Axis]
  Refine = true
  Reversed = true
  Suppressed = false
  Type = 0
  expr: Length = VarSet.Top_PcbZ
FEATURE [PartDesign::Pad] Pad014  label="TL-ScrewPostOut-Pad"
  BaseFeature = -> Pocket
  Direction = (0,0,1)
  Length = 1.5
  Length2 = 10
  Profile = -> Sketch039
  ReferenceAxis = -> Sketch039 [N_Axis]
  Refine = true
  Suppressed = false
  Type = 0
  expr: Length = VarSet.Top_PcbZ
FEATURE [PartDesign::Pocket] Pocket001  label="TL-ScrewPostIn-Pocket"
  BaseFeature = -> Pad014
  Direction = (0,0,-1)
  Length = 4
  Length2 = 5
  Profile = -> Sketch004
  ReferenceAxis = -> Sketch004 [N_Axis]
  Refine = true
  Reversed = true
  Suppressed = false
  Type = 0
  expr: Length = VarSet.Top_PcbZ + VarSet.Top_LoZ + VarSet.Top_MedZ
FEATURE [Sketcher::SketchObject] Sketch064  label="TR-HiSw"
  ArcFitTolerance = 1e-06
  AttachmentOffset = pos=(0,0,5) rot=(0,0,1;0rad)
  AttachmentSupport = -> [XY_Plane002]
  FullyConstrained = true
  MakeInternals = false
  MapMode = 5
  Placement = pos=(0,0,5) rot=(0,0,1;0rad)
  expr: .AttachmentOffset.Base.z = VarSet.Top_PcbZ + VarSet.Top_LoZ + VarSet.Top_MedZ + VarSet.Top_HiZ
  expr: Constraints[46] = 19.05 mm / 2
  expr: Constraints[47] = 6 * 19.05 mm
  expr: Constraints[48] = 4 * 19.05 mm
  expr: Constraints[49] = 7 * 19.05 mm
  sketch-geometry (20):
    g0: LineSegment StartX=142.875 StartY=81.2 StartZ=0 EndX=142.875 EndY=71.2 EndZ=0
    g1: GeomPoint [constr] X=85.725 Y=76.2 Z=0
    g2: LineSegment StartX=142.875 StartY=62.15 StartZ=0 EndX=142.875 EndY=52.15 EndZ=0
    g3: GeomPoint [constr] X=85.725 Y=57.15 Z=0
    g4: LineSegment StartX=142.875 StartY=43.1 StartZ=0 EndX=142.875 EndY=33.1 EndZ=0
    g5: GeomPoint [constr] X=85.725 Y=38.1 Z=0
    g6: LineSegment StartX=142.875 StartY=24.05 StartZ=0 EndX=142.875 EndY=14.05 EndZ=0
    g7: GeomPoint [constr] X=76.2 Y=19.05 Z=0
    g8: LineSegment StartX=142.875 StartY=71.2 StartZ=0 EndX=28.575 EndY=71.2 EndZ=0
    g9: LineSegment StartX=28.575 StartY=71.2 StartZ=0 EndX=28.575 EndY=81.2 EndZ=0
    g10: LineSegment StartX=28.575 StartY=81.2 StartZ=0 EndX=142.875 EndY=81.2 EndZ=0
    g11: LineSegment StartX=142.875 StartY=52.15 StartZ=0 EndX=28.575 EndY=52.15 EndZ=0
    g12: LineSegment StartX=28.575 StartY=52.15 StartZ=0 EndX=28.575 EndY=62.15 EndZ=0
    g13: LineSegment StartX=28.575 StartY=62.15 StartZ=0 EndX=142.875 EndY=62.15 EndZ=0
    g14: LineSegment StartX=142.875 StartY=33.1 StartZ=0 EndX=28.575 EndY=33.1 EndZ=0
    g15: LineSegment StartX=28.575 StartY=33.1 StartZ=0 EndX=28.575 EndY=43.1 EndZ=0
    g16: LineSegment StartX=28.575 StartY=43.1 StartZ=0 EndX=142.875 EndY=43.1 EndZ=0
    g17: LineSegment StartX=9.525 StartY=24.05 StartZ=0 EndX=142.875 EndY=24.05 EndZ=0
    g18: LineSegment StartX=142.875 StartY=14.05 StartZ=0 EndX=9.525 EndY=14.05 EndZ=0
    g19: LineSegment StartX=9.525 StartY=14.05 StartZ=0 EndX=9.525 EndY=24.05 EndZ=0
  constraints (52):
    c: Coincident(g0,g8)
    c: Coincident(g8,g9)
    c: Coincident(g9,g10)
    c: Coincident(g10,g0)
    c: Vertical(g0)
    c: Vertical(g9)
    c: Horizontal(g8)
    c: Horizontal(g10)
    c: Symmetric(g9,g0,g1)
    c: Coincident(g2,g11)
    c: Coincident(g11,g12)
    c: Coincident(g12,g13)
    c: Coincident(g13,g2)
    c: Vertical(g2)
    c: Vertical(g12)
    c: Horizontal(g11)
    c: Horizontal(g13)
    c: Symmetric(g12,g2,g3)
    c: Coincident(g4,g14)
    c: Coincident(g14,g15)
    c: Coincident(g15,g16)
    c: Coincident(g16,g4)
    c: Vertical(g4)
    c: Vertical(g15)
    c: Horizontal(g14)
    c: Horizontal(g16)
    c: Symmetric(g15,g4,g5)
    c: Coincident(g17,g6)
    c: Coincident(g6,g18)
    c: Coincident(g18,g19)
    c: Coincident(g19,g17)
    c: Horizontal(g17)
    c: Horizontal(g18)
    c: Vertical(g6)
    c: Vertical(g19)
    c: Symmetric(g18,g17,g7)
    c: Equal(g8,g11)
    c: Equal(g11,g14)
    c: Equal(g0,g2)
    c: Equal(g2,g4)
    c: Equal(g4,g6)
    c: DistanceY(g19,g19) = 10
    c: DistanceY(g3,g1) = 19.05
    c: DistanceY(g5,g3) = 19.05
    c: DistanceY(g7,g5) = 19.05
    c: DistanceY(g-1,g7) = 19.05
    c: DistanceX(g7,g5) = 9.525
    c: DistanceX(g10,g10) = 114.3
    c: DistanceX(g-1,g7) = 76.2
    c: DistanceX(g18,g18) = 133.35
    c: Vertical(g5,g3)
    c: Vertical(g3,g1)
FEATURE [PartDesign::Pad] Pad021  label="TR-HiSw-Pad"
  BaseFeature = -> Pocket038
  Direction = (0,0,1)
  Length = 1
  Length2 = 10
  Profile = -> Sketch064
  ReferenceAxis = -> Sketch064 [N_Axis]
  Refine = true
  Reversed = true
  Suppressed = false
  Type = 0
  expr: Length = VarSet.Top_HiZ
FEATURE [PartDesign::Pocket] Pocket040  label="TR-Med-Pocket"
  BaseFeature = -> Pad021
  Direction = (0,0,-1)
  Length = 5
  Length2 = 5
  Profile = -> Sketch013
  ReferenceAxis = -> Sketch013 [N_Axis]
  Refine = true
  Reversed = true
  Suppressed = false
  Type = 1
FEATURE [PartDesign::Pocket] Pocket002  label="TR-PCB-Pocket"
  BaseFeature = -> Pocket040
  Direction = (0,0,-1)
  Length = 1.5
  Length2 = 5
  Profile = -> Sketch015
  ReferenceAxis = -> Sketch015 [N_Axis]
  Refine = true
  Reversed = true
  Suppressed = false
  Type = 0
  expr: Length = VarSet.Top_PcbZ
FEATURE [PartDesign::Pad] Pad015  label="TR-ScrewPostOut-Pad"
  BaseFeature = -> Pocket002
  Direction = (0,0,1)
  Length = 1.5
  Length2 = 10
  Profile = -> Sketch040
  ReferenceAxis = -> Sketch040 [N_Axis]
  Refine = true
  Suppressed = false
  Type = 0
  expr: Length = VarSet.Top_PcbZ
FEATURE [PartDesign::Pocket] Pocket003  label="TR-ScrewPostIn-Pocket"
  BaseFeature = -> Pad015
  Direction = (0,0,-1)
  Length = 4
  Length2 = 5
  Profile = -> Sketch016
  ReferenceAxis = -> Sketch016 [N_Axis]
  Refine = true
  Reversed = true
  Suppressed = false
  Type = 0
  expr: Length = VarSet.Top_PcbZ + VarSet.Top_LoZ + VarSet.Top_MedZ
FEATURE [Sketcher::SketchObject] Sketch065  label="BL-ScrewRecess"
  ArcFitTolerance = 1e-06
  AttachmentOffset = pos=(0,0,-3) rot=(0,0,1;0rad)
  AttachmentSupport = -> [XY_Plane001]
  FullyConstrained = true
  MakeInternals = false
  MapMode = 5
  Placement = pos=(0,0,-3) rot=(0,0,1;0rad)
  expr: .AttachmentOffset.Base.z = -VarSet.Bottom_PlateZ
  expr: Constraints[15] = VarSet.Screw_RecessD
  expr: Constraints[16] = 1.5 * 19.05 mm
  expr: Constraints[17] = 19.05 mm / 2
  expr: Constraints[48] = 19.05 mm + VarSet.Screw_RearAdd
  expr: Constraints[55] = 1.5 * 19.05 mm
  sketch-geometry (20):
    g0: Circle CenterX=-123.825 CenterY=28.575 CenterZ=0 NormalX=0 NormalY=0 NormalZ=1 AngleXU=0 Radius=1.95
    g1: Circle CenterX=-123.825 CenterY=66.675 CenterZ=0 NormalX=0 NormalY=0 NormalZ=1 AngleXU=0 Radius=1.95
    g2: Circle CenterX=-85.725 CenterY=66.675 CenterZ=0 NormalX=0 NormalY=0 NormalZ=1 AngleXU=0 Radius=1.95
    g3: Circle CenterX=-85.725 CenterY=28.575 CenterZ=0 NormalX=0 NormalY=0 NormalZ=1 AngleXU=0 Radius=1.95
    g4: Circle CenterX=-47.625 CenterY=28.575 CenterZ=0 NormalX=0 NormalY=0 NormalZ=1 AngleXU=0 Radius=1.95
    g5: Circle CenterX=-47.625 CenterY=66.675 CenterZ=0 NormalX=0 NormalY=0 NormalZ=1 AngleXU=0 Radius=1.95
    g6: Circle CenterX=-123.825 CenterY=9.525 CenterZ=0 NormalX=0 NormalY=0 NormalZ=1 AngleXU=0 Radius=1.95
    g7: Circle CenterX=-104.775 CenterY=9.525 CenterZ=0 NormalX=0 NormalY=0 NormalZ=1 AngleXU=0 Radius=1.95
    g8: Circle CenterX=-85.725 CenterY=9.525 CenterZ=0 NormalX=0 NormalY=0 NormalZ=1 AngleXU=0 Radius=1.95
    g9: Circle CenterX=-66.675 CenterY=9.525 CenterZ=0 NormalX=0 NormalY=0 NormalZ=1 AngleXU=0 Radius=1.95
    g10: Circle CenterX=-47.625 CenterY=9.525 CenterZ=0 NormalX=0 NormalY=0 NormalZ=1 AngleXU=0 Radius=1.95
    g11: Circle CenterX=-28.575 CenterY=9.525 CenterZ=0 NormalX=0 NormalY=0 NormalZ=1 AngleXU=0 Radius=1.95
    g12: Circle CenterX=-123.825 CenterY=88.225 CenterZ=0 NormalX=0 NormalY=0 NormalZ=1 AngleXU=0 Radius=1.95
    g13: Circle CenterX=-104.775 CenterY=88.225 CenterZ=0 NormalX=0 NormalY=0 NormalZ=1 AngleXU=0 Radius=1.95
    g14: Circle CenterX=-85.725 CenterY=88.225 CenterZ=0 NormalX=0 NormalY=0 NormalZ=1 AngleXU=0 Radius=1.95
    g15: Circle CenterX=-66.675 CenterY=88.225 CenterZ=0 NormalX=0 NormalY=0 NormalZ=1 AngleXU=0 Radius=1.95
    g16: Circle CenterX=-47.625 CenterY=88.225 CenterZ=0 NormalX=0 NormalY=0 NormalZ=1 AngleXU=0 Radius=1.95
    g17: Circle CenterX=-11.43 CenterY=88.225 CenterZ=0 NormalX=0 NormalY=0 NormalZ=1 AngleXU=0 Radius=1.95
    g18: Circle CenterX=-26.67 CenterY=88.225 CenterZ=0 NormalX=0 NormalY=0 NormalZ=1 AngleXU=0 Radius=1.95
    g19: GeomPoint X=-19.05 Y=88.225 Z=0
  constraints (58):
    c: Horizontal(g6,g7)
    c: Horizontal(g7,g8)
    c: Horizontal(g8,g9)
    c: Horizontal(g9,g10)
    c: Horizontal(g10,g11)
    c: DistanceX(g10,g11) = 19.05
    c: DistanceX(g9,g10) = 19.05
    c: DistanceX(g8,g9) = 19.05
    c: DistanceX(g7,g8) = 19.05
    c: DistanceX(g6,g7) = 19.05
    c: Equal(g6,g7)
    c: Equal(g7,g8)
    c: Equal(g8,g9)
    c: Equal(g9,g10)
    c: Equal(g10,g11)
    c: Diameter(g11) = 3.9
    c: DistanceX(g11,g-1) = 28.575
    c: DistanceY(g-1,g11) = 9.525
    c: DistanceY(g11,g4) = 19.05
    c: DistanceY(g4,g5) = 38.1
    c: Horizontal(g1,g2)
    c: Horizontal(g2,g5)
    c: Horizontal(g0,g3)
    c: Horizontal(g3,g4)
    c: Vertical(g1,g0)
    c: Vertical(g0,g6)
    c: Vertical(g2,g3)
    c: Vertical(g3,g8)
    c: Vertical(g5,g4)
    c: Vertical(g4,g10)
    c: Equal(g1,g2)
    c: Equal(g2,g5)
    c: Equal(g0,g3)
    c: Equal(g3,g4)
    c: Equal(g5,g4)
    c: Equal(g4,g10)
    c: Horizontal(g12,g13)
    c: Horizontal(g13,g14)
    c: Horizontal(g14,g15)
    c: Equal(g12,g13)
    c: Equal(g13,g14)
    c: Equal(g14,g15)
    c: Equal(g15,g16)
    c: Horizontal(g15,g16)
    c: DistanceX(g12,g13) = 19.05
    c: DistanceX(g13,g14) = 19.05
    c: DistanceX(g14,g15) = 19.05
    c: DistanceX(g15,g16) = 19.05
    c: DistanceY(g5,g16) = 21.55
    c: Equal(g16,g5)
    c: Equal(g18,g17)
    c: Symmetric(g18,g17,g19)
    c: Horizontal(g18,g17)
    c: DistanceX(g19,g-1) = 19.05
    c: DistanceX(g18,g19) = 7.62
    c: DistanceX(g16,g19) = 28.575
    c: Horizontal(g16,g19)
    c: Equal(g16,g18)
FEATURE [Sketcher::SketchObject] Sketch066  label="BR-ScrewRecess"
  ArcFitTolerance = 1e-06
  AttachmentOffset = pos=(0,0,-3) rot=(0,0,1;0rad)
  AttachmentSupport = -> [XY_Plane003]
  FullyConstrained = true
  MakeInternals = false
  MapMode = 5
  Placement = pos=(0,0,-3) rot=(0,0,1;0rad)
  expr: .AttachmentOffset.Base.z = -VarSet.Bottom_PlateZ
  expr: Constraints[10] = 1.5 * 19.05 mm
  expr: Constraints[32] = 19.05 mm / 2
  expr: Constraints[35] = VarSet.Screw_RecessD
  expr: Constraints[49] = 19.05 mm + VarSet.Screw_RearAdd
  expr: Constraints[57] = 1.5 * 19.05 mm
  sketch-geometry (20):
    g0: Circle CenterX=123.825 CenterY=28.575 CenterZ=0 NormalX=0 NormalY=0 NormalZ=1 AngleXU=0 Radius=1.95
    g1: Circle CenterX=123.825 CenterY=66.675 CenterZ=0 NormalX=0 NormalY=0 NormalZ=1 AngleXU=0 Radius=1.95
    g2: Circle CenterX=85.725 CenterY=66.675 CenterZ=0 NormalX=0 NormalY=0 NormalZ=1 AngleXU=0 Radius=1.95
    g3: Circle CenterX=85.725 CenterY=28.575 CenterZ=0 NormalX=0 NormalY=0 NormalZ=1 AngleXU=0 Radius=1.95
    g4: Circle CenterX=47.625 CenterY=28.575 CenterZ=0 NormalX=0 NormalY=0 NormalZ=1 AngleXU=0 Radius=1.95
    g5: Circle CenterX=47.625 CenterY=66.675 CenterZ=0 NormalX=0 NormalY=0 NormalZ=1 AngleXU=0 Radius=1.95
    g6: Circle CenterX=28.575 CenterY=9.525 CenterZ=0 NormalX=0 NormalY=0 NormalZ=1 AngleXU=0 Radius=1.95
    g7: Circle CenterX=47.625 CenterY=9.525 CenterZ=0 NormalX=0 NormalY=0 NormalZ=1 AngleXU=0 Radius=1.95
    g8: Circle CenterX=66.675 CenterY=9.525 CenterZ=0 NormalX=0 NormalY=0 NormalZ=1 AngleXU=0 Radius=1.95
    g9: Circle CenterX=85.725 CenterY=9.525 CenterZ=0 NormalX=0 NormalY=0 NormalZ=1 AngleXU=0 Radius=1.95
    g10: Circle CenterX=104.775 CenterY=9.525 CenterZ=0 NormalX=0 NormalY=0 NormalZ=1 AngleXU=0 Radius=1.95
    g11: Circle CenterX=123.825 CenterY=9.525 CenterZ=0 NormalX=0 NormalY=0 NormalZ=1 AngleXU=0 Radius=1.95
    g12: Circle CenterX=47.625 CenterY=88.225 CenterZ=0 NormalX=0 NormalY=0 NormalZ=1 AngleXU=0 Radius=1.95
    g13: Circle CenterX=66.675 CenterY=88.225 CenterZ=0 NormalX=0 NormalY=0 NormalZ=1 AngleXU=0 Radius=1.95
    g14: Circle CenterX=85.725 CenterY=88.225 CenterZ=0 NormalX=0 NormalY=0 NormalZ=1 AngleXU=0 Radius=1.95
    g15: Circle CenterX=104.775 CenterY=88.225 CenterZ=0 NormalX=0 NormalY=0 NormalZ=1 AngleXU=0 Radius=1.95
    g16: Circle CenterX=123.825 CenterY=88.225 CenterZ=0 NormalX=0 NormalY=0 NormalZ=1 AngleXU=0 Radius=1.95
    g17: Circle CenterX=26.67 CenterY=88.225 CenterZ=0 NormalX=0 NormalY=0 NormalZ=1 AngleXU=0 Radius=1.95
    g18: Circle CenterX=11.43 CenterY=88.225 CenterZ=0 NormalX=0 NormalY=0 NormalZ=1 AngleXU=0 Radius=1.95
    g19: GeomPoint X=19.05 Y=88.225 Z=0
  constraints (58):
    c: Horizontal(g6,g7)
    c: Horizontal(g7,g8)
    c: Horizontal(g8,g9)
    c: Horizontal(g9,g10)
    c: Horizontal(g10,g11)
    c: DistanceX(g10,g11) = 19.05
    c: DistanceX(g9,g10) = 19.05
    c: DistanceX(g8,g9) = 19.05
    c: DistanceX(g7,g8) = 19.05
    c: DistanceX(g6,g7) = 19.05
    c: DistanceX(g-1,g6) = 28.575
    c: Horizontal(g1,g2)
    c: Horizontal(g2,g5)
    c: Horizontal(g0,g3)
    c: Horizontal(g3,g4)
    c: Vertical(g1,g0)
    c: Vertical(g0,g11)
    c: Vertical(g2,g3)
    c: Vertical(g3,g9)
    c: Vertical(g5,g4)
    c: Vertical(g4,g7)
    c: Equal(g11,g10)
    c: Equal(g10,g9)
    c: Equal(g9,g8)
    c: Equal(g8,g7)
    c: Equal(g7,g6)
    c: Equal(g1,g2)
    c: Equal(g2,g5)
    c: Equal(g0,g3)
    c: Equal(g3,g4)
    c: Equal(g5,g4)
    c: Equal(g4,g7)
    c: DistanceY(g-1,g6) = 9.525
    c: DistanceY(g6,g4) = 19.05
    c: DistanceY(g4,g5) = 38.1
    c: Diameter(g6) = 3.9
    c: Horizontal(g12,g13)
    c: Horizontal(g13,g14)
    c: Horizontal(g14,g15)
    c: Horizontal(g15,g16)
    c: Equal(g12,g13)
    c: Equal(g13,g14)
    c: Equal(g14,g15)
    c: Equal(g15,g16)
    c: DistanceX(g12,g13) = 19.05
    c: DistanceX(g13,g14) = 19.05
    c: DistanceX(g14,g15) = 19.05
    c: DistanceX(g15,g16) = 19.05
    c: Equal(g12,g5)
    c: DistanceY(g5,g12) = 21.55
    c: Equal(g18,g17)
    c: Symmetric(g18,g17,g19)
    c: Horizontal(g18,g17)
    c: DistanceX(g18,g19) = 7.62
    c: DistanceX(g-1,g19) = 19.05
    c: Horizontal(g19,g12)
    c: Equal(g17,g12)
    c: DistanceX(g19,g12) = 28.575
FEATURE [PartDesign::Body] Body007  label="ModuleRight"
  AllowCompound = false
  Origin = -> Origin007
FEATURE [Sketcher::SketchObject] Sketch070  label="BL-PCB"
  ArcFitTolerance = 1e-06
  AttachmentSupport = -> [XY_Plane001]
  FullyConstrained = true
  MakeInternals = false
  MapMode = 5
  expr: Constraints[10] = VarSet.Top_PcbY
  expr: Constraints[11] = VarSet.Top_PcbX
  expr: Constraints[12] = 2.5 * 19.05 mm
  expr: Constraints[9] = 4 * 19.05 mm
  sketch-geometry (5):
    g0: LineSegment StartX=-142.5 StartY=85.375 StartZ=0 EndX=-142.5 EndY=9.875 EndZ=0
    g1: LineSegment StartX=-142.5 StartY=9.875 StartZ=0 EndX=-9.9 EndY=9.875 EndZ=0
    g2: LineSegment StartX=-9.9 StartY=9.875 StartZ=0 EndX=-9.9 EndY=85.375 EndZ=0
    g3: LineSegment StartX=-9.9 StartY=85.375 StartZ=0 EndX=-142.5 EndY=85.375 EndZ=0
    g4: GeomPoint [constr] X=-76.2 Y=47.625 Z=0
  constraints (13):
    c: Coincident(g0,g1)
    c: Coincident(g1,g2)
    c: Coincident(g2,g3)
    c: Coincident(g3,g0)
    c: Vertical(g0)
    c: Vertical(g2)
    c: Horizontal(g1)
    c: Horizontal(g3)
    c: Symmetric(g2,g0,g4)
    c: DistanceX(g4,g-1) = 76.2
    c: DistanceY(g0,g0) = 75.5
    c: DistanceX(g1,g1) = 132.6
    c: DistanceY(g-1,g4) = 47.625
FEATURE [Sketcher::SketchObject] Sketch071  label="BR-PCB"
  ArcFitTolerance = 1e-06
  AttachmentSupport = -> [XY_Plane003]
  FullyConstrained = true
  MakeInternals = false
  MapMode = 5
  expr: Constraints[10] = 4 * 19.05 mm
  expr: Constraints[11] = VarSet.Top_PcbY
  expr: Constraints[12] = 2.5 * 19.05 mm
  expr: Constraints[9] = VarSet.Top_PcbX
  sketch-geometry (5):
    g0: LineSegment StartX=9.9 StartY=85.375 StartZ=0 EndX=9.9 EndY=9.875 EndZ=0
    g1: LineSegment StartX=9.9 StartY=9.875 StartZ=0 EndX=142.5 EndY=9.875 EndZ=0
    g2: LineSegment StartX=142.5 StartY=9.875 StartZ=0 EndX=142.5 EndY=85.375 EndZ=0
    g3: LineSegment StartX=142.5 StartY=85.375 StartZ=0 EndX=9.9 EndY=85.375 EndZ=0
    g4: GeomPoint [constr] X=76.2 Y=47.625 Z=0
  constraints (13):
    c: Coincident(g0,g1)
    c: Coincident(g1,g2)
    c: Coincident(g2,g3)
    c: Coincident(g3,g0)
    c: Vertical(g0)
    c: Vertical(g2)
    c: Horizontal(g1)
    c: Horizontal(g3)
    c: Symmetric(g2,g0,g4)
    c: DistanceX(g1,g1) = 132.6
    c: DistanceX(g-1,g4) = 76.2
    c: DistanceY(g2,g2) = 75.5
    c: DistanceY(g-1,g4) = 47.625
FEATURE [PartDesign::Fillet] Fillet004  label="BL-Fillet"
  Base = -> Pad010 [Edge13,Edge16,Edge19,Edge22,Edge24,Edge4,Edge7]
  BaseFeature = -> Pad010
  Radius = 0.1
  Refine = true
  SupportTransform = false
  Suppressed = false
  UseAllEdges = false
  expr: Radius = VarSet.Bottom_FilletR
FEATURE [PartDesign::Pocket] Pocket004  label="BL-Stem-Pocket"
  BaseFeature = -> Fillet004
  Direction = (0,0,-1)
  Length = 1.2
  Length2 = 5
  Profile = -> Sketch018
  ReferenceAxis = -> Sketch018 [N_Axis]
  Refine = true
  Suppressed = false
  Type = 0
  expr: Length = VarSet.Bottom_StemZ
  expr: TaperAngle = VarSet.Bottom_StemTaper
FEATURE [PartDesign::Pocket] Pocket007  label="BL-Contact-Pocket"
  BaseFeature = -> Pocket004
  Direction = (0,0,-1)
  Length = 1.5
  Length2 = 5
  Profile = -> Sketch021
  ReferenceAxis = -> Sketch021 [N_Axis]
  Refine = true
  Suppressed = false
  Type = 0
  expr: Length = VarSet.Bottom_ContactZ
  expr: TaperAngle = VarSet.Bottom_ContactTaper
FEATURE [PartDesign::Pocket] Pocket016  label="BL-ContactEnc-Pocket"
  BaseFeature = -> Pocket007
  Direction = (0,0,-1)
  Length = 1.5
  Length2 = 5
  Profile = -> Sketch030
  ReferenceAxis = -> Sketch030 [N_Axis]
  Refine = true
  Suppressed = false
  Type = 0
  expr: Length = VarSet.Bottom_ContactZ
  expr: TaperAngle = VarSet.Bottom_ContactTaper
FEATURE [PartDesign::Pocket] Pocket010  label="BL-LED-Pocket"
  BaseFeature = -> Pocket016
  Direction = (0,0,-1)
  Length = 1.2
  Length2 = 5
  Profile = -> Sketch022
  ReferenceAxis = -> Sketch022 [N_Axis]
  Refine = true
  Suppressed = false
  Type = 0
  expr: Length = VarSet.Bottom_LedZ
FEATURE [PartDesign::Pocket] Pocket011  label="BL-UnderLED-Pocket"
  BaseFeature = -> Pocket010
  Direction = (0,0,-1)
  Length = 1.8
  Length2 = 5
  Profile = -> Sketch023
  ReferenceAxis = -> Sketch023 [N_Axis]
  Refine = true
  Suppressed = false
  Type = 0
  expr: Length = VarSet.Bottom_UnderLedZ
FEATURE [PartDesign::Pocket] Pocket014  label="BL-Diode-Pocket"
  BaseFeature = -> Pocket011
  Direction = (0,0,-1)
  Length = 1.5
  Length2 = 5
  Profile = -> Sketch029
  ReferenceAxis = -> Sketch029 [N_Axis]
  Refine = true
  Suppressed = false
  Type = 0
  expr: Length = VarSet.Bottom_DiodeZ
FEATURE [PartDesign::Fillet] Fillet005  label="BR-Fillet"
  Base = -> Pad011 [Edge16,Edge13,Edge10,Edge7,Edge4,Edge24,Edge22,Edge19]
  BaseFeature = -> Pad011
  Radius = 0.1
  Refine = true
  SupportTransform = false
  Suppressed = false
  UseAllEdges = false
  expr: Radius = VarSet.Bottom_FilletR
FEATURE [PartDesign::Pocket] Pocket008  label="BR-Stem-Pocket"
  BaseFeature = -> Fillet005
  Direction = (0,0,-1)
  Length = 1.2
  Length2 = 5
  Profile = -> Sketch025
  ReferenceAxis = -> Sketch025 [N_Axis]
  Refine = true
  Suppressed = false
  Type = 0
  expr: Length = VarSet.Bottom_StemZ
  expr: TaperAngle = VarSet.Bottom_StemTaper
FEATURE [PartDesign::Pocket] Pocket009  label="BR-Contact-Pocket"
  BaseFeature = -> Pocket008
  Direction = (0,0,-1)
  Length = 1.5
  Length2 = 5
  Profile = -> Sketch026
  ReferenceAxis = -> Sketch026 [N_Axis]
  Refine = true
  Suppressed = false
  Type = 0
  expr: Length = VarSet.Bottom_ContactZ
  expr: TaperAngle = VarSet.Bottom_ContactTaper
FEATURE [PartDesign::Pocket] Pocket017  label="BR-ContactEnc-Pocket"
  BaseFeature = -> Pocket009
  Direction = (0,0,-1)
  Length = 1.5
  Length2 = 5
  Profile = -> Sketch032
  ReferenceAxis = -> Sketch032 [N_Axis]
  Refine = true
  Suppressed = false
  Type = 0
  expr: Length = VarSet.Bottom_ContactZ
  expr: TaperAngle = VarSet.Bottom_ContactTaper
FEATURE [PartDesign::Pocket] Pocket012  label="BR-LED-Pocket"
  BaseFeature = -> Pocket017
  Direction = (0,0,-1)
  Length = 1.2
  Length2 = 5
  Profile = -> Sketch027
  ReferenceAxis = -> Sketch027 [N_Axis]
  Refine = true
  Suppressed = false
  Type = 0
  expr: Length = VarSet.Bottom_LedZ
FEATURE [PartDesign::Pocket] Pocket013  label="BR-UnderLED-Pocket"
  BaseFeature = -> Pocket012
  Direction = (0,0,-1)
  Length = 1.8
  Length2 = 5
  Profile = -> Sketch028
  ReferenceAxis = -> Sketch028 [N_Axis]
  Refine = true
  Suppressed = false
  Type = 0
  expr: Length = VarSet.Bottom_UnderLedZ
FEATURE [PartDesign::Pocket] Pocket015  label="BR-Diode-Pocket"
  BaseFeature = -> Pocket013
  Direction = (0,0,-1)
  Length = 1.5
  Length2 = 5
  Profile = -> Sketch031
  ReferenceAxis = -> Sketch031 [N_Axis]
  Refine = true
  Suppressed = false
  Type = 0
  expr: Length = VarSet.Bottom_DiodeZ
FEATURE [Sketcher::SketchObject] Sketch072  label="BL-ScrewPostOut"
  ArcFitTolerance = 1e-06
  AttachmentSupport = -> [XY_Plane001]
  FullyConstrained = true
  MakeInternals = false
  MapMode = 5
  expr: Constraints[15] = VarSet.Screw_PostOutD
  expr: Constraints[16] = 1.5 * 19.05 mm
  expr: Constraints[17] = 19.05 mm / 2
  expr: Constraints[48] = 19.05 mm + VarSet.Screw_RearAdd
  expr: Constraints[55] = 1.5 * 19.05 mm
  sketch-geometry (20):
    g0: Circle CenterX=-123.825 CenterY=28.575 CenterZ=0 NormalX=0 NormalY=0 NormalZ=1 AngleXU=0 Radius=1.75
    g1: Circle CenterX=-123.825 CenterY=66.675 CenterZ=0 NormalX=0 NormalY=0 NormalZ=1 AngleXU=0 Radius=1.75
    g2: Circle CenterX=-85.725 CenterY=66.675 CenterZ=0 NormalX=0 NormalY=0 NormalZ=1 AngleXU=0 Radius=1.75
    g3: Circle CenterX=-85.725 CenterY=28.575 CenterZ=0 NormalX=0 NormalY=0 NormalZ=1 AngleXU=0 Radius=1.75
    g4: Circle CenterX=-47.625 CenterY=28.575 CenterZ=0 NormalX=0 NormalY=0 NormalZ=1 AngleXU=0 Radius=1.75
    g5: Circle CenterX=-47.625 CenterY=66.675 CenterZ=0 NormalX=0 NormalY=0 NormalZ=1 AngleXU=0 Radius=1.75
    g6: Circle CenterX=-123.825 CenterY=9.525 CenterZ=0 NormalX=0 NormalY=0 NormalZ=1 AngleXU=0 Radius=1.75
    g7: Circle CenterX=-104.775 CenterY=9.525 CenterZ=0 NormalX=0 NormalY=0 NormalZ=1 AngleXU=0 Radius=1.75
    g8: Circle CenterX=-85.725 CenterY=9.525 CenterZ=0 NormalX=0 NormalY=0 NormalZ=1 AngleXU=0 Radius=1.75
    g9: Circle CenterX=-66.675 CenterY=9.525 CenterZ=0 NormalX=0 NormalY=0 NormalZ=1 AngleXU=0 Radius=1.75
    g10: Circle CenterX=-47.625 CenterY=9.525 CenterZ=0 NormalX=0 NormalY=0 NormalZ=1 AngleXU=0 Radius=1.75
    g11: Circle CenterX=-28.575 CenterY=9.525 CenterZ=0 NormalX=0 NormalY=0 NormalZ=1 AngleXU=0 Radius=1.75
    g12: Circle CenterX=-123.825 CenterY=88.225 CenterZ=0 NormalX=0 NormalY=0 NormalZ=1 AngleXU=0 Radius=1.75
    g13: Circle CenterX=-104.775 CenterY=88.225 CenterZ=0 NormalX=0 NormalY=0 NormalZ=1 AngleXU=0 Radius=1.75
    g14: Circle CenterX=-85.725 CenterY=88.225 CenterZ=0 NormalX=0 NormalY=0 NormalZ=1 AngleXU=0 Radius=1.75
    g15: Circle CenterX=-66.675 CenterY=88.225 CenterZ=0 NormalX=0 NormalY=0 NormalZ=1 AngleXU=0 Radius=1.75
    g16: Circle CenterX=-47.625 CenterY=88.225 CenterZ=0 NormalX=0 NormalY=0 NormalZ=1 AngleXU=0 Radius=1.75
    g17: Circle CenterX=-11.43 CenterY=88.225 CenterZ=0 NormalX=0 NormalY=0 NormalZ=1 AngleXU=0 Radius=1.75
    g18: Circle CenterX=-26.67 CenterY=88.225 CenterZ=0 NormalX=0 NormalY=0 NormalZ=1 AngleXU=0 Radius=1.75
    g19: GeomPoint X=-19.05 Y=88.225 Z=0
  constraints (58):
    c: Horizontal(g6,g7)
    c: Horizontal(g7,g8)
    c: Horizontal(g8,g9)
    c: Horizontal(g9,g10)
    c: Horizontal(g10,g11)
    c: DistanceX(g10,g11) = 19.05
    c: DistanceX(g9,g10) = 19.05
    c: DistanceX(g8,g9) = 19.05
    c: DistanceX(g7,g8) = 19.05
    c: DistanceX(g6,g7) = 19.05
    c: Equal(g6,g7)
    c: Equal(g7,g8)
    c: Equal(g8,g9)
    c: Equal(g9,g10)
    c: Equal(g10,g11)
    c: Diameter(g11) = 3.5
    c: DistanceX(g11,g-1) = 28.575
    c: DistanceY(g-1,g11) = 9.525
    c: DistanceY(g11,g4) = 19.05
    c: DistanceY(g4,g5) = 38.1
    c: Horizontal(g1,g2)
    c: Horizontal(g2,g5)
    c: Horizontal(g0,g3)
    c: Horizontal(g3,g4)
    c: Vertical(g1,g0)
    c: Vertical(g0,g6)
    c: Vertical(g2,g3)
    c: Vertical(g3,g8)
    c: Vertical(g5,g4)
    c: Vertical(g4,g10)
    c: Equal(g1,g2)
    c: Equal(g2,g5)
    c: Equal(g0,g3)
    c: Equal(g3,g4)
    c: Equal(g5,g4)
    c: Equal(g4,g10)
    c: Horizontal(g12,g13)
    c: Horizontal(g13,g14)
    c: Horizontal(g14,g15)
    c: Equal(g12,g13)
    c: Equal(g13,g14)
    c: Equal(g14,g15)
    c: Equal(g15,g16)
    c: Horizontal(g15,g16)
    c: DistanceX(g12,g13) = 19.05
    c: DistanceX(g13,g14) = 19.05
    c: DistanceX(g14,g15) = 19.05
    c: DistanceX(g15,g16) = 19.05
    c: DistanceY(g5,g16) = 21.55
    c: Equal(g16,g5)
    c: Equal(g18,g17)
    c: Symmetric(g18,g17,g19)
    c: Horizontal(g18,g17)
    c: DistanceX(g19,g-1) = 19.05
    c: DistanceX(g18,g19) = 7.62
    c: DistanceX(g16,g19) = 28.575
    c: Horizontal(g16,g19)
    c: Equal(g16,g18)
FEATURE [Sketcher::SketchObject] Sketch073  label="BR-ScrewPostOut"
  ArcFitTolerance = 1e-06
  AttachmentSupport = -> [XY_Plane003]
  FullyConstrained = true
  MakeInternals = false
  MapMode = 5
  expr: Constraints[10] = 1.5 * 19.05 mm
  expr: Constraints[32] = 19.05 mm / 2
  expr: Constraints[35] = VarSet.Screw_PostOutD
  expr: Constraints[49] = 19.05 mm + VarSet.Screw_RearAdd
  expr: Constraints[57] = 1.5 * 19.05 mm
  sketch-geometry (20):
    g0: Circle CenterX=123.825 CenterY=28.575 CenterZ=0 NormalX=0 NormalY=0 NormalZ=1 AngleXU=0 Radius=1.75
    g1: Circle CenterX=123.825 CenterY=66.675 CenterZ=0 NormalX=0 NormalY=0 NormalZ=1 AngleXU=0 Radius=1.75
    g2: Circle CenterX=85.725 CenterY=66.675 CenterZ=0 NormalX=0 NormalY=0 NormalZ=1 AngleXU=0 Radius=1.75
    g3: Circle CenterX=85.725 CenterY=28.575 CenterZ=0 NormalX=0 NormalY=0 NormalZ=1 AngleXU=0 Radius=1.75
    g4: Circle CenterX=47.625 CenterY=28.575 CenterZ=0 NormalX=0 NormalY=0 NormalZ=1 AngleXU=0 Radius=1.75
    g5: Circle CenterX=47.625 CenterY=66.675 CenterZ=0 NormalX=0 NormalY=0 NormalZ=1 AngleXU=0 Radius=1.75
    g6: Circle CenterX=28.575 CenterY=9.525 CenterZ=0 NormalX=0 NormalY=0 NormalZ=1 AngleXU=0 Radius=1.75
    g7: Circle CenterX=47.625 CenterY=9.525 CenterZ=0 NormalX=0 NormalY=0 NormalZ=1 AngleXU=0 Radius=1.75
    g8: Circle CenterX=66.675 CenterY=9.525 CenterZ=0 NormalX=0 NormalY=0 NormalZ=1 AngleXU=0 Radius=1.75
    g9: Circle CenterX=85.725 CenterY=9.525 CenterZ=0 NormalX=0 NormalY=0 NormalZ=1 AngleXU=0 Radius=1.75
    g10: Circle CenterX=104.775 CenterY=9.525 CenterZ=0 NormalX=0 NormalY=0 NormalZ=1 AngleXU=0 Radius=1.75
    g11: Circle CenterX=123.825 CenterY=9.525 CenterZ=0 NormalX=0 NormalY=0 NormalZ=1 AngleXU=0 Radius=1.75
    g12: Circle CenterX=47.625 CenterY=88.225 CenterZ=0 NormalX=0 NormalY=0 NormalZ=1 AngleXU=0 Radius=1.75
    g13: Circle CenterX=66.675 CenterY=88.225 CenterZ=0 NormalX=0 NormalY=0 NormalZ=1 AngleXU=0 Radius=1.75
    g14: Circle CenterX=85.725 CenterY=88.225 CenterZ=0 NormalX=0 NormalY=0 NormalZ=1 AngleXU=0 Radius=1.75
    g15: Circle CenterX=104.775 CenterY=88.225 CenterZ=0 NormalX=0 NormalY=0 NormalZ=1 AngleXU=0 Radius=1.75
    g16: Circle CenterX=123.825 CenterY=88.225 CenterZ=0 NormalX=0 NormalY=0 NormalZ=1 AngleXU=0 Radius=1.75
    g17: Circle CenterX=26.67 CenterY=88.225 CenterZ=0 NormalX=0 NormalY=0 NormalZ=1 AngleXU=0 Radius=1.75
    g18: Circle CenterX=11.43 CenterY=88.225 CenterZ=0 NormalX=0 NormalY=0 NormalZ=1 AngleXU=0 Radius=1.75
    g19: GeomPoint X=19.05 Y=88.225 Z=0
  constraints (58):
    c: Horizontal(g6,g7)
    c: Horizontal(g7,g8)
    c: Horizontal(g8,g9)
    c: Horizontal(g9,g10)
    c: Horizontal(g10,g11)
    c: DistanceX(g10,g11) = 19.05
    c: DistanceX(g9,g10) = 19.05
    c: DistanceX(g8,g9) = 19.05
    c: DistanceX(g7,g8) = 19.05
    c: DistanceX(g6,g7) = 19.05
    c: DistanceX(g-1,g6) = 28.575
    c: Horizontal(g1,g2)
    c: Horizontal(g2,g5)
    c: Horizontal(g0,g3)
    c: Horizontal(g3,g4)
    c: Vertical(g1,g0)
    c: Vertical(g0,g11)
    c: Vertical(g2,g3)
    c: Vertical(g3,g9)
    c: Vertical(g5,g4)
    c: Vertical(g4,g7)
    c: Equal(g11,g10)
    c: Equal(g10,g9)
    c: Equal(g9,g8)
    c: Equal(g8,g7)
    c: Equal(g7,g6)
    c: Equal(g1,g2)
    c: Equal(g2,g5)
    c: Equal(g0,g3)
    c: Equal(g3,g4)
    c: Equal(g5,g4)
    c: Equal(g4,g7)
    c: DistanceY(g-1,g6) = 9.525
    c: DistanceY(g6,g4) = 19.05
    c: DistanceY(g4,g5) = 38.1
    c: Diameter(g6) = 3.5
    c: Horizontal(g12,g13)
    c: Horizontal(g13,g14)
    c: Horizontal(g14,g15)
    c: Horizontal(g15,g16)
    c: Equal(g12,g13)
    c: Equal(g13,g14)
    c: Equal(g14,g15)
    c: Equal(g15,g16)
    c: DistanceX(g12,g13) = 19.05
    c: DistanceX(g13,g14) = 19.05
    c: DistanceX(g14,g15) = 19.05
    c: DistanceX(g15,g16) = 19.05
    c: Equal(g12,g5)
    c: DistanceY(g5,g12) = 21.55
    c: Equal(g18,g17)
    c: Symmetric(g18,g17,g19)
    c: Horizontal(g18,g17)
    c: DistanceX(g18,g19) = 7.62
    c: DistanceX(g-1,g19) = 19.05
    c: Horizontal(g19,g12)
    c: Equal(g17,g12)
    c: DistanceX(g19,g12) = 28.575
FEATURE [Sketcher::SketchObject] Sketch074  label="TL-CutToMidPCB"
  ArcFitTolerance = 1e-06
  AttachmentSupport = -> [XY_Plane]
  FullyConstrained = true
  MakeInternals = false
  MapMode = 5
  sketch-geometry (5):
    g0: LineSegment StartX=-200 StartY=-150 StartZ=0 EndX=200 EndY=-150 EndZ=0
    g1: LineSegment StartX=200 StartY=-150 StartZ=0 EndX=200 EndY=150 EndZ=0
    g2: LineSegment StartX=200 StartY=150 StartZ=0 EndX=-200 EndY=150 EndZ=0
    g3: LineSegment StartX=-200 StartY=150 StartZ=0 EndX=-200 EndY=-150 EndZ=0
    g4: GeomPoint [constr] X=-2e-16 Y=1.7e-15 Z=0
  constraints (12):
    c: Coincident(g0,g1)
    c: Coincident(g1,g2)
    c: Coincident(g2,g3)
    c: Coincident(g3,g0)
    c: Horizontal(g0)
    c: Horizontal(g2)
    c: Vertical(g1)
    c: Vertical(g3)
    c: Symmetric(g2,g0,g4)
    c: Distance(g1,g3) = 400
    c: Distance(g0,g2) = 300
    c: Coincident(g4,g-1)
FEATURE [PartDesign::Pocket] Pocket047  label="TL-CutToMidPCB-Pocket"
  BaseFeature = -> Pocket001
  Direction = (0,0,-1)
  Length = 0.75
  Length2 = 5
  Profile = -> Sketch074
  ReferenceAxis = -> Sketch074 [N_Axis]
  Refine = true
  Reversed = true
  Suppressed = false
  Type = 0
  expr: Length = VarSet.Top_PcbZ / 2
FEATURE [PartDesign::Body] Body  label="TopLeft"
  AllowCompound = false
  Group = -> [Pad,Fillet002,Sketch062,Sketch,Sketch001,Pocket035,Pocket036,Pad020,Sketch061,Pocket039,Sketch002,Sketch003,Pocket,Pad014,Pocket001,Sketch004,Sketch039,Sketch074,Pocket047]
  Origin = -> Origin
  Tip = -> Pocket047
FEATURE [Sketcher::SketchObject] Sketch075  label="TR-CutToMidPCB"
  ArcFitTolerance = 1e-06
  AttachmentSupport = -> [XY_Plane002]
  FullyConstrained = true
  MakeInternals = false
  MapMode = 5
  sketch-geometry (5):
    g0: LineSegment StartX=-200 StartY=-150 StartZ=0 EndX=200 EndY=-150 EndZ=0
    g1: LineSegment StartX=200 StartY=-150 StartZ=0 EndX=200 EndY=150 EndZ=0
    g2: LineSegment StartX=200 StartY=150 StartZ=0 EndX=-200 EndY=150 EndZ=0
    g3: LineSegment StartX=-200 StartY=150 StartZ=0 EndX=-200 EndY=-150 EndZ=0
    g4: GeomPoint [constr] X=0 Y=0 Z=0
  constraints (12):
    c: Coincident(g0,g1)
    c: Coincident(g1,g2)
    c: Coincident(g2,g3)
    c: Coincident(g3,g0)
    c: Horizontal(g0)
    c: Horizontal(g2)
    c: Vertical(g1)
    c: Vertical(g3)
    c: Symmetric(g2,g0,g4)
    c: Distance(g1,g3) = 400
    c: Distance(g0,g2) = 300
    c: Coincident(g4,g-1)
FEATURE [PartDesign::Pocket] Pocket048  label="TR-CutToMidPCB-Pocket"
  BaseFeature = -> Pocket003
  Direction = (0,0,-1)
  Length = 0.75
  Length2 = 5
  Profile = -> Sketch075
  ReferenceAxis = -> Sketch075 [N_Axis]
  Refine = true
  Reversed = true
  Suppressed = false
  Type = 0
  expr: Length = VarSet.Top_PcbZ / 2
FEATURE [PartDesign::Body] Body002  label="TopRight"
  AllowCompound = false
  Group = -> [Pad019,Fillet,Pocket037,Pocket038,Pad021,Pocket040,Sketch007,Sketch013,Sketch014,Sketch015,Pocket002,Pad015,Pocket003,Sketch016,Sketch040,Sketch063,Sketch064,Sketch075,Pocket048]
  Origin = -> Origin002
  Tip = -> Pocket048
FEATURE [Sketcher::SketchObject] Sketch084  label="CR-ResetBtn"
  ArcFitTolerance = 1e-06
  AttachmentSupport = -> [XY_Plane005]
  FullyConstrained = true
  MakeInternals = false
  MapMode = 5
  expr: Constraints[11] = VarSet.Top_MedXY / 2 + VarSet.Top_Frame
  expr: Constraints[14] = VarSet.Cover_ResetHoleWidth / 2
  expr: Constraints[8] = 2.5 * 19.05 mm
  expr: Constraints[9] = VarSet.Cover_ResetHoleDepth
  sketch-geometry (6):
    g0: LineSegment StartX=7.15 StartY=49.225 StartZ=0 EndX=7.15 EndY=44.625 EndZ=0
    g1: LineSegment StartX=7.15 StartY=44.625 StartZ=0 EndX=8.65 EndY=44.625 EndZ=0
    g2: LineSegment StartX=8.65 StartY=44.625 StartZ=0 EndX=8.65 EndY=49.225 EndZ=0
    g3: LineSegment StartX=8.65 StartY=49.225 StartZ=0 EndX=7.15 EndY=49.225 EndZ=0
    g4: GeomPoint X=19.05 Y=47.625 Z=0
    g5: GeomPoint X=19.05 Y=47.225 Z=0
  constraints (16):
    c: Coincident(g0,g1)
    c: Coincident(g1,g2)
    c: Coincident(g2,g3)
    c: Coincident(g3,g0)
    c: Vertical(g0)
    c: Vertical(g2)
    c: Horizontal(g1)
    c: Horizontal(g3)
    c: DistanceY(g-1,g4) = 47.625
    c: DistanceX(g1,g1) = 1.5
    c: DistanceX(g-1,g4) = 19.05
    c: DistanceX(g0,g4) = 11.9
    c: Vertical(g5,g4)
    c: DistanceY(g5,g4) = 0.4
    c: DistanceY(g5,g2) = 2
    c: DistanceY(g1,g4) = 3
FEATURE [Sketcher::SketchObject] Sketch087  label="CR-MCULED"
  ArcFitTolerance = 1e-06
  AttachmentSupport = -> [XY_Plane005]
  FullyConstrained = true
  MakeInternals = false
  MapMode = 5
  expr: Constraints[25] = VarSet.Cover_McuRearAdd
  expr: Constraints[26] = 4 * 19.05 mm
  expr: Constraints[27] = 2.5 * 19.05 mm + VarSet.Top_PcbY / 2
  sketch-geometry (12):
    g0: GeomPoint X=38.1 Y=76.2 Z=0
    g1: LineSegment StartX=12.8 StartY=82.335 StartZ=0 EndX=10 EndY=82.335 EndZ=0
    g2: LineSegment StartX=10 StartY=82.335 StartZ=0 EndX=10 EndY=85.875 EndZ=0
    g3: LineSegment StartX=10 StartY=85.875 StartZ=0 EndX=12.8 EndY=85.875 EndZ=0
    g4: LineSegment StartX=12.8 StartY=85.875 StartZ=0 EndX=12.8 EndY=82.335 EndZ=0
    g5: GeomPoint [constr] X=11.4 Y=84.105 Z=0
    g6: LineSegment StartX=25.6 StartY=85.875 StartZ=0 EndX=28.1 EndY=85.875 EndZ=0
    g7: LineSegment StartX=28.1 StartY=85.875 StartZ=0 EndX=28.1 EndY=82.335 EndZ=0
    g8: LineSegment StartX=28.1 StartY=82.335 StartZ=0 EndX=25.6 EndY=82.335 EndZ=0
    g9: LineSegment StartX=25.6 StartY=82.335 StartZ=0 EndX=25.6 EndY=85.875 EndZ=0
    g10: GeomPoint [constr] X=26.85 Y=84.105 Z=0
    g11: GeomPoint X=38.1 Y=85.375 Z=0
  constraints (30):
    c: Coincident(g1,g2)
    c: Coincident(g2,g3)
    c: Coincident(g3,g4)
    c: Coincident(g4,g1)
    c: Horizontal(g1)
    c: Horizontal(g3)
    c: Vertical(g2)
    c: Vertical(g4)
    c: Symmetric(g3,g1,g5)
    c: Coincident(g6,g7)
    c: Coincident(g7,g8)
    c: Coincident(g8,g9)
    c: Coincident(g9,g6)
    c: Horizontal(g6)
    c: Horizontal(g8)
    c: Vertical(g7)
    c: Vertical(g9)
    c: Symmetric(g8,g6,g10)
    c: DistanceX(g-1,g0) = 38.1
    c: DistanceX(g-1,g1) = 10
    c: DistanceX(g7,g0) = 10
    c: Horizontal(g5,g10)
    c: DistanceX(g1,g1) = 2.8
    c: DistanceY(g4,g4) = 3.54
    c: DistanceX(g8,g8) = 2.5
    c: DistanceY(g11,g6) = 0.5
    c: DistanceY(g-1,g0) = 76.2
    c: DistanceY(g-1,g11) = 85.375
    c: Vertical(g11,g0)
    c: Horizontal(g1,g8)
FEATURE [Sketcher::SketchObject] Sketch088  label="BL- TestSlice"
  ArcFitTolerance = 1e-06
  AttachmentOffset = pos=(0,0,-3) rot=(0,0,1;0rad)
  AttachmentSupport = -> [XY_Plane001]
  FullyConstrained = true
  MakeInternals = false
  MapMode = 5
  Placement = pos=(0,0,-3) rot=(0,0,1;0rad)
  sketch-geometry (5):
    g0: LineSegment StartX=150 StartY=-100 StartZ=0 EndX=150 EndY=100 EndZ=0
    g1: LineSegment StartX=150 StartY=100 StartZ=0 EndX=-150 EndY=100 EndZ=0
    g2: LineSegment StartX=-150 StartY=100 StartZ=0 EndX=-150 EndY=-100 EndZ=0
    g3: LineSegment StartX=-150 StartY=-100 StartZ=0 EndX=150 EndY=-100 EndZ=0
    g4: GeomPoint [constr] X=0 Y=1e-16 Z=0
  constraints (12):
    c: Coincident(g0,g1)
    c: Coincident(g1,g2)
    c: Coincident(g2,g3)
    c: Coincident(g3,g0)
    c: Vertical(g0)
    c: Vertical(g2)
    c: Horizontal(g1)
    c: Horizontal(g3)
    c: Symmetric(g2,g0,g4)
    c: Coincident(g4,g-1)
    c: DistanceX(g1,g1) = 300
    c: DistanceY(g2,g2) = 200
FEATURE [Sketcher::SketchObject] Sketch089  label="BR-TestSlice"
  ArcFitTolerance = 1e-06
  AttachmentOffset = pos=(0,0,-3) rot=(0,0,1;0rad)
  AttachmentSupport = -> [XY_Plane003]
  FullyConstrained = true
  MakeInternals = false
  MapMode = 5
  Placement = pos=(0,0,-3) rot=(0,0,1;0rad)
  sketch-geometry (5):
    g0: LineSegment StartX=150 StartY=-100 StartZ=0 EndX=150 EndY=100 EndZ=0
    g1: LineSegment StartX=150 StartY=100 StartZ=0 EndX=-150 EndY=100 EndZ=0
    g2: LineSegment StartX=-150 StartY=100 StartZ=0 EndX=-150 EndY=-100 EndZ=0
    g3: LineSegment StartX=-150 StartY=-100 StartZ=0 EndX=150 EndY=-100 EndZ=0
    g4: GeomPoint [constr] X=0 Y=0 Z=0
  constraints (12):
    c: Coincident(g0,g1)
    c: Coincident(g1,g2)
    c: Coincident(g2,g3)
    c: Coincident(g3,g0)
    c: Vertical(g0)
    c: Vertical(g2)
    c: Horizontal(g1)
    c: Horizontal(g3)
    c: Symmetric(g2,g0,g4)
    c: Coincident(g4,g-1)
    c: DistanceX(g1,g1) = 300
    c: DistanceY(g2,g2) = 200
FEATURE [Sketcher::SketchObject] Sketch091  label="CR-Slant"
  ArcFitTolerance = 1e-06
  AttachmentSupport = -> [YZ_Plane005]
  FullyConstrained = true
  MakeInternals = false
  MapMode = 5
  Placement = pos=(0,0,0) rot=(0.57735,0.57735,0.57735;2.0944rad)
  expr: Constraints[10] = VarSet.Top_PcbZ / 2 + VarSet.Cover_OutZ - VarSet.Cover_SlantZ
  expr: Constraints[11] = VarSet.Top_PcbZ / 2
  expr: Constraints[4] = 2.5 * 19.05 mm
  expr: Constraints[5] = 4 * 19.05 mm + VarSet.Top_MedXY / 2 + VarSet.Top_Frame + VarSet.Top_RearAdd
  sketch-geometry (4):
    g0: LineSegment StartX=47.625 StartY=0 StartZ=0 EndX=47.625 EndY=0.75 EndZ=0
    g1: LineSegment StartX=91.1 StartY=0.75 StartZ=0 EndX=91.1 EndY=0 EndZ=0
    g2: LineSegment StartX=47.625 StartY=0.75 StartZ=0 EndX=91.1 EndY=0.75 EndZ=0
    g3: LineSegment StartX=91.1 StartY=0 StartZ=0 EndX=47.625 EndY=0 EndZ=0
  constraints (12):
    c: PointOnObject(g0,g-1)
    c: Vertical(g0)
    c: PointOnObject(g1,g-1)
    c: Vertical(g1)
    c: DistanceX(g-1,g0) = 47.625
    c: DistanceX(g-1,g1) = 91.1
    c: Coincident(g2,g0)
    c: Coincident(g2,g1)
    c: Coincident(g3,g1)
    c: Coincident(g3,g0)
    c: DistanceY(g0,g0) = 0.75
    c: DistanceY(g1,g1) = 0.75
FEATURE [Sketcher::SketchObject] Sketch048  label="CL-Out"
  ArcFitTolerance = 1e-06
  AttachmentSupport = -> [XY_Plane004]
  FullyConstrained = true
  MakeInternals = false
  MapMode = 5
  expr: Constraints[10] = 19.05 mm / 2
  expr: Constraints[11] = VarSet.Top_MedXY / 2 + VarSet.Top_Frame
  expr: Constraints[19] = VarSet.Top_FrameFilletR
  expr: Constraints[20] = 3 * 19.05 mm
  expr: Constraints[21] = 1.5 * 19.05 mm
  expr: Constraints[23] = VarSet.Cover_FrontAdd
  expr: Constraints[9] = VarSet.Top_MedXY / 2 + VarSet.Top_Frame + VarSet.Top_RearAdd
  sketch-geometry (10):
    g0: GeomPoint [constr] X=-19.05 Y=19.05 Z=0
    g1: LineSegment StartX=-28.575 StartY=91.1 StartZ=0 EndX=-28.575 EndY=46.425 EndZ=0
    g2: LineSegment StartX=-28.575 StartY=46.425 StartZ=0 EndX=-7.15 EndY=46.425 EndZ=0
    g3: LineSegment StartX=-7.15 StartY=46.425 StartZ=0 EndX=-7.15 EndY=89.1 EndZ=0
    g4: LineSegment StartX=-9.15 StartY=91.1 StartZ=0 EndX=-28.575 EndY=91.1 EndZ=0
    g5: GeomPoint X=-38.1 Y=76.2 Z=0
    g6: GeomPoint X=-38.1 Y=19.05 Z=0
    g7: ArcOfCircle CenterX=-9.15 CenterY=89.1 CenterZ=0 NormalX=0 NormalY=0 NormalZ=1 AngleXU=0 Radius=2 StartAngle=1e-16 EndAngle=1.5708
    g8: GeomPoint [constr] X=-7.15 Y=91.1 Z=0
    g9: GeomPoint X=-19.05 Y=47.625 Z=0
  constraints (24):
    c: DistanceX(g0,g-1) = 19.05
    c: DistanceY(g-1,g0) = 19.05
    c: Coincident(g1,g2)
    c: Coincident(g2,g3)
    c: Coincident(g4,g1)
    c: Vertical(g1)
    c: Vertical(g3)
    c: Horizontal(g2)
    c: Horizontal(g4)
    c: DistanceY(g5,g1) = 14.9
    c: DistanceX(g5,g1) = 9.525
    c: DistanceX(g0,g2) = 11.9
    c: DistanceX(g6,g0) = 19.05
    c: Vertical(g6,g5)
    c: Horizontal(g6,g0)
    c: PointOnObject(g8,g3)
    c: PointOnObject(g8,g4)
    c: Tangent(g3,g7) = -1.5708
    c: Tangent(g4,g7) = -1.5708
    c: Radius(g7) = 2
    c: DistanceY(g6,g5) = 57.15
    c: DistanceY(g0,g9) = 28.575
    c: Vertical(g9,g0)
    c: DistanceY(g2,g9) = 1.2
FEATURE [PartDesign::Pad] Pad016  label="CL-Out-Pad"
  Direction = (0,0,1)
  Length = 7.5
  Length2 = 10
  Profile = -> Sketch048
  ReferenceAxis = -> Sketch048 [N_Axis]
  Refine = true
  Suppressed = false
  Type = 0
  expr: Length = VarSet.Top_PcbZ / 2 + VarSet.Cover_OutZ
FEATURE [Sketcher::SketchObject] Sketch047  label="CL-PCB"
  ArcFitTolerance = 1e-06
  AttachmentSupport = -> [XY_Plane004]
  FullyConstrained = true
  MakeInternals = false
  MapMode = 5
  expr: Constraints[10] = 2.5 * 19.05 mm + VarSet.Top_PcbY / 2
  expr: Constraints[11] = 4 * 19.05 mm - VarSet.Top_PcbX / 2
  sketch-geometry (4):
    g0: LineSegment StartX=-9.9 StartY=35.375 StartZ=0 EndX=-59.9 EndY=35.375 EndZ=0
    g1: LineSegment StartX=-59.9 StartY=35.375 StartZ=0 EndX=-59.9 EndY=85.375 EndZ=0
    g2: LineSegment StartX=-59.9 StartY=85.375 StartZ=0 EndX=-9.9 EndY=85.375 EndZ=0
    g3: LineSegment StartX=-9.9 StartY=85.375 StartZ=0 EndX=-9.9 EndY=35.375 EndZ=0
  constraints (12):
    c: Coincident(g0,g1)
    c: Coincident(g1,g2)
    c: Coincident(g2,g3)
    c: Coincident(g3,g0)
    c: Horizontal(g0)
    c: Horizontal(g2)
    c: Vertical(g1)
    c: Vertical(g3)
    c: DistanceX(g0,g0) = 50
    c: DistanceY(g1,g1) = 50
    c: DistanceY(g-1,g2) = 85.375
    c: DistanceX(g2,g-1) = 9.9
FEATURE [Sketcher::SketchObject] Sketch052  label="CL-In"
  ArcFitTolerance = 1e-06
  AttachmentSupport = -> [XY_Plane004]
  FullyConstrained = true
  MakeInternals = false
  MapMode = 5
  expr: Constraints[12] = 3 * 19.05
  expr: Constraints[13] = 2.5 * 19.05 mm + VarSet.Top_PcbY / 2
  expr: Constraints[16] = VarSet.Cover_McuRearAdd
  expr: Constraints[19] = 1.5 * 19.05 mm
  expr: Constraints[20] = VarSet.Cover_FrontAdd
  sketch-geometry (13):
    g0: LineSegment StartX=-28.1 StartY=51.625 StartZ=0 EndX=-28.1 EndY=85.875 EndZ=0
    g1: LineSegment StartX=-10 StartY=85.875 StartZ=0 EndX=-10 EndY=46.425 EndZ=0
    g2: GeomPoint [constr] X=-19.05 Y=19.05 Z=0
    g3: GeomPoint [constr] X=-38.1 Y=19.05 Z=0
    g4: GeomPoint [constr] X=-38.1 Y=76.2 Z=0
    g5: LineSegment StartX=-28.1 StartY=51.625 StartZ=0 EndX=-25.6 EndY=51.625 EndZ=0
    g6: LineSegment StartX=-28.1 StartY=85.875 StartZ=0 EndX=-10 EndY=85.875 EndZ=0
    g7: GeomPoint X=-38.1 Y=85.375 Z=0
    g8: GeomPoint X=-19.05 Y=47.625 Z=0
    g9: LineSegment StartX=-25.6 StartY=46.425 StartZ=0 EndX=-10 EndY=46.425 EndZ=0
    g10: ArcOfCircle CenterX=-25.6 CenterY=48.425 CenterZ=0 NormalX=0 NormalY=0 NormalZ=1 AngleXU=0 Radius=2 StartAngle=4.71239 EndAngle=6.28319
    g11: ArcOfCircle CenterX=-25.6 CenterY=49.625 CenterZ=0 NormalX=0 NormalY=0 NormalZ=1 AngleXU=0 Radius=2 StartAngle=0 EndAngle=1.5708
    g12: LineSegment StartX=-23.6 StartY=49.625 StartZ=0 EndX=-23.6 EndY=48.425 EndZ=0
  constraints (33):
    c: Vertical(g0)
    c: Vertical(g1)
    c: Horizontal(g5)
    c: Coincident(g5,g0)
    c: Horizontal(g6)
    c: Coincident(g0,g6)
    c: DistanceX(g2,g-1) = 19.05
    c: DistanceX(g3,g2) = 19.05
    c: DistanceY(g-1,g2) = 19.05
    c: Horizontal(g3,g2)
    c: Vertical(g3,g4)
    c: Vertical(g4,g7)
    c: DistanceY(g3,g4) = 57.15
    c: DistanceY(g-1,g7) = 85.375
    c: DistanceX(g4,g0) = 10
    c: DistanceX(g1,g-1) = 10
    c: DistanceY(g7,g0) = 0.5
    c: DistanceX(g5,g5) = 2.5
    c: Coincident(g6,g1)
    c: DistanceY(g2,g8) = 28.575
    c: DistanceY(g1,g8) = 1.2
    c: Vertical(g8,g2)
    c: Coincident(g9,g1)
    c: Horizontal(g9)
    c: Radius(g11) = 2
    c: Vertical(g12)
    c: Tangent(g11,g5) = 1.5708
    c: Tangent(g11,g12) = 1.5708
    c: Tangent(g12,g10) = 1.5708
    c: Coincident(g10,g9)
    c: Vertical(g5,g9)
    c: DistanceY(g8,g11) = 2
    c: Equal(g10,g11)
FEATURE [PartDesign::Pocket] Pocket029  label="CL-In-Pocket"
  BaseFeature = -> Pad016
  Direction = (0,0,-1)
  Length = 5.5
  Length2 = 5
  Profile = -> Sketch052
  ReferenceAxis = -> Sketch052 [N_Axis]
  Refine = true
  Reversed = true
  Suppressed = false
  Type = 0
  expr: Length = VarSet.Top_PcbZ / 2 + VarSet.Cover_InZ
FEATURE [Sketcher::SketchObject] Sketch059  label="CL-MCU"
  ArcFitTolerance = 1e-06
  AttachmentSupport = -> [XY_Plane004]
  FullyConstrained = true
  MakeInternals = false
  MapMode = 5
  expr: Constraints[32] = 1.5 * 19.05 mm
  expr: Constraints[43] = VarSet.Top_MedXY / 2 + VarSet.Top_Frame - VarSet.Cover_ResetHoleDepth
  sketch-geometry (139):
    g0: GeomPoint X=-19.05 Y=81.365 Z=0
    g1: LineSegment StartX=-24.05 StartY=78.365 StartZ=0 EndX=-14.05 EndY=78.365 EndZ=0
    g2: LineSegment StartX=-14.05 StartY=78.365 StartZ=0 EndX=-14.05 EndY=86.365 EndZ=0
    g3: LineSegment StartX=-14.05 StartY=86.365 StartZ=0 EndX=-24.05 EndY=86.365 EndZ=0
    g4: LineSegment StartX=-24.05 StartY=86.365 StartZ=0 EndX=-24.05 EndY=78.365 EndZ=0
    g5: GeomPoint [constr] X=-19.05 Y=82.365 Z=0
    g6: LineSegment StartX=-13.03 StartY=69.265 StartZ=0 EndX=-13.03 EndY=74.765 EndZ=0
    g7: LineSegment StartX=-13.03 StartY=74.765 StartZ=0 EndX=-18.53 EndY=74.765 EndZ=0
    g8: LineSegment StartX=-18.53 StartY=74.765 StartZ=0 EndX=-18.53 EndY=69.265 EndZ=0
    g9: LineSegment StartX=-18.53 StartY=69.265 StartZ=0 EndX=-13.03 EndY=69.265 EndZ=0
    g10: GeomPoint [constr] X=-15.78 Y=72.015 Z=0
    g11: GeomPoint X=-19.05 Y=19.05 Z=0
    g12: GeomPoint X=-38.1 Y=19.05 Z=0
    g13: GeomPoint X=-19.05 Y=47.625 Z=0
    g14: LineSegment StartX=-15.55 StartY=51.725 StartZ=0 EndX=-15.55 EndY=42.725 EndZ=0
    g15: LineSegment StartX=-15.55 StartY=42.725 StartZ=0 EndX=-8.65 EndY=42.725 EndZ=0
    g16: LineSegment StartX=-8.65 StartY=42.725 StartZ=0 EndX=-8.65 EndY=51.725 EndZ=0
    g17: LineSegment StartX=-8.65 StartY=51.725 StartZ=0 EndX=-15.55 EndY=51.725 EndZ=0
    g18: GeomPoint [constr] X=-12.1 Y=47.225 Z=0
    g19: LineSegment StartX=-10 StartY=79.825 StartZ=0 EndX=-10 EndY=77.825 EndZ=0
    g20: LineSegment StartX=-10 StartY=77.825 StartZ=0 EndX=-12.5 EndY=77.825 EndZ=0
    g21: LineSegment StartX=-12.5 StartY=77.825 StartZ=0 EndX=-12.5 EndY=79.825 EndZ=0
    g22: LineSegment StartX=-12.5 StartY=79.825 StartZ=0 EndX=-10 EndY=79.825 EndZ=0
    g23: GeomPoint [constr] X=-11.25 Y=78.825 Z=0
    g24: LineSegment StartX=-10 StartY=77.285 StartZ=0 EndX=-10 EndY=75.285 EndZ=0
    g25: LineSegment StartX=-10 StartY=75.285 StartZ=0 EndX=-12.5 EndY=75.285 EndZ=0
    g26: LineSegment StartX=-12.5 StartY=75.285 StartZ=0 EndX=-12.5 EndY=77.285 EndZ=0
    g27: LineSegment StartX=-12.5 StartY=77.285 StartZ=0 EndX=-10 EndY=77.285 EndZ=0
    g28: GeomPoint [constr] X=-11.25 Y=76.285 Z=0
    g29: LineSegment StartX=-10 StartY=74.745 StartZ=0 EndX=-10 EndY=72.745 EndZ=0
    g30: LineSegment StartX=-10 StartY=72.745 StartZ=0 EndX=-12.5 EndY=72.745 EndZ=0
    g31: LineSegment StartX=-12.5 StartY=72.745 StartZ=0 EndX=-12.5 EndY=74.745 EndZ=0
    g32: LineSegment StartX=-12.5 StartY=74.745 StartZ=0 EndX=-10 EndY=74.745 EndZ=0
    g33: GeomPoint [constr] X=-11.25 Y=73.745 Z=0
    g34: LineSegment StartX=-10 StartY=72.205 StartZ=0 EndX=-10 EndY=70.205 EndZ=0
    g35: LineSegment StartX=-10 StartY=70.205 StartZ=0 EndX=-12.5 EndY=70.205 EndZ=0
    g36: LineSegment StartX=-12.5 StartY=70.205 StartZ=0 EndX=-12.5 EndY=72.205 EndZ=0
    g37: LineSegment StartX=-12.5 StartY=72.205 StartZ=0 EndX=-10 EndY=72.205 EndZ=0
    g38: GeomPoint [constr] X=-11.25 Y=71.205 Z=0
    g39: LineSegment StartX=-10 StartY=69.665 StartZ=0 EndX=-10 EndY=67.665 EndZ=0
    g40: LineSegment StartX=-10 StartY=67.665 StartZ=0 EndX=-12.5 EndY=67.665 EndZ=0
    g41: LineSegment StartX=-12.5 StartY=67.665 StartZ=0 EndX=-12.5 EndY=69.665 EndZ=0
    g42: LineSegment StartX=-12.5 StartY=69.665 StartZ=0 EndX=-10 EndY=69.665 EndZ=0
    g43: GeomPoint [constr] X=-11.25 Y=68.665 Z=0
    g44: LineSegment StartX=-10 StartY=67.125 StartZ=0 EndX=-10 EndY=65.125 EndZ=0
    g45: LineSegment StartX=-10 StartY=65.125 StartZ=0 EndX=-12.5 EndY=65.125 EndZ=0
    g46: LineSegment StartX=-12.5 StartY=65.125 StartZ=0 EndX=-12.5 EndY=67.125 EndZ=0
    g47: LineSegment StartX=-12.5 StartY=67.125 StartZ=0 EndX=-10 EndY=67.125 EndZ=0
    g48: GeomPoint [constr] X=-11.25 Y=66.125 Z=0
    g49: LineSegment StartX=-10 StartY=64.585 StartZ=0 EndX=-10 EndY=62.585 EndZ=0
    g50: LineSegment StartX=-10 StartY=62.585 StartZ=0 EndX=-12.5 EndY=62.585 EndZ=0
    g51: LineSegment StartX=-12.5 StartY=62.585 StartZ=0 EndX=-12.5 EndY=64.585 EndZ=0
    g52: LineSegment StartX=-12.5 StartY=64.585 StartZ=0 EndX=-10 EndY=64.585 EndZ=0
    g53: GeomPoint [constr] X=-11.25 Y=63.585 Z=0
    g54: LineSegment StartX=-10 StartY=82.365 StartZ=0 EndX=-10 EndY=80.365 EndZ=0
    g55: LineSegment StartX=-10 StartY=80.365 StartZ=0 EndX=-12.5 EndY=80.365 EndZ=0
    g56: LineSegment StartX=-12.5 StartY=80.365 StartZ=0 EndX=-12.5 EndY=82.365 EndZ=0
    g57: LineSegment StartX=-12.5 StartY=82.365 StartZ=0 EndX=-10 EndY=82.365 EndZ=0
    g58: GeomPoint [constr] X=-11.25 Y=81.365 Z=0
    g59: LineSegment StartX=-10 StartY=62.045 StartZ=0 EndX=-10 EndY=60.045 EndZ=0
    g60: LineSegment StartX=-10 StartY=60.045 StartZ=0 EndX=-12.5 EndY=60.045 EndZ=0
    g61: LineSegment StartX=-12.5 StartY=60.045 StartZ=0 EndX=-12.5 EndY=62.045 EndZ=0
    g62: LineSegment StartX=-12.5 StartY=62.045 StartZ=0 EndX=-10 EndY=62.045 EndZ=0
    g63: GeomPoint [constr] X=-11.25 Y=61.045 Z=0
    g64: LineSegment StartX=-10 StartY=59.505 StartZ=0 EndX=-10 EndY=57.505 EndZ=0
    g65: LineSegment StartX=-10 StartY=57.505 StartZ=0 EndX=-12.5 EndY=57.505 EndZ=0
    g66: LineSegment StartX=-12.5 StartY=57.505 StartZ=0 EndX=-12.5 EndY=59.505 EndZ=0
    g67: LineSegment StartX=-12.5 StartY=59.505 StartZ=0 EndX=-10 EndY=59.505 EndZ=0
    g68: GeomPoint [constr] X=-11.25 Y=58.505 Z=0
    g69: LineSegment StartX=-10 StartY=56.965 StartZ=0 EndX=-10 EndY=54.965 EndZ=0
    g70: LineSegment StartX=-10 StartY=54.965 StartZ=0 EndX=-12.5 EndY=54.965 EndZ=0
    g71: LineSegment StartX=-12.5 StartY=54.965 StartZ=0 EndX=-12.5 EndY=56.965 EndZ=0
    g72: LineSegment StartX=-12.5 StartY=56.965 StartZ=0 EndX=-10 EndY=56.965 EndZ=0
    g73: GeomPoint [constr] X=-11.25 Y=55.965 Z=0
    g74: LineSegment StartX=-10 StartY=54.425 StartZ=0 EndX=-10 EndY=52.425 EndZ=0
    g75: LineSegment StartX=-10 StartY=52.425 StartZ=0 EndX=-12.5 EndY=52.425 EndZ=0
    g76: LineSegment StartX=-12.5 StartY=52.425 StartZ=0 EndX=-12.5 EndY=54.425 EndZ=0
    g77: LineSegment StartX=-12.5 StartY=54.425 StartZ=0 EndX=-10 EndY=54.425 EndZ=0
    g78: GeomPoint [constr] X=-11.25 Y=53.425 Z=0
    g79: LineSegment StartX=-25.6 StartY=79.825 StartZ=0 EndX=-25.6 EndY=77.825 EndZ=0
    g80: LineSegment StartX=-25.6 StartY=77.825 StartZ=0 EndX=-28.1 EndY=77.825 EndZ=0
    g81: LineSegment StartX=-28.1 StartY=77.825 StartZ=0 EndX=-28.1 EndY=79.825 EndZ=0
    g82: LineSegment StartX=-28.1 StartY=79.825 StartZ=0 EndX=-25.6 EndY=79.825 EndZ=0
    g83: GeomPoint [constr] X=-26.85 Y=78.825 Z=0
    g84: LineSegment StartX=-25.6 StartY=77.285 StartZ=0 EndX=-25.6 EndY=75.285 EndZ=0
    g85: LineSegment StartX=-25.6 StartY=75.285 StartZ=0 EndX=-28.1 EndY=75.285 EndZ=0
    g86: LineSegment StartX=-28.1 StartY=75.285 StartZ=0 EndX=-28.1 EndY=77.285 EndZ=0
    g87: LineSegment StartX=-28.1 StartY=77.285 StartZ=0 EndX=-25.6 EndY=77.285 EndZ=0
    g88: GeomPoint [constr] X=-26.85 Y=76.285 Z=0
    g89: LineSegment StartX=-25.6 StartY=74.745 StartZ=0 EndX=-25.6 EndY=72.745 EndZ=0
    g90: LineSegment StartX=-25.6 StartY=72.745 StartZ=0 EndX=-28.1 EndY=72.745 EndZ=0
    g91: LineSegment StartX=-28.1 StartY=72.745 StartZ=0 EndX=-28.1 EndY=74.745 EndZ=0
    g92: LineSegment StartX=-28.1 StartY=74.745 StartZ=0 EndX=-25.6 EndY=74.745 EndZ=0
    g93: GeomPoint [constr] X=-26.85 Y=73.745 Z=0
    g94: LineSegment StartX=-25.6 StartY=72.205 StartZ=0 EndX=-25.6 EndY=70.205 EndZ=0
    g95: LineSegment StartX=-25.6 StartY=70.205 StartZ=0 EndX=-28.1 EndY=70.205 EndZ=0
    g96: LineSegment StartX=-28.1 StartY=70.205 StartZ=0 EndX=-28.1 EndY=72.205 EndZ=0
    g97: LineSegment StartX=-28.1 StartY=72.205 StartZ=0 EndX=-25.6 EndY=72.205 EndZ=0
    g98: GeomPoint [constr] X=-26.85 Y=71.205 Z=0
    g99: LineSegment StartX=-25.6 StartY=69.665 StartZ=0 EndX=-25.6 EndY=67.665 EndZ=0
    g100: LineSegment StartX=-25.6 StartY=67.665 StartZ=0 EndX=-28.1 EndY=67.665 EndZ=0
    g101: LineSegment StartX=-28.1 StartY=67.665 StartZ=0 EndX=-28.1 EndY=69.665 EndZ=0
    g102: LineSegment StartX=-28.1 StartY=69.665 StartZ=0 EndX=-25.6 EndY=69.665 EndZ=0
    g103: GeomPoint [constr] X=-26.85 Y=68.665 Z=0
    g104: LineSegment StartX=-25.6 StartY=67.125 StartZ=0 EndX=-25.6 EndY=65.125 EndZ=0
    g105: LineSegment StartX=-25.6 StartY=65.125 StartZ=0 EndX=-28.1 EndY=65.125 EndZ=0
    g106: LineSegment StartX=-28.1 StartY=65.125 StartZ=0 EndX=-28.1 EndY=67.125 EndZ=0
    g107: LineSegment StartX=-28.1 StartY=67.125 StartZ=0 EndX=-25.6 EndY=67.125 EndZ=0
    g108: GeomPoint [constr] X=-26.85 Y=66.125 Z=0
    g109: LineSegment StartX=-25.6 StartY=64.585 StartZ=0 EndX=-25.6 EndY=62.585 EndZ=0
    g110: LineSegment StartX=-25.6 StartY=62.585 StartZ=0 EndX=-28.1 EndY=62.585 EndZ=0
    g111: LineSegment StartX=-28.1 StartY=62.585 StartZ=0 EndX=-28.1 EndY=64.585 EndZ=0
    g112: LineSegment StartX=-28.1 StartY=64.585 StartZ=0 EndX=-25.6 EndY=64.585 EndZ=0
    g113: GeomPoint [constr] X=-26.85 Y=63.585 Z=0
    g114: LineSegment StartX=-25.6 StartY=62.045 StartZ=0 EndX=-25.6 EndY=60.045 EndZ=0
    g115: LineSegment StartX=-25.6 StartY=60.045 StartZ=0 EndX=-28.1 EndY=60.045 EndZ=0
    g116: LineSegment StartX=-28.1 StartY=60.045 StartZ=0 EndX=-28.1 EndY=62.045 EndZ=0
    g117: LineSegment StartX=-28.1 StartY=62.045 StartZ=0 EndX=-25.6 EndY=62.045 EndZ=0
    g118: GeomPoint [constr] X=-26.85 Y=61.045 Z=0
    g119: LineSegment StartX=-25.6 StartY=59.505 StartZ=0 EndX=-25.6 EndY=57.505 EndZ=0
    g120: LineSegment StartX=-25.6 StartY=57.505 StartZ=0 EndX=-28.1 EndY=57.505 EndZ=0
    g121: LineSegment StartX=-28.1 StartY=57.505 StartZ=0 EndX=-28.1 EndY=59.505 EndZ=0
    g122: LineSegment StartX=-28.1 StartY=59.505 StartZ=0 EndX=-25.6 EndY=59.505 EndZ=0
    g123: GeomPoint [constr] X=-26.85 Y=58.505 Z=0
    g124: LineSegment StartX=-25.6 StartY=56.965 StartZ=0 EndX=-25.6 EndY=54.965 EndZ=0
    g125: LineSegment StartX=-25.6 StartY=54.965 StartZ=0 EndX=-28.1 EndY=54.965 EndZ=0
    g126: LineSegment StartX=-28.1 StartY=54.965 StartZ=0 EndX=-28.1 EndY=56.965 EndZ=0
    g127: LineSegment StartX=-28.1 StartY=56.965 StartZ=0 EndX=-25.6 EndY=56.965 EndZ=0
    g128: GeomPoint [constr] X=-26.85 Y=55.965 Z=0
    g129: LineSegment StartX=-25.6 StartY=54.425 StartZ=0 EndX=-25.6 EndY=52.425 EndZ=0
    g130: LineSegment StartX=-25.6 StartY=52.425 StartZ=0 EndX=-28.1 EndY=52.425 EndZ=0
    g131: LineSegment StartX=-28.1 StartY=52.425 StartZ=0 EndX=-28.1 EndY=54.425 EndZ=0
    g132: LineSegment StartX=-28.1 StartY=54.425 StartZ=0 EndX=-25.6 EndY=54.425 EndZ=0
    g133: GeomPoint [constr] X=-26.85 Y=53.425 Z=0
    g134: LineSegment StartX=-25.6 StartY=82.365 StartZ=0 EndX=-25.6 EndY=80.365 EndZ=0
    g135: LineSegment StartX=-25.6 StartY=80.365 StartZ=0 EndX=-28.1 EndY=80.365 EndZ=0
    g136: LineSegment StartX=-28.1 StartY=80.365 StartZ=0 EndX=-28.1 EndY=82.365 EndZ=0
    g137: LineSegment StartX=-28.1 StartY=82.365 StartZ=0 EndX=-25.6 EndY=82.365 EndZ=0
    g138: GeomPoint [constr] X=-26.85 Y=81.365 Z=0
  constraints (359):
    c: Coincident(g1,g2)
    c: Coincident(g2,g3)
    c: Coincident(g3,g4)
    c: Coincident(g4,g1)
    c: Horizontal(g1)
    c: Horizontal(g3)
    c: Vertical(g2)
    c: Vertical(g4)
    c: Symmetric(g3,g1,g5)
    c: Distance(g1,g3) = 8
    c: Vertical(g5,g0)
    c: DistanceY(g1,g0) = 3
    c: Coincident(g6,g7)
    c: Coincident(g7,g8)
    c: Coincident(g8,g9)
    c: Coincident(g9,g6)
    c: Vertical(g6)
    c: Vertical(g8)
    c: Horizontal(g7)
    c: Horizontal(g9)
    c: Symmetric(g8,g6,g10)
    c: DistanceY(g10,g0) = 9.35
    c: DistanceX(g3,g3) = 10
    c: DistanceX(g0,g10) = 3.27
    c: Equal(g9,g8)
    c: DistanceX(g9,g9) = 5.5
    c: Horizontal(g12,g11)
    c: DistanceX(g11,g-1) = 19.05
    c: Vertical(g0,g11)
    c: DistanceX(g12,g11) = 19.05
    c: DistanceY(g-1,g11) = 19.05
    c: Vertical(g13,g11)
    c: DistanceY(g11,g13) = 28.575
    c: Coincident(g14,g15)
    c: Coincident(g15,g16)
    c: Coincident(g16,g17)
    c: Coincident(g17,g14)
    c: Vertical(g14)
    c: Vertical(g16)
    c: Horizontal(g15)
    c: Horizontal(g17)
    c: Symmetric(g16,g14,g18)
    c: DistanceY(g18,g13) = 0.4
    c: DistanceX(g13,g15) = 10.4
    c: DistanceY(g16,g16) = 9
    c: DistanceX(g13,g14) = 3.5
    c: Coincident(g19,g20)
    c: Coincident(g20,g21)
    c: Coincident(g21,g22)
    c: Coincident(g22,g19)
    c: Vertical(g19)
    c: Vertical(g21)
    c: Horizontal(g20)
    c: Horizontal(g22)
    c: Symmetric(g21,g19,g23)
    c: Coincident(g24,g25)
    c: Coincident(g25,g26)
    c: Coincident(g26,g27)
    c: Coincident(g27,g24)
    c: Vertical(g24)
    c: Vertical(g26)
    c: Horizontal(g25)
    c: Horizontal(g27)
    c: Symmetric(g26,g24,g28)
    c: Coincident(g29,g30)
    c: Coincident(g30,g31)
    c: Coincident(g31,g32)
    c: Coincident(g32,g29)
    c: Vertical(g29)
    c: Vertical(g31)
    c: Horizontal(g30)
    c: Horizontal(g32)
    c: Symmetric(g31,g29,g33)
    c: Coincident(g34,g35)
    c: Coincident(g35,g36)
    c: Coincident(g36,g37)
    c: Coincident(g37,g34)
    c: Vertical(g34)
    c: Vertical(g36)
    c: Horizontal(g35)
    c: Horizontal(g37)
    c: Symmetric(g36,g34,g38)
    c: Coincident(g39,g40)
    c: Coincident(g40,g41)
    c: Coincident(g41,g42)
    c: Coincident(g42,g39)
    c: Vertical(g39)
    c: Vertical(g41)
    c: Horizontal(g40)
    c: Horizontal(g42)
    c: Symmetric(g41,g39,g43)
    c: Coincident(g44,g45)
    c: Coincident(g45,g46)
    c: Coincident(g46,g47)
    c: Coincident(g47,g44)
    c: Vertical(g44)
    c: Vertical(g46)
    c: Horizontal(g45)
    c: Horizontal(g47)
    c: Symmetric(g46,g44,g48)
    c: Coincident(g49,g50)
    c: Coincident(g50,g51)
    c: Coincident(g51,g52)
    c: Coincident(g52,g49)
    c: Vertical(g49)
    c: Vertical(g51)
    c: Horizontal(g50)
    c: Horizontal(g52)
    c: Symmetric(g51,g49,g53)
    c: Coincident(g54,g55)
    c: Coincident(g55,g56)
    c: Coincident(g56,g57)
    c: Coincident(g57,g54)
    c: Vertical(g54)
    c: Vertical(g56)
    c: Horizontal(g55)
    c: Horizontal(g57)
    c: Symmetric(g56,g54,g58)
    c: Coincident(g59,g60)
    c: Coincident(g60,g61)
    c: Coincident(g61,g62)
    c: Coincident(g62,g59)
    c: Vertical(g59)
    c: Vertical(g61)
    c: Horizontal(g60)
    c: Horizontal(g62)
    c: Symmetric(g61,g59,g63)
    c: Coincident(g64,g65)
    c: Coincident(g65,g66)
    c: Coincident(g66,g67)
    c: Coincident(g67,g64)
    c: Vertical(g64)
    c: Vertical(g66)
    c: Horizontal(g65)
    c: Horizontal(g67)
    c: Symmetric(g66,g64,g68)
    c: Coincident(g69,g70)
    c: Coincident(g70,g71)
    c: Coincident(g71,g72)
    c: Coincident(g72,g69)
    c: Vertical(g69)
    c: Vertical(g71)
    c: Horizontal(g70)
    c: Horizontal(g72)
    c: Symmetric(g71,g69,g73)
    c: Coincident(g74,g75)
    c: Coincident(g75,g76)
    c: Coincident(g76,g77)
    c: Coincident(g77,g74)
    c: Vertical(g74)
    c: Vertical(g76)
    c: Horizontal(g75)
    c: Horizontal(g77)
    c: Symmetric(g76,g74,g78)
    c: Vertical(g58,g23)
    c: Vertical(g23,g28)
    c: Vertical(g28,g33)
    c: Vertical(g33,g38)
    c: Vertical(g38,g43)
    c: Vertical(g43,g48)
    c: Vertical(g48,g53)
    c: Vertical(g53,g63)
    c: Vertical(g63,g68)
    c: Vertical(g68,g73)
    c: Vertical(g73,g78)
    c: DistanceY(g23,g58) = 2.54
    c: DistanceY(g28,g23) = 2.54
    c: DistanceY(g33,g28) = 2.54
    c: DistanceY(g38,g33) = 2.54
    c: DistanceY(g43,g38) = 2.54
    c: DistanceY(g48,g43) = 2.54
    c: DistanceY(g53,g48) = 2.54
    c: DistanceY(g63,g53) = 2.54
    c: DistanceY(g68,g63) = 2.54
    c: DistanceY(g73,g68) = 2.54
    c: DistanceY(g78,g73) = 2.54
    c: Equal(g54,g19)
    c: Equal(g19,g24)
    c: Equal(g24,g29)
    c: Equal(g29,g34)
    c: Equal(g34,g39)
    c: Equal(g39,g44)
    c: Equal(g44,g49)
    c: Equal(g49,g59)
    c: Equal(g59,g64)
    c: Equal(g64,g69)
    c: Equal(g69,g74)
    c: Equal(g55,g20)
    c: Equal(g20,g25)
    c: Equal(g25,g30)
    c: Equal(g30,g35)
    c: Equal(g35,g40)
    c: Equal(g40,g45)
    c: Equal(g45,g50)
    c: Equal(g50,g60)
    c: Equal(g60,g65)
    c: Equal(g65,g70)
    c: Equal(g70,g75)
    c: DistanceY(g13,g78) = 5.8
    c: Coincident(g79,g80)
    c: Coincident(g80,g81)
    c: Coincident(g81,g82)
    c: Coincident(g82,g79)
    c: Vertical(g79)
    c: Vertical(g81)
    c: Horizontal(g80)
    c: Horizontal(g82)
    c: Symmetric(g81,g79,g83)
    c: Coincident(g84,g85)
    c: Coincident(g85,g86)
    c: Coincident(g86,g87)
    c: Coincident(g87,g84)
    c: Vertical(g84)
    c: Vertical(g86)
    c: Horizontal(g85)
    c: Horizontal(g87)
    c: Symmetric(g86,g84,g88)
    c: Coincident(g89,g90)
    c: Coincident(g90,g91)
    c: Coincident(g91,g92)
    c: Coincident(g92,g89)
    c: Vertical(g89)
    c: Vertical(g91)
    c: Horizontal(g90)
    c: Horizontal(g92)
    c: Symmetric(g91,g89,g93)
    c: Coincident(g94,g95)
    c: Coincident(g95,g96)
    c: Coincident(g96,g97)
    c: Coincident(g97,g94)
    c: Vertical(g94)
    c: Vertical(g96)
    c: Horizontal(g95)
    c: Horizontal(g97)
    c: Symmetric(g96,g94,g98)
    c: Coincident(g99,g100)
    c: Coincident(g100,g101)
    c: Coincident(g101,g102)
    c: Coincident(g102,g99)
    c: Vertical(g99)
    c: Vertical(g101)
    c: Horizontal(g100)
    c: Horizontal(g102)
    c: Symmetric(g101,g99,g103)
    c: Coincident(g104,g105)
    c: Coincident(g105,g106)
    c: Coincident(g106,g107)
    c: Coincident(g107,g104)
    c: Vertical(g104)
    c: Vertical(g106)
    c: Horizontal(g105)
    c: Horizontal(g107)
    c: Symmetric(g106,g104,g108)
    c: Coincident(g109,g110)
    c: Coincident(g110,g111)
    c: Coincident(g111,g112)
    c: Coincident(g112,g109)
    c: Vertical(g109)
    c: Vertical(g111)
    c: Horizontal(g110)
    c: Horizontal(g112)
    c: Symmetric(g111,g109,g113)
    c: Coincident(g114,g115)
    c: Coincident(g115,g116)
    c: Coincident(g116,g117)
    c: Coincident(g117,g114)
    c: Vertical(g114)
    c: Vertical(g116)
    c: Horizontal(g115)
    c: Horizontal(g117)
    c: Symmetric(g116,g114,g118)
    c: Coincident(g119,g120)
    c: Coincident(g120,g121)
    c: Coincident(g121,g122)
    c: Coincident(g122,g119)
    c: Vertical(g119)
    c: Vertical(g121)
    c: Horizontal(g120)
    c: Horizontal(g122)
    c: Symmetric(g121,g119,g123)
    c: Coincident(g124,g125)
    c: Coincident(g125,g126)
    c: Coincident(g126,g127)
    c: Coincident(g127,g124)
    c: Vertical(g124)
    c: Vertical(g126)
    c: Horizontal(g125)
    c: Horizontal(g127)
    c: Symmetric(g126,g124,g128)
    c: Coincident(g129,g130)
    c: Coincident(g130,g131)
    c: Coincident(g131,g132)
    c: Coincident(g132,g129)
    c: Vertical(g129)
    c: Vertical(g131)
    c: Horizontal(g130)
    c: Horizontal(g132)
    c: Symmetric(g131,g129,g133)
    c: Vertical(g83,g88)
    c: Vertical(g88,g93)
    c: Vertical(g93,g98)
    c: Vertical(g98,g103)
    c: Vertical(g103,g108)
    c: Vertical(g108,g113)
    c: Vertical(g113,g118)
    c: Vertical(g118,g123)
    c: Vertical(g123,g128)
    c: Vertical(g128,g133)
    c: Equal(g79,g84)
    c: Equal(g84,g89)
    c: Equal(g89,g94)
    c: Equal(g94,g99)
    c: Equal(g99,g104)
    c: Equal(g104,g109)
    c: Equal(g109,g114)
    c: Equal(g114,g119)
    c: Equal(g119,g124)
    c: Equal(g124,g129)
    c: Equal(g80,g85)
    c: Equal(g85,g90)
    c: Equal(g90,g95)
    c: Equal(g95,g100)
    c: Equal(g100,g105)
    c: Equal(g105,g110)
    c: Equal(g110,g115)
    c: Equal(g115,g120)
    c: Equal(g120,g125)
    c: Equal(g125,g130)
    c: Horizontal(g23,g83)
    c: Horizontal(g28,g88)
    c: Horizontal(g33,g93)
    c: Horizontal(g38,g98)
    c: Horizontal(g43,g103)
    c: Horizontal(g48,g108)
    c: Horizontal(g53,g113)
    c: Horizontal(g63,g118)
    c: Horizontal(g68,g123)
    c: Horizontal(g73,g128)
    c: Horizontal(g78,g133)
    c: Coincident(g134,g135)
    c: Coincident(g135,g136)
    c: Coincident(g136,g137)
    c: Coincident(g137,g134)
    c: Vertical(g134)
    c: Vertical(g136)
    c: Horizontal(g135)
    c: Horizontal(g137)
    c: Symmetric(g136,g134,g138)
    c: Vertical(g138,g83)
    c: Horizontal(g138,g58)
    c: Equal(g135,g80)
    c: Equal(g79,g134)
    c: DistanceX(g12,g130) = 10
    c: DistanceX(g74,g-1) = 10
    c: Equal(g130,g75)
    c: Equal(g129,g74)
    c: Horizontal(g58,g0)
    c: DistanceX(g130,g130) = 2.5
    c: DistanceY(g131,g131) = 2
FEATURE [Sketcher::SketchObject] Sketch082  label="CL-ResetBtn"
  ArcFitTolerance = 1e-06
  AttachmentSupport = -> [XY_Plane004]
  FullyConstrained = true
  MakeInternals = false
  MapMode = 5
  expr: Constraints[10] = VarSet.Cover_ResetHoleDepth
  expr: Constraints[11] = VarSet.Top_MedXY / 2 + VarSet.Top_Frame
  expr: Constraints[13] = VarSet.Cover_ResetHoleWidth / 2
  expr: Constraints[9] = 2.5 * 19.05 mm
  sketch-geometry (6):
    g0: LineSegment StartX=-8.65 StartY=49.225 StartZ=0 EndX=-8.65 EndY=44.625 EndZ=0
    g1: LineSegment StartX=-8.65 StartY=44.625 StartZ=0 EndX=-7.15 EndY=44.625 EndZ=0
    g2: LineSegment StartX=-7.15 StartY=44.625 StartZ=0 EndX=-7.15 EndY=49.225 EndZ=0
    g3: LineSegment StartX=-7.15 StartY=49.225 StartZ=0 EndX=-8.65 EndY=49.225 EndZ=0
    g4: GeomPoint X=-19.05 Y=47.625 Z=0
    g5: GeomPoint X=-19.05 Y=47.225 Z=0
  constraints (16):
    c: Coincident(g0,g1)
    c: Coincident(g1,g2)
    c: Coincident(g2,g3)
    c: Coincident(g3,g0)
    c: Vertical(g0)
    c: Vertical(g2)
    c: Horizontal(g1)
    c: Horizontal(g3)
    c: DistanceX(g4,g-1) = 19.05
    c: DistanceY(g-1,g4) = 47.625
    c: DistanceX(g1,g1) = 1.5
    c: DistanceX(g4,g1) = 11.9
    c: DistanceY(g5,g4) = 0.4
    c: DistanceY(g5,g0) = 2
    c: Vertical(g5,g4)
    c: DistanceY(g0,g4) = 3
FEATURE [Sketcher::SketchObject] Sketch086  label="CL-MCULED"
  ArcFitTolerance = 1e-06
  AttachmentSupport = -> [XY_Plane004]
  FullyConstrained = true
  MakeInternals = false
  MapMode = 5
  expr: Constraints[23] = 2.5 * 19.05 mm + VarSet.Top_PcbY / 2
  expr: Constraints[24] = VarSet.Cover_McuRearAdd
  expr: Constraints[29] = 4 * 19.05 mm
  sketch-geometry (12):
    g0: GeomPoint X=-38.1 Y=76.2 Z=0
    g1: LineSegment StartX=-12.5 StartY=82.335 StartZ=0 EndX=-10 EndY=82.335 EndZ=0
    g2: LineSegment StartX=-10 StartY=82.335 StartZ=0 EndX=-10 EndY=85.875 EndZ=0
    g3: LineSegment StartX=-10 StartY=85.875 StartZ=0 EndX=-12.5 EndY=85.875 EndZ=0
    g4: LineSegment StartX=-12.5 StartY=85.875 StartZ=0 EndX=-12.5 EndY=82.335 EndZ=0
    g5: GeomPoint [constr] X=-11.25 Y=84.105 Z=0
    g6: LineSegment StartX=-25.3 StartY=85.875 StartZ=0 EndX=-28.1 EndY=85.875 EndZ=0
    g7: LineSegment StartX=-28.1 StartY=85.875 StartZ=0 EndX=-28.1 EndY=82.335 EndZ=0
    g8: LineSegment StartX=-28.1 StartY=82.335 StartZ=0 EndX=-25.3 EndY=82.335 EndZ=0
    g9: LineSegment StartX=-25.3 StartY=82.335 StartZ=0 EndX=-25.3 EndY=85.875 EndZ=0
    g10: GeomPoint [constr] X=-26.7 Y=84.105 Z=0
    g11: GeomPoint X=-38.1 Y=85.375 Z=0
  constraints (30):
    c: Coincident(g1,g2)
    c: Coincident(g2,g3)
    c: Coincident(g3,g4)
    c: Coincident(g4,g1)
    c: Horizontal(g1)
    c: Horizontal(g3)
    c: Vertical(g2)
    c: Vertical(g4)
    c: Symmetric(g3,g1,g5)
    c: Coincident(g6,g7)
    c: Coincident(g7,g8)
    c: Coincident(g8,g9)
    c: Coincident(g9,g6)
    c: Horizontal(g6)
    c: Horizontal(g8)
    c: Vertical(g7)
    c: Vertical(g9)
    c: Symmetric(g8,g6,g10)
    c: Horizontal(g6,g3)
    c: DistanceY(g9,g9) = 3.54
    c: DistanceX(g0,g6) = 10
    c: DistanceX(g2,g-1) = 10
    c: Vertical(g11,g0)
    c: DistanceY(g-1,g11) = 85.375
    c: DistanceY(g11,g6) = 0.5
    c: DistanceX(g0,g-1) = 38.1
    c: DistanceX(g1,g1) = 2.5
    c: DistanceX(g8,g8) = 2.8
    c: Horizontal(g8,g1)
    c: DistanceY(g0) = 76.2
FEATURE [Sketcher::SketchObject] Sketch090  label="CL-Slant"
  ArcFitTolerance = 1e-06
  AttachmentSupport = -> [YZ_Plane004]
  FullyConstrained = true
  MakeInternals = false
  MapMode = 5
  Placement = pos=(0,0,0) rot=(0.57735,0.57735,0.57735;2.0944rad)
  expr: Constraints[10] = VarSet.Top_PcbZ / 2 + VarSet.Cover_OutZ - VarSet.Cover_SlantZ
  expr: Constraints[11] = VarSet.Top_PcbZ / 2
  expr: Constraints[4] = 2.5 * 19.05 mm
  expr: Constraints[5] = 4 * 19.05 mm + VarSet.Top_MedXY / 2 + VarSet.Top_Frame + VarSet.Top_RearAdd
  sketch-geometry (4):
    g0: LineSegment StartX=47.625 StartY=0 StartZ=0 EndX=47.625 EndY=0.75 EndZ=0
    g1: LineSegment StartX=91.1 StartY=0.75 StartZ=0 EndX=91.1 EndY=0 EndZ=0
    g2: LineSegment StartX=47.625 StartY=0.75 StartZ=0 EndX=91.1 EndY=0.75 EndZ=0
    g3: LineSegment StartX=91.1 StartY=0 StartZ=0 EndX=47.625 EndY=0 EndZ=0
  constraints (12):
    c: PointOnObject(g0,g-1)
    c: Vertical(g0)
    c: PointOnObject(g1,g-1)
    c: Vertical(g1)
    c: DistanceX(g-1,g0) = 47.625
    c: DistanceX(g-1,g1) = 91.1
    c: Coincident(g2,g0)
    c: Coincident(g2,g1)
    c: Coincident(g3,g1)
    c: Coincident(g3,g0)
    c: DistanceY(g0,g0) = 0.75
    c: DistanceY(g1,g1) = 0.75
FEATURE [Sketcher::SketchObject] Sketch092  label="CL-Slant-PCB"
  ArcFitTolerance = 1e-06
  AttachmentOffset = pos=(0,0,-19.05) rot=(0,0,1;0rad)
  AttachmentSupport = -> [YZ_Plane004]
  FullyConstrained = true
  MakeInternals = false
  MapMode = 5
  Placement = pos=(-19.05,0,0) rot=(0.57735,0.57735,0.57735;2.0944rad)
  expr: Constraints[10] = VarSet.Top_PcbZ / 2 + VarSet.Cover_OutZ - VarSet.Cover_SlantZ
  expr: Constraints[11] = VarSet.Top_PcbZ / 2
  expr: Constraints[16] = VarSet.Top_PcbZ / 2
  expr: Constraints[20] = VarSet.Top_PcbZ / 2
  expr: Constraints[22] = VarSet.Top_PcbY / 2
  expr: Constraints[4] = 2.5 * 19.05 mm
  expr: Constraints[5] = 4 * 19.05 mm + VarSet.Top_MedXY / 2 + VarSet.Top_Frame + VarSet.Top_RearAdd
  sketch-geometry (8):
    g0: LineSegment [constr] StartX=47.625 StartY=0 StartZ=0 EndX=47.625 EndY=0.75 EndZ=0
    g1: LineSegment [constr] StartX=91.1 StartY=0.75 StartZ=0 EndX=91.1 EndY=0 EndZ=0
    g2: LineSegment [constr] StartX=47.625 StartY=0.75 StartZ=0 EndX=91.1 EndY=0.75 EndZ=0
    g3: LineSegment [constr] StartX=91.1 StartY=0 StartZ=0 EndX=47.625 EndY=0 EndZ=0
    g4: LineSegment StartX=85.375 StartY=1.5 StartZ=0 EndX=47.625 EndY=1.5 EndZ=0
    g5: LineSegment StartX=85.375 StartY=1.5 StartZ=0 EndX=85.375 EndY=0.75 EndZ=0
    g6: LineSegment StartX=47.625 StartY=1.5 StartZ=0 EndX=47.625 EndY=0.75 EndZ=0
    g7: LineSegment StartX=47.625 StartY=0.75 StartZ=0 EndX=85.375 EndY=0.75 EndZ=0
  constraints (23):
    c: PointOnObject(g0,g-1)
    c: Vertical(g0)
    c: PointOnObject(g1,g-1)
    c: Vertical(g1)
    c: DistanceX(g-1,g0) = 47.625
    c: DistanceX(g-1,g1) = 91.1
    c: Coincident(g2,g0)
    c: Coincident(g2,g1)
    c: Coincident(g3,g1)
    c: Coincident(g3,g0)
    c: DistanceY(g0,g0) = 0.75
    c: DistanceY(g1,g1) = 0.75
    c: PointOnObject(g5,g2)
    c: Coincident(g5,g4)
    c: Coincident(g6,g4)
    c: Coincident(g6,g0)
    c: DistanceY(g5,g5) = 0.75
    c: Vertical(g6)
    c: Vertical(g5)
    c: Coincident(g7,g0)
    c: DistanceY(g0,g4) = 0.75
    c: Coincident(g7,g5)
    c: DistanceX(g0,g5) = 37.75
FEATURE [Sketcher::SketchObject] Sketch093  label="CR-SlantPCB"
  ArcFitTolerance = 1e-06
  AttachmentOffset = pos=(0,0,19.05) rot=(0,0,1;0rad)
  AttachmentSupport = -> [YZ_Plane005]
  FullyConstrained = true
  MakeInternals = false
  MapMode = 5
  Placement = pos=(19.05,0,0) rot=(0.57735,0.57735,0.57735;2.0944rad)
  expr: Constraints[10] = VarSet.Top_PcbZ / 2 + VarSet.Cover_OutZ - VarSet.Cover_SlantZ
  expr: Constraints[11] = VarSet.Top_PcbZ / 2
  expr: Constraints[14] = VarSet.Top_PcbZ / 2
  expr: Constraints[18] = VarSet.Top_PcbY / 2
  expr: Constraints[20] = VarSet.Top_PcbZ / 2
  expr: Constraints[4] = 2.5 * 19.05 mm
  expr: Constraints[5] = 4 * 19.05 mm + VarSet.Top_MedXY / 2 + VarSet.Top_Frame + VarSet.Top_RearAdd
  sketch-geometry (8):
    g0: LineSegment [constr] StartX=47.625 StartY=0 StartZ=0 EndX=47.625 EndY=0.75 EndZ=0
    g1: LineSegment [constr] StartX=91.1 StartY=0.75 StartZ=0 EndX=91.1 EndY=0 EndZ=0
    g2: LineSegment [constr] StartX=47.625 StartY=0.75 StartZ=0 EndX=91.1 EndY=0.75 EndZ=0
    g3: LineSegment [constr] StartX=91.1 StartY=0 StartZ=0 EndX=47.625 EndY=0 EndZ=0
    g4: LineSegment StartX=85.375 StartY=1.5 StartZ=0 EndX=47.625 EndY=1.5 EndZ=0
    g5: LineSegment StartX=85.375 StartY=1.5 StartZ=0 EndX=85.375 EndY=0.75 EndZ=0
    g6: LineSegment StartX=47.625 StartY=1.5 StartZ=0 EndX=47.625 EndY=0.75 EndZ=0
    g7: LineSegment StartX=47.625 StartY=0.75 StartZ=0 EndX=85.375 EndY=0.75 EndZ=0
  constraints (23):
    c: PointOnObject(g0,g-1)
    c: Vertical(g0)
    c: PointOnObject(g1,g-1)
    c: Vertical(g1)
    c: DistanceX(g-1,g0) = 47.625
    c: DistanceX(g-1,g1) = 91.1
    c: Coincident(g2,g0)
    c: Coincident(g2,g1)
    c: Coincident(g3,g1)
    c: Coincident(g3,g0)
    c: DistanceY(g0,g0) = 0.75
    c: DistanceY(g1,g1) = 0.75
    c: Coincident(g5,g4)
    c: Coincident(g6,g4)
    c: DistanceY(g5,g5) = 0.75
    c: Vertical(g6)
    c: Vertical(g5)
    c: Coincident(g7,g5)
    c: DistanceX(g0,g5) = 37.75
    c: PointOnObject(g5,g2)
    c: DistanceY(g6,g4) = 0.75
    c: Coincident(g7,g6)
    c: Coincident(g0,g6)
FEATURE [Sketcher::SketchObject] Sketch094  label="ML-Plate"
  ArcFitTolerance = 1e-06
  AttachmentOffset = pos=(0,0,-3) rot=(0,0,1;0rad)
  AttachmentSupport = -> [XY_Plane008]
  FullyConstrained = true
  MakeInternals = false
  MapMode = 5
  Placement = pos=(0,0,-3) rot=(0,0,1;0rad)
  expr: Constraints[58] = VarSet.Top_MedXY / 2 + VarSet.Top_Frame + 2 * VarSet.Mold_WallD + VarSet.Mold_MoatD
  expr: Constraints[59] = VarSet.Top_MedXY / 2 + VarSet.Top_Frame + 2 * VarSet.Mold_WallD + VarSet.Mold_MoatD
  expr: Constraints[60] = VarSet.Top_MedXY / 2 + VarSet.Top_Frame + VarSet.Top_RearAdd + 2 * VarSet.Mold_WallD + VarSet.Mold_MoatD
  expr: Constraints[61] = VarSet.Top_MedXY / 2 + VarSet.Top_Frame + 2 * VarSet.Mold_WallD + VarSet.Mold_MoatD
  sketch-geometry (29):
    g0: GeomPoint [constr] X=-38.1 Y=19.05 Z=0
    g1: GeomPoint [constr] X=-57.15 Y=19.05 Z=0
    g2: GeomPoint [constr] X=-76.2 Y=19.05 Z=0
    g3: GeomPoint [constr] X=-95.25 Y=19.05 Z=0
    g4: GeomPoint [constr] X=-114.3 Y=19.05 Z=0
    g5: GeomPoint [constr] X=-38.1 Y=57.15 Z=0
    g6: GeomPoint [constr] X=-57.15 Y=57.15 Z=0
    g7: GeomPoint [constr] X=-76.2 Y=57.15 Z=0
    g8: GeomPoint [constr] X=-95.25 Y=57.15 Z=0
    g9: GeomPoint [constr] X=-114.3 Y=57.15 Z=0
    g10: GeomPoint [constr] X=-38.1 Y=38.1 Z=0
    g11: GeomPoint [constr] X=-57.15 Y=38.1 Z=0
    g12: GeomPoint [constr] X=-76.2 Y=38.1 Z=0
    g13: GeomPoint [constr] X=-95.25 Y=38.1 Z=0
    g14: GeomPoint [constr] X=-114.3 Y=38.1 Z=0
    g15: GeomPoint [constr] X=-95.25 Y=76.2 Z=0
    g16: GeomPoint [constr] X=-57.15 Y=76.2 Z=0
    g17: GeomPoint [constr] X=-133.35 Y=76.2 Z=0
    g18: GeomPoint [constr] X=-114.3 Y=76.2 Z=0
    g19: GeomPoint [constr] X=-76.2 Y=76.2 Z=0
    g20: LineSegment StartX=-157.25 StartY=103.1 StartZ=0 EndX=-157.25 EndY=-4.85 EndZ=0
    g21: LineSegment StartX=-157.25 StartY=103.1 StartZ=0 EndX=4.85 EndY=103.1 EndZ=0
    g22: LineSegment StartX=4.85 StartY=103.1 StartZ=0 EndX=4.85 EndY=-4.85 EndZ=0
    g23: LineSegment StartX=4.85 StartY=-4.85 StartZ=0 EndX=-157.25 EndY=-4.85 EndZ=0
    g24: GeomPoint [constr] X=-38.1 Y=76.2 Z=0
    g25: GeomPoint [constr] X=-133.35 Y=57.15 Z=0
    g26: GeomPoint [constr] X=-133.35 Y=38.1 Z=0
    g27: GeomPoint [constr] X=-133.35 Y=19.05 Z=0
    g28: GeomPoint [constr] X=-19.05 Y=19.05 Z=0
  constraints (62):
    c: DistanceX(g1,g0) = 19.05
    c: DistanceX(g2,g1) = 19.05
    c: DistanceX(g3,g2) = 19.05
    c: DistanceX(g4,g3) = 19.05
    c: DistanceY(g0,g10) = 19.05
    c: DistanceY(g10,g5) = 19.05
    c: Vertical(g20)
    c: Horizontal(g21)
    c: Vertical(g22)
    c: Horizontal(g23)
    c: DistanceY(g5,g24) = 19.05
    c: DistanceX(g27,g4) = 19.05
    c: DistanceX(g0,g28) = 19.05
    c: DistanceX(g28,g-1) = 19.05
    c: Horizontal(g17,g18)
    c: Horizontal(g18,g15)
    c: Horizontal(g15,g19)
    c: Horizontal(g19,g16)
    c: Horizontal(g16,g24)
    c: Horizontal(g25,g9)
    c: Horizontal(g9,g8)
    c: Horizontal(g8,g7)
    c: Horizontal(g7,g6)
    c: Horizontal(g6,g5)
    c: Horizontal(g26,g14)
    c: Horizontal(g14,g13)
    c: Horizontal(g13,g12)
    c: Horizontal(g12,g11)
    c: Horizontal(g11,g10)
    c: Vertical(g17,g25)
    c: Vertical(g25,g26)
    c: Vertical(g26,g27)
    c: Vertical(g18,g9)
    c: Vertical(g9,g14)
    c: Vertical(g14,g4)
    c: Vertical(g15,g8)
    c: Vertical(g8,g13)
    c: Vertical(g13,g3)
    c: Vertical(g19,g7)
    c: Vertical(g7,g12)
    c: Vertical(g12,g2)
    c: Vertical(g16,g6)
    c: Vertical(g6,g11)
    c: Vertical(g11,g1)
    c: Vertical(g24,g5)
    c: Vertical(g5,g10)
    c: Vertical(g10,g0)
    c: Horizontal(g27,g4)
    c: Horizontal(g4,g3)
    c: Horizontal(g3,g2)
    c: Horizontal(g2,g1)
    c: Horizontal(g1,g0)
    c: Horizontal(g0,g28)
    c: DistanceY(g-1,g28) = 19.05
    c: Coincident(g21,g20)
    c: Coincident(g21,g22)
    c: Coincident(g23,g22)
    c: Coincident(g23,g20)
    c: DistanceX(g20,g17) = 23.9
    c: DistanceX(g28,g22) = 23.9
    c: DistanceY(g17,g20) = 26.9
    c: DistanceY(g22,g28) = 23.9
FEATURE [PartDesign::Pad] Pad028  label="ML-Plate-Pad"
  Direction = (0,0,1)
  Length = 4.75
  Length2 = 10
  Profile = -> Sketch094
  ReferenceAxis = -> Sketch094 [N_Axis]
  Refine = true
  Suppressed = false
  Type = 0
  expr: Length = 3 mm + VarSet.Top_PcbZ / 2 + VarSet.Mold_WallD
FEATURE [Sketcher::SketchObject] Sketch095  label="ML-Moat"
  ArcFitTolerance = 1e-06
  AttachmentOffset = pos=(0,0,-3) rot=(0,0,1;0rad)
  AttachmentSupport = -> [XY_Plane008]
  FullyConstrained = true
  MakeInternals = false
  MapMode = 5
  Placement = pos=(0,0,-3) rot=(0,0,1;0rad)
  expr: Constraints[58] = VarSet.Top_MedXY / 2 + VarSet.Top_Frame + VarSet.Mold_WallD + VarSet.Mold_MoatD
  expr: Constraints[59] = VarSet.Top_MedXY / 2 + VarSet.Top_Frame + VarSet.Mold_WallD + VarSet.Mold_MoatD
  expr: Constraints[60] = VarSet.Top_MedXY / 2 + VarSet.Top_Frame + VarSet.Top_RearAdd + VarSet.Mold_WallD + VarSet.Mold_MoatD
  expr: Constraints[61] = VarSet.Top_MedXY / 2 + VarSet.Top_Frame + VarSet.Mold_WallD + VarSet.Mold_MoatD
  expr: Constraints[70] = VarSet.Top_MedXY / 2 + VarSet.Top_Frame + VarSet.Top_RearAdd + VarSet.Mold_WallD
  expr: Constraints[71] = VarSet.Top_MedXY / 2 + VarSet.Top_Frame + VarSet.Mold_WallD
  expr: Constraints[72] = VarSet.Top_MedXY / 2 + VarSet.Top_Frame + VarSet.Mold_WallD
  expr: Constraints[73] = VarSet.Top_MedXY / 2 + VarSet.Top_Frame + VarSet.Mold_WallD
  sketch-geometry (33):
    g0: GeomPoint [constr] X=-38.1 Y=19.05 Z=0
    g1: GeomPoint [constr] X=-57.15 Y=19.05 Z=0
    g2: GeomPoint [constr] X=-76.2 Y=19.05 Z=0
    g3: GeomPoint [constr] X=-95.25 Y=19.05 Z=0
    g4: GeomPoint [constr] X=-114.3 Y=19.05 Z=0
    g5: GeomPoint [constr] X=-38.1 Y=57.15 Z=0
    g6: GeomPoint [constr] X=-57.15 Y=57.15 Z=0
    g7: GeomPoint [constr] X=-76.2 Y=57.15 Z=0
    g8: GeomPoint [constr] X=-95.25 Y=57.15 Z=0
    g9: GeomPoint [constr] X=-114.3 Y=57.15 Z=0
    g10: GeomPoint [constr] X=-38.1 Y=38.1 Z=0
    g11: GeomPoint [constr] X=-57.15 Y=38.1 Z=0
    g12: GeomPoint [constr] X=-76.2 Y=38.1 Z=0
    g13: GeomPoint [constr] X=-95.25 Y=38.1 Z=0
    g14: GeomPoint [constr] X=-114.3 Y=38.1 Z=0
    g15: GeomPoint [constr] X=-95.25 Y=76.2 Z=0
    g16: GeomPoint [constr] X=-57.15 Y=76.2 Z=0
    g17: GeomPoint [constr] X=-133.35 Y=76.2 Z=0
    g18: GeomPoint [constr] X=-114.3 Y=76.2 Z=0
    g19: GeomPoint [constr] X=-76.2 Y=76.2 Z=0
    g20: LineSegment StartX=-156.25 StartY=102.1 StartZ=0 EndX=-156.25 EndY=-3.85 EndZ=0
    g21: LineSegment StartX=-156.25 StartY=102.1 StartZ=0 EndX=3.85 EndY=102.1 EndZ=0
    g22: LineSegment StartX=3.85 StartY=102.1 StartZ=0 EndX=3.85 EndY=-3.85 EndZ=0
    g23: LineSegment StartX=3.85 StartY=-3.85 StartZ=0 EndX=-156.25 EndY=-3.85 EndZ=0
    g24: GeomPoint [constr] X=-38.1 Y=76.2 Z=0
    g25: GeomPoint [constr] X=-133.35 Y=57.15 Z=0
    g26: GeomPoint [constr] X=-133.35 Y=38.1 Z=0
    g27: GeomPoint [constr] X=-133.35 Y=19.05 Z=0
    g28: GeomPoint [constr] X=-19.05 Y=19.05 Z=0
    g29: LineSegment StartX=-146.25 StartY=92.1 StartZ=0 EndX=-146.25 EndY=6.15 EndZ=0
    g30: LineSegment StartX=-146.25 StartY=6.15 StartZ=0 EndX=-6.15 EndY=6.15 EndZ=0
    g31: LineSegment StartX=-6.15 StartY=6.15 StartZ=0 EndX=-6.15 EndY=92.1 EndZ=0
    g32: LineSegment StartX=-6.15 StartY=92.1 StartZ=0 EndX=-146.25 EndY=92.1 EndZ=0
  constraints (74):
    c: DistanceX(g1,g0) = 19.05
    c: DistanceX(g2,g1) = 19.05
    c: DistanceX(g3,g2) = 19.05
    c: DistanceX(g4,g3) = 19.05
    c: DistanceY(g0,g10) = 19.05
    c: DistanceY(g10,g5) = 19.05
    c: Vertical(g20)
    c: Horizontal(g21)
    c: Vertical(g22)
    c: Horizontal(g23)
    c: DistanceY(g5,g24) = 19.05
    c: DistanceX(g27,g4) = 19.05
    c: DistanceX(g0,g28) = 19.05
    c: DistanceX(g28,g-1) = 19.05
    c: Horizontal(g17,g18)
    c: Horizontal(g18,g15)
    c: Horizontal(g15,g19)
    c: Horizontal(g19,g16)
    c: Horizontal(g16,g24)
    c: Horizontal(g25,g9)
    c: Horizontal(g9,g8)
    c: Horizontal(g8,g7)
    c: Horizontal(g7,g6)
    c: Horizontal(g6,g5)
    c: Horizontal(g26,g14)
    c: Horizontal(g14,g13)
    c: Horizontal(g13,g12)
    c: Horizontal(g12,g11)
    c: Horizontal(g11,g10)
    c: Vertical(g17,g25)
    c: Vertical(g25,g26)
    c: Vertical(g26,g27)
    c: Vertical(g18,g9)
    c: Vertical(g9,g14)
    c: Vertical(g14,g4)
    c: Vertical(g15,g8)
    c: Vertical(g8,g13)
    c: Vertical(g13,g3)
    c: Vertical(g19,g7)
    c: Vertical(g7,g12)
    c: Vertical(g12,g2)
    c: Vertical(g16,g6)
    c: Vertical(g6,g11)
    c: Vertical(g11,g1)
    c: Vertical(g24,g5)
    c: Vertical(g5,g10)
    c: Vertical(g10,g0)
    c: Horizontal(g27,g4)
    c: Horizontal(g4,g3)
    c: Horizontal(g3,g2)
    c: Horizontal(g2,g1)
    c: Horizontal(g1,g0)
    c: Horizontal(g0,g28)
    c: DistanceY(g-1,g28) = 19.05
    c: Coincident(g21,g20)
    c: Coincident(g21,g22)
    c: Coincident(g23,g22)
    c: Coincident(g23,g20)
    c: DistanceX(g20,g17) = 22.9
    c: DistanceX(g28,g22) = 22.9
    c: DistanceY(g17,g20) = 25.9
    c: DistanceY(g22,g28) = 22.9
    c: Coincident(g29,g30)
    c: Coincident(g30,g31)
    c: Coincident(g31,g32)
    c: Coincident(g32,g29)
    c: Vertical(g29)
    c: Vertical(g31)
    c: Horizontal(g30)
    c: Horizontal(g32)
    c: DistanceY(g17,g29) = 15.9
    c: DistanceX(g29,g17) = 12.9
    c: DistanceX(g28,g30) = 12.9
    c: DistanceY(g30,g28) = 12.9
FEATURE [PartDesign::Pocket] Pocket063  label="ML-Moat-Pocket"
  BaseFeature = -> Pad028
  Direction = (0,0,-1)
  Length = 3.75
  Length2 = 5
  Profile = -> Sketch095
  ReferenceAxis = -> Sketch095 [N_Axis]
  Refine = true
  Reversed = true
  Suppressed = false
  Type = 0
  expr: Length = 3 mm - 1 mm + VarSet.Top_PcbZ / 2 + VarSet.Mold_WallD
FEATURE [Sketcher::SketchObject] Sketch096  label="MR-Plate"
  ArcFitTolerance = 1e-06
  AttachmentOffset = pos=(0,0,-3) rot=(0,0,1;0rad)
  AttachmentSupport = -> [XY_Plane009]
  FullyConstrained = true
  MakeInternals = false
  MapMode = 5
  Placement = pos=(0,0,-3) rot=(0,0,1;0rad)
  expr: Constraints[58] = VarSet.Top_MedXY / 2 + VarSet.Top_Frame + 2 * VarSet.Mold_WallD + VarSet.Mold_MoatD
  expr: Constraints[59] = VarSet.Top_MedXY / 2 + VarSet.Top_Frame + 2 * VarSet.Mold_WallD + VarSet.Mold_MoatD
  expr: Constraints[60] = VarSet.Top_MedXY / 2 + VarSet.Top_Frame + VarSet.Top_RearAdd + 2 * VarSet.Mold_WallD + VarSet.Mold_MoatD
  expr: Constraints[61] = VarSet.Top_MedXY / 2 + VarSet.Top_Frame + 2 * VarSet.Mold_WallD + VarSet.Mold_MoatD
  sketch-geometry (29):
    g0: GeomPoint [constr] X=38.1 Y=19.05 Z=0
    g1: GeomPoint [constr] X=57.15 Y=19.05 Z=0
    g2: GeomPoint [constr] X=38.1 Y=38.1 Z=0
    g3: GeomPoint [constr] X=76.2 Y=19.05 Z=0
    g4: GeomPoint [constr] X=95.25 Y=19.05 Z=0
    g5: GeomPoint [constr] X=57.15 Y=38.1 Z=0
    g6: GeomPoint [constr] X=76.2 Y=38.1 Z=0
    g7: GeomPoint [constr] X=114.3 Y=19.05 Z=0
    g8: GeomPoint [constr] X=95.25 Y=38.1 Z=0
    g9: GeomPoint [constr] X=38.1 Y=57.15 Z=0
    g10: GeomPoint [constr] X=57.15 Y=57.15 Z=0
    g11: GeomPoint [constr] X=76.2 Y=57.15 Z=0
    g12: GeomPoint [constr] X=95.25 Y=57.15 Z=0
    g13: GeomPoint [constr] X=38.1 Y=76.2 Z=0
    g14: GeomPoint [constr] X=57.15 Y=76.2 Z=0
    g15: GeomPoint [constr] X=76.2 Y=76.2 Z=0
    g16: GeomPoint [constr] X=95.25 Y=76.2 Z=0
    g17: GeomPoint [constr] X=114.3 Y=76.2 Z=0
    g18: GeomPoint [constr] X=114.3 Y=57.15 Z=0
    g19: GeomPoint [constr] X=114.3 Y=38.1 Z=0
    g20: GeomPoint [constr] X=133.35 Y=19.05 Z=0
    g21: GeomPoint [constr] X=19.05 Y=19.05 Z=0
    g22: GeomPoint [constr] X=133.35 Y=38.1 Z=0
    g23: GeomPoint [constr] X=133.35 Y=57.15 Z=0
    g24: GeomPoint [constr] X=133.35 Y=76.2 Z=0
    g25: LineSegment StartX=-4.85 StartY=103.1 StartZ=0 EndX=157.25 EndY=103.1 EndZ=0
    g26: LineSegment StartX=157.25 StartY=103.1 StartZ=0 EndX=157.25 EndY=-4.85 EndZ=0
    g27: LineSegment StartX=157.25 StartY=-4.85 StartZ=0 EndX=-4.85 EndY=-4.85 EndZ=0
    g28: LineSegment StartX=-4.85 StartY=-4.85 StartZ=0 EndX=-4.85 EndY=103.1 EndZ=0
  constraints (62):
    c: Horizontal(g13,g14)
    c: Horizontal(g14,g15)
    c: Horizontal(g15,g16)
    c: Horizontal(g16,g17)
    c: Horizontal(g17,g24)
    c: Horizontal(g9,g10)
    c: Horizontal(g10,g11)
    c: Horizontal(g11,g12)
    c: Horizontal(g12,g18)
    c: Horizontal(g18,g23)
    c: Horizontal(g2,g5)
    c: Horizontal(g5,g6)
    c: Horizontal(g6,g8)
    c: Horizontal(g8,g19)
    c: Horizontal(g19,g22)
    c: Horizontal(g21,g0)
    c: Horizontal(g0,g1)
    c: Horizontal(g1,g3)
    c: Horizontal(g3,g4)
    c: Horizontal(g4,g7)
    c: Horizontal(g7,g20)
    c: Vertical(g13,g9)
    c: Vertical(g9,g2)
    c: Vertical(g2,g0)
    c: Vertical(g14,g10)
    c: Vertical(g10,g5)
    c: Vertical(g5,g1)
    c: Vertical(g15,g11)
    c: Vertical(g11,g6)
    c: Vertical(g6,g3)
    c: Vertical(g16,g12)
    c: Vertical(g12,g8)
    c: Vertical(g8,g4)
    c: Vertical(g17,g18)
    c: Vertical(g18,g19)
    c: Vertical(g19,g7)
    c: Vertical(g24,g23)
    c: Vertical(g23,g22)
    c: Vertical(g22,g20)
    c: DistanceX(g21,g0) = 19.05
    c: DistanceX(g0,g1) = 19.05
    c: DistanceX(g1,g3) = 19.05
    c: DistanceX(g3,g4) = 19.05
    c: DistanceX(g4,g7) = 19.05
    c: DistanceX(g7,g20) = 19.05
    c: DistanceY(g9,g13) = 19.05
    c: DistanceY(g2,g9) = 19.05
    c: DistanceY(g21,g2) = 19.05
    c: DistanceX(g-1,g21) = 19.05
    c: DistanceY(g-1,g21) = 19.05
    c: Horizontal(g25)
    c: Vertical(g26)
    c: Horizontal(g27)
    c: Vertical(g28)
    c: Coincident(g28,g25)
    c: Coincident(g25,g26)
    c: Coincident(g26,g27)
    c: Coincident(g27,g28)
    c: DistanceX(g27,g21) = 23.9
    c: DistanceX(g24,g25) = 23.9
    c: DistanceY(g24,g25) = 26.9
    c: DistanceY(g27,g21) = 23.9
FEATURE [PartDesign::Pad] Pad029  label="MR-Plate-Pad"
  Direction = (0,0,1)
  Length = 4.75
  Length2 = 10
  Profile = -> Sketch096
  ReferenceAxis = -> Sketch096 [N_Axis]
  Refine = true
  Suppressed = false
  Type = 0
  expr: Length = 3 mm + VarSet.Top_PcbZ / 2 + VarSet.Mold_WallD
FEATURE [Sketcher::SketchObject] Sketch097  label="MR-Moat"
  ArcFitTolerance = 1e-06
  AttachmentOffset = pos=(0,0,-3) rot=(0,0,1;0rad)
  AttachmentSupport = -> [XY_Plane009]
  FullyConstrained = true
  MakeInternals = false
  MapMode = 5
  Placement = pos=(0,0,-3) rot=(0,0,1;0rad)
  expr: Constraints[58] = VarSet.Top_MedXY / 2 + VarSet.Top_Frame + VarSet.Mold_WallD + VarSet.Mold_MoatD
  expr: Constraints[59] = VarSet.Top_MedXY / 2 + VarSet.Top_Frame + VarSet.Mold_WallD + VarSet.Mold_MoatD
  expr: Constraints[60] = VarSet.Top_MedXY / 2 + VarSet.Top_Frame + VarSet.Top_RearAdd + VarSet.Mold_WallD + VarSet.Mold_MoatD
  expr: Constraints[61] = VarSet.Top_MedXY / 2 + VarSet.Top_Frame + VarSet.Mold_WallD + VarSet.Mold_MoatD
  expr: Constraints[70] = VarSet.Top_MedXY / 2 + VarSet.Top_Frame + VarSet.Mold_WallD
  expr: Constraints[71] = VarSet.Top_MedXY / 2 + VarSet.Top_Frame + VarSet.Mold_WallD
  expr: Constraints[72] = VarSet.Top_MedXY / 2 + VarSet.Top_Frame + VarSet.Mold_WallD
  expr: Constraints[73] = VarSet.Top_MedXY / 2 + VarSet.Top_Frame + VarSet.Top_RearAdd + VarSet.Mold_WallD
  sketch-geometry (33):
    g0: GeomPoint [constr] X=38.1 Y=19.05 Z=0
    g1: GeomPoint [constr] X=57.15 Y=19.05 Z=0
    g2: GeomPoint [constr] X=38.1 Y=38.1 Z=0
    g3: GeomPoint [constr] X=76.2 Y=19.05 Z=0
    g4: GeomPoint [constr] X=95.25 Y=19.05 Z=0
    g5: GeomPoint [constr] X=57.15 Y=38.1 Z=0
    g6: GeomPoint [constr] X=76.2 Y=38.1 Z=0
    g7: GeomPoint [constr] X=114.3 Y=19.05 Z=0
    g8: GeomPoint [constr] X=95.25 Y=38.1 Z=0
    g9: GeomPoint [constr] X=38.1 Y=57.15 Z=0
    g10: GeomPoint [constr] X=57.15 Y=57.15 Z=0
    g11: GeomPoint [constr] X=76.2 Y=57.15 Z=0
    g12: GeomPoint [constr] X=95.25 Y=57.15 Z=0
    g13: GeomPoint [constr] X=38.1 Y=76.2 Z=0
    g14: GeomPoint [constr] X=57.15 Y=76.2 Z=0
    g15: GeomPoint [constr] X=76.2 Y=76.2 Z=0
    g16: GeomPoint [constr] X=95.25 Y=76.2 Z=0
    g17: GeomPoint [constr] X=114.3 Y=76.2 Z=0
    g18: GeomPoint [constr] X=114.3 Y=57.15 Z=0
    g19: GeomPoint [constr] X=114.3 Y=38.1 Z=0
    g20: GeomPoint [constr] X=133.35 Y=19.05 Z=0
    g21: GeomPoint [constr] X=19.05 Y=19.05 Z=0
    g22: GeomPoint [constr] X=133.35 Y=38.1 Z=0
    g23: GeomPoint [constr] X=133.35 Y=57.15 Z=0
    g24: GeomPoint [constr] X=133.35 Y=76.2 Z=0
    g25: LineSegment StartX=-3.85 StartY=102.1 StartZ=0 EndX=156.25 EndY=102.1 EndZ=0
    g26: LineSegment StartX=156.25 StartY=102.1 StartZ=0 EndX=156.25 EndY=-3.85 EndZ=0
    g27: LineSegment StartX=156.25 StartY=-3.85 StartZ=0 EndX=-3.85 EndY=-3.85 EndZ=0
    g28: LineSegment StartX=-3.85 StartY=-3.85 StartZ=0 EndX=-3.85 EndY=102.1 EndZ=0
    g29: LineSegment StartX=6.15 StartY=92.1 StartZ=0 EndX=6.15 EndY=6.15 EndZ=0
    g30: LineSegment StartX=6.15 StartY=6.15 StartZ=0 EndX=146.25 EndY=6.15 EndZ=0
    g31: LineSegment StartX=146.25 StartY=6.15 StartZ=0 EndX=146.25 EndY=92.1 EndZ=0
    g32: LineSegment StartX=146.25 StartY=92.1 StartZ=0 EndX=6.15 EndY=92.1 EndZ=0
  constraints (74):
    c: Horizontal(g13,g14)
    c: Horizontal(g14,g15)
    c: Horizontal(g15,g16)
    c: Horizontal(g16,g17)
    c: Horizontal(g17,g24)
    c: Horizontal(g9,g10)
    c: Horizontal(g10,g11)
    c: Horizontal(g11,g12)
    c: Horizontal(g12,g18)
    c: Horizontal(g18,g23)
    c: Horizontal(g2,g5)
    c: Horizontal(g5,g6)
    c: Horizontal(g6,g8)
    c: Horizontal(g8,g19)
    c: Horizontal(g19,g22)
    c: Horizontal(g21,g0)
    c: Horizontal(g0,g1)
    c: Horizontal(g1,g3)
    c: Horizontal(g3,g4)
    c: Horizontal(g4,g7)
    c: Horizontal(g7,g20)
    c: Vertical(g13,g9)
    c: Vertical(g9,g2)
    c: Vertical(g2,g0)
    c: Vertical(g14,g10)
    c: Vertical(g10,g5)
    c: Vertical(g5,g1)
    c: Vertical(g15,g11)
    c: Vertical(g11,g6)
    c: Vertical(g6,g3)
    c: Vertical(g16,g12)
    c: Vertical(g12,g8)
    c: Vertical(g8,g4)
    c: Vertical(g17,g18)
    c: Vertical(g18,g19)
    c: Vertical(g19,g7)
    c: Vertical(g24,g23)
    c: Vertical(g23,g22)
    c: Vertical(g22,g20)
    c: DistanceX(g21,g0) = 19.05
    c: DistanceX(g0,g1) = 19.05
    c: DistanceX(g1,g3) = 19.05
    c: DistanceX(g3,g4) = 19.05
    c: DistanceX(g4,g7) = 19.05
    c: DistanceX(g7,g20) = 19.05
    c: DistanceY(g9,g13) = 19.05
    c: DistanceY(g2,g9) = 19.05
    c: DistanceY(g21,g2) = 19.05
    c: DistanceX(g-1,g21) = 19.05
    c: DistanceY(g-1,g21) = 19.05
    c: Horizontal(g25)
    c: Vertical(g26)
    c: Horizontal(g27)
    c: Vertical(g28)
    c: Coincident(g28,g25)
    c: Coincident(g25,g26)
    c: Coincident(g26,g27)
    c: Coincident(g27,g28)
    c: DistanceX(g27,g21) = 22.9
    c: DistanceX(g24,g25) = 22.9
    c: DistanceY(g24,g25) = 25.9
    c: DistanceY(g27,g21) = 22.9
    c: Coincident(g29,g30)
    c: Coincident(g30,g31)
    c: Coincident(g31,g32)
    c: Coincident(g32,g29)
    c: Vertical(g29)
    c: Vertical(g31)
    c: Horizontal(g30)
    c: Horizontal(g32)
    c: DistanceX(g24,g31) = 12.9
    c: DistanceX(g29,g21) = 12.9
    c: DistanceY(g29,g21) = 12.9
    c: DistanceY(g24,g31) = 15.9
FEATURE [PartDesign::Pocket] Pocket064  label="MR-Moat-Pocket"
  BaseFeature = -> Pad029
  Direction = (0,0,-1)
  Length = 3.75
  Length2 = 5
  Profile = -> Sketch097
  ReferenceAxis = -> Sketch097 [N_Axis]
  Refine = true
  Reversed = true
  Suppressed = false
  Type = 0
  expr: Length = 3 mm - 1 mm + VarSet.Top_PcbZ / 2 + VarSet.Mold_WallD
FEATURE [Sketcher::SketchObject] Sketch101  label="BL-DiodeLEDGap"
  ArcFitTolerance = 1e-06
  AttachmentSupport = -> [XY_Plane001]
  ExternalGeometry = -> [Sketch029,Sketch022]
  FullyConstrained = true
  MakeInternals = false
  MapMode = 5
  sketch-geometry (96):
    g0: LineSegment StartX=-40.7 StartY=25.75 StartZ=0 EndX=-40.7 EndY=25.35 EndZ=0
    g1: LineSegment StartX=-40.7 StartY=25.35 StartZ=0 EndX=-35 EndY=25.35 EndZ=0
    g2: LineSegment StartX=-35 StartY=25.35 StartZ=0 EndX=-35 EndY=25.75 EndZ=0
    g3: LineSegment StartX=-35 StartY=25.75 StartZ=0 EndX=-40.7 EndY=25.75 EndZ=0
    g4: LineSegment StartX=-59.75 StartY=25.75 StartZ=0 EndX=-59.75 EndY=25.35 EndZ=0
    g5: LineSegment StartX=-59.75 StartY=25.35 StartZ=0 EndX=-54.05 EndY=25.35 EndZ=0
    g6: LineSegment StartX=-54.05 StartY=25.35 StartZ=0 EndX=-54.05 EndY=25.75 EndZ=0
    g7: LineSegment StartX=-54.05 StartY=25.75 StartZ=0 EndX=-59.75 EndY=25.75 EndZ=0
    g8: LineSegment StartX=-78.8 StartY=25.75 StartZ=0 EndX=-78.8 EndY=25.35 EndZ=0
    g9: LineSegment StartX=-78.8 StartY=25.35 StartZ=0 EndX=-73.1 EndY=25.35 EndZ=0
    g10: LineSegment StartX=-73.1 StartY=25.35 StartZ=0 EndX=-73.1 EndY=25.75 EndZ=0
    g11: LineSegment StartX=-73.1 StartY=25.75 StartZ=0 EndX=-78.8 EndY=25.75 EndZ=0
    g12: LineSegment StartX=-97.85 StartY=25.75 StartZ=0 EndX=-97.85 EndY=25.35 EndZ=0
    g13: LineSegment StartX=-97.85 StartY=25.35 StartZ=0 EndX=-92.15 EndY=25.35 EndZ=0
    g14: LineSegment StartX=-92.15 StartY=25.35 StartZ=0 EndX=-92.15 EndY=25.75 EndZ=0
    g15: LineSegment StartX=-92.15 StartY=25.75 StartZ=0 EndX=-97.85 EndY=25.75 EndZ=0
    g16: LineSegment StartX=-116.9 StartY=25.75 StartZ=0 EndX=-116.9 EndY=25.35 EndZ=0
    g17: LineSegment StartX=-116.9 StartY=25.35 StartZ=0 EndX=-111.2 EndY=25.35 EndZ=0
    g18: LineSegment StartX=-111.2 StartY=25.35 StartZ=0 EndX=-111.2 EndY=25.75 EndZ=0
    g19: LineSegment StartX=-111.2 StartY=25.75 StartZ=0 EndX=-116.9 EndY=25.75 EndZ=0
    g20: LineSegment StartX=-135.95 StartY=25.75 StartZ=0 EndX=-135.95 EndY=25.35 EndZ=0
    g21: LineSegment StartX=-135.95 StartY=25.35 StartZ=0 EndX=-130.25 EndY=25.35 EndZ=0
    g22: LineSegment StartX=-130.25 StartY=25.35 StartZ=0 EndX=-130.25 EndY=25.75 EndZ=0
    g23: LineSegment StartX=-130.25 StartY=25.75 StartZ=0 EndX=-135.95 EndY=25.75 EndZ=0
    g24: LineSegment StartX=-40.7 StartY=44.8 StartZ=0 EndX=-40.7 EndY=44.4 EndZ=0
    g25: LineSegment StartX=-40.7 StartY=44.4 StartZ=0 EndX=-35 EndY=44.4 EndZ=0
    g26: LineSegment StartX=-35 StartY=44.4 StartZ=0 EndX=-35 EndY=44.8 EndZ=0
    g27: LineSegment StartX=-35 StartY=44.8 StartZ=0 EndX=-40.7 EndY=44.8 EndZ=0
    g28: LineSegment StartX=-59.75 StartY=44.8 StartZ=0 EndX=-59.75 EndY=44.4 EndZ=0
    g29: LineSegment StartX=-59.75 StartY=44.4 StartZ=0 EndX=-54.05 EndY=44.4 EndZ=0
    g30: LineSegment StartX=-54.05 StartY=44.4 StartZ=0 EndX=-54.05 EndY=44.8 EndZ=0
    g31: LineSegment StartX=-54.05 StartY=44.8 StartZ=0 EndX=-59.75 EndY=44.8 EndZ=0
    g32: LineSegment StartX=-78.8 StartY=44.8 StartZ=0 EndX=-78.8 EndY=44.4 EndZ=0
    g33: LineSegment StartX=-78.8 StartY=44.4 StartZ=0 EndX=-73.1 EndY=44.4 EndZ=0
    g34: LineSegment StartX=-73.1 StartY=44.4 StartZ=0 EndX=-73.1 EndY=44.8 EndZ=0
    g35: LineSegment StartX=-73.1 StartY=44.8 StartZ=0 EndX=-78.8 EndY=44.8 EndZ=0
    g36: LineSegment StartX=-97.85 StartY=44.8 StartZ=0 EndX=-97.85 EndY=44.4 EndZ=0
    g37: LineSegment StartX=-97.85 StartY=44.4 StartZ=0 EndX=-92.15 EndY=44.4 EndZ=0
    g38: LineSegment StartX=-92.15 StartY=44.4 StartZ=0 EndX=-92.15 EndY=44.8 EndZ=0
    g39: LineSegment StartX=-92.15 StartY=44.8 StartZ=0 EndX=-97.85 EndY=44.8 EndZ=0
    g40: LineSegment StartX=-116.9 StartY=44.8 StartZ=0 EndX=-116.9 EndY=44.4 EndZ=0
    g41: LineSegment StartX=-116.9 StartY=44.4 StartZ=0 EndX=-111.2 EndY=44.4 EndZ=0
    g42: LineSegment StartX=-111.2 StartY=44.4 StartZ=0 EndX=-111.2 EndY=44.8 EndZ=0
    g43: LineSegment StartX=-111.2 StartY=44.8 StartZ=0 EndX=-116.9 EndY=44.8 EndZ=0
    g44: LineSegment StartX=-135.95 StartY=44.8 StartZ=0 EndX=-135.95 EndY=44.4 EndZ=0
    g45: LineSegment StartX=-135.95 StartY=44.4 StartZ=0 EndX=-130.25 EndY=44.4 EndZ=0
    g46: LineSegment StartX=-130.25 StartY=44.4 StartZ=0 EndX=-130.25 EndY=44.8 EndZ=0
    g47: LineSegment StartX=-130.25 StartY=44.8 StartZ=0 EndX=-135.95 EndY=44.8 EndZ=0
    g48: LineSegment StartX=-40.7 StartY=63.85 StartZ=0 EndX=-40.7 EndY=63.45 EndZ=0
    g49: LineSegment StartX=-40.7 StartY=63.45 StartZ=0 EndX=-35 EndY=63.45 EndZ=0
    g50: LineSegment StartX=-35 StartY=63.45 StartZ=0 EndX=-35 EndY=63.85 EndZ=0
    g51: LineSegment StartX=-35 StartY=63.85 StartZ=0 EndX=-40.7 EndY=63.85 EndZ=0
    g52: LineSegment StartX=-59.75 StartY=63.85 StartZ=0 EndX=-59.75 EndY=63.45 EndZ=0
    g53: LineSegment StartX=-59.75 StartY=63.45 StartZ=0 EndX=-54.05 EndY=63.45 EndZ=0
    g54: LineSegment StartX=-54.05 StartY=63.45 StartZ=0 EndX=-54.05 EndY=63.85 EndZ=0
    g55: LineSegment StartX=-54.05 StartY=63.85 StartZ=0 EndX=-59.75 EndY=63.85 EndZ=0
    g56: LineSegment StartX=-78.8 StartY=63.85 StartZ=0 EndX=-78.8 EndY=63.45 EndZ=0
    g57: LineSegment StartX=-78.8 StartY=63.45 StartZ=0 EndX=-73.1 EndY=63.45 EndZ=0
    g58: LineSegment StartX=-73.1 StartY=63.45 StartZ=0 EndX=-73.1 EndY=63.85 EndZ=0
    g59: LineSegment StartX=-73.1 StartY=63.85 StartZ=0 EndX=-78.8 EndY=63.85 EndZ=0
    g60: LineSegment StartX=-97.85 StartY=63.85 StartZ=0 EndX=-97.85 EndY=63.45 EndZ=0
    g61: LineSegment StartX=-97.85 StartY=63.45 StartZ=0 EndX=-92.15 EndY=63.45 EndZ=0
    g62: LineSegment StartX=-92.15 StartY=63.45 StartZ=0 EndX=-92.15 EndY=63.85 EndZ=0
    g63: LineSegment StartX=-92.15 StartY=63.85 StartZ=0 EndX=-97.85 EndY=63.85 EndZ=0
    g64: LineSegment StartX=-116.9 StartY=63.85 StartZ=0 EndX=-116.9 EndY=63.45 EndZ=0
    g65: LineSegment StartX=-116.9 StartY=63.45 StartZ=0 EndX=-111.2 EndY=63.45 EndZ=0
    g66: LineSegment StartX=-111.2 StartY=63.45 StartZ=0 EndX=-111.2 EndY=63.85 EndZ=0
    g67: LineSegment StartX=-111.2 StartY=63.85 StartZ=0 EndX=-116.9 EndY=63.85 EndZ=0
    g68: LineSegment StartX=-135.95 StartY=63.85 StartZ=0 EndX=-135.95 EndY=63.45 EndZ=0
    g69: LineSegment StartX=-135.95 StartY=63.45 StartZ=0 EndX=-130.25 EndY=63.45 EndZ=0
    g70: LineSegment StartX=-130.25 StartY=63.45 StartZ=0 EndX=-130.25 EndY=63.85 EndZ=0
    g71: LineSegment StartX=-130.25 StartY=63.85 StartZ=0 EndX=-135.95 EndY=63.85 EndZ=0
    g72: LineSegment StartX=-53.375 StartY=82.9 StartZ=0 EndX=-53.375 EndY=82.5 EndZ=0
    g73: LineSegment StartX=-53.375 StartY=82.5 StartZ=0 EndX=-53.15 EndY=82.5 EndZ=0
    g74: LineSegment StartX=-53.15 StartY=82.5 StartZ=0 EndX=-53.15 EndY=82.9 EndZ=0
    g75: LineSegment StartX=-53.15 StartY=82.9 StartZ=0 EndX=-53.375 EndY=82.9 EndZ=0
    g76: LineSegment StartX=-61.15 StartY=82.9 StartZ=0 EndX=-61.15 EndY=82.5 EndZ=0
    g77: LineSegment StartX=-61.15 StartY=82.5 StartZ=0 EndX=-60.425 EndY=82.5 EndZ=0
    g78: LineSegment StartX=-60.425 StartY=82.5 StartZ=0 EndX=-60.425 EndY=82.9 EndZ=0
    g79: LineSegment StartX=-60.425 StartY=82.9 StartZ=0 EndX=-61.15 EndY=82.9 EndZ=0
    g80: LineSegment StartX=-78.8 StartY=82.9 StartZ=0 EndX=-78.8 EndY=82.5 EndZ=0
    g81: LineSegment StartX=-78.8 StartY=82.5 StartZ=0 EndX=-73.1 EndY=82.5 EndZ=0
    g82: LineSegment StartX=-73.1 StartY=82.5 StartZ=0 EndX=-73.1 EndY=82.9 EndZ=0
    g83: LineSegment StartX=-73.1 StartY=82.9 StartZ=0 EndX=-78.8 EndY=82.9 EndZ=0
    g84: LineSegment StartX=-97.85 StartY=82.9 StartZ=0 EndX=-97.85 EndY=82.5 EndZ=0
    g85: LineSegment StartX=-97.85 StartY=82.5 StartZ=0 EndX=-92.15 EndY=82.5 EndZ=0
    g86: LineSegment StartX=-92.15 StartY=82.5 StartZ=0 EndX=-92.15 EndY=82.9 EndZ=0
    g87: LineSegment StartX=-92.15 StartY=82.9 StartZ=0 EndX=-97.85 EndY=82.9 EndZ=0
    g88: LineSegment StartX=-110.525 StartY=82.9 StartZ=0 EndX=-110.525 EndY=82.5 EndZ=0
    g89: LineSegment StartX=-110.525 StartY=82.5 StartZ=0 EndX=-110.3 EndY=82.5 EndZ=0
    g90: LineSegment StartX=-110.3 StartY=82.5 StartZ=0 EndX=-110.3 EndY=82.9 EndZ=0
    g91: LineSegment StartX=-110.3 StartY=82.9 StartZ=0 EndX=-110.525 EndY=82.9 EndZ=0
    g92: LineSegment StartX=-118.3 StartY=82.9 StartZ=0 EndX=-118.3 EndY=82.5 EndZ=0
    g93: LineSegment StartX=-118.3 StartY=82.5 StartZ=0 EndX=-117.575 EndY=82.5 EndZ=0
    g94: LineSegment StartX=-117.575 StartY=82.5 StartZ=0 EndX=-117.575 EndY=82.9 EndZ=0
    g95: LineSegment StartX=-117.575 StartY=82.9 StartZ=0 EndX=-118.3 EndY=82.9 EndZ=0
  constraints (288):
    c: Coincident(g0,g1)
    c: Coincident(g1,g2)
    c: Coincident(g2,g3)
    c: Coincident(g3,g0)
    c: Vertical(g0)
    c: Vertical(g2)
    c: Horizontal(g1)
    c: Horizontal(g3)
    c: Coincident(g4,g5)
    c: Coincident(g5,g6)
    c: Coincident(g6,g7)
    c: Coincident(g7,g4)
    c: Vertical(g4)
    c: Vertical(g6)
    c: Horizontal(g5)
    c: Horizontal(g7)
    c: Coincident(g8,g9)
    c: Coincident(g9,g10)
    c: Coincident(g10,g11)
    c: Coincident(g11,g8)
    c: Vertical(g8)
    c: Vertical(g10)
    c: Horizontal(g9)
    c: Horizontal(g11)
    c: Coincident(g12,g13)
    c: Coincident(g13,g14)
    c: Coincident(g14,g15)
    c: Coincident(g15,g12)
    c: Vertical(g12)
    c: Vertical(g14)
    c: Horizontal(g13)
    c: Horizontal(g15)
    c: Coincident(g16,g17)
    c: Coincident(g17,g18)
    c: Coincident(g18,g19)
    c: Coincident(g19,g16)
    c: Vertical(g16)
    c: Vertical(g18)
    c: Horizontal(g17)
    c: Horizontal(g19)
    c: Coincident(g20,g21)
    c: Coincident(g21,g22)
    c: Coincident(g22,g23)
    c: Coincident(g23,g20)
    c: Vertical(g20)
    c: Vertical(g22)
    c: Horizontal(g21)
    c: Horizontal(g23)
    c: Coincident(g24,g25)
    c: Coincident(g25,g26)
    c: Coincident(g26,g27)
    c: Coincident(g27,g24)
    c: Vertical(g24)
    c: Vertical(g26)
    c: Horizontal(g25)
    c: Horizontal(g27)
    c: Coincident(g28,g29)
    c: Coincident(g29,g30)
    c: Coincident(g30,g31)
    c: Coincident(g31,g28)
    c: Vertical(g28)
    c: Vertical(g30)
    c: Horizontal(g29)
    c: Horizontal(g31)
    c: Coincident(g32,g33)
    c: Coincident(g33,g34)
    c: Coincident(g34,g35)
    c: Coincident(g35,g32)
    c: Vertical(g32)
    c: Vertical(g34)
    c: Horizontal(g33)
    c: Horizontal(g35)
    c: Coincident(g36,g37)
    c: Coincident(g37,g38)
    c: Coincident(g38,g39)
    c: Coincident(g39,g36)
    c: Vertical(g36)
    c: Vertical(g38)
    c: Horizontal(g37)
    c: Horizontal(g39)
    c: Coincident(g40,g41)
    c: Coincident(g41,g42)
    c: Coincident(g42,g43)
    c: Coincident(g43,g40)
    c: Vertical(g40)
    c: Vertical(g42)
    c: Horizontal(g41)
    c: Horizontal(g43)
    c: Coincident(g44,g45)
    c: Coincident(g45,g46)
    c: Coincident(g46,g47)
    c: Coincident(g47,g44)
    c: Vertical(g44)
    c: Vertical(g46)
    c: Horizontal(g45)
    c: Horizontal(g47)
    c: Coincident(g48,g49)
    c: Coincident(g49,g50)
    c: Coincident(g50,g51)
    c: Coincident(g51,g48)
    c: Vertical(g48)
    c: Vertical(g50)
    c: Horizontal(g49)
    c: Horizontal(g51)
    c: Coincident(g52,g53)
    c: Coincident(g53,g54)
    c: Coincident(g54,g55)
    c: Coincident(g55,g52)
    c: Vertical(g52)
    c: Vertical(g54)
    c: Horizontal(g53)
    c: Horizontal(g55)
    c: Coincident(g56,g57)
    c: Coincident(g57,g58)
    c: Coincident(g58,g59)
    c: Coincident(g59,g56)
    c: Vertical(g56)
    c: Vertical(g58)
    c: Horizontal(g57)
    c: Horizontal(g59)
    c: Coincident(g60,g61)
    c: Coincident(g61,g62)
    c: Coincident(g62,g63)
    c: Coincident(g63,g60)
    c: Vertical(g60)
    c: Vertical(g62)
    c: Horizontal(g61)
    c: Horizontal(g63)
    c: Coincident(g64,g65)
    c: Coincident(g65,g66)
    c: Coincident(g66,g67)
    c: Coincident(g67,g64)
    c: Vertical(g64)
    c: Vertical(g66)
    c: Horizontal(g65)
    c: Horizontal(g67)
    c: Coincident(g68,g69)
    c: Coincident(g69,g70)
    c: Coincident(g70,g71)
    c: Coincident(g71,g68)
    c: Vertical(g68)
    c: Vertical(g70)
    c: Horizontal(g69)
    c: Horizontal(g71)
    c: Coincident(g72,g73)
    c: Coincident(g73,g74)
    c: Coincident(g74,g75)
    c: Coincident(g75,g72)
    c: Vertical(g72)
    c: Vertical(g74)
    c: Horizontal(g73)
    c: Horizontal(g75)
    c: Coincident(g76,g77)
    c: Coincident(g77,g78)
    c: Coincident(g78,g79)
    c: Coincident(g79,g76)
    c: Vertical(g76)
    c: Vertical(g78)
    c: Horizontal(g77)
    c: Horizontal(g79)
    c: Coincident(g80,g81)
    c: Coincident(g81,g82)
    c: Coincident(g82,g83)
    c: Coincident(g83,g80)
    c: Vertical(g80)
    c: Vertical(g82)
    c: Horizontal(g81)
    c: Horizontal(g83)
    c: Coincident(g84,g85)
    c: Coincident(g85,g86)
    c: Coincident(g86,g87)
    c: Coincident(g87,g84)
    c: Vertical(g84)
    c: Vertical(g86)
    c: Horizontal(g85)
    c: Horizontal(g87)
    c: Coincident(g88,g89)
    c: Coincident(g89,g90)
    c: Coincident(g90,g91)
    c: Coincident(g91,g88)
    c: Vertical(g88)
    c: Vertical(g90)
    c: Horizontal(g89)
    c: Horizontal(g91)
    c: Coincident(g92,g93)
    c: Coincident(g93,g94)
    c: Coincident(g94,g95)
    c: Coincident(g95,g92)
    c: Vertical(g92)
    c: Vertical(g94)
    c: Horizontal(g93)
    c: Horizontal(g95)
    c: Horizontal(g0,g-3)
    c: Horizontal(g0,g-4)
    c: Horizontal(g4,g-5)
    c: Horizontal(g4,g-6)
    c: Horizontal(g8,g-7)
    c: Horizontal(g8,g-8)
    c: Horizontal(g12,g-9)
    c: Horizontal(g12,g-10)
    c: Horizontal(g16,g-11)
    c: Horizontal(g16,g-12)
    c: Horizontal(g20,g-13)
    c: Horizontal(g20,g-14)
    c: Horizontal(g24,g-15)
    c: Horizontal(g-16,g24)
    c: Horizontal(g28,g-17)
    c: Horizontal(g28,g-18)
    c: Horizontal(g32,g-19)
    c: Horizontal(g32,g-20)
    c: Horizontal(g36,g-21)
    c: Horizontal(g36,g-22)
    c: Horizontal(g40,g-23)
    c: Horizontal(g40,g-24)
    c: Horizontal(g44,g-25)
    c: Horizontal(g44,g-26)
    c: Horizontal(g48,g-27)
    c: Horizontal(g48,g-28)
    c: Horizontal(g52,g-29)
    c: Horizontal(g52,g-30)
    c: Horizontal(g56,g-31)
    c: Horizontal(g56,g-32)
    c: Horizontal(g60,g-33)
    c: Horizontal(g60,g-34)
    c: Horizontal(g64,g-35)
    c: Horizontal(g64,g-36)
    c: Horizontal(g68,g-37)
    c: Horizontal(g68,g-38)
    c: Horizontal(g72,g-39)
    c: Horizontal(g73,g-41)
    c: Horizontal(g78,g-40)
    c: Horizontal(g76,g-41)
    c: Horizontal(g80,g-42)
    c: Horizontal(g80,g-43)
    c: Horizontal(g84,g-44)
    c: Horizontal(g84,g-45)
    c: Horizontal(g88,g-46)
    c: Horizontal(g89,g-48)
    c: Horizontal(g92,g-48)
    c: Horizontal(g94,g-47)
    c: Vertical(g0,g-3)
    c: Vertical(g2,g-3)
    c: Vertical(g4,g-5)
    c: Vertical(g6,g-5)
    c: Vertical(g8,g-7)
    c: Vertical(g10,g-7)
    c: Vertical(g12,g-9)
    c: Vertical(g14,g-9)
    c: Vertical(g16,g-11)
    c: Vertical(g18,g-11)
    c: Vertical(g20,g-13)
    c: Vertical(g22,g-13)
    c: Vertical(g24,g-15)
    c: Vertical(g26,g-15)
    c: Vertical(g28,g-17)
    c: Vertical(g30,g-17)
    c: Vertical(g32,g-19)
    c: Vertical(g34,g-19)
    c: Vertical(g36,g-21)
    c: Vertical(g38,g-21)
    c: Vertical(g40,g-23)
    c: Vertical(g42,g-23)
    c: Vertical(g44,g-25)
    c: Vertical(g46,g-25)
    c: Vertical(g48,g-27)
    c: Vertical(g50,g-27)
    c: Vertical(g52,g-29)
    c: Vertical(g54,g-29)
    c: Vertical(g56,g-31)
    c: Vertical(g58,g-31)
    c: Vertical(g60,g-33)
    c: Vertical(g62,g-33)
    c: Vertical(g64,g-35)
    c: Vertical(g66,g-35)
    c: Vertical(g68,g-37)
    c: Vertical(g70,g-37)
    c: Vertical(g73,g-41)
    c: Vertical(g72,g-39)
    c: Vertical(g76,g-41)
    c: Vertical(g78,g-40)
    c: Vertical(g82,g-42)
    c: Vertical(g80,g-42)
    c: Vertical(g84,g-44)
    c: Vertical(g86,g-44)
    c: Vertical(g88,g-46)
    c: Vertical(g89,g-48)
    c: Vertical(g94,g-47)
    c: Vertical(g92,g-48)
FEATURE [PartDesign::Pocket] Pocket067  label="BL-DiodeLEDGap-Pocket"
  BaseFeature = -> Pocket014
  Direction = (0,0,-1)
  Length = 1.2
  Length2 = 5
  Profile = -> Sketch101
  ReferenceAxis = -> Sketch101 [N_Axis]
  Refine = true
  Suppressed = false
  Type = 0
  expr: Length = VarSet.Bottom_DiodeLedGapMerge == True ? VarSet.Bottom_LedZ : 0.001 mm
FEATURE [PartDesign::Pocket] Pocket022  label="BL-Resistor-Pocket"
  BaseFeature = -> Pocket067
  Direction = (0,0,-1)
  Length = 0.9
  Length2 = 5
  Profile = -> Sketch041
  ReferenceAxis = -> Sketch041 [N_Axis]
  Refine = true
  Suppressed = false
  Type = 0
  expr: Length = VarSet.Bottom_ResistorZ
FEATURE [PartDesign::Pocket] Pocket020  label="BL-MCU-Pocket"
  BaseFeature = -> Pocket022
  Direction = (0,0,-1)
  Length = 1.3
  Length2 = 5
  Profile = -> Sketch035
  ReferenceAxis = -> Sketch035 [N_Axis]
  Refine = true
  Suppressed = false
  Type = 0
  expr: Length = VarSet.Bottom_McuZ
  expr: TaperAngle = VarSet.Bottom_McuContactTaper
FEATURE [PartDesign::Pocket] Pocket018  label="BL-Connector-Pocket"
  BaseFeature = -> Pocket020
  Direction = (0,0,-1)
  Length = 1.7
  Length2 = 5
  Profile = -> Sketch033
  ReferenceAxis = -> Sketch033 [N_Axis]
  Refine = true
  Suppressed = false
  Type = 0
  expr: Length = VarSet.Bottom_ConnectorZ
FEATURE [PartDesign::Pad] Pad026  label="BL-LipFrame-Pad"
  BaseFeature = -> Pocket018
  Direction = (0,0,1)
  Length = 0.75
  Length2 = 10
  Profile = -> Sketch017
  ReferenceAxis = -> Sketch017 [N_Axis]
  Refine = true
  Suppressed = false
  Type = 0
  expr: Length = VarSet.Top_PcbZ / 2
FEATURE [PartDesign::Pocket] Pocket051  label="BL-LipPCB-Pocket"
  BaseFeature = -> Pad026
  Direction = (0,0,-1)
  Length = 0.75
  Length2 = 5
  Profile = -> Sketch070
  ReferenceAxis = -> Sketch070 [N_Axis]
  Refine = true
  Reversed = true
  Suppressed = false
  Type = 0
  expr: Length = VarSet.Top_PcbZ / 2
FEATURE [PartDesign::Pad] Pad024  label="BL-ScrewPostOut-Pad"
  BaseFeature = -> Pocket051
  Direction = (0,0,1)
  Length = 0.75
  Length2 = 10
  Profile = -> Sketch072
  ReferenceAxis = -> Sketch072 [N_Axis]
  Refine = true
  Suppressed = false
  Type = 0
  expr: Length = VarSet.Top_PcbZ / 2
FEATURE [PartDesign::Pocket] Pocket024  label="BL-ScrewClearance-Pocket"
  BaseFeature = -> Pad024
  Direction = (0,0,-1)
  Length = 5
  Length2 = 5
  Profile = -> Sketch043
  ReferenceAxis = -> Sketch043 [N_Axis]
  Refine = true
  Suppressed = false
  Type = 1
FEATURE [PartDesign::Pocket] Pocket041  label="BL-ScrewRecess-Pocket"
  BaseFeature = -> Pocket024
  Direction = (0,0,-1)
  Length = 1.5
  Length2 = 5
  Profile = -> Sketch065
  ReferenceAxis = -> Sketch065 [N_Axis]
  Refine = true
  Reversed = true
  Suppressed = false
  Type = 0
  expr: Length = VarSet.Screw_RecessZ
FEATURE [PartDesign::Body] Body001  label="BottomLeft"
  AllowCompound = false
  Group = -> [Pad010,Fillet004,Sketch029,Sketch033,Sketch065,Pocket004,Pocket007,Pocket016,Pocket010,Pocket011,Pocket014,Pocket067,Sketch101,Pocket022,Sketch041,Pocket020,Pocket018,Sketch072,Pad026,Pocket051,Pad024,Sketch035,Sketch043,Sketch030,Sketch021,Sketch022,Sketch023,Sketch017,Sketch018,Sketch070,Pocket024,Pocket041,Sketch088]
  Origin = -> Origin001
  Tip = -> Pocket024
FEATURE [PartDesign::ShapeBinder] ShapeBinder  label="ML-BottomLeft"
  Support = -> [Body001]
  TraceSupport = false
FEATURE [PartDesign::Boolean] Boolean  label="ML-Mold-Boolean"
  BaseFeature = -> Pocket063
  Group = -> [ShapeBinder]
  Refine = true
  Suppressed = false
  Type = 1
  UsePlacement = true
FEATURE [PartDesign::Body] Body008  label="MoldLeft"
  AllowCompound = false
  Group = -> [Sketch094,Pad028,Pocket063,Boolean,Sketch095]
  Origin = -> Origin008
  Tip = -> Boolean
FEATURE [Sketcher::SketchObject] Sketch102  label="BR-DiodeLEDGap"
  ArcFitTolerance = 1e-06
  AttachmentSupport = -> [XY_Plane003]
  ExternalGeometry = -> [Sketch031,Sketch027]
  FullyConstrained = true
  MakeInternals = false
  MapMode = 5
  sketch-geometry (96):
    g0: LineSegment StartX=35 StartY=25.75 StartZ=0 EndX=35 EndY=25.35 EndZ=0
    g1: LineSegment StartX=35 StartY=25.35 StartZ=0 EndX=40.7 EndY=25.35 EndZ=0
    g2: LineSegment StartX=40.7 StartY=25.35 StartZ=0 EndX=40.7 EndY=25.75 EndZ=0
    g3: LineSegment StartX=40.7 StartY=25.75 StartZ=0 EndX=35 EndY=25.75 EndZ=0
    g4: LineSegment StartX=54.05 StartY=25.75 StartZ=0 EndX=54.05 EndY=25.35 EndZ=0
    g5: LineSegment StartX=54.05 StartY=25.35 StartZ=0 EndX=59.75 EndY=25.35 EndZ=0
    g6: LineSegment StartX=59.75 StartY=25.35 StartZ=0 EndX=59.75 EndY=25.75 EndZ=0
    g7: LineSegment StartX=59.75 StartY=25.75 StartZ=0 EndX=54.05 EndY=25.75 EndZ=0
    g8: LineSegment StartX=73.1 StartY=25.75 StartZ=0 EndX=73.1 EndY=25.35 EndZ=0
    g9: LineSegment StartX=73.1 StartY=25.35 StartZ=0 EndX=78.8 EndY=25.35 EndZ=0
    g10: LineSegment StartX=78.8 StartY=25.35 StartZ=0 EndX=78.8 EndY=25.75 EndZ=0
    g11: LineSegment StartX=78.8 StartY=25.75 StartZ=0 EndX=73.1 EndY=25.75 EndZ=0
    g12: LineSegment StartX=92.15 StartY=25.75 StartZ=0 EndX=92.15 EndY=25.35 EndZ=0
    g13: LineSegment StartX=92.15 StartY=25.35 StartZ=0 EndX=97.85 EndY=25.35 EndZ=0
    g14: LineSegment StartX=97.85 StartY=25.35 StartZ=0 EndX=97.85 EndY=25.75 EndZ=0
    g15: LineSegment StartX=97.85 StartY=25.75 StartZ=0 EndX=92.15 EndY=25.75 EndZ=0
    g16: LineSegment StartX=111.2 StartY=25.75 StartZ=0 EndX=111.2 EndY=25.35 EndZ=0
    g17: LineSegment StartX=111.2 StartY=25.35 StartZ=0 EndX=116.9 EndY=25.35 EndZ=0
    g18: LineSegment StartX=116.9 StartY=25.35 StartZ=0 EndX=116.9 EndY=25.75 EndZ=0
    g19: LineSegment StartX=116.9 StartY=25.75 StartZ=0 EndX=111.2 EndY=25.75 EndZ=0
    g20: LineSegment StartX=130.25 StartY=25.75 StartZ=0 EndX=130.25 EndY=25.35 EndZ=0
    g21: LineSegment StartX=130.25 StartY=25.35 StartZ=0 EndX=135.95 EndY=25.35 EndZ=0
    g22: LineSegment StartX=135.95 StartY=25.35 StartZ=0 EndX=135.95 EndY=25.75 EndZ=0
    g23: LineSegment StartX=135.95 StartY=25.75 StartZ=0 EndX=130.25 EndY=25.75 EndZ=0
    g24: LineSegment StartX=35 StartY=44.8 StartZ=0 EndX=35 EndY=44.4 EndZ=0
    g25: LineSegment StartX=35 StartY=44.4 StartZ=0 EndX=40.7 EndY=44.4 EndZ=0
    g26: LineSegment StartX=40.7 StartY=44.4 StartZ=0 EndX=40.7 EndY=44.8 EndZ=0
    g27: LineSegment StartX=40.7 StartY=44.8 StartZ=0 EndX=35 EndY=44.8 EndZ=0
    g28: LineSegment StartX=54.05 StartY=44.8 StartZ=0 EndX=54.05 EndY=44.4 EndZ=0
    g29: LineSegment StartX=54.05 StartY=44.4 StartZ=0 EndX=59.75 EndY=44.4 EndZ=0
    g30: LineSegment StartX=59.75 StartY=44.4 StartZ=0 EndX=59.75 EndY=44.8 EndZ=0
    g31: LineSegment StartX=59.75 StartY=44.8 StartZ=0 EndX=54.05 EndY=44.8 EndZ=0
    g32: LineSegment StartX=73.1 StartY=44.8 StartZ=0 EndX=73.1 EndY=44.4 EndZ=0
    g33: LineSegment StartX=73.1 StartY=44.4 StartZ=0 EndX=78.8 EndY=44.4 EndZ=0
    g34: LineSegment StartX=78.8 StartY=44.4 StartZ=0 EndX=78.8 EndY=44.8 EndZ=0
    g35: LineSegment StartX=78.8 StartY=44.8 StartZ=0 EndX=73.1 EndY=44.8 EndZ=0
    g36: LineSegment StartX=92.15 StartY=44.8 StartZ=0 EndX=92.15 EndY=44.4 EndZ=0
    g37: LineSegment StartX=92.15 StartY=44.4 StartZ=0 EndX=97.85 EndY=44.4 EndZ=0
    g38: LineSegment StartX=97.85 StartY=44.4 StartZ=0 EndX=97.85 EndY=44.8 EndZ=0
    g39: LineSegment StartX=97.85 StartY=44.8 StartZ=0 EndX=92.15 EndY=44.8 EndZ=0
    g40: LineSegment StartX=111.2 StartY=44.8 StartZ=0 EndX=111.2 EndY=44.4 EndZ=0
    g41: LineSegment StartX=111.2 StartY=44.4 StartZ=0 EndX=116.9 EndY=44.4 EndZ=0
    g42: LineSegment StartX=116.9 StartY=44.4 StartZ=0 EndX=116.9 EndY=44.8 EndZ=0
    g43: LineSegment StartX=116.9 StartY=44.8 StartZ=0 EndX=111.2 EndY=44.8 EndZ=0
    g44: LineSegment StartX=130.25 StartY=44.8 StartZ=0 EndX=130.25 EndY=44.4 EndZ=0
    g45: LineSegment StartX=130.25 StartY=44.4 StartZ=0 EndX=135.95 EndY=44.4 EndZ=0
    g46: LineSegment StartX=135.95 StartY=44.4 StartZ=0 EndX=135.95 EndY=44.8 EndZ=0
    g47: LineSegment StartX=135.95 StartY=44.8 StartZ=0 EndX=130.25 EndY=44.8 EndZ=0
    g48: LineSegment StartX=35 StartY=63.85 StartZ=0 EndX=35 EndY=63.45 EndZ=0
    g49: LineSegment StartX=35 StartY=63.45 StartZ=0 EndX=40.7 EndY=63.45 EndZ=0
    g50: LineSegment StartX=40.7 StartY=63.45 StartZ=0 EndX=40.7 EndY=63.85 EndZ=0
    g51: LineSegment StartX=40.7 StartY=63.85 StartZ=0 EndX=35 EndY=63.85 EndZ=0
    g52: LineSegment StartX=54.05 StartY=63.85 StartZ=0 EndX=54.05 EndY=63.45 EndZ=0
    g53: LineSegment StartX=54.05 StartY=63.45 StartZ=0 EndX=59.75 EndY=63.45 EndZ=0
    g54: LineSegment StartX=59.75 StartY=63.45 StartZ=0 EndX=59.75 EndY=63.85 EndZ=0
    g55: LineSegment StartX=59.75 StartY=63.85 StartZ=0 EndX=54.05 EndY=63.85 EndZ=0
    g56: LineSegment StartX=73.1 StartY=63.85 StartZ=0 EndX=73.1 EndY=63.45 EndZ=0
    g57: LineSegment StartX=73.1 StartY=63.45 StartZ=0 EndX=78.8 EndY=63.45 EndZ=0
    g58: LineSegment StartX=78.8 StartY=63.45 StartZ=0 EndX=78.8 EndY=63.85 EndZ=0
    g59: LineSegment StartX=78.8 StartY=63.85 StartZ=0 EndX=73.1 EndY=63.85 EndZ=0
    g60: LineSegment StartX=92.15 StartY=63.85 StartZ=0 EndX=92.15 EndY=63.45 EndZ=0
    g61: LineSegment StartX=92.15 StartY=63.45 StartZ=0 EndX=97.85 EndY=63.45 EndZ=0
    g62: LineSegment StartX=97.85 StartY=63.45 StartZ=0 EndX=97.85 EndY=63.85 EndZ=0
    g63: LineSegment StartX=97.85 StartY=63.85 StartZ=0 EndX=92.15 EndY=63.85 EndZ=0
    g64: LineSegment StartX=111.2 StartY=63.85 StartZ=0 EndX=111.2 EndY=63.45 EndZ=0
    g65: LineSegment StartX=111.2 StartY=63.45 StartZ=0 EndX=116.9 EndY=63.45 EndZ=0
    g66: LineSegment StartX=116.9 StartY=63.45 StartZ=0 EndX=116.9 EndY=63.85 EndZ=0
    g67: LineSegment StartX=116.9 StartY=63.85 StartZ=0 EndX=111.2 EndY=63.85 EndZ=0
    g68: LineSegment StartX=130.25 StartY=63.85 StartZ=0 EndX=130.25 EndY=63.45 EndZ=0
    g69: LineSegment StartX=130.25 StartY=63.45 StartZ=0 EndX=135.95 EndY=63.45 EndZ=0
    g70: LineSegment StartX=135.95 StartY=63.45 StartZ=0 EndX=135.95 EndY=63.85 EndZ=0
    g71: LineSegment StartX=135.95 StartY=63.85 StartZ=0 EndX=130.25 EndY=63.85 EndZ=0
    g72: LineSegment StartX=53.15 StartY=82.9 StartZ=0 EndX=53.15 EndY=82.5 EndZ=0
    g73: LineSegment StartX=53.15 StartY=82.5 StartZ=0 EndX=53.375 EndY=82.5 EndZ=0
    g74: LineSegment StartX=53.375 StartY=82.5 StartZ=0 EndX=53.375 EndY=82.9 EndZ=0
    g75: LineSegment StartX=53.375 StartY=82.9 StartZ=0 EndX=53.15 EndY=82.9 EndZ=0
    g76: LineSegment StartX=60.425 StartY=82.9 StartZ=0 EndX=60.425 EndY=82.5 EndZ=0
    g77: LineSegment StartX=60.425 StartY=82.5 StartZ=0 EndX=61.15 EndY=82.5 EndZ=0
    g78: LineSegment StartX=61.15 StartY=82.5 StartZ=0 EndX=61.15 EndY=82.9 EndZ=0
    g79: LineSegment StartX=61.15 StartY=82.9 StartZ=0 EndX=60.425 EndY=82.9 EndZ=0
    g80: LineSegment StartX=73.1 StartY=82.9 StartZ=0 EndX=73.1 EndY=82.5 EndZ=0
    g81: LineSegment StartX=73.1 StartY=82.5 StartZ=0 EndX=78.8 EndY=82.5 EndZ=0
    g82: LineSegment StartX=78.8 StartY=82.5 StartZ=0 EndX=78.8 EndY=82.9 EndZ=0
    g83: LineSegment StartX=78.8 StartY=82.9 StartZ=0 EndX=73.1 EndY=82.9 EndZ=0
    g84: LineSegment StartX=92.15 StartY=82.9 StartZ=0 EndX=92.15 EndY=82.5 EndZ=0
    g85: LineSegment StartX=92.15 StartY=82.5 StartZ=0 EndX=97.85 EndY=82.5 EndZ=0
    g86: LineSegment StartX=97.85 StartY=82.5 StartZ=0 EndX=97.85 EndY=82.9 EndZ=0
    g87: LineSegment StartX=97.85 StartY=82.9 StartZ=0 EndX=92.15 EndY=82.9 EndZ=0
    g88: LineSegment StartX=110.3 StartY=82.9 StartZ=0 EndX=110.3 EndY=82.5 EndZ=0
    g89: LineSegment StartX=110.3 StartY=82.5 StartZ=0 EndX=110.525 EndY=82.5 EndZ=0
    g90: LineSegment StartX=110.525 StartY=82.5 StartZ=0 EndX=110.525 EndY=82.9 EndZ=0
    g91: LineSegment StartX=110.525 StartY=82.9 StartZ=0 EndX=110.3 EndY=82.9 EndZ=0
    g92: LineSegment StartX=117.575 StartY=82.9 StartZ=0 EndX=117.575 EndY=82.5 EndZ=0
    g93: LineSegment StartX=117.575 StartY=82.5 StartZ=0 EndX=118.3 EndY=82.5 EndZ=0
    g94: LineSegment StartX=118.3 StartY=82.5 StartZ=0 EndX=118.3 EndY=82.9 EndZ=0
    g95: LineSegment StartX=118.3 StartY=82.9 StartZ=0 EndX=117.575 EndY=82.9 EndZ=0
  constraints (288):
    c: Coincident(g0,g1)
    c: Coincident(g1,g2)
    c: Coincident(g2,g3)
    c: Coincident(g3,g0)
    c: Vertical(g0)
    c: Vertical(g2)
    c: Horizontal(g1)
    c: Horizontal(g3)
    c: Coincident(g4,g5)
    c: Coincident(g5,g6)
    c: Coincident(g6,g7)
    c: Coincident(g7,g4)
    c: Vertical(g4)
    c: Vertical(g6)
    c: Horizontal(g5)
    c: Horizontal(g7)
    c: Coincident(g8,g9)
    c: Coincident(g9,g10)
    c: Coincident(g10,g11)
    c: Coincident(g11,g8)
    c: Vertical(g8)
    c: Vertical(g10)
    c: Horizontal(g9)
    c: Horizontal(g11)
    c: Coincident(g12,g13)
    c: Coincident(g13,g14)
    c: Coincident(g14,g15)
    c: Coincident(g15,g12)
    c: Vertical(g12)
    c: Vertical(g14)
    c: Horizontal(g13)
    c: Horizontal(g15)
    c: Coincident(g16,g17)
    c: Coincident(g17,g18)
    c: Coincident(g18,g19)
    c: Coincident(g19,g16)
    c: Vertical(g16)
    c: Vertical(g18)
    c: Horizontal(g17)
    c: Horizontal(g19)
    c: Coincident(g20,g21)
    c: Coincident(g21,g22)
    c: Coincident(g22,g23)
    c: Coincident(g23,g20)
    c: Vertical(g20)
    c: Vertical(g22)
    c: Horizontal(g21)
    c: Horizontal(g23)
    c: Coincident(g24,g25)
    c: Coincident(g25,g26)
    c: Coincident(g26,g27)
    c: Coincident(g27,g24)
    c: Vertical(g24)
    c: Vertical(g26)
    c: Horizontal(g25)
    c: Horizontal(g27)
    c: Coincident(g28,g29)
    c: Coincident(g29,g30)
    c: Coincident(g30,g31)
    c: Coincident(g31,g28)
    c: Vertical(g28)
    c: Vertical(g30)
    c: Horizontal(g29)
    c: Horizontal(g31)
    c: Coincident(g32,g33)
    c: Coincident(g33,g34)
    c: Coincident(g34,g35)
    c: Coincident(g35,g32)
    c: Vertical(g32)
    c: Vertical(g34)
    c: Horizontal(g33)
    c: Horizontal(g35)
    c: Coincident(g36,g37)
    c: Coincident(g37,g38)
    c: Coincident(g38,g39)
    c: Coincident(g39,g36)
    c: Vertical(g36)
    c: Vertical(g38)
    c: Horizontal(g37)
    c: Horizontal(g39)
    c: Coincident(g40,g41)
    c: Coincident(g41,g42)
    c: Coincident(g42,g43)
    c: Coincident(g43,g40)
    c: Vertical(g40)
    c: Vertical(g42)
    c: Horizontal(g41)
    c: Horizontal(g43)
    c: Coincident(g44,g45)
    c: Coincident(g45,g46)
    c: Coincident(g46,g47)
    c: Coincident(g47,g44)
    c: Vertical(g44)
    c: Vertical(g46)
    c: Horizontal(g45)
    c: Horizontal(g47)
    c: Coincident(g48,g49)
    c: Coincident(g49,g50)
    c: Coincident(g50,g51)
    c: Coincident(g51,g48)
    c: Vertical(g48)
    c: Vertical(g50)
    c: Horizontal(g49)
    c: Horizontal(g51)
    c: Coincident(g52,g53)
    c: Coincident(g53,g54)
    c: Coincident(g54,g55)
    c: Coincident(g55,g52)
    c: Vertical(g52)
    c: Vertical(g54)
    c: Horizontal(g53)
    c: Horizontal(g55)
    c: Coincident(g56,g57)
    c: Coincident(g57,g58)
    c: Coincident(g58,g59)
    c: Coincident(g59,g56)
    c: Vertical(g56)
    c: Vertical(g58)
    c: Horizontal(g57)
    c: Horizontal(g59)
    c: Coincident(g60,g61)
    c: Coincident(g61,g62)
    c: Coincident(g62,g63)
    c: Coincident(g63,g60)
    c: Vertical(g60)
    c: Vertical(g62)
    c: Horizontal(g61)
    c: Horizontal(g63)
    c: Coincident(g64,g65)
    c: Coincident(g65,g66)
    c: Coincident(g66,g67)
    c: Coincident(g67,g64)
    c: Vertical(g64)
    c: Vertical(g66)
    c: Horizontal(g65)
    c: Horizontal(g67)
    c: Coincident(g68,g69)
    c: Coincident(g69,g70)
    c: Coincident(g70,g71)
    c: Coincident(g71,g68)
    c: Vertical(g68)
    c: Vertical(g70)
    c: Horizontal(g69)
    c: Horizontal(g71)
    c: Coincident(g72,g73)
    c: Coincident(g73,g74)
    c: Coincident(g74,g75)
    c: Coincident(g75,g72)
    c: Vertical(g72)
    c: Vertical(g74)
    c: Horizontal(g73)
    c: Horizontal(g75)
    c: Coincident(g76,g77)
    c: Coincident(g77,g78)
    c: Coincident(g78,g79)
    c: Coincident(g79,g76)
    c: Vertical(g76)
    c: Vertical(g78)
    c: Horizontal(g77)
    c: Horizontal(g79)
    c: Coincident(g80,g81)
    c: Coincident(g81,g82)
    c: Coincident(g82,g83)
    c: Coincident(g83,g80)
    c: Vertical(g80)
    c: Vertical(g82)
    c: Horizontal(g81)
    c: Horizontal(g83)
    c: Coincident(g84,g85)
    c: Coincident(g85,g86)
    c: Coincident(g86,g87)
    c: Coincident(g87,g84)
    c: Vertical(g84)
    c: Vertical(g86)
    c: Horizontal(g85)
    c: Horizontal(g87)
    c: Coincident(g88,g89)
    c: Coincident(g89,g90)
    c: Coincident(g90,g91)
    c: Coincident(g91,g88)
    c: Vertical(g88)
    c: Vertical(g90)
    c: Horizontal(g89)
    c: Horizontal(g91)
    c: Coincident(g92,g93)
    c: Coincident(g93,g94)
    c: Coincident(g94,g95)
    c: Coincident(g95,g92)
    c: Vertical(g92)
    c: Vertical(g94)
    c: Horizontal(g93)
    c: Horizontal(g95)
    c: Horizontal(g0,g-3)
    c: Horizontal(g0,g-4)
    c: Horizontal(g4,g-5)
    c: Horizontal(g4,g-6)
    c: Horizontal(g8,g-7)
    c: Horizontal(g-8,g8)
    c: Horizontal(g12,g-9)
    c: Horizontal(g12,g-10)
    c: Horizontal(g16,g-11)
    c: Horizontal(g16,g-12)
    c: Horizontal(g20,g-13)
    c: Horizontal(g20,g-14)
    c: Horizontal(g24,g-15)
    c: Horizontal(g24,g-16)
    c: Horizontal(g28,g-17)
    c: Horizontal(g28,g-18)
    c: Horizontal(g32,g-19)
    c: Horizontal(g32,g-20)
    c: Horizontal(g36,g-21)
    c: Horizontal(g36,g-22)
    c: Horizontal(g40,g-23)
    c: Horizontal(g40,g-24)
    c: Horizontal(g44,g-25)
    c: Horizontal(g44,g-26)
    c: Horizontal(g48,g-27)
    c: Horizontal(g48,g-28)
    c: Horizontal(g52,g-29)
    c: Horizontal(g52,g-30)
    c: Horizontal(g56,g-31)
    c: Horizontal(g56,g-32)
    c: Horizontal(g60,g-33)
    c: Horizontal(g60,g-34)
    c: Horizontal(g64,g-35)
    c: Horizontal(g64,g-36)
    c: Horizontal(g68,g-37)
    c: Horizontal(g68,g-38)
    c: Horizontal(g74,g-39)
    c: Horizontal(g72,g-41)
    c: Horizontal(g76,g-40)
    c: Horizontal(g77,g-41)
    c: Horizontal(g80,g-42)
    c: Horizontal(g80,g-43)
    c: Horizontal(g84,g-44)
    c: Horizontal(g-45,g84)
    c: Horizontal(g90,g-46)
    c: Horizontal(g88,g-48)
    c: Horizontal(g92,g-47)
    c: Horizontal(g93,g-48)
    c: Vertical(g0,g-3)
    c: Vertical(g2,g-3)
    c: Vertical(g4,g-5)
    c: Vertical(g6,g-5)
    c: Vertical(g-7,g8)
    c: Vertical(g10,g-7)
    c: Vertical(g12,g-9)
    c: Vertical(g14,g-9)
    c: Vertical(g16,g-11)
    c: Vertical(g18,g-11)
    c: Vertical(g20,g-13)
    c: Vertical(g22,g-13)
    c: Vertical(g24,g-15)
    c: Vertical(g26,g-15)
    c: Vertical(g-17,g28)
    c: Vertical(g30,g-17)
    c: Vertical(g-19,g32)
    c: Vertical(g34,g-19)
    c: Vertical(g-21,g36)
    c: Vertical(g38,g-21)
    c: Vertical(g-23,g40)
    c: Vertical(g42,g-23)
    c: Vertical(g-25,g44)
    c: Vertical(g46,g-25)
    c: Vertical(g-27,g48)
    c: Vertical(g50,g-27)
    c: Vertical(g52,g-29)
    c: Vertical(g54,g-29)
    c: Vertical(g56,g-31)
    c: Vertical(g58,g-31)
    c: Vertical(g60,g-33)
    c: Vertical(g62,g-33)
    c: Vertical(g64,g-35)
    c: Vertical(g66,g-35)
    c: Vertical(g68,g-37)
    c: Vertical(g70,g-37)
    c: Vertical(g74,g-39)
    c: Vertical(g72,g-41)
    c: Vertical(g76,g-40)
    c: Vertical(g-41,g77)
    c: Vertical(g80,g-42)
    c: Vertical(g82,g-42)
    c: Vertical(g84,g-44)
    c: Vertical(g86,g-44)
    c: Vertical(g90,g-46)
    c: Vertical(g88,g-48)
    c: Vertical(g92,g-47)
    c: Vertical(g93,g-48)
FEATURE [PartDesign::Pocket] Pocket068  label="BR-DiodeLEDGap-Pocket"
  BaseFeature = -> Pocket015
  Direction = (0,0,-1)
  Length = 1.2
  Length2 = 5
  Profile = -> Sketch102
  ReferenceAxis = -> Sketch102 [N_Axis]
  Refine = true
  Suppressed = false
  Type = 0
  expr: Length = VarSet.Bottom_DiodeLedGapMerge == True ? VarSet.Bottom_LedZ : 0.001 mm
FEATURE [PartDesign::Pocket] Pocket023  label="BR-Resistor-Pocket"
  BaseFeature = -> Pocket068
  Direction = (0,0,-1)
  Length = 0.9
  Length2 = 5
  Profile = -> Sketch042
  ReferenceAxis = -> Sketch042 [N_Axis]
  Refine = true
  Suppressed = false
  Type = 0
  expr: Length = VarSet.Bottom_ResistorZ
FEATURE [PartDesign::Pocket] Pocket021  label="BR-MCU-Pocket"
  BaseFeature = -> Pocket023
  Direction = (0,0,-1)
  Length = 1.3
  Length2 = 5
  Profile = -> Sketch037
  ReferenceAxis = -> Sketch037 [N_Axis]
  Refine = true
  Suppressed = false
  Type = 0
  expr: Length = VarSet.Bottom_McuZ
  expr: TaperAngle = VarSet.Bottom_McuContactTaper
FEATURE [PartDesign::Pocket] Pocket019  label="BR-Connector-Pocket"
  BaseFeature = -> Pocket021
  Direction = (0,0,-1)
  Length = 1.7
  Length2 = 5
  Profile = -> Sketch034
  ReferenceAxis = -> Sketch034 [N_Axis]
  Refine = true
  Suppressed = false
  Type = 0
  expr: Length = VarSet.Bottom_ConnectorZ
FEATURE [PartDesign::Pad] Pad027  label="BR-LipFrame-Pad"
  BaseFeature = -> Pocket019
  Direction = (0,0,1)
  Length = 0.75
  Length2 = 10
  Profile = -> Sketch024
  ReferenceAxis = -> Sketch024 [N_Axis]
  Refine = true
  Suppressed = false
  Type = 0
  expr: Length = VarSet.Top_PcbZ / 2
FEATURE [PartDesign::Pocket] Pocket052  label="BR-LipPCB-Pocket"
  BaseFeature = -> Pad027
  Direction = (0,0,-1)
  Length = 0.75
  Length2 = 5
  Profile = -> Sketch071
  ReferenceAxis = -> Sketch071 [N_Axis]
  Refine = true
  Reversed = true
  Suppressed = false
  Type = 0
  expr: Length = VarSet.Top_PcbZ / 2
FEATURE [PartDesign::Pad] Pad025  label="BR-ScrewPostOut-Pad"
  BaseFeature = -> Pocket052
  Direction = (0,0,1)
  Length = 0.75
  Length2 = 10
  Profile = -> Sketch073
  ReferenceAxis = -> Sketch073 [N_Axis]
  Refine = true
  Suppressed = false
  Type = 0
  expr: Length = VarSet.Top_PcbZ / 2
FEATURE [PartDesign::Pocket] Pocket025  label="BR-ScrewClearance-Pocket"
  BaseFeature = -> Pad025
  Direction = (0,0,-1)
  Length = 5
  Length2 = 5
  Profile = -> Sketch044
  ReferenceAxis = -> Sketch044 [N_Axis]
  Refine = true
  Suppressed = false
  Type = 1
FEATURE [PartDesign::Pocket] Pocket042  label="BR-ScrewRecess-Pocket"
  BaseFeature = -> Pocket025
  Direction = (0,0,-1)
  Length = 1.5
  Length2 = 5
  Profile = -> Sketch066
  ReferenceAxis = -> Sketch066 [N_Axis]
  Refine = true
  Reversed = true
  Suppressed = false
  Type = 0
  expr: Length = VarSet.Screw_RecessZ
FEATURE [PartDesign::Body] Body003  label="BottomRight"
  AllowCompound = false
  Group = -> [Sketch024,Pad011,Fillet005,Sketch025,Pocket008,Sketch026,Pocket009,Pocket017,Sketch027,Sketch028,Pocket012,Pocket013,Pocket015,Pocket068,Pocket023,Pocket021,Sketch031,Sketch032,Sketch034,Pocket019,Pad027,Pocket052,Sketch071,Sketch037,Sketch042,Sketch044,Sketch066,Sketch073,Pad025,Pocket025,Sketch102,Pocket042,Sketch089]
  Origin = -> Origin003
  Tip = -> Pocket025
FEATURE [PartDesign::ShapeBinder] ShapeBinder001  label="MR-BottomRight"
  Support = -> [Body003]
  TraceSupport = false
FEATURE [PartDesign::Boolean] Boolean001  label="MR-Mold-Boolean"
  BaseFeature = -> Pocket064
  Group = -> [ShapeBinder001]
  Refine = true
  Suppressed = false
  Type = 1
  UsePlacement = true
FEATURE [PartDesign::Body] Body009  label="MoldRight"
  AllowCompound = false
  Group = -> [Sketch096,Pad029,Sketch097,Pocket064,Boolean001]
  Origin = -> Origin009
  Tip = -> Boolean001
FEATURE [Sketcher::SketchObject] Sketch103  label="CL-USB"
  ArcFitTolerance = 1e-06
  AttachmentSupport = -> [XY_Plane004]
  FullyConstrained = true
  MakeInternals = false
  MapMode = 5
  expr: Constraints[14] = 3 * 19.05 mm
  expr: Constraints[19] = 2.5 * 19.05 mm + VarSet.Top_PcbY / 2
  expr: Constraints[20] = VarSet.Cover_McuRearAdd
  sketch-geometry (9):
    g0: LineSegment StartX=-13.05 StartY=90.2 StartZ=0 EndX=-25.05 EndY=90.2 EndZ=0
    g1: LineSegment StartX=-25.05 StartY=90.2 StartZ=0 EndX=-25.05 EndY=85.875 EndZ=0
    g2: LineSegment StartX=-25.05 StartY=85.875 StartZ=0 EndX=-13.05 EndY=85.875 EndZ=0
    g3: LineSegment StartX=-13.05 StartY=85.875 StartZ=0 EndX=-13.05 EndY=90.2 EndZ=0
    g4: GeomPoint [constr] X=-19.05 Y=88.0375 Z=0
    g5: GeomPoint X=-19.05 Y=19.05 Z=0
    g6: GeomPoint X=-38.1 Y=19.05 Z=0
    g7: GeomPoint X=-38.1 Y=76.2 Z=0
    g8: GeomPoint X=-38.1 Y=85.375 Z=0
  constraints (21):
    c: Coincident(g0,g1)
    c: Coincident(g1,g2)
    c: Coincident(g2,g3)
    c: Coincident(g3,g0)
    c: Horizontal(g0)
    c: Horizontal(g2)
    c: Vertical(g1)
    c: Vertical(g3)
    c: Symmetric(g2,g0,g4)
    c: DistanceX(g0,g0) = 12
    c: Horizontal(g6,g5)
    c: Vertical(g6,g7)
    c: DistanceX(g5,g-1) = 19.05
    c: DistanceX(g6,g5) = 19.05
    c: DistanceY(g6,g7) = 57.15
    c: DistanceY(g7,g0) = 14
    c: DistanceY(g-1,g5) = 19.05
    c: Vertical(g4,g5)
    c: Vertical(g8,g7)
    c: DistanceY(g-1,g8) = 85.375
    c: DistanceY(g8,g1) = 0.5
FEATURE [PartDesign::Pocket] Pocket069  label="CL-USB-Pocket"
  BaseFeature = -> Pocket029
  Direction = (0,0,-1)
  Length = 6.75
  Length2 = 5
  Profile = -> Sketch103
  ReferenceAxis = -> Sketch103 [N_Axis]
  Refine = true
  Reversed = true
  Suppressed = false
  Type = 0
  expr: Length = VarSet.Top_PcbZ / 2 + VarSet.Cover_InZ + VarSet.Cover_McuContactZ
FEATURE [PartDesign::Pocket] Pocket028  label="CL-PCB-Pocket"
  BaseFeature = -> Pocket069
  Direction = (0,0,-1)
  Length = 1.5
  Length2 = 5
  Profile = -> Sketch047
  ReferenceAxis = -> Sketch047 [N_Axis]
  Refine = true
  Reversed = true
  Suppressed = false
  Type = 0
  expr: Length = VarSet.Top_PcbZ
FEATURE [PartDesign::Pocket] Pocket033  label="CL-MCU-Pocket"
  BaseFeature = -> Pocket028
  Direction = (0,0,-1)
  Length = 6.75
  Length2 = 5
  Profile = -> Sketch059
  ReferenceAxis = -> Sketch059 [N_Axis]
  Refine = true
  Reversed = true
  Suppressed = false
  Type = 0
  expr: Length = VarSet.Top_PcbZ / 2 + VarSet.Cover_InZ + VarSet.Cover_McuContactZ
FEATURE [PartDesign::Fillet] Fillet010  label="CL-MCUPin-Fillet"
  Base = -> Pocket033 [Edge371,Edge372,Edge373,Edge374,Edge375,Edge376,Edge377,Edge378,Edge379,Edge380,Edge381,Edge382]
  BaseFeature = -> Pocket033
  Radius = 1
  Refine = true
  SupportTransform = false
  Suppressed = false
  UseAllEdges = false
FEATURE [PartDesign::Pocket] Pocket057  label="CL-MCULED-Pocket"
  BaseFeature = -> Fillet010
  Direction = (0,0,-1)
  Length = 6.75
  Length2 = 5
  Profile = -> Sketch086
  ReferenceAxis = -> Sketch086 [N_Axis]
  Refine = true
  Reversed = true
  Suppressed = false
  Type = 0
  expr: Length = VarSet.Top_PcbZ / 2 + VarSet.Cover_InZ + VarSet.Cover_McuContactZ
FEATURE [PartDesign::Pocket] Pocket053  label="CL-ResetBtn-Pocket"
  BaseFeature = -> Pocket057
  Direction = (0,0,-1)
  Length = 5.15
  Length2 = 5
  Profile = -> Sketch082
  ReferenceAxis = -> Sketch082 [N_Axis]
  Refine = true
  Reversed = true
  Suppressed = false
  Type = 0
  expr: Length = VarSet.Top_PcbZ / 2 + VarSet.Cover_ResetHoleHeightH
FEATURE [PartDesign::Pocket] Pocket059  label="CL-Slant-Pocket"
  BaseFeature = -> Pocket053
  Direction = (-1,0,0)
  Length = 20
  Length2 = 5
  Profile = -> Sketch090
  ReferenceAxis = -> Sketch090 [N_Axis]
  Refine = true
  Suppressed = false
  Type = 1
FEATURE [PartDesign::Pocket] Pocket061  label="CL-SlantPCB-Pocket"
  BaseFeature = -> Pocket059
  Direction = (-1,0,0)
  Length = 5
  Length2 = 5
  Profile = -> Sketch092
  ReferenceAxis = -> Sketch092 [N_Axis]
  Refine = true
  Suppressed = false
  Type = 1
FEATURE [Sketcher::SketchObject] Sketch058  label="CL-Screw"
  ArcFitTolerance = 1e-06
  AttachmentOffset = pos=(0,0,0) rot=(1,0,0;3.14159rad)
  AttachmentSupport = -> [Pocket061]
  ExternalGeometry = -> [Pocket061]
  FullyConstrained = true
  MakeInternals = false
  MapMode = 5
  Placement = pos=(0,0,0.75) rot=(0,0,1;0rad)
  expr: Constraints[5] = VarSet.Screw_PostInD
  expr: Constraints[6] = VarSet.Top_MedXY / 2 + VarSet.Top_Frame + VarSet.Top_RearAdd - (9.525 mm + VarSet.Screw_RearAdd)
  sketch-geometry (3):
    g0: Circle CenterX=-11.43 CenterY=88.225 CenterZ=0 NormalX=0 NormalY=0 NormalZ=1 AngleXU=0 Radius=0.95
    g1: Circle CenterX=-26.67 CenterY=88.225 CenterZ=0 NormalX=0 NormalY=0 NormalZ=1 AngleXU=0 Radius=0.95
    g2: GeomPoint X=-19.05 Y=88.225 Z=0
  constraints (7):
    c: Equal(g1,g0)
    c: Symmetric(g1,g0,g2)
    c: DistanceX(g2,g0) = 7.62
    c: DistanceX(g2,g-1) = 19.05
    c: Horizontal(g1,g0)
    c: Diameter(g0) = 1.9
    c: DistanceY(g2,g-3) = 2.875
FEATURE [PartDesign::Pocket] Pocket043  label="CL-Screw-Pocket"
  BaseFeature = -> Pocket061
  Direction = (0,-1e-16,-1)
  Length = 3.25
  Length2 = 5
  Profile = -> Sketch058
  ReferenceAxis = -> Sketch058 [N_Axis]
  Refine = true
  Reversed = true
  Suppressed = false
  Type = 0
  expr: Length = VarSet.Top_PcbZ / 2 + VarSet.Top_LoZ + VarSet.Top_MedZ
FEATURE [PartDesign::Body] Body004  label="CoverLeft"
  AllowCompound = false
  Group = -> [Sketch048,Pad016,Pocket029,Pocket069,Pocket028,Pocket033,Fillet010,Pocket057,Sketch047,Sketch052,Sketch059,Sketch058,Sketch082,Pocket053,Sketch086,Sketch090,Pocket059,Sketch092,Pocket061,Pocket043,Sketch103]
  Origin = -> Origin004
  Tip = -> Pocket043
FEATURE [Sketcher::SketchObject] Sketch104  label="CR-USB"
  ArcFitTolerance = 1e-06
  AttachmentSupport = -> [XY_Plane005]
  FullyConstrained = true
  MakeInternals = false
  MapMode = 5
  expr: Constraints[12] = 3 * 19.05 mm
  expr: Constraints[17] = 2.5 * 19.05 mm + VarSet.Top_PcbY / 2
  expr: Constraints[18] = VarSet.Cover_McuRearAdd
  sketch-geometry (9):
    g0: LineSegment StartX=25.05 StartY=90.2 StartZ=0 EndX=13.05 EndY=90.2 EndZ=0
    g1: LineSegment StartX=13.05 StartY=90.2 StartZ=0 EndX=13.05 EndY=85.875 EndZ=0
    g2: LineSegment StartX=13.05 StartY=85.875 StartZ=0 EndX=25.05 EndY=85.875 EndZ=0
    g3: LineSegment StartX=25.05 StartY=85.875 StartZ=0 EndX=25.05 EndY=90.2 EndZ=0
    g4: GeomPoint [constr] X=19.05 Y=88.0375 Z=0
    g5: GeomPoint X=19.05 Y=19.05 Z=0
    g6: GeomPoint X=38.1 Y=19.05 Z=0
    g7: GeomPoint X=38.1 Y=76.2 Z=0
    g8: GeomPoint X=38.1 Y=85.375 Z=0
  constraints (21):
    c: Coincident(g0,g1)
    c: Coincident(g1,g2)
    c: Coincident(g2,g3)
    c: Coincident(g3,g0)
    c: Horizontal(g0)
    c: Horizontal(g2)
    c: Vertical(g1)
    c: Vertical(g3)
    c: Symmetric(g2,g0,g4)
    c: DistanceX(g0,g0) = 12
    c: Horizontal(g6,g5)
    c: Vertical(g6,g7)
    c: DistanceY(g6,g7) = 57.15
    c: DistanceY(g7,g0) = 14
    c: DistanceY(g-1,g5) = 19.05
    c: Vertical(g4,g5)
    c: Vertical(g8,g7)
    c: DistanceY(g-1,g8) = 85.375
    c: DistanceY(g8,g1) = 0.5
    c: DistanceX(g-1,g5) = 19.05
    c: DistanceX(g5,g6) = 19.05
FEATURE [PartDesign::Pocket] Pocket070  label="CR-USB-Pocket"
  BaseFeature = -> Pocket031
  Direction = (0,0,-1)
  Length = 6.75
  Length2 = 5
  Profile = -> Sketch104
  ReferenceAxis = -> Sketch104 [N_Axis]
  Refine = true
  Reversed = true
  Suppressed = false
  Type = 0
  expr: Length = VarSet.Top_PcbZ / 2 + VarSet.Cover_InZ + VarSet.Cover_McuContactZ
FEATURE [PartDesign::Pocket] Pocket030  label="CR-PCB-Pocket"
  BaseFeature = -> Pocket070
  Direction = (0,0,-1)
  Length = 1.5
  Length2 = 5
  Profile = -> Sketch054
  ReferenceAxis = -> Sketch054 [N_Axis]
  Refine = true
  Reversed = true
  Suppressed = false
  Type = 0
  expr: Length = VarSet.Top_PcbZ
FEATURE [PartDesign::Pocket] Pocket034  label="CR-MCU-Pocket"
  BaseFeature = -> Pocket030
  Direction = (0,0,-1)
  Length = 6.75
  Length2 = 5
  Profile = -> Sketch060
  ReferenceAxis = -> Sketch060 [N_Axis]
  Refine = true
  Reversed = true
  Suppressed = false
  Type = 0
  expr: Length = VarSet.Top_PcbZ / 2 + VarSet.Cover_InZ + VarSet.Cover_McuContactZ
FEATURE [PartDesign::Fillet] Fillet007  label="CR-MCUPin-Fillet"
  Base = -> Pocket034 [Edge371,Edge372,Edge373,Edge374,Edge375,Edge376,Edge377,Edge378,Edge379,Edge380,Edge381,Edge382]
  BaseFeature = -> Pocket034
  Radius = 1
  Refine = true
  SupportTransform = false
  Suppressed = false
  UseAllEdges = false
FEATURE [PartDesign::Pocket] Pocket058  label="CR-MCULED-Pocket"
  BaseFeature = -> Fillet007
  Direction = (0,0,-1)
  Length = 6.75
  Length2 = 5
  Profile = -> Sketch087
  ReferenceAxis = -> Sketch087 [N_Axis]
  Refine = true
  Reversed = true
  Suppressed = false
  Type = 0
  expr: Length = VarSet.Top_PcbZ / 2 + VarSet.Cover_InZ + VarSet.Cover_McuContactZ
FEATURE [PartDesign::Pocket] Pocket055  label="CR-ResetBtn-Pocket"
  BaseFeature = -> Pocket058
  Direction = (0,0,-1)
  Length = 5.15
  Length2 = 5
  Profile = -> Sketch084
  ReferenceAxis = -> Sketch084 [N_Axis]
  Refine = true
  Reversed = true
  Suppressed = false
  Type = 0
  expr: Length = VarSet.Top_PcbZ / 2 + VarSet.Cover_ResetHoleHeightH
FEATURE [PartDesign::Pocket] Pocket060  label="CR-Slant-Pocket"
  BaseFeature = -> Pocket055
  Direction = (-1,0,0)
  Length = 5
  Length2 = 5
  Profile = -> Sketch091
  ReferenceAxis = -> Sketch091 [N_Axis]
  Refine = true
  Reversed = true
  Suppressed = false
  Type = 1
FEATURE [PartDesign::Pocket] Pocket062  label="CR-SlantPCB-Pocket"
  BaseFeature = -> Pocket060
  Direction = (-1,0,0)
  Length = 5
  Length2 = 5
  Profile = -> Sketch093
  ReferenceAxis = -> Sketch093 [N_Axis]
  Refine = true
  Reversed = true
  Suppressed = false
  Type = 1
FEATURE [Sketcher::SketchObject] Sketch067  label="CR-Screw"
  ArcFitTolerance = 1e-06
  AttachmentOffset = pos=(0,0,0) rot=(1,0,0;3.14159rad)
  AttachmentSupport = -> [Pocket062]
  ExternalGeometry = -> [Pocket062]
  FullyConstrained = true
  MakeInternals = false
  MapMode = 5
  Placement = pos=(0,0,0.75) rot=(0,0,1;0rad)
  expr: Constraints[5] = VarSet.Screw_PostInD
  expr: Constraints[6] = VarSet.Top_MedXY / 2 + VarSet.Top_Frame + VarSet.Top_RearAdd - (9.525 mm + VarSet.Screw_RearAdd)
  sketch-geometry (3):
    g0: Circle CenterX=26.67 CenterY=88.225 CenterZ=0 NormalX=0 NormalY=0 NormalZ=1 AngleXU=0 Radius=0.95
    g1: Circle CenterX=11.43 CenterY=88.225 CenterZ=0 NormalX=0 NormalY=0 NormalZ=1 AngleXU=0 Radius=0.95
    g2: GeomPoint X=19.05 Y=88.225 Z=0
  constraints (7):
    c: Equal(g1,g0)
    c: Symmetric(g1,g0,g2)
    c: Horizontal(g1,g0)
    c: DistanceX(g-1,g2) = 19.05
    c: DistanceX(g1,g2) = 7.62
    c: Diameter(g1) = 1.9
    c: DistanceY(g2,g-3) = 2.875
FEATURE [PartDesign::Pocket] Pocket044  label="CR-Screw-Pocket"
  BaseFeature = -> Pocket062
  Direction = (0,-1e-16,-1)
  Length = 3.25
  Length2 = 5
  Profile = -> Sketch067
  ReferenceAxis = -> Sketch067 [N_Axis]
  Refine = true
  Reversed = true
  Suppressed = false
  Type = 0
  expr: Length = VarSet.Top_PcbZ / 2 + VarSet.Top_LoZ + VarSet.Top_MedZ
FEATURE [PartDesign::Body] Body005  label="CoverRight"
  AllowCompound = false
  Group = -> [Sketch053,Pad018,Pocket031,Pocket070,Sketch054,Pocket030,Sketch055,Sketch060,Pocket034,Fillet007,Pocket058,Sketch067,Sketch084,Pocket055,Sketch087,Sketch091,Pocket060,Sketch093,Pocket062,Pocket044,Sketch104]
  Origin = -> Origin005
  Tip = -> Pocket044
